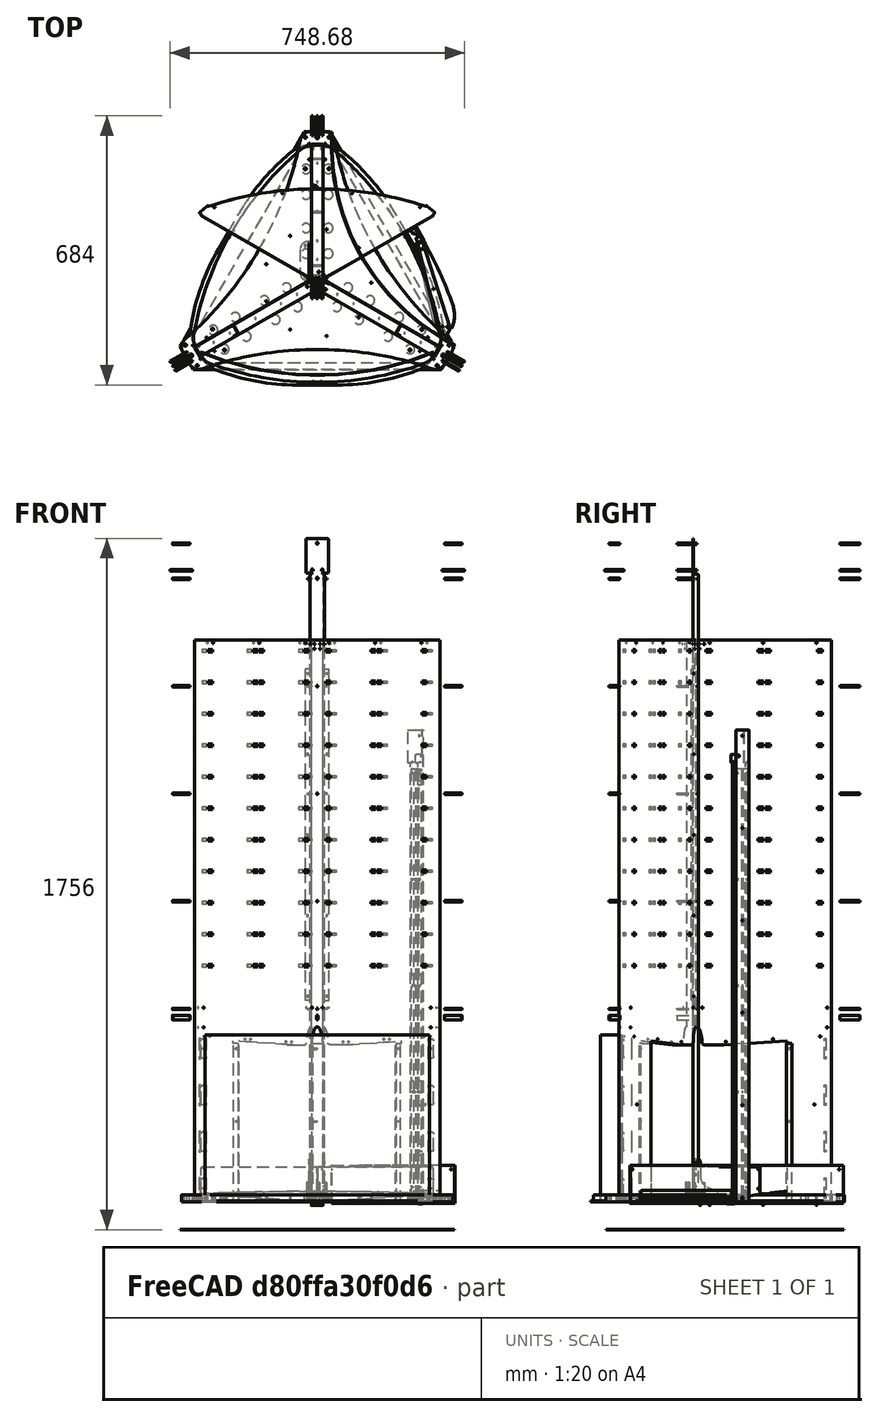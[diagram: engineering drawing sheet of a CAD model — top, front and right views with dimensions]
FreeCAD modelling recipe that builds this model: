
FCSTD DOCUMENT  (FreeCAD 0.22R36596 (Git))
Label: composit_full_size3_door
License: All rights reserved
LicenseURL: http://en.wikipedia.org/wiki/All_rights_reserved
objects: Sketcher::SketchObject×217, Part::FeaturePython×205, PartDesign::SubShapeBinder×115, Part::Compound×106, PartDesign::Pocket×95, PartDesign::Body×85, PartDesign::FeaturePython×60, PartDesign::Boolean×58, PartDesign::CoordinateSystem×49, App::Link×46, PartDesign::Pad×43, Part::Extrusion×41, Part::Mirroring×40, TechDraw::DrawViewDimension×37, App::DocumentObjectGroup×23, PartDesign::Mirrored×23, PartDesign::Hole×18, Part::Cylinder×16, PartDesign::Fillet×12, App::Part×11, +22 more types
note: 1421 computed .brp shape members not serialized (recipe doc carries the construction recipe); baked Part::Feature solids carry a one-line shape summary decoded from their .brp
EXTERNAL_REF file=basin_big.FCStd obj=Spreadsheet
EXTERNAL_REF file=composit-properties.FCStd obj=Spreadsheet
EXTERNAL_REF file=module.FCStd obj=Spreadsheet
EXTERNAL_REF file=module.FCStd obj=Sketch
EXTERNAL_REF file=dropper.FCStd obj=Sketch007
EXTERNAL_REF file=dropper.FCStd obj=Sketch008
EXTERNAL_REF file=dropper.FCStd obj=Connect
EXTERNAL_REF file=hub2108.FCStd obj=Body
EXTERNAL_REF file=U-fix.FCStd obj=Body
EXTERNAL_REF file=ULY-P91-20W.FCStd obj=Sketch001
EXTERNAL_REF file=socket_fixture.FCStd obj=Sketch003
EXTERNAL_REF file=UET-VAS-060A20_12V_IP20.FCStd obj=Sketch001
EXTERNAL_REF file=module.FCStd obj=Body
EXTERNAL_REF file=ULY-P91-20W.FCStd obj=Body
EXTERNAL_REF file=hub2108.FCStd obj=Sketch
EXTERNAL_REF file=hub2108.FCStd obj=Sketch001
EXTERNAL_REF file=U-fix.FCStd obj=Sketch002
EXTERNAL_REF file=hub2108.FCStd obj=Sketch002
EXTERNAL_REF file=hub2108.FCStd obj=Sketch003
EXTERNAL_REF file=ULZ-P02-14W.FCStd obj=Sketch
EXTERNAL_REF file=composit_full_size3_composit_cut.FCStd obj=Link026

FEATURE [Sketcher::SketchObject] Sketch
  FullyConstrained = true
  expr: Constraints[5] = <<Properties>>.endface_width
  expr: Constraints[9] = Spreadsheet.total_length
  sketch-geometry (4):
    g0: LineSegment StartX=-2.7195e-12 StartY=2.3473e-12 StartZ=0 EndX=14.5 EndY=8.37158 EndZ=0
    g1: LineSegment StartX=14.5 StartY=8.37158 StartZ=0 EndX=14.5 EndY=351.872 EndZ=0
    g2: GeomPoint X=-14.5 Y=351.872 Z=0
    g3: LineSegment StartX=14.5 StartY=351.872 StartZ=0 EndX=0 EndY=351.872 EndZ=0
  constraints (14):
    c: Coincident(g-1,g0)
    c: Coincident(g0,g1)
    c: Vertical(g1)
    c: Angle(g0) = 0.523599
    c: Symmetric(g2,g1,g-2)
    c: DistanceX(g2,g1) = 29
    c: Coincident(g3,g1)
    c: PointOnObject(g3,g-2)
    c: Horizontal(g3)
    c: DistanceY(g3) = 351.872
    c: Distance(g0,g1) = 352.17  'max_r'
    c: DistanceX(g1) = 14.5
    c: DistanceY(g1) = 8.37158
    c: Distance(g0) = 16.7432  'connection_offset'
FEATURE [Spreadsheet::Sheet] Spreadsheet  label="Properties"
  cells = B2(total_length)==22.5 mm + module#<<Properties>>.module_width + plane_middle; C2(endface_width)==29 mm; D2(rivet_d)==3.4 mm; E2(total_height)==modules_span + basin_big#<<Properties>>.height + 76 mm; F2(number_of_modules)=11; G2(module_distance_x)==2 mm; H2(modules_span)==<<module>>#<<Properties>>.module_fixture_distance_y * (number_of_modules - 1) + <<module>>#<<Properties>>.module_height; I2(top_offset)==27 mm; J2(plane_middle)==module#<<Properties>>.module_width + 25 mm + petal_offset; K2(inner_width)==endface_width - composit_properties#<<Properties>>.thickness * 2; L2(dropper_distance)==65 mm; M2(plane_width)==22.5 mm + module#<<Properties>>.module_width + plane_middle - petal_offset; N2(petal_offset)==endface_width / 2 / tan(60)
FEATURE [Part::Mirroring] Part__Mirroring  label="Sketch (Mirror #1)"
  Base = (0,0,0)
  Normal = (1,0,0)
  Source = -> Sketch
FEATURE [Part::Compound] Compound
  Links = -> [Part__Mirroring,Sketch]
FEATURE [Sketcher::SketchObject] Sketch001  label="part_main_sketch"
  ExternalGeometry = -> [Sketch]
  FullyConstrained = true
  expr: Constraints[7] = composit_properties#<<Properties>>.thickness
  sketch-geometry (3):
    g0: LineSegment StartX=0 StartY=351.872 StartZ=0 EndX=14.5 EndY=351.872 EndZ=0
    g1: LineSegment StartX=14.5 StartY=351.872 StartZ=0 EndX=14.5 EndY=4.90748 EndZ=0
    g2: LineSegment StartX=14.5 StartY=4.90748 StartZ=0 EndX=29.6554 EndY=-3.84252 EndZ=0
  constraints (9):
    c: PointOnObject(g0,g-2)
    c: Coincident(g0,g-3)
    c: Horizontal(g0)
    c: Coincident(g0,g1)
    c: PointOnObject(g1,g-3)
    c: Coincident(g1,g2)
    c: Angle(g2) = -0.523599
    c: Distance(g-3,g2) = 3
    c: Distance(g2) = 17.5
FEATURE [Part::Mirroring] Part__Mirroring001  label="part_main_sketch (Mirror #2)"
  Base = (0,0,0)
  Normal = (1,0,0)
  Source = -> Sketch001
FEATURE [Part::Compound] Compound001  label="part1_base"
  Links = -> [Part__Mirroring001,Sketch001]
FEATURE [Part::FeaturePython] Array001  label="2part_base"  # Draft array (typed FeaturePython)
  AlwaysSyncPlacement = false
  Angle = 240
  ArrayType = 1
  Axis = (0,0,1)
  Base = -> Compound
  Center = (0,0,0)
  Count = 2
  ExpandArray = false
  Fuse = false
  IntervalAxis = (0,0,0)
  IntervalX = (50,0,0)
  IntervalY = (0,50,0)
  IntervalZ = (0,0,50)
  NumberCircles = 3
  NumberPolar = 2
  NumberX = 2
  NumberY = 2
  NumberZ = 1
  PlacementList = 2 placements: [(0,0,0),(0,0,0)]
  RadialDistance = 50
  ScaleList = (2) [(1,1,1),(1,1,1)]
  Symmetry = 1
  TangentialDistance = 25
FEATURE [PartDesign::SubShapeBinder] Binder
  BindCopyOnChange = 0
  BindMode = 0
  ClaimChildren = true
  Context = -> Body [Binder.]
  Fuse = false
  MakeFace = true
  OffsetFill = false
  OffsetIntersection = false
  OffsetJoinType = 0
  OffsetOpenResult = false
  PartialLoad = false
  Relative = true
  Support = -> [Compound001]
  _Version = 2
  expr: Support = <<part1_base>>._self
FEATURE [PartDesign::SubShapeBinder] Binder001
  BindCopyOnChange = 0
  BindMode = 0
  ClaimChildren = true
  Context = -> Body001 [Binder001.]
  Fuse = false
  MakeFace = true
  OffsetFill = false
  OffsetIntersection = false
  OffsetJoinType = 0
  OffsetOpenResult = false
  PartialLoad = false
  Placement = pos=(0,0,0) rot=(0,0,1;4.18879rad)
  Relative = false
  Support = -> [Array001]
  _Version = 2
  expr: Support = <<2part_base>>._self
FEATURE [PartDesign::FeaturePython] BaseBend  # WARN: FeaturePython — macro-defined, semantics opaque (R4)
  BendSide = 1
  BendSketch = -> Binder
  MidPlane = false
  Reverse = false
  Suppressed = false
  length = 1428
  radius = 0.1
  thickness = 0.3
  expr: length = <<Properties>>.total_height
  expr: radius = composit_properties#<<Properties>>.bend_r
  expr: thickness = composit_properties#<<Properties>>.al_thickness
FEATURE [PartDesign::FeaturePython] BaseBend001  # WARN: FeaturePython — macro-defined, semantics opaque (R4)
  BendSide = 0
  BendSketch = -> Binder001
  MidPlane = false
  Reverse = false
  Suppressed = false
  length = 1428
  radius = 0.1
  thickness = 0.3
  expr: length = <<Properties>>.total_height
  expr: radius = composit_properties#<<Properties>>.bend_r
  expr: thickness = composit_properties#<<Properties>>.al_thickness
FEATURE [App::Link] Link  label="module_holes"
  LinkedObject = -> <external module.FCStd>#Sketch
  expr: LinkedObject = module#<<module_holes>>._self
FEATURE [Part::FeaturePython] LinearArray  # WARN: FeaturePython — macro-defined, semantics opaque (R4)
  Alignment = 0
  CellStart = A1
  Count = 11
  Dir = (0,-1,0)
  DirIsDriven = true
  DistributionLaw = 0
  DrivenProperty = 1
  EndInclusive = true
  ExposePlacement = false
  GeneratorMode = 1
  MarkerShape = 1
  MarkerSize = 0
  NumElements = 11
  OrientMode = 0
  Point = (0,0,0)
  PointIsDriven = true
  Reverse = false
  SpanEnd = 800
  SpanStart = 0
  Step = 80
  Type = lattice2LinearArray.LinearArray
  VSGVersion = 1
  Values = 0.0 | 80.0 | 160.0 | 240.0 | 320.0 | 400.0 | 480.0 | 560.0 | 640.0 | 720.0 | 800.0
  ValuesSource = 2
  isLattice = 1
  expr: Count = <<Properties>>.number_of_modules
  expr: SpanEnd = Step * (Count - 1)
  expr: Step = <<module>>#<<Properties>>.module_fixture_distance_y
FEATURE [Part::FeaturePython] LinearArray001  # WARN: FeaturePython — macro-defined, semantics opaque (R4)
  Alignment = 0
  CellStart = A1
  Count = 2
  Dir = (1,0,0)
  DirIsDriven = true
  DistributionLaw = 0
  DrivenProperty = 1
  EndInclusive = true
  ExposePlacement = false
  GeneratorMode = 1
  MarkerShape = 1
  MarkerSize = 0
  NumElements = 2
  OrientMode = 1
  Placement = pos=(-75,0,0) rot=(0,0,1;0rad)
  Point = (0,0,0)
  PointIsDriven = true
  Reverse = false
  SpanEnd = 150
  SpanStart = 0
  Step = 150
  Type = lattice2LinearArray.LinearArray
  VSGVersion = 1
  Values = 0.0 | 150.0
  ValuesSource = 2
  isLattice = 1
  expr: .Placement.Base.x = -SpanEnd / 2
  expr: SpanEnd = Step * (Count - 1)
  expr: Step = <<module>>#<<Properties>>.module_width + <<Properties>>.module_distance_x
FEATURE [Part::FeaturePython] Populate  label="Populate LinearArray with LinearArray001"  # WARN: FeaturePython — macro-defined, semantics opaque (R4)
  Copying = 0
  ExposePlacement = false
  MarkerShape = 1
  MarkerSize = 0
  NumElements = 22
  Object = -> LinearArray001
  OutputCompounding = 0
  PlacementsTo = -> LinearArray
  Referencing = 0
  Type = lattice2PopulateCopies.LatticePopulateCopies
  isLattice = 1
FEATURE [Part::FeaturePython] Populate001  label="Populate Populate LinearArray with LinearArray001 with module_holes"  # WARN: FeaturePython — macro-defined, semantics opaque (R4)
  Copying = 0
  ExposePlacement = false
  MarkerShape = 1
  MarkerSize = 0
  NumElements = 0
  Object = -> Link
  OutputCompounding = 1
  PlacementsTo = -> Populate
  Referencing = 0
  Type = lattice2PopulateCopies.LatticePopulateCopies
  isLattice = 0
FEATURE [Part::Extrusion] Extrude  label="modules_holes"
  Base = -> Populate001
  Dir = (0,0,1)
  DirMode = 2
  FaceMakerClass = Part::FaceMakerBullseye
  LengthFwd = 31
  LengthRev = 0
  Placement = pos=(0,181.372,1401) rot=(0.57735,0.57735,0.57735;2.0944rad)
  Solid = true
  Symmetric = true
  expr: .Placement.Base.y = <<Properties>>.plane_middle
  expr: .Placement.Base.z = <<Properties>>.total_height - <<Properties>>.top_offset
  expr: LengthFwd = <<Properties>>.endface_width + 2 mm
FEATURE [Sketcher::SketchObject] Sketch003  label="basin_cut_sketch"
  ExternalGeometry = -> [Sketch]
  FullyConstrained = true
  Placement = pos=(0,0,0) rot=(0.57735,0.57735,0.57735;2.0944rad)
  expr: Constraints[27] = <<sink_bend_line>>.FaceAngle
  sketch-geometry (12):
    g0: LineSegment StartX=0 StartY=0 StartZ=0 EndX=238.372 EndY=0 EndZ=0
    g1: LineSegment StartX=238.372 StartY=0 StartZ=0 EndX=238.372 EndY=409.023 EndZ=0
    g2: LineSegment StartX=79.3716 StartY=400 StartZ=0 EndX=28.4155 EndY=400 EndZ=0
    g3: ArcOfCircle CenterX=28.4155 CenterY=405 CenterZ=0 NormalX=0 NormalY=0 NormalZ=1 AngleXU=0 Radius=5 StartAngle=3.17548 EndAngle=4.71239
    g4: ArcOfEllipse CenterX=9.37158 CenterY=400 CenterZ=0 NormalX=0 NormalY=0 NormalZ=1 MajorRadius=45 MinorRadius=14.1284 AngleXU=-1.5708 StartAngle=1.67835 EndAngle=3.14159
    g5: LineSegment StartX=9.37158 StartY=355 StartZ=0 EndX=9.37158 EndY=445 EndZ=0
    g6: LineSegment StartX=23.5 StartY=400 StartZ=0 EndX=-4.75684 EndY=400 EndZ=0
    g7: GeomPoint X=9.37158 Y=357.275 Z=0
    g8: GeomPoint X=9.37158 Y=442.725 Z=0
    g9: LineSegment StartX=0 StartY=0 StartZ=0 EndX=0 EndY=445 EndZ=0
    g10: LineSegment StartX=0 StartY=445 StartZ=0 EndX=9.37158 EndY=445 EndZ=0
    g11: LineSegment StartX=79.3716 StartY=400 StartZ=0 EndX=238.372 EndY=409.023 EndZ=0
  constraints (25):
    c: Coincident(g-1,g0)
    c: Horizontal(g0)
    c: Coincident(g0,g1)
    c: Vertical(g1)
    c: Horizontal(g2)
    c: Tangent(g3,g2) = 1.5708
    c: InternalAlignment(g5-g8 -> g4) x4
    c: Horizontal(g6)
    c: Tangent(g4,g3) = 1.5708
    c: Coincident(g9,g0)
    c: Coincident(g9,g10)
    c: Vertical(g9)
    c: Horizontal(g10)
    c: Tangent(g10,g4) = 1.5708
    c: DistanceX(g-3,g0) = 230
    c: DistanceY(g2) = 400
    c: DistanceY(g9) = 445
    c: DistanceX(g-3,g4) = 1
    c: Radius(g3) = 5
    c: DistanceX(g6) = 23.5
    c: PointOnObject(g4,g2)
    c: DistanceX(g-3,g2) = 71
    c: Coincident(g11,g2)
    c: Coincident(g11,g1)
    c: Angle(g11) = 0.0566865
FEATURE [Part::Extrusion] Extrude001  label="basin_cut"
  Base = -> Sketch003
  Dir = (1,0,0)
  DirMode = 2
  FaceMakerClass = Part::FaceMakerBullseye
  LengthFwd = 30
  LengthRev = 0
  Solid = true
  Symmetric = true
FEATURE [Sketcher::SketchObject] Sketch004  label="leg_amplifier_base_sketch"
  ExternalGeometry = -> [Sketch003]
  FullyConstrained = true
  expr: Constraints[5] = <<Properties>>.endface_width / 2
  expr: Constraints[6] = composit_properties#<<Properties>>.bend_r + composit_properties#<<Properties>>.al_thickness
  expr: Constraints[7] = <<Properties>>.endface_width - composit_properties#<<Properties>>.thickness
  sketch-geometry (3):
    g0: LineSegment StartX=-11.5 StartY=-0.4 StartZ=0 EndX=14.5 EndY=-0.4 EndZ=0
    g1: LineSegment StartX=-11.5 StartY=-0.4 StartZ=0 EndX=-11.5 EndY=13 EndZ=0
    g2: LineSegment StartX=14.5 StartY=-0.4 StartZ=0 EndX=14.5 EndY=13 EndZ=0
  constraints (10):
    c: Horizontal(g0)
    c: Coincident(g1,g0)
    c: Vertical(g1)
    c: Coincident(g2,g0)
    c: Vertical(g2)
    c: DistanceX(g0) = 14.5
    c: DistanceY(g0,g-3) = 0.4
    c: DistanceX(g0,g0) = 26
    c: Horizontal(g1,g2)
    c: DistanceY(g-3,g2) = 13
FEATURE [Part::Mirroring] Part__Mirroring002  label="Sketch004 (Mirror #3)"
  Base = (0,0,0)
  Normal = (1,0,0)
  Source = -> Sketch004
FEATURE [Spreadsheet::Sheet] Spreadsheet001  label="Properties001"
  cells = B2(plane_width)==27.5 mm + module#<<Properties>>.module_width * 2 + 20 mm; C2(endface_width)==29 mm; D2(rivet_d)==3.4 mm; E2(total_height)==modules_span + basin_big#<<Properties>>.height; F2(number_of_modules)=11; G2(module_distance_x)==2 mm; H2(modules_span)==<<module>>#<<Properties>>.module_fixture_distance_y * number_of_modules + <<module>>#<<Properties>>.module_height; I2(top_offset)==30.5 mm; J2(plane_middle)==module#<<Properties>>.module_width + 25 mm; K2(inner_width)==endface_width - composit_properties#<<Properties>>.thickness * 2; L2(dropper_distance)==65 mm
FEATURE [Sketcher::SketchObject] Sketch005
  FullyConstrained = true
  expr: Constraints[5] = <<Properties001>>.endface_width
  expr: Constraints[6] = <<Properties001>>.plane_width
  sketch-geometry (4):
    g0: LineSegment StartX=5.67e-14 StartY=-9.82e-14 StartZ=0 EndX=14.5 EndY=8.37158 EndZ=0
    g1: LineSegment StartX=14.5 StartY=8.37158 StartZ=0 EndX=14.5 EndY=351.872 EndZ=0
    g2: GeomPoint X=-14.5 Y=351.872 Z=0
    g3: LineSegment StartX=14.5 StartY=351.872 StartZ=0 EndX=0 EndY=351.872 EndZ=0
  constraints (10):
    c: Coincident(g-1,g0)
    c: Coincident(g0,g1)
    c: Vertical(g1)
    c: Angle(g0) = 0.523599
    c: Symmetric(g2,g1,g-2)
    c: DistanceX(g2,g1) = 29
    c: DistanceY(g1,g1) = 343.5
    c: Coincident(g3,g1)
    c: PointOnObject(g3,g-2)
    c: Horizontal(g3)
FEATURE [Sketcher::SketchObject] Sketch006
  ExternalGeometry = -> [Sketch005]
  FullyConstrained = true
  Placement = pos=(0,0,0) rot=(0.57735,0.57735,0.57735;2.0944rad)
  sketch-geometry (12):
    g0: LineSegment StartX=0 StartY=0 StartZ=0 EndX=238.372 EndY=0 EndZ=0
    g1: LineSegment StartX=238.372 StartY=0 StartZ=0 EndX=238.372 EndY=410 EndZ=0
    g2: LineSegment StartX=238.372 StartY=410 StartZ=0 EndX=79.3716 EndY=400 EndZ=0
    g3: LineSegment StartX=79.3716 StartY=400 StartZ=0 EndX=19.9656 EndY=400 EndZ=0
    g4: ArcOfCircle CenterX=19.9656 CenterY=405 CenterZ=0 NormalX=0 NormalY=0 NormalZ=1 AngleXU=0 Radius=5 StartAngle=3.15538 EndAngle=4.71239
    g5: ArcOfEllipse CenterX=9.37158 CenterY=400 CenterZ=0 NormalX=0 NormalY=0 NormalZ=1 MajorRadius=45 MinorRadius=5.62842 AngleXU=-1.5708 StartAngle=1.6806 EndAngle=3.14159
    g6: LineSegment StartX=9.37158 StartY=355 StartZ=0 EndX=9.37158 EndY=445 EndZ=0
    g7: LineSegment StartX=15 StartY=400 StartZ=0 EndX=3.74316 EndY=400 EndZ=0
    g8: GeomPoint X=9.37158 Y=355.353 Z=0
    g9: GeomPoint X=9.37158 Y=444.647 Z=0
    g10: LineSegment StartX=0 StartY=0 StartZ=0 EndX=0 EndY=445 EndZ=0
    g11: LineSegment StartX=0 StartY=445 StartZ=0 EndX=9.37158 EndY=445 EndZ=0
  constraints (25):
    c: Coincident(g-1,g0)
    c: Horizontal(g0)
    c: Coincident(g0,g1)
    c: Vertical(g1)
    c: Coincident(g1,g2)
    c: Coincident(g2,g3)
    c: Horizontal(g3)
    c: Tangent(g4,g3) = 1.5708
    c: InternalAlignment(g6-g9 -> g5) x4
    c: Horizontal(g7)
    c: Tangent(g5,g4) = 1.5708
    c: Coincident(g10,g0)
    c: Coincident(g10,g11)
    c: Vertical(g10)
    c: Horizontal(g11)
    c: Tangent(g11,g5) = 1.5708
    c: DistanceX(g-3,g0) = 230
    c: DistanceY(g2) = 400
    c: DistanceY(g10) = 445
    c: DistanceX(g-3,g5) = 1
    c: Radius(g4) = 5
    c: DistanceX(g7) = 15
    c: PointOnObject(g5,g3)
    c: DistanceY(g1) = 410
    c: DistanceX(g-3,g2) = 71
FEATURE [Sketcher::SketchObject] Sketch007
  ExternalGeometry = -> [Sketch006]
  FullyConstrained = true
  expr: Constraints[5] = <<Properties001>>.endface_width / 2
  expr: Constraints[6] = composit_properties#<<Properties>>.bend_r + composit_properties#<<Properties>>.al_thickness
  expr: Constraints[7] = <<Properties001>>.endface_width - composit_properties#<<Properties>>.thickness
  sketch-geometry (3):
    g0: LineSegment StartX=-11.5 StartY=237.972 StartZ=0 EndX=14.5 EndY=237.972 EndZ=0
    g1: LineSegment StartX=-11.5 StartY=237.972 StartZ=0 EndX=-11.5 EndY=258.372 EndZ=0
    g2: LineSegment StartX=14.5 StartY=237.972 StartZ=0 EndX=14.5 EndY=258.372 EndZ=0
  constraints (10):
    c: Horizontal(g0)
    c: Coincident(g1,g0)
    c: Vertical(g1)
    c: Coincident(g2,g0)
    c: Vertical(g2)
    c: DistanceX(g0) = 14.5
    c: DistanceY(g0,g-3) = 0.4
    c: DistanceX(g0,g0) = 26
    c: Horizontal(g1,g2)
    c: DistanceY(g-3,g2) = 20
FEATURE [Part::FeaturePython] BaseBend003  label="BaseBend002_material_0.30ansi002"  # WARN: FeaturePython — macro-defined, semantics opaque (R4)
  BendSide = 0
  BendSketch = -> Part__Mirroring002
  MidPlane = false
  Reverse = false
  length = 403.5
  radius = 0.1
  thickness = 0.3
  expr: length = <<leg_amplifier>>.length
  expr: radius = composit_properties#<<Properties>>.bend_r
  expr: thickness = composit_properties#<<Properties>>.al_thickness
FEATURE [App::LinkGroup] CopyOnChangeGroup
  ElementList = -> [BaseBend003,Sketch007,Sketch006,Sketch005,Spreadsheet001]
  LinkMode = 1
FEATURE [App::Link] Link002  label="leg_amplifier_link"
  BendSketch = -> Part__Mirroring002
  LinkCopyOnChange = 2
  LinkCopyOnChangeGroup = -> CopyOnChangeGroup
  LinkCopyOnChangeSource = -> BaseBend002
  LinkCopyOnChangeTouched = true
  LinkPlacement = pos=(206.436,-119.186,0) rot=(0,0,1;4.18879rad)
  LinkedObject = -> BaseBend003
  Placement = pos=(206.436,-119.186,0) rot=(0,0,1;4.18879rad)
  expr: .LinkPlacement.Base.x = (<<Properties>>.petal_offset + 230 mm) * cos(-30)
  expr: .LinkPlacement.Base.y = (<<Properties>>.petal_offset + 230 mm) * sin(-30)
FEATURE [Part::Compound] Compound008
  Links = -> [Sketch004]
FEATURE [Part::FeaturePython] BaseBend002  label="leg_amplifier"  # WARN: FeaturePython — macro-defined, semantics opaque (R4)
  BendSide = 1
  BendSketch = -> Compound008
  MidPlane = false
  Placement = pos=(0,238.372,0) rot=(0,0,1;0rad)
  Reverse = false
  length = 403.5
  radius = 0.1
  thickness = 0.3
  expr: .Placement.Base.y = <<Properties>>.petal_offset + 230 mm
  expr: radius = composit_properties#<<Properties>>.bend_r
  expr: thickness = composit_properties#<<Properties>>.al_thickness
FEATURE [Part::Compound] Compound006  label="mirror_compound"
  Links = -> [BaseBend002]
  Placement = pos=(0,0,0) rot=(0,0,1;2.0944rad)
FEATURE [Part::Compound] Compound007  label="part2_fuse1"
  Links = -> [Link002,Compound006]
  expr: Links = list(<<leg_amplifier_link>>._self; <<mirror_compound>>._self)
FEATURE [App::DocumentObjectGroup] Group006  label="composit_cut"
FEATURE [App::DocumentObjectGroup] Group007  label="PP_cut"
FEATURE [App::DocumentObjectGroup] Group008  label="plywood_cut"
FEATURE [App::DocumentObjectGroup] Group002  label="cut"
  Group = -> [Group006,Group007,Group008]
FEATURE [Sketcher::SketchObject] Sketch008  label="pillar_base_sketch"
  FullyConstrained = true
  sketch-geometry (5):
    g0: LineSegment StartX=-18.3 StartY=19 StartZ=0 EndX=-18.3 EndY=-4.62e-14 EndZ=0
    g1: LineSegment StartX=-18.3 StartY=-4.62e-14 StartZ=0 EndX=18.3 EndY=-4.62e-14 EndZ=0
    g2: LineSegment StartX=18.3 StartY=-4.62e-14 StartZ=0 EndX=18.3 EndY=19 EndZ=0
    g3: LineSegment StartX=18.3 StartY=19 StartZ=0 EndX=-18.3 EndY=19 EndZ=0
    g4: GeomPoint X=8.6e-15 Y=9.5 Z=0
  constraints (13):
    c: Coincident(g0,g1)
    c: Coincident(g1,g2)
    c: Coincident(g2,g3)
    c: Coincident(g3,g0)
    c: Horizontal(g1)
    c: Horizontal(g3)
    c: Vertical(g0)
    c: Vertical(g2)
    c: Symmetric(g1,g0,g4)
    c: PointOnObject(g4,g-2)
    c: PointOnObject(g1,g-1)
    c: DistanceX(g1,g1) = 36.6  'width'
    c: DistanceY(g2,g2) = 19  'length'
FEATURE [PartDesign::SubShapeBinder] Binder002
  BindCopyOnChange = 0
  BindMode = 0
  ClaimChildren = true
  Fuse = false
  MakeFace = true
  OffsetFill = false
  OffsetIntersection = false
  OffsetJoinType = 0
  OffsetOpenResult = false
  PartialLoad = false
  Relative = false
  Support = -> [Sketch008]
  _Version = 2
FEATURE [PartDesign::FeaturePython] BaseBend004  label="pillar_BaseBend"  # WARN: FeaturePython — macro-defined, semantics opaque (R4)
  BendSide = 1
  BendSketch = -> Binder002
  MidPlane = false
  Reverse = false
  Suppressed = false
  length = 1594
  radius = 2
  thickness = 2
FEATURE [Sketcher::SketchObject] Sketch009
  AttachmentOffset = pos=(0,1594,0) rot=(0,0,1;0rad)
  AttachmentSupport = -> [XZ_Plane014]
  FullyConstrained = true
  MapMode = 5
  Placement = pos=(0,3.539e-13,1594) rot=(1,0,0;1.5708rad)
  expr: .AttachmentOffset.Base.y = BaseBend004.length
  expr: Constraints[15] = <<pillar_base_sketch>>.Constraints.width - (<<pillar_BaseBend>>.thickness + <<pillar_BaseBend>>.radius) * 2
  sketch-geometry (16):
    g0: LineSegment StartX=-14.3 StartY=0 StartZ=0 EndX=14.3 EndY=0 EndZ=0
    g1: LineSegment StartX=14.3 StartY=0 StartZ=0 EndX=14.3 EndY=2 EndZ=0
    g2: LineSegment StartX=14.3 StartY=2 StartZ=0 EndX=34.5 EndY=2 EndZ=0
    g3: LineSegment StartX=37.5 StartY=5 StartZ=0 EndX=37.5 EndY=87 EndZ=0
    g4: LineSegment StartX=34.5 StartY=90 StartZ=0 EndX=-34.5 EndY=90 EndZ=0
    g5: LineSegment StartX=-37.5 StartY=87 StartZ=0 EndX=-37.5 EndY=5 EndZ=0
    g6: LineSegment StartX=-34.5 StartY=2 StartZ=0 EndX=-14.3 EndY=2 EndZ=0
    g7: LineSegment StartX=-14.3 StartY=2 StartZ=0 EndX=-14.3 EndY=0 EndZ=0
    g8: ArcOfCircle CenterX=34.5 CenterY=5 CenterZ=0 NormalX=0 NormalY=0 NormalZ=1 AngleXU=0 Radius=3 StartAngle=4.71239 EndAngle=6.28319
    g9: GeomPoint X=37.5 Y=2 Z=0
    g10: ArcOfCircle CenterX=34.5 CenterY=87 CenterZ=0 NormalX=0 NormalY=0 NormalZ=1 AngleXU=0 Radius=3 StartAngle=1.02861e-11 EndAngle=1.5708
    g11: GeomPoint X=37.5 Y=90 Z=0
    g12: ArcOfCircle CenterX=-34.5 CenterY=87 CenterZ=0 NormalX=0 NormalY=0 NormalZ=1 AngleXU=0 Radius=3 StartAngle=1.5708 EndAngle=3.14159
    g13: GeomPoint X=-37.5 Y=90 Z=0
    g14: ArcOfCircle CenterX=-34.5 CenterY=5 CenterZ=0 NormalX=0 NormalY=0 NormalZ=1 AngleXU=0 Radius=3 StartAngle=3.14159 EndAngle=4.71239
    g15: GeomPoint X=-37.5 Y=2 Z=0
  constraints (38):
    c: PointOnObject(g0,g-1)
    c: Coincident(g0,g1)
    c: Vertical(g1)
    c: Coincident(g1,g2)
    c: Horizontal(g2)
    c: Vertical(g3)
    c: Vertical(g5)
    c: Horizontal(g6)
    c: Coincident(g6,g7)
    c: Vertical(g7)
    c: Coincident(g0,g7)
    c: Horizontal(g0)
    c: Symmetric(g6,g1,g-2)
    c: Symmetric(g11,g13,g-2)
    c: DistanceY(g1,g1) = 2
    c: DistanceX(g0,g0) = 28.6
    c: PointOnObject(g9,g2)
    c: PointOnObject(g9,g3)
    c: Tangent(g2,g8) = -1.5708
    c: Tangent(g3,g8) = -1.5708
    c: PointOnObject(g11,g3)
    c: PointOnObject(g11,g4)
    c: Tangent(g3,g10) = -1.5708
    c: Tangent(g4,g10) = -1.5708
    c: PointOnObject(g13,g4)
    c: PointOnObject(g13,g5)
    c: Tangent(g4,g12) = -1.5708
    c: Tangent(g5,g12) = -1.5708
    c: PointOnObject(g15,g5)
    c: PointOnObject(g15,g6)
    c: Tangent(g5,g14) = -1.5708
    c: Tangent(g6,g14) = -1.5708
    c: Equal(g14,g8)
    c: Equal(g14,g10)
    c: Equal(g14,g12)
    c: Radius(g14) = 3
    c: DistanceX(g13,g11) = 75
    c: DistanceY(g9,g11) = 88
FEATURE [Sketcher::SketchObject] Sketch010  label="pillar_bottom_BaseSketch"
  AttachmentSupport = -> [YZ_Plane015]
  FullyConstrained = true
  MapMode = 5
  Placement = pos=(0,0,0) rot=(0.57735,0.57735,0.57735;2.0944rad)
  sketch-geometry (2):
    g0: LineSegment StartX=-25 StartY=0 StartZ=0 EndX=0 EndY=0 EndZ=0
    g1: LineSegment StartX=0 StartY=0 StartZ=0 EndX=0 EndY=110 EndZ=0
  constraints (6):
    c: PointOnObject(g0,g-1)
    c: Coincident(g0,g-1)
    c: Coincident(g0,g1)
    c: PointOnObject(g1,g-2)
    c: DistanceX(g0,g0) = 25  'leg_length'
    c: DistanceY(g1) = 110  'height'
FEATURE [PartDesign::FeaturePython] BaseBend005  label="pillar_bottom_BaseBend"  # WARN: FeaturePython — macro-defined, semantics opaque (R4)
  BendSide = 0
  BendSketch = -> Sketch010
  MidPlane = true
  Reverse = true
  Suppressed = false
  length = 101
  radius = 2
  thickness = 2
FEATURE [Sketcher::SketchObject] Sketch011  label="pillar_bottom_cut_vert"
  AttachmentSupport = -> [XZ_Plane015]
  FullyConstrained = true
  MapMode = 5
  Placement = pos=(0,0,0) rot=(1,0,0;1.5708rad)
  expr: Constraints[15] = <<pillar_bottom_BaseBend>>.length
  expr: Constraints[16] = <<pillar_bottom_BaseBend>>.radius + <<pillar_bottom_BaseBend>>.thickness
  expr: Constraints[27] = <<pillar_base_sketch>>.Constraints.length - 4 mm
  sketch-geometry (15):
    g0: LineSegment StartX=-50.5 StartY=0 StartZ=0 EndX=-50.5 EndY=75 EndZ=0
    g1: LineSegment StartX=-45.5 StartY=80 StartZ=0 EndX=-40.5 EndY=80 EndZ=0
    g2: LineSegment StartX=50.5 StartY=4 StartZ=0 EndX=50.5 EndY=0 EndZ=0
    g3: LineSegment StartX=50.5 StartY=0 StartZ=0 EndX=-50.5 EndY=0 EndZ=0
    g4: ArcOfCircle CenterX=-45.5 CenterY=75 CenterZ=0 NormalX=0 NormalY=0 NormalZ=1 AngleXU=0 Radius=5 StartAngle=1.5708 EndAngle=3.14159
    g5: GeomPoint X=-50.5 Y=80 Z=0
    g6: ArcOfCircle CenterX=-40.5 CenterY=75 CenterZ=0 NormalX=0 NormalY=0 NormalZ=1 AngleXU=0 Radius=5 StartAngle=0 EndAngle=1.5708
    g7: GeomPoint X=-35.5 Y=80 Z=0
    g8: ArcOfCircle CenterX=45.5 CenterY=4 CenterZ=0 NormalX=0 NormalY=0 NormalZ=1 AngleXU=0 Radius=5 StartAngle=0 EndAngle=1.13485
    g9: GeomPoint X=50.5 Y=7.18672 Z=0
    g10: LineSegment StartX=-35.5 StartY=75 StartZ=0 EndX=-35.5 EndY=64.709 EndZ=0
    g11: LineSegment StartX=-19.6724 StartY=39.8753 StartZ=0 EndX=47.6113 EndY=8.53236 EndZ=0
    g12: ArcOfCircle CenterX=-8.10401 CenterY=64.709 CenterZ=0 NormalX=0 NormalY=0 NormalZ=1 AngleXU=0 Radius=27.396 StartAngle=3.14159 EndAngle=4.27645
    g13: GeomPoint X=-19.6724 Y=39.8753 Z=0
    g14: GeomPoint X=-13.5 Y=37 Z=0
  constraints (34):
    c: PointOnObject(g0,g-1)
    c: Vertical(g0)
    c: Horizontal(g1)
    c: Vertical(g2)
    c: Coincident(g2,g3)
    c: Coincident(g3,g0)
    c: PointOnObject(g5,g0)
    c: PointOnObject(g5,g1)
    c: Tangent(g0,g4) = 1.5708
    c: Tangent(g1,g4) = 1.5708
    c: PointOnObject(g7,g1)
    c: Tangent(g1,g6) = 1.5708
    c: PointOnObject(g9,g2)
    c: Tangent(g2,g8) = 1.5708
    c: Symmetric(g0,g2,g-2)
    c: DistanceX(g3,g3) = 101
    c: DistanceY(g2) = 4
    c: DistanceY(g5) = 80  'height'
    c: Radius(g4) = 5
    c: Radius(g8) = 5
    c: Equal(g4,g6)
    c: PointOnObject(g7,g10)
    c: PointOnObject(g9,g11)
    c: Vertical(g10)
    c: Tangent(g10,g6) = 1.5708
    c: Tangent(g12,g10) = -1.5708
    c: Tangent(g12,g11) = -1.5708
    c: DistanceX(g5,g7) = 15
    c: Tangent(g11,g8) = 1.5708
    c: Coincident(g11,g13)
    c: PointOnObject(g14,g11)
    c: DistanceY(g14) = 37
    c: DistanceX(g0,g14) = 37
    c: DistanceX(g11) = -19.6724
FEATURE [Sketcher::SketchObject] Sketch012
  AttachmentSupport = -> [XY_Plane015]
  FullyConstrained = true
  MapMode = 5
  expr: Constraints[18] = <<pillar_bottom_BaseSketch>>.Constraints.leg_length
  expr: Constraints[20] = <<pillar_bottom_BaseBend>>.radius + <<pillar_bottom_BaseBend>>.thickness
  expr: Constraints[9] = <<pillar_bottom_BaseBend>>.length
  sketch-geometry (9):
    g0: LineSegment StartX=-50.5 StartY=-4 StartZ=0 EndX=-50.5 EndY=0 EndZ=0
    g1: LineSegment StartX=-50.5 StartY=0 StartZ=0 EndX=50.5 EndY=0 EndZ=0
    g2: LineSegment StartX=50.5 StartY=0 StartZ=0 EndX=50.5 EndY=-4 EndZ=0
    g3: LineSegment StartX=29.5 StartY=-25 StartZ=0 EndX=-29.5 EndY=-25 EndZ=0
    g4: GeomPoint X=0 Y=-12.5 Z=0
    g5: ArcOfCircle CenterX=29.5 CenterY=-4 CenterZ=0 NormalX=0 NormalY=0 NormalZ=1 AngleXU=0 Radius=21 StartAngle=4.71239 EndAngle=6.28319
    g6: GeomPoint X=50.5 Y=-25 Z=0
    g7: ArcOfCircle CenterX=-29.5 CenterY=-4 CenterZ=0 NormalX=0 NormalY=0 NormalZ=1 AngleXU=0 Radius=21 StartAngle=3.14159 EndAngle=4.71239
    g8: GeomPoint X=-50.5 Y=-25 Z=0
  constraints (21):
    c: Coincident(g0,g1)
    c: Coincident(g1,g2)
    c: Horizontal(g1)
    c: Horizontal(g3)
    c: Vertical(g0)
    c: Vertical(g2)
    c: Symmetric(g1,g8,g4)
    c: PointOnObject(g4,g-2)
    c: PointOnObject(g1,g-1)
    c: DistanceX(g1,g1) = 101
    c: PointOnObject(g6,g2)
    c: PointOnObject(g6,g3)
    c: Tangent(g2,g5) = 1.5708
    c: Tangent(g3,g5) = 1.5708
    c: PointOnObject(g8,g0)
    c: PointOnObject(g8,g3)
    c: Tangent(g0,g7) = 1.5708
    c: Tangent(g3,g7) = 1.5708
    c: DistanceY(g6,g-1) = 25
    c: Equal(g7,g5)
    c: DistanceY(g2,g-1) = 4
FEATURE [Part::FeaturePython] WireFilter  # WARN: FeaturePython — macro-defined, semantics opaque (R4)
  AttacherType = Attacher::AttachEngine3D
  ClaimChildren = true
  ColorKeyCount = 8
  Colorize = true
  FaceMaker = 5
  FixNormal = false
  FollowSource = true
  InvertedFaceScale = 20
  MaxWires = 25
  Normal = (0,1,-2e-16)
  OffsetFill = false
  OffsetIntersection = false
  OffsetJoin = 0
  OffsetOpenResult = false
  Scale = (1,1,1)
  SelectEdges = false
  Source = -> Sketch011
  UniformScale = 1
  UseDefault = false
  UseSelected = true
  UseSelectedEdges = false
  Version = 0.2022.02.09
  WireOrder = [1]
FEATURE [Part::FeaturePython] WireFilter001  # WARN: FeaturePython — macro-defined, semantics opaque (R4)
  AttacherType = Attacher::AttachEngine3D
  ClaimChildren = true
  ColorKeyCount = 8
  Colorize = true
  FaceMaker = 5
  FixNormal = false
  FollowSource = true
  InvertedFaceScale = 5
  MaxWires = 25
  Normal = (0,0,1)
  OffsetFill = false
  OffsetIntersection = false
  OffsetJoin = 0
  OffsetOpenResult = false
  Scale = (1,1,1)
  SelectEdges = false
  Source = -> Sketch012
  UniformScale = 1
  UseDefault = false
  UseSelected = true
  UseSelectedEdges = false
  Version = 0.2022.02.09
  WireOrder = [1]
FEATURE [PartDesign::Pocket] Pocket
  BaseFeature = -> BaseBend005
  Direction = (0,-1,2e-16)
  Length = 5
  Length2 = 5
  Profile = -> WireFilter
  Suppressed = false
  Type = 1
FEATURE [PartDesign::Pocket] Pocket001
  BaseFeature = -> Pocket
  Direction = (0,0,-1)
  Length = 5
  Length2 = 5
  Profile = -> WireFilter001
  Reversed = true
  Suppressed = false
  Type = 1
FEATURE [Sketcher::SketchObject] Sketch013
  AttachmentSupport = -> [XY_Plane016]
  FullyConstrained = true
  MapMode = 5
  sketch-geometry (5):
    g0: LineSegment StartX=-36 StartY=25 StartZ=0 EndX=-36 EndY=0 EndZ=0
    g1: LineSegment StartX=-36 StartY=0 StartZ=0 EndX=36 EndY=0 EndZ=0
    g2: LineSegment StartX=36 StartY=0 StartZ=0 EndX=36 EndY=25 EndZ=0
    g3: LineSegment StartX=36 StartY=25 StartZ=0 EndX=-36 EndY=25 EndZ=0
    g4: GeomPoint X=0 Y=12.5 Z=0
  constraints (13):
    c: Coincident(g0,g1)
    c: Coincident(g1,g2)
    c: Coincident(g2,g3)
    c: Coincident(g3,g0)
    c: Horizontal(g1)
    c: Horizontal(g3)
    c: Vertical(g0)
    c: Vertical(g2)
    c: Symmetric(g1,g0,g4)
    c: PointOnObject(g4,g-2)
    c: PointOnObject(g1,g-1)
    c: DistanceY(g2,g2) = 25
    c: DistanceX(g1,g1) = 72
FEATURE [PartDesign::FeaturePython] BaseBend006  # WARN: FeaturePython — macro-defined, semantics opaque (R4)
  BendSide = 1
  BendSketch = -> Sketch013
  MidPlane = false
  Reverse = false
  Suppressed = false
  length = 84
  radius = 2
  thickness = 2
FEATURE [PartDesign::FeaturePython] Bend  # WARN: FeaturePython — macro-defined, semantics opaque (R4)
  AutoMiter = true
  BaseFeature = -> BaseBend006
  BendType = 1
  LengthList = [70]
  LengthSpec = 1
  ReliefFactor = 0.7
  Suppressed = false
  UseReliefFactor = false
  angle = 90
  baseObject = -> BaseBend006 [Edge26]
  bendAList = [90]
  extend1 = 0
  extend2 = 0
  gap1 = 0
  gap2 = 0
  invert = false
  kfactor = 0.5
  length = 70
  maxExtendDist = 5
  minGap = 0.1
  minReliefGap = 1
  miterangle1 = 0
  miterangle2 = 0
  offset = 0
  radius = 2
  reliefType = 0
  reliefd = 1
  reliefw = 0.8
  sketchflip = false
  sketchinvert = false
  unfold = false
  expr: radius = BaseBend006.radius
FEATURE [Sketcher::SketchObject] Sketch014  label="basement_bottom_sketch"
  FullyConstrained = true
  sketch-geometry (4):
    g0: LineSegment StartX=0 StartY=0 StartZ=0 EndX=147.224 EndY=85 EndZ=0
    g1: ArcOfCircle CenterX=930.111 CenterY=537 CenterZ=0 NormalX=0 NormalY=0 NormalZ=1 AngleXU=0 Radius=904 StartAngle=3.33435 EndAngle=3.66519
    g2: ArcOfCircle CenterX=18.317 CenterY=359.033 CenterZ=0 NormalX=0 NormalY=0 NormalZ=1 AngleXU=0 Radius=25 StartAngle=0.19276 EndAngle=1.51982
    g3: ArcOfCircle CenterX=0 CenterY=0 CenterZ=0 NormalX=0 NormalY=0 NormalZ=1 AngleXU=0 Radius=384.5 StartAngle=1.51982 EndAngle=1.5708
  constraints (13):
    c: Coincident(g0,g-1)
    c: Angle(g0) = 0.523599
    c: Coincident(g1,g0)
    c: PointOnObject(g1,g0)
    c: Tangent(g2,g1) = 1.5708
    c: Distance(g0) = 170  'min_r'
    c: Radius(g2) = 25
    c: PointOnObject(g3,g-2)
    c: PointOnObject(g3,g-2)
    c: Tangent(g3,g2) = -1.5708
    c: PointOnObject(g3,g-1)
    c: DistanceY(g3) = 384.5  'outer_r'
    c: Radius(g1) = 904
FEATURE [Sketcher::SketchObject] Sketch015  label="basement_sketch"
  FullyConstrained = true
  sketch-geometry (4):
    g0: LineSegment StartX=0 StartY=0 StartZ=0 EndX=219.104 EndY=126.5 EndZ=0
    g1: ArcOfCircle CenterX=-472.335 CenterY=-272.703 CenterZ=0 NormalX=0 NormalY=0 NormalZ=1 AngleXU=0 Radius=798.406 StartAngle=0.523599 EndAngle=0.870893
    g2: ArcOfCircle CenterX=12 CenterY=302.433 CenterZ=0 NormalX=0 NormalY=0 NormalZ=1 AngleXU=0 Radius=46.5 StartAngle=0.870893 EndAngle=1.53114
    g3: ArcOfCircle CenterX=0 CenterY=0 CenterZ=0 NormalX=0 NormalY=0 NormalZ=1 AngleXU=0 Radius=349.171 StartAngle=1.53114 EndAngle=1.5708
  constraints (13):
    c: Coincident(g1,g0)
    c: Angle(g0) = 0.523599
    c: Radius(g1) = 798.406
    c: Radius(g2) = 46.5
    c: Radius(g3) = 349.171  'max_r'
    c: Coincident(g3,g0)
    c: Coincident(g3,g-1)
    c: Tangent(g2,g1) = -1.5708
    c: Tangent(g3,g2) = -1.5708
    c: PointOnObject(g3,g-2)
    c: Distance(g0) = 253  'min_r'
    c: DistanceX(g2) = 12
    c: PointOnObject(g1,g0)
FEATURE [Part::Mirroring] Part__Mirroring003  label="Sketch014 (Mirror #4)"
  Base = (0,0,0)
  Normal = (1,0,0)
  Source = -> Sketch014
FEATURE [Part::Compound] Compound009
  Links = -> [Part__Mirroring003,Sketch014]
FEATURE [Part::FeaturePython] Array002  label="basement_bottom_2d"  # Draft array (typed FeaturePython)
  AlwaysSyncPlacement = false
  Angle = 360
  ArrayType = 1
  Axis = (0,0,1)
  Base = -> Compound009
  Center = (0,0,0)
  Count = 3
  ExpandArray = false
  Fuse = false
  IntervalAxis = (0,0,0)
  IntervalX = (50,0,0)
  IntervalY = (0,50,0)
  IntervalZ = (0,0,50)
  NumberCircles = 3
  NumberPolar = 3
  NumberX = 2
  NumberY = 2
  NumberZ = 1
  PlacementList = 3 placements: [(0,0,0),(0,0,0),(0,0,0)]
  RadialDistance = 50
  ScaleList = (3) [(1,1,1),(1,1,1),(1,1,1)]
  Symmetry = 1
  TangentialDistance = 25
FEATURE [Part::Mirroring] Part__Mirroring004  label="Sketch015 (Mirror #5)"
  Base = (0,0,0)
  Normal = (1,0,0)
  Source = -> Sketch015
FEATURE [PartDesign::SubShapeBinder] Binder003
  BindCopyOnChange = 0
  BindMode = 0
  ClaimChildren = true
  Context = -> Body007 [Binder003.]
  Fuse = false
  MakeFace = true
  OffsetFill = false
  OffsetIntersection = false
  OffsetJoinType = 0
  OffsetOpenResult = false
  PartialLoad = false
  Relative = false
  Support = -> [Array002]
  _Version = 2
FEATURE [PartDesign::SubShapeBinder] Binder004
  BindCopyOnChange = 0
  BindMode = 0
  ClaimChildren = true
  Context = -> Body009 [Binder004.]
  Fuse = false
  MakeFace = true
  Offset = 2
  OffsetFill = false
  OffsetIntersection = false
  OffsetJoinType = 0
  OffsetOpenResult = false
  PartialLoad = false
  Relative = false
  Support = -> [Array002]
  _Version = 2
FEATURE [PartDesign::SubShapeBinder] Binder005
  BindCopyOnChange = 0
  BindMode = 0
  ClaimChildren = true
  Context = -> Body006 [Binder005.]
  Fuse = false
  MakeFace = true
  OffsetFill = false
  OffsetIntersection = false
  OffsetJoinType = 0
  OffsetOpenResult = false
  PartialLoad = false
  Relative = false
  Support = -> [Array003]
  _Version = 2
FEATURE [PartDesign::SubShapeBinder] Binder006
  BindCopyOnChange = 0
  BindMode = 0
  ClaimChildren = true
  Context = -> Body008 [Binder006.]
  Fuse = false
  MakeFace = true
  Offset = 2
  OffsetFill = false
  OffsetIntersection = false
  OffsetJoinType = 0
  OffsetOpenResult = false
  PartialLoad = false
  Relative = false
  Support = -> [Array003]
  _Version = 2
FEATURE [Part::Compound] Compound010
  Links = -> [Sketch015,Part__Mirroring004]
FEATURE [Part::FeaturePython] Array003  label="basement_top_2d"  # Draft array (typed FeaturePython)
  AlwaysSyncPlacement = false
  Angle = 360
  ArrayType = 1
  Axis = (0,0,1)
  Base = -> Compound010
  Center = (0,0,0)
  Count = 3
  ExpandArray = false
  Fuse = false
  IntervalAxis = (0,0,0)
  IntervalX = (50,0,0)
  IntervalY = (0,50,0)
  IntervalZ = (0,0,50)
  NumberCircles = 3
  NumberPolar = 3
  NumberX = 2
  NumberY = 2
  NumberZ = 1
  PlacementList = 3 placements: [(0,0,0),(0,0,0),(0,0,0)]
  RadialDistance = 50
  ScaleList = (3) [(1,1,1),(1,1,1),(1,1,1)]
  Symmetry = 1
  TangentialDistance = 25
FEATURE [PartDesign::Pad] Pad001
  Direction = (0,0,1)
  Length = 18
  Length2 = 10
  Profile = -> Binder005
  Refine = true
  Suppressed = false
  Type = 0
FEATURE [PartDesign::Pad] Pad002
  Direction = (0,0,1)
  Length = 18
  Length2 = 10
  Profile = -> Binder003
  Suppressed = false
  Type = 0
FEATURE [PartDesign::Pad] Pad003
  Direction = (0,0,1)
  Length = 3
  Length2 = 10
  Profile = -> Binder006
  Suppressed = false
  Type = 0
FEATURE [PartDesign::Pad] Pad004
  Direction = (0,0,1)
  Length = 3
  Length2 = 10
  Profile = -> Binder004
  Suppressed = false
  Type = 0
FEATURE [PartDesign::SubShapeBinder] Binder007
  BindCopyOnChange = 0
  BindMode = 0
  ClaimChildren = true
  Fuse = false
  MakeFace = true
  OffsetFill = false
  OffsetIntersection = false
  OffsetJoinType = 0
  OffsetOpenResult = false
  PartialLoad = false
  Relative = false
  Support = -> [Compound011]
  _Version = 2
FEATURE [PartDesign::SubShapeBinder] Binder009  label="dropper_base"
  BindCopyOnChange = 0
  BindMode = 0
  ClaimChildren = true
  Fuse = false
  MakeFace = true
  OffsetFill = false
  OffsetIntersection = false
  OffsetJoinType = 0
  OffsetOpenResult = false
  PartialLoad = false
  Relative = true
  Support = -> [<external dropper.FCStd>#Sketch007]
  _Version = 2
  expr: Support = dropper#<<base>>._self
FEATURE [PartDesign::SubShapeBinder] Binder010  label="dropper_feed"
  BindCopyOnChange = 0
  BindMode = 0
  ClaimChildren = false
  Fuse = false
  MakeFace = true
  OffsetFill = false
  OffsetIntersection = false
  OffsetJoinType = 0
  OffsetOpenResult = false
  PartialLoad = false
  Relative = true
  Support = -> [<external dropper.FCStd>#Sketch008]
  _Version = 2
  expr: Support = dropper#<<feed>>._self
FEATURE [PartDesign::SubShapeBinder] Binder011  label="dropper_fix"
  BindCopyOnChange = 0
  BindMode = 0
  ClaimChildren = false
  Fuse = false
  MakeFace = true
  Offset = 0.5
  OffsetFill = false
  OffsetIntersection = false
  OffsetJoinType = 0
  OffsetOpenResult = false
  PartialLoad = false
  Relative = true
  Support = -> [<external dropper.FCStd>#Connect]
  _Version = 2
  expr: Support = dropper#<<fix>>._self
FEATURE [Part::FeaturePython] LinearArray002  # WARN: FeaturePython — macro-defined, semantics opaque (R4)
  Alignment = 0
  CellStart = A1
  Count = 2
  Dir = (1,0,0)
  DirIsDriven = true
  DistributionLaw = 0
  DrivenProperty = 1
  EndInclusive = true
  ExposePlacement = false
  GeneratorMode = 0
  MarkerShape = 1
  MarkerSize = 0
  NumElements = 2
  OrientMode = 1
  Placement = pos=(-32.5,0,0) rot=(0,0,1;0rad)
  Point = (0,0,0)
  PointIsDriven = true
  Reverse = false
  SpanEnd = 65
  SpanStart = 0
  Step = 65
  Type = lattice2LinearArray.LinearArray
  VSGVersion = 1
  Values = 0.0 | 65.0
  ValuesSource = 2
  isLattice = 1
  expr: .Placement.Base.x = -SpanEnd / 2
FEATURE [Part::FeaturePython] LinearArray003  # WARN: FeaturePython — macro-defined, semantics opaque (R4)
  Alignment = 0
  CellStart = A1
  Count = 2
  Dir = (1,0,0)
  DirIsDriven = true
  DistributionLaw = 0
  DrivenProperty = 1
  EndInclusive = true
  ExposePlacement = false
  GeneratorMode = 0
  MarkerShape = 1
  MarkerSize = 0
  NumElements = 2
  OrientMode = 1
  Placement = pos=(0,-75,0) rot=(0,0,1;1.5708rad)
  Point = (0,0,0)
  PointIsDriven = true
  Reverse = false
  SpanEnd = 150
  SpanStart = 0
  Step = 150
  Type = lattice2LinearArray.LinearArray
  VSGVersion = 1
  Values = 0.0 | 150.0
  ValuesSource = 2
  isLattice = 1
  expr: .Placement.Base.y = -SpanEnd / 2
FEATURE [Part::FeaturePython] LinearArray004  # WARN: FeaturePython — macro-defined, semantics opaque (R4)
  Alignment = 0
  CellStart = A1
  Count = 2
  Dir = (1,0,0)
  DirIsDriven = true
  DistributionLaw = 0
  DrivenProperty = 1
  EndInclusive = true
  ExposePlacement = false
  GeneratorMode = 0
  MarkerShape = 1
  MarkerSize = 0
  NumElements = 2
  OrientMode = 1
  Placement = pos=(-28.3,0,0) rot=(0,0,1;0rad)
  Point = (0,0,0)
  PointIsDriven = true
  Reverse = false
  SpanEnd = 56.6
  SpanStart = 0
  Step = 56.6
  Type = lattice2LinearArray.LinearArray
  VSGVersion = 1
  Values = 0.0 | 56.6
  ValuesSource = 2
  isLattice = 1
  expr: .Placement.Base.x = -SpanEnd / 2
  expr: SpanEnd = <<Properties>>.endface_width + dropper#<<base>>.Constraints.r * 2 + 4 mm
FEATURE [Part::FeaturePython] Populate002  label="Populate LinearArray004 with LinearArray003"  # WARN: FeaturePython — macro-defined, semantics opaque (R4)
  Copying = 0
  ExposePlacement = false
  MarkerShape = 1
  MarkerSize = 0
  NumElements = 4
  Object = -> LinearArray003
  OutputCompounding = 0
  PlacementsTo = -> LinearArray004
  Referencing = 0
  Type = lattice2PopulateCopies.LatticePopulateCopies
  isLattice = 1
FEATURE [Part::FeaturePython] Populate003  label="droppers placements"  # WARN: FeaturePython — macro-defined, semantics opaque (R4)
  Copying = 0
  ExposePlacement = false
  MarkerShape = 1
  MarkerSize = 0
  NumElements = 8
  Object = -> LinearArray002
  OutputCompounding = 0
  PlacementsTo = -> Populate002
  Referencing = 0
  Type = lattice2PopulateCopies.LatticePopulateCopies
  isLattice = 1
FEATURE [Part::FeaturePython] Populate004  label="populate dropper_fix"  # WARN: FeaturePython — macro-defined, semantics opaque (R4)
  Copying = 0
  ExposePlacement = false
  MarkerShape = 1
  MarkerSize = 0
  NumElements = 0
  Object = -> Binder011
  OutputCompounding = 1
  PlacementsTo = -> Populate003
  Referencing = 0
  Type = lattice2PopulateCopies.LatticePopulateCopies
  isLattice = 0
FEATURE [Part::FeaturePython] Populate005  label="Populate droppers placements with dropper_feed"  # WARN: FeaturePython — macro-defined, semantics opaque (R4)
  Copying = 0
  ExposePlacement = false
  MarkerShape = 1
  MarkerSize = 0
  NumElements = 0
  Object = -> Binder010
  OutputCompounding = 1
  PlacementsTo = -> Populate003
  Referencing = 0
  Type = lattice2PopulateCopies.LatticePopulateCopies
  isLattice = 0
FEATURE [Part::FeaturePython] Populate006  label="Populate droppers placements with dropper_base"  # WARN: FeaturePython — macro-defined, semantics opaque (R4)
  Copying = 0
  ExposePlacement = false
  MarkerShape = 1
  MarkerSize = 0
  NumElements = 0
  Object = -> Binder009
  OutputCompounding = 1
  PlacementsTo = -> Populate003
  Referencing = 0
  Type = lattice2PopulateCopies.LatticePopulateCopies
  isLattice = 0
FEATURE [Part::FeaturePython] Clone005  label="Populate droppers placements with dropper_base001"  # Draft clone (typed FeaturePython)
  AttacherType = Attacher::AttachEngine3D
  Fuse = false
  Objects = -> [Populate006]
  Placement = pos=(0,181.372,0) rot=(0,0,1;0rad)
  Scale = (1,1,1)
  expr: .Placement.Base.y = <<Properties>>.plane_middle
FEATURE [Sketcher::SketchObject] Sketch002  label="dropper_fix_sketch"
  ExternalGeometry = -> [Sketch,Clone005]
  FullyConstrained = true
  expr: Constraints[15] = composit_properties#<<Properties>>.thickness
  expr: Constraints[9] = 2 mm + <<dropper>>#<<base>>.Constraints.r * 2 + 2 mm
  sketch-geometry (8):
    g0: LineSegment StartX=42.1 StartY=292.046 StartZ=0 EndX=42.1 EndY=27.7705 EndZ=0
    g1: LineSegment StartX=0 StartY=348.872 StartZ=0 EndX=14.5 EndY=348.872 EndZ=0
    g2: LineSegment StartX=14.5 StartY=348.872 StartZ=0 EndX=42.1 EndY=292.046 EndZ=0
    g3: LineSegment StartX=0 StartY=0 StartZ=0 EndX=17 EndY=9.81495 EndZ=0
    g4: LineSegment StartX=17 StartY=9.81495 StartZ=0 EndX=15.5 EndY=12.413 EndZ=0
    g5: LineSegment StartX=15.5 StartY=12.413 StartZ=0 EndX=42.1 EndY=27.7705 EndZ=0
    g6: LineSegment StartX=28.3 StartY=288.872 StartZ=0 EndX=40.7133 EndY=294.901 EndZ=0
    g7: LineSegment StartX=28.3 StartY=288.872 StartZ=0 EndX=42.1 EndY=288.872 EndZ=0
  constraints (24):
    c: PointOnObject(g1,g-2)
    c: Coincident(g2,g0)
    c: Vertical(g0)
    c: Coincident(g3,g-1)
    c: Coincident(g5,g0)
    c: Coincident(g1,g2)
    c: Horizontal(g1)
    c: PointOnObject(g1,g-3)
    c: DistanceY(g1,g-3) = 3
    c: DistanceX(g-3,g5) = 27.6
    c: Coincident(g3,g4)
    c: PointOnObject(g-3,g3)
    c: Coincident(g4,g5)
    c: Perpendicular(g4,g3)
    c: Perpendicular(g5,g4)
    c: Distance(g4) = 3
    c: DistanceX(g-3,g4) = 1
    c: PointOnObject(g6,g2)
    c: PointOnObject(g7,g0)
    c: Perpendicular(g0,g7)
    c: Perpendicular(g2,g6)
    c: Equal(g7,g6)
    c: Coincident(g7,g-4)
    c: Coincident(g7,g6)
FEATURE [Part::Mirroring] Part__Mirroring005  label="dropper_fix_sketch (Mirror #6)"
  Base = (0,0,0)
  Normal = (1,0,0)
  Source = -> Sketch002
FEATURE [Part::Compound] Compound011  label="dropper_fix_base"
  Links = -> [Sketch002,Part__Mirroring005]
FEATURE [PartDesign::Pad] Pad005
  Direction = (0,0,1)
  Length = 3
  Length2 = 10
  Profile = -> Binder007
  Suppressed = false
  Type = 0
FEATURE [Sketcher::SketchObject] Sketch016
  ExternalGeometry = -> [Sketch002]
  FullyConstrained = true
  expr: Constraints[21] = composit_properties#<<Properties>>.thickness
  sketch-geometry (8):
    g0: LineSegment StartX=1.5 StartY=0.866025 StartZ=0 EndX=45.1 EndY=26.0385 EndZ=0
    g1: LineSegment StartX=45.1 StartY=26.0385 StartZ=0 EndX=45.1 EndY=292.736 EndZ=0
    g2: LineSegment StartX=45.1 StartY=292.736 StartZ=0 EndX=16.378 EndY=351.872 EndZ=0
    g3: LineSegment StartX=16.378 StartY=351.872 StartZ=0 EndX=0 EndY=351.872 EndZ=0
    g4: LineSegment StartX=14.5 StartY=351.872 StartZ=0 EndX=14.5 EndY=348.872 EndZ=0
    g5: LineSegment StartX=14.5 StartY=348.872 StartZ=0 EndX=17.1985 EndY=350.182 EndZ=0
    g6: LineSegment StartX=42.1 StartY=27.7705 StartZ=0 EndX=43.6 EndY=25.1725 EndZ=0
    g7: LineSegment StartX=42.1 StartY=27.7705 StartZ=0 EndX=45.1 EndY=27.7705 EndZ=0
  constraints (25):
    c: Coincident(g0,g1)
    c: Vertical(g1)
    c: Coincident(g1,g2)
    c: Coincident(g2,g3)
    c: PointOnObject(g3,g-2)
    c: Horizontal(g3)
    c: PointOnObject(g4,g3)
    c: Coincident(g4,g-4)
    c: Vertical(g4)
    c: Coincident(g4,g5)
    c: PointOnObject(g5,g2)
    c: Coincident(g-3,g6)
    c: PointOnObject(g6,g0)
    c: Coincident(g6,g7)
    c: PointOnObject(g7,g1)
    c: Horizontal(g7)
    c: Equal(g5,g4)
    c: Perpendicular(g5,g2)
    c: Perpendicular(g-4,g5)
    c: Perpendicular(g0,g6)
    c: Perpendicular(g-3,g6)
    c: DistanceY(g4,g4) = 3
    c: DistanceX(g0) = 1.5
    c: Equal(g5,g7)
    c: Equal(g7,g6)
FEATURE [Part::Mirroring] Part__Mirroring006  label="Sketch016 (Mirror #7)"
  Base = (0,0,0)
  Normal = (1,0,0)
  Source = -> Sketch016
FEATURE [Sketcher::SketchObject] Sketch017
  ExternalGeometry = -> [Sketch016]
  FullyConstrained = true
  sketch-geometry (9):
    g0: LineSegment StartX=45.1 StartY=26.0385 StartZ=0 EndX=-7.1e-15 EndY=52.077 EndZ=0
    g1: LineSegment StartX=45.1 StartY=292.736 StartZ=0 EndX=0 EndY=282.363 EndZ=0
    g2: LineSegment StartX=16.378 StartY=351.872 StartZ=0 EndX=0 EndY=325.709 EndZ=0
    g3: LineSegment StartX=0 StartY=351.872 StartZ=0 EndX=0 EndY=325.709 EndZ=0
    g4: LineSegment StartX=0 StartY=325.709 StartZ=0 EndX=23.5334 EndY=337.139 EndZ=0
    g5: LineSegment StartX=40.5682 StartY=302.066 StartZ=0 EndX=0 EndY=282.363 EndZ=0
    g6: LineSegment StartX=0 StartY=282.363 StartZ=0 EndX=45.1 EndY=282.363 EndZ=0
    g7: LineSegment StartX=22.55 StartY=13.0192 StartZ=0 EndX=-7.1e-15 EndY=52.077 EndZ=0
    g8: LineSegment StartX=-7.1e-15 StartY=52.077 StartZ=0 EndX=45.1 EndY=52.077 EndZ=0
  constraints (27):
    c: Coincident(g0,g-3)
    c: PointOnObject(g0,g-2)
    c: Coincident(g1,g-4)
    c: PointOnObject(g1,g-2)
    c: PointOnObject(g2,g-2)
    c: Coincident(g2,g-4)
    c: PointOnObject(g3,g-2)
    c: Coincident(g3,g2)
    c: Coincident(g3,g4)
    c: PointOnObject(g4,g-4)
    c: PointOnObject(g5,g-4)
    c: Coincident(g5,g1)
    c: Coincident(g5,g6)
    c: Horizontal(g6)
    c: PointOnObject(g7,g-3)
    c: Coincident(g7,g0)
    c: Coincident(g7,g8)
    c: Horizontal(g8)
    c: Vertical(g0,g8)
    c: Vertical(g8,g6)
    c: Horizontal(g3,g2)
    c: Perpendicular(g-4,g4)
    c: Perpendicular(g-4,g5)
    c: Equal(g6,g5)
    c: Equal(g4,g3)
    c: Perpendicular(g-3,g7)
    c: Equal(g7,g8)
FEATURE [Sketcher::SketchObject] Sketch018
  ExternalGeometry = -> [Sketch017]
  FullyConstrained = true
  sketch-geometry (30):
    g0: LineSegment StartX=0.05 StartY=0 StartZ=0 EndX=0.05 EndY=51.9904 EndZ=0
    g1: LineSegment StartX=0.05 StartY=51.9904 StartZ=0 EndX=44.65 EndY=26.2406 EndZ=0
    g2: LineSegment StartX=44.65 StartY=26.2406 StartZ=0 EndX=44.85 EndY=25.8942 EndZ=0
    g3: LineSegment StartX=44.85 StartY=25.8942 StartZ=0 EndX=45.1 EndY=26.0385 EndZ=0
    g4: LineSegment StartX=45.1 StartY=26.0385 StartZ=0 EndX=45.1 EndY=26.3272 EndZ=0
    g5: LineSegment StartX=45.1 StartY=26.3272 StartZ=0 EndX=44.7 EndY=26.3272 EndZ=0
    g6: LineSegment StartX=44.7 StartY=26.3272 StartZ=0 EndX=0.05 EndY=52.1059 EndZ=0
    g7: LineSegment StartX=0.05 StartY=52.1059 StartZ=0 EndX=0.05 EndY=282.323 EndZ=0
    g8: LineSegment StartX=0.05 StartY=282.323 StartZ=0 EndX=44.7 EndY=292.592 EndZ=0
    g9: LineSegment StartX=44.7 StartY=292.592 StartZ=0 EndX=45.1 EndY=292.592 EndZ=0
    g10: LineSegment StartX=45.1 StartY=292.592 StartZ=0 EndX=45.1 EndY=292.736 EndZ=0
    g11: LineSegment StartX=45.1 StartY=292.736 StartZ=0 EndX=45.0374 EndY=292.864 EndZ=0
    g12: LineSegment StartX=45.0374 StartY=292.864 StartZ=0 EndX=44.6776 EndY=292.69 EndZ=0
    g13: LineSegment StartX=44.6776 StartY=292.69 StartZ=0 EndX=0.05 EndY=282.425 EndZ=0
    g14: LineSegment StartX=0.05 StartY=282.425 StartZ=0 EndX=0.05 EndY=325.695 EndZ=0
    g15: LineSegment StartX=0.05 StartY=325.695 StartZ=0 EndX=16.1534 EndY=351.419 EndZ=0
    g16: LineSegment StartX=16.1534 StartY=351.419 StartZ=0 EndX=16.5132 EndY=351.593 EndZ=0
    g17: LineSegment StartX=16.5132 StartY=351.593 StartZ=0 EndX=16.378 EndY=351.872 EndZ=0
    g18: LineSegment StartX=16.378 StartY=351.872 StartZ=0 EndX=16.0687 EndY=351.872 EndZ=0
    g19: LineSegment StartX=16.0687 StartY=351.872 StartZ=0 EndX=16.0687 EndY=351.472 EndZ=0
    g20: LineSegment StartX=16.0687 StartY=351.472 StartZ=0 EndX=0 EndY=325.803 EndZ=0
    g21: LineSegment StartX=0.05 StartY=0 StartZ=0 EndX=0 EndY=0 EndZ=0
    g22: LineSegment StartX=0 StartY=0 StartZ=0 EndX=45.1 EndY=26.0385 EndZ=0
    g23: LineSegment StartX=45.1 StartY=26.0385 StartZ=0 EndX=45.1 EndY=292.736 EndZ=0
    g24: LineSegment StartX=45.1 StartY=292.736 StartZ=0 EndX=16.378 EndY=351.872 EndZ=0
    g25: LineSegment StartX=16.378 StartY=351.872 StartZ=0 EndX=0 EndY=351.872 EndZ=0
    g26: LineSegment StartX=-0.05 StartY=51.9904 StartZ=0 EndX=0.05 EndY=51.9904 EndZ=0
    g27: LineSegment StartX=0.05 StartY=51.9904 StartZ=0 EndX=0.1 EndY=52.077 EndZ=0
    g28: LineSegment StartX=0.05 StartY=282.425 StartZ=0 EndX=0.0724148 EndY=282.328 EndZ=0
    g29: LineSegment StartX=0.05 StartY=325.695 StartZ=0 EndX=-0.0347611 EndY=325.748 EndZ=0
  constraints (80):
    c: PointOnObject(g0,g-1)
    c: Vertical(g0)
    c: Coincident(g0,g1)
    c: Coincident(g1,g2)
    c: Coincident(g2,g3)
    c: Coincident(g3,g-5)
    c: Coincident(g3,g4)
    c: Vertical(g4)
    c: Coincident(g4,g5)
    c: Coincident(g5,g6)
    c: Coincident(g6,g7)
    c: Vertical(g7)
    c: Coincident(g7,g8)
    c: Coincident(g8,g9)
    c: Coincident(g9,g10)
    c: Coincident(g10,g-4)
    c: Vertical(g10)
    c: Coincident(g10,g11)
    c: Coincident(g11,g12)
    c: Coincident(g12,g13)
    c: Coincident(g13,g14)
    c: Vertical(g14)
    c: Coincident(g14,g15)
    c: Coincident(g15,g16)
    c: Coincident(g16,g17)
    c: Coincident(g17,g-3)
    c: Coincident(g17,g18)
    c: Horizontal(g18)
    c: Coincident(g18,g19)
    c: Vertical(g19)
    c: Coincident(g19,g20)
    c: PointOnObject(g20,g-2)
    c: Equal(g19,g16)
    c: Equal(g16,g12)
    c: Equal(g12,g9)
    c: Equal(g9,g5)
    c: Equal(g5,g2)
    c: Coincident(g21,g0)
    c: Coincident(g21,g-1)
    c: Coincident(g21,g22)
    c: Coincident(g22,g3)
    c: Coincident(g3,g23)
    c: Coincident(g23,g10)
    c: Coincident(g23,g24)
    c: Coincident(g24,g17)
    c: Coincident(g24,g25)
    c: PointOnObject(g25,g-2)
    c: Horizontal(g25)
    c: PointOnObject(g11,g24)
    c: PointOnObject(g2,g22)
    c: DistanceY(g19,g19) = 0.4
    c: Parallel(g15,g-3)
    c: Parallel(g-3,g20)
    c: Parallel(g13,g-4)
    c: Parallel(g-4,g8)
    c: Parallel(g6,g-5)
    c: Parallel(g-5,g1)
    c: Coincident(g26,g0)
    c: Coincident(g26,g27)
    c: PointOnObject(g27,g6)
    c: Symmetric(g26,g0,g-2)
    c: Vertical(g0,g6)
    c: Vertical(g7,g13)
    c: Coincident(g28,g13)
    c: PointOnObject(g28,g8)
    c: Coincident(g29,g14)
    c: PointOnObject(g29,g20)
    c: Equal(g26,g27)
    c: PointOnObject(g16,g24)
    c: Symmetric(g14,g29,g-3)
    c: DistanceX(g26,g26) = 0.1
    c: Perpendicular(g3,g2)
    c: Perpendicular(g4,g5)
    c: Equal(g27,g28)
    c: Equal(g29,g28)
    c: Perpendicular(g10,g9)
    c: Perpendicular(g11,g12)
    c: Symmetric(g0,g27,g-5)
    c: Perpendicular(g17,g16)
    c: Symmetric(g28,g13,g-4)
FEATURE [Part::Compound] Compound012
  Links = -> [Sketch016,Part__Mirroring006]
FEATURE [Part::Mirroring] Part__Mirroring007  label="Sketch018 (Mirror #8)"
  Base = (0,0,0)
  Normal = (1,0,0)
  Source = -> Sketch018
FEATURE [Part::Compound] Compound013
  Links = -> [Sketch018,Part__Mirroring007]
FEATURE [PartDesign::SubShapeBinder] Binder012
  BindCopyOnChange = 0
  BindMode = 0
  ClaimChildren = true
  Fuse = false
  MakeFace = true
  OffsetFill = false
  OffsetIntersection = false
  OffsetJoinType = 0
  OffsetOpenResult = false
  PartialLoad = false
  Placement = pos=(0,0,40) rot=(0,0,1;0rad)
  Relative = false
  Support = -> [Compound012]
  _Version = 2
FEATURE [PartDesign::SubShapeBinder] Binder013
  BindCopyOnChange = 0
  BindMode = 0
  ClaimChildren = true
  Fuse = false
  MakeFace = true
  OffsetFill = false
  OffsetIntersection = false
  OffsetJoinType = 0
  OffsetOpenResult = false
  PartialLoad = false
  Placement = pos=(0,0,40) rot=(0,0,1;0rad)
  Relative = false
  Support = -> [Compound013]
  _Version = 2
FEATURE [PartDesign::FeaturePython] BaseBend007  # WARN: FeaturePython — macro-defined, semantics opaque (R4)
  BendSide = 1
  BendSketch = -> Binder012
  MidPlane = false
  Reverse = true
  Suppressed = false
  length = 100
  radius = 0.1
  thickness = 0.3
  expr: radius = composit_properties#<<Properties>>.bend_r
  expr: thickness = composit_properties#<<Properties>>.al_thickness
FEATURE [PartDesign::FeaturePython] Bend001  # WARN: FeaturePython — macro-defined, semantics opaque (R4)
  AutoMiter = false
  BaseFeature = -> BaseBend007
  BendType = 0
  LengthList = [47]
  LengthSpec = 1
  ReliefFactor = 0.7
  Suppressed = false
  UseReliefFactor = false
  angle = 90
  baseObject = -> BaseBend007 [Edge14,Edge30,Edge46,Edge62,Edge70,Edge86,Edge102,Edge116]
  bendAList = [90]
  extend1 = 0
  extend2 = 0
  gap1 = 0
  gap2 = 0
  invert = false
  kfactor = 0.5
  length = 47
  maxExtendDist = 5
  minGap = 0.1
  minReliefGap = 1
  miterangle1 = 0
  miterangle2 = 0
  offset = 0
  radius = 0.1
  reliefType = 0
  reliefd = 1
  reliefw = 0.8
  sketchflip = false
  sketchinvert = false
  unfold = false
  expr: radius = BaseBend007.radius
FEATURE [PartDesign::Pocket] Pocket002
  BaseFeature = -> Bend001
  Direction = (0,0,-1)
  Length = 5
  Length2 = 5
  Profile = -> Binder013 [Face1]
  Refine = true
  Reversed = true
  Suppressed = false
  Type = 1
FEATURE [Sketcher::SketchObject] Sketch019
  ExternalGeometry = -> [Sketch017]
  FullyConstrained = true
  expr: Constraints[12] = <<Properties>>.rivet_d
  sketch-geometry (13):
    g0: Circle CenterX=0 CenterY=325.709 CenterZ=0 NormalX=0 NormalY=0 NormalZ=1 AngleXU=0 Radius=1.7
    g1: Circle CenterX=0 CenterY=282.363 CenterZ=0 NormalX=0 NormalY=0 NormalZ=1 AngleXU=0 Radius=2
    g2: Circle CenterX=-22.55 CenterY=277.288 CenterZ=0 NormalX=0 NormalY=0 NormalZ=1 AngleXU=0 Radius=1.7
    g3: Circle CenterX=22.55 CenterY=277.288 CenterZ=0 NormalX=0 NormalY=0 NormalZ=1 AngleXU=0 Radius=1.7
    g4: Circle CenterX=0 CenterY=52.077 CenterZ=0 NormalX=0 NormalY=0 NormalZ=1 AngleXU=0 Radius=2
    g5: Circle CenterX=20 CenterY=52.077 CenterZ=0 NormalX=0 NormalY=0 NormalZ=1 AngleXU=0 Radius=1.7
    g6: Circle CenterX=10 CenterY=34.7565 CenterZ=0 NormalX=0 NormalY=0 NormalZ=1 AngleXU=0 Radius=1.7
    g7: Circle CenterX=-10 CenterY=34.7565 CenterZ=0 NormalX=0 NormalY=0 NormalZ=1 AngleXU=0 Radius=1.7
    g8: Circle CenterX=-20 CenterY=52.077 CenterZ=0 NormalX=0 NormalY=0 NormalZ=1 AngleXU=0 Radius=1.7
    g9: GeomPoint X=22.55 Y=287.549 Z=0
    g10: LineSegment StartX=0 StartY=34.7565 StartZ=0 EndX=10 EndY=34.7565 EndZ=0
    g11: LineSegment StartX=10 StartY=34.7565 StartZ=0 EndX=15 EndY=43.4167 EndZ=0
    g12: Circle CenterX=0 CenterY=325.709 CenterZ=0 NormalX=0 NormalY=0 NormalZ=1 AngleXU=0 Radius=2
  constraints (29):
    c: Coincident(g0,g-4)
    c: Coincident(g1,g-3)
    c: Coincident(g4,g-5)
    c: Symmetric(g8,g5,g-2)
    c: Symmetric(g7,g6,g-2)
    c: Symmetric(g3,g2,g-2)
    c: Equal(g0,g3)
    c: Equal(g0,g2)
    c: Equal(g0,g8)
    c: Equal(g0,g5)
    c: Equal(g0,g7)
    c: Equal(g0,g6)
    c: Diameter(g0) = 3.4
    c: Symmetric(g1,g-3,g9)
    c: Symmetric(g6,g5,g-5)
    c: PointOnObject(g10,g-2)
    c: Coincident(g10,g6)
    c: Horizontal(g10)
    c: Coincident(g10,g11)
    c: PointOnObject(g11,g-5)
    c: Perpendicular(g-5,g11)
    c: Equal(g11,g10)
    c: DistanceX(g10,g10) = 10
    c: Vertical(g3,g9)
    c: Distance(g3,g-3) = 10
    c: Coincident(g12,g0)
    c: Diameter(g12) = 4
    c: Equal(g4,g1)
    c: Equal(g1,g12)
FEATURE [PartDesign::SubShapeBinder] Binder014
  BindCopyOnChange = 0
  BindMode = 0
  ClaimChildren = true
  Context = -> Link012 [Binder014.]
  Fuse = false
  MakeFace = true
  OffsetFill = false
  OffsetIntersection = false
  OffsetJoinType = 0
  OffsetOpenResult = false
  PartialLoad = false
  Relative = true
  Support = -> [Sketch019]
  _Version = 2
FEATURE [Sketcher::SketchObject] Sketch020
  AttachmentSupport = -> [XY_Plane005]
  FullyConstrained = true
  MapMode = 5
  expr: Constraints[10] = composit_properties#<<Properties>>.bend_r + composit_properties#<<Properties>>.al_thickness
  sketch-geometry (5):
    g0: ArcOfCircle CenterX=0 CenterY=0.46188 CenterZ=0 NormalX=0 NormalY=0 NormalZ=1 AngleXU=0 Radius=5 StartAngle=0.523599 EndAngle=2.61799
    g1: LineSegment StartX=0 StartY=0 StartZ=0 EndX=4.53013 EndY=2.61547 EndZ=0
    g2: LineSegment StartX=4.53013 StartY=2.61547 StartZ=0 EndX=4.33013 EndY=2.96188 EndZ=0
    g3: LineSegment StartX=0 StartY=0 StartZ=0 EndX=-4.53013 EndY=2.61547 EndZ=0
    g4: LineSegment StartX=-4.53013 StartY=2.61547 StartZ=0 EndX=-4.33013 EndY=2.96188 EndZ=0
  constraints (13):
    c: PointOnObject(g0,g-2)
    c: Coincident(g1,g-1)
    c: Coincident(g2,g1)
    c: Coincident(g3,g1)
    c: Coincident(g4,g3)
    c: Perpendicular(g3,g4)
    c: Perpendicular(g1,g2)
    c: Tangent(g2,g0) = -1.5708
    c: Tangent(g4,g0) = 1.5708
    c: Equal(g4,g2)
    c: Distance(g2) = 0.4
    c: Diameter(g0) = 10
    c: Angle(g1,g3) = 2.0944
FEATURE [PartDesign::SubShapeBinder] Binder015
  BindCopyOnChange = 0
  BindMode = 0
  ClaimChildren = false
  Context = -> Link012 [Binder015.]
  Fuse = false
  MakeFace = true
  OffsetFill = false
  OffsetIntersection = false
  OffsetJoinType = 0
  OffsetOpenResult = false
  PartialLoad = false
  Relative = true
  Support = -> [Sketch002]
  _Version = 2
  expr: Support = <<dropper_fix_sketch>>._self
FEATURE [Sketcher::SketchObject] Sketch022  label="cap_outer_shape"
  AttachmentSupport = -> [YZ_Plane005]
  ExternalGeometry = -> [Binder012]
  FullyConstrained = true
  MapMode = 5
  Placement = pos=(0,0,0) rot=(0.57735,0.57735,0.57735;2.0944rad)
  expr: Constraints[11] = composit_properties#<<Properties>>.bend_r + composit_properties#<<Properties>>.al_thickness
  expr: Constraints[9] = composit_properties#<<Properties>>.bend_r + composit_properties#<<Properties>>.al_thickness + 0.01 mm
  sketch-geometry (5):
    g0: LineSegment StartX=351.882 StartY=40.41 StartZ=0 EndX=0 EndY=40.41 EndZ=0
    g1: LineSegment StartX=0 StartY=40.41 StartZ=0 EndX=0 EndY=0 EndZ=0
    g2: LineSegment StartX=0 StartY=0 StartZ=0 EndX=351.882 EndY=0 EndZ=0
    g3: LineSegment StartX=351.882 StartY=0 StartZ=0 EndX=351.882 EndY=40.41 EndZ=0
    g4: GeomPoint X=351.872 Y=40.4 Z=0
  constraints (14):
    c: Coincident(g0,g1)
    c: Coincident(g1,g2)
    c: Coincident(g2,g3)
    c: Coincident(g3,g0)
    c: Horizontal(g0)
    c: Horizontal(g2)
    c: Vertical(g1)
    c: Vertical(g3)
    c: Coincident(g1,g-1)
    c: DistanceY(g-3,g0) = 0.41
    c: DistanceX(g-3,g0) = 0.01
    c: DistanceY(g-3,g4) = 0.4
    c: Vertical(g-3,g4)
    c: DistanceY(g4) = 40.4  'height'
FEATURE [Part::FeaturePython] WireFilter002  # WARN: FeaturePython — macro-defined, semantics opaque (R4)
  AttacherType = Attacher::AttachEngine3D
  ClaimChildren = true
  ColorKeyCount = 8
  Colorize = true
  FaceMaker = 5
  FixNormal = false
  FollowSource = true
  InvertedFaceScale = 5
  MaxWires = 25
  Normal = (1,0,0)
  OffsetFill = false
  OffsetIntersection = false
  OffsetJoin = 0
  OffsetOpenResult = false
  Scale = (1,1,1)
  SelectEdges = false
  Source = -> Sketch022
  UniformScale = 1
  UseDefault = false
  UseSelected = true
  UseSelectedEdges = false
  Version = 0.2022.02.09
  WireOrder = [1]
FEATURE [PartDesign::SubShapeBinder] Binder016
  BindCopyOnChange = 0
  BindMode = 0
  ClaimChildren = true
  Fuse = false
  MakeFace = false
  OffsetFill = false
  OffsetIntersection = false
  OffsetJoinType = 0
  OffsetOpenResult = false
  PartialLoad = false
  Relative = false
  Support = -> [Sketch019]
  _Version = 2
FEATURE [PartDesign::SubShapeBinder] Binder018
  BindCopyOnChange = 0
  BindMode = 0
  ClaimChildren = false
  Fuse = false
  MakeFace = true
  OffsetFill = false
  OffsetIntersection = false
  OffsetJoinType = 0
  OffsetOpenResult = false
  PartialLoad = false
  Relative = false
  Support = -> [Body002[BaseBend007.Binder012.Compound012.Part__Mirroring006.Sketch016.]]
  _Version = 2
FEATURE [PartDesign::SubShapeBinder] Binder019
  BindCopyOnChange = 0
  BindMode = 0
  ClaimChildren = false
  Fuse = false
  MakeFace = false
  OffsetFill = false
  OffsetIntersection = false
  OffsetJoinType = 0
  OffsetOpenResult = false
  PartialLoad = false
  Relative = false
  Support = -> [Sketch019]
  _Version = 2
FEATURE [PartDesign::SubShapeBinder] Binder020
  BindCopyOnChange = 0
  BindMode = 0
  ClaimChildren = false
  Context = -> Link015 [Binder020.]
  Fuse = false
  MakeFace = true
  OffsetFill = false
  OffsetIntersection = false
  OffsetJoinType = 0
  OffsetOpenResult = false
  PartialLoad = false
  Relative = true
  Support = -> [Body002[BaseBend007.Binder012.Compound012.Part__Mirroring006.Sketch016.]]
  _Version = 2
FEATURE [Sketcher::SketchObject] Sketch023
  AttachmentSupport = -> [XY_Plane006]
  ExternalGeometry = -> [Binder020]
  FullyConstrained = true
  MapMode = 5
  expr: Constraints[9] = composit_properties#<<Properties>>.thickness + composit_properties#<<Properties>>.bend_r + composit_properties#<<Properties>>.al_thickness
  sketch-geometry (5):
    g0: LineSegment StartX=41.7 StartY=29.0385 StartZ=0 EndX=-41.7 EndY=29.0385 EndZ=0
    g1: LineSegment StartX=-41.7 StartY=29.0385 StartZ=0 EndX=-41.7 EndY=58.0385 EndZ=0
    g2: LineSegment StartX=-41.7 StartY=58.0385 StartZ=0 EndX=41.7 EndY=58.0385 EndZ=0
    g3: LineSegment StartX=41.7 StartY=58.0385 StartZ=0 EndX=41.7 EndY=29.0385 EndZ=0
    g4: GeomPoint X=0 Y=43.5385 Z=0
  constraints (13):
    c: Coincident(g0,g1)
    c: Coincident(g1,g2)
    c: Coincident(g2,g3)
    c: Coincident(g3,g0)
    c: Horizontal(g0)
    c: Horizontal(g2)
    c: Vertical(g1)
    c: Vertical(g3)
    c: DistanceY(g-3,g0) = 3
    c: DistanceX(g0,g-3) = 3.4
    c: PointOnObject(g4,g-2)
    c: Symmetric(g2,g0,g4)
    c: DistanceY(g3,g3) = 29
FEATURE [PartDesign::Pad] Pad007
  Direction = (0,0,1)
  Length = 0.3
  Length2 = 10
  Profile = -> Sketch023
  ReferenceAxis = -> Sketch023 [N_Axis]
  Suppressed = false
  Type = 0
  expr: Length = composit_properties#<<Properties>>.al_thickness
FEATURE [PartDesign::FeaturePython] Bend002  label="cap_inner1_bend"  # WARN: FeaturePython — macro-defined, semantics opaque (R4)
  AutoMiter = true
  BaseFeature = -> Pad007
  BendType = 0
  LengthList = [31]
  LengthSpec = 0
  ReliefFactor = 0.7
  Suppressed = false
  UseReliefFactor = false
  angle = 90
  baseObject = -> Pad007 [Edge12,Edge7]
  bendAList = [90]
  extend1 = 0
  extend2 = 0
  gap1 = 0
  gap2 = 0
  invert = false
  kfactor = 0.5
  length = 31
  maxExtendDist = 5
  minGap = 0.1
  minReliefGap = 1
  miterangle1 = 0
  miterangle2 = 0
  offset = 0
  radius = 0.1
  reliefType = 0
  reliefd = 1
  reliefw = 0.8
  sketchflip = false
  sketchinvert = false
  unfold = false
  expr: length = <<cap_outer_shape>>.Constraints.height - composit_properties#<<Properties>>.thickness - composit_properties#<<Properties>>.al_thickness - composit_properties#<<Properties>>.bend_r - 6 mm
  expr: radius = BaseBend007.radius
FEATURE [Sketcher::SketchObject] Sketch024
  AttachmentSupport = -> [XY_Plane023]
  ExternalGeometry = -> [Binder019,Binder018]
  FullyConstrained = true
  MapMode = 5
  expr: Constraints[10] = composit_properties#<<Properties>>.thickness + composit_properties#<<Properties>>.al_thickness + composit_properties#<<Properties>>.bend_r
  sketch-geometry (5):
    g0: LineSegment StartX=-41.7 StartY=272.288 StartZ=0 EndX=-41.7 EndY=289.736 EndZ=0
    g1: LineSegment StartX=-41.7 StartY=289.736 StartZ=0 EndX=41.7 EndY=289.736 EndZ=0
    g2: LineSegment StartX=41.7 StartY=289.736 StartZ=0 EndX=41.7 EndY=272.288 EndZ=0
    g3: LineSegment StartX=41.7 StartY=272.288 StartZ=0 EndX=-41.7 EndY=272.288 EndZ=0
    g4: GeomPoint X=0 Y=281.012 Z=0
  constraints (13):
    c: Coincident(g0,g1)
    c: Coincident(g1,g2)
    c: Coincident(g2,g3)
    c: Coincident(g3,g0)
    c: Horizontal(g1)
    c: Horizontal(g3)
    c: Vertical(g0)
    c: Vertical(g2)
    c: Symmetric(g1,g0,g4)
    c: PointOnObject(g4,g-2)
    c: DistanceX(g1,g-4) = 3.4
    c: DistanceY(g2,g-3) = 5
    c: DistanceY(g1,g-4) = 3
FEATURE [PartDesign::FeaturePython] BaseBend008  # WARN: FeaturePython — macro-defined, semantics opaque (R4)
  BendSide = 0
  BendSketch = -> Sketch024
  MidPlane = false
  Reverse = false
  Suppressed = false
  length = 100
  radius = 0.1
  thickness = 0.3
  expr: radius = composit_properties#<<Properties>>.bend_r
  expr: thickness = composit_properties#<<Properties>>.al_thickness
FEATURE [PartDesign::Hole] Hole001
  BaseFeature = -> Bend002
  CustomThreadClearance = 0
  Depth = 25
  DepthType = 0
  Diameter = 3.4
  DrillForDepth = false
  DrillPoint = 1
  DrillPointAngle = 118
  HoleCutCountersinkAngle = 90
  HoleCutCustomValues = false
  HoleCutDepth = 0
  HoleCutDiameter = 6.1
  HoleCutType = 0
  ModelThread = false
  Profile = -> Binder016
  Reversed = true
  Suppressed = false
  Tapered = false
  TaperedAngle = 90
  ThreadClass = 0
  ThreadDepth = 25
  ThreadDepthType = 0
  ThreadDirection = 0
  ThreadFit = 0
  ThreadSize = 0
  ThreadType = 0
  Threaded = false
  UseCustomThreadClearance = false
  expr: Diameter = <<Properties>>.rivet_d
FEATURE [PartDesign::Body] Body003  label="cap_inner1_material_0.30ansi"
  Group = -> [Sketch023,Binder016,Binder020,Pad007,Bend002,Hole001]
  Origin = -> Origin006
  Tip = -> Hole001
FEATURE [Sketcher::SketchObject] Sketch025
  AttachmentSupport = -> [XY_Plane007]
  FullyConstrained = true
  MapMode = 5
FEATURE [Sketcher::SketchObject] Sketch026
  ExternalGeometry = -> [Sketch002]
  FullyConstrained = true
  expr: Constraints[38] = composit_properties#<<Properties>>.thickness
  sketch-geometry (16):
    g0: LineSegment StartX=42.1 StartY=27.7705 StartZ=0 EndX=42.1 EndY=292.046 EndZ=0
    g1: LineSegment StartX=14.5 StartY=348.872 StartZ=0 EndX=0 EndY=348.872 EndZ=0
    g2: LineSegment StartX=17 StartY=9.81495 StartZ=0 EndX=15.5 EndY=12.413 EndZ=0
    g3: ArcOfCircle CenterX=0 CenterY=5.53356 CenterZ=0 NormalX=0 NormalY=0 NormalZ=1 AngleXU=0 Radius=4.79221 StartAngle=4.71239 EndAngle=5.23599
    g4: LineSegment StartX=0 StartY=0 StartZ=0 EndX=2.39612 EndY=1.3834 EndZ=0
    g5: ArcOfCircle CenterX=16.8856 CenterY=13.213 CenterZ=0 NormalX=0 NormalY=0 NormalZ=1 AngleXU=0 Radius=1.6 StartAngle=0.523599 EndAngle=3.66519
    g6: LineSegment StartX=17 StartY=9.81495 StartZ=0 EndX=18.2713 EndY=14.013 EndZ=0
    g7: ArcOfCircle CenterX=37.3078 CenterY=30.5373 CenterZ=0 NormalX=0 NormalY=0 NormalZ=1 AngleXU=0 Radius=4.79221 StartAngle=5.23599 EndAngle=6.28319
    g8: LineSegment StartX=39.7039 StartY=26.3872 StartZ=0 EndX=42.1 EndY=27.7705 EndZ=0
    g9: LineSegment StartX=42.1 StartY=27.7705 StartZ=0 EndX=42.1 EndY=30.5373 EndZ=0
    g10: ArcOfCircle CenterX=29.6 CenterY=289.171 CenterZ=0 NormalX=0 NormalY=0 NormalZ=1 AngleXU=0 Radius=12.5 StartAngle=-9e-16 EndAngle=0.452137
    g11: LineSegment StartX=42.1 StartY=289.171 StartZ=0 EndX=42.1 EndY=292.046 EndZ=0
    g12: LineSegment StartX=42.1 StartY=292.046 StartZ=0 EndX=40.8439 EndY=294.632 EndZ=0
    g13: LineSegment StartX=11.5 StartY=348.872 StartZ=0 EndX=14.5 EndY=348.872 EndZ=0
    g14: LineSegment StartX=14.5 StartY=348.872 StartZ=0 EndX=15.8107 EndY=346.173 EndZ=0
    g15: ArcOfCircle CenterX=11.5 CenterY=344.079 CenterZ=0 NormalX=0 NormalY=0 NormalZ=1 AngleXU=0 Radius=4.79221 StartAngle=0.452137 EndAngle=1.5708
  constraints (42):
    c: Coincident(g0,g-4)
    c: Coincident(g0,g-5)
    c: Coincident(g1,g-5)
    c: PointOnObject(g1,g-2)
    c: Horizontal(g1)
    c: Coincident(g2,g-3)
    c: Coincident(g2,g-4)
    c: PointOnObject(g3,g-2)
    c: PointOnObject(g3,g-2)
    c: PointOnObject(g3,g-3)
    c: Coincident(g4,g-3)
    c: Coincident(g4,g3)
    c: Tangent(g4,g3)
    c: PointOnObject(g5,g-4)
    c: Coincident(g5,g2)
    c: PointOnObject(g5,g-4)
    c: Coincident(g6,g2)
    c: Coincident(g6,g5)
    c: Diameter(g5) = 3.2
    c: PointOnObject(g7,g-4)
    c: PointOnObject(g7,g0)
    c: Coincident(g8,g0)
    c: Coincident(g9,g8)
    c: Coincident(g9,g7)
    c: Tangent(g9,g7)
    c: Tangent(g8,g7) = -1.5708
    c: PointOnObject(g10,g-5)
    c: PointOnObject(g10,g0)
    c: Coincident(g11,g12)
    c: Tangent(g10,g11) = -1.5708
    c: Coincident(g11,g0)
    c: Tangent(g12,g10) = -1.5708
    c: PointOnObject(g13,g1)
    c: Coincident(g13,g1)
    c: Coincident(g13,g14)
    c: PointOnObject(g14,g-5)
    c: Tangent(g15,g13) = 1.5708
    c: Tangent(g15,g14) = 1.5708
    c: DistanceX(g13,g13) = 3
    c: Diameter(g10) = 25
    c: Equal(g3,g7)
    c: Equal(g7,g15)
FEATURE [Part::Mirroring] Part__Mirroring008  label="Sketch026 (Mirror #9)"
  Base = (0,0,0)
  Normal = (1,0,0)
  Source = -> Sketch026
FEATURE [Part::Compound] Compound014
  Links = -> [Part__Mirroring008,Sketch026]
FEATURE [PartDesign::SubShapeBinder] Binder021
  BindCopyOnChange = 0
  BindMode = 0
  ClaimChildren = true
  Fuse = false
  MakeFace = true
  OffsetFill = false
  OffsetIntersection = false
  OffsetJoinType = 0
  OffsetOpenResult = false
  PartialLoad = false
  Relative = false
  Support = -> [Compound014]
  _Version = 2
FEATURE [PartDesign::Pocket] Pocket006
  BaseFeature = -> Pad005
  Direction = (0,0,-1)
  Length = 5
  Length2 = 5
  Midplane = true
  Profile = -> Binder021
  Suppressed = false
  Type = 1
FEATURE [Sketcher::SketchObject] Sketch027
  AttachmentSupport = -> [XY_Plane007]
  FullyConstrained = true
  MapMode = 5
  sketch-geometry (1):
    g0: Circle CenterX=0 CenterY=40 CenterZ=0 NormalX=0 NormalY=0 NormalZ=1 AngleXU=0 Radius=4
  constraints (3):
    c: PointOnObject(g0,g-2)
    c: Diameter(g0) = 8
    c: DistanceY(g0) = 40
FEATURE [PartDesign::SubShapeBinder] Binder023
  BindCopyOnChange = 0
  BindMode = 0
  ClaimChildren = true
  Context = -> Body004 [Binder023.]
  Fuse = false
  MakeFace = true
  OffsetFill = false
  OffsetIntersection = false
  OffsetJoinType = 0
  OffsetOpenResult = false
  PartialLoad = false
  Relative = true
  Support = -> [Clone005]
  _Version = 2
FEATURE [Sketcher::SketchObject] Sketch028
  AttachmentSupport = -> [XY_Plane007]
  ExternalGeometry = -> [Binder023]
  FullyConstrained = true
  MapMode = 5
  expr: Constraints[9] = <<Properties>>.rivet_d
  sketch-geometry (10):
    g0: Circle CenterX=0 CenterY=59 CenterZ=0 NormalX=0 NormalY=0 NormalZ=1 AngleXU=0 Radius=1.7
    g1: Circle CenterX=0 CenterY=106.372 CenterZ=0 NormalX=0 NormalY=0 NormalZ=1 AngleXU=0 Radius=1.7
    g2: Circle CenterX=0 CenterY=181.372 CenterZ=0 NormalX=0 NormalY=0 NormalZ=1 AngleXU=0 Radius=1.7
    g3: Circle CenterX=0 CenterY=256.372 CenterZ=0 NormalX=0 NormalY=0 NormalZ=1 AngleXU=0 Radius=1.7
    g4: Circle CenterX=0 CenterY=303.743 CenterZ=0 NormalX=0 NormalY=0 NormalZ=1 AngleXU=0 Radius=1.7
    g5: LineSegment StartX=28.3 StartY=73.8716 StartZ=0 EndX=28.3 EndY=106.372 EndZ=0
    g6: LineSegment StartX=28.3 StartY=106.372 StartZ=0 EndX=28.3 EndY=138.872 EndZ=0
    g7: LineSegment StartX=28.3 StartY=138.872 StartZ=0 EndX=28.3 EndY=181.372 EndZ=0
    g8: LineSegment StartX=28.3 StartY=181.372 StartZ=0 EndX=28.3 EndY=223.872 EndZ=0
    g9: LineSegment StartX=28.3 StartY=223.872 StartZ=0 EndX=28.3 EndY=256.372 EndZ=0
  constraints (24):
    c: PointOnObject(g0,g-2)
    c: PointOnObject(g1,g-2)
    c: PointOnObject(g2,g-2)
    c: PointOnObject(g3,g-2)
    c: DistanceY(g0) = 59
    c: Equal(g0, g1-g4) x4
    c: Diameter(g0) = 3.4
    c: Coincident(g5,g-3)
    c: Vertical(g5)
    c: Coincident(g5,g6)
    c: Coincident(g6,g-4)
    c: Coincident(g6,g7)
    c: Vertical(g7)
    c: Coincident(g7,g8)
    c: Coincident(g8,g-5)
    c: Coincident(g8,g9)
    c: Vertical(g9)
    c: Equal(g5,g6)
    c: Equal(g6,g9)
    c: Equal(g7,g8)
    c: Horizontal(g2,g7)
    c: Horizontal(g1,g5)
    c: Horizontal(g3,g9)
    c: Symmetric(g0,g4,g2)
FEATURE [PartDesign::Hole] Hole003
  BaseFeature = -> Pocket006
  CustomThreadClearance = 0
  Depth = 25
  DepthType = 0
  Diameter = 3.4
  DrillForDepth = false
  DrillPoint = 1
  DrillPointAngle = 118
  HoleCutCountersinkAngle = 90
  HoleCutCustomValues = false
  HoleCutDepth = 0
  HoleCutDiameter = 6.1
  HoleCutType = 0
  ModelThread = false
  Profile = -> Sketch028
  Reversed = true
  Suppressed = false
  Tapered = false
  TaperedAngle = 90
  ThreadClass = 0
  ThreadDepth = 25
  ThreadDepthType = 0
  ThreadDirection = 0
  ThreadFit = 0
  ThreadSize = 0
  ThreadType = 0
  Threaded = false
  UseCustomThreadClearance = false
  expr: Diameter = <<Properties>>.rivet_d
FEATURE [Sketcher::SketchObject] Sketch029  label="top_connector_base_sketch"
  AttachmentOffset = pos=(0,0,-35) rot=(0,0,1;0rad)
  AttachmentSupport = -> [XZ_Plane024]
  FullyConstrained = true
  MapMode = 5
  Placement = pos=(0,35,-7.8e-15) rot=(1,0,0;1.5708rad)
  expr: .Constraints.width = <<Properties>>.inner_width
  sketch-geometry (5):
    g0: LineSegment StartX=-11.5 StartY=-13 StartZ=0 EndX=-11.5 EndY=-1.95e-14 EndZ=0
    g1: LineSegment StartX=-11.5 StartY=-1.95e-14 StartZ=0 EndX=11.5 EndY=-1.95e-14 EndZ=0
    g2: LineSegment StartX=11.5 StartY=-1.95e-14 StartZ=0 EndX=11.5 EndY=-13 EndZ=0
    g3: LineSegment StartX=11.5 StartY=-13 StartZ=0 EndX=-11.5 EndY=-13 EndZ=0
    g4: GeomPoint X=-3.6e-15 Y=-6.5 Z=0
  constraints (13):
    c: Coincident(g0,g1)
    c: Coincident(g1,g2)
    c: Coincident(g2,g3)
    c: Coincident(g3,g0)
    c: Horizontal(g1)
    c: Horizontal(g3)
    c: Vertical(g0)
    c: Vertical(g2)
    c: Symmetric(g1,g0,g4)
    c: PointOnObject(g4,g-2)
    c: PointOnObject(g1,g-1)
    c: DistanceX(g1,g1) = 23  'width'
    c: DistanceY(g2,g2) = 13  'height'
FEATURE [PartDesign::FeaturePython] BaseBend009  # WARN: FeaturePython — macro-defined, semantics opaque (R4)
  BendSide = 0
  BendSketch = -> Sketch029
  MidPlane = false
  Reverse = true
  Suppressed = false
  length = 283.743
  radius = 0.1
  thickness = 0.3
  expr: radius = composit_properties#<<Properties>>.bend_r
  expr: thickness = composit_properties#<<Properties>>.al_thickness
FEATURE [PartDesign::SubShapeBinder] Binder029
  BindCopyOnChange = 0
  BindMode = 0
  ClaimChildren = false
  Context = -> Body017 [Binder029.]
  Fuse = false
  MakeFace = true
  OffsetFill = false
  OffsetIntersection = false
  OffsetJoinType = 0
  OffsetOpenResult = false
  PartialLoad = false
  Relative = true
  Support = -> [Sketch027]
  _Version = 2
  expr: Support = Sketch027._self
FEATURE [PartDesign::SubShapeBinder] Binder030
  BindCopyOnChange = 0
  BindMode = 0
  ClaimChildren = false
  Context = -> Body017 [Binder030.]
  Fuse = false
  MakeFace = true
  OffsetFill = false
  OffsetIntersection = false
  OffsetJoinType = 0
  OffsetOpenResult = false
  PartialLoad = false
  Relative = true
  Support = -> [Sketch028]
  _Version = 2
  expr: Support = Sketch028._self
FEATURE [PartDesign::Hole] Hole004
  BaseFeature = -> BaseBend009
  CustomThreadClearance = 0
  Depth = 25
  DepthType = 0
  Diameter = 3.4
  DrillForDepth = false
  DrillPoint = 1
  DrillPointAngle = 118
  HoleCutCountersinkAngle = 90
  HoleCutCustomValues = false
  HoleCutDepth = 0
  HoleCutDiameter = 6.1
  HoleCutType = 0
  ModelThread = false
  Profile = -> Binder030
  Suppressed = false
  Tapered = false
  TaperedAngle = 90
  ThreadClass = 0
  ThreadDepth = 25
  ThreadDepthType = 0
  ThreadDirection = 0
  ThreadFit = 0
  ThreadSize = 0
  ThreadType = 0
  Threaded = false
  UseCustomThreadClearance = false
  expr: Diameter = <<Properties>>.rivet_d
FEATURE [Sketcher::SketchObject] Sketch032
  AttachmentSupport = -> [XZ_Plane025]
  FullyConstrained = true
  MapMode = 5
  Placement = pos=(0,0,0) rot=(1,0,0;1.5708rad)
  expr: Constraints[11] = <<Properties>>.inner_width
  sketch-geometry (5):
    g0: LineSegment StartX=-11.5 StartY=-12 StartZ=0 EndX=-11.5 EndY=-2.84e-14 EndZ=0
    g1: LineSegment StartX=-11.5 StartY=-2.84e-14 StartZ=0 EndX=11.5 EndY=-2.84e-14 EndZ=0
    g2: LineSegment StartX=11.5 StartY=-2.84e-14 StartZ=0 EndX=11.5 EndY=-12 EndZ=0
    g3: LineSegment StartX=11.5 StartY=-12 StartZ=0 EndX=-11.5 EndY=-12 EndZ=0
    g4: GeomPoint X=-5.1e-15 Y=-6 Z=0
  constraints (13):
    c: Coincident(g0,g1)
    c: Coincident(g1,g2)
    c: Coincident(g2,g3)
    c: Coincident(g3,g0)
    c: Horizontal(g1)
    c: Horizontal(g3)
    c: Vertical(g0)
    c: Vertical(g2)
    c: Symmetric(g1,g0,g4)
    c: PointOnObject(g4,g-2)
    c: PointOnObject(g1,g-1)
    c: DistanceX(g1,g1) = 23
    c: DistanceY(g2,g2) = 12
FEATURE [PartDesign::FeaturePython] BaseBend010  # WARN: FeaturePython — macro-defined, semantics opaque (R4)
  BendSide = 0
  BendSketch = -> Sketch032
  MidPlane = false
  Reverse = true
  Suppressed = false
  length = 35
  radius = 0.1
  thickness = 0.3
  expr: radius = composit_properties#<<Properties>>.bend_r
  expr: thickness = composit_properties#<<Properties>>.al_thickness
FEATURE [Sketcher::SketchObject] Sketch033
  AttachmentSupport = -> [XY_Plane025]
  FullyConstrained = true
  MapMode = 5
  expr: Constraints[6] = composit_properties#<<Properties>>.bend_r + composit_properties#<<Properties>>.al_thickness
  expr: Constraints[7] = <<Properties>>.inner_width / 2
  sketch-geometry (7):
    g0: LineSegment StartX=0 StartY=-1.289e-13 StartZ=0 EndX=11.1 EndY=6.40859 EndZ=0
    g1: LineSegment StartX=11.5 StartY=0 StartZ=0 EndX=0 EndY=-1.289e-13 EndZ=0
    g2: LineSegment StartX=11.1 StartY=6.40859 StartZ=0 EndX=11.1 EndY=8.33953 EndZ=0
    g3: LineSegment StartX=11.1 StartY=8.33953 StartZ=0 EndX=11.5 EndY=8.33953 EndZ=0
    g4: GeomPoint X=11.5 Y=6.63953 Z=0
    g5: LineSegment StartX=11.5 StartY=8.33953 StartZ=0 EndX=11.5 EndY=6.63953 EndZ=0
    g6: LineSegment StartX=11.5 StartY=6.63953 StartZ=0 EndX=11.5 EndY=0 EndZ=0
  constraints (18):
    c: Coincident(g-1,g0)
    c: Coincident(g0,g2)
    c: Coincident(g3,g5)
    c: PointOnObject(g6,g-1)
    c: Coincident(g6,g1)
    c: Coincident(g1,g0)
    c: DistanceX(g2,g3) = 0.4
    c: DistanceX(g1,g1) = 11.5
    c: Coincident(g2,g3)
    c: Horizontal(g3)
    c: Vertical(g2)
    c: PointOnObject(g4,g0)
    c: DistanceY(g4,g5) = 1.7
    c: Angle(g0) = 0.523599
    c: Coincident(g5,g6)
    c: Vertical(g5)
    c: Vertical(g6)
    c: Coincident(g5,g4)
FEATURE [PartDesign::Pocket] Pocket018
  BaseFeature = -> BaseBend010
  Direction = (0,0,-1)
  Length = 5
  Length2 = 5
  Profile = -> Sketch033
  ReferenceAxis = -> Sketch033 [N_Axis]
  Suppressed = false
  Type = 1
FEATURE [PartDesign::Mirrored] Mirrored001
  BaseFeature = -> Pocket018
  MirrorPlane = -> Sketch033 [V_Axis]
  Originals = -> [Pocket018]
  Suppressed = false
FEATURE [Sketcher::SketchObject] Sketch034
  AttachmentSupport = -> [YZ_Plane025]
  ExternalGeometry = -> [Sketch033]
  FullyConstrained = false
  MapMode = 5
  Placement = pos=(0,0,0) rot=(0.57735,0.57735,0.57735;2.0944rad)
  sketch-geometry (4):
    g0: LineSegment StartX=6.63953 StartY=-25.0734 StartZ=0 EndX=22.8156 EndY=-25.0734 EndZ=0
    g1: LineSegment StartX=22.8156 StartY=-25.0734 StartZ=0 EndX=8.57047 EndY=-0.4 EndZ=0
    g2: LineSegment StartX=6.63953 StartY=-0.4 StartZ=0 EndX=6.63953 EndY=-25.0734 EndZ=0
    g3: LineSegment StartX=6.63953 StartY=-0.4 StartZ=0 EndX=8.57047 EndY=-0.4 EndZ=0
  constraints (11):
    c: Coincident(g2,g0)
    c: Horizontal(g0)
    c: Coincident(g0,g1)
    c: Vertical(g2)
    c: Coincident(g3,g2)
    c: Coincident(g3,g1)
    c: Horizontal(g3)
    c: Angle(g1) = 2.0944
    c: DistanceY(g2) = -0.4
    c: PointOnObject(g-3,g2)
    c: PointOnObject(g-3,g1)
FEATURE [PartDesign::Pocket] Pocket019
  BaseFeature = -> Mirrored001
  Direction = (-1,0,0)
  Length = 5
  Length2 = 5
  Midplane = true
  Profile = -> Sketch034
  ReferenceAxis = -> Sketch034 [N_Axis]
  Suppressed = false
  Type = 1
FEATURE [Sketcher::SketchObject] Sketch036
  AttachmentSupport = -> [XY_Plane025]
  FullyConstrained = true
  MapMode = 5
  sketch-geometry (1):
    g0: Circle CenterX=0 CenterY=25 CenterZ=0 NormalX=0 NormalY=0 NormalZ=1 AngleXU=0 Radius=3
  constraints (3):
    c: PointOnObject(g0,g-2)
    c: DistanceY(g0) = 25
    c: Diameter(g0) = 6
FEATURE [PartDesign::Pocket] Pocket021
  BaseFeature = -> Pocket019
  Direction = (0,0,-1)
  Length = 5
  Length2 = 5
  Profile = -> Sketch036
  ReferenceAxis = -> Sketch036 [N_Axis]
  Suppressed = false
  Type = 0
FEATURE [Sketcher::SketchObject] Sketch037
  AttachmentSupport = -> [XY_Plane028]
  FullyConstrained = false
  MapMode = 5
  sketch-geometry (2):
    g0: LineSegment StartX=0 StartY=0 StartZ=0 EndX=74.4649 EndY=59.2839 EndZ=0
    g1: LineSegment StartX=0 StartY=0 StartZ=0 EndX=-93.8109 EndY=73.3435 EndZ=0
  constraints (2):
    c: Coincident(g0,g-1)
    c: Coincident(g1,g0)
FEATURE [Part::Part2DObjectPython] Line  label="sink_bend_line"  # Draft 2D object (typed FeaturePython)
  Area = 0
  AttachmentOffset = pos=(304.73,175.936,20) rot=(0,0,1;0rad)
  AttachmentSupport = -> [XY_Plane028]
  BendAngle = 6.48542
  ChamferSize = 0
  Closed = false
  End = (0,0,0)
  FaceAngle = 3.2479
  FilletRadius = 0
  Length = 352.44
  MakeFace = true
  MapMode = 5
  Placement = pos=(304.73,175.936,20) rot=(0,0,1;0rad)
  Points = (2) [(0,0,0),(-304.73,-175.936,-20)]
  Start = (304.73,175.936,20)
  Subdivisions = 0
  expr: .AttachmentOffset.Base.x = Spreadsheet.total_length * cos(30)
  expr: .AttachmentOffset.Base.y = Spreadsheet.total_length * sin(30)
  expr: BendAngle = atan2(.AttachmentOffset.Base.z; .AttachmentOffset.Base.y)
  expr: End = tuple(0; 0; 0)
  expr: FaceAngle = atan2(.AttachmentOffset.Base.z; Length)
FEATURE [PartDesign::Line] DatumLine
  AttacherType = Attacher::AttachEngineLine
  AttachmentSupport = -> [Z_Axis028]
  Length = 20
  MapMode = 29
  ResizeMode = 0
FEATURE [PartDesign::Line] DatumLine001
  AttacherType = Attacher::AttachEngineLine
  AttachmentSupport = -> [Line,X_Axis028]
  Length = 20
  MapMode = 24
  Placement = pos=(304.73,175.936,20) rot=(0.57735,-0.57735,-0.57735;2.0944rad)
  ResizeMode = 0
FEATURE [Sketcher::SketchObject] Sketch038
  AttachmentSupport = -> [Line]
  ExternalGeometry = -> [DatumLine001]
  FullyConstrained = false
  MapMode = 45
  Placement = pos=(152.365,87.9679,10) rot=(0.368581,0.6384,0.675717;2.39766rad)
  sketch-geometry (3):
    g0: LineSegment StartX=4.75e-14 StartY=4.27e-14 StartZ=0 EndX=4.75e-14 EndY=93.8582 EndZ=0
    g1: LineSegment StartX=4.75e-14 StartY=4.27e-14 StartZ=0 EndX=35.2298 EndY=3.46271 EndZ=0
    g2: ArcOfCircle CenterX=2.5 CenterY=2.75777 CenterZ=0 NormalX=0 NormalY=0 NormalZ=1 AngleXU=0 Radius=2.5 StartAngle=3.14159 EndAngle=4.81036
  constraints (9):
    c: Coincident(g0,g-1)
    c: Vertical(g0)
    c: Coincident(g1,g0)
    c: PointOnObject(g1,g-3)
    c: Angle(g-3) = 0.0979746
    c: Angle(g1,g0) = 1.47282  'bend_angle'
    c: Tangent(g2,g0) = 1.5708
    c: Tangent(g2,g1) = -1.5708
    c: Radius(g2) = 2.5
FEATURE [PartDesign::CoordinateSystem] Local_CS
  AttacherType = Attacher::AttachEngine3D
  AttachmentOffset = pos=(0,0,0) rot=(1,0,0;0.113192rad)
  AttachmentSupport = -> [XY_Plane028]
  MapMode = 5
  Placement = pos=(0,0,0) rot=(1,0,0;0.113192rad)
  expr: .AttachmentOffset.Rotation.Angle = Line.BendAngle
FEATURE [Sketcher::SketchObject] Sketch039
  AttachmentSupport = -> [Local_CS]
  ExternalGeometry = -> [Line,Sketch038]
  FullyConstrained = true
  MapMode = 5
  Placement = pos=(0,0,0) rot=(1,0,0;0.113192rad)
  sketch-geometry (3):
    g0: LineSegment StartX=2e-16 StartY=3.18954 StartZ=0 EndX=-459.172 EndY=270 EndZ=0
    g1: LineSegment StartX=2e-16 StartY=3.18954 StartZ=0 EndX=459.172 EndY=270 EndZ=0
    g2: LineSegment StartX=459.172 StartY=270 StartZ=0 EndX=-459.172 EndY=270 EndZ=0
  constraints (8):
    c: Coincident(g2,g1)
    c: DistanceY(g1) = 270
    c: Coincident(g0,g2)
    c: Symmetric(g1,g0,g-2)
    c: Coincident(g1,g0)
    c: PointOnObject(g0,g-2)
    c: Parallel(g1,g-3)
    c: PointOnObject(g-4,g1)
FEATURE [PartDesign::FeaturePython] BaseBend011  # WARN: FeaturePython — macro-defined, semantics opaque (R4)
  BendSide = 0
  BendSketch = -> Sketch039
  MidPlane = false
  Reverse = false
  Suppressed = false
  length = 100
  radius = 2
  thickness = 0.5
FEATURE [PartDesign::FeaturePython] Bend004  # WARN: FeaturePython — macro-defined, semantics opaque (R4)
  AutoMiter = false
  BaseFeature = -> BaseBend011
  BendType = 0
  LengthList = [100]
  LengthSpec = 1
  ReliefFactor = 0.7
  Suppressed = false
  UseReliefFactor = false
  angle = 95.6135
  baseObject = -> BaseBend011 [Edge3,Edge8]
  bendAList = [95.6135]
  extend1 = 2
  extend2 = 0
  gap1 = 0
  gap2 = 0
  invert = true
  kfactor = 0.5
  length = 100
  maxExtendDist = 5
  minGap = 0.1
  minReliefGap = 1
  miterangle1 = 0
  miterangle2 = 0
  offset = 0
  radius = 2
  reliefType = 0
  reliefd = 1
  reliefw = 0.8
  sketchflip = false
  sketchinvert = false
  unfold = false
  expr: angle = 180 deg - Sketch038.Constraints.bend_angle
  expr: radius = BaseBend011.radius
FEATURE [Sketcher::SketchObject] Sketch040
  AttachmentSupport = -> [Local_CS]
  ExternalGeometry = -> [Line,Sketch038]
  FullyConstrained = true
  MapMode = 5
  Placement = pos=(0,0,0) rot=(1,0,0;0.113192rad)
  sketch-geometry (13):
    g0: ArcOfCircle CenterX=0 CenterY=-630 CenterZ=0 NormalX=0 NormalY=0 NormalZ=1 AngleXU=0 Radius=870 StartAngle=1.24863 EndAngle=1.89296
    g1: LineSegment StartX=0 StartY=0 StartZ=0 EndX=294.959 EndY=171.391 EndZ=0
    g2: LineSegment StartX=150.979 StartY=90.9189 StartZ=0 EndX=293.573 EndY=173.776 EndZ=0
    g3: LineSegment StartX=-294.959 StartY=171.391 StartZ=0 EndX=0 EndY=0 EndZ=0
    g4: LineSegment StartX=-294.959 StartY=171.391 StartZ=0 EndX=-464.661 EndY=270 EndZ=0
    g5: LineSegment StartX=-464.661 StartY=270 StartZ=0 EndX=464.661 EndY=270 EndZ=0
    g6: LineSegment StartX=464.661 StartY=270 StartZ=0 EndX=294.959 EndY=171.391 EndZ=0
    g7: LineSegment StartX=294.959 StartY=171.391 StartZ=0 EndX=294.075 EndY=172.911 EndZ=0
    g8: LineSegment StartX=294.075 StartY=172.911 StartZ=0 EndX=293.573 EndY=173.776 EndZ=0
    g9: LineSegment StartX=-294.959 StartY=171.391 StartZ=0 EndX=-294.959 EndY=171.391 EndZ=0
    g10: LineSegment StartX=293.573 StartY=173.776 StartZ=0 EndX=275.46 EndY=195.241 EndZ=0
    g11: LineSegment StartX=-293.573 StartY=173.776 StartZ=0 EndX=-275.46 EndY=195.241 EndZ=0
    g12: LineSegment StartX=-294.959 StartY=171.391 StartZ=0 EndX=-293.573 EndY=173.776 EndZ=0
  constraints (34):
    c: Coincident(g1,g-1)
    c: PointOnObject(g1,g-3)
    c: Coincident(g7,g1)
    c: Distance(g1) = 341.139
    c: Coincident(g2,g-4)
    c: Parallel(g2,g1)
    c: DistanceY(g0) = -630
    c: Radius(g0) = 870
    c: Coincident(g9,g3)
    c: Coincident(g3,g1)
    c: Symmetric(g9,g7,g-2)
    c: Coincident(g4,g5)
    c: Coincident(g5,g6)
    c: Parallel(g6,g2)
    c: Symmetric(g5,g4,g-2)
    c: DistanceY(g5) = 270
    c: Coincident(g2,g8)
    c: Coincident(g7,g8)
    c: Perpendicular(g1,g7)
    c: Perpendicular(g1,g8)
    c: Distance(g8) = 1
    c: Coincident(g10,g0)
    c: Coincident(g11,g0)
    c: PointOnObject(g0,g-2)
    c: Coincident(g10,g8)
    c: Coincident(g12,g9)
    c: Coincident(g4,g12)
    c: Coincident(g12,g11)
    c: Symmetric(g4,g6,g-2)
    c: Symmetric(g8,g11,g-2)
    c: Horizontal(g0,g0)
    c: Distance(g10) = 28.0862
    c: Angle(g10,g2) = 1.39626
    c: Coincident(g6,g7)
FEATURE [PartDesign::SubShapeBinder] Binder031
  BindCopyOnChange = 0
  BindMode = 0
  ClaimChildren = false
  Context = -> Part007 [Body020.Binder031.]
  Fuse = false
  MakeFace = true
  OffsetFill = false
  OffsetIntersection = false
  OffsetJoinType = 0
  OffsetOpenResult = false
  PartialLoad = false
  Relative = true
  _Version = 2
FEATURE [PartDesign::Pocket] Pocket022
  BaseFeature = -> Bend004
  Direction = (0,0.11295,-0.993601)
  Length = 2.5
  Length2 = 5
  Profile = -> Sketch040
  ReferenceAxis = -> Sketch040 [N_Axis]
  Refine = true
  Reversed = true
  Suppressed = false
  Type = 0
FEATURE [Sketcher::SketchObject] Sketch042
  AttachmentSupport = -> [XY_Plane028]
  FullyConstrained = true
  MapMode = 5
  sketch-geometry (7):
    g0: LineSegment StartX=-18.3205 StartY=-10 StartZ=0 EndX=-0.5 EndY=0.288675 EndZ=0
    g1: LineSegment StartX=18.3205 StartY=-10 StartZ=0 EndX=-18.3205 EndY=-10 EndZ=0
    g2: LineSegment StartX=1 StartY=1.5e-15 StartZ=0 EndX=-1e-16 EndY=0.57735 EndZ=0
    g3: LineSegment StartX=1.3e-15 StartY=-2.2e-15 StartZ=0 EndX=0.5 EndY=0.288675 EndZ=0
    g4: LineSegment StartX=0.5 StartY=0.288675 StartZ=0 EndX=18.3205 EndY=-10 EndZ=0
    g5: LineSegment StartX=-2.6e-15 StartY=1.1547 StartZ=0 EndX=0.5 EndY=0.288675 EndZ=0
    g6: LineSegment StartX=-0.5 StartY=0.288675 StartZ=0 EndX=-2.6e-15 EndY=1.1547 EndZ=0
  constraints (19):
    c: Coincident(g4,g1)
    c: Coincident(g1,g0)
    c: Symmetric(g4,g0,g-2)
    c: PointOnObject(g2,g-1)
    c: PointOnObject(g2,g-2)
    c: Angle(g2) = 2.61799
    c: Distance(g-1,g2) = 0.5
    c: Coincident(g3,g-1)
    c: PointOnObject(g3,g2)
    c: Angle(g3) = 0.523599
    c: PointOnObject(g2,g4)
    c: Perpendicular(g3,g5)
    c: Coincident(g4,g5)
    c: Coincident(g4,g3)
    c: PointOnObject(g5,g-2)
    c: Coincident(g6,g0)
    c: Coincident(g6,g5)
    c: Symmetric(g4,g0,g-2)
    c: DistanceY(g1) = -10
FEATURE [Sketcher::SketchObject] Sketch041
  AttachmentOffset = pos=(0,0,0) rot=(0,1,0;0.523599rad)
  AttachmentSupport = -> [XZ_Plane028]
  ExternalGeometry = -> [Sketch038,Sketch042,Sketch040]
  FullyConstrained = false
  MapMode = 5
  Placement = pos=(0,0,0) rot=(0.935113,0.250563,0.250563;1.63783rad)
  sketch-geometry (16):
    g0: LineSegment StartX=340.573 StartY=19.628 StartZ=0 EndX=340.432 EndY=22.112 EndZ=0
    g1: LineSegment StartX=175.779 StartY=12.7533 StartZ=0 EndX=340.432 EndY=22.112 EndZ=0
    g2: LineSegment StartX=0.57735 StartY=196.491 StartZ=0 EndX=638.392 EndY=196.491 EndZ=0
    g3: LineSegment StartX=638.392 StartY=196.491 StartZ=0 EndX=638.392 EndY=36.5557 EndZ=0
    g4: LineSegment StartX=638.392 StartY=36.5557 StartZ=0 EndX=340.573 EndY=19.628 EndZ=0
    g5: LineSegment StartX=340.432 StartY=22.112 StartZ=0 EndX=340.432 EndY=85 EndZ=0
    g6: LineSegment StartX=0.57735 StartY=85 StartZ=0 EndX=0.57735 EndY=196.491 EndZ=0
    g7: LineSegment StartX=335.432 StartY=90 StartZ=0 EndX=5.57735 EndY=90 EndZ=0
    g8: ArcOfCircle CenterX=5.57735 CenterY=85 CenterZ=0 NormalX=0 NormalY=0 NormalZ=1 AngleXU=0 Radius=5 StartAngle=1.5708 EndAngle=3.14159
    g9: ArcOfCircle CenterX=335.432 CenterY=85 CenterZ=0 NormalX=0 NormalY=0 NormalZ=1 AngleXU=0 Radius=5 StartAngle=2e-16 EndAngle=1.5708
    g10: GeomPoint X=340.432 Y=90 Z=0
    g11: LineSegment StartX=0.57735 StartY=0 StartZ=0 EndX=0.57735 EndY=27.6603 EndZ=0
    g12: ArcOfCircle CenterX=5 CenterY=27.6603 CenterZ=0 NormalX=0 NormalY=0 NormalZ=1 AngleXU=0 Radius=4.42265 StartAngle=3.14159 EndAngle=4.18879
    g13: ArcOfCircle CenterX=0.57735 CenterY=20 CenterZ=0 NormalX=0 NormalY=0 NormalZ=1 AngleXU=0 Radius=4.42265 StartAngle=-2.31e-14 EndAngle=1.0472
    g14: LineSegment StartX=5 StartY=20 StartZ=0 EndX=5 EndY=0 EndZ=0
    g15: LineSegment StartX=5 StartY=0 StartZ=0 EndX=0.57735 EndY=0 EndZ=0
  constraints (39):
    c: Coincident(g1,g-3)
    c: Coincident(g1,g0)
    c: Perpendicular(g-3,g1)
    c: Perpendicular(g1,g0)
    c: Coincident(g5,g0)
    c: Coincident(g6,g2)
    c: Horizontal(g2)
    c: Coincident(g2,g3)
    c: Vertical(g3)
    c: Coincident(g3,g4)
    c: Coincident(g4,g0)
    c: Parallel(g4,g1)
    c: Vertical(g5)
    c: Vertical(g6)
    c: Vertical(g6,g-4)
    c: Horizontal(g7)
    c: Tangent(g8,g7) = -1.5708
    c: Tangent(g8,g6) = 1.5708
    c: PointOnObject(g10,g5)
    c: PointOnObject(g10,g7)
    c: Tangent(g5,g9) = -1.5708
    c: Tangent(g7,g9) = -1.5708
    c: Equal(g9,g8)
    c: Coincident(g11,g-4)
    c: Vertical(g11)
    c: PointOnObject(g13,g11)
    c: PointOnObject(g14,g-1)
    c: Vertical(g14)
    c: Coincident(g15,g14)
    c: Coincident(g15,g11)
    c: Tangent(g13,g12) = 1.5708
    c: Tangent(g12,g11) = 1.5708
    c: Tangent(g14,g13) = 1.5708
    c: Equal(g13,g12)
    c: DistanceX(g14) = 5
    c: DistanceY(g13) = 20
    c: DistanceY(g7) = 90
    c: Radius(g9) = 5
    c: Coincident(g0,g-5)
FEATURE [Sketcher::SketchObject] Sketch043
  AttachmentSupport = -> [Local_CS]
  FullyConstrained = false
  MapMode = 5
  Placement = pos=(0,0,0) rot=(1,0,0;0.113192rad)
  expr: Constraints[12] = Sketch038.Constraints.bend_angle / 2
  sketch-geometry (7):
    g0: ArcOfCircle CenterX=-2.2e-14 CenterY=1.72e-14 CenterZ=0 NormalX=0 NormalY=0 NormalZ=1 AngleXU=0 Radius=19.4106 StartAngle=5.52221 EndAngle=10.1858
    g1: ArcOfCircle CenterX=17.4885 CenterY=-16.6545 CenterZ=0 NormalX=0 NormalY=0 NormalZ=1 AngleXU=0 Radius=4.73935 StartAngle=2.38062 EndAngle=3.72466
    g2: ArcOfCircle CenterX=-17.4885 CenterY=-16.6545 CenterZ=0 NormalX=0 NormalY=0 NormalZ=1 AngleXU=0 Radius=4.73935 StartAngle=5.70012 EndAngle=7.04416
    g3: LineSegment StartX=13.5322 StartY=-19.2639 StartZ=0 EndX=49.1398 EndY=-73.2508 EndZ=0
    g4: LineSegment StartX=-13.5322 StartY=-19.2639 StartZ=0 EndX=-49.1398 EndY=-73.2508 EndZ=0
    g5: LineSegment StartX=-49.1398 StartY=-73.2508 StartZ=0 EndX=49.1398 EndY=-73.2508 EndZ=0
    g6: LineSegment StartX=-86.3387 StartY=-141.994 StartZ=0 EndX=130.665 EndY=54.7259 EndZ=0
  constraints (13):
    c: Coincident(g0,g-1)
    c: Coincident(g5,g4)
    c: Coincident(g5,g3)
    c: Tangent(g3,g1) = -1.5708
    c: Tangent(g1,g0) = 1.5708
    c: Tangent(g2,g0) = 1.5708
    c: Tangent(g4,g2) = 1.5708
    c: Symmetric(g4,g3,g-2)
    c: Symmetric(g2,g1,g-2)
    c: DistanceX(g1) = 13.5322
    c: DistanceY(g1) = -19.2639
    c: Angle(g3) = -0.987729
    c: Angle(g6) = 0.736411
FEATURE [Sketcher::SketchObject] Sketch044
  AttachmentSupport = -> [YZ_Plane]
  ExternalGeometry = -> [Binder]
  FullyConstrained = false
  MapMode = 5
  Placement = pos=(0,0,0) rot=(0.57735,0.57735,0.57735;2.0944rad)
  expr: Constraints[16] = <<Properties>>.total_height
  expr: Constraints[23] = composit_properties#<<Properties>>.bend_r
  expr: Constraints[33] = <<Properties>>.petal_offset
  sketch-geometry (12):
    g0: LineSegment StartX=-41.6284 StartY=0 StartZ=0 EndX=4.96521 EndY=0 EndZ=0
    g1: LineSegment StartX=4.96521 StartY=0 StartZ=0 EndX=4.96521 EndY=512 EndZ=0
    g2: LineSegment StartX=4.96521 StartY=512 StartZ=0 EndX=-41.6284 EndY=512 EndZ=0
    g3: LineSegment StartX=-41.6284 StartY=512 StartZ=0 EndX=-41.6284 EndY=0 EndZ=0
    g4: LineSegment StartX=-41.6284 StartY=1428 StartZ=0 EndX=8.37158 EndY=1428 EndZ=0
    g5: LineSegment StartX=4.96521 StartY=1354 StartZ=0 EndX=-41.6284 EndY=1354 EndZ=0
    g6: LineSegment StartX=-41.6284 StartY=1354 StartZ=0 EndX=-41.6284 EndY=1428 EndZ=0
    g7: ArcOfCircle CenterX=4.96521 CenterY=0.1 CenterZ=0 NormalX=0 NormalY=0 NormalZ=1 AngleXU=0 Radius=0.1 StartAngle=3.66519 EndAngle=4.71239
    g8: LineSegment StartX=4.96521 StartY=0 StartZ=0 EndX=6.6679 EndY=0 EndZ=0
    g9: LineSegment StartX=4.87861 StartY=0.05 StartZ=0 EndX=2.02073 EndY=5 EndZ=0
    g10: LineSegment StartX=8.37158 StartY=1428 StartZ=0 EndX=4.96521 EndY=1424.59 EndZ=0
    g11: LineSegment StartX=4.96521 StartY=1424.59 StartZ=0 EndX=4.96521 EndY=1354 EndZ=0
  constraints (35):
    c: Coincident(g0,g1)
    c: Coincident(g1,g2)
    c: Coincident(g2,g3)
    c: Coincident(g3,g0)
    c: Horizontal(g0)
    c: Horizontal(g2)
    c: Vertical(g1)
    c: Vertical(g3)
    c: PointOnObject(g0,g-1)
    c: Coincident(g4,g10)
    c: Coincident(g11,g5)
    c: Coincident(g5,g6)
    c: Coincident(g6,g4)
    c: Horizontal(g4)
    c: Horizontal(g5)
    c: Vertical(g6)
    c: DistanceY(g4) = 1428
    c: DistanceY(g11,g10) = 74
    c: PointOnObject(g7,g-1)
    c: PointOnObject(g8,g-1)
    c: Tangent(g8,g7) = -1.5708
    c: Tangent(g9,g7) = 1.5708
    c: Angle(g9) = 2.0944
    c: Radius(g7) = 0.1
    c: PointOnObject(g-3,g9)
    c: DistanceY(g9) = 5
    c: PointOnObject(g7,g1)
    c: DistanceY(g1,g11) = 842
    c: Vertical(g2,g5)
    c: DistanceX(g4,g4) = 50
    c: Coincident(g10,g11)
    c: Vertical(g11)
    c: Angle(g10) = -2.35619
    c: DistanceX(g4) = 8.37158
    c: Vertical(g5,g1)
FEATURE [Sketcher::SketchObject] Sketch045
  AttachmentSupport = -> [YZ_Plane025]
  FullyConstrained = true
  MapMode = 5
  Placement = pos=(0,0,0) rot=(0.57735,0.57735,0.57735;2.0944rad)
  expr: Constraints[0] = <<BaseBend010>>.length
  sketch-geometry (5):
    g0: ArcOfCircle CenterX=30 CenterY=-7 CenterZ=0 NormalX=0 NormalY=0 NormalZ=1 AngleXU=0 Radius=5 StartAngle=4.71239 EndAngle=6.28319
    g1: LineSegment StartX=35 StartY=-7 StartZ=0 EndX=35 EndY=-25 EndZ=0
    g2: LineSegment StartX=30 StartY=-12 StartZ=0 EndX=0 EndY=-12 EndZ=0
    g3: LineSegment StartX=35 StartY=-25 StartZ=0 EndX=0 EndY=-25 EndZ=0
    g4: LineSegment StartX=0 StartY=-25 StartZ=0 EndX=0 EndY=-12 EndZ=0
  constraints (14):
    c: DistanceX(g0) = 35
    c: Vertical(g1)
    c: Tangent(g1,g0) = 1.5708
    c: PointOnObject(g2,g-2)
    c: Horizontal(g2)
    c: Coincident(g3,g1)
    c: PointOnObject(g3,g-2)
    c: Horizontal(g3)
    c: Coincident(g4,g3)
    c: Coincident(g4,g2)
    c: Tangent(g2,g0) = 1.5708
    c: DistanceY(g0) = -7
    c: DistanceY(g3) = -25
    c: Radius(g0) = 5
FEATURE [PartDesign::Pocket] Pocket026
  BaseFeature = -> Pocket021
  Direction = (-1,0,0)
  Length = 5
  Length2 = 5
  Midplane = true
  Profile = -> Sketch045
  ReferenceAxis = -> Sketch045 [N_Axis]
  Suppressed = false
  Type = 1
FEATURE [Part::Part2DObjectPython] Circle  label="hole3.4mm"  # Draft 2D object (typed FeaturePython)
  Area = 0
  FirstAngle = 0
  LastAngle = 0
  MakeFace = false
  Placement = pos=(0,0,0) rot=(0,0,1;1.5708rad)
  Radius = 1.7
  expr: Radius = <<Properties>>.rivet_d / 2
FEATURE [Part::FeaturePython] LinearArray005  label="leg_amplifier_fix"  # WARN: FeaturePython — macro-defined, semantics opaque (R4)
  Alignment = 0
  CellStart = A1
  Count = 3
  Dir = (1,0,0)
  DirIsDriven = true
  DistributionLaw = 0
  DrivenProperty = 1
  EndInclusive = true
  ExposePlacement = false
  GeneratorMode = 0
  MarkerShape = 1
  MarkerSize = 0
  NumElements = 3
  OrientMode = 1
  Point = (0,0,0)
  PointIsDriven = true
  Reverse = false
  SpanEnd = 390
  SpanStart = 20
  Step = 185
  Type = lattice2LinearArray.LinearArray
  VSGVersion = 1
  Values = 20.0 | 205.0 | 390.0
  ValuesSource = 2
  isLattice = 1
FEATURE [Part::FeaturePython] Populate007  label="Populate leg_amplifier_fix with hole3.4mm"  # WARN: FeaturePython — macro-defined, semantics opaque (R4)
  Copying = 0
  ExposePlacement = false
  MarkerShape = 1
  MarkerSize = 0
  NumElements = 0
  Object = -> Circle
  OutputCompounding = 1
  PlacementsTo = -> LinearArray005
  Referencing = 0
  Type = lattice2PopulateCopies.LatticePopulateCopies
  isLattice = 0
FEATURE [Part::FeaturePython] LinearArray006  label="part_connector_array"  # WARN: FeaturePython — macro-defined, semantics opaque (R4)
  Alignment = 0
  CellStart = A1
  Count = 5
  Dir = (1,0,0)
  DirIsDriven = true
  DistributionLaw = 0
  DrivenProperty = 1
  EndInclusive = true
  ExposePlacement = false
  GeneratorMode = 0
  MarkerShape = 1
  MarkerSize = 0
  NumElements = 5
  OrientMode = 1
  Point = (0,0,0)
  PointIsDriven = true
  Reverse = false
  SpanEnd = 820
  SpanStart = 0
  Step = 205
  Type = lattice2LinearArray.LinearArray
  VSGVersion = 1
  Values = 0.0 | 205.0 | 410.0 | 615.0 | 820.0
  ValuesSource = 2
  isLattice = 1
FEATURE [Part::FeaturePython] Populate008  label="Populate part_connector with hole3.4mm"  # WARN: FeaturePython — macro-defined, semantics opaque (R4)
  Copying = 0
  ExposePlacement = false
  MarkerShape = 1
  MarkerSize = 0
  NumElements = 0
  Object = -> Circle
  OutputCompounding = 1
  PlacementsTo = -> LinearArray006
  Referencing = 0
  Type = lattice2PopulateCopies.LatticePopulateCopies
  isLattice = 0
FEATURE [Part::Extrusion] Extrude002  label="part_connector_extrude"
  Base = -> Populate008
  Dir = (0,0,1)
  DirMode = 2
  FaceMakerClass = Part::FaceMakerBullseye
  LengthFwd = 10
  LengthRev = 0
  Placement = pos=(21,-5,1343) rot=(-0.447204,0.774607,0.447204;1.82348rad)
  Solid = true
  Symmetric = false
  expr: .Placement.Base.z = <<Properties>>.total_height - 85 mm
FEATURE [Part::Mirroring] Part__Mirroring009  label="part_connector_extrude (Mirror #10)"
  Base = (0,0,0)
  Normal = (1,0,-1.19209e-07)
  Source = -> Extrude002
FEATURE [Part::Compound] Compound015  label="part_connector"
  Links = -> [Part__Mirroring009,Extrude002]
FEATURE [Part::Extrusion] Extrude003  label="star_amplifier_holes_extrude"
  Base = -> Circle
  Dir = (0,0,1)
  DirMode = 2
  FaceMakerClass = Part::FaceMakerBullseye
  LengthFwd = 29
  LengthRev = 0
  Placement = pos=(0,19,-7) rot=(0,1,0;1.5708rad)
  Solid = true
  Symmetric = true
  expr: LengthFwd = <<Properties>>.endface_width
FEATURE [Part::Extrusion] Extrude004  label=" leg_amplifier_extrude"
  Base = -> Populate007
  Dir = (0,0,1)
  DirMode = 2
  FaceMakerClass = Part::FaceMakerBullseye
  LengthFwd = 14.5
  LengthRev = 0
  Placement = pos=(0,245,0) rot=(0,-1,0;1.5708rad)
  Solid = true
  Symmetric = false
  expr: LengthFwd = <<Properties>>.endface_width / 2
FEATURE [Part::FeaturePython] Mirror  label="Mirror of  leg_amplifier_extrude"  # WARN: FeaturePython — macro-defined, semantics opaque (R4)
  ExposePlacement = false
  FlipX = true
  FlipY = false
  FlipZ = false
  MarkerShape = 1
  MarkerSize = 0
  NumElements = 0
  Object = -> Extrude004
  ObjectTraversal = 0
  PivotPlacement = pos=(0,0,0) rot=(0,0,1;4.18879rad)
  Type = lattice2Mirror.LatticeMirror
  isLattice = 0
FEATURE [Part::Compound] Compound018  label="leg_fix_2"
  Links = -> [Extrude004,Mirror]
  Placement = pos=(0,0,0) rot=(0,0,1;2.0944rad)
FEATURE [Part::FeaturePython] LinearArray007  label="plexiglass_bottom_fix_array"  # WARN: FeaturePython — macro-defined, semantics opaque (R4)
  Alignment = 0
  CellStart = A1
  Count = 4
  Dir = (1,0,0)
  DirIsDriven = true
  DistributionLaw = 0
  DrivenProperty = 1
  EndInclusive = true
  ExposePlacement = false
  GeneratorMode = 0
  MarkerShape = 1
  MarkerSize = 0
  NumElements = 4
  OrientMode = 1
  Point = (0,0,0)
  PointIsDriven = true
  Reverse = false
  SpanEnd = 390
  SpanStart = 35
  Step = 118.333
  Type = lattice2LinearArray.LinearArray
  VSGVersion = 1
  Values = 35.0 | 153.33333333333331 | 271.66666666666663 | 390.0
  ValuesSource = 2
  isLattice = 1
FEATURE [Sketcher::SketchObject] Sketch046  label="plexiglass_bottom_fix_sketch"
  FullyConstrained = true
  sketch-geometry (5):
    g0: LineSegment StartX=-26 StartY=1.6 StartZ=0 EndX=-26 EndY=-1.6 EndZ=0
    g1: LineSegment StartX=-26 StartY=-1.6 StartZ=0 EndX=26 EndY=-1.6 EndZ=0
    g2: LineSegment StartX=26 StartY=-1.6 StartZ=0 EndX=26 EndY=1.6 EndZ=0
    g3: LineSegment StartX=26 StartY=1.6 StartZ=0 EndX=-26 EndY=1.6 EndZ=0
    g4: GeomPoint X=0 Y=0 Z=0
  constraints (12):
    c: Coincident(g0,g1)
    c: Coincident(g1,g2)
    c: Coincident(g2,g3)
    c: Coincident(g3,g0)
    c: Horizontal(g1)
    c: Horizontal(g3)
    c: Vertical(g0)
    c: Vertical(g2)
    c: Symmetric(g1,g0,g4)
    c: Coincident(g4,g-1)
    c: DistanceY(g2,g2) = 3.2  'width'
    c: DistanceX(g3,g3) = 52  'length'
FEATURE [Part::FeaturePython] Populate009  label="Populate plexiglass_bottom_fix_array with plexiglass_bottom_fix_sketch"  # WARN: FeaturePython — macro-defined, semantics opaque (R4)
  Copying = 0
  ExposePlacement = false
  MarkerShape = 1
  MarkerSize = 0
  NumElements = 0
  Object = -> Sketch046
  OutputCompounding = 1
  PlacementsTo = -> LinearArray007
  Referencing = 0
  Type = lattice2PopulateCopies.LatticePopulateCopies
  isLattice = 0
FEATURE [Part::Extrusion] Extrude005  label="plexiglass_bottom_fix_extrude"
  Base = -> Populate009
  Dir = (0,0,1)
  DirMode = 2
  FaceMakerClass = Part::FaceMakerBullseye
  LengthFwd = 14.5
  LengthRev = 0
  Placement = pos=(0,336,0) rot=(0,-1,0;1.5708rad)
  Solid = true
  Symmetric = false
  expr: LengthFwd = <<Properties>>.endface_width / 2
FEATURE [Part::FeaturePython] Mirror001  label="Mirror001 of plexiglass_bottom_fix_extrude"  # WARN: FeaturePython — macro-defined, semantics opaque (R4)
  ExposePlacement = false
  FlipX = true
  FlipY = false
  FlipZ = false
  MarkerShape = 1
  MarkerSize = 0
  NumElements = 0
  Object = -> Extrude005
  ObjectTraversal = 0
  PivotPlacement = pos=(0,0,0) rot=(0,0,1;2.0944rad)
  Type = lattice2Mirror.LatticeMirror
  isLattice = 0
FEATURE [Part::FeaturePython] Mirror002  label="Mirror002 of plexiglass_bottom_fix_extrude"  # WARN: FeaturePython — macro-defined, semantics opaque (R4)
  ExposePlacement = false
  FlipX = true
  FlipY = false
  FlipZ = false
  MarkerShape = 1
  MarkerSize = 0
  NumElements = 0
  Object = -> Extrude005
  ObjectTraversal = 0
  Type = lattice2Mirror.LatticeMirror
  isLattice = 0
FEATURE [Part::Compound] Compound020
  Links = -> [Extrude005]
  Placement = pos=(0,0,0) rot=(0,0,1;4.18879rad)
FEATURE [Part::Compound] Compound019  label="plexiglass_bottom_fix"
  Links = -> [Mirror001,Mirror002,Compound020]
  Placement = pos=(0,0,0) rot=(0,0,1;4.18879rad)
FEATURE [Part::FeaturePython] LinearArray008  label="top_fix_array"  # WARN: FeaturePython — macro-defined, semantics opaque (R4)
  Alignment = 0
  CellStart = A1
  Count = 3
  Dir = (1,0,0)
  DirIsDriven = true
  DistributionLaw = 0
  DrivenProperty = 1
  EndInclusive = true
  ExposePlacement = false
  GeneratorMode = 0
  MarkerShape = 1
  MarkerSize = 0
  NumElements = 3
  OrientMode = 1
  Placement = pos=(-135.5,0,0) rot=(0,0,1;0rad)
  Point = (0,0,0)
  PointIsDriven = true
  Reverse = false
  SpanEnd = 271
  SpanStart = 0
  Step = 135.5
  Type = lattice2LinearArray.LinearArray
  VSGVersion = 1
  Values = 0.0 | 135.5 | 271.0
  ValuesSource = 2
  isLattice = 1
  expr: .Placement.Base.x = -SpanEnd / 2
FEATURE [Part::FeaturePython] Populate010  label="Populate top_fix_array with hole3.4mm"  # WARN: FeaturePython — macro-defined, semantics opaque (R4)
  Copying = 0
  ExposePlacement = false
  MarkerShape = 1
  MarkerSize = 0
  NumElements = 0
  Object = -> Circle
  OutputCompounding = 1
  PlacementsTo = -> LinearArray008
  Referencing = 0
  Type = lattice2PopulateCopies.LatticePopulateCopies
  isLattice = 0
FEATURE [Part::Extrusion] Extrude006  label="top_fix_extrude"
  Base = -> Populate010
  Dir = (0,0,1)
  DirMode = 2
  FaceMakerClass = Part::FaceMakerBullseye
  LengthFwd = 29
  LengthRev = 0
  Placement = pos=(0,178.372,-7) rot=(0.57735,0.57735,0.57735;2.0944rad)
  Solid = true
  Symmetric = true
  expr: .Placement.Base.y = <<Properties>>.plane_middle - 3 mm
  expr: LengthFwd = <<Properties>>.endface_width
FEATURE [Part::Compound] Compound022  label="top_fix2"
  Links = -> [Extrude006]
  Placement = pos=(0,0,1428) rot=(0,0,1;0rad)
  expr: .Placement.Base.z = <<Properties>>.total_height
FEATURE [Sketcher::SketchObject] Sketch047
  FullyConstrained = true
  expr: Constraints[14] = <<Properties>>.rivet_d
  sketch-geometry (8):
    g0: LineSegment StartX=22.7472 StartY=52 StartZ=0 EndX=340 EndY=52 EndZ=0
    g1: LineSegment StartX=340 StartY=52 StartZ=0 EndX=340 EndY=102 EndZ=0
    g2: LineSegment StartX=340 StartY=102 StartZ=0 EndX=22.7472 EndY=102 EndZ=0
    g3: LineSegment StartX=22.7472 StartY=102 StartZ=0 EndX=22.7472 EndY=52 EndZ=0
    g4: Circle CenterX=22.7472 CenterY=52 CenterZ=0 NormalX=0 NormalY=0 NormalZ=1 AngleXU=0 Radius=1.7
    g5: Circle CenterX=22.7472 CenterY=102 CenterZ=0 NormalX=0 NormalY=0 NormalZ=1 AngleXU=0 Radius=1.7
    g6: Circle CenterX=340 CenterY=102 CenterZ=0 NormalX=0 NormalY=0 NormalZ=1 AngleXU=0 Radius=1.7
    g7: Circle CenterX=340 CenterY=52 CenterZ=0 NormalX=0 NormalY=0 NormalZ=1 AngleXU=0 Radius=1.7
  constraints (20):
    c: Coincident(g0,g1)
    c: Coincident(g1,g2)
    c: Coincident(g2,g3)
    c: Coincident(g3,g0)
    c: Horizontal(g2)
    c: Vertical(g1)
    c: Vertical(g3)
    c: Coincident(g4,g0)
    c: Coincident(g5,g2)
    c: Coincident(g6,g1)
    c: Coincident(g7,g0)
    c: Equal(g4,g5)
    c: Equal(g4,g6)
    c: Equal(g4,g7)
    c: Diameter(g4) = 3.4
    c: DistanceX(g4) = 22.7472
    c: DistanceY(g4) = 52
    c: DistanceY(g5) = 102
    c: DistanceX(g7) = 340
    c: DistanceY(g7) = 52
FEATURE [Part::Extrusion] Extrude007  label="sink_fix_extrude"
  Base = -> Sketch047
  Dir = (0,0,1)
  DirMode = 2
  FaceMakerClass = Part::FaceMakerBullseye
  LengthFwd = 34
  LengthRev = 0
  Placement = pos=(0,0,0) rot=(0.57735,0.57735,0.57735;2.0944rad)
  Solid = true
  Symmetric = true
  expr: LengthFwd = <<Properties>>.endface_width + 5 mm
FEATURE [Part::Compound] Compound024  label="part1_cut2"
  Links = -> [Extrude004]
FEATURE [Part::Compound] Compound025  label="part2_cut2"
  Links = -> [Compound018]
FEATURE [Part::Compound] Compound026  label="part1_fuse1"
  Links = -> [BaseBend002]
FEATURE [Sketcher::SketchObject] Sketch048
  AttachmentSupport = -> [YZ_Plane024]
  FullyConstrained = true
  MapMode = 5
  Placement = pos=(0,0,0) rot=(0.57735,0.57735,0.57735;2.0944rad)
  expr: Constraints[5] = -<<top_connector_base_sketch>>.Constraints.height
  expr: Constraints[7] = -<<top_connector_base_sketch>>.AttachmentOffset.Base.z
  sketch-geometry (3):
    g0: ArcOfCircle CenterX=42 CenterY=-6 CenterZ=0 NormalX=0 NormalY=0 NormalZ=1 AngleXU=0 Radius=7 StartAngle=3.14159 EndAngle=4.71239
    g1: LineSegment StartX=42 StartY=-13 StartZ=0 EndX=35 EndY=-13 EndZ=0
    g2: LineSegment StartX=35 StartY=-6 StartZ=0 EndX=35 EndY=-13 EndZ=0
  constraints (8):
    c: Horizontal(g1)
    c: Coincident(g2,g1)
    c: Vertical(g2)
    c: Tangent(g1,g0) = 1.5708
    c: Tangent(g2,g0) = -1.5708
    c: DistanceY(g1) = -13
    c: DistanceY(g0) = -6
    c: DistanceX(g1) = 35
FEATURE [Part::FeaturePython] LinearArray009  label="bot_hor_amplifier_fix_array"  # WARN: FeaturePython — macro-defined, semantics opaque (R4)
  Alignment = 0
  CellStart = A1
  Count = 3
  Dir = (1,0,0)
  DirIsDriven = true
  DistributionLaw = 0
  DrivenProperty = 1
  EndInclusive = true
  ExposePlacement = false
  GeneratorMode = 0
  MarkerShape = 1
  MarkerSize = 0
  NumElements = 3
  OrientMode = 1
  Placement = pos=(-120,0,0) rot=(0,0,1;0rad)
  Point = (0,0,0)
  PointIsDriven = true
  Reverse = false
  SpanEnd = 240
  SpanStart = 0
  Step = 120
  Type = lattice2LinearArray.LinearArray
  VSGVersion = 1
  Values = 0.0 | 120.0 | 240.0
  ValuesSource = 2
  isLattice = 1
  expr: .Placement.Base.x = -SpanEnd / 2
FEATURE [Part::FeaturePython] Populate011  label="Populate bot_hor_amplifier_fix_array with hole3.4mm"  # WARN: FeaturePython — macro-defined, semantics opaque (R4)
  Copying = 0
  ExposePlacement = false
  MarkerShape = 1
  MarkerSize = 0
  NumElements = 0
  Object = -> Circle
  OutputCompounding = 1
  PlacementsTo = -> LinearArray009
  Referencing = 0
  Type = lattice2PopulateCopies.LatticePopulateCopies
  isLattice = 0
FEATURE [Sketcher::SketchObject] Sketch049
  AttachmentSupport = -> [YZ_Plane030]
  FullyConstrained = true
  MapMode = 5
  Placement = pos=(0,0,0) rot=(0.57735,0.57735,0.57735;2.0944rad)
  expr: Constraints[11] = <<Properties>>.inner_width
  sketch-geometry (5):
    g0: LineSegment StartX=-11.5 StartY=-14 StartZ=0 EndX=-11.5 EndY=0 EndZ=0
    g1: LineSegment StartX=-11.5 StartY=0 StartZ=0 EndX=11.5 EndY=0 EndZ=0
    g2: LineSegment StartX=11.5 StartY=0 StartZ=0 EndX=11.5 EndY=-14 EndZ=0
    g3: LineSegment StartX=11.5 StartY=-14 StartZ=0 EndX=-11.5 EndY=-14 EndZ=0
    g4: GeomPoint X=0 Y=-7 Z=0
  constraints (13):
    c: Coincident(g0,g1)
    c: Coincident(g1,g2)
    c: Coincident(g2,g3)
    c: Coincident(g3,g0)
    c: Horizontal(g1)
    c: Horizontal(g3)
    c: Vertical(g0)
    c: Vertical(g2)
    c: Symmetric(g1,g0,g4)
    c: PointOnObject(g4,g-2)
    c: PointOnObject(g1,g-1)
    c: DistanceX(g1,g1) = 23
    c: DistanceY(g2) = -14
FEATURE [Part::Extrusion] Extrude008  label="bot_hor_amplifier_extrude"
  Base = -> Populate011
  Dir = (0,0,1)
  DirMode = 2
  FaceMakerClass = Part::FaceMakerBullseye
  LengthFwd = 29
  LengthRev = 0
  Placement = pos=(0,0,-7) rot=(1,0,0;1.5708rad)
  Solid = true
  Symmetric = true
  expr: LengthFwd = <<Properties>>.endface_width
FEATURE [Part::Compound] Compound027
  Links = -> [Extrude007]
  Placement = pos=(0,-16.7432,-18) rot=(0,0,1;1.0472rad)
  expr: .Placement.Base.y = -<<Properties>>.endface_width / 2 / sin(60)
FEATURE [Part::Mirroring] Part__Mirroring010  label="Compound027 (Mirror #11)"
  Base = (0,0,0)
  Normal = (1,0,0)
  Source = -> Compound027
FEATURE [Part::Compound] Compound028  label="sink_fix001"
  Links = -> [Part__Mirroring010,Compound027]
FEATURE [Part::Compound] Compound029
  Links = -> [Extrude008]
  Placement = pos=(0,204,407.1) rot=(0.706965,0.706965,0.020021;3.18172rad)
  expr: .Placement.Rotation.Pitch = -<<sink_bend_line>>.FaceAngle
FEATURE [Part::Part2DObjectPython] Circle001  label="hole_8mm"  # Draft 2D object (typed FeaturePython)
  Area = 0
  FirstAngle = 0
  LastAngle = 0
  MakeFace = false
  Radius = 4
FEATURE [Sketcher::SketchObject] Sketch055
  ExternalGeometry = -> [Sketch008]
  FullyConstrained = true
  sketch-geometry (7):
    g0: LineSegment StartX=16.3 StartY=4 StartZ=0 EndX=16.3 EndY=19 EndZ=0
    g1: LineSegment StartX=16.3 StartY=19 StartZ=0 EndX=6.55 EndY=19 EndZ=0
    g2: LineSegment StartX=6.55 StartY=19 StartZ=0 EndX=6.55 EndY=11 EndZ=0
    g3: LineSegment StartX=6.55 StartY=11 StartZ=0 EndX=-6.55 EndY=11 EndZ=0
    g4: LineSegment StartX=-6.55 StartY=11 StartZ=0 EndX=-6.55 EndY=19 EndZ=0
    g5: LineSegment StartX=-6.55 StartY=19 StartZ=0 EndX=-16.3 EndY=19 EndZ=0
    g6: LineSegment StartX=-16.3 StartY=19 StartZ=0 EndX=-16.3 EndY=4 EndZ=0
  constraints (20):
    c: Vertical(g0)
    c: Coincident(g0,g1)
    c: Horizontal(g1)
    c: Coincident(g1,g2)
    c: Vertical(g2)
    c: Coincident(g2,g3)
    c: Coincident(g3,g4)
    c: Coincident(g4,g5)
    c: Horizontal(g5)
    c: Coincident(g5,g6)
    c: Vertical(g6)
    c: DistanceY(g0) = 4
    c: DistanceX(g0,g-3) = 2
    c: DistanceY(g0,g-3) = 0
    c: Symmetric(g0,g5,g-2)
    c: Horizontal(g6,g0)
    c: Symmetric(g2,g3,g-2)
    c: Vertical(g4)
    c: DistanceX(g3,g3) = 13.1
    c: DistanceY(g2,g2) = 8
FEATURE [PartDesign::SubShapeBinder] Binder034
  BindCopyOnChange = 0
  BindMode = 0
  ClaimChildren = true
  Fuse = false
  MakeFace = true
  OffsetFill = false
  OffsetIntersection = false
  OffsetJoinType = 0
  OffsetOpenResult = false
  PartialLoad = false
  Placement = pos=(0,0,1594) rot=(0,0,1;0rad)
  Relative = false
  Support = -> [Sketch055]
  _Version = 2
FEATURE [PartDesign::FeaturePython] BaseBend016  # WARN: FeaturePython — macro-defined, semantics opaque (R4)
  BendSide = 1
  BendSketch = -> Binder034
  MidPlane = false
  Reverse = true
  Suppressed = false
  length = 1122.3
  radius = 0.1
  thickness = 0.3
  expr: radius = composit_properties#<<Properties>>.bend_r
  expr: thickness = composit_properties#<<Properties>>.al_thickness
FEATURE [Part::FeaturePython] LinearArray012  label="led_holder_fix_array"  # WARN: FeaturePython — macro-defined, semantics opaque (R4)
  Alignment = 0
  CellStart = A1
  Count = 5
  Dir = (1,0,0)
  DirIsDriven = true
  DistributionLaw = 0
  DrivenProperty = 1
  EndInclusive = true
  ExposePlacement = false
  GeneratorMode = 0
  MarkerShape = 1
  MarkerSize = 0
  NumElements = 5
  OrientMode = 1
  Point = (0,0,0)
  PointIsDriven = true
  Reverse = false
  SpanEnd = 1093
  SpanStart = 0
  Step = 273.25
  Type = lattice2LinearArray.LinearArray
  VSGVersion = 1
  Values = 0.0 | 273.25 | 546.5 | 819.75 | 1093.0
  ValuesSource = 2
  isLattice = 1
FEATURE [Part::FeaturePython] Populate015  label="Populate led_holder_fix_array with hole3.4mm"  # WARN: FeaturePython — macro-defined, semantics opaque (R4)
  Copying = 0
  ExposePlacement = false
  MarkerShape = 1
  MarkerSize = 0
  NumElements = 0
  Object = -> Circle
  OutputCompounding = 1
  PlacementsTo = -> LinearArray012
  Referencing = 0
  Type = lattice2PopulateCopies.LatticePopulateCopies
  isLattice = 0
FEATURE [Part::Extrusion] Extrude010  label="led_holder_fix_extrude"
  Base = -> Populate015
  Dir = (0,0,1)
  DirMode = 2
  FaceMakerClass = Part::FaceMakerBullseye
  LengthFwd = 10
  LengthRev = 0
  Placement = pos=(-15,11.8848,1584) rot=(0.707107,0,-0.707107;3.14159rad)
  Solid = true
  Symmetric = false
FEATURE [Sketcher::SketchObject] Sketch056  label="pillar_dec_corner_base_sketch"
  ExternalGeometry = -> [Sketch008]
  FullyConstrained = true
  sketch-geometry (2):
    g0: LineSegment StartX=-18.3 StartY=19 StartZ=0 EndX=-18.3 EndY=-1.5 EndZ=0
    g1: LineSegment StartX=-18.3 StartY=-1.5 StartZ=0 EndX=18.3 EndY=-1.5 EndZ=0
  constraints (5):
    c: Coincident(g-3,g0)
    c: Vertical(g0)
    c: Coincident(g0,g1)
    c: Symmetric(g1,g0,g-2)
    c: DistanceY(g0) = -1.5
FEATURE [PartDesign::SubShapeBinder] Binder035
  BindCopyOnChange = 0
  BindMode = 0
  ClaimChildren = true
  Fuse = false
  MakeFace = true
  OffsetFill = false
  OffsetIntersection = false
  OffsetJoinType = 0
  OffsetOpenResult = false
  PartialLoad = false
  Relative = false
  Support = -> [Sketch056]
  _Version = 2
FEATURE [PartDesign::FeaturePython] BaseBend017  # WARN: FeaturePython — macro-defined, semantics opaque (R4)
  BendSide = 0
  BendSketch = -> Binder035
  MidPlane = false
  Placement = pos=(0,0,481) rot=(0,0,1;0rad)
  Reverse = false
  Suppressed = false
  length = 1113
  radius = 2
  thickness = 0.5
FEATURE [Part::Mirroring] Part__Mirroring011  label="led_holder_fix_extrude (Mirror #12)"
  Base = (0,0,0)
  Normal = (1,0,0)
  Source = -> Extrude010
FEATURE [Part::Compound] Compound033  label="led_holder_fix"
  Links = -> [Extrude010,Part__Mirroring011]
FEATURE [App::Link] Link004  label="hub2108"
  LinkPlacement = pos=(0,0,-90) rot=(0,0,1;0rad)
  LinkedObject = -> <external hub2108.FCStd>#Body
  Placement = pos=(0,0,-90) rot=(0,0,1;0rad)
FEATURE [App::Link] Link005  label="U_fix_material_0.50ansi"
  LinkPlacement = pos=(0,294.4,0) rot=(0,0,1;0rad)
  LinkedObject = -> <external U-fix.FCStd>#Body
  Placement = pos=(0,294.4,0) rot=(0,0,1;0rad)
FEATURE [PartDesign::SubShapeBinder] Binder036
  BindCopyOnChange = 0
  BindMode = 0
  ClaimChildren = true
  Fuse = false
  MakeFace = true
  OffsetFill = false
  OffsetIntersection = false
  OffsetJoinType = 0
  OffsetOpenResult = false
  PartialLoad = false
  Relative = false
  Support = -> [Link005[Binder.]]
  _Version = 2
FEATURE [Part::Extrusion] Extrude011  label="U-fix_vert_holes_extrude"
  Base = -> Binder036
  Dir = (0,1,2e-16)
  DirMode = 2
  FaceMakerClass = Part::FaceMakerBullseye
  LengthFwd = 29
  LengthRev = 0
  Placement = pos=(0,294.4,0) rot=(0,0,1;1.5708rad)
  Solid = false
  Symmetric = true
  expr: LengthFwd = <<Properties>>.endface_width
FEATURE [Sketcher::SketchObject] Sketch058
  AttachmentSupport = -> [XZ_Plane019]
  FullyConstrained = true
  MapMode = 5
  Placement = pos=(0,0,0) rot=(1,0,0;1.5708rad)
  sketch-geometry (5):
    g0: LineSegment StartX=8 StartY=497.7 StartZ=0 EndX=8 EndY=471.7 EndZ=0
    g1: LineSegment StartX=8 StartY=471.7 StartZ=0 EndX=-8 EndY=471.7 EndZ=0
    g2: LineSegment StartX=-8 StartY=471.7 StartZ=0 EndX=-8 EndY=497.7 EndZ=0
    g3: LineSegment StartX=-8 StartY=497.7 StartZ=0 EndX=8 EndY=497.7 EndZ=0
    g4: GeomPoint X=0 Y=484.7 Z=0
  constraints (13):
    c: Coincident(g0,g1)
    c: Coincident(g1,g2)
    c: Coincident(g2,g3)
    c: Coincident(g3,g0)
    c: Horizontal(g1)
    c: Horizontal(g3)
    c: Vertical(g0)
    c: Vertical(g2)
    c: Symmetric(g1,g0,g4)
    c: PointOnObject(g4,g-2)
    c: DistanceY(g0) = 471.7
    c: DistanceX(g1,g1) = 16
    c: DistanceY(g0,g0) = 26
FEATURE [Sketcher::SketchObject] Sketch060
  FullyConstrained = true
  expr: Constraints[11] = Sketch.Constraints.max_r + 15 mm
  sketch-geometry (4):
    g0: LineSegment StartX=0 StartY=0 StartZ=0 EndX=317.979 EndY=183.585 EndZ=0
    g1: LineSegment StartX=0 StartY=380 StartZ=0 EndX=37.5 EndY=380 EndZ=0
    g2: ArcOfCircle CenterX=-35.1249 CenterY=-20.2794 CenterZ=0 NormalX=0 NormalY=0 NormalZ=1 AngleXU=0 Radius=407.729 StartAngle=0.523599 EndAngle=1.36636
    g3: ArcOfCircle CenterX=37.5 CenterY=330 CenterZ=0 NormalX=0 NormalY=0 NormalZ=1 AngleXU=0 Radius=50 StartAngle=1.36636 EndAngle=1.5708
  constraints (12):
    c: Coincident(g0,g-1)
    c: Angle(g0) = 0.523599
    c: PointOnObject(g1,g-2)
    c: Horizontal(g1)
    c: DistanceX(g1,g1) = 37.5
    c: DistanceY(g1) = 380
    c: Coincident(g2,g0)
    c: PointOnObject(g2,g0)
    c: Tangent(g3,g1) = 1.5708
    c: Tangent(g2,g3) = -1.5708
    c: Radius(g3) = 50
    c: Distance(g0) = 367.17
FEATURE [Part::Mirroring] Mirror003  label="Sketch060 (mirrored)"
  Base = (0,0,0)
  Normal = (0.5,-0.866025,0)
  Source = -> Sketch060
  expr: .Normal.x = sin(30)
  expr: .Normal.y = -cos(30)
FEATURE [Sketcher::SketchObject] Sketch061
  ExternalGeometry = -> [Sketch060]
  FullyConstrained = true
  expr: Constraints[7] = (36.6 mm - 8 mm) / 2 + 1 mm
  sketch-geometry (3):
    g0: LineSegment StartX=0 StartY=380 StartZ=0 EndX=0 EndY=0 EndZ=0
    g1: LineSegment StartX=0 StartY=0 StartZ=0 EndX=329.09 EndY=-190 EndZ=0
    g2: LineSegment StartX=329.09 StartY=-190 StartZ=0 EndX=321.44 EndY=-203.25 EndZ=0
  constraints (8):
    c: Coincident(g-3,g0)
    c: Coincident(g0,g-1)
    c: Coincident(g0,g1)
    c: Angle(g1) = -0.523599
    c: Equal(g1,g0)
    c: Coincident(g2,g1)
    c: Perpendicular(g1,g2)
    c: Distance(g2) = 15.3
FEATURE [Part::Compound] Compound035
  Links = -> [Mirror003,Sketch061,Sketch060]
FEATURE [Part::Mirroring] Part__Mirroring012  label="Compound035 (Mirror #14)"
  Base = (0,0,0)
  Normal = (1,0,0)
  Source = -> Compound035
FEATURE [Part::Compound] Compound036
  Links = -> [Part__Mirroring012,Compound035]
FEATURE [PartDesign::SubShapeBinder] Binder037
  BindCopyOnChange = 0
  BindMode = 0
  ClaimChildren = true
  Context = -> Body072 [Binder037.]
  Fuse = false
  MakeFace = true
  OffsetFill = false
  OffsetIntersection = false
  OffsetJoinType = 0
  OffsetOpenResult = false
  PartialLoad = false
  Relative = false
  Support = -> [Compound036]
  _Version = 2
FEATURE [PartDesign::FeaturePython] BaseBend018  # WARN: FeaturePython — macro-defined, semantics opaque (R4)
  BendSide = 1
  BendSketch = -> Binder037
  MidPlane = false
  Placement = pos=(0,0,1596) rot=(0,0,1;0rad)
  Reverse = true
  Suppressed = false
  length = 1203
  radius = 1
  thickness = 1.5
FEATURE [PartDesign::FeaturePython] BaseBend019  # WARN: FeaturePython — macro-defined, semantics opaque (R4)
  BendSide = 0
  BendSketch = -> Sketch049
  MidPlane = true
  Reverse = false
  Suppressed = false
  length = 250
  radius = 0.1
  thickness = 0.3
FEATURE [PartDesign::Boolean] Boolean009
  BaseFeature = -> BaseBend019
  Group = -> [Extrude008]
  Suppressed = false
  Type = 1
  UsePlacement = false
  expr: Group = <<bot_hor_amplifier_extrude>>._self
FEATURE [PartDesign::Body] Body068  label="bot_hor_amplifier_material_0.30ansi"
  Group = -> [BaseBend019,Sketch049,Boolean009]
  Origin = -> Origin030
  Tip = -> Boolean009
FEATURE [Sketcher::SketchObject] Sketch062
  AttachmentSupport = -> [XY_Plane036]
  FullyConstrained = true
  MapMode = 5
  expr: Constraints[3] = <<Properties>>.endface_width / 2 + 0.5 mm
  sketch-geometry (7):
    g0: LineSegment StartX=61.9452 StartY=297.209 StartZ=0 EndX=15 EndY=280 EndZ=0
    g1: LineSegment StartX=15 StartY=280 StartZ=0 EndX=15 EndY=335 EndZ=0
    g2: LineSegment StartX=15 StartY=335 StartZ=0 EndX=62.031 EndY=297.743 EndZ=0
    g3: LineSegment StartX=61.9452 StartY=297.209 StartZ=0 EndX=62.4647 EndY=297.399 EndZ=0
    g4: LineSegment StartX=62.4647 StartY=297.399 StartZ=0 EndX=62.031 EndY=297.743 EndZ=0
    g5: LineSegment StartX=61.9452 StartY=297.209 StartZ=0 EndX=61.8385 EndY=297.5 EndZ=0
    g6: LineSegment StartX=61.8385 StartY=297.5 StartZ=0 EndX=62.031 EndY=297.743 EndZ=0
  constraints (20):
    c: Coincident(g0,g1)
    c: Vertical(g1)
    c: Coincident(g1,g2)
    c: DistanceX(g1) = 15
    c: Distance(g1) = 55
    c: Distance(g2) = 60
    c: Distance(g0) = 50
    c: Coincident(g3,g0)
    c: Coincident(g4,g3)
    c: Coincident(g4,g2)
    c: Parallel(g0,g3)
    c: Parallel(g4,g2)
    c: Equal(g3,g4)
    c: Coincident(g0,g5)
    c: Coincident(g5,g6)
    c: Coincident(g6,g2)
    c: Perpendicular(g3,g5)
    c: Perpendicular(g4,g6)
    c: Distance(g5) = 0.31
    c: DistanceY(g1) = 335
FEATURE [PartDesign::FeaturePython] BaseBend020  # WARN: FeaturePython — macro-defined, semantics opaque (R4)
  BendSide = 0
  BendSketch = -> Sketch062
  MidPlane = false
  Reverse = false
  Suppressed = false
  length = 413
  radius = 0.1
  thickness = 0.3
  expr: radius = composit_properties#<<Properties>>.bend_r
  expr: thickness = composit_properties#<<Properties>>.al_thickness
FEATURE [PartDesign::FeaturePython] Bend009  # WARN: FeaturePython — macro-defined, semantics opaque (R4)
  AutoMiter = true
  BaseFeature = -> BaseBend020
  BendType = 0
  LengthList = [15]
  LengthSpec = 0
  ReliefFactor = 0.7
  Suppressed = false
  UseReliefFactor = false
  angle = 90
  baseObject = -> BaseBend020 [Edge17,Edge4,Edge33,Edge32,Edge16,Edge3]
  bendAList = [90]
  extend1 = 0
  extend2 = 0
  gap1 = 0
  gap2 = 0
  invert = false
  kfactor = 0.5
  length = 15
  maxExtendDist = 5
  minGap = 0.1
  minReliefGap = 1
  miterangle1 = 0
  miterangle2 = 0
  offset = 0
  radius = 0.1
  reliefType = 0
  reliefd = 1
  reliefw = 0.8
  sketchflip = false
  sketchinvert = false
  unfold = false
  expr: radius = BaseBend020.radius
FEATURE [Sketcher::SketchObject] Sketch063
  ExternalGeometry = -> [Sketch062]
  FullyConstrained = true
  sketch-geometry (8):
    g0: LineSegment StartX=15 StartY=281.556 StartZ=0 EndX=15 EndY=328.796 EndZ=0
    g1: LineSegment StartX=19.8629 StartY=331.148 StartZ=0 EndX=62.031 EndY=297.743 EndZ=0
    g2: LineSegment StartX=0 StartY=0 StartZ=0 EndX=212.95 EndY=122.947 EndZ=0
    g3: ArcOfCircle CenterX=-320.353 CenterY=-184.956 CenterZ=0 NormalX=0 NormalY=0 NormalZ=1 AngleXU=0 Radius=615.805 StartAngle=0.523599 EndAngle=0.900842
    g4: ArcOfCircle CenterX=-305.711 CenterY=-176.502 CenterZ=0 NormalX=0 NormalY=0 NormalZ=1 AngleXU=0 Radius=557.898 StartAngle=0.523599 EndAngle=0.955586
    g5: ArcOfCircle CenterX=18 CenterY=328.796 CenterZ=0 NormalX=0 NormalY=0 NormalZ=1 AngleXU=0 Radius=3 StartAngle=0.900842 EndAngle=3.14159
    g6: GeomPoint X=15 Y=335 Z=0
    g7: ArcOfCircle CenterX=18 CenterY=281.556 CenterZ=0 NormalX=0 NormalY=0 NormalZ=1 AngleXU=0 Radius=3 StartAngle=3.14159 EndAngle=4.09718
  constraints (20):
    c: Coincident(g6,g-4)
    c: Coincident(g1,g-3)
    c: Coincident(g2,g-1)
    c: Angle(g2) = 0.523599
    c: Coincident(g3,g2)
    c: PointOnObject(g4,g2)
    c: Perpendicular(g4,g2)
    c: Perpendicular(g3,g2)
    c: Tangent(g3,g1) = 1.5708
    c: PointOnObject(g6,g0)
    c: PointOnObject(g6,g1)
    c: Tangent(g0,g5) = 1.5708
    c: Tangent(g1,g5) = 1.5708
    c: Tangent(g4,g7) = 1.5708
    c: Tangent(g0,g7) = 1.5708
    c: PointOnObject(g-4,g4)
    c: PointOnObject(g-4,g0)
    c: Equal(g7,g5)
    c: Radius(g7) = 3
    c: Distance(g4,g3) = 41
FEATURE [Part::Mirroring] Mirror004  label="Sketch063 (mirrored)"
  Base = (0,0,0)
  Normal = (0.5,-0.866025,0)
  Source = -> Sketch063
  expr: .Normal.x = cos(-60)
  expr: .Normal.y = sin(-60)
FEATURE [Part::Compound] Compound037
  Links = -> [Sketch063,Mirror004]
FEATURE [PartDesign::SubShapeBinder] Binder038
  BindCopyOnChange = 0
  BindMode = 0
  ClaimChildren = true
  Context = -> Body074 [Binder038.]
  Fuse = false
  MakeFace = true
  OffsetFill = false
  OffsetIntersection = false
  OffsetJoinType = 0
  OffsetOpenResult = false
  PartialLoad = false
  Relative = true
  Support = -> [Compound037]
  _Version = 2
FEATURE [PartDesign::Pad] Pad008
  Direction = (0,0,1)
  Length = 3
  Length2 = 10
  Profile = -> Binder038
  Suppressed = false
  Type = 0
FEATURE [Sketcher::SketchObject] Sketch064
  AttachmentSupport = -> [Local_CS]
  FullyConstrained = true
  MapMode = 5
  Placement = pos=(0,0,0) rot=(1,0,0;0.113192rad)
  expr: Constraints[3] = <<Properties>>.rivet_d
  sketch-geometry (4):
    g0: Circle CenterX=-88.3 CenterY=228.865 CenterZ=0 NormalX=0 NormalY=0 NormalZ=1 AngleXU=0 Radius=1.7
    g1: Circle CenterX=88.3 CenterY=228.865 CenterZ=0 NormalX=0 NormalY=0 NormalZ=1 AngleXU=0 Radius=1.7
    g2: Circle CenterX=261.291 CenterY=193.3 CenterZ=0 NormalX=0 NormalY=0 NormalZ=1 AngleXU=0 Radius=1.7
    g3: Circle CenterX=-261.291 CenterY=193.3 CenterZ=0 NormalX=0 NormalY=0 NormalZ=1 AngleXU=0 Radius=1.7
  constraints (10):
    c: Equal(g2,g1)
    c: Equal(g2,g0)
    c: Equal(g2,g3)
    c: Diameter(g2) = 3.4
    c: DistanceX(g1) = 88.3
    c: DistanceY(g1) = 228.865
    c: DistanceX(g2) = 261.291
    c: DistanceY(g2) = 193.3
    c: Symmetric(g0,g1,g-2)
    c: Symmetric(g3,g2,g-2)
FEATURE [Sketcher::SketchObject] Sketch066
  AttachmentSupport = -> [XY_Plane016]
  FullyConstrained = true
  MapMode = 5
  expr: Constraints[6] = <<Properties>>.rivet_d
  sketch-geometry (3):
    g0: Circle CenterX=0 CenterY=35 CenterZ=0 NormalX=0 NormalY=0 NormalZ=1 AngleXU=0 Radius=1.7
    g1: Circle CenterX=25 CenterY=60 CenterZ=0 NormalX=0 NormalY=0 NormalZ=1 AngleXU=0 Radius=1.7
    g2: Circle CenterX=-25 CenterY=60 CenterZ=0 NormalX=0 NormalY=0 NormalZ=1 AngleXU=0 Radius=1.7
  constraints (8):
    c: PointOnObject(g0,g-2)
    c: DistanceY(g0) = 35
    c: DistanceX(g1) = 25
    c: DistanceY(g1) = 60
    c: Equal(g0,g1)
    c: Equal(g0,g2)
    c: Diameter(g0) = 3.4
    c: Symmetric(g2,g1,g-2)
FEATURE [Sketcher::SketchObject] Sketch067
  AttachmentSupport = -> [XY_Plane016]
  FullyConstrained = true
  MapMode = 5
  sketch-geometry (13):
    g0: LineSegment StartX=-8.5 StartY=28 StartZ=0 EndX=-8.5 EndY=0 EndZ=0
    g1: LineSegment StartX=-8.5 StartY=0 StartZ=0 EndX=8.5 EndY=0 EndZ=0
    g2: LineSegment StartX=8.5 StartY=28 StartZ=0 EndX=-8.5 EndY=28 EndZ=0
    g3: GeomPoint X=0 Y=14 Z=0
    g4: LineSegment StartX=8.5 StartY=0 StartZ=0 EndX=14 EndY=0 EndZ=0
    g5: LineSegment StartX=8.5 StartY=20.9904 StartZ=0 EndX=8.5 EndY=28 EndZ=0
    g6: ArcOfCircle CenterX=8.5 CenterY=8 CenterZ=0 NormalX=0 NormalY=0 NormalZ=1 AngleXU=0 Radius=7.5 StartAngle=0 EndAngle=1.0472
    g7: ArcOfCircle CenterX=16 CenterY=20.9904 CenterZ=0 NormalX=0 NormalY=0 NormalZ=1 AngleXU=0 Radius=7.5 StartAngle=3.14159 EndAngle=4.18879
    g8: LineSegment StartX=14 StartY=0 StartZ=0 EndX=14 EndY=4 EndZ=0
    g9: LineSegment StartX=14 StartY=4 StartZ=0 EndX=14 EndY=10 EndZ=0
    g10: LineSegment StartX=16 StartY=6 StartZ=0 EndX=16 EndY=8 EndZ=0
    g11: ArcOfCircle CenterX=15 CenterY=4 CenterZ=0 NormalX=0 NormalY=0 NormalZ=1 AngleXU=0 Radius=1 StartAngle=1.5708 EndAngle=3.14159
    g12: ArcOfCircle CenterX=15 CenterY=6 CenterZ=0 NormalX=0 NormalY=0 NormalZ=1 AngleXU=0 Radius=1 StartAngle=4.71239 EndAngle=6.28319
  constraints (34):
    c: Coincident(g0,g1)
    c: Coincident(g1,g4)
    c: Coincident(g5,g2)
    c: Coincident(g2,g0)
    c: Horizontal(g1)
    c: Vertical(g0)
    c: Symmetric(g1,g0,g3)
    c: PointOnObject(g3,g-2)
    c: PointOnObject(g1,g-1)
    c: DistanceX(g2,g2) = 17
    c: DistanceY(g4,g5) = 28
    c: Coincident(g4,g8)
    c: Vertical(g5)
    c: Horizontal(g4)
    c: DistanceX(g4,g4) = 5.5
    c: DistanceY(g8,g9) = 10
    c: Symmetric(g2,g0,g-2)
    c: Tangent(g7,g6) = 1.5708
    c: Tangent(g7,g5) = 1.5708
    c: PointOnObject(g6,g5)
    c: Equal(g6,g7)
    c: Coincident(g8,g9)
    c: Vertical(g8)
    c: Vertical(g9)
    c: DistanceY(g8,g8) = 4
    c: Vertical(g10)
    c: DistanceX(g10) = 16
    c: Tangent(g11,g8) = 1.5708
    c: Tangent(g12,g11) = 1.5708
    c: Tangent(g12,g10) = -1.5708
    c: Equal(g12,g11)
    c: Tangent(g6,g10) = -1.5708
    c: Vertical(g11,g11)
    c: DistanceY(g10,g10) = 2
FEATURE [Sketcher::SketchObject] Sketch068  label="hat1_sketch"
  FullyConstrained = true
  sketch-geometry (8):
    g0: LineSegment StartX=0 StartY=0 StartZ=0 EndX=112.627 EndY=65.0251 EndZ=0
    g1: GeomPoint X=36 Y=353 Z=0
    g2: ArcOfCircle CenterX=34 CenterY=351 CenterZ=0 NormalX=0 NormalY=0 NormalZ=1 AngleXU=0 Radius=2 StartAngle=-1.07e-14 EndAngle=1.80501
    g3: LineSegment StartX=0 StartY=350 StartZ=0 EndX=8.5 EndY=350 EndZ=0
    g4: ArcOfCircle CenterX=8.5 CenterY=457.875 CenterZ=0 NormalX=0 NormalY=0 NormalZ=1 AngleXU=0 Radius=107.875 StartAngle=4.71239 EndAngle=4.94661
    g5: LineSegment StartX=34 StartY=353 StartZ=0 EndX=36 EndY=353 EndZ=0
    g6: ArcOfCircle CenterX=607.95 CenterY=351 CenterZ=0 NormalX=0 NormalY=0 NormalZ=1 AngleXU=0 Radius=571.95 StartAngle=3.14159 EndAngle=3.66519
    g7: LineSegment StartX=36 StartY=351 StartZ=0 EndX=36 EndY=353 EndZ=0
  constraints (23):
    c: DistanceX(g1) = 36
    c: DistanceY(g1) = 353
    c: Coincident(g0,g-1)
    c: Angle(g0) = 0.523599
    c: PointOnObject(g3,g-2)
    c: Horizontal(g3)
    c: DistanceX(g3,g3) = 8.5
    c: DistanceY(g3) = 350
    c: Tangent(g4,g2) = 1.5708
    c: PointOnObject(g5,g2)
    c: Coincident(g5,g1)
    c: Horizontal(g5)
    c: Tangent(g5,g2)
    c: Tangent(g4,g3) = -1.5708
    c: Radius(g2) = 2
    c: Distance(g0) = 130.05
    c: Coincident(g6,g0)
    c: Tangent(g6,g2) = 1.5708
    c: Horizontal(g2,g2)
    c: Perpendicular(g6,g0)
    c: Coincident(g7,g2)
    c: Coincident(g7,g1)
    c: Vertical(g7)
FEATURE [Sketcher::SketchObject] Sketch070
  AttachmentSupport = -> [XY_Plane015]
  FullyConstrained = true
  MapMode = 5
  sketch-geometry (2):
    g0: Circle CenterX=-40 CenterY=-12 CenterZ=0 NormalX=0 NormalY=0 NormalZ=1 AngleXU=0 Radius=2.75
    g1: Circle CenterX=40 CenterY=-12 CenterZ=0 NormalX=0 NormalY=0 NormalZ=1 AngleXU=0 Radius=2.75
  constraints (5):
    c: Equal(g1,g0)
    c: Diameter(g1) = 5.5
    c: Symmetric(g0,g1,g-2)
    c: DistanceX(g0,g1) = 80
    c: DistanceY(g1) = -12
FEATURE [PartDesign::Pocket] Pocket031
  BaseFeature = -> Pocket001
  Direction = (0,0,-1)
  Length = 5
  Length2 = 5
  Midplane = true
  Profile = -> Sketch070
  ReferenceAxis = -> Sketch070 [N_Axis]
  Suppressed = false
  Type = 1
FEATURE [Part::Mirroring] Part__Mirroring013  label="Sketch068 (Mirror #16)"
  Base = (0,0,0)
  Normal = (1,0,0)
  Source = -> Sketch068
FEATURE [Part::Compound] Compound039
  Links = -> [Part__Mirroring013,Sketch068]
FEATURE [Part::FeaturePython] Array005  # Draft array (typed FeaturePython)
  AlwaysSyncPlacement = false
  Angle = 360
  ArrayType = 1
  Axis = (0,0,1)
  Base = -> Compound039
  Center = (0,0,0)
  Count = 3
  ExpandArray = false
  Fuse = false
  IntervalAxis = (0,0,0)
  IntervalX = (50,0,0)
  IntervalY = (0,50,0)
  IntervalZ = (0,0,50)
  NumberCircles = 3
  NumberPolar = 3
  NumberX = 2
  NumberY = 2
  NumberZ = 1
  PlacementList = 3 placements: [(0,0,0),(0,0,0),(0,0,0)]
  RadialDistance = 50
  ScaleList = (3) [(1,1,1),(1,1,1),(1,1,1)]
  Symmetry = 1
  TangentialDistance = 25
FEATURE [PartDesign::SubShapeBinder] Binder039
  BindCopyOnChange = 0
  BindMode = 0
  ClaimChildren = true
  Context = -> Body075 [Binder039.]
  Fuse = false
  MakeFace = true
  OffsetFill = false
  OffsetIntersection = false
  OffsetJoinType = 0
  OffsetOpenResult = false
  PartialLoad = false
  Relative = false
  Support = -> [Array005]
  _Version = 2
FEATURE [PartDesign::Pad] Pad009
  Direction = (0,0,1)
  Length = 3
  Length2 = 10
  Profile = -> Binder039
  Suppressed = false
  Type = 0
FEATURE [PartDesign::SubShapeBinder] Binder040
  BindCopyOnChange = 0
  BindMode = 0
  ClaimChildren = true
  Context = -> Part010 [Body075.Binder040.]
  Fuse = false
  MakeFace = true
  OffsetFill = false
  OffsetIntersection = false
  OffsetJoinType = 0
  OffsetOpenResult = false
  PartialLoad = false
  Placement = pos=(0,382,0) rot=(0,0,1;3.14159rad)
  Relative = false
  Support = -> [Sketch066]
  _Version = 2
  expr: Support = Sketch066._self
FEATURE [PartDesign::Pocket] Pocket032
  BaseFeature = -> Pad009
  Direction = (0,0,-1)
  Length = 5
  Length2 = 5
  Midplane = true
  Profile = -> Binder040
  Suppressed = false
  Type = 1
FEATURE [Sketcher::SketchObject] Sketch071  label="hat2_sketch"
  ExternalGeometry = -> [Sketch068]
  FullyConstrained = true
  sketch-geometry (13):
    g0: LineSegment StartX=36 StartY=353 StartZ=0 EndX=36 EndY=376.5 EndZ=0
    g1: LineSegment StartX=0 StartY=381.5 StartZ=0 EndX=31 EndY=381.5 EndZ=0
    g2: ArcOfCircle CenterX=31 CenterY=376.5 CenterZ=0 NormalX=0 NormalY=0 NormalZ=1 AngleXU=0 Radius=5 StartAngle=2e-15 EndAngle=1.5708
    g3: GeomPoint X=36 Y=381.5 Z=0
    g4: ArcOfEllipse CenterX=243.039 CenterY=353 CenterZ=0 NormalX=0 NormalY=0 NormalZ=1 MajorRadius=395.482 MinorRadius=207.039 AngleXU=1.5708 StartAngle=1.5708 EndAngle=2.40506
    g5: LineSegment StartX=243.039 StartY=748.482 StartZ=0 EndX=243.039 EndY=-42.4822 EndZ=0
    g6: LineSegment StartX=36 StartY=353 StartZ=0 EndX=450.077 EndY=353 EndZ=0
    g7: GeomPoint X=243.039 Y=689.959 Z=0
    g8: GeomPoint X=243.039 Y=16.0414 Z=0
    g9: LineSegment StartX=103.966 StartY=60.0251 StartZ=0 EndX=112.627 EndY=65.0251 EndZ=0
    g10: GeomPoint X=103.966 Y=60.0251 Z=0
    g11: ArcOfCircle CenterX=34 CenterY=351 CenterZ=0 NormalX=0 NormalY=0 NormalZ=1 AngleXU=0 Radius=2 StartAngle=5.8e-15 EndAngle=1.80501
    g12: LineSegment StartX=34 StartY=353 StartZ=0 EndX=36 EndY=353 EndZ=0
  constraints (26):
    c: Vertical(g0)
    c: DistanceY(g3) = 381.5
    c: PointOnObject(g1,g-2)
    c: Horizontal(g1)
    c: PointOnObject(g3,g0)
    c: PointOnObject(g3,g1)
    c: Tangent(g0,g2) = -1.5708
    c: Tangent(g1,g2) = 1.5708
    c: Radius(g2) = 5
    c: InternalAlignment(g5-g8 -> g4) x4
    c: Horizontal(g6)
    c: Coincident(g9,g4)
    c: Coincident(g9,g-4)
    c: PointOnObject(g-1,g9)
    c: PointOnObject(g10,g4)
    c: PointOnObject(g10,g9)
    c: Perpendicular(g4,g9,g10) = 1.5708
    c: Coincident(g4,g0)
    c: PointOnObject(g-4,g0)
    c: Distance(g9) = 10
    c: Coincident(g11,g-3)
    c: Tangent(g11,g-4) = 1.5708
    c: Coincident(g12,g0)
    c: Horizontal(g12)
    c: Tangent(g12,g11) = 1.5708
    c: Horizontal(g6,g0)
FEATURE [Part::Mirroring] Part__Mirroring014  label="hat2_sketch (Mirror #17)"
  Base = (0,0,0)
  Normal = (1,0,0)
  Source = -> Sketch071
FEATURE [Part::Compound] Compound040  label="hat2_sketch_compound"
  Links = -> [Part__Mirroring014,Sketch071]
FEATURE [Part::FeaturePython] Array006  label="hat2_pad_base"  # Draft array (typed FeaturePython)
  AlwaysSyncPlacement = false
  Angle = 360
  ArrayType = 1
  Axis = (0,0,1)
  Base = -> Compound040
  Center = (0,0,0)
  Count = 3
  ExpandArray = false
  Fuse = false
  IntervalAxis = (0,0,0)
  IntervalX = (50,0,0)
  IntervalY = (0,50,0)
  IntervalZ = (0,0,50)
  NumberCircles = 3
  NumberPolar = 3
  NumberX = 2
  NumberY = 2
  NumberZ = 1
  PlacementList = 3 placements: [(0,0,0),(0,0,0),(0,0,0)]
  RadialDistance = 50
  ScaleList = (3) [(1,1,1),(1,1,1),(1,1,1)]
  Symmetry = 1
  TangentialDistance = 25
FEATURE [PartDesign::SubShapeBinder] Binder041
  BindCopyOnChange = 0
  BindMode = 0
  ClaimChildren = true
  Context = -> Body076 [Binder041.]
  Fuse = false
  MakeFace = true
  OffsetFill = false
  OffsetIntersection = false
  OffsetJoinType = 0
  OffsetOpenResult = false
  PartialLoad = false
  Relative = false
  Support = -> [Array006]
  _Version = 2
FEATURE [PartDesign::Pad] Pad010
  Direction = (0,0,1)
  Length = 3
  Length2 = 10
  Profile = -> Binder041
  Suppressed = false
  Type = 0
FEATURE [Sketcher::SketchObject] Sketch072
  AttachmentSupport = -> [XY_Plane039]
  FullyConstrained = true
  MapMode = 5
  sketch-geometry (3):
    g0: Circle CenterX=122.567 CenterY=-102.846 CenterZ=0 NormalX=0 NormalY=0 NormalZ=1 AngleXU=0 Radius=15
    g1: Circle CenterX=-122.567 CenterY=-102.846 CenterZ=0 NormalX=0 NormalY=0 NormalZ=1 AngleXU=0 Radius=15
    g2: LineSegment StartX=0 StartY=0 StartZ=0 EndX=122.567 EndY=-102.846 EndZ=0
  constraints (7):
    c: Coincident(g2,g-1)
    c: Coincident(g2,g0)
    c: Angle(g2) = -0.698132
    c: Symmetric(g1,g0,g-2)
    c: Equal(g0,g1)
    c: Distance(g2) = 160
    c: Diameter(g0) = 30
FEATURE [PartDesign::Pocket] Pocket033
  BaseFeature = -> Pad010
  Direction = (0,0,-1)
  Length = 5
  Length2 = 5
  Midplane = true
  Profile = -> Sketch072
  ReferenceAxis = -> Sketch072 [N_Axis]
  Suppressed = false
  Type = 1
FEATURE [PartDesign::Body] Body076  label="hat_top"
  Group = -> [Binder041,Pad010,Sketch072,Pocket033]
  Origin = -> Origin039
  Placement = pos=(0,0,87) rot=(0,0,1;0rad)
  Tip = -> Pocket033
FEATURE [Sketcher::SketchObject] Sketch073
  AttachmentSupport = -> [YZ_Plane016]
  FullyConstrained = true
  MapMode = 5
  Placement = pos=(0,0,0) rot=(0.57735,0.57735,0.57735;2.0944rad)
  expr: Constraints[5] = <<Properties>>.rivet_d
  sketch-geometry (2):
    g0: Circle CenterX=10 CenterY=80 CenterZ=0 NormalX=0 NormalY=0 NormalZ=1 AngleXU=0 Radius=1.7
    g1: Circle CenterX=10 CenterY=10 CenterZ=0 NormalX=0 NormalY=0 NormalZ=1 AngleXU=0 Radius=1.7
  constraints (6):
    c: Vertical(g1,g0)
    c: DistanceX(g1) = 10
    c: DistanceY(g0) = 80
    c: DistanceY(g1) = 10
    c: Equal(g1,g0)
    c: Diameter(g1) = 3.4
FEATURE [Part::FeaturePython] Placment002  label="top_placement"  # WARN: FeaturePython — macro-defined, semantics opaque (R4)
  AttacherType = Attacher::AttachEngine3D
  ExposePlacement = true
  MarkerShape = 1
  MarkerSize = 10
  NumElements = 1
  Type = lattice2AttachablePlacement.AttachablePlacement
  isLattice = 1
FEATURE [Part::FeaturePython] Placment004  label="pillar_dec_corner_placement"  # WARN: FeaturePython — macro-defined, semantics opaque (R4)
  AttacherType = Attacher::AttachEngine3D
  ExposePlacement = true
  MarkerShape = 1
  MarkerSize = 50
  NumElements = 1
  Type = lattice2AttachablePlacement.AttachablePlacement
  isLattice = 1
FEATURE [Part::FeaturePython] Placment005  label="pillar_top_dec_corner_placement"  # WARN: FeaturePython — macro-defined, semantics opaque (R4)
  AttacherType = Attacher::AttachEngine3D
  ExposePlacement = true
  MarkerShape = 1
  MarkerSize = 50
  NumElements = 1
  Type = lattice2AttachablePlacement.AttachablePlacement
  isLattice = 1
FEATURE [Part::FeaturePython] PolarArray  # WARN: FeaturePython — macro-defined, semantics opaque (R4)
  Alignment = 0
  AttacherType = Attacher::AttachEngine3D
  CellStart = A1
  Count = 3
  DistributionLaw = 0
  EndInclusive = false
  ExposePlacement = false
  FlipX = false
  FlipZ = false
  GeneratorMode = 0
  MarkerShape = 1
  MarkerSize = 0
  NumElements = 3
  OrientMode = 2
  Radius = 50
  Reverse = false
  SpanEnd = 360
  SpanStart = 0
  Step = 120
  Type = lattice2PolarArray2.PolarArray
  UseArcRadius = false
  UseArcRange = 0
  VSGVersion = 1
  Values = 0.0 | 120.0 | 240.0
  ValuesSource = 2
  isLattice = 1
FEATURE [PartDesign::SubShapeBinder] Binder042  label="led_holes"
  BindCopyOnChange = 0
  BindMode = 0
  ClaimChildren = true
  Fuse = false
  MakeFace = false
  OffsetFill = false
  OffsetIntersection = false
  OffsetJoinType = 0
  OffsetOpenResult = false
  PartialLoad = false
  Relative = true
  Support = -> [<external ULY-P91-20W.FCStd>#Sketch001]
  _Version = 2
FEATURE [Part::FeaturePython] Placment006  label="Custom"  # WARN: FeaturePython — macro-defined, semantics opaque (R4)
  ExposePlacement = true
  FlipZ = false
  Invert = false
  MarkerShape = 1
  MarkerSize = 20
  NumElements = 1
  Placement = pos=(-89,0,0) rot=(0,0,1;0rad)
  PlacementChoice = 0
  Type = lattice2Placement.LatticePlacement
  isLattice = 1
FEATURE [Part::FeaturePython] Join  label="plexiglass_fix_base"  # WARN: FeaturePython — macro-defined, semantics opaque (R4)
  ExposePlacement = false
  Interleave = false
  Links = -> [Placment006,LinearArray012]
  MarkerShape = 1
  MarkerSize = 0
  NumElements = 6
  Type = lattice2JoinArrays.JoinArrays
  isLattice = 1
FEATURE [Part::FeaturePython] Populate017  label="Populate plexiglass_fix_base with hole3.4mm"  # WARN: FeaturePython — macro-defined, semantics opaque (R4)
  Copying = 0
  ExposePlacement = false
  MarkerShape = 1
  MarkerSize = 0
  NumElements = 0
  Object = -> Circle
  OutputCompounding = 1
  PlacementsTo = -> Join
  Referencing = 0
  Type = lattice2PopulateCopies.LatticePopulateCopies
  isLattice = 0
FEATURE [PartDesign::SubShapeBinder] Binder043  label="plexiglass_fix"
  BindCopyOnChange = 0
  BindMode = 0
  ClaimChildren = true
  Fuse = true
  MakeFace = true
  OffsetFill = false
  OffsetIntersection = false
  OffsetJoinType = 0
  OffsetOpenResult = false
  PartialLoad = false
  Relative = false
  Support = -> [Populate017,Compound041]
  _Version = 2
FEATURE [Part::Extrusion] Extrude014  label="plexiglass_fix_extrude"
  Base = -> Binder043
  Dir = (0,0,1)
  DirMode = 2
  FaceMakerClass = Part::FaceMakerBullseye
  LengthFwd = 50
  LengthRev = 0
  Placement = pos=(0,10,1584) rot=(0.57735,0.57735,-0.57735;2.0944rad)
  Solid = true
  Symmetric = false
FEATURE [Part::Compound] Compound034  label="pillar_common_cut"
  Links = -> [Compound033,Extrude014]
FEATURE [Part::Compound] Compound030  label="pillar_cut1"
  Links = -> [Extrude010,Compound034]
FEATURE [Part::Compound] Compound031  label="led_holder_cut1"
  Links = -> [Compound034]
FEATURE [PartDesign::Boolean] Boolean010
  BaseFeature = -> BaseBend016
  Group = -> [Compound031]
  Suppressed = false
  Type = 1
  UsePlacement = false
  expr: Group = <<led_holder_cut1>>._self
FEATURE [Part::Compound] Compound032  label="dec_corner_cut1"
  Links = -> [Compound034]
FEATURE [PartDesign::Pocket] Pocket028
  BaseFeature = -> Boolean010
  Direction = (0,1,-2e-16)
  Length = 5
  Length2 = 5
  Midplane = true
  Profile = -> Sketch058
  ReferenceAxis = -> Sketch058 [N_Axis]
  Suppressed = false
  Type = 1
FEATURE [PartDesign::Body] Body015  label="led_holder_material_0.30ansi"
  Group = -> [Binder034,BaseBend016,Boolean010,Sketch058,Pocket028]
  Origin = -> Origin019
  Tip = -> Pocket028
FEATURE [Sketcher::SketchObject] Sketch074
  ExternalGeometry = -> [Binder042]
  FullyConstrained = true
  sketch-geometry (1):
    g0: Circle CenterX=-12.5 CenterY=0 CenterZ=0 NormalX=0 NormalY=0 NormalZ=1 AngleXU=0 Radius=1.8
  constraints (2):
    c: Symmetric(g0,g-3,g-2)
    c: Equal(g0,g-3)
FEATURE [Part::Compound] Compound041
  Links = -> [Binder042,Sketch074]
  Placement = pos=(-21,0,0) rot=(0,0,1;1.5708rad)
FEATURE [Part::Compound] Compound042
  Links = -> [Extrude014]
  Placement = pos=(0,384,0) rot=(0,0,1;3.14159rad)
  expr: Placement = <<pillar_placement>>.Placement
FEATURE [Part::FeaturePython] Populate018  label="Populate PolarArray with Compound042"  # WARN: FeaturePython — macro-defined, semantics opaque (R4)
  Copying = 0
  ExposePlacement = false
  MarkerShape = 1
  MarkerSize = 0
  NumElements = 0
  Object = -> Compound042
  OutputCompounding = 1
  PlacementsTo = -> PolarArray
  Referencing = 1
  Type = lattice2PopulateCopies.LatticePopulateCopies
  isLattice = 0
FEATURE [Sketcher::SketchObject] Sketch075
  AttachmentSupport = -> [XY_Plane036]
  ExternalGeometry = -> [Sketch062]
  FullyConstrained = true
  MapMode = 5
  expr: Constraints[34] = <<Properties>>.rivet_d
  sketch-geometry (14):
    g0: LineSegment StartX=15 StartY=280 StartZ=0 EndX=62.4647 EndY=297.399 EndZ=0
    g1: LineSegment StartX=62.4647 StartY=297.399 StartZ=0 EndX=15 EndY=335 EndZ=0
    g2: LineSegment StartX=15 StartY=280 StartZ=0 EndX=30.7162 EndY=302.5 EndZ=0
    g3: LineSegment StartX=30.7162 StartY=302.5 StartZ=0 EndX=15 EndY=335 EndZ=0
    g4: LineSegment StartX=30.7162 StartY=302.5 StartZ=0 EndX=62.4647 EndY=297.399 EndZ=0
    g5: LineSegment StartX=15 StartY=302.5 StartZ=0 EndX=30.7162 EndY=302.5 EndZ=0
    g6: LineSegment StartX=30.7162 StartY=302.5 StartZ=0 EndX=36.1253 EndY=287.744 EndZ=0
    g7: LineSegment StartX=30.7162 StartY=302.5 StartZ=0 EndX=40.4751 EndY=314.819 EndZ=0
    g8: Circle CenterX=34.4044 CenterY=292.439 CenterZ=0 NormalX=0 NormalY=0 NormalZ=1 AngleXU=0 Radius=1.7
    g9: Circle CenterX=36.2097 CenterY=309.435 CenterZ=0 NormalX=0 NormalY=0 NormalZ=1 AngleXU=0 Radius=1.7
    g10: Circle CenterX=20.588 CenterY=302.5 CenterZ=0 NormalX=0 NormalY=0 NormalZ=1 AngleXU=0 Radius=1.7
    g11: LineSegment StartX=20.588 StartY=302.5 StartZ=0 EndX=36.2097 EndY=309.435 EndZ=0
    g12: LineSegment StartX=36.2097 StartY=309.435 StartZ=0 EndX=34.4044 EndY=292.439 EndZ=0
    g13: LineSegment StartX=34.4044 StartY=292.439 StartZ=0 EndX=20.588 EndY=302.5 EndZ=0
  constraints (36):
    c: Coincident(g-4,g0)
    c: Coincident(g0,g1)
    c: Coincident(g1,g-3)
    c: PointOnObject(g-4,g0)
    c: PointOnObject(g-3,g1)
    c: Coincident(g0,g2)
    c: Coincident(g2,g3)
    c: Coincident(g2,g4)
    c: Coincident(g4,g0)
    c: Coincident(g3,g1)
    c: Coincident(g5,g2)
    c: Horizontal(g5)
    c: Coincident(g5,g6)
    c: PointOnObject(g6,g0)
    c: Perpendicular(g0,g6)
    c: Vertical(g5,g0)
    c: Equal(g6,g5)
    c: Coincident(g7,g2)
    c: PointOnObject(g7,g1)
    c: Perpendicular(g1,g7)
    c: Equal(g6,g7)
    c: PointOnObject(g8,g6)
    c: PointOnObject(g9,g7)
    c: PointOnObject(g10,g5)
    c: Coincident(g11,g10)
    c: Coincident(g11,g9)
    c: Coincident(g11,g12)
    c: Coincident(g12,g8)
    c: Coincident(g12,g13)
    c: Coincident(g13,g11)
    c: Equal(g13,g11)
    c: Equal(g11,g12)
    c: Equal(g8,g10)
    c: Equal(g8,g9)
    c: Diameter(g8) = 3.4
    c: Distance(g8,g6) = 5
FEATURE [PartDesign::Pocket] Pocket035
  BaseFeature = -> Bend009
  Direction = (0,0,-1)
  Length = 5
  Length2 = 5
  Midplane = true
  Profile = -> Sketch075
  ReferenceAxis = -> Sketch075 [N_Axis]
  Suppressed = false
  Type = 1
FEATURE [PartDesign::SubShapeBinder] Binder044
  BindCopyOnChange = 0
  BindMode = 0
  ClaimChildren = false
  Context = -> Body074 [Binder044.]
  Fuse = false
  MakeFace = true
  OffsetFill = false
  OffsetIntersection = false
  OffsetJoinType = 0
  OffsetOpenResult = false
  PartialLoad = false
  Relative = true
  Support = -> [Body073[Pocket035.Sketch075.]]
  _Version = 2
FEATURE [PartDesign::Pocket] Pocket036
  BaseFeature = -> Pad008
  Direction = (0,0,-1)
  Length = 5
  Length2 = 5
  Midplane = true
  Profile = -> Binder044
  Suppressed = false
  Type = 1
FEATURE [PartDesign::Plane] DatumPlane
  AttachmentOffset = pos=(0,0,0) rot=(0,1,0;0.523599rad)
  AttachmentSupport = -> [XZ_Plane037]
  Length = 552.693
  MapMode = 5
  Placement = pos=(0,0,0) rot=(0.935113,0.250563,0.250563;1.63783rad)
  ResizeMode = 0
  Width = 82.2624
FEATURE [PartDesign::Mirrored] Mirrored003
  BaseFeature = -> Pocket036
  MirrorPlane = -> DatumPlane
  Originals = -> [Pocket036]
  Suppressed = false
FEATURE [PartDesign::SubShapeBinder] Binder045
  BindCopyOnChange = 0
  BindMode = 0
  ClaimChildren = false
  Context = -> Body077 [Binder045.]
  Fuse = false
  MakeFace = true
  OffsetFill = false
  OffsetIntersection = false
  OffsetJoinType = 0
  OffsetOpenResult = false
  PartialLoad = false
  Relative = true
  Support = -> [Body074[Binder038.Compound037.Sketch063.]]
  _Version = 2
FEATURE [Sketcher::SketchObject] Sketch076
  AttachmentSupport = -> [XY_Plane041]
  ExternalGeometry = -> [Binder045]
  FullyConstrained = true
  MapMode = 5
  sketch-geometry (5):
    g0: LineSegment StartX=15 StartY=335 StartZ=0 EndX=62.031 EndY=297.743 EndZ=0
    g1: ArcOfCircle CenterX=-320.353 CenterY=-184.956 CenterZ=0 NormalX=0 NormalY=0 NormalZ=1 AngleXU=0 Radius=615.805 StartAngle=0.146355 EndAngle=0.900842
    g2: LineSegment StartX=288.868 StartY=-95.1511 StartZ=0 EndX=297.619 EndY=-154.51 EndZ=0
    g3: LineSegment StartX=-320.353 StartY=-184.956 StartZ=0 EndX=212.95 EndY=122.947 EndZ=0
    g4: LineSegment StartX=62.031 StartY=297.743 StartZ=0 EndX=288.868 EndY=-95.1511 EndZ=0
  constraints (12):
    c: Coincident(g0,g-4)
    c: Coincident(g1,g-4)
    c: Coincident(g1,g0)
    c: Tangent(g2,g1) = 1.5708
    c: Coincident(g3,g1)
    c: Coincident(g3,g-4)
    c: Vertical(g0,g-5)
    c: Equal(g0,g2)
    c: PointOnObject(g-3,g0)
    c: Coincident(g4,g0)
    c: Coincident(g4,g1)
    c: Perpendicular(g3,g4)
FEATURE [PartDesign::FeaturePython] BaseBend021  # WARN: FeaturePython — macro-defined, semantics opaque (R4)
  BendSide = 1
  BendSketch = -> Sketch076
  MidPlane = false
  Reverse = false
  Suppressed = false
  length = 419
  radius = 1
  thickness = 1.5
  expr: length = BaseBend020.length + composit_properties#<<Properties>>.thickness * 2
FEATURE [PartDesign::Fillet] Fillet
  Base = -> BaseBend021 [Edge10,Edge8,Edge25,Edge23]
  BaseFeature = -> BaseBend021
  Radius = 3
  SupportTransform = false
  Suppressed = false
  UseAllEdges = false
FEATURE [PartDesign::Plane] DatumPlane001
  AttachmentOffset = pos=(0,0,0) rot=(0,1,0;1.5708rad)
  AttachmentSupport = -> [Sketch062]
  Length = 411.982
  MapMode = 7
  Placement = pos=(15,335,0) rot=(-0.89718,0.312304,0.312304;4.6041rad)
  ResizeMode = 0
  Width = 515.08
FEATURE [Sketcher::SketchObject] Sketch077
  AttachmentSupport = -> [DatumPlane001]
  FullyConstrained = true
  MapMode = 5
  Placement = pos=(15,335,0) rot=(0.89718,-0.312304,-0.312304;1.67908rad)
  expr: Constraints[1] = <<Properties>>.rivet_d
  expr: Constraints[3] = BaseBend020.length
  sketch-geometry (4):
    g0: Circle CenterX=10 CenterY=7 CenterZ=0 NormalX=0 NormalY=0 NormalZ=1 AngleXU=0 Radius=1.7
    g1: Circle CenterX=10 CenterY=406 CenterZ=0 NormalX=0 NormalY=0 NormalZ=1 AngleXU=0 Radius=1.7
    g2: GeomPoint X=0 Y=413 Z=0
    g3: LineSegment StartX=0 StartY=206.5 StartZ=0 EndX=10 EndY=206.5 EndZ=0
  constraints (10):
    c: Equal(g0,g1)
    c: Diameter(g0) = 3.4
    c: PointOnObject(g2,g-2)
    c: DistanceY(g2) = 413
    c: DistanceX(g0) = 10
    c: DistanceY(g0) = 7
    c: Vertical(g1,g0)
    c: Horizontal(g3)
    c: Symmetric(g-1,g2,g3)
    c: Symmetric(g1,g0,g3)
FEATURE [PartDesign::Hole] Hole006
  BaseFeature = -> Pocket035
  CustomThreadClearance = 0
  Depth = 1
  DepthType = 0
  Diameter = 3.4
  DrillForDepth = false
  DrillPoint = 1
  DrillPointAngle = 118
  HoleCutCountersinkAngle = 90
  HoleCutCustomValues = false
  HoleCutDepth = 0
  HoleCutDiameter = 6.1
  HoleCutType = 0
  ModelThread = false
  Profile = -> Sketch077
  Reversed = true
  Suppressed = false
  Tapered = false
  TaperedAngle = 90
  ThreadClass = 0
  ThreadDepth = 1
  ThreadDepthType = 0
  ThreadDirection = 0
  ThreadFit = 0
  ThreadSize = 0
  ThreadType = 0
  Threaded = false
  UseCustomThreadClearance = false
  expr: Diameter = <<Properties>>.rivet_d
FEATURE [PartDesign::SubShapeBinder] Binder046
  BindCopyOnChange = 0
  BindMode = 0
  ClaimChildren = false
  Context = -> Body077 [Binder046.]
  Fuse = false
  MakeFace = true
  OffsetFill = false
  OffsetIntersection = false
  OffsetJoinType = 0
  OffsetOpenResult = false
  PartialLoad = false
  Relative = true
  Support = -> [Body073[Hole006.Sketch077.]]
  _Version = 2
FEATURE [Sketcher::SketchObject] Sketch078  label="pillar_magnet_fix"
  AttachmentOffset = pos=(0,0,0) rot=(0,1,0;1.5708rad)
  AttachmentSupport = -> [Sketch062]
  FullyConstrained = true
  MapMode = 7
  Placement = pos=(15,280,0) rot=(0.57735,0.57735,0.57735;2.0944rad)
  expr: Constraints[11] = <<Properties>>.rivet_d
  sketch-geometry (8):
    g0: ArcOfCircle CenterX=32.5 CenterY=244.5 CenterZ=0 NormalX=0 NormalY=0 NormalZ=1 AngleXU=0 Radius=11 StartAngle=4.71239 EndAngle=7.85398
    g1: ArcOfCircle CenterX=27.5 CenterY=244.5 CenterZ=0 NormalX=0 NormalY=0 NormalZ=1 AngleXU=0 Radius=11 StartAngle=1.5708 EndAngle=4.71239
    g2: LineSegment StartX=32.5 StartY=255.5 StartZ=0 EndX=27.5 EndY=255.5 EndZ=0
    g3: LineSegment StartX=27.5 StartY=233.5 StartZ=0 EndX=32.5 EndY=233.5 EndZ=0
    g4: Circle CenterX=30 CenterY=224.5 CenterZ=0 NormalX=0 NormalY=0 NormalZ=1 AngleXU=0 Radius=1.7
    g5: Circle CenterX=30 CenterY=264.5 CenterZ=0 NormalX=0 NormalY=0 NormalZ=1 AngleXU=0 Radius=1.7
    g6: LineSegment StartX=27.5 StartY=244.5 StartZ=0 EndX=30 EndY=244.5 EndZ=0
    g7: LineSegment StartX=32.5 StartY=244.5 StartZ=0 EndX=30 EndY=244.5 EndZ=0
  constraints (20):
    c: Tangent(g0,g2) = -1.5708
    c: Tangent(g2,g1) = -1.5708
    c: Tangent(g1,g3) = -1.5708
    c: Tangent(g3,g0) = -1.5708
    c: Equal(g0,g1)
    c: Coincident(g6,g1)
    c: Coincident(g7,g0)
    c: Coincident(g7,g6)
    c: Equal(g6,g7)
    c: Symmetric(g4,g5,g6)
    c: Equal(g4,g5)
    c: Diameter(g4) = 3.4
    c: Parallel(g6,g7)
    c: Distance(g1,g0) = 5
    c: Diameter(g0) = 22
    c: Horizontal(g1,g0)
    c: DistanceY(g4,g5) = 40
    c: DistanceY(g6) = 244.5  'height'
    c: DistanceX(g6) = 30
    c: Vertical(g4,g5)
FEATURE [PartDesign::Pocket] Pocket037
  BaseFeature = -> Hole006
  Direction = (-1,2e-16,0)
  Length = 5
  Length2 = 5
  Midplane = true
  Profile = -> Sketch078
  ReferenceAxis = -> Sketch078 [N_Axis]
  Suppressed = false
  Type = 0
FEATURE [Sketcher::SketchObject] Sketch079
  AttachmentSupport = -> [DatumPlane001]
  FullyConstrained = true
  MapMode = 5
  Placement = pos=(15,335,0) rot=(0.89718,-0.312304,-0.312304;1.67908rad)
  expr: Constraints[3] = BaseBend020.length - 111.35 mm
  sketch-geometry (2):
    g0: Circle CenterX=35 CenterY=301.65 CenterZ=0 NormalX=0 NormalY=0 NormalZ=1 AngleXU=0 Radius=1.25
    g1: Circle CenterX=35 CenterY=205.65 CenterZ=0 NormalX=0 NormalY=0 NormalZ=1 AngleXU=0 Radius=1.25
  constraints (6):
    c: Vertical(g1,g0)
    c: DistanceY(g1,g0) = 96
    c: DistanceX(g1) = 35
    c: DistanceY(g0) = 301.65
    c: Equal(g1,g0)
    c: Diameter(g1) = 2.5
FEATURE [PartDesign::SubShapeBinder] Binder047
  BindCopyOnChange = 0
  BindMode = 0
  ClaimChildren = true
  Context = -> Body077 [Binder047.]
  Fuse = false
  MakeFace = true
  OffsetFill = false
  OffsetIntersection = false
  OffsetJoinType = 0
  OffsetOpenResult = false
  PartialLoad = false
  Relative = true
  Support = -> [Body073[Sketch079.]]
  _Version = 2
FEATURE [PartDesign::Hole] Hole009
  BaseFeature = -> Pocket037
  CustomThreadClearance = 0
  Depth = 25
  DepthType = 0
  Diameter = 2.5
  DrillForDepth = false
  DrillPoint = 1
  DrillPointAngle = 118
  HoleCutCountersinkAngle = 90
  HoleCutCustomValues = false
  HoleCutDepth = 0
  HoleCutDiameter = 6.1
  HoleCutType = 0
  ModelThread = false
  Profile = -> Sketch079
  Reversed = true
  Suppressed = false
  Tapered = false
  TaperedAngle = 90
  ThreadClass = 0
  ThreadDepth = 25
  ThreadDepthType = 0
  ThreadDirection = 0
  ThreadFit = 0
  ThreadSize = 0
  ThreadType = 0
  Threaded = false
  UseCustomThreadClearance = false
FEATURE [PartDesign::Body] Body073  label="tech_sector_pillar_material_0.30ansi"
  Group = -> [Sketch062,BaseBend020,Bend009,Sketch075,Pocket035,DatumPlane001,Sketch077,Hole006,Sketch078,Pocket037,Sketch079,Hole009]
  Origin = -> Origin036
  Placement = pos=(0,0,3) rot=(0,0,1;0rad)
  Tip = -> Hole009
FEATURE [PartDesign::FeaturePython] Extend  # WARN: FeaturePython — macro-defined, semantics opaque (R4)
  BaseFeature = -> BaseBend018
  Offset = 0.02
  Refine = true
  Suppressed = false
  UseSubtraction = false
  baseObject = -> BaseBend018 [Face32]
  gap1 = 0
  gap2 = 0
  length = 0
FEATURE [PartDesign::Boolean] Boolean013
  BaseFeature = -> Extend
  Group = -> [Populate018]
  Suppressed = false
  Type = 1
  UsePlacement = false
FEATURE [PartDesign::Body] Body072  label="plexiglass_outer_material_0.30ansi"
  Group = -> [Binder037,BaseBend018,Extend,Boolean013]
  Origin = -> Origin035
  Tip = -> Extend
FEATURE [PartDesign::Plane] DatumPlane002
  AttachmentOffset = pos=(0,0,0) rot=(0,1,0;0.523599rad)
  AttachmentSupport = -> [XZ_Plane041]
  Length = 622.679
  MapMode = 5
  Placement = pos=(0,0,0) rot=(0.935113,0.250563,0.250563;1.63783rad)
  ResizeMode = 0
  Width = 540.655
FEATURE [Sketcher::SketchObject] Sketch080  label="hat_plexiglass_sketch"
  ExternalGeometry = -> [Sketch071,Sketch068]
  FullyConstrained = true
  sketch-geometry (4):
    g0: ArcOfCircle CenterX=614.788 CenterY=353 CenterZ=0 NormalX=0 NormalY=0 NormalZ=1 AngleXU=0 Radius=578.788 StartAngle=3.14159 EndAngle=3.645
    g1: LineSegment StartX=36 StartY=353 StartZ=0 EndX=36 EndY=382 EndZ=0
    g2: LineSegment StartX=112.627 StartY=65.0251 StartZ=0 EndX=107.803 EndY=73.7845 EndZ=0
    g3: LineSegment StartX=0 StartY=0 StartZ=0 EndX=112.627 EndY=65.0251 EndZ=0
  constraints (11):
    c: Coincident(g0,g-3)
    c: Vertical(g1)
    c: Coincident(g2,g-5)
    c: Tangent(g2,g0) = 1.5708
    c: Tangent(g1,g0) = 1.5708
    c: Distance(g2) = 10
    c: Coincident(g3,g-1)
    c: Coincident(g3,g2)
    c: Angle(g3) = 0.523599
    c: Angle(g2,g3) = 1.59099
    c: DistanceY(g1,g1) = 29
FEATURE [PartDesign::SubShapeBinder] Binder048
  BindCopyOnChange = 0
  BindMode = 0
  ClaimChildren = true
  Context = -> Part010 [Body078.Binder048.]
  Fuse = false
  MakeFace = true
  OffsetFill = false
  OffsetIntersection = false
  OffsetJoinType = 0
  OffsetOpenResult = false
  PartialLoad = false
  Relative = false
  Support = -> [Compound043]
  _Version = 2
FEATURE [PartDesign::FeaturePython] BaseBend022  # WARN: FeaturePython — macro-defined, semantics opaque (R4)
  BendSide = 1
  BendSketch = -> Binder048
  MidPlane = false
  Reverse = false
  Suppressed = false
  length = 96
  radius = 1
  thickness = 1.5
FEATURE [PartDesign::SubShapeBinder] Binder049
  BindCopyOnChange = 0
  BindMode = 0
  ClaimChildren = true
  Context = -> Part010 [Body078.Binder049.]
  Fuse = false
  MakeFace = false
  OffsetFill = false
  OffsetIntersection = false
  OffsetJoinType = 0
  OffsetOpenResult = false
  PartialLoad = false
  Placement = pos=(0,362,6) rot=(0.57735,0.57735,0.57735;2.0944rad)
  Relative = false
  Support = -> [Sketch073]
  _Version = 2
  expr: Support = Sketch073._self
FEATURE [PartDesign::Plane] DatumPlane003
  AttachmentOffset = pos=(0,0,0) rot=(0,1,0;0.523599rad)
  AttachmentSupport = -> [XZ_Plane043]
  Length = 648.977
  MapMode = 5
  Placement = pos=(0,0,0) rot=(0.935113,0.250563,0.250563;1.63783rad)
  ResizeMode = 0
  Width = 174.677
FEATURE [Part::Mirroring] Part__Mirroring015  label="hat_plexiglass_sketch (Mirror #19)"
  Base = (0,0,0)
  Normal = (0.5,-0.866025,0)
  Source = -> Sketch080
  expr: .Normal.x = cos(-60)
  expr: .Normal.y = sin(-60)
FEATURE [Part::Compound] Compound043  label="hat_plexiglass_bend_base"
  Links = -> [Sketch080,Part__Mirroring015]
FEATURE [PartDesign::Hole] Hole010
  BaseFeature = -> BaseBend022
  CustomThreadClearance = 0
  Depth = 1303.68
  DepthType = 1
  Diameter = 3.4
  DrillForDepth = false
  DrillPoint = 1
  DrillPointAngle = 118
  HoleCutCountersinkAngle = 90
  HoleCutCustomValues = false
  HoleCutDepth = 0
  HoleCutDiameter = 6.1
  HoleCutType = 0
  ModelThread = false
  Profile = -> Binder049
  Reversed = true
  Suppressed = false
  Tapered = false
  TaperedAngle = 90
  ThreadClass = 0
  ThreadDepth = 1303.68
  ThreadDepthType = 0
  ThreadDirection = 0
  ThreadFit = 0
  ThreadSize = 0
  ThreadType = 0
  Threaded = false
  UseCustomThreadClearance = false
  expr: Diameter = <<Properties>>.rivet_d
FEATURE [Sketcher::SketchObject] Sketch081
  AttachmentOffset = pos=(0,0,0) rot=(0,1,0;-1.0472rad)
  AttachmentSupport = -> [XZ_Plane043]
  FullyConstrained = true
  MapMode = 5
  Placement = pos=(0,0,0) rot=(-0.774597,0.447214,0.447214;4.45971rad)
  expr: Constraints[2] = <<Properties>>.rivet_d
  sketch-geometry (1):
    g0: Circle CenterX=0 CenterY=19 CenterZ=0 NormalX=0 NormalY=0 NormalZ=1 AngleXU=0 Radius=1.7
  constraints (3):
    c: PointOnObject(g0,g-2)
    c: DistanceY(g0) = 19
    c: Diameter(g0) = 3.4
FEATURE [PartDesign::Mirrored] Mirrored005
  BaseFeature = -> Hole010
  MirrorPlane = -> DatumPlane003
  Originals = -> [Hole010]
  Refine = true
  Suppressed = false
FEATURE [PartDesign::SubShapeBinder] Binder050
  BindCopyOnChange = 0
  BindMode = 0
  ClaimChildren = true
  Context = -> Part010 [Body078.Binder050.]
  Fuse = false
  MakeFace = true
  OffsetFill = false
  OffsetIntersection = false
  OffsetJoinType = 0
  OffsetOpenResult = false
  PartialLoad = false
  Relative = false
  Support = -> [Body075[Binder039.Array005.Compound039.Sketch068.]]
  _Version = 2
FEATURE [Sketcher::SketchObject] Sketch082
  AttachmentSupport = -> [XY_Plane043]
  FullyConstrained = true
  MapMode = 5
FEATURE [Sketcher::SketchObject] Sketch083
  AttachmentSupport = -> [XY_Plane037]
  ExternalGeometry = -> [Binder038]
  FullyConstrained = true
  MapMode = 5
  expr: Constraints[4] = <<Properties>>.rivet_d
  sketch-geometry (2):
    g0: LineSegment StartX=212.95 StartY=122.947 StartZ=0 EndX=201.691 EndY=116.447 EndZ=0
    g1: Circle CenterX=201.691 CenterY=116.447 CenterZ=0 NormalX=0 NormalY=0 NormalZ=1 AngleXU=0 Radius=1.7
  constraints (5):
    c: Coincident(g0,g-3)
    c: Perpendicular(g-3,g0)
    c: Distance(g0) = 13
    c: Coincident(g1,g0)
    c: Diameter(g1) = 3.4
FEATURE [PartDesign::Hole] Hole011
  BaseFeature = -> Mirrored003
  CustomThreadClearance = 0
  Depth = 25
  DepthType = 0
  Diameter = 3.4
  DrillForDepth = false
  DrillPoint = 1
  DrillPointAngle = 118
  HoleCutCountersinkAngle = 90
  HoleCutCustomValues = false
  HoleCutDepth = 0
  HoleCutDiameter = 6.1
  HoleCutType = 0
  ModelThread = false
  Profile = -> Sketch083
  Reversed = true
  Suppressed = false
  Tapered = false
  TaperedAngle = 90
  ThreadClass = 0
  ThreadDepth = 25
  ThreadDepthType = 0
  ThreadDirection = 0
  ThreadFit = 0
  ThreadSize = 0
  ThreadType = 0
  Threaded = false
  UseCustomThreadClearance = false
  expr: Diameter = <<Properties>>.rivet_d
FEATURE [PartDesign::Body] Body074  label="tech_sector_hor"
  Group = -> [Binder038,Pad008,Binder044,Pocket036,DatumPlane,Mirrored003,Sketch083,Hole011]
  Origin = -> Origin037
  Tip = -> Hole011
FEATURE [Sketcher::SketchObject] Sketch084
  AttachmentSupport = -> [Binder046]
  ExternalGeometry = -> [Binder046]
  FullyConstrained = false
  MapMode = 5
  Placement = pos=(168.839,213.132,5.44e-14) rot=(0.239007,0.686613,0.686613;2.67238rad)
  sketch-geometry (3):
    g0: Circle CenterX=186.261 CenterY=10.25 CenterZ=0 NormalX=0 NormalY=0 NormalZ=1 AngleXU=0 Radius=1.69397
    g1: Circle CenterX=186.261 CenterY=408.75 CenterZ=0 NormalX=0 NormalY=0 NormalZ=1 AngleXU=0 Radius=1.72481
    g2: GeomPoint X=186.261 Y=209.5 Z=0
  constraints (4):
    c: Symmetric(g-4,g-3,g2)
    c: Symmetric(g1,g0,g2)
    c: Vertical(g-3,g0)
    c: DistanceY(g-3,g0) = 0.25
FEATURE [PartDesign::Hole] Hole007
  BaseFeature = -> Fillet
  CustomThreadClearance = 0
  Depth = 25
  DepthType = 0
  Diameter = 3.4
  DrillForDepth = false
  DrillPoint = 1
  DrillPointAngle = 118
  HoleCutCountersinkAngle = 90
  HoleCutCustomValues = false
  HoleCutDepth = 0
  HoleCutDiameter = 6.1
  HoleCutType = 0
  ModelThread = false
  Profile = -> Sketch084
  Reversed = true
  Suppressed = false
  Tapered = false
  TaperedAngle = 90
  ThreadClass = 0
  ThreadDepth = 25
  ThreadDepthType = 0
  ThreadDirection = 0
  ThreadFit = 0
  ThreadSize = 0
  ThreadType = 0
  Threaded = false
  UseCustomThreadClearance = false
  expr: Diameter = <<Properties>>.rivet_d
FEATURE [PartDesign::Hole] Hole008
  BaseFeature = -> Hole007
  CustomThreadClearance = 0
  Depth = 25
  DepthType = 0
  Diameter = 3.4
  DrillForDepth = false
  DrillPoint = 1
  DrillPointAngle = 118
  HoleCutCountersinkAngle = 90
  HoleCutCustomValues = false
  HoleCutDepth = 0
  HoleCutDiameter = 6.1
  HoleCutType = 0
  ModelThread = false
  Profile = -> Binder047
  Reversed = true
  Suppressed = false
  Tapered = false
  TaperedAngle = 90
  ThreadClass = 0
  ThreadDepth = 25
  ThreadDepthType = 0
  ThreadDirection = 0
  ThreadFit = 0
  ThreadSize = 0
  ThreadType = 0
  Threaded = false
  UseCustomThreadClearance = false
  expr: Diameter = <<Properties>>.rivet_d
FEATURE [PartDesign::Mirrored] Mirrored004
  BaseFeature = -> Hole008
  MirrorPlane = -> DatumPlane002
  Originals = -> [Hole007,Hole008]
  Suppressed = false
FEATURE [PartDesign::Body] Body077  label="tech_sector_plexiglass_material_0.30ansi"
  Group = -> [Binder045,Sketch076,BaseBend021,Fillet,Binder046,Hole007,Binder047,Hole008,DatumPlane002,Mirrored004,Sketch084]
  Origin = -> Origin041
  Tip = -> Mirrored004
FEATURE [Part::Extrusion] Extrude015  label="magnet_fix"
  Base = -> Circle
  Dir = (0,0,1)
  DirMode = 2
  FaceMakerClass = Part::FaceMakerBullseye
  LengthFwd = 15
  LengthRev = 0
  Placement = pos=(0,308.872,248) rot=(0,1,0;1.5708rad)
  Solid = true
  Symmetric = false
  expr: .Placement.Base.y = <<Properties>>.total_length - 43 mm
FEATURE [Part::Mirroring] Part__Mirroring016  label="magnet_fix (Mirror #20)"
  Base = (0,0,0)
  Normal = (0.5,-0.866025,0)
  Source = -> Extrude015
  expr: .Normal.x = cos(-60)
  expr: .Normal.y = sin(-60)
FEATURE [Sketcher::SketchObject] Sketch098
  AttachmentSupport = -> [XY_Plane038]
  FullyConstrained = true
  MapMode = 5
  sketch-geometry (1):
    g0: Circle CenterX=0 CenterY=0 CenterZ=0 NormalX=0 NormalY=0 NormalZ=1 AngleXU=0 Radius=3.25
  constraints (2):
    c: Coincident(g0,g-1)
    c: Diameter(g0) = 6.5
FEATURE [PartDesign::SubShapeBinder] Binder054  label="socket_fixture"
  BindCopyOnChange = 0
  BindMode = 0
  ClaimChildren = false
  Context = -> Part010 [Body075.Binder054.]
  Fuse = false
  MakeFace = true
  OffsetFill = false
  OffsetIntersection = false
  OffsetJoinType = 0
  OffsetOpenResult = false
  PartialLoad = false
  Placement = pos=(69,65,0) rot=(0,0,1;3.14159rad)
  Relative = false
  Support = -> [<external socket_fixture.FCStd>#Sketch003]
  _Version = 2
  expr: Support = socket_fixture#<<fix_holes>>._self
FEATURE [PartDesign::SubShapeBinder] Binder055  label="driver_fixture"
  BindCopyOnChange = 0
  BindMode = 0
  ClaimChildren = false
  Context = -> Part010 [Body075.Binder055.]
  Fuse = false
  MakeFace = true
  OffsetFill = false
  OffsetIntersection = false
  OffsetJoinType = 0
  OffsetOpenResult = false
  PartialLoad = false
  Placement = pos=(-24,152,0) rot=(0,0,1;0rad)
  Relative = false
  Support = -> [<external UET-VAS-060A20_12V_IP20.FCStd>#Sketch001]
  _Version = 2
  expr: Support = <<UET-VAS-060A20_12V_IP20>>#<<holes>>._self
FEATURE [Sketcher::SketchObject] Sketch108
  AttachmentSupport = -> [XY_Plane038]
  ExternalGeometry = -> [Binder039]
  FullyConstrained = true
  MapMode = 5
  expr: Constraints[3] = <<Properties>>.rivet_d
  sketch-geometry (2):
    g0: LineSegment StartX=112.627 StartY=65.0251 StartZ=0 EndX=101.801 EndY=58.7751 EndZ=0
    g1: Circle CenterX=101.801 CenterY=58.7751 CenterZ=0 NormalX=0 NormalY=0 NormalZ=1 AngleXU=0 Radius=1.7
  constraints (5):
    c: Coincident(g0,g-3)
    c: PointOnObject(g-1,g0)
    c: Coincident(g1,g0)
    c: Diameter(g1) = 3.4
    c: Distance(g0) = 12.5
FEATURE [PartDesign::Pocket] Pocket054
  BaseFeature = -> Pocket032
  Direction = (0,0,-1)
  Length = 5
  Length2 = 5
  Profile = -> Sketch108
  ReferenceAxis = -> Sketch108 [N_Axis]
  Reversed = true
  Suppressed = false
  Type = 0
FEATURE [PartDesign::PolarPattern] PolarPattern
  Angle = 360
  Axis = -> Z_Axis038
  BaseFeature = -> Pocket054
  Mode = 0
  Occurrences = 3
  Offset = 120
  Originals = -> [Pocket032,Pocket054]
  Suppressed = false
FEATURE [PartDesign::Hole] Hole015
  BaseFeature = -> PolarPattern
  CustomThreadClearance = 0
  Depth = 25
  DepthType = 0
  Diameter = 27.5
  DrillForDepth = false
  DrillPoint = 1
  DrillPointAngle = 118
  HoleCutCountersinkAngle = 90
  HoleCutCustomValues = false
  HoleCutDepth = 0
  HoleCutDiameter = 0
  HoleCutType = 0
  ModelThread = false
  Profile = -> Sketch098
  Reversed = true
  Suppressed = false
  Tapered = false
  TaperedAngle = 90
  ThreadClass = 0
  ThreadDepth = 23.5
  ThreadDepthType = 0
  ThreadDirection = 0
  ThreadFit = 0
  ThreadSize = 0
  ThreadType = 0
  Threaded = false
  UseCustomThreadClearance = false
  expr: Diameter = <<sleeve_inner_sketch>>.Constraints.outer_r * 2 + 1.5 mm
FEATURE [PartDesign::Hole] Hole016
  BaseFeature = -> Hole015
  CustomThreadClearance = 0
  Depth = 25
  DepthType = 0
  Diameter = 3.4
  DrillForDepth = false
  DrillPoint = 1
  DrillPointAngle = 118
  HoleCutCountersinkAngle = 90
  HoleCutCustomValues = false
  HoleCutDepth = 0
  HoleCutDiameter = 0
  HoleCutType = 0
  ModelThread = false
  Profile = -> Binder054
  Reversed = true
  Suppressed = false
  Tapered = false
  TaperedAngle = 90
  ThreadClass = 0
  ThreadDepth = 23.5
  ThreadDepthType = 0
  ThreadDirection = 0
  ThreadFit = 0
  ThreadSize = 0
  ThreadType = 0
  Threaded = false
  UseCustomThreadClearance = false
  expr: Diameter = <<Properties>>.rivet_d
FEATURE [PartDesign::Hole] Hole017
  BaseFeature = -> Hole016
  CustomThreadClearance = 0
  Depth = 25
  DepthType = 0
  Diameter = 3.4
  DrillForDepth = false
  DrillPoint = 1
  DrillPointAngle = 118
  HoleCutCountersinkAngle = 90
  HoleCutCustomValues = false
  HoleCutDepth = 0
  HoleCutDiameter = 0
  HoleCutType = 0
  ModelThread = false
  Profile = -> Binder055
  Reversed = true
  Suppressed = false
  Tapered = false
  TaperedAngle = 90
  ThreadClass = 0
  ThreadDepth = 23.5
  ThreadDepthType = 0
  ThreadDirection = 0
  ThreadFit = 0
  ThreadSize = 0
  ThreadType = 0
  Threaded = false
  UseCustomThreadClearance = false
FEATURE [PartDesign::Mirrored] Mirrored006
  BaseFeature = -> Hole017
  MirrorPlane = -> YZ_Plane038
  Originals = -> [Hole016]
  Refine = true
  Suppressed = false
FEATURE [PartDesign::SubShapeBinder] Binder061
  BindCopyOnChange = 0
  BindMode = 0
  ClaimChildren = false
  Context = -> Part007 [Body021.Binder061.]
  Fuse = false
  MakeFace = true
  OffsetFill = false
  OffsetIntersection = false
  OffsetJoinType = 0
  OffsetOpenResult = false
  PartialLoad = false
  Relative = false
  Support = -> [Body020[Pocket022.Sketch040.]]
  _Version = 2
FEATURE [PartDesign::SubShapeBinder] Binder062
  BindCopyOnChange = 0
  BindMode = 0
  ClaimChildren = false
  Context = -> Part007 [Body021.Binder062.]
  Fuse = false
  MakeFace = true
  OffsetFill = false
  OffsetIntersection = false
  OffsetJoinType = 0
  OffsetOpenResult = false
  PartialLoad = false
  Relative = false
  Support = -> [Body020[Pocket029.Sketch064.]]
  _Version = 2
FEATURE [Sketcher::SketchObject] Sketch109
  AttachmentSupport = -> [XY_Plane029]
  ExternalGeometry = -> [Binder061]
  FullyConstrained = false
  MapMode = 5
  sketch-geometry (19):
    g0: ArcOfCircle CenterX=291.996 CenterY=172.865 CenterZ=0 NormalX=0 NormalY=0 NormalZ=1 AngleXU=0 Radius=1 StartAngle=5.23599 EndAngle=6.98132
    g1: LineSegment StartX=5.51e-14 StartY=239 StartZ=0 EndX=5.51e-14 EndY=240 EndZ=0
    g2: LineSegment StartX=292.496 StartY=171.999 StartZ=0 EndX=287.719 EndY=169.241 EndZ=0
    g3: ArcOfCircle CenterX=287.219 CenterY=170.107 CenterZ=0 NormalX=0 NormalY=0 NormalZ=1 AngleXU=0 Radius=1 StartAngle=3.90153 EndAngle=5.23599
    g4: LineSegment StartX=5.51e-14 StartY=239 StartZ=0 EndX=5.51e-14 EndY=224 EndZ=0
    g5: ArcOfCircle CenterX=243.002 CenterY=128.086 CenterZ=0 NormalX=0 NormalY=0 NormalZ=1 AngleXU=0 Radius=60 StartAngle=0.759936 EndAngle=1.27733
    g6: GeomPoint X=287.033 Y=168.845 Z=0
    g7: GeomPoint X=293.528 Y=172.595 Z=0
    g8: ArcOfCircle CenterX=1.26657 CenterY=-621.999 CenterZ=0 NormalX=0 NormalY=0 NormalZ=1 AngleXU=0 Radius=862 StartAngle=1.25533 EndAngle=1.57227
    g9: LineSegment StartX=5.28e-14 StartY=220.8 StartZ=0 EndX=5.51e-14 EndY=240 EndZ=0
    g10: ArcOfCircle CenterX=0 CenterY=-641.2 CenterZ=0 NormalX=0 NormalY=0 NormalZ=1 AngleXU=0 Radius=862 StartAngle=1.25386 EndAngle=1.5708
    g11: LineSegment StartX=5.51e-14 StartY=240 StartZ=0 EndX=268.713 EndY=197.462 EndZ=0
    g12: LineSegment StartX=5.28e-14 StartY=220.8 StartZ=0 EndX=268.65 EndY=177.867 EndZ=0
    g13: ArcOfCircle CenterX=0 CenterY=-676.059 CenterZ=0 NormalX=0 NormalY=0 NormalZ=1 AngleXU=0 Radius=900.059 StartAngle=1.27733 EndAngle=1.5708
    g14: Circle CenterX=268.65 CenterY=177.867 CenterZ=0 NormalX=0 NormalY=0 NormalZ=1 AngleXU=0 Radius=4
    g15: LineSegment StartX=0 StartY=0 StartZ=0 EndX=301.632 EndY=174.148 EndZ=0
    g16: LineSegment StartX=0 StartY=0 StartZ=0 EndX=-15 EndY=25.9808 EndZ=0
    g17: ArcOfCircle CenterX=262.507 CenterY=178.449 CenterZ=0 NormalX=0 NormalY=0 NormalZ=1 AngleXU=0 Radius=20 StartAngle=0.698132 EndAngle=1.25533
    g18: LineSegment StartX=292.762 StartY=173.508 StartZ=0 EndX=277.828 EndY=191.305 EndZ=0
  constraints (51):
    c: Tangent(g17,g8) = -1.5708
    c: Vertical(g1)
    c: PointOnObject(g1,g-2)
    c: Angle(g2) = -2.61799
    c: Tangent(g2,g0) = 1.5708
    c: DistanceY(g1,g1) = 1
    c: Tangent(g3,g2) = 1.5708
    c: Radius(g3) = 1
    c: Equal(g3,g0)
    c: Coincident(g4,g1)
    c: Vertical(g4)
    c: Distance(g4) = 15
    c: Tangent(g5,g3) = 1.5708
    c: PointOnObject(g7,g2)
    c: PointOnObject(g6,g2)
    c: PointOnObject(g6,g5)
    c: Coincident(g8,g1)
    c: PointOnObject(g9,g-2)
    c: DistanceY(g9,g4) = 3.2
    c: Coincident(g9,g1)
    c: Radius(g8) = 862  'outer_r'
    c: Distance(g6,g7) = 7.5
    c: PointOnObject(g10,g-2)
    c: Coincident(g11,g1)
    c: Coincident(g11,g17)
    c: Coincident(g12,g10)
    c: Coincident(g12,g10)
    c: Equal(g10,g8)
    c: Equal(g12,g11)
    c: Coincident(g10,g9)
    c: PointOnObject(g13,g-2)
    c: Coincident(g13,g4)
    c: Tangent(g13,g5) = -1.5708
    c: Coincident(g14,g10)
    c: Tangent(g14,g5)
    c: Radius(g14) = 4
    c: Coincident(g15,g-1)
    c: Angle(g15) = 0.523599
    c: Distance(g6,g15) = 2.7076
    c: DistanceY(g1) = 240
    c: Coincident(g16,g15)
    c: Perpendicular(g15,g16)
    c: Distance(g7,g16) = 340.5
    c: Tangent(g18,g0) = -1.5708
    c: Angle(g18) = 2.26893
    c: Tangent(g17,g18) = -1.5708
    c: PointOnObject(g8,g-5)
    c: Radius(g17) = 20
    c: PointOnObject(g7,g18)
    c: Radius(g5) = 60
    c: Distance(g16) = 30
FEATURE [PartDesign::Pad] Pad014
  Direction = (0,0,1)
  Length = 3
  Length2 = 10
  Profile = -> Sketch109
  ReferenceAxis = -> Sketch109 [N_Axis]
  Suppressed = false
  Type = 0
FEATURE [PartDesign::Mirrored] Mirrored008
  BaseFeature = -> Pad014
  MirrorPlane = -> Sketch109 [V_Axis]
  Originals = -> [Pad014]
  Refine = true
  Suppressed = false
FEATURE [PartDesign::Pocket] Pocket055
  BaseFeature = -> Mirrored008
  Direction = (0,0,-1)
  Length = 5
  Length2 = 5
  Profile = -> Binder062
  Reversed = true
  Suppressed = false
  Type = 0
FEATURE [PartDesign::Body] Body021
  Group = -> [Binder061,Binder062,Sketch109,Pad014,Mirrored008,Pocket055]
  Origin = -> Origin029
  Placement = pos=(0,0,0) rot=(1,0,0;0.116239rad)
  Tip = -> Pocket055
FEATURE [Sketcher::SketchObject] Sketch110
  AttachmentOffset = pos=(0,333,0) rot=(0,0,1;0rad)
  AttachmentSupport = -> [XY_Plane011]
  FullyConstrained = true
  MapMode = 5
  Placement = pos=(0,333,0) rot=(0,0,1;0rad)
  sketch-geometry (2):
    g0: Circle CenterX=0 CenterY=26.3 CenterZ=0 NormalX=0 NormalY=0 NormalZ=1 AngleXU=0 Radius=2.75
    g1: Circle CenterX=0 CenterY=-26.3 CenterZ=0 NormalX=0 NormalY=0 NormalZ=1 AngleXU=0 Radius=2.75
  constraints (5):
    c: PointOnObject(g0,g-2)
    c: Equal(g1,g0)
    c: Diameter(g1) = 5.5
    c: Symmetric(g1,g0,g-1)
    c: DistanceY(g1,g0) = 52.6
FEATURE [PartDesign::PolarPattern] PolarPattern002
  Angle = 360
  Axis = -> Z_Axis011
  BaseFeature = -> Pad002
  Mode = 0
  Occurrences = 3
  Offset = 120
  Suppressed = false
FEATURE [Sketcher::SketchObject] Sketch112
  AttachmentSupport = -> [XY_Plane010]
  FullyConstrained = true
  MapMode = 5
  sketch-geometry (2):
    g0: Circle CenterX=0 CenterY=311.872 CenterZ=0 NormalX=0 NormalY=0 NormalZ=1 AngleXU=0 Radius=2.75
    g1: Circle CenterX=0 CenterY=276.872 CenterZ=0 NormalX=0 NormalY=0 NormalZ=1 AngleXU=0 Radius=2.75
  constraints (6):
    c: PointOnObject(g0,g-2)
    c: PointOnObject(g1,g-2)
    c: Equal(g1,g0)
    c: Diameter(g1) = 5.5
    c: DistanceY(g1,g0) = 35
    c: DistanceY(g1) = 276.872
FEATURE [Sketcher::SketchObject] Sketch113
  AttachmentSupport = -> [XY_Plane010]
  FullyConstrained = true
  MapMode = 5
  sketch-geometry (9):
    g0: LineSegment StartX=-22.5 StartY=-136 StartZ=0 EndX=-22.5 EndY=-161 EndZ=0
    g1: LineSegment StartX=-22.5 StartY=-161 StartZ=0 EndX=22.5 EndY=-161 EndZ=0
    g2: LineSegment StartX=22.5 StartY=-161 StartZ=0 EndX=22.5 EndY=-136 EndZ=0
    g3: LineSegment StartX=22.5 StartY=-136 StartZ=0 EndX=-22.5 EndY=-136 EndZ=0
    g4: GeomPoint X=0 Y=-148.5 Z=0
    g5: Circle CenterX=22.5 CenterY=-161 CenterZ=0 NormalX=0 NormalY=0 NormalZ=1 AngleXU=0 Radius=2.75
    g6: Circle CenterX=22.5 CenterY=-136 CenterZ=0 NormalX=0 NormalY=0 NormalZ=1 AngleXU=0 Radius=2.75
    g7: Circle CenterX=-22.5 CenterY=-136 CenterZ=0 NormalX=0 NormalY=0 NormalZ=1 AngleXU=0 Radius=2.75
    g8: Circle CenterX=-22.5 CenterY=-161 CenterZ=0 NormalX=0 NormalY=0 NormalZ=1 AngleXU=0 Radius=2.75
  constraints (21):
    c: Coincident(g0,g1)
    c: Coincident(g1,g2)
    c: Coincident(g2,g3)
    c: Coincident(g3,g0)
    c: Horizontal(g1)
    c: Horizontal(g3)
    c: Vertical(g0)
    c: Vertical(g2)
    c: Symmetric(g1,g0,g4)
    c: PointOnObject(g4,g-2)
    c: Coincident(g5,g1)
    c: Coincident(g6,g2)
    c: Coincident(g7,g0)
    c: Coincident(g8,g0)
    c: Equal(g5,g8)
    c: Equal(g5,g7)
    c: Equal(g5,g6)
    c: Diameter(g5) = 5.5
    c: DistanceY(g2,g2) = 25
    c: DistanceX(g1,g1) = 45
    c: DistanceY(g6) = -136
FEATURE [App::Link] Link006  label="Body084"
  LinkedObject = -> <external module.FCStd>#Body
FEATURE [Part::FeaturePython] Populate019  label="Populate Populate LinearArray with LinearArray001 with Body084"  # WARN: FeaturePython — macro-defined, semantics opaque (R4)
  Copying = 0
  ExposePlacement = false
  MarkerShape = 1
  MarkerSize = 0
  NumElements = 0
  Object = -> Link006
  OutputCompounding = 1
  Placement = pos=(14.5,181.372,1401) rot=(0.57735,0.57735,0.57735;2.0944rad)
  PlacementsTo = -> Populate
  Referencing = 0
  Type = lattice2PopulateCopies.LatticePopulateCopies
  isLattice = 0
  expr: Placement = <<modules_holes>>.Placement * placement(vector(0; 0; 14.5); rotation(0; 0; 0))
FEATURE [Sketcher::SketchObject] Sketch118
  AttachmentSupport = -> [XZ_Plane015]
  FullyConstrained = true
  MapMode = 5
  Placement = pos=(0,0,0) rot=(1,0,0;1.5708rad)
  expr: Constraints[10] = <<pillar_base_sketch>>.Constraints.length / 2 - 2 mm
  expr: Constraints[9] = -<<pillar_bottom_BaseBend>>.length / 2
  sketch-geometry (11):
    g0: Circle CenterX=-43 CenterY=9 CenterZ=0 NormalX=0 NormalY=0 NormalZ=1 AngleXU=0 Radius=1.7
    g1: Circle CenterX=-43 CenterY=40.3333 CenterZ=0 NormalX=0 NormalY=0 NormalZ=1 AngleXU=0 Radius=1.7
    g2: Circle CenterX=-43 CenterY=103 CenterZ=0 NormalX=0 NormalY=0 NormalZ=1 AngleXU=0 Radius=1.7
    g3: LineSegment StartX=-43 StartY=9 StartZ=0 EndX=-43 EndY=40.3333 EndZ=0
    g4: GeomPoint X=-50.5 Y=0 Z=0
    g5: GeomPoint X=-43 Y=110 Z=0
    g6: LineSegment StartX=-43 StartY=103 StartZ=0 EndX=-43 EndY=110 EndZ=0
    g7: LineSegment StartX=-43 StartY=9 StartZ=0 EndX=-43 EndY=0 EndZ=0
    g8: LineSegment StartX=-43 StartY=40.3333 StartZ=0 EndX=-43 EndY=71.6667 EndZ=0
    g9: LineSegment StartX=-43 StartY=71.6667 StartZ=0 EndX=-43 EndY=103 EndZ=0
    g10: Circle CenterX=-43 CenterY=71.6667 CenterZ=0 NormalX=0 NormalY=0 NormalZ=1 AngleXU=0 Radius=1.7
  constraints (27):
    c: Equal(g0,g1)
    c: Equal(g0,g2)
    c: Diameter(g0) = 3.4
    c: Coincident(g3,g0)
    c: Coincident(g3,g1)
    c: Vertical(g3)
    c: Coincident(g8,g1)
    c: Coincident(g9,g2)
    c: PointOnObject(g4,g-1)
    c: DistanceX(g4) = -50.5
    c: DistanceX(g4,g0) = 7.5
    c: DistanceY(g5) = 110
    c: Coincident(g6,g2)
    c: Coincident(g6,g5)
    c: Vertical(g6)
    c: Coincident(g7,g0)
    c: PointOnObject(g7,g-1)
    c: Vertical(g7)
    c: DistanceY(g7,g7) = 9
    c: DistanceY(g6,g6) = 7
    c: Coincident(g8,g9)
    c: Vertical(g8)
    c: Vertical(g9)
    c: Equal(g3,g8)
    c: Equal(g8,g9)
    c: Coincident(g10,g8)
    c: Equal(g0,g10)
FEATURE [PartDesign::Pocket] Pocket063
  BaseFeature = -> Pocket031
  Direction = (0,1,-2e-16)
  Length = 5
  Length2 = 5
  Profile = -> Sketch118
  ReferenceAxis = -> Sketch118 [N_Axis]
  Reversed = true
  Suppressed = false
  Type = 0
FEATURE [PartDesign::SubShapeBinder] Binder072
  BindCopyOnChange = 0
  BindMode = 0
  ClaimChildren = true
  Context = -> Body010 [Binder072.]
  Fuse = false
  MakeFace = true
  OffsetFill = false
  OffsetIntersection = false
  OffsetJoinType = 0
  OffsetOpenResult = false
  PartialLoad = false
  Relative = true
  Support = -> [Body011[Pocket063.Sketch118.]]
  _Version = 2
FEATURE [PartDesign::Fillet] Fillet001
  Base = -> Bend [Edge65,Edge66,Edge8,Edge64,Edge50,Edge2]
  BaseFeature = -> Bend
  Radius = 5
  SupportTransform = false
  Suppressed = false
  UseAllEdges = false
FEATURE [PartDesign::Hole] Hole005
  BaseFeature = -> Fillet001
  CustomThreadClearance = 0
  Depth = 286.27
  DepthType = 1
  Diameter = 3.4
  DrillForDepth = false
  DrillPoint = 1
  DrillPointAngle = 118
  HoleCutCountersinkAngle = 90
  HoleCutCustomValues = false
  HoleCutDepth = 0
  HoleCutDiameter = 6.1
  HoleCutType = 0
  ModelThread = false
  Profile = -> Sketch066
  Reversed = true
  Suppressed = false
  Tapered = false
  TaperedAngle = 90
  ThreadClass = 0
  ThreadDepth = 286.27
  ThreadDepthType = 0
  ThreadDirection = 0
  ThreadFit = 0
  ThreadSize = 0
  ThreadType = 0
  Threaded = false
  UseCustomThreadClearance = false
  expr: Diameter = <<Properties>>.rivet_d
FEATURE [PartDesign::Pocket] Pocket030
  BaseFeature = -> Hole005
  Direction = (0,0,-1)
  Length = 5
  Length2 = 5
  Profile = -> Sketch067
  ReferenceAxis = -> Sketch067 [N_Axis]
  Reversed = true
  Suppressed = false
  Type = 0
FEATURE [PartDesign::Pocket] Pocket034
  BaseFeature = -> Pocket030
  Direction = (-1,0,0)
  Length = 5
  Length2 = 5
  Midplane = true
  Profile = -> Sketch073
  ReferenceAxis = -> Sketch073 [N_Axis]
  Suppressed = false
  Type = 1
FEATURE [PartDesign::Fillet] Fillet002
  Base = -> BaseBend004 [Edge10,Edge39,Edge41,Edge8]
  BaseFeature = -> BaseBend004
  Radius = 5
  SupportTransform = false
  Suppressed = false
  UseAllEdges = false
FEATURE [PartDesign::Pad] Pad
  BaseFeature = -> Fillet002
  Direction = (0,-1,2e-16)
  Length = 2
  Length2 = 10
  Profile = -> Sketch009
  ReferenceAxis = -> Sketch009 [N_Axis]
  Reversed = true
  Suppressed = false
  Type = 0
  expr: Length = <<pillar_BaseBend>>.thickness
FEATURE [PartDesign::Boolean] Boolean011
  BaseFeature = -> Pad
  Group = -> [Compound030]
  Refine = true
  Suppressed = false
  Type = 1
  UsePlacement = false
  expr: Group = <<pillar_cut1>>._self
FEATURE [PartDesign::Hole] Hole019
  BaseFeature = -> Boolean011
  CustomThreadClearance = 0
  Depth = 3405.27
  DepthType = 1
  Diameter = 3.4
  DrillForDepth = false
  DrillPoint = 1
  DrillPointAngle = 118
  HoleCutCountersinkAngle = 90
  HoleCutCustomValues = false
  HoleCutDepth = 0
  HoleCutDiameter = 6.1
  HoleCutType = 0
  ModelThread = false
  Profile = -> Binder072
  Suppressed = false
  Tapered = false
  TaperedAngle = 90
  ThreadClass = 0
  ThreadDepth = 3405.27
  ThreadDepthType = 0
  ThreadDirection = 0
  ThreadFit = 0
  ThreadSize = 0
  ThreadType = 0
  Threaded = false
  UseCustomThreadClearance = false
  expr: Diameter = <<Properties>>.rivet_d
FEATURE [PartDesign::Body] Body010  label="pillar_material_0.30ansi"
  Group = -> [Binder002,BaseBend004,Sketch009,Fillet002,Pad,Boolean011,Binder072,Hole019]
  Origin = -> Origin014
  Tip = -> Hole019
FEATURE [PartDesign::Fillet] Fillet003
  Base = -> BaseBend017 [Edge23,Edge10,Edge25,Edge8]
  BaseFeature = -> BaseBend017
  Placement = pos=(0,0,481) rot=(0,0,1;0rad)
  Radius = 5
  SupportTransform = false
  Suppressed = false
  UseAllEdges = false
FEATURE [PartDesign::Boolean] Boolean012
  BaseFeature = -> Fillet003
  Group = -> [Compound032]
  Suppressed = false
  Type = 1
  UsePlacement = false
  expr: Group = <<dec_corner_cut1>>._self
FEATURE [PartDesign::Body] Body013  label="dec_corner_material_0.30ansi"
  Group = -> [Binder035,BaseBend017,Fillet003,Boolean012]
  Origin = -> Origin017
  Tip = -> Boolean012
FEATURE [Sketcher::SketchObject] Sketch119
  AttachmentSupport = -> [XY_Plane018]
  FullyConstrained = true
  MapMode = 5
  sketch-geometry (2):
    g0: LineSegment StartX=37.5 StartY=-1.5 StartZ=0 EndX=-37.5 EndY=-1.5 EndZ=0
    g1: LineSegment StartX=-37.5 StartY=-1.5 StartZ=0 EndX=-37.5 EndY=27 EndZ=0
  constraints (6):
    c: Coincident(g1,g0)
    c: Vertical(g1)
    c: DistanceY(g0) = -1.5
    c: Symmetric(g0,g0,g-2)
    c: DistanceX(g0,g0) = 75
    c: DistanceY(g1) = 27
FEATURE [PartDesign::FeaturePython] BaseBend029  # WARN: FeaturePython — macro-defined, semantics opaque (R4)
  BendSide = 1
  BendSketch = -> Sketch119
  MidPlane = false
  Placement = pos=(0,0,1588) rot=(0,0,1;0rad)
  Reverse = false
  Suppressed = false
  length = 96
  radius = 2
  thickness = 0.5
FEATURE [Sketcher::SketchObject] Sketch120
  AttachmentOffset = pos=(0,1588,0) rot=(0,0,1;0rad)
  AttachmentSupport = -> [XZ_Plane018]
  FullyConstrained = true
  MapMode = 5
  Placement = pos=(0,3.526e-13,1588) rot=(1,0,0;1.5708rad)
  expr: .AttachmentOffset.Base.y = BaseBend029.Placement.Base.z
  sketch-geometry (5):
    g0: ArcOfCircle CenterX=-35.5 CenterY=13.8267 CenterZ=0 NormalX=0 NormalY=0 NormalZ=1 AngleXU=0 Radius=13.8267 StartAngle=4.71239 EndAngle=5.38367
    g1: ArcOfCircle CenterX=-18.3 CenterY=-7.82667 CenterZ=0 NormalX=0 NormalY=0 NormalZ=1 AngleXU=0 Radius=13.8267 StartAngle=1.5708 EndAngle=2.24207
    g2: LineSegment StartX=-18.3 StartY=6 StartZ=0 EndX=40 EndY=6 EndZ=0
    g3: LineSegment StartX=40 StartY=6 StartZ=0 EndX=40 EndY=0 EndZ=0
    g4: LineSegment StartX=40 StartY=0 StartZ=0 EndX=-35.5 EndY=1.42e-14 EndZ=0
  constraints (15):
    c: PointOnObject(g0,g-1)
    c: Horizontal(g2)
    c: Coincident(g3,g2)
    c: PointOnObject(g3,g-1)
    c: Vertical(g3)
    c: Coincident(g4,g3)
    c: Coincident(g4,g0)
    c: Tangent(g4,g0)
    c: Equal(g0,g1)
    c: DistanceX(g0) = -35.5
    c: Tangent(g2,g1) = 1.5708
    c: Tangent(g1,g0) = 1.5708
    c: DistanceY(g3,g3) = 6
    c: DistanceX(g1) = -18.3
    c: DistanceX(g3) = 40
FEATURE [PartDesign::Pocket] Pocket064
  BaseFeature = -> BaseBend029
  Direction = (0,1,2e-16)
  Length = 5
  Length2 = 5
  Midplane = true
  Placement = pos=(0,0,1588) rot=(0,0,1;0rad)
  Profile = -> Sketch120
  ReferenceAxis = -> Sketch120 [N_Axis]
  Suppressed = false
  Type = 1
FEATURE [PartDesign::Fillet] Fillet004
  Base = -> Pocket064 [Edge25,Edge31,Edge8,Edge10]
  BaseFeature = -> Pocket064
  Placement = pos=(0,0,1588) rot=(0,0,1;0rad)
  Radius = 3
  SupportTransform = false
  Suppressed = false
  UseAllEdges = false
FEATURE [Part::Compound] Compound044  label="top_dec_corner_cut1"
  Links = -> [Compound034]
FEATURE [PartDesign::Boolean] Boolean014
  BaseFeature = -> Fillet004
  Group = -> [Compound044]
  Suppressed = false
  Type = 1
  UsePlacement = false
FEATURE [PartDesign::SubShapeBinder] Binder073
  BindCopyOnChange = 0
  BindMode = 0
  ClaimChildren = false
  Context = -> Link025 [Binder073.]
  Fuse = false
  MakeFace = true
  OffsetFill = false
  OffsetIntersection = false
  OffsetJoinType = 0
  OffsetOpenResult = false
  PartialLoad = false
  Relative = true
  Support = -> [Body012[Pocket034.Sketch073.]]
  _Version = 2
FEATURE [PartDesign::Hole] Hole020
  BaseFeature = -> Boolean014
  CustomThreadClearance = 0
  Depth = 253.566
  DepthType = 1
  Diameter = 3.4
  DrillForDepth = false
  DrillPoint = 1
  DrillPointAngle = 118
  HoleCutCountersinkAngle = 90
  HoleCutCustomValues = false
  HoleCutDepth = 0
  HoleCutDiameter = 6.1
  HoleCutType = 0
  ModelThread = false
  Profile = -> Binder073
  Suppressed = false
  Tapered = false
  TaperedAngle = 90
  ThreadClass = 0
  ThreadDepth = 253.566
  ThreadDepthType = 0
  ThreadDirection = 0
  ThreadFit = 0
  ThreadSize = 0
  ThreadType = 0
  Threaded = false
  UseCustomThreadClearance = false
  expr: Diameter = <<Properties>>.rivet_d
FEATURE [PartDesign::Body] Body014  label="top_dec_corner_material_0.30ansi"
  Group = -> [Sketch119,BaseBend029,Sketch120,Pocket064,Fillet004,Boolean014,Binder073,Hole020]
  Origin = -> Origin018
  Tip = -> Hole020
FEATURE [PartDesign::SubShapeBinder] Binder074
  BindCopyOnChange = 0
  BindMode = 0
  ClaimChildren = false
  Context = -> Body012 [Binder074.]
  Fuse = false
  MakeFace = true
  OffsetFill = false
  OffsetIntersection = false
  OffsetJoinType = 0
  OffsetOpenResult = false
  PartialLoad = false
  Relative = true
  Support = -> [Body010[Boolean011.Edge138,Boolean011.Edge140,Boolean011.Edge152]]
  _Version = 2
FEATURE [PartDesign::Pocket] Pocket065
  BaseFeature = -> Pocket034
  Direction = (0,-1,2e-16)
  Length = 5
  Length2 = 5
  Profile = -> Binder074
  Reversed = true
  Suppressed = false
  Type = 0
FEATURE [PartDesign::Body] Body012  label="pillar_top_element_material_0.30ansi"
  Group = -> [Sketch013,BaseBend006,Bend,Sketch066,Fillet001,Hole005,Sketch067,Pocket030,Sketch073,Pocket034,Binder074,Pocket065]
  Origin = -> Origin016
  Placement = pos=(0,2,1594) rot=(0,0,1;0rad)
  Tip = -> Pocket065
FEATURE [Sketcher::SketchObject] Sketch121
  AttachmentSupport = -> [XZ_Plane054]
  FullyConstrained = true
  MapMode = 5
  Placement = pos=(0,0,0) rot=(1,0,0;1.5708rad)
  sketch-geometry (5):
    g0: LineSegment StartX=-18 StartY=15 StartZ=0 EndX=-18 EndY=0 EndZ=0
    g1: LineSegment StartX=-18 StartY=0 StartZ=0 EndX=18 EndY=0 EndZ=0
    g2: LineSegment StartX=18 StartY=0 StartZ=0 EndX=18 EndY=15 EndZ=0
    g3: LineSegment StartX=18 StartY=15 StartZ=0 EndX=-18 EndY=15 EndZ=0
    g4: GeomPoint X=0 Y=7.5 Z=0
  constraints (13):
    c: Coincident(g0,g1)
    c: Coincident(g1,g2)
    c: Coincident(g2,g3)
    c: Coincident(g3,g0)
    c: Horizontal(g1)
    c: Horizontal(g3)
    c: Vertical(g0)
    c: Vertical(g2)
    c: Symmetric(g1,g0,g4)
    c: PointOnObject(g4,g-2)
    c: PointOnObject(g1,g-1)
    c: DistanceY(g2,g2) = 15  'height'
    c: DistanceX(g1,g1) = 36  'width'
FEATURE [PartDesign::FeaturePython] BaseBend030  # WARN: FeaturePython — macro-defined, semantics opaque (R4)
  BendSide = 1
  BendSketch = -> Sketch121
  MidPlane = true
  Reverse = false
  Suppressed = false
  length = 245
  radius = 2
  thickness = 2
FEATURE [Sketcher::SketchObject] Sketch122
  AttachmentSupport = -> [YZ_Plane054]
  FullyConstrained = true
  MapMode = 5
  Placement = pos=(0,0,0) rot=(0.57735,0.57735,0.57735;2.0944rad)
  expr: Constraints[10] = Sketch121.Constraints.height
  expr: Constraints[12] = BaseBend030.length / 2
  expr: Constraints[9] = BaseBend030.thickness + BaseBend030.radius
  sketch-geometry (14):
    g0: ArcOfCircle CenterX=117.5 CenterY=4 CenterZ=0 NormalX=0 NormalY=0 NormalZ=1 AngleXU=0 Radius=5 StartAngle=1e-16 EndAngle=0.785398
    g1: LineSegment StartX=121.036 StartY=7.53553 StartZ=0 EndX=115.036 EndY=13.5355 EndZ=0
    g2: ArcOfCircle CenterX=111.5 CenterY=10 CenterZ=0 NormalX=0 NormalY=0 NormalZ=1 AngleXU=0 Radius=5 StartAngle=0.785398 EndAngle=1.5708
    g3: LineSegment StartX=111.5 StartY=15 StartZ=0 EndX=-111.5 EndY=15 EndZ=0
    g4: LineSegment StartX=122.5 StartY=4 StartZ=0 EndX=122.5 EndY=0 EndZ=0
    g5: LineSegment StartX=122.5 StartY=0 StartZ=0 EndX=-122.5 EndY=0 EndZ=0
    g6: LineSegment StartX=-122.5 StartY=0 StartZ=0 EndX=-122.5 EndY=4 EndZ=0
    g7: LineSegment StartX=-121.036 StartY=7.53553 StartZ=0 EndX=-115.036 EndY=13.5355 EndZ=0
    g8: ArcOfCircle CenterX=-111.5 CenterY=10 CenterZ=0 NormalX=0 NormalY=0 NormalZ=1 AngleXU=0 Radius=5 StartAngle=1.5708 EndAngle=2.35619
    g9: GeomPoint X=-113.571 Y=15 Z=0
    g10: ArcOfCircle CenterX=-117.5 CenterY=4 CenterZ=0 NormalX=0 NormalY=0 NormalZ=1 AngleXU=0 Radius=5 StartAngle=2.35619 EndAngle=3.14159
    g11: GeomPoint X=-122.5 Y=6.07107 Z=0
    g12: GeomPoint X=113.571 Y=15 Z=0
    g13: GeomPoint X=122.5 Y=6.07107 Z=0
  constraints (32):
    c: Tangent(g1,g0) = -1.5708
    c: Angle(g1) = 2.35619
    c: Tangent(g2,g1) = -1.5708
    c: Horizontal(g3)
    c: Tangent(g3,g2) = -1.5708
    c: Equal(g0,g2)
    c: Tangent(g0,g4) = 1.5708
    c: Coincident(g4,g5)
    c: Horizontal(g5)
    c: DistanceY(g0) = 4
    c: DistanceY(g9) = 15
    c: Vertical(g4)
    c: DistanceX(g4) = 122.5
    c: Radius(g0) = 5
    c: Coincident(g5,g6)
    c: Tangent(g3,g8) = -1.5708
    c: Tangent(g7,g8) = 1.5708
    c: PointOnObject(g11,g6)
    c: PointOnObject(g11,g7)
    c: Tangent(g6,g10) = 1.5708
    c: Tangent(g7,g10) = 1.5708
    c: Vertical(g6)
    c: Equal(g10,g8)
    c: Equal(g8,g2)
    c: PointOnObject(g13,g4)
    c: PointOnObject(g13,g1)
    c: PointOnObject(g12,g1)
    c: Symmetric(g13,g11,g-2)
    c: Symmetric(g9,g12,g-2)
    c: PointOnObject(g9,g3)
    c: PointOnObject(g9,g7)
    c: PointOnObject(g-1,g5)
FEATURE [Part::FeaturePython] WireFilter003  # WARN: FeaturePython — macro-defined, semantics opaque (R4)
  AttacherType = Attacher::AttachEngine3D
  ClaimChildren = true
  ColorKeyCount = 8
  Colorize = true
  FaceMaker = 5
  FixNormal = false
  FollowSource = true
  InvertedFaceScale = 5
  MaxWires = 25
  Normal = (1,-3e-16,2e-16)
  OffsetFill = false
  OffsetIntersection = false
  OffsetJoin = 0
  OffsetOpenResult = false
  Scale = (1,1,1)
  SelectEdges = false
  Source = -> Sketch122
  UniformScale = 1
  UseDefault = false
  UseSelected = true
  UseSelectedEdges = false
  Version = 0.2022.02.09
  WireOrder = [1]
FEATURE [PartDesign::Pocket] Pocket066
  BaseFeature = -> BaseBend030
  Direction = (-1,3e-16,-2e-16)
  Length = 5
  Length2 = 5
  Midplane = true
  Profile = -> WireFilter003
  Suppressed = false
  Type = 1
FEATURE [Sketcher::SketchObject] Sketch123
  AttachmentSupport = -> [XY_Plane054]
  FullyConstrained = true
  MapMode = 5
  expr: Constraints[1] = -BaseBend030.length / 2
  expr: Constraints[32] = BaseBend030.length - 14 mm
  sketch-geometry (15):
    g0: GeomPoint X=0 Y=-122.5 Z=0
    g1: Circle CenterX=0 CenterY=92.5 CenterZ=0 NormalX=0 NormalY=0 NormalZ=1 AngleXU=0 Radius=2.5
    g2: LineSegment StartX=9 StartY=115.5 StartZ=0 EndX=-9 EndY=115.5 EndZ=0
    g3: LineSegment StartX=-9 StartY=115.5 StartZ=0 EndX=-9 EndY=0 EndZ=0
    g4: LineSegment StartX=-9 StartY=0 StartZ=0 EndX=-9 EndY=-115.5 EndZ=0
    g5: LineSegment StartX=-9 StartY=-115.5 StartZ=0 EndX=9 EndY=-115.5 EndZ=0
    g6: LineSegment StartX=9 StartY=-115.5 StartZ=0 EndX=9 EndY=0 EndZ=0
    g7: LineSegment StartX=9 StartY=0 StartZ=0 EndX=9 EndY=115.5 EndZ=0
    g8: Circle CenterX=-9 CenterY=0 CenterZ=0 NormalX=0 NormalY=0 NormalZ=1 AngleXU=0 Radius=2.5
    g9: Circle CenterX=9 CenterY=0 CenterZ=0 NormalX=0 NormalY=0 NormalZ=1 AngleXU=0 Radius=2.5
    g10: Circle CenterX=-9 CenterY=115.5 CenterZ=0 NormalX=0 NormalY=0 NormalZ=1 AngleXU=0 Radius=2.5
    g11: Circle CenterX=9 CenterY=115.5 CenterZ=0 NormalX=0 NormalY=0 NormalZ=1 AngleXU=0 Radius=2.5
    g12: Circle CenterX=-9 CenterY=-115.5 CenterZ=0 NormalX=0 NormalY=0 NormalZ=1 AngleXU=0 Radius=2.5
    g13: Circle CenterX=9 CenterY=-115.5 CenterZ=0 NormalX=0 NormalY=0 NormalZ=1 AngleXU=0 Radius=2.5
    g14: Circle CenterX=0 CenterY=-92.5 CenterZ=0 NormalX=0 NormalY=0 NormalZ=1 AngleXU=0 Radius=4
  constraints (36):
    c: PointOnObject(g0,g-2)
    c: DistanceY(g0) = -122.5
    c: PointOnObject(g1,g-2)
    c: DistanceY(g0,g1) = 215
    c: Horizontal(g2)
    c: Coincident(g2,g3)
    c: PointOnObject(g3,g-1)
    c: Vertical(g3)
    c: Coincident(g3,g4)
    c: Vertical(g4)
    c: Coincident(g4,g5)
    c: Horizontal(g5)
    c: Coincident(g5,g6)
    c: PointOnObject(g6,g-1)
    c: Vertical(g6)
    c: Coincident(g6,g7)
    c: Coincident(g7,g2)
    c: Vertical(g7)
    c: Coincident(g8,g3)
    c: Coincident(g9,g6)
    c: Coincident(g10,g2)
    c: Coincident(g11,g2)
    c: Coincident(g12,g4)
    c: Coincident(g13,g5)
    c: Symmetric(g12,g11,g-1)
    c: Equal(g11,g10)
    c: Equal(g11,g1)
    c: Equal(g11,g8)
    c: Equal(g11,g9)
    c: Equal(g11,g12)
    c: Equal(g11,g13)
    c: Diameter(g11) = 5
    c: DistanceY(g12,g10) = 231
    c: DistanceX(g2,g2) = 18
    c: Diameter(g14) = 8
    c: Symmetric(g14,g1,g-1)
FEATURE [PartDesign::Pocket] Pocket067
  BaseFeature = -> Pocket066
  Direction = (0,0,-1)
  Length = 5
  Length2 = 5
  Profile = -> Sketch123
  ReferenceAxis = -> Sketch123 [N_Axis]
  Reversed = true
  Suppressed = false
  Type = 0
FEATURE [PartDesign::Body] Body088  label="basement_amplifier_material_0.30ansi"
  Group = -> [Sketch121,BaseBend030,Sketch122,WireFilter003,Pocket066,Sketch123,Pocket067]
  Origin = -> Origin054
  Tip = -> Pocket067
FEATURE [Sketcher::SketchObject] Sketch128  label="door_base_pillar_sketch"
  FullyConstrained = true
  Raduis = 2
  Thickness = 1
  expr: Constraints[2] = <<Properties>>.endface_width / 2 + 25 mm
  expr: Constraints[3] = <<Properties>>.total_length + 5 mm
  expr: Constraints[5] = <<Properties>>.total_length - 15 mm
  sketch-geometry (2):
    g0: LineSegment StartX=39.5 StartY=336.872 StartZ=0 EndX=39.5 EndY=356.872 EndZ=0
    g1: LineSegment StartX=39.5 StartY=356.872 StartZ=0 EndX=69.3858 EndY=354.257 EndZ=0
  constraints (8):
    c: Vertical(g0)
    c: Coincident(g0,g1)
    c: DistanceX(g0) = 39.5
    c: DistanceY(g0) = 356.872
    c: Distance(g0,g1) = 30  'face_side'
    c: DistanceY(g0) = 336.872
    c: Angle(g1) = -0.0872665
    c: Distance(g0) = 20  'fix_side'
FEATURE [Sketcher::SketchObject] Sketch131  label="door_base_pillar_to_hor_fix_sketch"
  ExternalGeometry = -> [Sketch128]
  FullyConstrained = false
  Raduis = 2
  Thickness = 1
  expr: Constraints[6] = <<door_base_pillar_sketch>>.Thickness + Thickness + Raduis
  sketch-geometry (10):
    g0: LineSegment StartX=43.5 StartY=336.872 StartZ=0 EndX=43.5 EndY=352.506 EndZ=0
    g1: LineSegment StartX=43.5 StartY=352.506 StartZ=0 EndX=69.0372 EndY=350.272 EndZ=0
    g2: LineSegment StartX=39.5 StartY=336.872 StartZ=0 EndX=43.5 EndY=336.872 EndZ=0
    g3: LineSegment StartX=69.0372 StartY=350.272 StartZ=0 EndX=69.3858 EndY=354.257 EndZ=0
    g4: GeomPoint X=69.0372 Y=350.272 Z=0
    g5: GeomPoint X=43.5 Y=336.872 Z=0
    g6: ArcOfCircle CenterX=62.4098 CenterY=331.608 CenterZ=0 NormalX=0 NormalY=0 NormalZ=1 AngleXU=0 Radius=6 StartAngle=4.13024 EndAngle=5.83473
    g7: ArcOfCircle CenterX=68.5143 CenterY=344.295 CenterZ=0 NormalX=0 NormalY=0 NormalZ=1 AngleXU=0 Radius=6 StartAngle=5.83473 EndAngle=7.76672
    g8: LineSegment StartX=67.8165 StartY=329.006 StartZ=0 EndX=73.921 EndY=341.694 EndZ=0
    g9: LineSegment StartX=59.1109 StartY=326.596 StartZ=0 EndX=43.5 EndY=336.872 EndZ=0
  constraints (22):
    c: Coincident(g2,g-4)
    c: Coincident(g2,g0)
    c: Perpendicular(g-4,g2)
    c: Coincident(g3,g1)
    c: Coincident(g3,g-3)
    c: Perpendicular(g1,g3)
    c: Distance(g3) = 4
    c: Equal(g3,g2)
    c: Perpendicular(g-3,g3)
    c: Perpendicular(g2,g0)
    c: Coincident(g0,g1)
    c: PointOnObject(g4,g3)
    c: PointOnObject(g5,g2)
    c: Tangent(g7,g1) = 1.5708
    c: Tangent(g8,g6) = -1.5708
    c: Tangent(g8,g7) = -1.5708
    c: DistanceX(g6) = 62.4098
    c: DistanceY(g6) = 331.608
    c: Radius(g6) = 6
    c: Radius(g7) = 6
    c: Coincident(g9,g0)
    c: Tangent(g9,g6) = 1.5708
FEATURE [Sketcher::SketchObject] Sketch133  label="door_base_pillar_to_hor_fix_holes_sketch"
  ExternalGeometry = -> [Sketch131]
  FullyConstrained = false
  sketch-geometry (7):
    g0: Circle CenterX=68.34 CenterY=342.303 CenterZ=0 NormalX=0 NormalY=0 NormalZ=1 AngleXU=0 Radius=1.7
    g1: Circle CenterX=51.5 CenterY=336.872 CenterZ=0 NormalX=0 NormalY=0 NormalZ=1 AngleXU=0 Radius=1.7
    g2: Circle CenterX=62.5438 CenterY=331.451 CenterZ=0 NormalX=0 NormalY=0 NormalZ=1 AngleXU=0 Radius=1.7
    g3: LineSegment StartX=68.34 StartY=342.303 StartZ=0 EndX=62.5438 EndY=331.451 EndZ=0
    g4: LineSegment StartX=62.5438 StartY=331.451 StartZ=0 EndX=51.5 EndY=336.872 EndZ=0
    g5: LineSegment StartX=51.5 StartY=336.872 StartZ=0 EndX=43.5 EndY=336.872 EndZ=0
    g6: LineSegment StartX=69.0372 StartY=350.272 StartZ=0 EndX=68.34 EndY=342.303 EndZ=0
  constraints (16):
    c: Equal(g0,g2)
    c: Equal(g0,g1)
    c: Diameter(g0) = 3.4
    c: Coincident(g3,g0)
    c: Coincident(g3,g2)
    c: Coincident(g4,g2)
    c: Coincident(g4,g1)
    c: Distance(g1,g-3) = 8
    c: Coincident(g5,g1)
    c: Perpendicular(g-3,g5)
    c: Coincident(g6,g0)
    c: Equal(g4,g3)
    c: Coincident(g5,g-3)
    c: Coincident(g6,g-4)
    c: Equal(g6,g5)
    c: Perpendicular(g-4,g6)
FEATURE [Sketcher::SketchObject] Sketch138
  FullyConstrained = true
  expr: Constraints[4] = <<Properties>>.endface_width / 2
  expr: Constraints[5] = Sketch.Constraints.max_r
  sketch-geometry (7):
    g0: LineSegment StartX=0 StartY=0 StartZ=0 EndX=220.836 EndY=127.5 EndZ=0
    g1: LineSegment StartX=0 StartY=0 StartZ=0 EndX=14.5 EndY=351.872 EndZ=0
    g2: ArcOfCircle CenterX=14.5 CenterY=270.372 CenterZ=0 NormalX=0 NormalY=0 NormalZ=1 AngleXU=0 Radius=80 StartAngle=0.886335 EndAngle=1.5708
    g3: ArcOfCircle CenterX=-298.923 CenterY=-113.694 CenterZ=0 NormalX=0 NormalY=0 NormalZ=1 AngleXU=0 Radius=575.722 StartAngle=0.523599 EndAngle=0.886335
    g4: LineSegment StartX=225.167 StartY=130 StartZ=0 EndX=199.667 EndY=174.167 EndZ=0
    g5: LineSegment StartX=220.836 StartY=127.5 StartZ=0 EndX=225.167 EndY=130 EndZ=0
    g6: LineSegment StartX=14.5 StartY=350.372 StartZ=0 EndX=0 EndY=350.372 EndZ=0
  constraints (20):
    c: Coincident(g0,g-1)
    c: Angle(g0) = 0.523599
    c: Distance(g0,g0) = 255
    c: Coincident(g1,g0)
    c: DistanceX(g1) = 14.5
    c: Distance(g0,g1) = 352.17
    c: Vertical(g2,g2)
    c: Tangent(g3,g2) = -1.5708
    c: Tangent(g4,g3) = -1.5708
    c: Coincident(g5,g0)
    c: Coincident(g5,g4)
    c: Parallel(g5,g0)
    c: Distance(g5) = 5
    c: Perpendicular(g5,g4)
    c: Distance(g4) = 51
    c: Radius(g2) = 80
    c: PointOnObject(g6,g-2)
    c: Tangent(g2,g6) = -1.5708
    c: Vertical(g2,g1)
    c: DistanceY(g2,g1) = 1.5
FEATURE [Part::Mirroring] Part__Mirroring021  label="Sketch138 (Mirror #25)"
  Base = (0,0,0)
  Normal = (-0.5,0.866025,0)
  Source = -> Sketch138
  expr: .Normal.x = sin(-30)
  expr: .Normal.y = cos(-30)
FEATURE [Part::Compound] Compound045
  Links = -> [Part__Mirroring021,Sketch138]
FEATURE [PartDesign::SubShapeBinder] Binder076
  BindCopyOnChange = 0
  BindMode = 0
  ClaimChildren = true
  Context = -> Part014 [Body091.Binder076.]
  Fuse = false
  MakeFace = true
  OffsetFill = false
  OffsetIntersection = false
  OffsetJoinType = 0
  OffsetOpenResult = false
  PartialLoad = false
  Relative = false
  Support = -> [Compound045]
  _Version = 2
FEATURE [PartDesign::FeaturePython] BaseBend031  # WARN: FeaturePython — macro-defined, semantics opaque (R4)
  BendSide = 1
  BendSketch = -> Binder076
  MidPlane = false
  Reverse = false
  Suppressed = false
  length = 100
  radius = 1
  thickness = 1.5
FEATURE [PartDesign::FeaturePython] Extend001  # WARN: FeaturePython — macro-defined, semantics opaque (R4)
  BaseFeature = -> BaseBend031
  Offset = 0.02
  Refine = true
  Suppressed = false
  UseSubtraction = false
  baseObject = -> BaseBend031 [Face5]
  gap1 = 0
  gap2 = 0
  length = 0
FEATURE [PartDesign::Body] Body091  label="door_top_plexiglass_material_0.30ansi"
  Group = -> [Binder076,BaseBend031,Extend001]
  Origin = -> Origin057
  Tip = -> Extend001
FEATURE [Part::FeaturePython] Array007  # Draft array (typed FeaturePython)
  AlwaysSyncPlacement = false
  Angle = 360
  ArrayType = 1
  Axis = (0,0,1)
  Base = -> Compound045
  Center = (0,0,0)
  Count = 3
  ExpandArray = false
  Fuse = false
  IntervalAxis = (0,0,0)
  IntervalX = (50,0,0)
  IntervalY = (0,50,0)
  IntervalZ = (0,0,50)
  NumberCircles = 3
  NumberPolar = 3
  NumberX = 2
  NumberY = 2
  NumberZ = 1
  PlacementList = 3 placements: [(0,0,0),(0,0,0),(0,0,0)]
  RadialDistance = 50
  ScaleList = (3) [(1,1,1),(1,1,1),(1,1,1)]
  Symmetry = 1
  TangentialDistance = 25
FEATURE [PartDesign::SubShapeBinder] Binder077
  BindCopyOnChange = 0
  BindMode = 0
  ClaimChildren = true
  Context = -> Part014 [Body092.Binder077.]
  Fuse = false
  MakeFace = true
  OffsetFill = false
  OffsetIntersection = false
  OffsetJoinType = 0
  OffsetOpenResult = false
  PartialLoad = false
  Relative = false
  Support = -> [Array007]
  _Version = 2
FEATURE [PartDesign::Pad] Pad016
  Direction = (0,0,1)
  Length = 3
  Length2 = 10
  Profile = -> Binder077
  Suppressed = false
  Type = 0
FEATURE [Part::FeaturePython] Array008  # Draft array (typed FeaturePython)
  AlwaysSyncPlacement = false
  Angle = 360
  ArrayType = 1
  Axis = (0,0,1)
  Base = -> Clone005
  Center = (0,0,0)
  Count = 3
  ExpandArray = false
  Fuse = false
  IntervalAxis = (0,0,0)
  IntervalX = (50,0,0)
  IntervalY = (0,50,0)
  IntervalZ = (0,0,50)
  NumberCircles = 3
  NumberPolar = 3
  NumberX = 2
  NumberY = 2
  NumberZ = 1
  PlacementList = 3 placements: [(0,181.372,0),(-157.072,-90.6858,0),(157.072,-90.6858,0)]
  RadialDistance = 50
  ScaleList = (3) [(1,1,1),(1,1,1),(1,1,1)]
  Symmetry = 1
  TangentialDistance = 25
FEATURE [PartDesign::SubShapeBinder] Binder078
  BindCopyOnChange = 0
  BindMode = 0
  ClaimChildren = true
  Context = -> Part015 [Part014.Body092.Binder078.]
  Fuse = false
  MakeFace = true
  OffsetFill = false
  OffsetIntersection = false
  OffsetJoinType = 0
  OffsetOpenResult = false
  PartialLoad = false
  Relative = true
  Support = -> [Array008]
  _Version = 2
FEATURE [PartDesign::Pocket] Pocket070
  BaseFeature = -> Pad016
  Direction = (0,0,-1)
  Length = 5
  Length2 = 5
  Midplane = true
  Profile = -> Binder078
  Suppressed = false
  Type = 1
FEATURE [PartDesign::SubShapeBinder] Binder079
  BindCopyOnChange = 0
  BindMode = 0
  ClaimChildren = true
  Context = -> Body092 [Binder079.]
  Fuse = false
  MakeFace = true
  OffsetFill = false
  OffsetIntersection = false
  OffsetJoinType = 0
  OffsetOpenResult = false
  PartialLoad = false
  Relative = false
  Support = -> [Sketch028]
  _Version = 2
  expr: Support = Sketch028._self
FEATURE [PartDesign::Pocket] Pocket071
  BaseFeature = -> Pocket070
  Direction = (0,0,-1)
  Length = 5
  Length2 = 5
  Profile = -> Binder079
  Reversed = true
  Suppressed = false
  Type = 0
FEATURE [PartDesign::PolarPattern] PolarPattern004
  Angle = 360
  Axis = -> Z_Axis058
  BaseFeature = -> Pocket071
  Mode = 0
  Occurrences = 3
  Offset = 120
  Originals = -> [Pocket071]
  Suppressed = false
FEATURE [Part::FeaturePython] Placment007  # WARN: FeaturePython — macro-defined, semantics opaque (R4)
  AttacherType = Attacher::AttachEngine3D
  AttachmentOffset = pos=(0,0,0) rot=(-0.57735,-0.57735,-0.57735;2.0944rad)
  AttachmentSupport = -> [Sketch138]
  ExposePlacement = true
  MapMode = 7
  MarkerShape = 1
  MarkerSize = 5
  NumElements = 1
  Placement = pos=(225.167,130,0) rot=(0,0,-1;1.0472rad)
  Type = lattice2AttachablePlacement.AttachablePlacement
  isLattice = 1
FEATURE [Part::FeaturePython] Placment008  # WARN: FeaturePython — macro-defined, semantics opaque (R4)
  AttacherType = Attacher::AttachEngine3D
  AttachmentOffset = pos=(0,0,0) rot=(-0.57735,-0.57735,-0.57735;2.0944rad)
  AttachmentSupport = -> [Sketch138]
  ExposePlacement = true
  MapMode = 7
  MarkerShape = 1
  MarkerSize = 20
  NumElements = 1
  Placement = pos=(0,350.372,0) rot=(0,0,1;0rad)
  Type = lattice2AttachablePlacement.AttachablePlacement
  isLattice = 1
FEATURE [Part::FeaturePython] Join001  # WARN: FeaturePython — macro-defined, semantics opaque (R4)
  ExposePlacement = false
  Interleave = false
  Links = -> [Placment007,Placment008]
  MarkerShape = 1
  MarkerSize = 0
  NumElements = 2
  Type = lattice2JoinArrays.JoinArrays
  isLattice = 1
FEATURE [Part::FeaturePython] PolarArray001  # WARN: FeaturePython — macro-defined, semantics opaque (R4)
  Alignment = 0
  AttacherType = Attacher::AttachEngine3D
  CellStart = A1
  Count = 3
  DistributionLaw = 0
  EndInclusive = false
  ExposePlacement = false
  FlipX = false
  FlipZ = false
  GeneratorMode = 0
  MarkerShape = 1
  MarkerSize = 0
  NumElements = 3
  OrientMode = 2
  Radius = 50
  Reverse = false
  SpanEnd = 360
  SpanStart = 0
  Step = 120
  Type = lattice2PolarArray2.PolarArray
  UseArcRadius = false
  UseArcRange = 0
  VSGVersion = 1
  Values = 0.0 | 120.0 | 240.0
  ValuesSource = 2
  isLattice = 1
FEATURE [Part::FeaturePython] Populate020  label="Populate PolarArray001 with Join001"  # WARN: FeaturePython — macro-defined, semantics opaque (R4)
  Copying = 0
  ExposePlacement = false
  MarkerShape = 1
  MarkerSize = 0
  NumElements = 6
  Object = -> Join001
  OutputCompounding = 0
  PlacementsTo = -> PolarArray001
  Referencing = 1
  Type = lattice2PopulateCopies.LatticePopulateCopies
  isLattice = 1
FEATURE [Sketcher::SketchObject] Sketch139
  FullyConstrained = true
  sketch-geometry (2):
    g0: Circle CenterX=-10 CenterY=-10 CenterZ=0 NormalX=0 NormalY=0 NormalZ=1 AngleXU=0 Radius=1.7
    g1: Circle CenterX=10 CenterY=-10 CenterZ=0 NormalX=0 NormalY=0 NormalZ=1 AngleXU=0 Radius=1.7
  constraints (5):
    c: Symmetric(g0,g1,g-2)
    c: Equal(g0,g1)
    c: Diameter(g0) = 3.4
    c: DistanceX(g0,g1) = 20
    c: DistanceY(g1) = -10
FEATURE [Part::FeaturePython] Populate021  label="Populate Populate PolarArray001 with Join001 with Sketch139"  # WARN: FeaturePython — macro-defined, semantics opaque (R4)
  Copying = 0
  ExposePlacement = false
  MarkerShape = 1
  MarkerSize = 0
  NumElements = 0
  Object = -> Sketch139
  OutputCompounding = 1
  PlacementsTo = -> Populate020
  Referencing = 0
  Type = lattice2PopulateCopies.LatticePopulateCopies
  isLattice = 0
FEATURE [PartDesign::SubShapeBinder] Binder080
  BindCopyOnChange = 0
  BindMode = 0
  ClaimChildren = true
  Context = -> Body092 [Binder080.]
  Fuse = false
  MakeFace = true
  OffsetFill = false
  OffsetIntersection = false
  OffsetJoinType = 0
  OffsetOpenResult = false
  PartialLoad = false
  Relative = false
  Support = -> [Populate021]
  _Version = 2
FEATURE [PartDesign::Pocket] Pocket072
  BaseFeature = -> PolarPattern004
  Direction = (0,0,-1)
  Length = 5
  Length2 = 5
  Profile = -> Binder080
  Reversed = true
  Suppressed = false
  Type = 0
FEATURE [PartDesign::Body] Body092  label="top_door"
  Group = -> [Binder077,Pad016,Binder078,Pocket070,Binder079,Pocket071,PolarPattern004,Binder080,Pocket072]
  Origin = -> Origin058
  Tip = -> Pocket072
FEATURE [PartDesign::SubShapeBinder] Binder081
  BindCopyOnChange = 0
  BindMode = 0
  ClaimChildren = true
  Fuse = false
  MakeFace = true
  OffsetFill = false
  OffsetIntersection = false
  OffsetJoinType = 0
  OffsetOpenResult = false
  PartialLoad = false
  Relative = false
  Support = -> [Sketch131]
  _Version = 2
FEATURE [PartDesign::FeaturePython] BaseBend032  # WARN: FeaturePython — macro-defined, semantics opaque (R4)
  BendSide = 0
  BendSketch = -> Binder081
  MidPlane = false
  Reverse = false
  Suppressed = false
  length = 100
  radius = 2
  thickness = 1
FEATURE [PartDesign::FeaturePython] Bend020  # WARN: FeaturePython — macro-defined, semantics opaque (R4)
  AutoMiter = false
  BaseFeature = -> BaseBend032
  BendType = 0
  LengthList = [10]
  LengthSpec = 0
  ReliefFactor = 0.7
  Suppressed = false
  UseReliefFactor = false
  angle = 90
  baseObject = -> BaseBend032 [Edge7,Edge10]
  bendAList = [90]
  extend1 = 0
  extend2 = 0
  gap1 = 0
  gap2 = 0
  invert = false
  kfactor = 0.5
  length = 10
  maxExtendDist = 5
  minGap = 0.1
  minReliefGap = 1
  miterangle1 = 0
  miterangle2 = 0
  offset = 0
  radius = 2
  reliefType = 0
  reliefd = 1
  reliefw = 0.8
  sketchflip = false
  sketchinvert = false
  unfold = false
  expr: radius = BaseBend032.radius
FEATURE [PartDesign::SubShapeBinder] Binder082
  BindCopyOnChange = 0
  BindMode = 0
  ClaimChildren = true
  Context = -> Body094 [Binder082.]
  Fuse = false
  MakeFace = true
  OffsetFill = false
  OffsetIntersection = false
  OffsetJoinType = 0
  OffsetOpenResult = false
  PartialLoad = false
  Relative = false
  Support = -> [Sketch137]
  _Version = 2
FEATURE [PartDesign::FeaturePython] BaseBend033  label="door_led_holder_BaseBend"  # WARN: FeaturePython — macro-defined, semantics opaque (R4)
  BendSide = 1
  BendSketch = -> Binder082
  MidPlane = false
  Reverse = false
  Suppressed = false
  length = 1100
  radius = 0.1
  thickness = 0.3
  expr: radius = composit_properties#<<Properties>>.bend_r
  expr: thickness = composit_properties#<<Properties>>.al_thickness
FEATURE [PartDesign::SubShapeBinder] Binder083
  BindCopyOnChange = 0
  BindMode = 0
  ClaimChildren = true
  Context = -> Body095 [Binder083.]
  Fuse = false
  MakeFace = true
  OffsetFill = false
  OffsetIntersection = false
  OffsetJoinType = 0
  OffsetOpenResult = false
  PartialLoad = false
  Relative = false
  Support = -> [Sketch128]
  _Version = 2
FEATURE [PartDesign::FeaturePython] BaseBend034  label="door_base_pillar_BaseBend"  # WARN: FeaturePython — macro-defined, semantics opaque (R4)
  BendSide = 0
  BendSketch = -> Binder083
  MidPlane = false
  Reverse = false
  Suppressed = false
  length = 1200
  radius = 2
  thickness = 1
FEATURE [App::Part] Part014  label="door3_top"
  Group = -> [Body092,Body091]
  Origin = -> Origin068
  Placement = pos=(0,0,1428) rot=(0,0,1;0rad)
  expr: .Placement.Base.z = <<Properties>>.total_height
FEATURE [PartDesign::SubShapeBinder] Binder091
  BindCopyOnChange = 0
  BindMode = 0
  ClaimChildren = true
  Fuse = false
  MakeFace = true
  OffsetFill = false
  OffsetIntersection = false
  OffsetJoinType = 0
  OffsetOpenResult = false
  PartialLoad = false
  Relative = false
  Support = -> [Sketch133]
  _Version = 2
FEATURE [App::Link] Link007  label="Body100"
  LinkPlacement = pos=(253.237,121.38,1450) rot=(0.774597,-0.447214,-0.447214;1.82348rad)
  LinkedObject = -> <external ULY-P91-20W.FCStd>#Body
  Placement = pos=(253.237,121.38,1450) rot=(0.774597,-0.447214,-0.447214;1.82348rad)
  expr: Placement = placement(vector(0; 0; 1450 mm); rotation(-60; 0; 90)) * placement(vector(21.5; 0; -280); rotation(0; 0; 0))
FEATURE [Sketcher::SketchObject] Sketch141
  FullyConstrained = true
  Placement = pos=(0,0,0) rot=(1,0,0;1.5708rad)
  expr: Constraints[19] = <<Properties>>.total_height - 5 mm
  sketch-geometry (8):
    g0: LineSegment StartX=0 StartY=0 StartZ=0 EndX=44 EndY=0 EndZ=0
    g1: LineSegment StartX=44 StartY=0 StartZ=0 EndX=44 EndY=440 EndZ=0
    g2: LineSegment StartX=44 StartY=440 StartZ=0 EndX=0 EndY=440 EndZ=0
    g3: LineSegment StartX=0 StartY=440 StartZ=0 EndX=0 EndY=0 EndZ=0
    g4: LineSegment StartX=0 StartY=1423 StartZ=0 EndX=44 EndY=1423 EndZ=0
    g5: LineSegment StartX=44 StartY=1423 StartZ=0 EndX=44 EndY=1623 EndZ=0
    g6: LineSegment StartX=44 StartY=1623 StartZ=0 EndX=0 EndY=1623 EndZ=0
    g7: LineSegment StartX=0 StartY=1623 StartZ=0 EndX=0 EndY=1423 EndZ=0
  constraints (23):
    c: Coincident(g0,g1)
    c: Coincident(g1,g2)
    c: Coincident(g2,g3)
    c: Coincident(g3,g0)
    c: Horizontal(g0)
    c: Horizontal(g2)
    c: Vertical(g1)
    c: Vertical(g3)
    c: Coincident(g0,g-1)
    c: Coincident(g4,g5)
    c: Coincident(g5,g6)
    c: Coincident(g6,g7)
    c: Coincident(g7,g4)
    c: Horizontal(g4)
    c: Horizontal(g6)
    c: Vertical(g5)
    c: Vertical(g7)
    c: PointOnObject(g4,g-2)
    c: Vertical(g1,g4)
    c: DistanceY(g4) = 1423
    c: DistanceX(g1) = 44
    c: DistanceY(g3,g3) = 440
    c: DistanceY(g7,g7) = 200
FEATURE [PartDesign::SubShapeBinder] Binder092
  BindCopyOnChange = 0
  BindMode = 0
  ClaimChildren = true
  Context = -> Body095 [Binder092.]
  Fuse = false
  MakeFace = true
  OffsetFill = false
  OffsetIntersection = false
  OffsetJoinType = 0
  OffsetOpenResult = false
  PartialLoad = false
  Relative = true
  Support = -> [Sketch141]
  _Version = 2
FEATURE [PartDesign::Pocket] Pocket075
  BaseFeature = -> BaseBend034
  Direction = (0,-1,2e-16)
  Length = 5
  Length2 = 5
  Midplane = true
  Profile = -> Binder092
  Suppressed = false
  Type = 1
FEATURE [PartDesign::SubShapeBinder] Binder093
  BindCopyOnChange = 0
  BindMode = 0
  ClaimChildren = true
  Fuse = false
  MakeFace = false
  OffsetFill = false
  OffsetIntersection = false
  OffsetJoinType = 0
  OffsetOpenResult = false
  PartialLoad = false
  Relative = true
  Support = -> [Link007[Sketch005.]]
  _Version = 2
FEATURE [PartDesign::Line] DatumLine002
  AttacherType = Attacher::AttachEngineLine
  Length = 20
  Placement = pos=(0,0,0) rot=(-0.250563,0.935113,0.250563;1.63783rad)
  ResizeMode = 0
FEATURE [PartDesign::SubShapeBinder] Binder094
  BindCopyOnChange = 0
  BindMode = 0
  ClaimChildren = true
  Fuse = false
  MakeFace = false
  OffsetFill = false
  OffsetIntersection = false
  OffsetJoinType = 0
  OffsetOpenResult = false
  PartialLoad = false
  Relative = true
  Support = -> [Link007[Sketch006.]]
  _Version = 2
FEATURE [Sketcher::SketchObject] Sketch144
  ExternalGeometry = -> [DatumLine002]
  FullyConstrained = false
  sketch-geometry (4):
    g0: LineSegment StartX=235.737 StartY=134.371 StartZ=0 EndX=234.987 EndY=135.67 EndZ=0
    g1: LineSegment StartX=235.737 StartY=134.371 StartZ=0 EndX=235.987 EndY=133.938 EndZ=0
    g2: LineSegment StartX=235.987 StartY=133.938 StartZ=0 EndX=236.487 EndY=133.072 EndZ=0
    g3: LineSegment StartX=236.487 StartY=133.072 StartZ=0 EndX=237.987 EndY=130.474 EndZ=0
  constraints (12):
    c: PointOnObject(g0,g-3)
    c: Perpendicular(g0,g-3)
    c: Distance(g0) = 1.5  'rivet_length'
    c: Coincident(g0,g1)
    c: Coincident(g1,g2)
    c: Parallel(g0,g1)
    c: Parallel(g1,g2)
    c: Distance(g1) = 0.5  'dec_thickness'
    c: Distance(g2) = 1  'corner_thickness'
    c: Coincident(g3,g2)
    c: Parallel(g2,g3)
    c: Distance(g3) = 3  'composit_thickness'
FEATURE [Sketcher::SketchObject] Sketch137  label="door_led_holder_sketch"
  ExternalGeometry = -> [Binder094,Sketch144]
  FullyConstrained = true
  expr: Constraints[32] = 10
  sketch-geometry (16):
    g0: LineSegment StartX=246.282 StartY=138.727 StartZ=0 EndX=237.622 EndY=133.727 EndZ=0
    g1: LineSegment StartX=237.622 StartY=133.727 StartZ=0 EndX=243.547 EndY=123.465 EndZ=0
    g2: LineSegment StartX=243.547 StartY=123.465 StartZ=0 EndX=249.955 EndY=127.165 EndZ=0
    g3: LineSegment StartX=249.955 StartY=127.165 StartZ=0 EndX=256.605 EndY=115.646 EndZ=0
    g4: LineSegment StartX=256.605 StartY=115.646 StartZ=0 EndX=250.197 EndY=111.946 EndZ=0
    g5: LineSegment StartX=250.197 StartY=111.946 StartZ=0 EndX=256.122 EndY=101.684 EndZ=0
    g6: LineSegment StartX=267.727 StartY=108.384 StartZ=0 EndX=262.727 EndY=117.044 EndZ=0
    g7: LineSegment StartX=250.197 StartY=111.946 StartZ=0 EndX=243.547 EndY=123.465 EndZ=0
    g8: LineSegment StartX=243.547 StartY=123.465 StartZ=0 EndX=243.64 EndY=123.403 EndZ=0
    g9: LineSegment StartX=250.197 StartY=111.946 StartZ=0 EndX=250.19 EndY=112.058 EndZ=0
    g10: LineSegment StartX=249.955 StartY=127.165 StartZ=0 EndX=249.962 EndY=127.053 EndZ=0
    g11: LineSegment StartX=256.512 StartY=115.708 StartZ=0 EndX=256.605 EndY=115.646 EndZ=0
    g12: LineSegment StartX=236.487 StartY=133.072 StartZ=0 EndX=237.622 EndY=133.727 EndZ=0
    g13: LineSegment StartX=256.605 StartY=115.646 StartZ=0 EndX=261.802 EndY=118.646 EndZ=0
    g14: LineSegment StartX=256.122 StartY=101.684 StartZ=0 EndX=264.782 EndY=106.684 EndZ=0
    g15: LineSegment StartX=264.782 StartY=106.684 StartZ=0 EndX=267.727 EndY=108.384 EndZ=0
  constraints (44):
    c: Coincident(g0,g1)
    c: Coincident(g1,g2)
    c: Coincident(g2,g3)
    c: Coincident(g3,g4)
    c: Coincident(g4,g5)
    c: Coincident(g5,g14)
    c: Coincident(g15,g6)
    c: Perpendicular(g4,g5)
    c: Perpendicular(g3,g4)
    c: Perpendicular(g3,g2)
    c: Perpendicular(g0,g1)
    c: Coincident(g7,g4)
    c: Coincident(g7,g1)
    c: Parallel(g7,g3)
    c: Perpendicular(g2,g1)
    c: Distance(g6) = 10
    c: Distance(g7) = 13.3
    c: Distance(g4) = 7.4
    c: Coincident(g8,g1)
    c: Coincident(g8,g-4)
    c: Coincident(g9,g4)
    c: Coincident(g9,g-3)
    c: Coincident(g10,g2)
    c: Coincident(g10,g-4)
    c: Equal(g10,g8)
    c: Equal(g8,g9)
    c: Coincident(g11,g-3)
    c: Coincident(g11,g3)
    c: Equal(g11,g10)
    c: Coincident(g12,g-5)
    c: Coincident(g12,g0)
    c: Perpendicular(g-5,g12)
    c: Distance(g0) = 10
    c: Coincident(g13,g3)
    c: Parallel(g13,g4)
    c: PointOnObject(g13,g6)
    c: Distance(g13) = 6
    c: Distance(g5) = 11.85
    c: Coincident(g14,g15)
    c: Perpendicular(g14,g6)
    c: Perpendicular(g15,g6)
    c: Perpendicular(g5,g14)
    c: Equal(g14,g0)
    c: Equal(g5,g1)
FEATURE [Sketcher::SketchObject] Sketch146
  ExternalGeometry = -> [Sketch137,Binder093]
  FullyConstrained = true
  sketch-geometry (4):
    g0: LineSegment StartX=230.997 StartY=129.902 StartZ=0 EndX=249.227 EndY=140.427 EndZ=0
    g1: LineSegment StartX=249.227 StartY=140.427 StartZ=0 EndX=267.727 EndY=108.384 EndZ=0
    g2: LineSegment StartX=249.497 StartY=97.859 StartZ=0 EndX=267.727 EndY=108.384 EndZ=0
    g3: LineSegment StartX=235.397 StartY=122.281 StartZ=0 EndX=230.997 EndY=129.902 EndZ=0
  constraints (12):
    c: Coincident(g0,g1)
    c: Coincident(g2,g1)
    c: Coincident(g3,g-4)
    c: Coincident(g3,g0)
    c: Perpendicular(g-4,g2)
    c: Parallel(g-4,g3)
    c: PointOnObject(g-3,g0)
    c: PointOnObject(g-3,g0)
    c: Perpendicular(g0,g1)
    c: Distance(g-5,g1) = 6
    c: PointOnObject(g2,g-4)
    c: PointOnObject(g-6,g2)
FEATURE [PartDesign::SubShapeBinder] Binder095
  BindCopyOnChange = 0
  BindMode = 0
  ClaimChildren = true
  Context = -> Part015 [Body100.Binder095.]
  Fuse = false
  MakeFace = true
  OffsetFill = false
  OffsetIntersection = false
  OffsetJoinType = 0
  OffsetOpenResult = false
  PartialLoad = false
  Relative = true
  Support = -> [Sketch146]
  _Version = 2
FEATURE [PartDesign::FeaturePython] BaseBend039  # WARN: FeaturePython — macro-defined, semantics opaque (R4)
  BendSide = 1
  BendSketch = -> Binder095
  MidPlane = false
  Reverse = false
  Suppressed = false
  length = 1200
  radius = 2
  thickness = 1
FEATURE [PartDesign::SubShapeBinder] Binder096
  BindCopyOnChange = 0
  BindMode = 0
  ClaimChildren = true
  Context = -> Part015 [Body100.Binder096.]
  Fuse = false
  MakeFace = true
  OffsetFill = false
  OffsetIntersection = false
  OffsetJoinType = 0
  OffsetOpenResult = false
  PartialLoad = false
  Relative = true
  Support = -> [Body094[BaseBend033.Binder082.Sketch137.]]
  _Version = 2
FEATURE [Sketcher::SketchObject] Sketch148
  ExternalGeometry = -> [Sketch146]
  FullyConstrained = true
  sketch-geometry (4):
    g0: LineSegment StartX=230.497 StartY=130.768 StartZ=0 EndX=250.892 EndY=142.543 EndZ=0
    g1: LineSegment StartX=250.892 StartY=142.543 StartZ=0 EndX=269.892 EndY=109.634 EndZ=0
    g2: LineSegment StartX=230.997 StartY=129.902 StartZ=0 EndX=230.497 EndY=130.768 EndZ=0
    g3: LineSegment StartX=267.727 StartY=108.384 StartZ=0 EndX=269.892 EndY=109.634 EndZ=0
  constraints (11):
    c: Coincident(g0,g1)
    c: Coincident(g2,g-4)
    c: Coincident(g2,g0)
    c: Coincident(g3,g-3)
    c: Coincident(g3,g1)
    c: Perpendicular(g3,g1)
    c: Perpendicular(g-3,g3)
    c: Perpendicular(g2,g-4)
    c: Perpendicular(g0,g2)
    c: Distance(g2) = 1
    c: Distance(g3) = 2.5
FEATURE [PartDesign::SubShapeBinder] Binder097
  BindCopyOnChange = 0
  BindMode = 0
  ClaimChildren = true
  Context = -> Part015 [Body101.Binder097.]
  Fuse = false
  MakeFace = true
  OffsetFill = false
  OffsetIntersection = false
  OffsetJoinType = 0
  OffsetOpenResult = false
  PartialLoad = false
  Relative = true
  Support = -> [Sketch148]
  _Version = 2
FEATURE [PartDesign::FeaturePython] BaseBend040  # WARN: FeaturePython — macro-defined, semantics opaque (R4)
  BendSide = 1
  BendSketch = -> Binder097
  MidPlane = false
  Reverse = false
  Suppressed = false
  length = 1200
  radius = 2
  thickness = 0.5
FEATURE [PartDesign::SubShapeBinder] Binder098
  BindCopyOnChange = 0
  BindMode = 0
  ClaimChildren = true
  Context = -> Part015 [Body101.Binder098.]
  Fuse = false
  MakeFace = true
  OffsetFill = false
  OffsetIntersection = false
  OffsetJoinType = 0
  OffsetOpenResult = false
  PartialLoad = false
  Relative = true
  Support = -> [Sketch153]
  _Version = 2
FEATURE [PartDesign::Pocket] Pocket077
  BaseFeature = -> BaseBend040
  Direction = (0.5,-0.866025,-2e-16)
  Length = 5
  Length2 = 5
  Midplane = true
  Profile = -> Binder098
  Suppressed = false
  Type = 1
FEATURE [PartDesign::SubShapeBinder] Binder101
  BindCopyOnChange = 0
  BindMode = 0
  ClaimChildren = true
  Context = -> Part015 [Body100.Binder101.]
  Fuse = false
  MakeFace = false
  OffsetFill = false
  OffsetIntersection = false
  OffsetJoinType = 0
  OffsetOpenResult = false
  PartialLoad = false
  Relative = true
  Support = -> [Binder093]
  _Version = 2
FEATURE [Part::Mirroring] Part__Mirroring023  label="door_base_pillar_sketch (Mirror #27)"
  Base = (0,0,0)
  Normal = (-0.5,0.866025,0)
  Source = -> Sketch128
  expr: .Normal.x = sin(-30)
  expr: .Normal.y = cos(-30)
FEATURE [Sketcher::SketchObject] Sketch153
  ExternalGeometry = -> [Sketch137]
  FullyConstrained = true
  Placement = pos=(0,0,0) rot=(0.935113,0.250563,0.250563;1.63783rad)
  sketch-geometry (4):
    g0: LineSegment StartX=0 StartY=0 StartZ=0 EndX=272.65 EndY=-1.31e-14 EndZ=0
    g1: LineSegment StartX=272.65 StartY=-1.31e-14 StartZ=0 EndX=272.65 EndY=1116 EndZ=0
    g2: LineSegment StartX=272.65 StartY=1116 StartZ=0 EndX=0 EndY=1116 EndZ=0
    g3: LineSegment StartX=0 StartY=1116 StartZ=0 EndX=0 EndY=0 EndZ=0
  constraints (10):
    c: Coincident(g0,g1)
    c: Coincident(g1,g2)
    c: Coincident(g2,g3)
    c: Coincident(g3,g0)
    c: Horizontal(g2)
    c: Vertical(g1)
    c: Vertical(g3)
    c: Coincident(g0,g-1)
    c: Coincident(g-3,g0)
    c: DistanceY(g1,g1) = 1116
FEATURE [Sketcher::SketchObject] Sketch152
  ExternalGeometry = -> [Part__Mirroring023,Sketch146,Sketch153]
  FullyConstrained = true
  sketch-geometry (12):
    g0: LineSegment StartX=313.489 StartY=-130.764 StartZ=0 EndX=327.029 EndY=-138.581 EndZ=0
    g1: LineSegment StartX=327.029 StartY=-138.581 StartZ=0 EndX=337.863 EndY=-115.348 EndZ=0
    g2: LineSegment StartX=337.863 StartY=-115.348 StartZ=0 EndX=267.995 EndY=103.92 EndZ=0
    g3: LineSegment StartX=258.122 StartY=98.2199 StartZ=0 EndX=313.489 EndY=-130.764 EndZ=0
    g4: LineSegment StartX=251.497 StartY=94.3949 StartZ=0 EndX=249.497 EndY=97.859 EndZ=0
    g5: LineSegment StartX=269.727 StartY=104.92 StartZ=0 EndX=267.727 EndY=108.384 EndZ=0
    g6: LineSegment StartX=311.489 StartY=-134.228 StartZ=0 EndX=313.489 EndY=-130.764 EndZ=0
    g7: LineSegment StartX=337.863 StartY=-115.348 StartZ=0 EndX=341.488 EndY=-117.039 EndZ=0
    g8: LineSegment StartX=236.122 StartY=136.325 StartZ=0 EndX=258.122 EndY=98.2199 EndZ=0
    g9: LineSegment StartX=258.122 StartY=98.2199 StartZ=0 EndX=251.497 EndY=94.3949 EndZ=0
    g10: LineSegment StartX=269.727 StartY=104.92 StartZ=0 EndX=267.995 EndY=103.92 EndZ=0
    g11: LineSegment StartX=267.995 StartY=103.92 StartZ=0 EndX=258.122 EndY=98.2199 EndZ=0
  constraints (31):
    c: Coincident(g0,g1)
    c: Coincident(g1,g2)
    c: Coincident(g3,g0)
    c: Coincident(g4,g9)
    c: Coincident(g4,g-5)
    c: Coincident(g5,g-5)
    c: Perpendicular(g-5,g5)
    c: Perpendicular(g-5,g4)
    c: Distance(g4) = 4
    c: Equal(g5,g4)
    c: Parallel(g0,g-4)
    c: Parallel(g1,g-3)
    c: Coincident(g6,g-4)
    c: Coincident(g6,g0)
    c: Coincident(g7,g1)
    c: Coincident(g7,g-3)
    c: Perpendicular(g7,g-3)
    c: Perpendicular(g6,g-4)
    c: Equal(g6,g7)
    c: Equal(g7,g4)
    c: Coincident(g8,g-6)
    c: Coincident(g11,g9)
    c: Perpendicular(g9,g8)
    c: Coincident(g11,g8)
    c: Coincident(g3,g11)
    c: Coincident(g10,g5)
    c: Coincident(g10,g11)
    c: Perpendicular(g10,g8)
    c: Perpendicular(g11,g8)
    c: Distance(g10,g10) = 2
    c: Coincident(g2,g10)
FEATURE [PartDesign::SubShapeBinder] Binder102
  BindCopyOnChange = 0
  BindMode = 0
  ClaimChildren = true
  Context = -> Part015 [Body100.Binder102.]
  Fuse = false
  MakeFace = true
  OffsetFill = false
  OffsetIntersection = false
  OffsetJoinType = 0
  OffsetOpenResult = false
  PartialLoad = false
  Relative = true
  Support = -> [Sketch153]
  _Version = 2
FEATURE [PartDesign::Pocket] Pocket076
  BaseFeature = -> BaseBend039
  Direction = (0.5,-0.866025,-2e-16)
  Length = 5
  Length2 = 5
  Midplane = true
  Profile = -> Binder102
  Suppressed = false
  Type = 1
FEATURE [PartDesign::SubShapeBinder] Binder103
  BindCopyOnChange = 0
  BindMode = 0
  ClaimChildren = true
  Context = -> Body103 [Binder103.]
  Fuse = false
  MakeFace = true
  OffsetFill = false
  OffsetIntersection = false
  OffsetJoinType = 0
  OffsetOpenResult = false
  PartialLoad = false
  Relative = false
  Support = -> [Sketch152]
  _Version = 2
FEATURE [Sketcher::SketchObject] Sketch154
  AttachmentOffset = pos=(0,0,0) rot=(0,1,0;-1.0472rad)
  AttachmentSupport = -> [XZ_Plane070]
  FullyConstrained = false
  MapMode = 5
  Placement = pos=(0,0,0) rot=(-0.774597,0.447214,0.447214;4.45971rad)
  sketch-geometry (4):
    g0: LineSegment StartX=72.1252 StartY=1580.58 StartZ=0 EndX=37 EndY=1580.58 EndZ=0
    g1: LineSegment StartX=37 StartY=1580.58 StartZ=0 EndX=37 EndY=1137.47 EndZ=0
    g2: LineSegment StartX=37 StartY=1137.47 StartZ=0 EndX=72.1252 EndY=1137.47 EndZ=0
    g3: LineSegment StartX=72.1252 StartY=1137.47 StartZ=0 EndX=72.1252 EndY=1580.58 EndZ=0
  constraints (9):
    c: Coincident(g0,g1)
    c: Coincident(g1,g2)
    c: Coincident(g2,g3)
    c: Coincident(g3,g0)
    c: Horizontal(g0)
    c: Horizontal(g2)
    c: Vertical(g1)
    c: Vertical(g3)
    c: DistanceX(g1) = 37
FEATURE [PartDesign::Pocket] Pocket080
  BaseFeature = -> Pocket076
  Direction = (0.866025,0.5,-1e-16)
  Length = 5
  Length2 = 5
  Midplane = true
  Profile = -> Sketch154
  ReferenceAxis = -> Sketch154 [N_Axis]
  Suppressed = false
  Type = 1
FEATURE [Sketcher::SketchObject] Sketch155
  ExternalGeometry = -> [Sketch152]
  FullyConstrained = true
  sketch-geometry (4):
    g0: LineSegment StartX=266.995 StartY=105.652 StartZ=0 EndX=255.826 EndY=99.2039 EndZ=0
    g1: LineSegment StartX=255.826 StartY=99.2039 StartZ=0 EndX=258.857 EndY=86.6692 EndZ=0
    g2: LineSegment StartX=258.857 StartY=86.6692 StartZ=0 EndX=260.801 EndY=87.1392 EndZ=0
    g3: LineSegment StartX=267.995 StartY=103.92 StartZ=0 EndX=266.995 EndY=105.652 EndZ=0
  constraints (12):
    c: Coincident(g1,g0)
    c: Coincident(g2,g1)
    c: PointOnObject(g2,g-4)
    c: Coincident(g3,g-3)
    c: Coincident(g3,g0)
    c: Perpendicular(g-3,g3)
    c: Perpendicular(g0,g3)
    c: Perpendicular(g2,g-4)
    c: Perpendicular(g1,g2)
    c: Equal(g2,g3)
    c: Distance(g3) = 2
    c: Equal(g1,g0)
FEATURE [PartDesign::SubShapeBinder] Binder104
  BindCopyOnChange = 0
  BindMode = 0
  ClaimChildren = false
  Context = -> Part015 [Body104.Binder104.]
  Fuse = false
  MakeFace = true
  OffsetFill = false
  OffsetIntersection = false
  OffsetJoinType = 0
  OffsetOpenResult = false
  PartialLoad = false
  Relative = true
  Support = -> [Sketch155]
  _Version = 2
FEATURE [PartDesign::FeaturePython] BaseBend042  # WARN: FeaturePython — macro-defined, semantics opaque (R4)
  BendSide = 1
  BendSketch = -> Binder104
  MidPlane = false
  Reverse = true
  Suppressed = false
  length = 15
  radius = 1
  thickness = 1
FEATURE [PartDesign::SubShapeBinder] Binder105
  BindCopyOnChange = 0
  BindMode = 0
  ClaimChildren = true
  Context = -> Part015 [Body103.Binder105.]
  Fuse = false
  MakeFace = true
  OffsetFill = false
  OffsetIntersection = false
  OffsetJoinType = 0
  OffsetOpenResult = false
  PartialLoad = false
  Relative = true
  _Version = 2
FEATURE [PartDesign::FeaturePython] BaseBend041  # WARN: FeaturePython — macro-defined, semantics opaque (R4)
  BendSide = 0
  BendSketch = -> Binder103
  MidPlane = false
  Reverse = false
  Suppressed = false
  length = 100
  radius = 2
  thickness = 1
FEATURE [PartDesign::FeaturePython] Bend024  # WARN: FeaturePython — macro-defined, semantics opaque (R4)
  AutoMiter = false
  BaseFeature = -> BaseBend041
  BendType = 0
  LengthList = [15]
  LengthSpec = 0
  ReliefFactor = 0.7
  Suppressed = false
  UseReliefFactor = false
  angle = 90
  baseObject = -> BaseBend041 [Edge13,Edge15]
  bendAList = [90]
  extend1 = 0
  extend2 = 0
  gap1 = 0
  gap2 = 0
  invert = false
  kfactor = 0.5
  length = 15
  maxExtendDist = 5
  minGap = 0.1
  minReliefGap = 1
  miterangle1 = 0
  miterangle2 = 0
  offset = 0
  radius = 2
  reliefType = 0
  reliefd = 1
  reliefw = 0.8
  sketchflip = false
  sketchinvert = false
  unfold = false
  expr: radius = BaseBend041.radius
FEATURE [Sketcher::SketchObject] Sketch156
  AttachmentSupport = -> [XY_Plane073]
  ExternalGeometry = -> [Binder103]
  FullyConstrained = true
  MapMode = 5
  sketch-geometry (3):
    g0: ArcOfCircle CenterX=324.804 CenterY=-131.523 CenterZ=0 NormalX=0 NormalY=0 NormalZ=1 AngleXU=0 Radius=5 StartAngle=4.18879 EndAngle=5.84685
    g1: LineSegment StartX=322.304 StartY=-135.853 StartZ=0 EndX=327.029 EndY=-138.581 EndZ=0
    g2: LineSegment StartX=327.029 StartY=-138.581 StartZ=0 EndX=329.335 EndY=-133.636 EndZ=0
  constraints (7):
    c: Tangent(g0,g-4) = -1.5708
    c: Tangent(g0,g-3) = -1.5708
    c: Radius(g0) = 5
    c: Coincident(g1,g0)
    c: Coincident(g1,g-4)
    c: Coincident(g2,g1)
    c: Coincident(g2,g0)
FEATURE [App::Link] Link008  label="Part019"
  LinkPlacement = pos=(0,0,1090) rot=(0,0,1;0rad)
  LinkedObject = -> Part018
  Placement = pos=(0,0,1090) rot=(0,0,1;0rad)
FEATURE [PartDesign::CoordinateSystem] Local_CS003
  AttacherType = Attacher::AttachEngine3D
  AttachmentOffset = pos=(0,0,0) rot=(0,0,1;0.523599rad)
  AttachmentSupport = -> [XY_Plane060]
  MapMode = 5
  Placement = pos=(0,0,0) rot=(0,0,1;0.523599rad)
FEATURE [Sketcher::SketchObject] Sketch157
  AttachmentSupport = -> [Local_CS003]
  ExternalGeometry = -> [Binder082]
  FullyConstrained = true
  MapMode = 3
  Placement = pos=(0,0,0) rot=(0.935113,0.250563,0.250563;1.63783rad)
  sketch-geometry (12):
    g0: Circle CenterX=277.85 CenterY=10 CenterZ=0 NormalX=0 NormalY=0 NormalZ=1 AngleXU=0 Radius=1.7
    g1: LineSegment StartX=277.85 StartY=1100 StartZ=0 EndX=277.85 EndY=1090 EndZ=0
    g2: LineSegment StartX=277.85 StartY=1090 StartZ=0 EndX=277.85 EndY=820 EndZ=0
    g3: LineSegment StartX=277.85 StartY=820 StartZ=0 EndX=277.85 EndY=550 EndZ=0
    g4: LineSegment StartX=277.85 StartY=550 StartZ=0 EndX=277.85 EndY=280 EndZ=0
    g5: LineSegment StartX=277.85 StartY=280 StartZ=0 EndX=277.85 EndY=10 EndZ=0
    g6: LineSegment StartX=277.85 StartY=10 StartZ=0 EndX=277.85 EndY=1.8e-15 EndZ=0
    g7: Circle CenterX=277.85 CenterY=280 CenterZ=0 NormalX=0 NormalY=0 NormalZ=1 AngleXU=0 Radius=1.7
    g8: Circle CenterX=277.85 CenterY=550 CenterZ=0 NormalX=0 NormalY=0 NormalZ=1 AngleXU=0 Radius=1.7
    g9: Circle CenterX=277.85 CenterY=820 CenterZ=0 NormalX=0 NormalY=0 NormalZ=1 AngleXU=0 Radius=1.7
    g10: Circle CenterX=277.85 CenterY=1090 CenterZ=0 NormalX=0 NormalY=0 NormalZ=1 AngleXU=0 Radius=1.7
    g11: GeomPoint X=276.15 Y=10 Z=0
  constraints (31):
    c: Vertical(g1)
    c: DistanceY(g1) = 1100
    c: Coincident(g2,g1)
    c: Vertical(g2)
    c: Coincident(g2,g3)
    c: Vertical(g3)
    c: Coincident(g3,g4)
    c: Vertical(g4)
    c: Coincident(g4,g5)
    c: Coincident(g5,g0)
    c: Vertical(g5)
    c: Coincident(g5,g6)
    c: PointOnObject(g6,g-3)
    c: Vertical(g6)
    c: Equal(g6,g1)
    c: Equal(g5,g4)
    c: Equal(g4,g3)
    c: Equal(g3,g2)
    c: Coincident(g7,g4)
    c: Coincident(g8,g3)
    c: Coincident(g9,g2)
    c: Coincident(g10,g1)
    c: Equal(g10,g9)
    c: Equal(g10,g8)
    c: Equal(g10,g7)
    c: Equal(g10,g0)
    c: Diameter(g10) = 3.4
    c: PointOnObject(g11,g0)
    c: Horizontal(g0,g11)
    c: DistanceX(g-3,g11) = 3.5
    c: DistanceY(g6,g6) = 10
FEATURE [PartDesign::Pocket] Pocket083
  BaseFeature = -> BaseBend033
  Direction = (-0.5,0.866025,0)
  Length = 5
  Length2 = 5
  Midplane = true
  Profile = -> Sketch157
  ReferenceAxis = -> Sketch157 [N_Axis]
  Suppressed = false
  Type = 1
FEATURE [PartDesign::SubShapeBinder] Binder106
  BindCopyOnChange = 0
  BindMode = 0
  ClaimChildren = true
  Context = -> Part015 [Part017.Body100.Binder106.]
  Fuse = false
  MakeFace = true
  OffsetFill = false
  OffsetIntersection = false
  OffsetJoinType = 0
  OffsetOpenResult = false
  PartialLoad = false
  Relative = true
  Support = -> [Part016[Body094.Pocket083.Sketch157.]]
  _Version = 2
FEATURE [PartDesign::Pocket] Pocket084
  BaseFeature = -> Pocket080
  Direction = (0.5,-0.866025,-2e-16)
  Length = 5
  Length2 = 5
  Midplane = true
  Profile = -> Binder106
  Suppressed = false
  Type = 1
FEATURE [PartDesign::SubShapeBinder] Binder107
  BindCopyOnChange = 0
  BindMode = 0
  ClaimChildren = true
  Context = -> Part015 [Part017.Body101.Binder107.]
  Fuse = false
  MakeFace = true
  OffsetFill = false
  OffsetIntersection = false
  OffsetJoinType = 0
  OffsetOpenResult = false
  PartialLoad = false
  Relative = true
  Support = -> [Part016[Body094.Pocket083.Sketch157.]]
  _Version = 2
FEATURE [PartDesign::Pocket] Pocket085
  BaseFeature = -> Pocket077
  Direction = (0.5,-0.866025,-2e-16)
  Length = 5
  Length2 = 5
  Midplane = true
  Profile = -> Binder107
  Suppressed = false
  Type = 1
FEATURE [Sketcher::SketchObject] Sketch158
  AttachmentOffset = pos=(0,0,37) rot=(0,0,1;0rad)
  AttachmentSupport = -> [Local_CS003]
  FullyConstrained = true
  MapMode = 3
  Placement = pos=(18.5,-32.0429,0) rot=(0.935113,0.250563,0.250563;1.63783rad)
  sketch-geometry (9):
    g0: Circle CenterX=277.349 CenterY=120 CenterZ=0 NormalX=0 NormalY=0 NormalZ=1 AngleXU=0 Radius=1.7
    g1: GeomPoint X=275.649 Y=120 Z=0
    g2: Circle CenterX=280.849 CenterY=129.3 CenterZ=0 NormalX=0 NormalY=0 NormalZ=1 AngleXU=0 Radius=1.7
    g3: Circle CenterX=277.349 CenterY=1060 CenterZ=0 NormalX=0 NormalY=0 NormalZ=1 AngleXU=0 Radius=1.7
    g4: Circle CenterX=280.849 CenterY=1069.3 CenterZ=0 NormalX=0 NormalY=0 NormalZ=1 AngleXU=0 Radius=1.7
    g5: LineSegment StartX=277.349 StartY=120 StartZ=0 EndX=280.849 EndY=120 EndZ=0
    g6: LineSegment StartX=280.849 StartY=120 StartZ=0 EndX=280.849 EndY=129.3 EndZ=0
    g7: LineSegment StartX=277.349 StartY=1060 StartZ=0 EndX=280.849 EndY=1060 EndZ=0
    g8: LineSegment StartX=280.849 StartY=1060 StartZ=0 EndX=280.849 EndY=1069.3 EndZ=0
  constraints (25):
    c: PointOnObject(g1,g0)
    c: Horizontal(g1,g0)
    c: DistanceX(g1) = 275.649
    c: Diameter(g0) = 3.4
    c: Equal(g0,g2)
    c: DistanceX(g0,g2) = 3.5
    c: DistanceY(g0,g2) = 9.3
    c: DistanceY(g2) = 129.3
    c: Vertical(g3,g0)
    c: Coincident(g5,g0)
    c: Horizontal(g5)
    c: Coincident(g5,g6)
    c: Coincident(g6,g2)
    c: Coincident(g7,g3)
    c: Horizontal(g7)
    c: Coincident(g7,g8)
    c: Coincident(g8,g4)
    c: Vertical(g8)
    c: Vertical(g6)
    c: Equal(g5,g7)
    c: Equal(g6,g8)
    c: Equal(g4,g3)
    c: Equal(g3,g0)
    c: DistanceY(g3) = 1060
    c: DistanceY(g0,g3) = 940
FEATURE [PartDesign::Pocket] Pocket086
  BaseFeature = -> Pocket083
  Direction = (-0.5,0.866025,0)
  Length = 5
  Length2 = 5
  Profile = -> Sketch158
  ReferenceAxis = -> Sketch158 [N_Axis]
  Reversed = true
  Suppressed = false
  Type = 1
FEATURE [PartDesign::Body] Body094  label="door_led_holder_material_0.30ansi"
  Group = -> [Binder082,BaseBend033,Local_CS003,Sketch157,Pocket083,Sketch158,Pocket086]
  Origin = -> Origin060
  Tip = -> Pocket086
FEATURE [App::Part] Part016
  Group = -> [Body094]
  Origin = -> Origin075
  Placement = pos=(0,0,340) rot=(0,0,1;0rad)
FEATURE [PartDesign::SubShapeBinder] Binder108
  BindCopyOnChange = 0
  BindMode = 0
  ClaimChildren = true
  Context = -> Part015 [Part017.Body100.Binder108.]
  Fuse = false
  MakeFace = true
  OffsetFill = false
  OffsetIntersection = false
  OffsetJoinType = 0
  OffsetOpenResult = false
  PartialLoad = false
  Relative = true
  Support = -> [Part016[Body094.Pocket086.Sketch158.]]
  _Version = 2
FEATURE [PartDesign::Pocket] Pocket087
  BaseFeature = -> Pocket084
  Direction = (0.5,-0.866025,-2e-16)
  Length = 5
  Length2 = 5
  Profile = -> Binder108
  Suppressed = false
  Type = 1
FEATURE [PartDesign::SubShapeBinder] Binder109
  BindCopyOnChange = 0
  BindMode = 0
  ClaimChildren = true
  Context = -> Part015 [Part017.Part018.Body103.Binder109.]
  Fuse = false
  MakeFace = true
  OffsetFill = false
  OffsetIntersection = false
  OffsetJoinType = 0
  OffsetOpenResult = false
  PartialLoad = false
  Relative = true
  Support = -> [Part016[Body094.Pocket086.Sketch158.]]
  _Version = 2
FEATURE [PartDesign::SubShapeBinder] Binder110
  BindCopyOnChange = 0
  BindMode = 0
  ClaimChildren = true
  Context = -> Part015 [Part017.Part018.Body104.Binder110.]
  Fuse = false
  MakeFace = true
  OffsetFill = false
  OffsetIntersection = false
  OffsetJoinType = 0
  OffsetOpenResult = false
  PartialLoad = false
  Relative = true
  Support = -> [Part016[Body094.Pocket086.Sketch158.]]
  _Version = 2
FEATURE [Sketcher::SketchObject] Sketch159
  AttachmentSupport = -> [BaseBend034]
  FullyConstrained = true
  MapMode = 5
  Placement = pos=(40.5,0,0) rot=(0.57735,0.57735,0.57735;2.0944rad)
  sketch-geometry (2):
    g0: Circle CenterX=345 CenterY=1094 CenterZ=0 NormalX=0 NormalY=0 NormalZ=1 AngleXU=0 Radius=1.7
    g1: Circle CenterX=345 CenterY=154 CenterZ=0 NormalX=0 NormalY=0 NormalZ=1 AngleXU=0 Radius=1.7
  constraints (6):
    c: DistanceY(g0) = 1094
    c: DistanceY(g1,g0) = 940
    c: Equal(g0,g1)
    c: Diameter(g0) = 3.4
    c: Vertical(g1,g0)
    c: DistanceX(g0) = 345
FEATURE [Sketcher::SketchObject] Sketch160
  AttachmentSupport = -> [BaseBend034]
  FullyConstrained = true
  MapMode = 5
  Placement = pos=(31.1979,356.594,0) rot=(0.998099,-0.043578,-0.043578;1.5727rad)
  sketch-geometry (8):
    g0: Circle CenterX=17.5 CenterY=1094 CenterZ=0 NormalX=0 NormalY=0 NormalZ=1 AngleXU=0 Radius=1.7
    g1: Circle CenterX=33.5 CenterY=1094 CenterZ=0 NormalX=0 NormalY=0 NormalZ=1 AngleXU=0 Radius=1.7
    g2: Circle CenterX=17.5 CenterY=154 CenterZ=0 NormalX=0 NormalY=0 NormalZ=1 AngleXU=0 Radius=1.7
    g3: Circle CenterX=33.5 CenterY=154 CenterZ=0 NormalX=0 NormalY=0 NormalZ=1 AngleXU=0 Radius=1.7
    g4: LineSegment StartX=17.5 StartY=154 StartZ=0 EndX=33.5 EndY=154 EndZ=0
    g5: LineSegment StartX=33.5 StartY=154 StartZ=0 EndX=33.5 EndY=1094 EndZ=0
    g6: LineSegment StartX=33.5 StartY=1094 StartZ=0 EndX=17.5 EndY=1094 EndZ=0
    g7: LineSegment StartX=17.5 StartY=1094 StartZ=0 EndX=17.5 EndY=154 EndZ=0
  constraints (20):
    c: Equal(g0,g1)
    c: Diameter(g0) = 3.4
    c: Equal(g2,g3)
    c: Equal(g3,g0)
    c: Coincident(g4,g5)
    c: Coincident(g5,g6)
    c: Coincident(g6,g7)
    c: Coincident(g7,g4)
    c: Horizontal(g4)
    c: Horizontal(g6)
    c: Vertical(g5)
    c: Vertical(g7)
    c: Coincident(g4,g2)
    c: Coincident(g5,g1)
    c: Coincident(g4,g3)
    c: Coincident(g6,g0)
    c: DistanceY(g0) = 1094
    c: DistanceY(g7,g7) = 940
    c: DistanceX(g6,g6) = 16
    c: DistanceX(g0) = 17.5
FEATURE [PartDesign::SubShapeBinder] Binder111
  BindCopyOnChange = 0
  BindMode = 0
  ClaimChildren = false
  Context = -> Part013 [Body093.Binder111.]
  Fuse = false
  MakeFace = true
  OffsetFill = false
  OffsetIntersection = false
  OffsetJoinType = 0
  OffsetOpenResult = false
  PartialLoad = false
  Relative = true
  Support = -> [Compound047[Body095.Pocket090.Sketch159.]]
  _Version = 2
FEATURE [PartDesign::SubShapeBinder] Binder112
  BindCopyOnChange = 0
  BindMode = 0
  ClaimChildren = false
  Context = -> Part013 [Body093.Binder112.]
  Fuse = false
  MakeFace = true
  OffsetFill = false
  OffsetIntersection = false
  OffsetJoinType = 0
  OffsetOpenResult = false
  PartialLoad = false
  Relative = true
  Support = -> [Compound047[Body095.Pocket091.Sketch160.]]
  _Version = 2
FEATURE [Sketcher::SketchObject] Sketch161
  AttachmentSupport = -> [BaseBend034]
  FullyConstrained = true
  MapMode = 5
  Placement = pos=(40.5,0,0) rot=(0.57735,0.57735,0.57735;2.0944rad)
  sketch-geometry (8):
    g0: Circle CenterX=343.262 CenterY=363.2 CenterZ=0 NormalX=0 NormalY=0 NormalZ=1 AngleXU=0 Radius=2
    g1: Circle CenterX=343.262 CenterY=300 CenterZ=0 NormalX=0 NormalY=0 NormalZ=1 AngleXU=0 Radius=2
    g2: Circle CenterX=343.262 CenterY=1063 CenterZ=0 NormalX=0 NormalY=0 NormalZ=1 AngleXU=0 Radius=2
    g3: Circle CenterX=343.262 CenterY=999.8 CenterZ=0 NormalX=0 NormalY=0 NormalZ=1 AngleXU=0 Radius=2
    g4: LineSegment StartX=343.262 StartY=1063 StartZ=0 EndX=343.262 EndY=999.8 EndZ=0
    g5: LineSegment StartX=343.262 StartY=999.8 StartZ=0 EndX=343.262 EndY=363.2 EndZ=0
    g6: LineSegment StartX=343.262 StartY=363.2 StartZ=0 EndX=343.262 EndY=300 EndZ=0
    g7: GeomPoint X=353.262 Y=301.263 Z=0
  constraints (21):
    c: Coincident(g4,g2)
    c: Vertical(g4)
    c: Coincident(g4,g5)
    c: Coincident(g5,g0)
    c: Vertical(g5)
    c: Coincident(g5,g6)
    c: Coincident(g6,g1)
    c: Vertical(g6)
    c: Coincident(g4,g3)
    c: Equal(g4,g6)
    c: DistanceY(g6,g6) = 63.2
    c: DistanceY(g2) = 1063
    c: DistanceY(g1) = 300
    c: Equal(g1,g0)
    c: Equal(g1,g3)
    c: Equal(g1,g2)
    c: Diameter(g1) = 4
    c: DistanceX(g1) = 343.262
    c: DistanceX(g7) = 353.262
    c: DistanceY(g7) = 301.263
    c: DistanceX(g1,g7) = 10
FEATURE [Sketcher::SketchObject] Sketch162
  AttachmentSupport = -> [BaseBend034]
  FullyConstrained = true
  MapMode = 5
  Placement = pos=(31.1979,356.594,0) rot=(0.998099,-0.043578,-0.043578;1.5727rad)
  sketch-geometry (11):
    g0: LineSegment StartX=20 StartY=15 StartZ=0 EndX=20 EndY=250 EndZ=0
    g1: LineSegment StartX=20 StartY=250 StartZ=0 EndX=20 EndY=485 EndZ=0
    g2: LineSegment StartX=20 StartY=485 StartZ=0 EndX=20 EndY=720 EndZ=0
    g3: LineSegment StartX=20 StartY=720 StartZ=0 EndX=20 EndY=955 EndZ=0
    g4: LineSegment StartX=20 StartY=955 StartZ=0 EndX=20 EndY=1190 EndZ=0
    g5: Circle CenterX=20 CenterY=15 CenterZ=0 NormalX=0 NormalY=0 NormalZ=1 AngleXU=0 Radius=1.7
    g6: Circle CenterX=20 CenterY=250 CenterZ=0 NormalX=0 NormalY=0 NormalZ=1 AngleXU=0 Radius=1.7
    g7: Circle CenterX=20 CenterY=485 CenterZ=0 NormalX=0 NormalY=0 NormalZ=1 AngleXU=0 Radius=1.7
    g8: Circle CenterX=20 CenterY=720 CenterZ=0 NormalX=0 NormalY=0 NormalZ=1 AngleXU=0 Radius=1.7
    g9: Circle CenterX=20 CenterY=955 CenterZ=0 NormalX=0 NormalY=0 NormalZ=1 AngleXU=0 Radius=1.7
    g10: Circle CenterX=20 CenterY=1190 CenterZ=0 NormalX=0 NormalY=0 NormalZ=1 AngleXU=0 Radius=1.7
  constraints (24):
    c: Vertical(g0)
    c: Coincident(g0,g1)
    c: Vertical(g1)
    c: Coincident(g1,g2)
    c: Vertical(g2)
    c: Coincident(g2,g3)
    c: Vertical(g3)
    c: Coincident(g3,g4)
    c: Vertical(g4)
    c: Equal(g0,g1)
    c: Equal(g1,g2)
    c: Equal(g2,g3)
    c: Equal(g3,g4)
    c: Coincident(g5,g0)
    c: Coincident(g6,g0)
    c: Coincident(g7,g1)
    c: Coincident(g8,g2)
    c: Coincident(g9,g3)
    c: Coincident(g10,g4)
    c: Equal(g5, g6-g10) x5
    c: Diameter(g5) = 3.4
    c: DistanceY(g10) = 1190
    c: DistanceY(g5) = 15
    c: DistanceX(g5) = 20
FEATURE [PartDesign::Pocket] Pocket095
  BaseFeature = -> Pocket075
  Direction = (0.0871557,0.996195,3e-16)
  Length = 5
  Length2 = 5
  Profile = -> Sketch162
  ReferenceAxis = -> Sketch162 [N_Axis]
  Suppressed = false
  Type = 0
FEATURE [PartDesign::Pocket] Pocket094
  BaseFeature = -> Pocket095
  Direction = (-1,0,0)
  Length = 5
  Length2 = 5
  Profile = -> Sketch161
  ReferenceAxis = -> Sketch161 [N_Axis]
  Suppressed = false
  Type = 0
FEATURE [PartDesign::Pocket] Pocket090
  BaseFeature = -> Pocket094
  Direction = (-1,0,0)
  Length = 5
  Length2 = 5
  Profile = -> Sketch159
  ReferenceAxis = -> Sketch159 [N_Axis]
  Suppressed = false
  Type = 0
FEATURE [PartDesign::Pocket] Pocket091
  BaseFeature = -> Pocket090
  Direction = (0.0871557,0.996195,3e-16)
  Length = 5
  Length2 = 5
  Profile = -> Sketch160
  ReferenceAxis = -> Sketch160 [N_Axis]
  Suppressed = false
  Type = 0
FEATURE [PartDesign::Body] Body095  label="door_base_pillar_material_0.45ansi"
  Group = -> [Binder083,BaseBend034,Pocket075,Binder092,Sketch159,Sketch160,Sketch161,Sketch162,Pocket095,Pocket094,Pocket090,Pocket091]
  Origin = -> Origin061
  Tip = -> Pocket091
FEATURE [Part::Compound] Compound046
  Links = -> [Body095]
FEATURE [Part::Mirroring] Part__Mirroring025  label="door_base_pillar (Mirror #29)"
  Base = (0,0,0)
  Normal = (-0.5,0.866025,0)
  Placement = pos=(0,0,312) rot=(0,0,1;0rad)
  Source = -> Compound046
  expr: .Normal.x = sin(-30)
  expr: .Normal.y = cos(-30)
FEATURE [Part::Compound] Compound047
  Links = -> [Body095]
FEATURE [Sketcher::SketchObject] Sketch163
  AttachmentSupport = -> [BaseBend039]
  FullyConstrained = false
  MapMode = 5
  Placement = pos=(247.727,143.025,0) rot=(0.774597,-0.447214,-0.447214;1.82348rad)
  sketch-geometry (17):
    g0: LineSegment StartX=21.5 StartY=12 StartZ=0 EndX=21.5 EndY=246.6 EndZ=0
    g1: LineSegment StartX=21.5 StartY=246.6 StartZ=0 EndX=21.5 EndY=481.2 EndZ=0
    g2: LineSegment StartX=21.5 StartY=481.2 StartZ=0 EndX=21.5 EndY=715.8 EndZ=0
    g3: LineSegment StartX=21.5 StartY=715.8 StartZ=0 EndX=21.5 EndY=950.4 EndZ=0
    g4: LineSegment StartX=21.5 StartY=950.4 StartZ=0 EndX=21.5 EndY=1185 EndZ=0
    g5: Circle CenterX=21.5 CenterY=246.6 CenterZ=0 NormalX=0 NormalY=0 NormalZ=1 AngleXU=0 Radius=1.7
    g6: Circle CenterX=21.5 CenterY=481.2 CenterZ=0 NormalX=0 NormalY=0 NormalZ=1 AngleXU=0 Radius=1.7
    g7: Circle CenterX=21.5 CenterY=715.8 CenterZ=0 NormalX=0 NormalY=0 NormalZ=1 AngleXU=0 Radius=1.7
    g8: Circle CenterX=21.5 CenterY=950.4 CenterZ=0 NormalX=0 NormalY=0 NormalZ=1 AngleXU=0 Radius=1.7
    g9: Circle CenterX=21.5 CenterY=1185 CenterZ=0 NormalX=0 NormalY=0 NormalZ=1 AngleXU=0 Radius=1.7
    g10: ArcOfCircle CenterX=21.5 CenterY=12 CenterZ=0 NormalX=0 NormalY=0 NormalZ=1 AngleXU=0 Radius=1.7 StartAngle=-3.29e-14 EndAngle=3.14159
    g11: ArcOfCircle CenterX=21.5 CenterY=5 CenterZ=0 NormalX=0 NormalY=0 NormalZ=1 AngleXU=0 Radius=1.7 StartAngle=3.14159 EndAngle=6.28319
    g12: LineSegment StartX=19.8 StartY=12 StartZ=0 EndX=19.8 EndY=5 EndZ=0
    g13: LineSegment StartX=23.2 StartY=5 StartZ=0 EndX=23.2 EndY=12 EndZ=0
    g14: Circle CenterX=32.5346 CenterY=1133.99 CenterZ=0 NormalX=0 NormalY=0 NormalZ=1 AngleXU=0 Radius=2.5
    g15: LineSegment StartX=14 StartY=4.03894 StartZ=0 EndX=21.5 EndY=4.03894 EndZ=0
    g16: LineSegment StartX=21.5 StartY=4.03894 StartZ=0 EndX=29 EndY=4.03894 EndZ=0
  constraints (42):
    c: Vertical(g0)
    c: Coincident(g0,g1)
    c: Vertical(g1)
    c: Coincident(g1,g2)
    c: Vertical(g2)
    c: Coincident(g2,g3)
    c: Vertical(g3)
    c: Coincident(g3,g4)
    c: Vertical(g4)
    c: Coincident(g5,g0)
    c: Coincident(g6,g1)
    c: Coincident(g7,g2)
    c: Coincident(g8,g3)
    c: Coincident(g9,g4)
    c: Equal(g0,g1)
    c: Equal(g1,g2)
    c: Equal(g2,g3)
    c: Equal(g3,g4)
    c: Diameter(g5) = 3.4
    c: Tangent(g10,g12) = -1.5708
    c: Tangent(g12,g11) = -1.5708
    c: Tangent(g11,g13) = -1.5708
    c: Tangent(g13,g10) = -1.5708
    c: Equal(g10,g11)
    c: Coincident(g10,g0)
    c: Vertical(g12)
    c: Equal(g11,g5)
    c: DistanceY(g11,g10) = 7
    c: DistanceY(g11) = 5
    c: DistanceY(g9) = 1185
    c: Equal(g9,g8)
    c: Equal(g8,g7)
    c: Equal(g7,g6)
    c: Equal(g6,g5)
    c: Diameter(g14) = 5
    c: Horizontal(g15)
    c: Coincident(g16,g15)
    c: Horizontal(g16)
    c: DistanceX(g15) = 14
    c: DistanceX(g16) = 29
    c: Equal(g16,g15)
    c: Vertical(g15,g11)
FEATURE [PartDesign::Pocket] Pocket096
  BaseFeature = -> Pocket087
  Direction = (0.866025,0.5,0)
  Length = 5
  Length2 = 5
  Midplane = true
  Profile = -> Sketch163
  ReferenceAxis = -> Sketch163 [N_Axis]
  Suppressed = false
  Type = 1
FEATURE [PartDesign::SubShapeBinder] Binder113
  BindCopyOnChange = 0
  BindMode = 0
  ClaimChildren = true
  Context = -> Part015 [Part017.Body101.Binder113.]
  Fuse = false
  MakeFace = true
  OffsetFill = false
  OffsetIntersection = false
  OffsetJoinType = 0
  OffsetOpenResult = false
  PartialLoad = false
  Relative = true
  Support = -> [Body100[Pocket096.Sketch163.]]
  _Version = 2
FEATURE [PartDesign::Pocket] Pocket097
  BaseFeature = -> Pocket085
  Direction = (-0.866025,-0.5,0)
  Length = 5
  Length2 = 5
  Midplane = true
  Profile = -> Binder113
  Suppressed = false
  Type = 1
FEATURE [Sketcher::SketchObject] Sketch164
  AttachmentSupport = -> [Bend024]
  FullyConstrained = false
  MapMode = 5
  Placement = pos=(263.386,63.6858,-2.92e-14) rot=(0.668332,-0.525991,-0.525991;1.96328rad)
  sketch-geometry (1):
    g0: Circle CenterX=26.3683 CenterY=-9.22528 CenterZ=0 NormalX=0 NormalY=0 NormalZ=1 AngleXU=0 Radius=1.7
  constraints (1):
    c: Diameter(g0) = 3.4
FEATURE [PartDesign::SubShapeBinder] Binder114
  BindCopyOnChange = 0
  BindMode = 0
  ClaimChildren = true
  Context = -> Part015 [Part017.Part018.Body104.Binder114.]
  Fuse = false
  MakeFace = true
  OffsetFill = false
  OffsetIntersection = false
  OffsetJoinType = 0
  OffsetOpenResult = false
  PartialLoad = false
  Relative = true
  Support = -> [Body103[Pocket098.Sketch164.]]
  _Version = 2
FEATURE [Sketcher::SketchObject] Sketch165
  AttachmentSupport = -> [XY_Plane073]
  FullyConstrained = true
  MapMode = 5
  sketch-geometry (2):
    g0: Circle CenterX=267.044 CenterY=85.865 CenterZ=0 NormalX=0 NormalY=0 NormalZ=1 AngleXU=0 Radius=1.7
    g1: Circle CenterX=295.563 CenterY=-15.8437 CenterZ=0 NormalX=0 NormalY=0 NormalZ=1 AngleXU=0 Radius=1.7
  constraints (6):
    c: DistanceX(g0) = 267.044
    c: DistanceY(g0) = 85.865
    c: Diameter(g0) = 3.4
    c: Equal(g1,g0)
    c: DistanceX(g1) = 295.563
    c: DistanceY(g1) = -15.8437
FEATURE [PartDesign::Fillet] Fillet005
  Base = -> Bend020 [Edge2,Edge38,Edge50,Edge8]
  BaseFeature = -> Bend020
  Radius = 2
  SupportTransform = false
  Suppressed = false
  UseAllEdges = false
FEATURE [PartDesign::Pocket] Pocket074
  BaseFeature = -> Fillet005
  Direction = (0,0,-1)
  Length = 5
  Length2 = 5
  Midplane = true
  Profile = -> Binder091
  Suppressed = false
  Type = 1
FEATURE [PartDesign::Pocket] Pocket092
  BaseFeature = -> Pocket074
  Direction = (-1,0,0)
  Length = 5
  Length2 = 5
  Midplane = true
  Profile = -> Binder111
  Suppressed = false
  Type = 1
FEATURE [PartDesign::Pocket] Pocket093
  BaseFeature = -> Pocket092
  Direction = (-0.0871557,-0.996195,-4e-16)
  Length = 5
  Length2 = 5
  Midplane = true
  Profile = -> Binder112
  Suppressed = false
  Type = 1
FEATURE [PartDesign::Body] Body093  label="door_base_pillar_to_hor_fix_material_0.45ansi"
  Group = -> [Binder081,BaseBend032,Bend020,Binder091,Fillet005,Pocket074,Binder111,Binder112,Pocket092,Pocket093]
  Origin = -> Origin059
  Tip = -> Pocket093
FEATURE [App::Part] Part013  label="door3_hor_section"
  Group = -> [Body093]
  Origin = -> Origin067
  Placement = pos=(0,0,1101) rot=(0,0,1;0rad)
FEATURE [PartDesign::Fillet] Fillet006
  Base = -> BaseBend042 [Edge10,Edge8,Edge25,Edge23]
  BaseFeature = -> BaseBend042
  Radius = 2
  SupportTransform = false
  Suppressed = false
  UseAllEdges = false
FEATURE [PartDesign::Pocket] Pocket089
  BaseFeature = -> Fillet006
  Direction = (0.5,-0.866025,-2e-16)
  Length = 5
  Length2 = 5
  Profile = -> Binder110
  Suppressed = false
  Type = 1
FEATURE [PartDesign::Pocket] Pocket099
  BaseFeature = -> Pocket089
  Direction = (-0.97199,-0.235024,-6e-16)
  Length = 5
  Length2 = 5
  Midplane = true
  Profile = -> Binder114
  Suppressed = false
  Type = 1
FEATURE [PartDesign::Body] Body104  label="Body104_material_0.45ansi"
  Group = -> [Binder104,BaseBend042,Binder110,Fillet006,Pocket089,Binder114,Pocket099]
  Origin = -> Origin074
  Placement = pos=(0,0,10) rot=(0,0,1;0rad)
  Tip = -> Pocket099
FEATURE [PartDesign::Fillet] Fillet007
  Base = -> Bend024 [Edge2,Edge36,Edge47,Edge8,Edge40]
  BaseFeature = -> Bend024
  Radius = 2
  SupportTransform = false
  Suppressed = false
  UseAllEdges = false
FEATURE [PartDesign::Pocket] Pocket081
  BaseFeature = -> Fillet007
  Direction = (0,0,-1)
  Length = 5
  Length2 = 5
  Midplane = true
  Profile = -> Binder105
  Suppressed = false
  Type = 1
FEATURE [PartDesign::Pocket] Pocket082
  BaseFeature = -> Pocket081
  Direction = (0,0,-1)
  Length = 5
  Length2 = 5
  Profile = -> Sketch156
  ReferenceAxis = -> Sketch156 [N_Axis]
  Reversed = true
  Suppressed = false
  Type = 0
FEATURE [PartDesign::Pocket] Pocket088
  BaseFeature = -> Pocket082
  Direction = (0.5,-0.866025,-2e-16)
  Length = 5
  Length2 = 5
  Profile = -> Binder109
  Suppressed = false
  Type = 1
FEATURE [PartDesign::Pocket] Pocket098
  BaseFeature = -> Pocket088
  Direction = (0.97199,0.235024,2e-16)
  Length = 5
  Length2 = 5
  Midplane = true
  Profile = -> Sketch164
  ReferenceAxis = -> Sketch164 [N_Axis]
  Suppressed = false
  Type = 1
FEATURE [PartDesign::Pocket] Pocket100
  BaseFeature = -> Pocket098
  Direction = (0,0,-1)
  Length = 5
  Length2 = 5
  Midplane = true
  Profile = -> Sketch165
  ReferenceAxis = -> Sketch165 [N_Axis]
  Suppressed = false
  Type = 1
FEATURE [PartDesign::Body] Body103  label="Body103_material_0.45ansi"
  Group = -> [Binder103,BaseBend041,Bend024,Binder105,Fillet007,Pocket081,Sketch156,Pocket082,Binder109,Pocket088,Sketch164,Pocket098,Sketch165,Pocket100]
  Origin = -> Origin073
  Placement = pos=(0,0,12) rot=(0,0,1;0rad)
  Tip = -> Pocket100
FEATURE [PartDesign::Fillet] Fillet008
  Base = -> Pocket096 [Edge124,Edge18,Edge127,Edge83,Edge27,Edge125,Edge126,Edge22,Edge17]
  BaseFeature = -> Pocket096
  Radius = 2
  SupportTransform = false
  Suppressed = false
  UseAllEdges = false
FEATURE [PartDesign::Body] Body100  label="Body101_material_0.45ansi"
  Group = -> [Binder095,BaseBend039,Binder096,Pocket076,Binder101,Binder102,Sketch154,Pocket080,Binder106,Pocket084,Binder108,Pocket087,Sketch163,Pocket096,Fillet008]
  Origin = -> Origin070
  Tip = -> Fillet008
FEATURE [PartDesign::Fillet] Fillet010
  Base = -> Pocket097 [Edge23,Edge65,Edge18,Edge64,Edge62,Edge60]
  BaseFeature = -> Pocket097
  Radius = 2
  SupportTransform = false
  Suppressed = false
  UseAllEdges = false
FEATURE [PartDesign::Body] Body101  label="Body102"
  Group = -> [Binder097,BaseBend040,Binder098,Pocket077,Binder107,Pocket085,Binder113,Pocket097,Fillet010]
  Origin = -> Origin071
  Tip = -> Fillet010
FEATURE [Sketcher::SketchObject] Sketch166
  AttachmentOffset = pos=(349.171,0,0) rot=(0,0,1;0rad)
  AttachmentSupport = -> [YZ_Plane010]
  FullyConstrained = true
  MapMode = 5
  Placement = pos=(0,349.171,0) rot=(0.57735,0.57735,0.57735;2.0944rad)
  expr: .AttachmentOffset.Base.x = <<basement_sketch>>.Constraints.max_r
  sketch-geometry (3):
    g0: LineSegment StartX=-15 StartY=0 StartZ=0 EndX=0 EndY=15 EndZ=0
    g1: LineSegment StartX=0 StartY=15 StartZ=0 EndX=0 EndY=0 EndZ=0
    g2: LineSegment StartX=0 StartY=0 StartZ=0 EndX=-15 EndY=0 EndZ=0
  constraints (8):
    c: PointOnObject(g0,g-1)
    c: PointOnObject(g0,g-2)
    c: Coincident(g0,g1)
    c: Coincident(g1,g-1)
    c: Coincident(g1,g2)
    c: Coincident(g2,g0)
    c: Equal(g2,g1)
    c: DistanceY(g1,g1) = 15
FEATURE [Sketcher::SketchObject] Sketch167  label="basement_amplifier_sketch"
  AttachmentSupport = -> [XY_Plane078]
  FullyConstrained = true
  MapMode = 5
  sketch-geometry (10):
    g0: LineSegment StartX=-25 StartY=320.166 StartZ=0 EndX=25 EndY=320.166 EndZ=0
    g1: LineSegment StartX=80 StartY=46.188 StartZ=0 EndX=0 EndY=0 EndZ=0
    g2: LineSegment StartX=0 StartY=0 StartZ=0 EndX=-80 EndY=46.188 EndZ=0
    g3: LineSegment StartX=25 StartY=320.166 StartZ=0 EndX=79.5375 EndY=48.492 EndZ=0
    g4: LineSegment StartX=79.5375 StartY=48.492 StartZ=0 EndX=80 EndY=46.188 EndZ=0
    g5: LineSegment StartX=-80 StartY=46.188 StartZ=0 EndX=-79.5375 EndY=48.492 EndZ=0
    g6: LineSegment StartX=-79.5375 StartY=48.492 StartZ=0 EndX=-25 EndY=320.166 EndZ=0
    g7: LineSegment StartX=-79.7343 StartY=47.5116 StartZ=0 EndX=-83.6561 EndY=48.2988 EndZ=0
    g8: LineSegment StartX=-83.6561 StartY=48.2988 StartZ=0 EndX=-81.0134 EndY=45.2961 EndZ=0
    g9: LineSegment StartX=-81.0134 StartY=45.2961 StartZ=0 EndX=-80 EndY=46.188 EndZ=0
  constraints (27):
    c: Coincident(g2,g5)
    c: Coincident(g6,g0)
    c: Coincident(g0,g3)
    c: Coincident(g4,g1)
    c: Symmetric(g1,g2,g-2)
    c: Symmetric(g0,g6,g-2)
    c: DistanceX(g0,g0) = 50
    c: DistanceY(g6) = 320.166  'length'
    c: DistanceX(g2,g1) = 160
    c: Coincident(g1,g2)
    c: Coincident(g3,g4)
    c: Symmetric(g5,g3,g-2)
    c: Coincident(g8,g7)
    c: Perpendicular(g5,g7)
    c: Equal(g8,g7)
    c: Distance(g7) = 4
    c: PointOnObject(g7,g5)
    c: Coincident(g6,g5)
    c: Distance(g7,g5) = 1
    c: Distance(g2) = 92.376  'inner_r'
    c: Angle(g1) = -2.61799
    c: Coincident(g9,g8)
    c: Coincident(g9,g2)
    c: Symmetric(g8,g7,g2)
    c: Parallel(g5,g6)
    c: Coincident(g1,g-1)
    c: Angle(g5,g9) = 2.49062  'connection_angle'
FEATURE [PartDesign::FeaturePython] BaseBend043  # WARN: FeaturePython — macro-defined, semantics opaque (R4)
  BendSide = 0
  BendSketch = -> Sketch167
  MidPlane = false
  Reverse = false
  Suppressed = false
  length = 100
  radius = 2
  thickness = 2
FEATURE [PartDesign::FeaturePython] Bend025  # WARN: FeaturePython — macro-defined, semantics opaque (R4)
  AutoMiter = false
  BaseFeature = -> BaseBend043
  BendType = 0
  LengthList = [100]
  LengthSpec = 0
  ReliefFactor = 0.7
  Suppressed = false
  UseReliefFactor = false
  angle = 90
  baseObject = -> BaseBend043 [Edge21,Edge7]
  bendAList = [90]
  extend1 = 0
  extend2 = 0
  gap1 = 0
  gap2 = 0
  invert = false
  kfactor = 0.5
  length = 100
  maxExtendDist = 5
  minGap = 0.1
  minReliefGap = 1
  miterangle1 = 18.649
  miterangle2 = 18.649
  offset = 0
  radius = 2
  reliefType = 0
  reliefd = 1
  reliefw = 0.8
  sketchflip = false
  sketchinvert = false
  unfold = false
  expr: miterangle1 = 90 deg - Sketch167.Constraints.connection_angle / 2
  expr: miterangle2 = miterangle1
  expr: radius = BaseBend043.radius
FEATURE [Sketcher::SketchObject] Sketch170
  AttachmentSupport = -> [YZ_Plane078]
  FullyConstrained = false
  MapMode = 5
  Placement = pos=(0,0,0) rot=(0.57735,0.57735,0.57735;2.0944rad)
  expr: Constraints[10] = <<basement_amplifier_sketch>>.Constraints.length
  sketch-geometry (11):
    g0: LineSegment StartX=320.166 StartY=-15 StartZ=0 EndX=320.166 EndY=2 EndZ=0
    g1: LineSegment StartX=320.166 StartY=2 StartZ=0 EndX=0 EndY=2 EndZ=0
    g2: LineSegment StartX=0 StartY=2 StartZ=0 EndX=0 EndY=-60 EndZ=0
    g3: LineSegment StartX=0 StartY=-60 StartZ=0 EndX=125.378 EndY=-25.2665 EndZ=0
    g4: LineSegment StartX=133.266 StartY=-24 StartZ=0 EndX=320.166 EndY=-15 EndZ=0
    g5: ArcOfCircle CenterX=135 CenterY=-60 CenterZ=0 NormalX=0 NormalY=0 NormalZ=1 AngleXU=0 Radius=36.0417 StartAngle=1.61891 EndAngle=1.84105
    g6: GeomPoint X=129.251 Y=-24.1933 Z=0
    g7: LineSegment StartX=-219.815 StartY=310.193 StartZ=0 EndX=564.966 EndY=310.193 EndZ=0
    g8: LineSegment StartX=564.966 StartY=310.193 StartZ=0 EndX=564.966 EndY=-309.063 EndZ=0
    g9: LineSegment StartX=564.966 StartY=-309.063 StartZ=0 EndX=-219.815 EndY=-309.063 EndZ=0
    g10: LineSegment StartX=-219.815 StartY=-309.063 StartZ=0 EndX=-219.815 EndY=310.193 EndZ=0
  constraints (27):
    c: Vertical(g0)
    c: Coincident(g0,g1)
    c: Horizontal(g1)
    c: PointOnObject(g2,g-2)
    c: Coincident(g4,g0)
    c: Coincident(g2,g1)
    c: Vertical(g2)
    c: DistanceY(g-1,g1) = 2
    c: DistanceY(g0,g1) = 17
    c: DistanceY(g2) = -60
    c: DistanceX(g1,g1) = 320.166
    c: PointOnObject(g6,g4)
    c: PointOnObject(g6,g3)
    c: Tangent(g4,g5) = 1.5708
    c: Tangent(g3,g5) = 1.5708
    c: Coincident(g7,g8)
    c: Coincident(g8,g9)
    c: Coincident(g9,g10)
    c: Coincident(g10,g7)
    c: Horizontal(g7)
    c: Horizontal(g9)
    c: Vertical(g8)
    c: Vertical(g10)
    c: DistanceY(g4) = -24
    c: DistanceX(g5) = 135
    c: Coincident(g3,g2)
    c: Horizontal(g5,g2)
FEATURE [Sketcher::SketchObject] Sketch171  label="basement2_sketch"
  AttachmentSupport = -> [XY_Plane080]
  FullyConstrained = true
  MapMode = 5
  sketch-geometry (10):
    g0: LineSegment StartX=-80 StartY=46.188 StartZ=0 EndX=2.84e-14 EndY=-4.97e-14 EndZ=0
    g1: LineSegment StartX=2.84e-14 StartY=-4.97e-14 StartZ=0 EndX=80 EndY=46.188 EndZ=0
    g2: LineSegment StartX=80 StartY=46.188 StartZ=0 EndX=79.7011 EndY=48.0916 EndZ=0
    g3: LineSegment StartX=79.7011 StartY=48.0916 StartZ=0 EndX=42.5 EndY=285 EndZ=0
    g4: LineSegment StartX=42.5 StartY=285 StartZ=0 EndX=-42.5 EndY=285 EndZ=0
    g5: LineSegment StartX=-42.5 StartY=285 StartZ=0 EndX=-79.7011 EndY=48.0916 EndZ=0
    g6: LineSegment StartX=-79.7011 StartY=48.0916 StartZ=0 EndX=-80 EndY=46.188 EndZ=0
    g7: LineSegment StartX=80 StartY=46.188 StartZ=0 EndX=81.4991 EndY=44.9774 EndZ=0
    g8: LineSegment StartX=81.4991 StartY=44.9774 StartZ=0 EndX=84.6406 EndY=48.8672 EndZ=0
    g9: LineSegment StartX=84.6406 StartY=48.8672 StartZ=0 EndX=79.7011 EndY=48.0916 EndZ=0
  constraints (26):
    c: Coincident(g0,g-1)
    c: Coincident(g0,g1)
    c: Coincident(g1,g2)
    c: Coincident(g2,g3)
    c: Coincident(g3,g4)
    c: Coincident(g4,g5)
    c: Coincident(g5,g6)
    c: Coincident(g6,g0)
    c: Symmetric(g0,g1,g-2)
    c: Symmetric(g4,g3,g-2)
    c: Symmetric(g5,g2,g-2)
    c: Parallel(g2,g3)
    c: Angle(g1) = 0.523599
    c: Coincident(g7,g1)
    c: Symmetric(g7,g2,g1)
    c: DistanceX(g4,g4) = 85
    c: DistanceY(g3) = 285
    c: Coincident(g8,g7)
    c: Coincident(g9,g8)
    c: Coincident(g9,g2)
    c: Perpendicular(g2,g9)
    c: Perpendicular(g7,g8)
    c: Distance(g9) = 5
    c: Distance(g1) = 92.376  'inner_r'
    c: Angle(g7,g2) = 2.40591  'connection_angle'
    c: DistanceX(g0,g1) = 160
FEATURE [PartDesign::FeaturePython] BaseBend044  # WARN: FeaturePython — macro-defined, semantics opaque (R4)
  BendSide = 0
  BendSketch = -> Sketch171
  MidPlane = false
  Reverse = false
  Suppressed = false
  length = 100
  radius = 2
  thickness = 2
FEATURE [PartDesign::FeaturePython] Bend026  # WARN: FeaturePython — macro-defined, semantics opaque (R4)
  AutoMiter = false
  BaseFeature = -> BaseBend044
  BendType = 0
  LengthList = [30]
  LengthSpec = 0
  ReliefFactor = 0.7
  Suppressed = false
  UseReliefFactor = false
  angle = 90
  baseObject = -> BaseBend044 [Edge19,Edge13]
  bendAList = [90]
  extend1 = 0
  extend2 = 0
  gap1 = 0
  gap2 = 0
  invert = false
  kfactor = 0.5
  length = 30
  maxExtendDist = 5
  minGap = 0.1
  minReliefGap = 1
  miterangle1 = 21.0759
  miterangle2 = 21.0759
  offset = 0
  radius = 2
  reliefType = 0
  reliefd = 1
  reliefw = 0.8
  sketchflip = false
  sketchinvert = false
  unfold = false
  expr: miterangle1 = 90 deg - <<basement2_sketch>>.Constraints.connection_angle / 2
  expr: miterangle2 = miterangle1
  expr: radius = BaseBend044.radius
FEATURE [PartDesign::Plane] DatumPlane005
  AttachmentOffset = pos=(0,0,0) rot=(0,-1,0;1.5708rad)
  AttachmentSupport = -> [Sketch167]
  Length = 647.453
  MapMode = 7
  Placement = pos=(-79.5375,48.492,0) rot=(0.501242,-0.611865,-0.611865;2.21231rad)
  ResizeMode = 0
  Width = 88.0953
FEATURE [PartDesign::Line] DatumLine003
  AttacherType = Attacher::AttachEngineLine
  AttachmentOffset = pos=(0,0,0) rot=(0,1,0;1.5708rad)
  AttachmentSupport = -> [Sketch170]
  Length = 20
  MapMode = 24
  Placement = pos=(0,0,-60) rot=(0,1,0;1.5708rad)
  ResizeMode = 0
FEATURE [PartDesign::Line] DatumLine004
  AttacherType = Attacher::AttachEngineLine
  AttachmentOffset = pos=(0,0,0) rot=(0,1,0;1.5708rad)
  AttachmentSupport = -> [Sketch170]
  Length = 20
  MapMode = 24
  Placement = pos=(0,133.266,-24) rot=(0.58639,0.558832,0.58639;2.1224rad)
  ResizeMode = 0
FEATURE [Sketcher::SketchObject] Sketch173
  AttachmentOffset = pos=(0,0,4) rot=(0,0,1;0rad)
  AttachmentSupport = -> [DatumPlane005]
  ExternalGeometry = -> [Sketch167]
  FullyConstrained = false
  MapMode = 5
  Placement = pos=(-83.4592,49.2793,0) rot=(-0.501242,0.611865,0.611865;4.07087rad)
  sketch-geometry (9):
    g0: LineSegment StartX=49.4595 StartY=-30.4174 StartZ=0 EndX=49.4595 EndY=2 EndZ=0
    g1: LineSegment StartX=-86.4657 StartY=-24 StartZ=0 EndX=-277.094 EndY=-15 EndZ=0
    g2: LineSegment StartX=-277.094 StartY=-15 StartZ=0 EndX=-277.094 EndY=2 EndZ=0
    g3: LineSegment StartX=-277.094 StartY=2 StartZ=0 EndX=49.4595 EndY=2 EndZ=0
    g4: LineSegment StartX=-568.045 StartY=-343.581 StartZ=0 EndX=236.236 EndY=-343.581 EndZ=0
    g5: LineSegment StartX=236.236 StartY=-343.581 StartZ=0 EndX=236.236 EndY=220.397 EndZ=0
    g6: LineSegment StartX=236.236 StartY=220.397 StartZ=0 EndX=-568.045 EndY=220.397 EndZ=0
    g7: LineSegment StartX=-568.045 StartY=220.397 StartZ=0 EndX=-568.045 EndY=-343.581 EndZ=0
    g8: LineSegment StartX=-86.4657 StartY=-24 StartZ=0 EndX=49.4595 EndY=-30.4174 EndZ=0
  constraints (22):
    c: Coincident(g2,g1)
    c: Vertical(g2)
    c: Coincident(g3,g2)
    c: Horizontal(g3)
    c: Coincident(g3,g0)
    c: DistanceY(g0) = 2
    c: DistanceY(g1) = -15
    c: Coincident(g4,g5)
    c: Coincident(g5,g6)
    c: Coincident(g6,g7)
    c: Coincident(g7,g4)
    c: Horizontal(g4)
    c: Horizontal(g6)
    c: Vertical(g5)
    c: Vertical(g7)
    c: PointOnObject(g-5,g2)
    c: Coincident(g1,g-4) = -1.5708
    c: Coincident(g8,g1)
    c: Coincident(g8,g0)
    c: Parallel(g8,g1)
    c: Vertical(g0)
    c: PointOnObject(g-3,g0)
FEATURE [PartDesign::Pocket] Pocket104
  BaseFeature = -> Bend025
  Direction = (0.98044,-0.19682,0)
  Length = 2
  Length2 = 5
  Profile = -> Sketch173
  ReferenceAxis = -> Sketch173 [N_Axis]
  Suppressed = false
  Type = 0
FEATURE [PartDesign::Fillet] Fillet011
  Base = -> Pocket104 [Edge57,Edge56]
  BaseFeature = -> Pocket104
  Radius = 10
  SupportTransform = false
  Suppressed = false
  UseAllEdges = false
FEATURE [Sketcher::SketchObject] Sketch174
  AttachmentSupport = -> [XY_Plane080]
  ExternalGeometry = -> [Sketch171]
  FullyConstrained = true
  MapMode = 5
  sketch-geometry (7):
    g0: LineSegment StartX=44.3713 StartY=273.083 StartZ=0 EndX=49.3108 EndY=273.858 EndZ=0
    g1: LineSegment StartX=49.3108 StartY=273.858 StartZ=0 EndX=4.93947 EndY=556.429 EndZ=0
    g2: LineSegment StartX=4.93947 StartY=556.429 StartZ=0 EndX=0 EndY=555.654 EndZ=0
    g3: LineSegment StartX=42.5 StartY=285 StartZ=0 EndX=38.2239 EndY=285 EndZ=0
    g4: LineSegment StartX=43.1633 StartY=280.776 StartZ=0 EndX=44.3713 EndY=273.083 EndZ=0
    g5: LineSegment StartX=0 StartY=555.654 StartZ=0 EndX=42.5 EndY=285 EndZ=0
    g6: ArcOfCircle CenterX=38.2239 CenterY=280 CenterZ=0 NormalX=0 NormalY=0 NormalZ=1 AngleXU=0 Radius=5 StartAngle=0.155755 EndAngle=1.5708
  constraints (20):
    c: Coincident(g0,g1)
    c: Coincident(g1,g2)
    c: Coincident(g2,g5)
    c: Coincident(g4,g0)
    c: Parallel(g0,g2)
    c: Perpendicular(g1,g0)
    c: PointOnObject(g0,g-3)
    c: PointOnObject(g2,g-3)
    c: DistanceY(g0) = 273.083
    c: PointOnObject(g2,g-2)
    c: Distance(g0) = 5
    c: Coincident(g3,g-3)
    c: Horizontal(g3)
    c: Parallel(g1,g4)
    c: Parallel(g1,g5)
    c: Coincident(g5,g3)
    c: Tangent(g6,g4) = 1.5708
    c: Tangent(g6,g3) = -1.5708
    c: Radius(g6) = 5
    c: Distance(g3,g0) = 12.0632
FEATURE [PartDesign::Pocket] Pocket105
  BaseFeature = -> Bend026
  Direction = (0,0,-1)
  Length = 5
  Length2 = 5
  Midplane = true
  Profile = -> Sketch174
  ReferenceAxis = -> Sketch174 [N_Axis]
  Suppressed = false
  Type = 1
FEATURE [PartDesign::Mirrored] Mirrored011
  BaseFeature = -> Pocket105
  MirrorPlane = -> Sketch174 [V_Axis]
  Originals = -> [Pocket105]
  Refine = true
  Suppressed = false
FEATURE [PartDesign::SubShapeBinder] Binder117
  BindCopyOnChange = 0
  BindMode = 0
  ClaimChildren = false
  Context = -> Body107 [Binder117.]
  Fuse = false
  MakeFace = true
  OffsetFill = false
  OffsetIntersection = false
  OffsetJoinType = 0
  OffsetOpenResult = false
  PartialLoad = false
  Relative = true
  Support = -> [Body007[Binder066.Binder064.]]
  _Version = 2
FEATURE [PartDesign::SubShapeBinder] Binder118
  BindCopyOnChange = 0
  BindMode = 0
  ClaimChildren = false
  Context = -> Body105 [Binder118.]
  Fuse = false
  MakeFace = true
  OffsetFill = false
  OffsetIntersection = false
  OffsetJoinType = 0
  OffsetOpenResult = false
  PartialLoad = false
  Relative = true
  Support = -> [Body006[Binder069.]]
  _Version = 2
FEATURE [PartDesign::SubShapeBinder] Binder119
  BindCopyOnChange = 0
  BindMode = 0
  ClaimChildren = false
  Context = -> Body105 [Binder119.]
  Fuse = false
  MakeFace = true
  OffsetFill = false
  OffsetIntersection = false
  OffsetJoinType = 0
  OffsetOpenResult = false
  PartialLoad = false
  Relative = true
  Support = -> [Body006[Pocket061.Sketch112.]]
  _Version = 2
FEATURE [PartDesign::Pocket] Pocket108
  BaseFeature = -> Fillet011
  Direction = (0,0,-1)
  Length = 5
  Length2 = 5
  Midplane = true
  Profile = -> Binder119
  Suppressed = false
  Type = 1
FEATURE [Sketcher::SketchObject] Sketch175
  AttachmentSupport = -> [XY_Plane078]
  ExternalGeometry = -> [Sketch167]
  FullyConstrained = true
  MapMode = 5
  sketch-geometry (6):
    g0: Circle CenterX=43.3161 CenterY=155 CenterZ=0 NormalX=0 NormalY=0 NormalZ=1 AngleXU=0 Radius=2.55
    g1: Circle CenterX=-43.3161 CenterY=155 CenterZ=0 NormalX=0 NormalY=0 NormalZ=1 AngleXU=0 Radius=2.55
    g2: Circle CenterX=63.3907 CenterY=55 CenterZ=0 NormalX=0 NormalY=0 NormalZ=1 AngleXU=0 Radius=2.55
    g3: Circle CenterX=-63.3907 CenterY=55 CenterZ=0 NormalX=0 NormalY=0 NormalZ=1 AngleXU=0 Radius=2.55
    g4: LineSegment StartX=45.8162 StartY=155.502 StartZ=0 EndX=57.5815 EndY=157.864 EndZ=0
    g5: LineSegment StartX=65.8909 StartY=55.5019 StartZ=0 EndX=77.6561 EndY=57.8637 EndZ=0
  constraints (18):
    c: Distance(g0,g-3) = 12
    c: Diameter(g0) = 5.1
    c: Equal(g1,g0)
    c: Symmetric(g1,g0,g-2)
    c: DistanceY(g0) = 155
    c: Symmetric(g2,g3,g-2)
    c: Equal(g2,g3)
    c: Equal(g3,g0)
    c: PointOnObject(g4,g0)
    c: PointOnObject(g4,g-3)
    c: PointOnObject(g5,g2)
    c: PointOnObject(g5,g-3)
    c: Perpendicular(g5,g-3)
    c: PointOnObject(g2,g5)
    c: Equal(g5,g4)
    c: PointOnObject(g0,g4)
    c: Perpendicular(g-3,g4)
    c: DistanceY(g2) = 55
FEATURE [PartDesign::Pocket] Pocket109
  BaseFeature = -> Pocket108
  Direction = (0,0,-1)
  Length = 5
  Length2 = 5
  Midplane = true
  Profile = -> Sketch175
  ReferenceAxis = -> Sketch175 [N_Axis]
  Suppressed = false
  Type = 1
FEATURE [PartDesign::Mirrored] Mirrored010
  BaseFeature = -> Pocket109
  MirrorPlane = -> YZ_Plane078
  Originals = -> [Pocket104,Fillet011]
  Suppressed = false
FEATURE [PartDesign::FeatureAdditivePython] PDW_Common_Add  # link proxy (typed FeaturePython)
  BaseFeature = -> Mirrored010
  Body = Body105
  ClaimChildren = false
  EditPlacementAdjustments = false
  Enabled = 0
  LinkedObject = -> Mirrored010
  MeshTolerance = 0.1
  PatternBase = -> Pocket109
  PatternBaseOffset = 0
  PatternBaseScale = 1
  PatternBaseScaleXYZ = (1,1,1)
  PatternOffsetCut = false
  PatternOffsetIntersection = false
  PatternOffsetJoin = 0
  PatternOffsetMode = 0
  PatternOffsetSelfIntersection = false
  PatternOperation = 3
  PatternOperationDefault = Common
  PatternScaleCut = false
  PatternShapeOffset = 0
  PatternShapeScale = 1
  PatternShapeScaleXYZ = (1,1,1)
  PatternTool = -> Mirrored010
  PatternToolOffset = 0
  PatternToolScale = 1
  PatternToolScaleXYZ = (1,1,1)
  RefineMesh = true
  ShapeManagement = 0
  ShowMeshProps = false
  ShowOffsetProps = false
  ShowScaleProps = false
  ShowWarnings = true
  Suppressed = false
  TipBase = -> Mirrored010
  TipBaseOffset = 0
  TipBaseScale = 1
  TipBaseScaleXYZ = (1,1,1)
  TipOffsetCut = false
  TipOffsetIntersection = false
  TipOffsetJoin = 0
  TipOffsetMode = 0
  TipOffsetSelfIntersection = false
  TipOperation = 4
  TipOperationDefault = Common
  TipScaleCut = false
  TipShapeOffset = 0
  TipShapeScale = 1
  TipShapeScaleXYZ = (1,1,1)
  TipTool = -> Mirrored010
  TipToolOffset = 0
  TipToolScale = 1
  TipToolScaleXYZ = (1,1,1)
  Type = Additive
  UsePatternBaseAddSubShape = false
  UsePatternToolAddSubShape = true
  UseTipBaseAddSubShape = false
  UseTipToolAddSubShape = true
  Version = 0.2023.08.13
FEATURE [PartDesign::PolarPattern] PolarPattern006
  Angle = 360
  Axis = -> Z_Axis078
  BaseFeature = -> PDW_Common_Add
  Mode = 0
  Occurrences = 3
  Offset = 120
  Originals = -> [PDW_Common_Add]
  Refine = true
  Suppressed = false
FEATURE [PartDesign::Pocket] Pocket107
  BaseFeature = -> PolarPattern006
  Direction = (0,0,-1)
  Length = 5
  Length2 = 5
  Midplane = true
  Profile = -> Binder118
  Suppressed = false
  Type = 1
FEATURE [Sketcher::SketchObject] Sketch176
  AttachmentSupport = -> [XY_Plane080]
  ExternalGeometry = -> [Sketch171]
  FullyConstrained = true
  MapMode = 5
  sketch-geometry (5):
    g0: LineSegment StartX=42.5 StartY=285 StartZ=0 EndX=42.5 EndY=362 EndZ=0
    g1: ArcOfCircle CenterX=27.5 CenterY=362 CenterZ=0 NormalX=0 NormalY=0 NormalZ=1 AngleXU=0 Radius=15 StartAngle=-8.4623e-11 EndAngle=1.5708
    g2: LineSegment StartX=0 StartY=285 StartZ=0 EndX=42.5 EndY=285 EndZ=0
    g3: LineSegment StartX=0 StartY=377 StartZ=0 EndX=27.5 EndY=377 EndZ=0
    g4: LineSegment StartX=0 StartY=285 StartZ=0 EndX=0 EndY=377 EndZ=0
  constraints (13):
    c: Coincident(g2,g0)
    c: Vertical(g0)
    c: Coincident(g2,g-3)
    c: Tangent(g0,g1) = -1.5708
    c: PointOnObject(g2,g-2)
    c: PointOnObject(g2,g-3)
    c: PointOnObject(g3,g-2)
    c: Horizontal(g3)
    c: Tangent(g3,g1) = 1.5708
    c: Coincident(g4,g2)
    c: Coincident(g4,g3)
    c: DistanceY(g4,g4) = 92
    c: Radius(g1) = 15
FEATURE [PartDesign::SubShapeBinder] Binder120
  BindCopyOnChange = 0
  BindMode = 0
  ClaimChildren = false
  Context = -> Body107 [Binder120.]
  Fuse = false
  MakeFace = true
  OffsetFill = false
  OffsetIntersection = false
  OffsetJoinType = 0
  OffsetOpenResult = false
  PartialLoad = false
  Relative = true
  Support = -> [Body007[Binder063.]]
  _Version = 2
FEATURE [PartDesign::Pocket] Pocket110
  BaseFeature = -> Mirrored011
  Direction = (0,0,-1)
  Length = 5
  Length2 = 5
  Profile = -> Binder120
  Suppressed = false
  Type = 1
FEATURE [PartDesign::SubShapeBinder] Binder121
  BindCopyOnChange = 0
  BindMode = 0
  ClaimChildren = false
  Context = -> Body107 [Binder121.]
  Fuse = false
  MakeFace = true
  OffsetFill = false
  OffsetIntersection = false
  OffsetJoinType = 0
  OffsetOpenResult = false
  PartialLoad = false
  Relative = true
  Support = -> [Body007[Pocket057.Sketch110.,Pocket058.Sketch111.]]
  _Version = 2
FEATURE [PartDesign::Pocket] Pocket111
  BaseFeature = -> Pocket110
  Direction = (0,0,-1)
  Length = 5
  Length2 = 5
  Midplane = true
  Profile = -> Binder121
  Suppressed = false
  Type = 1
FEATURE [PartDesign::Mirrored] Mirrored012
  BaseFeature = -> Pocket111
  MirrorPlane = -> YZ_Plane080
  Originals = -> [Pocket110]
  Suppressed = false
FEATURE [PartDesign::FeatureAdditivePython] PDW_Add  # link proxy (typed FeaturePython)
  BaseFeature = -> Mirrored012
  Body = Body107
  ClaimChildren = false
  EditPlacementAdjustments = false
  Enabled = 1
  LinkedObject = -> Mirrored011
  MeshTolerance = 0.1
  PatternBase = -> Mirrored012
  PatternBaseOffset = 0
  PatternBaseScale = 1
  PatternBaseScaleXYZ = (1,1,1)
  PatternOffsetCut = false
  PatternOffsetIntersection = false
  PatternOffsetJoin = 0
  PatternOffsetMode = 0
  PatternOffsetSelfIntersection = false
  PatternOperation = 0
  PatternOperationDefault = None
  PatternScaleCut = false
  PatternShapeOffset = 0
  PatternShapeScale = 1
  PatternShapeScaleXYZ = (1,1,1)
  PatternTool = -> Mirrored011
  PatternToolOffset = 0
  PatternToolScale = 1
  PatternToolScaleXYZ = (1,1,1)
  RefineMesh = true
  ShapeManagement = 0
  ShowMeshProps = false
  ShowOffsetProps = false
  ShowScaleProps = false
  ShowWarnings = true
  Suppressed = false
  TipBase = -> Mirrored012
  TipBaseOffset = 0
  TipBaseScale = 1
  TipBaseScaleXYZ = (1,1,1)
  TipOffsetCut = false
  TipOffsetIntersection = false
  TipOffsetJoin = 0
  TipOffsetMode = 0
  TipOffsetSelfIntersection = false
  TipOperation = 0
  TipOperationDefault = Fuse
  TipScaleCut = false
  TipShapeOffset = 0
  TipShapeScale = 1
  TipShapeScaleXYZ = (1,1,1)
  TipTool = -> Mirrored011
  TipToolOffset = 0
  TipToolScale = 1
  TipToolScaleXYZ = (1,1,1)
  Type = Additive
  UsePatternBaseAddSubShape = false
  UsePatternToolAddSubShape = true
  UseTipBaseAddSubShape = false
  UseTipToolAddSubShape = true
  Version = 0.2023.08.13
FEATURE [PartDesign::FeatureAdditivePython] PDW_Common_Add001  # link proxy (typed FeaturePython)
  BaseFeature = -> PDW_Add
  Body = Body107
  ClaimChildren = false
  EditPlacementAdjustments = false
  Enabled = 1
  LinkedObject = -> Mirrored012
  MeshTolerance = 0.1
  PatternBase = -> PDW_Add
  PatternBaseOffset = 0
  PatternBaseScale = 1
  PatternBaseScaleXYZ = (1,1,1)
  PatternOffsetCut = false
  PatternOffsetIntersection = false
  PatternOffsetJoin = 0
  PatternOffsetMode = 0
  PatternOffsetSelfIntersection = false
  PatternOperation = 3
  PatternOperationDefault = Common
  PatternScaleCut = false
  PatternShapeOffset = 0
  PatternShapeScale = 1
  PatternShapeScaleXYZ = (1,1,1)
  PatternTool = -> Mirrored012
  PatternToolOffset = 0
  PatternToolScale = 1
  PatternToolScaleXYZ = (1,1,1)
  RefineMesh = true
  ShapeManagement = 0
  ShowMeshProps = false
  ShowOffsetProps = false
  ShowScaleProps = false
  ShowWarnings = true
  Suppressed = false
  TipBase = -> PDW_Add
  TipBaseOffset = 0
  TipBaseScale = 1
  TipBaseScaleXYZ = (1,1,1)
  TipOffsetCut = false
  TipOffsetIntersection = false
  TipOffsetJoin = 0
  TipOffsetMode = 0
  TipOffsetSelfIntersection = false
  TipOperation = 2
  TipOperationDefault = Common
  TipScaleCut = false
  TipShapeOffset = 0
  TipShapeScale = 1
  TipShapeScaleXYZ = (1,1,1)
  TipTool = -> Mirrored012
  TipToolOffset = 0
  TipToolScale = 1
  TipToolScaleXYZ = (1,1,1)
  Type = Additive
  UsePatternBaseAddSubShape = false
  UsePatternToolAddSubShape = true
  UseTipBaseAddSubShape = false
  UseTipToolAddSubShape = true
  Version = 0.2023.08.13
FEATURE [PartDesign::PolarPattern] PolarPattern007
  Angle = 360
  Axis = -> Z_Axis080
  BaseFeature = -> PDW_Common_Add001
  Mode = 0
  Occurrences = 3
  Offset = 120
  Originals = -> [PDW_Common_Add001]
  Refine = true
  Suppressed = false
FEATURE [PartDesign::Pocket] Pocket106
  BaseFeature = -> PolarPattern007
  Direction = (0,0,-1)
  Length = 5
  Length2 = 5
  Midplane = true
  Profile = -> Binder117
  Suppressed = false
  Type = 1
FEATURE [Spreadsheet::Sheet] Spreadsheet002  label="material_stainlessSteel"
  cells = A1='Radius / Thickness ; B1='K-factor (ANSI); A2=1; B2=0.38; A3=3; B3=0.43; A4=99; B4=0.5
FEATURE [App::DocumentObjectGroup] Group001  label="tables"
  Group = -> [Spreadsheet,Spreadsheet002]
FEATURE [Sketcher::SketchObject] Sketch177
  AttachmentSupport = -> [XY_Plane081]
  FullyConstrained = true
  MapMode = 5
  sketch-geometry (9):
    g0: LineSegment StartX=250 StartY=97 StartZ=0 EndX=269.053 EndY=108 EndZ=0
    g1: LineSegment StartX=250 StartY=97 StartZ=0 EndX=292.808 EndY=-94.3391 EndZ=0
    g2: LineSegment StartX=292.808 StartY=-94.3391 StartZ=0 EndX=329.057 EndY=-111.242 EndZ=0
    g3: ArcOfCircle CenterX=268.986 CenterY=-83.2305 CenterZ=0 NormalX=0 NormalY=0 NormalZ=1 AngleXU=0 Radius=80 StartAngle=5.84685 EndAngle=6.61803
    g4: ArcOfCircle CenterX=-564.456 CenterY=-373.226 CenterZ=0 NormalX=0 NormalY=0 NormalZ=1 AngleXU=0 Radius=962.453 StartAngle=0.334847 EndAngle=0.523599
    g5: Circle CenterX=295.561 CenterY=-15.8447 CenterZ=0 NormalX=0 NormalY=0 NormalZ=1 AngleXU=0 Radius=1.7
    g6: Circle CenterX=267.045 CenterY=85.8678 CenterZ=0 NormalX=0 NormalY=0 NormalZ=1 AngleXU=0 Radius=1.7
    g7: ArcOfCircle CenterX=330.58 CenterY=-111.997 CenterZ=0 NormalX=0 NormalY=0 NormalZ=1 AngleXU=0 Radius=1.7 StartAngle=5.8707 EndAngle=8.9646
    g8: LineSegment StartX=332.138 StartY=-112.679 StartZ=0 EndX=341.49 EndY=-117.04 EndZ=0
  constraints (29):
    c: Coincident(g1,g0)
    c: Coincident(g2,g1)
    c: Angle(g0) = 0.523599
    c: DistanceX(g0) = 250
    c: DistanceY(g0) = 97
    c: Distance(g0) = 22
    c: DistanceX(g8) = 341.49
    c: DistanceY(g8) = -117.04
    c: Coincident(g3,g8)
    c: Coincident(g4,g0)
    c: Tangent(g3,g4) = -1.5708
    c: Perpendicular(g3,g2)
    c: Perpendicular(g4,g0)
    c: Radius(g3) = 80
    c: Angle(g2) = -0.436332
    c: Equal(g6,g5)
    c: Diameter(g6) = 3.4
    c: DistanceX(g5) = 295.561
    c: DistanceY(g5) = -15.8447
    c: DistanceX(g6) = 267.045
    c: DistanceY(g6) = 85.8678
    c: Equal(g7,g5)
    c: DistanceX(g7) = 330.58
    c: DistanceY(g7) = -111.997
    c: Coincident(g2,g7)
    c: Coincident(g8,g7)
    c: Parallel(g8,g2)
    c: PointOnObject(g7,g2)
    c: Distance(g3,g1) = 53.7148
FEATURE [PartDesign::Pad] Pad019
  Direction = (0,0,1)
  Length = 3
  Length2 = 10
  Profile = -> Sketch177
  ReferenceAxis = -> Sketch177 [N_Axis]
  Suppressed = false
  Type = 0
FEATURE [PartDesign::Body] Body108
  Group = -> [Sketch177,Pad019]
  Origin = -> Origin081
  Tip = -> Pad019
FEATURE [App::Part] Part018
  Group = -> [Body103,Body104,Body108]
  Origin = -> Origin077
  Placement = pos=(0,0,150) rot=(0,0,1;0rad)
FEATURE [App::Part] Part017
  Group = -> [Body100,Body101,Link008,Part018]
  Origin = -> Origin076
  Placement = pos=(0,0,312) rot=(0,0,1;0rad)
FEATURE [App::Part] Part015  label="door3_2"
  Group = -> [Link007,Part016,Part017,Compound046,Part__Mirroring025,Part014]
  Origin = -> Origin069
FEATURE [PartDesign::Body] Body109  label="dummy_body"
  Origin = -> Origin082
FEATURE [Sketcher::SketchObject] Sketch178
  AttachmentSupport = -> [XY_Plane011]
  FullyConstrained = true
  MapMode = 5
  sketch-geometry (4):
    g0: Circle CenterX=29 CenterY=-145.633 CenterZ=0 NormalX=0 NormalY=0 NormalZ=1 AngleXU=0 Radius=4.25
    g1: LineSegment StartX=0 StartY=0 StartZ=0 EndX=84.8108 EndY=-48.9655 EndZ=0
    g2: Circle CenterX=140.622 CenterY=47.7016 CenterZ=0 NormalX=0 NormalY=0 NormalZ=1 AngleXU=0 Radius=4.25
    g3: LineSegment StartX=140.622 StartY=47.7016 StartZ=0 EndX=29 EndY=-145.633 EndZ=0
  constraints (10):
    c: Diameter(g0) = 8.5
    c: DistanceX(g0) = 29
    c: DistanceY(g0) = -145.633
    c: Coincident(g1,g-1)
    c: Angle(g1) = -0.523599
    c: Symmetric(g2,g0,g1)
    c: Equal(g2,g0)
    c: Coincident(g3,g2)
    c: Coincident(g3,g0)
    c: PointOnObject(g1,g3)
FEATURE [Part::Extrusion] Extrude016  label="Populate droppers placements with dropper_base_extrude"
  Base = -> Populate006
  Dir = (0,0,1)
  DirMode = 2
  FaceMakerClass = Part::FaceMakerBullseye
  LengthFwd = 10
  LengthRev = 0
  Placement = pos=(0,181.372,0) rot=(0,0,1;0rad)
  Solid = false
  Symmetric = false
  expr: .Placement.Base.y = <<Properties>>.plane_middle
FEATURE [App::Link] Link010  label="top_top001"
  LinkedObject = -> Body110
  expr: LinkedObject = <<dropper_fix_top>>._self
FEATURE [App::Link] Link011  label="top_bottom001"
  LinkedObject = -> Body004
FEATURE [App::Link] Link012  label="cap_outer_material_0.30ansi001"
  LinkedObject = -> Body002
FEATURE [App::Link] Link013  label="cap_inner2_material_0.30ansi001"
  LinkedObject = -> Body016
FEATURE [App::Link] Link014  label="top_connector_material_0.30ansi001"
  LinkedObject = -> Body017
FEATURE [App::Link] Link015  label="cap_inner1_material_0.30ansi001"
  LinkedObject = -> Body003
FEATURE [App::Link] Link016  label="part1_material_0.30ansi001"
  LinkedObject = -> Body
FEATURE [App::Link] Link017  label="part2_material_0.30ansi001"
  LinkedObject = -> Body001
FEATURE [App::Link] Link018  label="bot_hor_amplifier_material_0.30ansi001"
  LinkedObject = -> Body068
FEATURE [App::Link] Link019  label="star_material_0.30ansi001"
  LinkedObject = -> Body018
FEATURE [App::Link] Link020  label="plexiglass_outer_material_0.30ansi001"
  LinkedObject = -> Body072
FEATURE [App::Link] Link021  label="pillar_bottom_material_0.30ansi001"
  LinkedObject = -> Body011
FEATURE [App::Link] Link022  label="pillar_material_0.30ansi001"
  LinkedObject = -> Body010
FEATURE [App::Link] Link023  label="pillar_top_element_material_0.30ansi001"
  LinkedObject = -> Body012
FEATURE [App::Link] Link024  label="led_holder_material_0.30ansi001"
  LinkedObject = -> Body015
FEATURE [App::Link] Link025  label="top_dec_corner_material_0.30ansi001"
  LinkedObject = -> Body014
FEATURE [App::Link] Link026  label="dec_corner_material_0.30ansi001"
  LinkedObject = -> Body013
FEATURE [App::Link] Link027  label="basement_amplifier_material_0.30ansi002"
  LinkedObject = -> Body105
FEATURE [App::Link] Link028  label="basement_proxy001"
  LinkedObject = -> Body008
FEATURE [App::Link] Link029  label="basement_plywood001"
  LinkedObject = -> Body006
FEATURE [App::Link] Link030  label="basement2_amplifier_material_stainlessSteel001"
  LinkedObject = -> Body107
FEATURE [App::Link] Link031  label="basement2_plywood001"
  LinkedObject = -> Body007
FEATURE [App::Link] Link032  label="basement2_proxy001"
  LinkedObject = -> Body009
FEATURE [App::Link] Link033  label="sink_material_0.30ansi001"
  LinkedObject = -> Body020
FEATURE [App::Link] Link034  label="Body110"
  LinkedObject = -> Body021
FEATURE [App::Link] Link035  label="hat003"
  LinkedObject = -> Body076
FEATURE [App::Link] Link036  label="hat004"
  LinkedObject = -> Body075
FEATURE [App::Link] Link037  label="hat_plexiglass_material_0.30ansi001"
  LinkedObject = -> Body078
FEATURE [Part::Extrusion] Extrude017  label="populate dropper_fix_extrude"
  Base = -> Populate004
  Dir = (0,0,1)
  DirMode = 2
  FaceMakerClass = Part::FaceMakerBullseye
  LengthFwd = 10
  LengthRev = 0
  Placement = pos=(0,181.372,1.5) rot=(0,0,1;0rad)
  Solid = false
  Symmetric = false
  expr: .Placement.Base.y = <<Properties>>.plane_middle
FEATURE [Part::Compound] Compound048  label="top_bottom_cut1"
  Links = -> [Extrude016,Extrude017]
FEATURE [Part::Extrusion] Extrude018  label="Populate droppers placements with dropper_feed_extrude"
  Base = -> Populate005
  Dir = (0,0,1)
  DirMode = 2
  FaceMakerClass = Part::FaceMakerBullseye
  LengthFwd = 10
  LengthRev = 0
  Placement = pos=(0,181.372,0) rot=(0,0,1;0rad)
  Solid = false
  Symmetric = false
  expr: .Placement.Base.y = <<Properties>>.plane_middle
FEATURE [Part::Compound] Compound049  label="top_top_cut1"
  Links = -> [Extrude017,Extrude018]
FEATURE [Part::FeaturePython] Connect  label="top_bottom_cut1_refined"  # WARN: FeaturePython — macro-defined, semantics opaque (R4)
  Objects = -> [Compound048]
  Refine = true
  Tolerance = 0
FEATURE [Part::FeaturePython] Connect001  label="top_top_cut1_refined"  # WARN: FeaturePython — macro-defined, semantics opaque (R4)
  Objects = -> [Compound049]
  Refine = true
  Tolerance = 0
FEATURE [PartDesign::FeatureBase] BaseFeature
  BaseFeature = -> Hole003
  Suppressed = false
  expr: BaseFeature = <<Hole003>>._self
FEATURE [PartDesign::FeatureSubtractivePython] PDW_Sub  # link proxy (typed FeaturePython)
  BaseFeature = -> BaseFeature
  Body = Body110
  ClaimChildren = true
  EditPlacementAdjustments = false
  Enabled = 1
  LinkedObject = -> Connect001
  MeshTolerance = 0.1
  PatternBase = -> Connect001
  PatternBaseOffset = 0
  PatternBaseScale = 1
  PatternBaseScaleXYZ = (1,1,1)
  PatternOffsetCut = false
  PatternOffsetIntersection = false
  PatternOffsetJoin = 0
  PatternOffsetMode = 0
  PatternOffsetSelfIntersection = false
  PatternOperation = 0
  PatternOperationDefault = None
  PatternScaleCut = false
  PatternShapeOffset = 0
  PatternShapeScale = 1
  PatternShapeScaleXYZ = (1,1,1)
  PatternToolOffset = 0
  PatternToolScale = 1
  PatternToolScaleXYZ = (1,1,1)
  RefineMesh = true
  ShapeManagement = 0
  ShowMeshProps = false
  ShowOffsetProps = false
  ShowScaleProps = false
  ShowWarnings = true
  Suppressed = false
  TipBase = -> BaseFeature
  TipBaseOffset = 0
  TipBaseScale = 1
  TipBaseScaleXYZ = (1,1,1)
  TipOffsetCut = false
  TipOffsetIntersection = false
  TipOffsetJoin = 0
  TipOffsetMode = 0
  TipOffsetSelfIntersection = false
  TipOperation = 1
  TipOperationDefault = Cut
  TipScaleCut = false
  TipShapeOffset = 0
  TipShapeScale = 1
  TipShapeScaleXYZ = (1,1,1)
  TipTool = -> Connect001
  TipToolOffset = 0
  TipToolScale = 1
  TipToolScaleXYZ = (1,1,1)
  Type = Subtractive
  UsePatternBaseAddSubShape = false
  UsePatternToolAddSubShape = false
  UseTipBaseAddSubShape = false
  UseTipToolAddSubShape = false
  Version = 0.2023.08.13
FEATURE [Part::Extrusion] Extrude019  label="hole_3.4mm_extrude"
  Base = -> Circle
  Dir = (0,0,1)
  DirMode = 2
  FaceMakerClass = Part::FaceMakerBullseye
  LengthFwd = 10
  LengthRev = 10
  Solid = true
  Symmetric = false
FEATURE [Part::FeaturePython] LinearArray014  label="pillar_bottom_hor_fix_holes"  # WARN: FeaturePython — macro-defined, semantics opaque (R4)
  Alignment = 0
  CellStart = A1
  Count = 2
  Dir = (1,0,0)
  DirIsDriven = true
  DistributionLaw = 0
  DrivenProperty = 1
  EndInclusive = true
  ExposePlacement = false
  GeneratorMode = 0
  MarkerShape = 1
  MarkerSize = 0
  NumElements = 2
  OrientMode = 1
  Placement = pos=(-40,-12,0) rot=(0,0,1;0rad)
  Point = (0,0,0)
  PointIsDriven = true
  Reverse = false
  SpanEnd = 80
  SpanStart = 0
  Step = 80
  Type = lattice2LinearArray.LinearArray
  VSGVersion = 1
  Values = 0.0 | 80.0
  ValuesSource = 2
  isLattice = 1
  expr: .Placement.Base.x = -SpanEnd / 2
FEATURE [Part::Part2DObjectPython] Circle002  label="hole_5.5mm"  # Draft 2D object (typed FeaturePython)
  Area = 0
  FirstAngle = 0
  LastAngle = 0
  MakeFace = false
  Placement = pos=(0,0,0) rot=(0,0,1;1e-06rad)
  Radius = 2.75
FEATURE [Part::Extrusion] Extrude021  label="hole_5.5mm_extrude"
  Base = -> Circle002
  Dir = (2.13e-14,-2.56e-13,1)
  DirMode = 2
  FaceMakerClass = Part::FaceMakerBullseye
  LengthFwd = 30
  LengthRev = 0
  Solid = true
  Symmetric = false
FEATURE [Part::FeaturePython] Populate024  label="Populate pillar_bottom_hor_fix_holes with hole_5.5mm_extrude"  # WARN: FeaturePython — macro-defined, semantics opaque (R4)
  Copying = 0
  ExposePlacement = false
  MarkerShape = 1
  MarkerSize = 0
  NumElements = 0
  Object = -> Extrude021
  OutputCompounding = 1
  PlacementsTo = -> LinearArray014
  Referencing = 0
  Type = lattice2PopulateCopies.LatticePopulateCopies
  isLattice = 0
FEATURE [Part::FeaturePython] Mirror006  label="pillar_bottom_mirror_hor_fix_holes"  # WARN: FeaturePython — macro-defined, semantics opaque (R4)
  ExposePlacement = false
  FlipX = false
  FlipY = true
  FlipZ = false
  MarkerShape = 1
  MarkerSize = 0
  NumElements = 2
  Object = -> LinearArray014
  ObjectTraversal = 0
  Type = lattice2Mirror.LatticeMirror
  isLattice = 1
FEATURE [Part::FeaturePython] Placment017  # WARN: FeaturePython — macro-defined, semantics opaque (R4)
  AttacherType = Attacher::AttachEngine3D
  ExposePlacement = true
  MarkerShape = 1
  MarkerSize = 20
  NumElements = 1
  Placement = pos=(-18.3,329.5,0) rot=(0,0,-1;1.5708rad)
  Type = lattice2AttachablePlacement.AttachablePlacement
  isLattice = 1
  expr: Placement = <<pillar_placement>>.AttachmentOffset * <<pillar_bottom_placement>>.AttachmentOffset
FEATURE [Part::FeaturePython] Placment018  label="basement2_placement"  # WARN: FeaturePython — macro-defined, semantics opaque (R4)
  AttacherType = Attacher::AttachEngine3D
  AttachmentOffset = pos=(0,0,-88) rot=(0,0,1;0rad)
  ExposePlacement = true
  MarkerShape = 1
  MarkerSize = 20
  NumElements = 1
  Type = lattice2AttachablePlacement.AttachablePlacement
  isLattice = 1
FEATURE [Part::FeaturePython] Placment  label="pillar_placement"  # WARN: FeaturePython — macro-defined, semantics opaque (R4)
  AttacherType = Attacher::AttachEngine3D
  AttachmentOffset = pos=(0,384,0) rot=(0,0,1;3.14159rad)
  AttachmentSupport = -> [Placment018]
  ExposePlacement = true
  MapMode = 2
  MarkerShape = 1
  MarkerSize = 10
  NumElements = 1
  Placement = pos=(0,384,0) rot=(0,0,1;3.14159rad)
  Type = lattice2AttachablePlacement.AttachablePlacement
  isLattice = 1
FEATURE [Part::FeaturePython] Placment001  label="pillar_top_part_placement"  # WARN: FeaturePython — macro-defined, semantics opaque (R4)
  AttacherType = Attacher::AttachEngine3D
  AttachmentSupport = -> [Placment]
  ExposePlacement = true
  MapMode = 2
  MarkerShape = 1
  MarkerSize = 10
  NumElements = 1
  Placement = pos=(0,384,0) rot=(0,0,1;3.14159rad)
  Type = lattice2AttachablePlacement.AttachablePlacement
  isLattice = 1
FEATURE [Part::FeaturePython] Placment003  label="pillar_bottom_placement"  # WARN: FeaturePython — macro-defined, semantics opaque (R4)
  AttacherType = Attacher::AttachEngine3D
  AttachmentOffset = pos=(18.3,54.5,0) rot=(0,0,1;1.5708rad)
  AttachmentSupport = -> [Placment]
  ExposePlacement = true
  MapMode = 2
  MarkerShape = 1
  MarkerSize = 50
  NumElements = 1
  Placement = pos=(-18.3,329.5,0) rot=(0,0,1;4.71239rad)
  Type = lattice2AttachablePlacement.AttachablePlacement
  isLattice = 1
FEATURE [Part::FeaturePython] Mirror007  label="Mirror007 of Placment017"  # WARN: FeaturePython — macro-defined, semantics opaque (R4)
  ExposePlacement = false
  FlipX = true
  FlipY = false
  FlipZ = false
  MarkerShape = 1
  MarkerSize = 10
  NumElements = 1
  Object = -> Placment017
  ObjectTraversal = 0
  Type = lattice2Mirror.LatticeMirror
  isLattice = 1
FEATURE [Part::FeaturePython] Populate025  label="Populate Mirror007 of Placment017 with pillar_bottom_mirror_hor_fix_holes"  # WARN: FeaturePython — macro-defined, semantics opaque (R4)
  Copying = 0
  ExposePlacement = false
  MarkerShape = 1
  MarkerSize = 0
  NumElements = 2
  Object = -> Mirror006
  OutputCompounding = 0
  PlacementsTo = -> Mirror007
  Referencing = 0
  Type = lattice2PopulateCopies.LatticePopulateCopies
  isLattice = 1
FEATURE [Part::FeaturePython] Populate026  label="Populate Placment017 with pillar_bottom_hor_fix_holes"  # WARN: FeaturePython — macro-defined, semantics opaque (R4)
  Copying = 0
  ExposePlacement = false
  MarkerShape = 1
  MarkerSize = 0
  NumElements = 2
  Object = -> LinearArray014
  OutputCompounding = 0
  PlacementsTo = -> Placment017
  Referencing = 0
  Type = lattice2PopulateCopies.LatticePopulateCopies
  isLattice = 1
FEATURE [Part::FeaturePython] Join004  # WARN: FeaturePython — macro-defined, semantics opaque (R4)
  ExposePlacement = false
  Interleave = false
  Links = -> [Populate025,Populate026]
  MarkerShape = 1
  MarkerSize = 0
  NumElements = 4
  Type = lattice2JoinArrays.JoinArrays
  isLattice = 1
FEATURE [Part::FeaturePython] PolarArray002  # WARN: FeaturePython — macro-defined, semantics opaque (R4)
  Alignment = 0
  AttacherType = Attacher::AttachEngine3D
  CellStart = A1
  Count = 3
  DistributionLaw = 0
  EndInclusive = false
  ExposePlacement = false
  FlipX = false
  FlipZ = false
  GeneratorMode = 0
  MarkerShape = 1
  MarkerSize = 0
  NumElements = 3
  OrientMode = 2
  Radius = 25
  Reverse = false
  SpanEnd = 360
  SpanStart = 0
  Step = 120
  Type = lattice2PolarArray2.PolarArray
  UseArcRadius = false
  UseArcRange = 0
  VSGVersion = 1
  Values = 0.0 | 120.0 | 240.0
  ValuesSource = 2
  isLattice = 1
FEATURE [Part::FeaturePython] Populate027  label="Populate PolarArray002 with Join004"  # WARN: FeaturePython — macro-defined, semantics opaque (R4)
  Copying = 0
  ExposePlacement = false
  MarkerShape = 1
  MarkerSize = 0
  NumElements = 12
  Object = -> Join004
  OutputCompounding = 0
  PlacementsTo = -> PolarArray002
  Referencing = 1
  Type = lattice2PopulateCopies.LatticePopulateCopies
  isLattice = 1
FEATURE [Part::FeaturePython] Populate028  label="Populate Populate PolarArray002 with Join004 with hole_5.5mm_extrude"  # WARN: FeaturePython — macro-defined, semantics opaque (R4)
  Copying = 0
  ExposePlacement = false
  MarkerShape = 1
  MarkerSize = 0
  NumElements = 0
  Object = -> Extrude021
  OutputCompounding = 1
  PlacementsTo = -> Populate027
  Referencing = 0
  Type = lattice2PopulateCopies.LatticePopulateCopies
  isLattice = 0
FEATURE [Sketcher::SketchObject] Sketch180
  AttachmentSupport = -> [YZ_Plane085]
  FullyConstrained = true
  MapMode = 5
  Placement = pos=(0,0,0) rot=(0.57735,0.57735,0.57735;2.0944rad)
  sketch-geometry (4):
    g0: ArcOfCircle CenterX=-4 CenterY=4 CenterZ=0 NormalX=0 NormalY=0 NormalZ=1 AngleXU=0 Radius=4 StartAngle=4.71239 EndAngle=6.28319
    g1: ArcOfCircle CenterX=-4 CenterY=4 CenterZ=0 NormalX=0 NormalY=0 NormalZ=1 AngleXU=0 Radius=2 StartAngle=4.71239 EndAngle=6.28319
    g2: LineSegment StartX=-4 StartY=0 StartZ=0 EndX=-4 EndY=2 EndZ=0
    g3: LineSegment StartX=-2 StartY=4 StartZ=0 EndX=0 EndY=4 EndZ=0
  constraints (13):
    c: PointOnObject(g0,g-1)
    c: PointOnObject(g0,g-2)
    c: Coincident(g1,g0)
    c: Coincident(g2,g0)
    c: Coincident(g2,g1)
    c: Coincident(g3,g1)
    c: Coincident(g3,g0)
    c: Perpendicular(g1,g3)
    c: Perpendicular(g1,g2)
    c: Vertical(g2)
    c: Horizontal(g3)
    c: Radius(g1) = 2  'r'
    c: Distance(g2) = 2  'thickness'
FEATURE [PartDesign::Pad] Pad020
  Direction = (1,-2e-16,3e-16)
  Length = 101
  Length2 = 10
  Midplane = true
  Placement = pos=(0,0,0) rot=(0.57735,0.57735,0.57735;2.0944rad)
  Profile = -> Sketch180
  ReferenceAxis = -> Sketch180 [N_Axis]
  Suppressed = false
  Type = 0
FEATURE [Sketcher::SketchObject] Sketch181
  AttachmentSupport = -> [XY_Plane085]
  FullyConstrained = true
  MapMode = 5
  expr: Constraints[2] = Pad020.Length
  sketch-geometry (4):
    g0: LineSegment StartX=-50.5 StartY=-4 StartZ=0 EndX=50.5 EndY=-4 EndZ=0
    g1: LineSegment StartX=29.5 StartY=-25 StartZ=0 EndX=-29.5 EndY=-25 EndZ=0
    g2: ArcOfCircle CenterX=29.5 CenterY=-4 CenterZ=0 NormalX=0 NormalY=0 NormalZ=1 AngleXU=0 Radius=21 StartAngle=4.71239 EndAngle=6.28319
    g3: ArcOfCircle CenterX=-29.5 CenterY=-4 CenterZ=0 NormalX=0 NormalY=0 NormalZ=1 AngleXU=0 Radius=21 StartAngle=3.14159 EndAngle=4.71239
  constraints (11):
    c: Horizontal(g1)
    c: DistanceY(g0) = -4
    c: DistanceX(g0,g0) = 101
    c: DistanceY(g1,g-1) = 25
    c: PointOnObject(g2,g0)
    c: Coincident(g2,g0)
    c: PointOnObject(g3,g0)
    c: Coincident(g3,g0)
    c: Tangent(g3,g1) = 1.5708
    c: Tangent(g2,g1) = 1.5708
    c: Symmetric(g0,g0,g-2)
FEATURE [Sketcher::SketchObject] Sketch182
  AttachmentSupport = -> [XZ_Plane085]
  FullyConstrained = true
  MapMode = 5
  Placement = pos=(0,0,0) rot=(1,0,0;1.5708rad)
  expr: Constraints[17] = <<pillar2_base_sketch>>.Constraints.length + 3 mm
  expr: Constraints[8] = Pad020.Length
  sketch-geometry (13):
    g0: LineSegment StartX=-50.5 StartY=4 StartZ=0 EndX=-50.5 EndY=110 EndZ=0
    g1: LineSegment StartX=-35.5 StartY=110 StartZ=0 EndX=-35.5 EndY=66.1722 EndZ=0
    g2: LineSegment StartX=-18.1011 StartY=38.947 StartZ=0 EndX=47.6002 EndY=8.53754 EndZ=0
    g3: ArcOfCircle CenterX=45.5 CenterY=4 CenterZ=0 NormalX=0 NormalY=0 NormalZ=1 AngleXU=0 Radius=5 StartAngle=2.92426e-11 EndAngle=1.13731
    g4: ArcOfCircle CenterX=-5.5 CenterY=66.1722 CenterZ=0 NormalX=0 NormalY=0 NormalZ=1 AngleXU=0 Radius=30 StartAngle=3.14159 EndAngle=4.27891
    g5: GeomPoint X=-35.5 Y=47 Z=0
    g6: GeomPoint X=-35.5 Y=110 Z=0
    g7: GeomPoint X=-52.5 Y=110 Z=0
    g8: LineSegment StartX=50.5 StartY=4 StartZ=0 EndX=-48.5 EndY=4 EndZ=0
    g9: LineSegment StartX=-48.5 StartY=4 StartZ=0 EndX=-50.5 EndY=4 EndZ=0
    g10: LineSegment StartX=-50.5 StartY=110 StartZ=0 EndX=-48.5 EndY=110 EndZ=0
    g11: LineSegment StartX=-48.5 StartY=110 StartZ=0 EndX=-35.5 EndY=110 EndZ=0
    g12: LineSegment StartX=-48.5 StartY=4 StartZ=0 EndX=-48.5 EndY=110 EndZ=0
  constraints (32):
    c: Vertical(g0)
    c: Coincident(g0,g10)
    c: Vertical(g1)
    c: Coincident(g9,g0)
    c: Coincident(g3,g8)
    c: Tangent(g3,g2) = 1.5708
    c: DistanceY(g8) = 4
    c: Symmetric(g0,g8,g-2)
    c: DistanceX(g9,g8) = 101
    c: DistanceY(g0) = 110  'total_height'
    c: PointOnObject(g5,g1)
    c: PointOnObject(g5,g2)
    c: Tangent(g1,g4) = -1.5708
    c: Tangent(g2,g4) = -1.5708
    c: Radius(g4) = 30
    c: Radius(g3) = 5
    c: DistanceX(g7,g0) = 2
    c: DistanceX(g7,g6) = 17
    c: Coincident(g8,g9)
    c: PointOnObject(g3,g8)
    c: Coincident(g10,g11)
    c: Horizontal(g10)
    c: Horizontal(g11)
    c: PointOnObject(g7,g10)
    c: Coincident(g12,g8)
    c: Coincident(g12,g11)
    c: Vertical(g12)
    c: DistanceX(g0,g11) = 2
    c: Horizontal(g9)
    c: DistanceY(g5) = 47
    c: Coincident(g1,g11)
    c: Coincident(g1,g6)
FEATURE [PartDesign::Pad] Pad021
  BaseFeature = -> Pad020
  Direction = (0,0,1)
  Length = 2
  Length2 = 10
  Placement = pos=(0,0,0) rot=(0.57735,0.57735,0.57735;2.0944rad)
  Profile = -> Sketch181
  ReferenceAxis = -> Sketch181 [N_Axis]
  Suppressed = false
  Type = 0
FEATURE [PartDesign::Pad] Pad022
  BaseFeature = -> Pad021
  Direction = (0,-1,-2e-16)
  Length = 2
  Length2 = 10
  Placement = pos=(0,0,0) rot=(0.57735,0.57735,0.57735;2.0944rad)
  Profile = -> Sketch182
  ReferenceAxis = -> Sketch182 [N_Axis]
  Suppressed = false
  Type = 0
FEATURE [Sketcher::SketchObject] Sketch183
  AttachmentOffset = pos=(-52.5,2,0) rot=(0,0,1;0rad)
  AttachmentSupport = -> [XY_Plane085]
  FullyConstrained = true
  MapMode = 5
  Placement = pos=(-52.5,2,0) rot=(0,0,1;0rad)
  expr: .AttachmentOffset.Base.x = -Pad020.Length / 2 - 2 mm
  expr: Constraints[16] = <<pillar2_base_sketch>>.Constraints.width / 2 - 1 mm
  sketch-geometry (9):
    g0: ArcOfCircle CenterX=-5.92e-14 CenterY=4.503e-13 CenterZ=0 NormalX=0 NormalY=0 NormalZ=1 AngleXU=0 Radius=2 StartAngle=3.14159 EndAngle=4.71239
    g1: ArcOfCircle CenterX=-5.92e-14 CenterY=4.503e-13 CenterZ=0 NormalX=0 NormalY=0 NormalZ=1 AngleXU=0 Radius=4 StartAngle=3.14159 EndAngle=4.71239
    g2: LineSegment StartX=-2 StartY=-4.469e-13 StartZ=0 EndX=-2 EndY=15.3 EndZ=0
    g3: LineSegment StartX=-2 StartY=15.3 StartZ=0 EndX=-4 EndY=15.3 EndZ=0
    g4: LineSegment StartX=-4 StartY=15.3 StartZ=0 EndX=-4 EndY=0 EndZ=0
    g5: LineSegment StartX=0 StartY=-4 StartZ=0 EndX=0 EndY=-2 EndZ=0
    g6: LineSegment StartX=0 StartY=-4 StartZ=0 EndX=2 EndY=-4 EndZ=0
    g7: LineSegment StartX=2 StartY=-4 StartZ=0 EndX=2 EndY=-2 EndZ=0
    g8: LineSegment StartX=2 StartY=-2 StartZ=0 EndX=0 EndY=-2 EndZ=0
  constraints (25):
    c: Coincident(g0,g-1)
    c: PointOnObject(g0,g-2)
    c: PointOnObject(g0,g-1)
    c: Coincident(g1,g0)
    c: PointOnObject(g1,g-2)
    c: PointOnObject(g1,g-1)
    c: Tangent(g0,g2) = 1.5708
    c: Coincident(g2,g3)
    c: Horizontal(g3)
    c: Coincident(g3,g4)
    c: Coincident(g4,g1)
    c: Vertical(g4)
    c: Coincident(g5,g1)
    c: Coincident(g5,g0)
    c: Radius(g0) = 2
    c: DistanceY(g5,g5) = 2
    c: DistanceY(g0,g2) = 17.3
    c: Coincident(g6,g7)
    c: Coincident(g7,g8)
    c: Horizontal(g6)
    c: Horizontal(g8)
    c: Vertical(g7)
    c: Coincident(g6,g1)
    c: Coincident(g0,g8)
    c: DistanceX(g6,g6) = 2
FEATURE [Sketcher::SketchObject] Sketch184
  AttachmentSupport = -> [YZ_Plane085]
  ExternalGeometry = -> [Sketch183]
  FullyConstrained = true
  MapMode = 5
  Placement = pos=(0,0,0) rot=(0.57735,0.57735,0.57735;2.0944rad)
  expr: Constraints[12] = Sketch182.Constraints.total_height
  sketch-geometry (9):
    g0: ArcOfCircle CenterX=15.3 CenterY=2 CenterZ=0 NormalX=0 NormalY=0 NormalZ=1 AngleXU=0 Radius=2 StartAngle=4.71239 EndAngle=6.28319
    g1: LineSegment StartX=17.3 StartY=2 StartZ=0 EndX=17.3 EndY=1.47e-14 EndZ=0
    g2: LineSegment StartX=17.3 StartY=1.47e-14 StartZ=0 EndX=15.3 EndY=1.95e-14 EndZ=0
    g3: LineSegment StartX=17.3 StartY=108 StartZ=0 EndX=17.3 EndY=110 EndZ=0
    g4: LineSegment StartX=17.3 StartY=110 StartZ=0 EndX=15.3 EndY=110 EndZ=0
    g5: ArcOfCircle CenterX=15.3 CenterY=108 CenterZ=0 NormalX=0 NormalY=0 NormalZ=1 AngleXU=0 Radius=2 StartAngle=-5.3e-15 EndAngle=1.5708
    g6: ArcOfCircle CenterX=4 CenterY=2 CenterZ=0 NormalX=0 NormalY=0 NormalZ=1 AngleXU=0 Radius=2 StartAngle=3.14159 EndAngle=4.71239
    g7: LineSegment StartX=2 StartY=2 StartZ=0 EndX=2 EndY=1.11e-14 EndZ=0
    g8: LineSegment StartX=2 StartY=1.11e-14 StartZ=0 EndX=4 EndY=3.55e-14 EndZ=0
  constraints (22):
    c: Coincident(g1,g2)
    c: Vertical(g3)
    c: Coincident(g3,g4)
    c: Horizontal(g4)
    c: Tangent(g5,g4) = -1.5708
    c: Tangent(g5,g3) = -1.5708
    c: Vertical(g1)
    c: Tangent(g0,g1) = 1.5708
    c: Tangent(g2,g0) = 1.5708
    c: Vertical(g3,g1)
    c: Equal(g5,g0)
    c: Radius(g5) = 2
    c: DistanceY(g3) = 110
    c: Coincident(g7,g8)
    c: Vertical(g7)
    c: Tangent(g6,g7) = -1.5708
    c: Tangent(g8,g6) = -1.5708
    c: Equal(g6,g0)
    c: Coincident(g1,g-3)
    c: Coincident(g7,g-3)
    c: PointOnObject(g6,g-3)
    c: PointOnObject(g0,g-1)
FEATURE [Sketcher::SketchObject] Sketch185
  AttachmentOffset = pos=(-52.5,2,0) rot=(0,0,1;0rad)
  AttachmentSupport = -> [XY_Plane085]
  FullyConstrained = true
  MapMode = 5
  Placement = pos=(-52.5,2,0) rot=(0,0,1;0rad)
  expr: AttachmentOffset = <<Sketch183>>.AttachmentOffset
  sketch-geometry (6):
    g0: ArcOfCircle CenterX=-1.4879e-12 CenterY=3.7497e-12 CenterZ=0 NormalX=0 NormalY=0 NormalZ=1 AngleXU=0 Radius=4 StartAngle=3.14159 EndAngle=4.71239
    g1: ArcOfCircle CenterX=-1.4879e-12 CenterY=3.7497e-12 CenterZ=0 NormalX=0 NormalY=0 NormalZ=1 AngleXU=0 Radius=2 StartAngle=3.14159 EndAngle=4.71239
    g2: LineSegment StartX=-4 StartY=-4.94e-14 StartZ=0 EndX=-2 EndY=-2.158e-13 EndZ=0
    g3: LineSegment StartX=1.0947e-12 StartY=-4 StartZ=0 EndX=2 EndY=-4 EndZ=0
    g4: LineSegment StartX=2 StartY=-4 StartZ=0 EndX=2 EndY=-2 EndZ=0
    g5: LineSegment StartX=2 StartY=-2 StartZ=0 EndX=1.583e-13 EndY=-2 EndZ=0
  constraints (17):
    c: Coincident(g0,g-1)
    c: PointOnObject(g0,g-2)
    c: PointOnObject(g0,g-1)
    c: Coincident(g1,g0)
    c: PointOnObject(g1,g-2)
    c: PointOnObject(g1,g-1)
    c: Coincident(g2,g0)
    c: Coincident(g2,g1)
    c: Radius(g1) = 2
    c: Radius(g0) = 4
    c: Tangent(g0,g3) = -1.5708
    c: Coincident(g3,g4)
    c: Vertical(g4)
    c: Coincident(g4,g5)
    c: Coincident(g5,g1)
    c: Horizontal(g5)
    c: DistanceX(g5,g5) = 2
FEATURE [Sketcher::SketchObject] Sketch186  label="pillar2_base_sketch"
  AttachmentSupport = -> [XY_Plane086]
  FullyConstrained = true
  MapMode = 5
  expr: .Constraints.length = <<pillar2_Properties>>.outer_length
  sketch-geometry (5):
    g0: LineSegment StartX=-18.3 StartY=14 StartZ=0 EndX=-18.3 EndY=0 EndZ=0
    g1: LineSegment StartX=-18.3 StartY=0 StartZ=0 EndX=18.3 EndY=0 EndZ=0
    g2: LineSegment StartX=18.3 StartY=0 StartZ=0 EndX=18.3 EndY=14 EndZ=0
    g3: LineSegment StartX=18.3 StartY=14 StartZ=0 EndX=-18.3 EndY=14 EndZ=0
    g4: GeomPoint X=0 Y=7 Z=0
  constraints (13):
    c: Coincident(g0,g1)
    c: Coincident(g1,g2)
    c: Coincident(g2,g3)
    c: Coincident(g3,g0)
    c: Horizontal(g1)
    c: Horizontal(g3)
    c: Vertical(g0)
    c: Vertical(g2)
    c: Symmetric(g1,g0,g4)
    c: PointOnObject(g4,g-2)
    c: PointOnObject(g1,g-1)
    c: DistanceX(g1,g1) = 36.6  'width'
    c: DistanceY(g2,g2) = 14  'length'
FEATURE [PartDesign::FeaturePython] BaseBend045  # WARN: FeaturePython — macro-defined, semantics opaque (R4)
  BendSide = 1
  BendSketch = -> Sketch186
  MidPlane = false
  Reverse = false
  Suppressed = false
  length = 1596
  radius = 2
  thickness = 2
FEATURE [Part::FeaturePython] Placment019  # WARN: FeaturePython — macro-defined, semantics opaque (R4)
  AttacherType = Attacher::AttachEngine3D
  ExposePlacement = true
  MarkerShape = 1
  MarkerSize = 10
  NumElements = 1
  Placement = pos=(16.3,8,0) rot=(0.707107,0,0.707107;3.14159rad)
  Type = lattice2AttachablePlacement.AttachablePlacement
  isLattice = 1
  expr: .Placement.Base.x = <<pillar2_base_sketch>>.Constraints.width / 2 - 2 mm
FEATURE [Part::FeaturePython] LinearArray015  # WARN: FeaturePython — macro-defined, semantics opaque (R4)
  Alignment = 0
  CellStart = A1
  Count = 4
  Dir = (0,0,1)
  DirIsDriven = true
  DistributionLaw = 0
  DrivenProperty = 1
  EndInclusive = true
  ExposePlacement = false
  GeneratorMode = 0
  MarkerShape = 1
  MarkerSize = 0
  NumElements = 4
  OrientMode = 0
  Point = (0,0,0)
  PointIsDriven = true
  Reverse = false
  SpanEnd = 100
  SpanStart = 10
  Step = 30
  Type = lattice2LinearArray.LinearArray
  VSGVersion = 1
  Values = 10.0 | 40.0 | 70.0 | 100.0
  ValuesSource = 2
  isLattice = 1
FEATURE [Part::Part2DObjectPython] Join006  # Draft 2D object (typed FeaturePython)
  AttacherType = Attacher::AttachEngine3D
  ExposePlacement = false
  Interleave = false
  Links = -> [Placment019]
  MarkerShape = 1
  MarkerSize = 2
  NumElements = 1
  Type = lattice2JoinArrays.JoinArrays
  isLattice = 1
FEATURE [Part::FeaturePython] Mirror008  label="Mirror008 of Placment019"  # WARN: FeaturePython — macro-defined, semantics opaque (R4)
  ExposePlacement = false
  FlipX = true
  FlipY = false
  FlipZ = false
  MarkerShape = 1
  MarkerSize = 5
  NumElements = 1
  Object = -> Join006
  ObjectTraversal = 0
  Type = lattice2Mirror.LatticeMirror
  isLattice = 1
FEATURE [Part::FeaturePython] Join005  # WARN: FeaturePython — macro-defined, semantics opaque (R4)
  ExposePlacement = false
  Interleave = false
  Links = -> [Mirror008,Join006]
  MarkerShape = 1
  MarkerSize = 0
  NumElements = 2
  Type = lattice2JoinArrays.JoinArrays
  isLattice = 1
FEATURE [Part::FeaturePython] Populate029  label="Populate LinearArray015 with Join005"  # WARN: FeaturePython — macro-defined, semantics opaque (R4)
  Copying = 0
  ExposePlacement = false
  MarkerShape = 1
  MarkerSize = 0
  NumElements = 8
  Object = -> Join005
  OutputCompounding = 0
  PlacementsTo = -> LinearArray015
  Referencing = 0
  Type = lattice2PopulateCopies.LatticePopulateCopies
  isLattice = 1
FEATURE [Part::FeaturePython] Populate030  label="Populate Populate LinearArray015 with Join005 with hole_3.4mm_extrude"  # WARN: FeaturePython — macro-defined, semantics opaque (R4)
  Copying = 0
  ExposePlacement = false
  MarkerShape = 1
  MarkerSize = 0
  NumElements = 0
  Object = -> Extrude019
  OutputCompounding = 1
  PlacementsTo = -> Populate029
  Referencing = 0
  Type = lattice2PopulateCopies.LatticePopulateCopies
  isLattice = 0
FEATURE [Part::Compound] Compound053
  Links = -> [Populate030]
  Placement = pos=(-54.5,18.3,0) rot=(0,0,-1;1.5708rad)
FEATURE [Part::Compound] Compound054  label="pillar2_bottom_cut1"
  Links = -> [Compound053,Populate024]
FEATURE [Spreadsheet::Sheet] Spreadsheet003  label="pillar2_Properties"
  cells = B2(thickness)==2 mm; C2(default_bend_r)==2 mm; D2(outer_width)==36.6 mm; E2(outer_length)==14 mm
FEATURE [Spreadsheet::Sheet] Spreadsheet004  label="pillar2_bottom_Properties"
  cells = B2(thickness)==2 mm; C2(default_bend_r)==2 mm; D2(outer_width)==101 mm; E2(outer_length)==10 mm
FEATURE [Sketcher::SketchObject] Sketch187
  AttachmentOffset = pos=(0,1598,0) rot=(0,0,1;0rad)
  AttachmentSupport = -> [XZ_Plane086]
  FullyConstrained = true
  MapMode = 5
  Placement = pos=(0,3.548e-13,1598) rot=(1,0,0;1.5708rad)
  expr: .AttachmentOffset.Base.y = BaseBend045.length + Sketch188.Constraints.length
  expr: Constraints[11] = <<pillar2_Properties>>.outer_width - 4 mm * 2 + (<<pillar2_Properties>>.outer_length - 4 mm) * 2 + 9.42 mm
  sketch-geometry (5):
    g0: LineSegment StartX=-29.01 StartY=88 StartZ=0 EndX=-29.01 EndY=0 EndZ=0
    g1: LineSegment StartX=-29.01 StartY=0 StartZ=0 EndX=29.01 EndY=0 EndZ=0
    g2: LineSegment StartX=29.01 StartY=0 StartZ=0 EndX=29.01 EndY=88 EndZ=0
    g3: LineSegment StartX=29.01 StartY=88 StartZ=0 EndX=-29.01 EndY=88 EndZ=0
    g4: GeomPoint X=0 Y=44 Z=0
  constraints (13):
    c: Coincident(g0,g1)
    c: Coincident(g1,g2)
    c: Coincident(g2,g3)
    c: Coincident(g3,g0)
    c: Horizontal(g1)
    c: Horizontal(g3)
    c: Vertical(g0)
    c: Vertical(g2)
    c: Symmetric(g1,g0,g4)
    c: PointOnObject(g4,g-2)
    c: PointOnObject(g1,g-1)
    c: DistanceX(g1,g1) = 58.02
    c: DistanceY(g2,g2) = 88
FEATURE [Sketcher::SketchObject] Sketch188
  AttachmentOffset = pos=(0,1596,0) rot=(0,0,1;0rad)
  AttachmentSupport = -> [XZ_Plane086]
  FullyConstrained = true
  MapMode = 5
  Placement = pos=(0,3.544e-13,1596) rot=(1,0,0;1.5708rad)
  expr: .AttachmentOffset.Base.y = BaseBend045.length
  expr: Constraints[11] = <<pillar2_Properties>>.outer_width - (<<pillar2_Properties>>.thickness + <<pillar2_Properties>>.default_bend_r) * 2
  sketch-geometry (7):
    g0: LineSegment StartX=-14.3 StartY=2 StartZ=0 EndX=-14.3 EndY=-4e-16 EndZ=0
    g1: LineSegment StartX=-14.3 StartY=-4e-16 StartZ=0 EndX=14.3 EndY=-4e-16 EndZ=0
    g2: LineSegment StartX=14.3 StartY=-4e-16 StartZ=0 EndX=14.3 EndY=2 EndZ=0
    g3: LineSegment StartX=14.3 StartY=2 StartZ=0 EndX=-14.3 EndY=2 EndZ=0
    g4: GeomPoint X=-2.547e-12 Y=1 Z=0
    g5: ArcOfCircle CenterX=14.3 CenterY=1 CenterZ=0 NormalX=0 NormalY=0 NormalZ=1 AngleXU=0 Radius=1 StartAngle=1.5708 EndAngle=4.71239
    g6: ArcOfCircle CenterX=-14.3 CenterY=1 CenterZ=0 NormalX=0 NormalY=0 NormalZ=1 AngleXU=0 Radius=1 StartAngle=4.71239 EndAngle=7.85398
  constraints (19):
    c: Coincident(g0,g1)
    c: Coincident(g1,g2)
    c: Coincident(g2,g3)
    c: Coincident(g3,g0)
    c: Horizontal(g1)
    c: Horizontal(g3)
    c: Vertical(g0)
    c: Vertical(g2)
    c: Symmetric(g1,g0,g4)
    c: PointOnObject(g4,g-2)
    c: PointOnObject(g1,g-1)
    c: DistanceX(g1,g1) = 28.6
    c: DistanceY(g2) = 2  'length'
    c: PointOnObject(g5,g2)
    c: Coincident(g5,g1)
    c: Coincident(g5,g3)
    c: PointOnObject(g6,g0)
    c: Coincident(g6,g1)
    c: Coincident(g6,g3)
FEATURE [PartDesign::Pad] Pad024
  BaseFeature = -> BaseBend045
  Direction = (0,-1,2e-16)
  Length = 2
  Length2 = 10
  Profile = -> Sketch188
  ReferenceAxis = -> Sketch188 [N_Axis]
  Reversed = true
  Suppressed = false
  Type = 0
FEATURE [PartDesign::Pad] Pad025
  BaseFeature = -> Pad024
  Direction = (0,-1,2e-16)
  Length = 2
  Length2 = 10
  Profile = -> Sketch187
  ReferenceAxis = -> Sketch187 [N_Axis]
  Reversed = true
  Suppressed = false
  Type = 0
FEATURE [Sketcher::SketchObject] Sketch189
  AttachmentSupport = -> [XZ_Plane086]
  ExternalGeometry = -> [Sketch187]
  FullyConstrained = true
  MapMode = 5
  Placement = pos=(0,0,0) rot=(1,0,0;1.5708rad)
  sketch-geometry (12):
    g0: LineSegment StartX=26.01 StartY=1598 StartZ=0 EndX=29.01 EndY=1598 EndZ=0
    g1: LineSegment StartX=29.01 StartY=1598 StartZ=0 EndX=29.01 EndY=1601 EndZ=0
    g2: LineSegment StartX=29.01 StartY=1683 StartZ=0 EndX=29.01 EndY=1686 EndZ=0
    g3: LineSegment StartX=29.01 StartY=1686 StartZ=0 EndX=26.01 EndY=1686 EndZ=0
    g4: LineSegment StartX=-26.01 StartY=1686 StartZ=0 EndX=-29.01 EndY=1686 EndZ=0
    g5: LineSegment StartX=-29.01 StartY=1686 StartZ=0 EndX=-29.01 EndY=1683 EndZ=0
    g6: LineSegment StartX=-29.01 StartY=1601 StartZ=0 EndX=-29.01 EndY=1598 EndZ=0
    g7: LineSegment StartX=-29.01 StartY=1598 StartZ=0 EndX=-26.01 EndY=1598 EndZ=0
    g8: ArcOfCircle CenterX=26.01 CenterY=1601 CenterZ=0 NormalX=0 NormalY=0 NormalZ=1 AngleXU=0 Radius=3 StartAngle=4.71239 EndAngle=6.28319
    g9: ArcOfCircle CenterX=26.01 CenterY=1683 CenterZ=0 NormalX=0 NormalY=0 NormalZ=1 AngleXU=0 Radius=3 StartAngle=-2.04e-14 EndAngle=1.5708
    g10: ArcOfCircle CenterX=-26.01 CenterY=1683 CenterZ=0 NormalX=0 NormalY=0 NormalZ=1 AngleXU=0 Radius=3 StartAngle=1.5708 EndAngle=3.14159
    g11: ArcOfCircle CenterX=-26.01 CenterY=1601 CenterZ=0 NormalX=0 NormalY=0 NormalZ=1 AngleXU=0 Radius=3 StartAngle=3.14159 EndAngle=4.71239
  constraints (29):
    c: Coincident(g0,g-3)
    c: Horizontal(g0)
    c: Coincident(g0,g1)
    c: PointOnObject(g1,g-3)
    c: PointOnObject(g2,g-3)
    c: Coincident(g2,g-3)
    c: Coincident(g2,g3)
    c: Horizontal(g3)
    c: Coincident(g4,g-4)
    c: Horizontal(g4)
    c: Coincident(g4,g5)
    c: PointOnObject(g5,g-4)
    c: PointOnObject(g6,g-4)
    c: Coincident(g6,g-4)
    c: Coincident(g6,g7)
    c: Horizontal(g7)
    c: Coincident(g9,g3)
    c: Tangent(g8,g0) = -1.5708
    c: Tangent(g8,g1) = -1.5708
    c: Tangent(g9,g2) = -1.5708
    c: Tangent(g9,g3,g3) = -1.5708
    c: Tangent(g10,g4) = -1.5708
    c: Tangent(g10,g5) = -1.5708
    c: Tangent(g11,g7) = -1.5708
    c: Tangent(g11,g6) = -1.5708
    c: Equal(g8,g9)
    c: Equal(g8,g10)
    c: Equal(g8,g11)
    c: Radius(g8) = 3
FEATURE [PartDesign::Pocket] Pocket115
  BaseFeature = -> Pad025
  Direction = (0,1,-2e-16)
  Length = 5
  Length2 = 5
  Profile = -> Sketch189
  ReferenceAxis = -> Sketch189 [N_Axis]
  Suppressed = false
  Type = 1
FEATURE [Part::Extrusion] Extrude022
  Base = -> Compound041
  Dir = (0,0,1)
  DirMode = 2
  FaceMakerClass = Part::FaceMakerBullseye
  LengthFwd = 30
  LengthRev = 0
  Placement = pos=(0,10,1586) rot=(0.57735,0.57735,-0.57735;2.0944rad)
  Solid = true
  Symmetric = false
FEATURE [Sketcher::SketchObject] Sketch190
  AttachmentOffset = pos=(14,0,0) rot=(0,0,1;0rad)
  AttachmentSupport = -> [YZ_Plane086]
  FullyConstrained = true
  MapMode = 5
  Placement = pos=(0,14,0) rot=(0.57735,0.57735,0.57735;2.0944rad)
  expr: .AttachmentOffset.Base.x = <<pillar2_Properties>>.outer_length
  sketch-geometry (3):
    g0: ArcOfCircle CenterX=-3 CenterY=3 CenterZ=0 NormalX=0 NormalY=0 NormalZ=1 AngleXU=0 Radius=3 StartAngle=4.71239 EndAngle=6.28319
    g1: LineSegment StartX=-5.6e-14 StartY=3 StartZ=0 EndX=-5.6e-14 EndY=0 EndZ=0
    g2: LineSegment StartX=-5.6e-14 StartY=0 StartZ=0 EndX=-3 EndY=6.7e-15 EndZ=0
  constraints (7):
    c: PointOnObject(g0,g-1)
    c: Coincident(g2,g1)
    c: Vertical(g1)
    c: Tangent(g0,g1) = 1.5708
    c: Tangent(g2,g0) = 1.5708
    c: Coincident(g1,g-1)
    c: Radius(g0) = 3
FEATURE [PartDesign::Pocket] Pocket116
  BaseFeature = -> Pocket115
  Direction = (-1,2e-16,-3e-16)
  Length = 5
  Length2 = 5
  Midplane = true
  Profile = -> Sketch190
  ReferenceAxis = -> Sketch190 [N_Axis]
  Suppressed = false
  Type = 1
FEATURE [PartDesign::Plane] DatumPlane006
  AttachmentOffset = pos=(0,0,798) rot=(1,0,0;0rad)
  AttachmentSupport = -> [XY_Plane086]
  Length = 68.7922
  MapMode = 5
  Placement = pos=(0,0,798) rot=(0,0,1;0rad)
  ResizeMode = 0
  Width = 60.7722
  expr: .AttachmentOffset.Base.z = BaseBend045.length / 2
FEATURE [PartDesign::Mirrored] Mirrored013
  BaseFeature = -> Pocket116
  MirrorPlane = -> DatumPlane006
  Originals = -> [Pocket116]
  Suppressed = false
FEATURE [Sketcher::SketchObject] Sketch191  label="top_corner_base_sketch"
  AttachmentSupport = -> [XY_Plane087]
  FullyConstrained = true
  MapMode = 5
  sketch-geometry (2):
    g0: LineSegment StartX=-23.3827 StartY=13.5 StartZ=0 EndX=-5.116e-13 EndY=-3.109e-13 EndZ=0
    g1: LineSegment StartX=-5.131e-13 StartY=-3.108e-13 StartZ=0 EndX=23.3827 EndY=13.5 EndZ=0
  constraints (5):
    c: Coincident(g0,g-1)
    c: Coincident(g0,g1)
    c: Symmetric(g0,g1,g-2)
    c: Angle(g1,g0) = 2.0944
    c: Distance(g1) = 27  'length'
FEATURE [PartDesign::FeaturePython] BaseBend046  # WARN: FeaturePython — macro-defined, semantics opaque (R4)
  BendSide = 0
  BendSketch = -> Sketch191
  MidPlane = false
  Reverse = false
  Suppressed = false
  length = 30
  radius = 2
  thickness = 2
FEATURE [Part::FeaturePython] Placment021  # WARN: FeaturePython — macro-defined, semantics opaque (R4)
  AttacherType = Attacher::AttachEngine3D
  AttachmentOffset = pos=(0,24,-10) rot=(0,1,0;1.5708rad)
  AttachmentSupport = -> [Sketch191]
  ExposePlacement = true
  MapMode = 7
  MarkerShape = 1
  MarkerSize = 2
  NumElements = 1
  Placement = pos=(8.66025,5,24) rot=(0.935113,0.250563,0.250563;1.63783rad)
  Type = lattice2AttachablePlacement.AttachablePlacement
  isLattice = 1
FEATURE [Part::FeaturePython] Placment022  # WARN: FeaturePython — macro-defined, semantics opaque (R4)
  AttacherType = Attacher::AttachEngine3D
  AttachmentOffset = pos=(0,24,-22) rot=(0,1,0;1.5708rad)
  AttachmentSupport = -> [Sketch191]
  ExposePlacement = true
  MapMode = 7
  MarkerShape = 1
  MarkerSize = 2
  NumElements = 1
  Placement = pos=(19.0526,11,24) rot=(0.935113,0.250563,0.250563;1.63783rad)
  Type = lattice2AttachablePlacement.AttachablePlacement
  isLattice = 1
  expr: .AttachmentOffset.Base.z = -(<<top_corner_base_sketch>>.Constraints.length - 5 mm)
FEATURE [PartDesign::Pocket] Pocket117
  BaseFeature = -> Mirrored005
  Direction = (0.866025,0.5,-1e-16)
  Length = 5
  Length2 = 5
  Midplane = true
  Profile = -> Sketch081
  ReferenceAxis = -> Sketch081 [N_Axis]
  Refine = true
  Suppressed = false
  Type = 1
FEATURE [PartDesign::Body] Body078  label="hat_plexiglass_material_0.30ansi"
  Group = -> [Binder048,BaseBend022,Binder049,DatumPlane003,Hole010,Sketch081,Mirrored005,Binder050,Sketch082,Pocket117]
  Origin = -> Origin043
  Placement = pos=(0,0,-3) rot=(0,0,1;0rad)
  Tip = -> Pocket117
FEATURE [Sketcher::SketchObject] Sketch192
  AttachmentSupport = -> [XZ_Plane085]
  FullyConstrained = true
  MapMode = 5
  Placement = pos=(0,0,0) rot=(1,0,0;1.5708rad)
  sketch-geometry (4):
    g0: LineSegment StartX=-46.5 StartY=-2.18e-14 StartZ=0 EndX=-50.5 EndY=-2.18e-14 EndZ=0
    g1: LineSegment StartX=-50.5 StartY=-2.18e-14 StartZ=0 EndX=-50.5 EndY=4 EndZ=0
    g2: LineSegment StartX=-50.5 StartY=4 StartZ=0 EndX=-46.5 EndY=4 EndZ=0
    g3: LineSegment StartX=-46.5 StartY=4 StartZ=0 EndX=-46.5 EndY=-2.18e-14 EndZ=0
  constraints (12):
    c: Coincident(g0,g1)
    c: Coincident(g1,g2)
    c: Coincident(g2,g3)
    c: Coincident(g3,g0)
    c: Horizontal(g0)
    c: Horizontal(g2)
    c: Vertical(g1)
    c: Vertical(g3)
    c: PointOnObject(g0,g-1)
    c: DistanceX(g0,g0) = 4
    c: Equal(g1,g0)
    c: DistanceX(g0) = -50.5
FEATURE [Sketcher::SketchObject] Sketch193
  AttachmentOffset = pos=(0,0,0) rot=(0,1,0;0.523599rad)
  AttachmentSupport = -> [XZ_Plane087]
  FullyConstrained = true
  MapMode = 5
  Placement = pos=(0,0,0) rot=(0.935113,0.250563,0.250563;1.63783rad)
  expr: Constraints[6] = <<top_corner_base_sketch>>.Constraints.length
  sketch-geometry (9):
    g0: LineSegment StartX=27 StartY=20 StartZ=0 EndX=27 EndY=0 EndZ=0
    g1: LineSegment StartX=27 StartY=0 StartZ=0 EndX=4 EndY=0 EndZ=0
    g2: ArcOfCircle CenterX=24 CenterY=21.3669 CenterZ=0 NormalX=0 NormalY=0 NormalZ=1 AngleXU=0 Radius=3 StartAngle=5.42813 EndAngle=6.28319
    g3: ArcOfCircle CenterX=2.87807 CenterY=3 CenterZ=0 NormalX=0 NormalY=0 NormalZ=1 AngleXU=0 Radius=3 StartAngle=4.71239 EndAngle=5.42813
    g4: LineSegment StartX=25.9685 StartY=19.1031 StartZ=0 EndX=27 EndY=20 EndZ=0
    g5: LineSegment StartX=4 StartY=0 StartZ=0 EndX=4.84661 EndY=0.736183 EndZ=0
    g6: LineSegment StartX=4.84661 StartY=0.736183 StartZ=0 EndX=25.9685 EndY=19.1031 EndZ=0
    g7: LineSegment StartX=2.87807 StartY=0 StartZ=0 EndX=4 EndY=0 EndZ=0
    g8: LineSegment StartX=27 StartY=20 StartZ=0 EndX=27 EndY=21.3669 EndZ=0
  constraints (24):
    c: PointOnObject(g5,g-1)
    c: Coincident(g4,g0)
    c: PointOnObject(g0,g-1)
    c: Vertical(g0)
    c: Coincident(g0,g1)
    c: Coincident(g1,g5)
    c: DistanceX(g0) = 27
    c: DistanceX(g5) = 4
    c: Tangent(g2,g0)
    c: Coincident(g5,g6)
    c: Coincident(g7,g1)
    c: Horizontal(g7)
    c: Coincident(g8,g0)
    c: Coincident(g8,g2)
    c: Vertical(g8)
    c: Equal(g3,g2)
    c: Radius(g3) = 3
    c: Tangent(g3,g6) = -1.5708
    c: Tangent(g6,g2) = -1.5708
    c: Coincident(g2,g4)
    c: Parallel(g4,g6)
    c: Parallel(g5,g6)
    c: Tangent(g7,g3) = -1.5708
    c: DistanceY(g0) = 20
FEATURE [Part::FeaturePython] Placment023  # WARN: FeaturePython — macro-defined, semantics opaque (R4)
  AttacherType = Attacher::AttachEngine3D
  AttachmentOffset = pos=(0,12,-10) rot=(0,1,0;1.5708rad)
  AttachmentSupport = -> [Sketch191]
  ExposePlacement = true
  MapMode = 7
  MarkerShape = 1
  MarkerSize = 20
  NumElements = 1
  Placement = pos=(8.66025,5,12) rot=(0.935113,0.250563,0.250563;1.63783rad)
  Type = lattice2AttachablePlacement.AttachablePlacement
  isLattice = 1
FEATURE [Part::FeaturePython] Join007  # WARN: FeaturePython — macro-defined, semantics opaque (R4)
  ExposePlacement = false
  Interleave = false
  Links = -> [Placment021,Placment022,Placment023]
  MarkerShape = 1
  MarkerSize = 0
  NumElements = 3
  Type = lattice2JoinArrays.JoinArrays
  isLattice = 1
FEATURE [Part::FeaturePython] Mirror009  label="Mirror009 of Join007"  # WARN: FeaturePython — macro-defined, semantics opaque (R4)
  ExposePlacement = false
  FlipX = true
  FlipY = false
  FlipZ = false
  MarkerShape = 1
  MarkerSize = 0
  NumElements = 3
  Object = -> Join007
  ObjectTraversal = 0
  Type = lattice2Mirror.LatticeMirror
  isLattice = 1
FEATURE [Part::FeaturePython] Join008  # WARN: FeaturePython — macro-defined, semantics opaque (R4)
  ExposePlacement = false
  Interleave = false
  Links = -> [Mirror009,Join007]
  MarkerShape = 1
  MarkerSize = 0
  NumElements = 6
  Type = lattice2JoinArrays.JoinArrays
  isLattice = 1
FEATURE [Part::FeaturePython] Populate031  label="Populate Join008 with hole_3.4mm_extrude"  # WARN: FeaturePython — macro-defined, semantics opaque (R4)
  Copying = 0
  ExposePlacement = false
  MarkerShape = 1
  MarkerSize = 0
  NumElements = 0
  Object = -> Extrude019
  OutputCompounding = 1
  PlacementsTo = -> Join008
  Referencing = 0
  Type = lattice2PopulateCopies.LatticePopulateCopies
  isLattice = 0
FEATURE [Sketcher::SketchObject] Sketch194
  AttachmentSupport = -> [XZ_Plane085]
  FullyConstrained = true
  MapMode = 5
  Placement = pos=(0,0,0) rot=(1,0,0;1.5708rad)
  sketch-geometry (6):
    g0: LineSegment StartX=-50.5 StartY=108 StartZ=0 EndX=-50.5 EndY=110 EndZ=0
    g1: LineSegment StartX=-50.5 StartY=110 StartZ=0 EndX=-48.5 EndY=110 EndZ=0
    g2: LineSegment StartX=-43.5 StartY=110 StartZ=0 EndX=-35.5 EndY=110 EndZ=0
    g3: LineSegment StartX=-35.5 StartY=110 StartZ=0 EndX=-35.5 EndY=102 EndZ=0
    g4: ArcOfCircle CenterX=-43.5 CenterY=102 CenterZ=0 NormalX=0 NormalY=0 NormalZ=1 AngleXU=0 Radius=8 StartAngle=8.302e-13 EndAngle=1.5708
    g5: ArcOfCircle CenterX=-48.5 CenterY=108 CenterZ=0 NormalX=0 NormalY=0 NormalZ=1 AngleXU=0 Radius=2 StartAngle=1.5708 EndAngle=3.14159
  constraints (16):
    c: Vertical(g0)
    c: Coincident(g0,g1)
    c: Horizontal(g1)
    c: Horizontal(g2)
    c: Coincident(g2,g3)
    c: Vertical(g3)
    c: Horizontal(g0,g2)
    c: DistanceY(g0) = 110
    c: Tangent(g5,g0) = 1.5708
    c: DistanceX(g0) = -50.5
    c: Tangent(g5,g1) = 1.5708
    c: Tangent(g4,g3) = 1.5708
    c: Tangent(g4,g2) = 1.5708
    c: DistanceX(g0,g2) = 15
    c: DistanceX(g0,g2) = 7
    c: Radius(g5) = 2
FEATURE [PartDesign::Pocket] Pocket119
  BaseFeature = -> Pad022
  Direction = (0,1,2e-16)
  Length = 5
  Length2 = 5
  Midplane = true
  Placement = pos=(0,0,0) rot=(0.57735,0.57735,0.57735;2.0944rad)
  Profile = -> Sketch194
  ReferenceAxis = -> Sketch194 [N_Axis]
  Suppressed = false
  Type = 1
FEATURE [PartDesign::Boolean] Boolean015
  BaseFeature = -> Pocket119
  Group = -> [Compound054]
  Refine = true
  Suppressed = false
  Type = 1
  UsePlacement = false
FEATURE [PartDesign::Body] Body111  label="pillar2_bottom_material_0.50ansi"
  Group = -> [Sketch180,Pad020,Sketch181,Sketch182,Sketch192,Pad021,Pad022,Sketch183,Sketch184,Sketch185,Pocket119,Boolean015,Sketch194]
  Origin = -> Origin085
  Placement = pos=(18.3,54.5,0) rot=(0,0,1;1.5708rad)
  Tip = -> Boolean015
FEATURE [Part::Mirroring] Part__Mirroring026  label="pillar2_bottom_material_0.50ansi (Mirror #27)"
  Base = (0,0,0)
  Normal = (0,1,0)
  Placement = pos=(0,0,0) rot=(0,0,1;3.14159rad)
  Source = -> Body111
FEATURE [Sketcher::SketchObject] Sketch195
  AttachmentSupport = -> [XY_Plane080]
  ExternalGeometry = -> [Sketch174,Sketch171]
  FullyConstrained = true
  MapMode = 5
  sketch-geometry (9):
    g0: LineSegment StartX=6.08e-14 StartY=555.654 StartZ=0 EndX=42.5 EndY=285 EndZ=0
    g1: LineSegment StartX=42.5 StartY=285 StartZ=0 EndX=0 EndY=285 EndZ=0
    g2: LineSegment StartX=6.08e-14 StartY=555.654 StartZ=0 EndX=0 EndY=555.654 EndZ=0
    g3: LineSegment StartX=0 StartY=555.654 StartZ=0 EndX=0 EndY=285 EndZ=0
    g4: Circle CenterX=36 CenterY=265 CenterZ=0 NormalX=0 NormalY=0 NormalZ=1 AngleXU=0 Radius=2.5
    g5: Circle CenterX=68.9742 CenterY=55.7258 CenterZ=0 NormalX=0 NormalY=0 NormalZ=1 AngleXU=0 Radius=2.5
    g6: Circle CenterX=56.173 CenterY=140.207 CenterZ=0 NormalX=0 NormalY=0 NormalZ=1 AngleXU=0 Radius=2.5
    g7: LineSegment StartX=68.9742 StartY=55.7258 StartZ=0 EndX=56.173 EndY=140.207 EndZ=0
    g8: LineSegment StartX=56.173 StartY=140.207 StartZ=0 EndX=36 EndY=265 EndZ=0
  constraints (24):
    c: Coincident(g-3,g0)
    c: Coincident(g0,g-4)
    c: Coincident(g0,g1)
    c: Coincident(g0,g2)
    c: PointOnObject(g2,g-2)
    c: Horizontal(g2)
    c: Coincident(g2,g3)
    c: PointOnObject(g3,g-4)
    c: Vertical(g3)
    c: Coincident(g1,g3)
    c: Diameter(g4) = 5
    c: DistanceX(g-1,g4) = 36
    c: DistanceY(g-1,g4) = 265
    c: Equal(g5,g6)
    c: Equal(g6,g4)
    c: Block(g5)
    c: Block(g6)
    c: Coincident(g7,g5)
    c: Coincident(g7,g6)
    c: Coincident(g8,g6)
    c: Coincident(g8,g4)
    c: DistanceX(g5) = 68.9742
    c: DistanceY(g5) = 55.7258
    c: Distance(g6,g-3) = 419.132
FEATURE [Sketcher::SketchObject] Sketch196
  ExternalGeometry = -> [Sketch015]
  FullyConstrained = true
  sketch-geometry (8):
    g0: LineSegment StartX=0 StartY=0 StartZ=0 EndX=129.904 EndY=75 EndZ=0
    g1: ArcOfCircle CenterX=0 CenterY=-545.406 CenterZ=0 NormalX=0 NormalY=0 NormalZ=1 AngleXU=0 Radius=735.406 StartAngle=1.50554 EndAngle=1.5708
    g2: ArcOfCircle CenterX=46 CenterY=158.499 CenterZ=0 NormalX=0 NormalY=0 NormalZ=1 AngleXU=0 Radius=30 StartAngle=0.539589 EndAngle=1.50554
    g3: ArcOfCircle CenterX=-6084.95 CenterY=-3513.15 CenterZ=0 NormalX=0 NormalY=0 NormalZ=1 AngleXU=0 Radius=7176.3 StartAngle=0.523599 EndAngle=0.539589
    g4: Circle CenterX=0 CenterY=0 CenterZ=0 NormalX=0 NormalY=0 NormalZ=1 AngleXU=0 Radius=545.406
    g5: LineSegment StartX=0 StartY=0 StartZ=0 EndX=219.104 EndY=126.5 EndZ=0
    g6: LineSegment StartX=0 StartY=0 StartZ=0 EndX=4.89e-14 EndY=253 EndZ=0
    g7: ArcOfCircle CenterX=0 CenterY=-545.406 CenterZ=0 NormalX=0 NormalY=0 NormalZ=1 AngleXU=0 Radius=798.406 StartAngle=0.821161 EndAngle=1.5708
  constraints (23):
    c: Angle(g0) = 0.523599
    c: Tangent(g2,g1) = -1.5708
    c: Distance(g0) = 150
    c: PointOnObject(g1,g-2)
    c: PointOnObject(g1,g-2)
    c: DistanceY(g1) = 190
    c: Coincident(g3,g0)
    c: Coincident(g0,g-1)
    c: Coincident(g4,g0)
    c: Coincident(g5,g0)
    c: Coincident(g5,g-3)
    c: PointOnObject(g6,g-2)
    c: Coincident(g6,g0)
    c: Equal(g6,g5)
    c: PointOnObject(g7,g4)
    c: Coincident(g7,g6)
    c: PointOnObject(g7,g4)
    c: PointOnObject(g-3,g4)
    c: Coincident(g1,g7)
    c: Tangent(g3,g2) = -1.5708
    c: Perpendicular(g3,g5)
    c: Radius(g2) = 30
    c: DistanceX(g2) = 46
FEATURE [Sketcher::SketchObject] Sketch197  label="hole_5_mm"
  FullyConstrained = true
  sketch-geometry (1):
    g0: Circle CenterX=0 CenterY=0 CenterZ=0 NormalX=0 NormalY=0 NormalZ=1 AngleXU=0 Radius=2.5
  constraints (2):
    c: Coincident(g0,g-1)
    c: Diameter(g0) = 5
FEATURE [Part::Extrusion] Extrude023  label="hole_5_mm_extrude"
  Base = -> Sketch197
  Dir = (0,0,1)
  DirMode = 2
  FaceMakerClass = Part::FaceMakerBullseye
  LengthFwd = 30
  LengthRev = 0
  Solid = true
  Symmetric = false
FEATURE [Part::FeaturePython] PolarArray003  # WARN: FeaturePython — macro-defined, semantics opaque (R4)
  Alignment = 0
  AttacherType = Attacher::AttachEngine3D
  CellStart = A1
  Count = 9
  DistributionLaw = 0
  EndInclusive = false
  ExposePlacement = false
  FlipX = false
  FlipZ = false
  GeneratorMode = 0
  MarkerShape = 1
  MarkerSize = 0
  NumElements = 9
  OrientMode = 2
  Radius = 137.5
  Reverse = false
  SpanEnd = 360
  SpanStart = 0
  Step = 40
  Type = lattice2PolarArray2.PolarArray
  UseArcRadius = false
  UseArcRange = 0
  VSGVersion = 1
  Values = 0.0 | 40.0 | 80.0 | 120.0 | 160.0 | 200.0 | 240.0 | 280.0 | 320.0
  ValuesSource = 2
  isLattice = 1
FEATURE [Part::Mirroring] Part__Mirroring027  label="Sketch196 (Mirror #28)"
  Base = (0,0,0)
  Normal = (1,0,0)
  Source = -> Sketch196
FEATURE [Part::Compound] Compound055
  Links = -> [Sketch196,Part__Mirroring027]
FEATURE [Part::FeaturePython] Array009  # Draft array (typed FeaturePython)
  AlwaysSyncPlacement = false
  Angle = 360
  ArrayType = 1
  Axis = (0,0,1)
  Base = -> Compound055
  Center = (0,0,0)
  Count = 3
  ExpandArray = false
  Fuse = false
  IntervalAxis = (0,0,0)
  IntervalX = (50,0,0)
  IntervalY = (0,50,0)
  IntervalZ = (0,0,50)
  NumberCircles = 3
  NumberPolar = 3
  NumberX = 2
  NumberY = 2
  NumberZ = 1
  PlacementList = 3 placements: [(0,0,0),(0,0,0),(0,0,0)]
  RadialDistance = 50
  ScaleList = (3) [(1,1,1),(1,1,1),(1,1,1)]
  Symmetry = 1
  TangentialDistance = 25
FEATURE [PartDesign::SubShapeBinder] Binder123
  BindCopyOnChange = 0
  BindMode = 0
  ClaimChildren = true
  Context = -> Part020 [Body114.Binder123.]
  Fuse = false
  MakeFace = true
  OffsetFill = false
  OffsetIntersection = false
  OffsetJoinType = 0
  OffsetOpenResult = false
  PartialLoad = false
  Relative = true
  Support = -> [Array009]
  _Version = 2
FEATURE [PartDesign::Pad] Pad026
  Direction = (0,0,1)
  Length = 18
  Length2 = 10
  Profile = -> Binder123
  Suppressed = false
  Type = 0
FEATURE [Sketcher::SketchObject] Sketch198  label="hole_10.5mm"
  FullyConstrained = true
  sketch-geometry (1):
    g0: Circle CenterX=0 CenterY=0 CenterZ=0 NormalX=0 NormalY=0 NormalZ=1 AngleXU=0 Radius=5.25
  constraints (2):
    c: Coincident(g0,g-1)
    c: Diameter(g0) = 10.5
FEATURE [Part::Extrusion] Extrude024  label="hole_10.5mm_extrude"
  Base = -> Sketch198
  Dir = (0,0,1)
  DirMode = 2
  FaceMakerClass = Part::FaceMakerBullseye
  LengthFwd = 30
  LengthRev = 0
  Solid = true
  Symmetric = false
FEATURE [Sketcher::SketchObject] Sketch199
  AttachmentSupport = -> [XY_Plane090]
  FullyConstrained = true
  MapMode = 5
  sketch-geometry (5):
    g0: LineSegment StartX=-42.5 StartY=-49 StartZ=0 EndX=-42.5 EndY=49 EndZ=0
    g1: LineSegment StartX=-42.5 StartY=49 StartZ=0 EndX=42.5 EndY=49 EndZ=0
    g2: LineSegment StartX=42.5 StartY=49 StartZ=0 EndX=42.5 EndY=-49 EndZ=0
    g3: LineSegment StartX=42.5 StartY=-49 StartZ=0 EndX=-42.5 EndY=-49 EndZ=0
    g4: GeomPoint X=0 Y=0 Z=0
  constraints (12):
    c: Coincident(g0,g1)
    c: Coincident(g1,g2)
    c: Coincident(g2,g3)
    c: Coincident(g3,g0)
    c: Horizontal(g1)
    c: Horizontal(g3)
    c: Vertical(g0)
    c: Vertical(g2)
    c: Symmetric(g1,g0,g4)
    c: Coincident(g4,g-1)
    c: DistanceX(g0,g1) = 85
    c: DistanceY(g0,g1) = 98
FEATURE [Sketcher::SketchObject] Sketch200
  AttachmentOffset = pos=(0,0,3) rot=(0,0,1;0rad)
  AttachmentSupport = -> [XY_Plane090]
  FullyConstrained = true
  MapMode = 5
  Placement = pos=(0,0,3) rot=(0,0,1;0rad)
  sketch-geometry (7):
    g0: LineSegment StartX=9.81495 StartY=3.2e-14 StartZ=0 EndX=4.90748 EndY=8.5 EndZ=0
    g1: LineSegment StartX=4.90748 StartY=8.5 StartZ=0 EndX=-4.90748 EndY=8.5 EndZ=0
    g2: LineSegment StartX=-4.90748 StartY=8.5 StartZ=0 EndX=-9.81495 EndY=-2.149e-13 EndZ=0
    g3: LineSegment StartX=-9.81495 StartY=-2.149e-13 StartZ=0 EndX=-4.90748 EndY=-8.5 EndZ=0
    g4: LineSegment StartX=-4.90748 StartY=-8.5 StartZ=0 EndX=4.90748 EndY=-8.5 EndZ=0
    g5: LineSegment StartX=4.90748 StartY=-8.5 StartZ=0 EndX=9.81495 EndY=3.2e-14 EndZ=0
    g6: Circle CenterX=2.6e-15 CenterY=-5.63e-14 CenterZ=0 NormalX=0 NormalY=0 NormalZ=1 AngleXU=0 Radius=9.81495
  constraints (16):
    c: Coincident(g0,g1)
    c: Coincident(g1,g2)
    c: Coincident(g2,g3)
    c: Coincident(g3,g4)
    c: Coincident(g4,g5)
    c: Coincident(g5,g0)
    c: Equal(g0, g1-g5) x5
    c: PointOnObject(g0,g6)
    c: PointOnObject(g1,g6)
    c: PointOnObject(g2,g6)
    c: PointOnObject(g3,g6)
    c: PointOnObject(g4,g6)
    c: PointOnObject(g5,g6)
    c: Coincident(g6,g-1)
    c: PointOnObject(g5,g-1)
    c: DistanceY(g4,g0) = 17
FEATURE [PartDesign::SubShapeBinder] Binder124
  BindCopyOnChange = 0
  BindMode = 0
  ClaimChildren = false
  Context = -> Part020 [Body116.Binder124.]
  Fuse = false
  MakeFace = true
  OffsetFill = false
  OffsetIntersection = false
  OffsetJoinType = 0
  OffsetOpenResult = false
  PartialLoad = false
  Relative = true
  Support = -> [Array003]
  _Version = 2
  expr: Support = Array003._self
FEATURE [PartDesign::Pad] Pad027
  Direction = (0,0,1)
  Length = 18
  Length2 = 10
  Profile = -> Binder124
  Suppressed = false
  Type = 0
FEATURE [PartDesign::Body] Body116  label="basement_v2_top"
  Group = -> [Binder124,Pad027]
  Origin = -> Origin091
  Tip = -> Pad027
FEATURE [PartDesign::SubShapeBinder] Binder125
  BindCopyOnChange = 0
  BindMode = 0
  ClaimChildren = true
  Context = -> Part020 [Body117.Binder125.]
  Fuse = false
  MakeFace = true
  OffsetFill = false
  OffsetIntersection = false
  OffsetJoinType = 0
  OffsetOpenResult = false
  PartialLoad = false
  Relative = false
  Support = -> [Array002]
  _Version = 2
FEATURE [PartDesign::Pad] Pad028
  Direction = (0,0,1)
  Length = 18
  Length2 = 10
  Profile = -> Binder125
  Suppressed = false
  Type = 0
FEATURE [Sketcher::SketchObject] Sketch201  label="basement_v3_bottom_sketch"
  FullyConstrained = false
  sketch-geometry (3):
    g0: LineSegment StartX=0 StartY=383.246 StartZ=0 EndX=33.1532 EndY=383.246 EndZ=0
    g1: LineSegment StartX=33.1532 StartY=383.246 StartZ=0 EndX=190.815 EndY=110.167 EndZ=0
    g2: LineSegment StartX=0 StartY=0 StartZ=0 EndX=190.815 EndY=110.167 EndZ=0
  constraints (9):
    c: Horizontal(g0)
    c: Coincident(g0,g1)
    c: Coincident(g2,g-1)
    c: Coincident(g2,g1)
    c: Angle(g2) = 0.523599
    c: Perpendicular(g1,g2)
    c: DistanceX(g0) = 33.1532
    c: DistanceY(g0) = 383.246
    c: PointOnObject(g0,g-2)
FEATURE [Part::Mirroring] Part__Mirroring028  label="basement_v3_bottom_sketch (Mirror #29)"
  Base = (0,0,0)
  Normal = (1,0,0)
  Source = -> Sketch201
FEATURE [Part::Compound] Compound057
  Links = -> [Sketch201,Part__Mirroring028]
FEATURE [Part::FeaturePython] Array010  # Draft array (typed FeaturePython)
  AlwaysSyncPlacement = false
  Angle = 360
  ArrayType = 1
  Axis = (0,0,1)
  Base = -> Compound057
  Center = (0,0,0)
  Count = 3
  ExpandArray = false
  Fuse = false
  IntervalAxis = (0,0,0)
  IntervalX = (50,0,0)
  IntervalY = (0,50,0)
  IntervalZ = (0,0,50)
  NumberCircles = 3
  NumberPolar = 3
  NumberX = 2
  NumberY = 2
  NumberZ = 1
  PlacementList = 3 placements: [(0,0,0),(0,0,0),(0,0,0)]
  RadialDistance = 50
  ScaleList = (3) [(1,1,1),(1,1,1),(1,1,1)]
  Symmetry = 1
  TangentialDistance = 25
FEATURE [Sketcher::SketchObject] Sketch202  label="basement_v3_top_sketch"
  FullyConstrained = false
  sketch-geometry (3):
    g0: LineSegment StartX=9.16e-14 StartY=1.21e-14 StartZ=0 EndX=177.196 EndY=102.304 EndZ=0
    g1: LineSegment StartX=177.196 StartY=102.304 StartZ=0 EndX=37.3483 EndY=344.528 EndZ=0
    g2: LineSegment StartX=37.3483 StartY=344.528 StartZ=0 EndX=0 EndY=344.528 EndZ=0
  constraints (8):
    c: Coincident(g-1,g0)
    c: Coincident(g0,g1)
    c: Coincident(g1,g2)
    c: PointOnObject(g2,g-2)
    c: Horizontal(g2)
    c: Angle(g0) = 0.523599
    c: Perpendicular(g1,g0)
    c: Distance(g0) = 204.609
FEATURE [Part::Mirroring] Part__Mirroring029  label="basement_v3_top_sketch (Mirror #30)"
  Base = (0,0,0)
  Normal = (1,0,0)
  Source = -> Sketch202
FEATURE [Part::Compound] Compound058
  Links = -> [Part__Mirroring029,Sketch202]
FEATURE [Part::FeaturePython] Array011  # Draft array (typed FeaturePython)
  AlwaysSyncPlacement = false
  Angle = 360
  ArrayType = 1
  Axis = (0,0,1)
  Base = -> Compound058
  Center = (0,0,0)
  Count = 3
  ExpandArray = false
  Fuse = false
  IntervalAxis = (0,0,0)
  IntervalX = (50,0,0)
  IntervalY = (0,50,0)
  IntervalZ = (0,0,50)
  NumberCircles = 3
  NumberPolar = 3
  NumberX = 2
  NumberY = 2
  NumberZ = 1
  PlacementList = 3 placements: [(0,0,0),(0,0,0),(0,0,0)]
  RadialDistance = 50
  ScaleList = (3) [(1,1,1),(1,1,1),(1,1,1)]
  Symmetry = 1
  TangentialDistance = 25
FEATURE [PartDesign::SubShapeBinder] Binder126
  BindCopyOnChange = 0
  BindMode = 0
  ClaimChildren = true
  Context = -> Part021 [Body118.Binder126.]
  Fuse = false
  MakeFace = true
  OffsetFill = false
  OffsetIntersection = false
  OffsetJoinType = 0
  OffsetOpenResult = false
  PartialLoad = false
  Relative = false
  Support = -> [Array010]
  _Version = 2
FEATURE [PartDesign::FeaturePython] BaseBend047  # WARN: FeaturePython — macro-defined, semantics opaque (R4)
  BendSide = 0
  BendSketch = -> Binder126
  MidPlane = false
  Reverse = false
  Suppressed = false
  length = 100
  radius = 1
  thickness = 1
FEATURE [PartDesign::SubShapeBinder] Binder127
  BindCopyOnChange = 0
  BindMode = 0
  ClaimChildren = true
  Context = -> Part021 [Body119.Binder127.]
  Fuse = true
  MakeFace = true
  OffsetFill = false
  OffsetIntersection = false
  OffsetJoinType = 0
  OffsetOpenResult = false
  PartialLoad = false
  Relative = true
  Support = -> [Connect003]
  _Version = 2
FEATURE [PartDesign::FeaturePython] BaseBend048  # WARN: FeaturePython — macro-defined, semantics opaque (R4)
  BendSide = 0
  BendSketch = -> Binder127
  MidPlane = false
  Reverse = false
  Suppressed = false
  length = 100
  radius = 1
  thickness = 3
FEATURE [Sketcher::SketchObject] Sketch203  label="wheel_holes"
  FullyConstrained = true
  sketch-geometry (9):
    g0: LineSegment StartX=-20 StartY=-20 StartZ=0 EndX=-20 EndY=20 EndZ=0
    g1: LineSegment StartX=-20 StartY=20 StartZ=0 EndX=20 EndY=20 EndZ=0
    g2: LineSegment StartX=20 StartY=20 StartZ=0 EndX=20 EndY=-20 EndZ=0
    g3: LineSegment StartX=20 StartY=-20 StartZ=0 EndX=-20 EndY=-20 EndZ=0
    g4: GeomPoint X=0 Y=0 Z=0
    g5: Circle CenterX=20 CenterY=20 CenterZ=0 NormalX=0 NormalY=0 NormalZ=1 AngleXU=0 Radius=1.6
    g6: Circle CenterX=-20 CenterY=20 CenterZ=0 NormalX=0 NormalY=0 NormalZ=1 AngleXU=0 Radius=1.6
    g7: Circle CenterX=-20 CenterY=-20 CenterZ=0 NormalX=0 NormalY=0 NormalZ=1 AngleXU=0 Radius=1.6
    g8: Circle CenterX=20 CenterY=-20 CenterZ=0 NormalX=0 NormalY=0 NormalZ=1 AngleXU=0 Radius=1.6
  constraints (20):
    c: Coincident(g0,g1)
    c: Coincident(g1,g2)
    c: Coincident(g2,g3)
    c: Coincident(g3,g0)
    c: Horizontal(g1)
    c: Horizontal(g3)
    c: Vertical(g0)
    c: Vertical(g2)
    c: Symmetric(g1,g0,g4)
    c: Coincident(g4,g-1)
    c: Equal(g2,g1)
    c: DistanceX(g1,g1) = 40
    c: Coincident(g5,g1)
    c: Coincident(g6,g0)
    c: Coincident(g7,g0)
    c: Coincident(g8,g2)
    c: Equal(g8,g5)
    c: Equal(g5,g7)
    c: Equal(g7,g6)
    c: Diameter(g5) = 3.2
FEATURE [Part::FeaturePython] PolarArray004  label="wheel_holes_placements"  # WARN: FeaturePython — macro-defined, semantics opaque (R4)
  Alignment = 0
  AttacherType = Attacher::AttachEngine3D
  CellStart = A1
  Count = 3
  DistributionLaw = 0
  EndInclusive = false
  ExposePlacement = false
  FlipX = false
  FlipZ = false
  GeneratorMode = 0
  MarkerShape = 1
  MarkerSize = 0
  NumElements = 3
  OrientMode = 2
  Placement = pos=(0,0,0) rot=(0,0,1;1.5708rad)
  Radius = 333
  Reverse = false
  SpanEnd = 360
  SpanStart = 0
  Step = 120
  Type = lattice2PolarArray2.PolarArray
  UseArcRadius = false
  UseArcRange = 0
  VSGVersion = 1
  Values = 0.0 | 120.0 | 240.0
  ValuesSource = 2
  isLattice = 1
FEATURE [Part::Extrusion] Extrude025  label="wheel_holes_extrude"
  Base = -> Sketch203
  Dir = (0,0,1)
  DirMode = 2
  FaceMakerClass = Part::FaceMakerBullseye
  LengthFwd = 30
  LengthRev = 0
  Solid = true
  Symmetric = false
FEATURE [Part::FeaturePython] Populate033  label="Populate wheel_holes_placements with wheel_holes_extrude"  # WARN: FeaturePython — macro-defined, semantics opaque (R4)
  Copying = 0
  ExposePlacement = false
  MarkerShape = 1
  MarkerSize = 0
  NumElements = 0
  Object = -> Extrude025
  OutputCompounding = 1
  PlacementsTo = -> PolarArray004
  Referencing = 0
  Type = lattice2PopulateCopies.LatticePopulateCopies
  isLattice = 0
FEATURE [Part::Cylinder] Cylinder  label="hole_7.5_mm_extrude"
  Angle = 360
  AttacherType = Attacher::AttachEngine3D
  FirstAngle = 0
  Height = 30
  Radius = 3.5
  SecondAngle = 0
FEATURE [Part::FeaturePython] Populate034  label="Populate PolarArray003 with hole_7.5_mm_extrude"  # WARN: FeaturePython — macro-defined, semantics opaque (R4)
  Copying = 0
  ExposePlacement = false
  MarkerShape = 1
  MarkerSize = 0
  NumElements = 0
  Object = -> Cylinder
  OutputCompounding = 1
  PlacementsTo = -> PolarArray003
  Referencing = 0
  Type = lattice2PopulateCopies.LatticePopulateCopies
  isLattice = 0
FEATURE [Part::Compound] Compound056  label="basement_spacer_cut1"
  Links = -> [Extrude024,Populate034]
FEATURE [PartDesign::Boolean] Boolean018
  BaseFeature = -> Pad026
  Group = -> [Compound056]
  Suppressed = false
  Type = 1
  UsePlacement = false
FEATURE [PartDesign::Body] Body114  label="basement_v2_spacer"
  Group = -> [Binder123,Pad026,Boolean018]
  Origin = -> Origin089
  Tip = -> Boolean018
FEATURE [PartDesign::FeatureBase] BaseFeature001
  BaseFeature = -> Body114
  Suppressed = false
FEATURE [PartDesign::Pocket] Pocket122
  BaseFeature = -> BaseFeature001
  Direction = (0,0,-1)
  Length = 7
  Length2 = 5
  Profile = -> Sketch200
  ReferenceAxis = -> Sketch200 [N_Axis]
  Reversed = true
  Suppressed = false
  Type = 0
FEATURE [PartDesign::Body] Body115  label="basement_v2_spacer2"
  BaseFeature = -> Body114
  Group = -> [BaseFeature001,Sketch199,Sketch200,Pocket122]
  Origin = -> Origin090
  Tip = -> Pocket122
  expr: BaseFeature = <<basement_v2_spacer>>._self
FEATURE [Part::Cylinder] Cylinder001  label="hole_3.2_mm_extrude"
  Angle = 360
  AttacherType = Attacher::AttachEngine3D
  FirstAngle = 0
  Height = 30
  Radius = 1.6
  SecondAngle = 0
FEATURE [Part::FeaturePython] Populate035  label="Populate PolarArray003 with hole_3.2_mm"  # WARN: FeaturePython — macro-defined, semantics opaque (R4)
  Copying = 0
  ExposePlacement = false
  MarkerShape = 1
  MarkerSize = 0
  NumElements = 0
  Object = -> Cylinder001
  OutputCompounding = 1
  PlacementsTo = -> PolarArray003
  Referencing = 0
  Type = lattice2PopulateCopies.LatticePopulateCopies
  isLattice = 0
FEATURE [Part::Compound] Compound059  label="basement_v2_bottom_cut1"
  Links = -> [Populate033,Populate028,Populate035,Extrude024]
FEATURE [Sketcher::SketchObject] Sketch204
  AttachmentOffset = pos=(0,370,0) rot=(0,0,1;0rad)
  AttachmentSupport = -> [XY_Plane092]
  FullyConstrained = true
  MapMode = 5
  Placement = pos=(0,370,0) rot=(0,0,1;0rad)
  sketch-geometry (1):
    g0: Circle CenterX=0 CenterY=0 CenterZ=0 NormalX=0 NormalY=0 NormalZ=1 AngleXU=0 Radius=4
  constraints (2):
    c: Coincident(g0,g-1)
    c: Diameter(g0) = 8
FEATURE [PartDesign::Hole] Hole021
  BaseFeature = -> Pad028
  CustomThreadClearance = 0
  Depth = 25
  DepthType = 0
  Diameter = 8
  DrillForDepth = false
  DrillPoint = 1
  DrillPointAngle = 118
  HoleCutCountersinkAngle = 90
  HoleCutCustomValues = false
  HoleCutDepth = 0
  HoleCutDiameter = 6.1
  HoleCutType = 0
  ModelThread = false
  Profile = -> Sketch204
  Reversed = true
  Suppressed = false
  Tapered = false
  TaperedAngle = 90
  ThreadClass = 0
  ThreadDepth = 25
  ThreadDepthType = 0
  ThreadDirection = 0
  ThreadFit = 0
  ThreadSize = 0
  ThreadType = 0
  Threaded = false
  UseCustomThreadClearance = false
FEATURE [PartDesign::PolarPattern] PolarPattern011
  Angle = 360
  Axis = -> Z_Axis092
  BaseFeature = -> Hole021
  Mode = 0
  Occurrences = 3
  Offset = 120
  Originals = -> [Hole021]
  Suppressed = false
FEATURE [PartDesign::Boolean] Boolean019
  BaseFeature = -> PolarPattern011
  Group = -> [Compound059]
  Suppressed = false
  Type = 1
  UsePlacement = false
FEATURE [PartDesign::Body] Body117  label="basement_v2_bottom"
  Group = -> [Binder125,Pad028,Sketch204,Hole021,PolarPattern011,Boolean019]
  Origin = -> Origin092
  Tip = -> Boolean019
FEATURE [App::Part] Part020  label="basement_v2"
  Group = -> [Body114,Body115,Body116,Body117]
  Origin = -> Origin088
FEATURE [Sketcher::SketchObject] Sketch205
  AttachmentSupport = -> [XZ_Plane096]
  FullyConstrained = true
  MapMode = 5
  Placement = pos=(0,0,0) rot=(1,0,0;1.5708rad)
  sketch-geometry (4):
    g0: LineSegment StartX=0.1 StartY=485 StartZ=0 EndX=-14 EndY=485 EndZ=0
    g1: LineSegment StartX=-14 StartY=485 StartZ=0 EndX=-14 EndY=1590 EndZ=0
    g2: LineSegment StartX=-14 StartY=1590 StartZ=0 EndX=0.1 EndY=1590 EndZ=0
    g3: LineSegment StartX=0.1 StartY=1590 StartZ=0 EndX=0.1 EndY=485 EndZ=0
  constraints (13):
    c: Coincident(g0,g1)
    c: Coincident(g1,g2)
    c: Coincident(g2,g3)
    c: Coincident(g3,g0)
    c: Horizontal(g0)
    c: Horizontal(g2)
    c: Vertical(g1)
    c: Vertical(g3)
    c: DistanceY(g2) = 1590
    c: DistanceX(g2) = 0.1
    c: DistanceX(g1) = -14
    c: DistanceY(g0) = 485
    c: DistanceY(g3,g3) = 1105
FEATURE [Part::Cylinder] Cylinder002  label="hole_7_mm_extrude"
  Angle = 360
  AttacherType = Attacher::AttachEngine3D
  FirstAngle = 0
  Height = 20
  Radius = 5.5
  SecondAngle = 0
FEATURE [Part::FeaturePython] Populate036  label="Populate led_holder_fix_array with hole_7_mm_extrude"  # WARN: FeaturePython — macro-defined, semantics opaque (R4)
  Copying = 0
  ExposePlacement = false
  MarkerShape = 1
  MarkerSize = 0
  NumElements = 0
  Object = -> Cylinder002
  OutputCompounding = 1
  Placement = pos=(0,11.8848,1584) rot=(0.57735,0.57735,-0.57735;2.0944rad)
  PlacementsTo = -> LinearArray012
  Referencing = 0
  Type = lattice2PopulateCopies.LatticePopulateCopies
  isLattice = 0
FEATURE [Part::Compound] Compound060  label="led_holder_2_cut1"
  Links = -> [Populate036]
FEATURE [PartDesign::Pad] Pad029
  Direction = (0,-1,2e-16)
  Length = 3
  Length2 = 10
  Placement = pos=(0,0,0) rot=(1,0,0;1.5708rad)
  Profile = -> Sketch205
  ReferenceAxis = -> Sketch205 [N_Axis]
  Suppressed = false
  Type = 0
FEATURE [PartDesign::Boolean] Boolean020
  BaseFeature = -> Pad029
  Group = -> [Compound060]
  Suppressed = false
  Type = 1
  UsePlacement = false
FEATURE [Sketcher::SketchObject] Sketch206
  AttachmentSupport = -> [XZ_Plane096]
  ExternalGeometry = -> [Sketch205]
  FullyConstrained = true
  MapMode = 5
  Placement = pos=(0,0,0) rot=(1,0,0;1.5708rad)
  sketch-geometry (13):
    g0: LineSegment StartX=-14 StartY=1590 StartZ=0 EndX=-6.95 EndY=1570 EndZ=0
    g1: LineSegment StartX=-6.95 StartY=1570 StartZ=0 EndX=0.1 EndY=1590 EndZ=0
    g2: LineSegment StartX=-14 StartY=485 StartZ=0 EndX=-6.95 EndY=505 EndZ=0
    g3: LineSegment StartX=-6.95 StartY=505 StartZ=0 EndX=0.1 EndY=485 EndZ=0
    g4: Circle CenterX=-6.95 CenterY=1570 CenterZ=0 NormalX=0 NormalY=0 NormalZ=1 AngleXU=0 Radius=1.7
    g5: Circle CenterX=-6.95 CenterY=1057.5 CenterZ=0 NormalX=0 NormalY=0 NormalZ=1 AngleXU=0 Radius=1.7
    g6: Circle CenterX=-6.95 CenterY=505 CenterZ=0 NormalX=0 NormalY=0 NormalZ=1 AngleXU=0 Radius=1.7
    g7: Circle CenterX=-6.95 CenterY=786.25 CenterZ=0 NormalX=0 NormalY=0 NormalZ=1 AngleXU=0 Radius=1.7
    g8: Circle CenterX=-6.95 CenterY=1288.75 CenterZ=0 NormalX=0 NormalY=0 NormalZ=1 AngleXU=0 Radius=1.7
    g9: LineSegment StartX=-6.95 StartY=505 StartZ=0 EndX=-6.95 EndY=771.25 EndZ=0
    g10: LineSegment StartX=-6.95 StartY=771.25 StartZ=0 EndX=-6.95 EndY=1037.5 EndZ=0
    g11: LineSegment StartX=-6.95 StartY=1037.5 StartZ=0 EndX=-6.95 EndY=1303.75 EndZ=0
    g12: LineSegment StartX=-6.95 StartY=1303.75 StartZ=0 EndX=-6.95 EndY=1570 EndZ=0
  constraints (34):
    c: Coincident(g-4,g0)
    c: Coincident(g0,g1)
    c: Coincident(g1,g-4)
    c: Coincident(g-3,g2)
    c: Coincident(g2,g3)
    c: Coincident(g3,g-3)
    c: Equal(g2,g3)
    c: Equal(g3,g0)
    c: Equal(g0,g1)
    c: DistanceY(g2,g2) = 20
    c: Coincident(g9,g2)
    c: Coincident(g11,g10)
    c: Coincident(g12,g0)
    c: Coincident(g4,g0)
    c: Coincident(g6,g2)
    c: Equal(g6,g5)
    c: Equal(g6,g4)
    c: Diameter(g6) = 3.4
    c: DistanceY(g10,g5) = 20
    c: Equal(g8,g7)
    c: Equal(g7,g6)
    c: Coincident(g9,g10)
    c: Vertical(g9)
    c: Vertical(g10)
    c: PointOnObject(g7,g9)
    c: Equal(g9,g10)
    c: Coincident(g11,g12)
    c: PointOnObject(g5,g11)
    c: PointOnObject(g8,g11)
    c: Equal(g11,g12)
    c: Equal(g10,g11)
    c: DistanceY(g8,g11) = 15
    c: DistanceY(g9,g7) = 15
    c: Vertical(g11)
FEATURE [PartDesign::Pocket] Pocket123
  BaseFeature = -> Boolean020
  Direction = (0,1,2e-16)
  Length = 5
  Length2 = 5
  Midplane = true
  Profile = -> Sketch206
  ReferenceAxis = -> Sketch206 [N_Axis]
  Suppressed = false
  Type = 1
FEATURE [PartDesign::Body] Body120  label="led_holder2"
  Group = -> [Sketch205,Pad029,Boolean020,Sketch206,Pocket123]
  Origin = -> Origin096
  Placement = pos=(0,3.2,0) rot=(0,0,1;3.14159rad)
  Tip = -> Pocket123
FEATURE [Sketcher::SketchObject] Sketch207  label="sector_plexiglass_sketch"
  FullyConstrained = true
  expr: .Constraints.offset = <<plexiglass_bottom_fix_extrude>>.Placement.Base.y + <<plexiglass_bottom_fix_sketch>>.Constraints.width / 2
  expr: Constraints[3] = <<Properties>>.endface_width / 2
  sketch-geometry (5):
    g0: ArcOfCircle CenterX=0 CenterY=549.544 CenterZ=0 NormalX=0 NormalY=0 NormalZ=1 AngleXU=0 Radius=784.544 StartAngle=4.71239 EndAngle=5.08305
    g1: LineSegment StartX=-7.25 StartY=-12.5574 StartZ=0 EndX=285.12 EndY=-181.357 EndZ=0
    g2: LineSegment StartX=-7.25 StartY=-12.5574 StartZ=0 EndX=0 EndY=0 EndZ=0
    g3: LineSegment StartX=284.188 StartY=-181.72 StartZ=0 EndX=295.373 EndY=-177.373 EndZ=0
    g4: LineSegment StartX=295.373 StartY=-177.373 StartZ=0 EndX=751.783 EndY=0 EndZ=0
  constraints (17):
    c: PointOnObject(g0,g-2)
    c: PointOnObject(g0,g-2)
    c: Angle(g1) = -0.523599
    c: Distance(g-1,g1) = 14.5
    c: Coincident(g2,g1)
    c: Coincident(g2,g-1)
    c: Perpendicular(g2,g1)
    c: Distance(g1) = 337.6  'offset'
    c: PointOnObject(g4,g-1)
    c: Coincident(g3,g4)
    c: Parallel(g3,g4)
    c: Tangent(g3,g0) = -1.5708
    c: Distance(g3) = 12
    c: PointOnObject(g1,g3)
    c: Distance(g0,g1) = 1
    c: Angle(g4) = 0.370663
    c: DistanceY(g0) = -235
FEATURE [Part::Mirroring] Part__Mirroring030  label="sector_plexiglass_sketch (Mirror #31)"
  Base = (0,0,0)
  Normal = (1,0,0)
  Source = -> Sketch207
FEATURE [Part::Compound] Compound061
  Links = -> [Sketch207,Part__Mirroring030]
FEATURE [PartDesign::SubShapeBinder] Binder128
  BindCopyOnChange = 0
  BindMode = 0
  ClaimChildren = true
  Context = -> Body121 [Binder128.]
  Fuse = false
  MakeFace = true
  OffsetFill = false
  OffsetIntersection = false
  OffsetJoinType = 0
  OffsetOpenResult = false
  PartialLoad = false
  Relative = false
  Support = -> [Compound061]
  _Version = 2
FEATURE [PartDesign::FeaturePython] BaseBend049  label="sector_plexiglass_BaseBend"  # WARN: FeaturePython — macro-defined, semantics opaque (R4)
  BendSide = 1
  BendSketch = -> Binder128
  MidPlane = false
  Reverse = false
  Suppressed = false
  length = 425
  radius = 1
  thickness = 1
FEATURE [PartDesign::CoordinateSystem] Local_CS004
  AttacherType = Attacher::AttachEngine3D
  AttachmentOffset = pos=(0,0,0) rot=(0,-1,0;1.5708rad)
  AttachmentSupport = -> [Binder128]
  MapMode = 7
  Placement = pos=(284.188,-181.72,0) rot=(0.131421,-0.700974,-0.700974;2.88025rad)
FEATURE [Sketcher::SketchObject] Sketch208
  AttachmentSupport = -> [Local_CS004]
  FullyConstrained = true
  MapMode = 5
  Placement = pos=(284.188,-181.72,0) rot=(-0.131421,0.700974,0.700974;3.40294rad)
  expr: Constraints[4] = <<plexiglass_bottom_fix_array>>.Step * 1 mm - <<plexiglass_bottom_fix_sketch>>.Constraints.length + 2 mm
  expr: Constraints[6] = <<plexiglass_bottom_fix_array>>.SpanStart - <<plexiglass_bottom_fix_array>>.Step * 1 mm / 2
  sketch-geometry (7):
    g0: LineSegment StartX=-12 StartY=-63.3333 StartZ=0 EndX=-12 EndY=15 EndZ=0
    g1: LineSegment StartX=-1 StartY=10 StartZ=0 EndX=-1 EndY=-58.3333 EndZ=0
    g2: GeomPoint X=-1 Y=-24.1667 Z=0
    g3: LineSegment StartX=-7 StartY=10 StartZ=0 EndX=-1 EndY=10 EndZ=0
    g4: LineSegment StartX=-1 StartY=-58.3333 StartZ=0 EndX=-7 EndY=-58.3333 EndZ=0
    g5: ArcOfCircle CenterX=-7 CenterY=15 CenterZ=0 NormalX=0 NormalY=0 NormalZ=1 AngleXU=0 Radius=5 StartAngle=3.14159 EndAngle=4.71239
    g6: ArcOfCircle CenterX=-7 CenterY=-63.3333 CenterZ=0 NormalX=0 NormalY=0 NormalZ=1 AngleXU=0 Radius=5 StartAngle=1.5708 EndAngle=3.14159
  constraints (17):
    c: Coincident(g3,g1)
    c: Coincident(g1,g4)
    c: Vertical(g0)
    c: Vertical(g1)
    c: DistanceY(g1,g1) = 68.3333
    c: Symmetric(g4,g3,g2)
    c: DistanceY(g2) = -24.1667
    c: Horizontal(g3)
    c: Horizontal(g4)
    c: Tangent(g5,g3) = -1.5708
    c: Tangent(g5,g0) = 1.5708
    c: Tangent(g6,g4) = -1.5708
    c: Tangent(g6,g0) = 1.5708
    c: Equal(g6,g5)
    c: Radius(g6) = 5
    c: Distance(g-1,g0) = 12
    c: Distance(g-1,g1) = 1
FEATURE [PartDesign::Pocket] Pocket124
  BaseFeature = -> BaseBend049
  Direction = (0.362233,-0.932087,0)
  Length = 5
  Length2 = 5
  Midplane = true
  Profile = -> Sketch208
  ReferenceAxis = -> Sketch208 [N_Axis]
  Suppressed = false
  Type = 1
FEATURE [PartDesign::LinearPattern] LinearPattern
  Direction = -> Z_Axis097
  Length = 591.667
  Mode = 1
  Occurrences = 6
  Offset = 118.333
  Suppressed = false
  expr: Length = <<plexiglass_bottom_fix_array>>.Step
  expr: Offset = <<plexiglass_bottom_fix_array>>.Step
FEATURE [PartDesign::Mirrored] Mirrored015
  MirrorPlane = -> YZ_Plane097
  Suppressed = false
FEATURE [PartDesign::MultiTransform] MultiTransform001
  BaseFeature = -> Pocket124
  Originals = -> [Pocket124]
  Suppressed = false
  Transformations = -> [LinearPattern,Mirrored015]
FEATURE [App::Link] Link039  label="top_fix_holes"
  LinkedObject = -> <external hub2108.FCStd>#Sketch
FEATURE [App::Link] Link040  label="top_center_hole"
  LinkedObject = -> <external hub2108.FCStd>#Sketch001
FEATURE [PartDesign::SubShapeBinder] Binder129
  BindCopyOnChange = 0
  BindMode = 0
  ClaimChildren = false
  Context = -> Link028 [Binder129.]
  Fuse = false
  MakeFace = true
  OffsetFill = false
  OffsetIntersection = false
  OffsetJoinType = 0
  OffsetOpenResult = false
  PartialLoad = false
  Relative = true
  Support = -> [Link005[Hole.Binder001.]]
  _Version = 2
FEATURE [PartDesign::SubShapeBinder] Binder130  label="U-fix_bottom_holes"
  BindCopyOnChange = 0
  BindMode = 0
  ClaimChildren = false
  Fuse = false
  MakeFace = true
  OffsetFill = false
  OffsetIntersection = false
  OffsetJoinType = 0
  OffsetOpenResult = false
  PartialLoad = false
  Placement = pos=(0,0,0) rot=(0,0,1;1.5708rad)
  Relative = false
  Support = -> [<external U-fix.FCStd>#Sketch002]
  _Version = 2
  expr: Support = <<U-fix>>#<<holes_bottom>>._self
FEATURE [Part::Extrusion] Extrude027  label="U-fix_bottom_holes_extrude"
  Base = -> Binder130
  Dir = (0,0,1)
  DirMode = 2
  FaceMakerClass = Part::FaceMakerBullseye
  LengthFwd = 20
  LengthRev = 0
  Solid = false
  Symmetric = false
FEATURE [Part::FeaturePython] PolarArray005  label="U-fix_bottom_array"  # WARN: FeaturePython — macro-defined, semantics opaque (R4)
  Alignment = 0
  AttacherType = Attacher::AttachEngine3D
  CellStart = A1
  Count = 3
  DistributionLaw = 0
  EndInclusive = false
  ExposePlacement = false
  FlipX = false
  FlipZ = false
  GeneratorMode = 0
  MarkerShape = 1
  MarkerSize = 0
  NumElements = 3
  OrientMode = 2
  Placement = pos=(0,0,0) rot=(0,0,1;1.5708rad)
  Radius = 294.4
  Reverse = false
  SpanEnd = 360
  SpanStart = 0
  Step = 120
  Type = lattice2PolarArray2.PolarArray
  UseArcRadius = false
  UseArcRange = 0
  VSGVersion = 1
  Values = 0.0 | 120.0 | 240.0
  ValuesSource = 2
  isLattice = 1
  expr: Radius = <<U-fix_vert_holes_extrude>>.Placement.Base.y
FEATURE [Part::FeaturePython] Populate037  label="Populate U-fix_bottom_array with U-fix_bottom_holes_extrude"  # WARN: FeaturePython — macro-defined, semantics opaque (R4)
  Copying = 0
  ExposePlacement = false
  MarkerShape = 1
  MarkerSize = 0
  NumElements = 0
  Object = -> Extrude027
  OutputCompounding = 1
  PlacementsTo = -> PolarArray005
  Referencing = 0
  Type = lattice2PopulateCopies.LatticePopulateCopies
  isLattice = 0
FEATURE [Sketcher::SketchObject] Sketch209  label="basin_stop_sketch"
  FullyConstrained = true
  sketch-geometry (5):
    g0: ArcOfCircle CenterX=152.272 CenterY=-105.063 CenterZ=0 NormalX=0 NormalY=0 NormalZ=1 AngleXU=0 Radius=15 StartAngle=1.20141 EndAngle=2.53763
    g1: ArcOfCircle CenterX=156.785 CenterY=-93.4065 CenterZ=0 NormalX=0 NormalY=0 NormalZ=1 AngleXU=0 Radius=2.5 StartAngle=5.74589 EndAngle=7.48459
    g2: ArcOfCircle CenterX=0 CenterY=0 CenterZ=0 NormalX=0 NormalY=0 NormalZ=1 AngleXU=0 Radius=170 StartAngle=4.71239 EndAngle=5.67922
    g3: ArcOfCircle CenterX=0 CenterY=0 CenterZ=0 NormalX=0 NormalY=0 NormalZ=1 AngleXU=0 Radius=185 StartAngle=4.71239 EndAngle=5.74589
    g4: LineSegment StartX=0 StartY=0 StartZ=0 EndX=158.035 EndY=-91.2414 EndZ=0
  constraints (14):
    c: PointOnObject(g2,g-2)
    c: PointOnObject(g3,g-2)
    c: DistanceY(g3) = -185
    c: DistanceY(g2) = -170
    c: Radius(g1) = 2.5
    c: Tangent(g2,g0) = 1.5708
    c: Tangent(g3,g1) = -1.5708
    c: Tangent(g0,g1) = -1.5708
    c: PointOnObject(g0,g3)
    c: Coincident(g3,g2)
    c: Coincident(g2,g-1)
    c: Coincident(g4,g2)
    c: Tangent(g4,g1) = 1.5708
    c: Angle(g4) = -0.523599
FEATURE [Part::Mirroring] Part__Mirroring031  label="basin_stop_sketch (Mirror #32)"
  Base = (0,0,0)
  Normal = (1,0,0)
  Source = -> Sketch209
FEATURE [Part::Compound] Compound064
  Links = -> [Part__Mirroring031,Sketch209]
FEATURE [PartDesign::SubShapeBinder] Binder131
  BindCopyOnChange = 0
  BindMode = 0
  ClaimChildren = true
  Fuse = false
  MakeFace = true
  OffsetFill = false
  OffsetIntersection = false
  OffsetJoinType = 0
  OffsetOpenResult = false
  PartialLoad = false
  Placement = pos=(0,0,0) rot=(0,0,1;3.14159rad)
  Relative = false
  Support = -> [Compound064]
  _Version = 2
FEATURE [PartDesign::Pad] Pad030
  Direction = (0,0,1)
  Length = 3
  Length2 = 10
  Placement = pos=(0,0,0) rot=(0,0,1;3.14159rad)
  Profile = -> Binder131
  Refine = true
  Suppressed = false
  Type = 0
FEATURE [Sketcher::SketchObject] Sketch210
  ExternalGeometry = -> [Sketch209]
  FullyConstrained = false
  sketch-geometry (4):
    g0: LineSegment StartX=51.5032 StartY=-169.937 StartZ=0 EndX=56.2455 EndY=-168.353 EndZ=0
    g1: LineSegment StartX=56.2455 StartY=-168.353 StartZ=0 EndX=49.908 EndY=-149.384 EndZ=0
    g2: LineSegment StartX=143.621 StartY=-105.272 StartZ=0 EndX=146.462 EndY=-101.158 EndZ=0
    g3: LineSegment StartX=146.462 StartY=-101.158 StartZ=0 EndX=130.006 EndY=-89.7916 EndZ=0
  constraints (12):
    c: Coincident(g1,g0)
    c: Coincident(g3,g2)
    c: Perpendicular(g1,g0)
    c: Perpendicular(g3,g2)
    c: Equal(g0,g2)
    c: Equal(g1,g3)
    c: Distance(g0) = 5
    c: Distance(g1) = 20
    c: DistanceX(g0) = 56.2455
    c: DistanceY(g0) = -168.353
    c: DistanceX(g2) = 146.462
    c: DistanceY(g2) = -101.158
FEATURE [Part::FeaturePython] Placment024  # WARN: FeaturePython — macro-defined, semantics opaque (R4)
  AttacherType = Attacher::AttachEngine3D
  AttachmentOffset = pos=(0,0,0) rot=(0,0,1;1.5708rad)
  AttachmentSupport = -> [Sketch210]
  ExposePlacement = true
  MapMode = 49
  MarkerShape = 1
  MarkerSize = 10
  NumElements = 1
  Placement = pos=(56.2455,-168.353,0) rot=(0,0,1;1.89323rad)
  Type = lattice2AttachablePlacement.AttachablePlacement
  isLattice = 1
FEATURE [Part::FeaturePython] PlacementSubsequence  # WARN: FeaturePython — macro-defined, semantics opaque (R4)
  Base = -> Placment024
  CycleMode = 0
  ExposePlacement = false
  MarkerShape = 1
  MarkerSize = 0
  NumElements = 2
  Type = lattice2AttachablePlacement.AttachedPlacementSubsequence
  isLattice = 1
FEATURE [Part::FeaturePython] Mirror010  label="Mirror010 of PlacementSubsequence"  # WARN: FeaturePython — macro-defined, semantics opaque (R4)
  ExposePlacement = false
  FlipX = true
  FlipY = false
  FlipZ = false
  MarkerShape = 1
  MarkerSize = 0
  NumElements = 2
  Object = -> PlacementSubsequence
  ObjectTraversal = 0
  Type = lattice2Mirror.LatticeMirror
  isLattice = 1
FEATURE [Part::FeaturePython] Join009  label="basin_limiter_placements"  # WARN: FeaturePython — macro-defined, semantics opaque (R4)
  ExposePlacement = false
  Interleave = false
  Links = -> [Mirror010,PlacementSubsequence]
  MarkerShape = 1
  MarkerSize = 0
  NumElements = 4
  Type = lattice2JoinArrays.JoinArrays
  isLattice = 1
FEATURE [Part::FeaturePython] Populate038  label="Populate basin_limiter_placements with hole_3.4mm_extrude"  # WARN: FeaturePython — macro-defined, semantics opaque (R4)
  Copying = 0
  ExposePlacement = false
  MarkerShape = 1
  MarkerSize = 0
  NumElements = 0
  Object = -> Extrude019
  OutputCompounding = 1
  Placement = pos=(0,0,0) rot=(0,0,1;3.14159rad)
  PlacementsTo = -> Join009
  Referencing = 0
  Type = lattice2PopulateCopies.LatticePopulateCopies
  isLattice = 0
FEATURE [Part::Compound] Compound063  label="basement_proxy_cut1"
  Links = -> [Populate037,Populate038]
FEATURE [PartDesign::Boolean] Boolean021
  BaseFeature = -> Pad003
  Group = -> [Compound063]
  Suppressed = false
  Type = 1
  UsePlacement = false
FEATURE [Part::Compound] Compound065  label="basin_limiter_cut1"
  Links = -> [Populate038]
FEATURE [PartDesign::Boolean] Boolean022
  BaseFeature = -> Pad030
  Group = -> [Compound065]
  Refine = true
  Suppressed = false
  Type = 1
  UsePlacement = false
FEATURE [PartDesign::SubShapeBinder] Binder132
  BindCopyOnChange = 0
  BindMode = 0
  ClaimChildren = true
  Fuse = false
  MakeFace = true
  OffsetFill = false
  OffsetIntersection = false
  OffsetJoinType = 0
  OffsetOpenResult = false
  PartialLoad = false
  Relative = false
  Support = -> [Sketch017]
  _Version = 2
FEATURE [PartDesign::SubShapeBinder] Binder133
  BindCopyOnChange = 0
  BindMode = 0
  ClaimChildren = true
  Context = -> Body122 [Binder133.]
  Fuse = false
  MakeFace = true
  OffsetFill = false
  OffsetIntersection = false
  OffsetJoinType = 0
  OffsetOpenResult = false
  PartialLoad = false
  Relative = true
  Support = -> [Sketch210]
  _Version = 2
FEATURE [PartDesign::Body] Body122  label="basin_limiter"
  Group = -> [Binder131,Pad030,Boolean022,Binder133]
  Origin = -> Origin098
  Placement = pos=(0,0,21) rot=(0,0,1;0rad)
  Tip = -> Boolean022
FEATURE [PartDesign::Pocket] Pocket125
  BaseFeature = -> Pocket002
  Direction = (0,0,-1)
  Length = 5
  Length2 = 5
  Midplane = true
  Profile = -> Binder014
  Suppressed = false
  Type = 1
FEATURE [PartDesign::Pocket] Pocket003
  BaseFeature = -> Pocket125
  Direction = (0,0,-1)
  Length = 5
  Length2 = 5
  Midplane = true
  Profile = -> Sketch020
  ReferenceAxis = -> Sketch020 [N_Axis]
  Suppressed = false
  Type = 1
FEATURE [PartDesign::Mirrored] Mirrored
  BaseFeature = -> Pocket003
  MirrorPlane = -> YZ_Plane005
  Suppressed = false
FEATURE [PartDesign::Pocket] Pocket005
  BaseFeature = -> Mirrored
  Direction = (-1,0,0)
  Length = 5
  Length2 = 5
  Midplane = true
  Profile = -> WireFilter002
  Suppressed = false
  Type = 1
FEATURE [Part::Extrusion] Extrude028
  Base = -> Populate017
  Dir = (0,0,1)
  DirMode = 2
  FaceMakerClass = Part::FaceMakerBullseye
  LengthFwd = 10
  LengthRev = 0
  Placement = pos=(0,10,1586) rot=(0.57735,0.57735,-0.57735;2.0944rad)
  Solid = true
  Symmetric = false
  expr: Placement = <<Extrude022>>.Placement
FEATURE [Part::Compound] Compound052  label="pillar2_cut1"
  Links = -> [Populate030,Extrude022,Extrude028]
FEATURE [PartDesign::Boolean] Boolean016
  BaseFeature = -> Mirrored013
  Group = -> [Compound052]
  Refine = true
  Suppressed = false
  Type = 1
  UsePlacement = false
FEATURE [PartDesign::Body] Body112  label="pillar2_material_0.50ansi"
  Group = -> [Sketch186,BaseBend045,Sketch187,Sketch188,Pad024,Pad025,Sketch189,Pocket115,Sketch190,Pocket116,DatumPlane006,Mirrored013,Boolean016]
  Origin = -> Origin086
  Tip = -> Boolean016
FEATURE [App::Part] Part019  label="pillar2"
  Group = -> [Body111,Body112,Spreadsheet003,Spreadsheet004,Part__Mirroring026]
  Origin = -> Origin084
  Placement = pos=(0,384,0) rot=(0,0,1;3.14159rad)
FEATURE [Sketcher::SketchObject] Sketch213
  AttachmentOffset = pos=(0,0,3) rot=(0,0,1;0rad)
  AttachmentSupport = -> [XY_Plane095]
  FullyConstrained = false
  MapMode = 5
  Placement = pos=(0,0,3) rot=(0,0,1;0rad)
  sketch-geometry (4):
    g0: LineSegment StartX=-416.278 StartY=-313.21 StartZ=0 EndX=489.891 EndY=-313.21 EndZ=0
    g1: LineSegment StartX=489.891 StartY=-313.21 StartZ=0 EndX=489.891 EndY=399.547 EndZ=0
    g2: LineSegment StartX=489.891 StartY=399.547 StartZ=0 EndX=-416.278 EndY=399.547 EndZ=0
    g3: LineSegment StartX=-416.278 StartY=399.547 StartZ=0 EndX=-416.278 EndY=-313.21 EndZ=0
  constraints (8):
    c: Coincident(g0,g1)
    c: Coincident(g1,g2)
    c: Coincident(g2,g3)
    c: Coincident(g3,g0)
    c: Horizontal(g0)
    c: Horizontal(g2)
    c: Vertical(g1)
    c: Vertical(g3)
FEATURE [Part::FeaturePython] Connect003  # WARN: FeaturePython — macro-defined, semantics opaque (R4)
  Objects = -> [Array011]
  Tolerance = 0
FEATURE [PartDesign::Pad] Pad031
  BaseFeature = -> BaseBend048
  Direction = (0,0,1)
  Length = 10
  Length2 = 10
  Profile = -> Binder127
  Refine = true
  Suppressed = false
  Type = 0
FEATURE [PartDesign::Pocket] Pocket126
  BaseFeature = -> Pad031
  Direction = (0,0,-1)
  Length = 5
  Length2 = 5
  Profile = -> Sketch213
  ReferenceAxis = -> Sketch213 [N_Axis]
  Refine = true
  Reversed = true
  Suppressed = false
  Type = 1
FEATURE [PartDesign::FeaturePython] Bend028  # WARN: FeaturePython — macro-defined, semantics opaque (R4)
  AutoMiter = true
  BaseFeature = -> Pocket126
  BendType = 0
  LengthList = [10]
  LengthSpec = 0
  ReliefFactor = 0.7
  Suppressed = false
  UseReliefFactor = false
  angle = 90
  baseObject = -> Pocket126 [Edge4]
  bendAList = [90]
  extend1 = 0
  extend2 = 0
  gap1 = 0
  gap2 = 0
  invert = false
  kfactor = 0.5
  length = 10
  maxExtendDist = 5
  minGap = 0.1
  minReliefGap = 1
  miterangle1 = 0
  miterangle2 = 0
  offset = 0
  radius = 1
  reliefType = 0
  reliefd = 1
  reliefw = 0.8
  sketchflip = false
  sketchinvert = false
  unfold = false
  expr: baseObject = tuple(<<Pocket126>>._self; list(<<Edge4>>))
  expr: radius = BaseBend048.radius
FEATURE [PartDesign::FeatureAdditivePython] PDW_Add001  # link proxy (typed FeaturePython)
  BaseFeature = -> Bend028
  Body = Body119
  ClaimChildren = false
  EditPlacementAdjustments = false
  Enabled = 1
  LinkedObject = -> Bend028
  MeshTolerance = 0.1
  PatternBaseOffset = 0
  PatternBaseScale = 1
  PatternBaseScaleXYZ = (1,1,1)
  PatternOffsetCut = false
  PatternOffsetIntersection = false
  PatternOffsetJoin = 0
  PatternOffsetMode = 0
  PatternOffsetSelfIntersection = false
  PatternOperation = 4
  PatternOperationDefault = None
  PatternScaleCut = false
  PatternShapeOffset = 0
  PatternShapeScale = 1
  PatternShapeScaleXYZ = (1,1,1)
  PatternTool = -> Bend028
  PatternToolOffset = 0
  PatternToolScale = 1
  PatternToolScaleXYZ = (1,1,1)
  RefineMesh = true
  ShapeManagement = 1
  ShowMeshProps = false
  ShowOffsetProps = false
  ShowScaleProps = false
  ShowWarnings = true
  Suppressed = false
  TipBaseOffset = 0
  TipBaseScale = 1
  TipBaseScaleXYZ = (1,1,1)
  TipOffsetCut = false
  TipOffsetIntersection = false
  TipOffsetJoin = 0
  TipOffsetMode = 0
  TipOffsetSelfIntersection = false
  TipOperation = 0
  TipOperationDefault = Fuse
  TipScaleCut = false
  TipShapeOffset = 0
  TipShapeScale = 1
  TipShapeScaleXYZ = (1,1,1)
  TipTool = -> Bend028
  TipToolOffset = 0
  TipToolScale = 1
  TipToolScaleXYZ = (1,1,1)
  Type = Additive
  UsePatternBaseAddSubShape = false
  UsePatternToolAddSubShape = true
  UseTipBaseAddSubShape = false
  UseTipToolAddSubShape = true
  Version = 0.2023.08.13
FEATURE [PartDesign::PolarPattern] PolarPattern010
  Angle = 360
  Axis = -> Z_Axis095
  BaseFeature = -> PDW_Add001
  Mode = 0
  Occurrences = 3
  Offset = 120
  Originals = -> [PDW_Add001]
  Suppressed = false
FEATURE [Part::Compound] Compound068  label="basement_v3_bottom_cut1"
  Links = -> [Populate033,Populate028]
FEATURE [Sketcher::SketchObject] Sketch214
  AttachmentOffset = pos=(0,0,1) rot=(0,0,1;0rad)
  AttachmentSupport = -> [XY_Plane094]
  FullyConstrained = false
  MapMode = 5
  Placement = pos=(0,0,1) rot=(0,0,1;0rad)
  expr: .AttachmentOffset.Base.z = <<BaseBend047>>.thickness
  sketch-geometry (4):
    g0: LineSegment StartX=-1342.32 StartY=-909.255 StartZ=0 EndX=1751.43 EndY=-909.255 EndZ=0
    g1: LineSegment StartX=1751.43 StartY=-909.255 StartZ=0 EndX=1751.43 EndY=1451 EndZ=0
    g2: LineSegment StartX=1751.43 StartY=1451 StartZ=0 EndX=-1342.32 EndY=1451 EndZ=0
    g3: LineSegment StartX=-1342.32 StartY=1451 StartZ=0 EndX=-1342.32 EndY=-909.255 EndZ=0
  constraints (8):
    c: Coincident(g0,g1)
    c: Coincident(g1,g2)
    c: Coincident(g2,g3)
    c: Coincident(g3,g0)
    c: Horizontal(g0)
    c: Horizontal(g2)
    c: Vertical(g1)
    c: Vertical(g3)
FEATURE [PartDesign::Pad] Pad032
  BaseFeature = -> BaseBend047
  Direction = (0,0,1)
  Length = 10
  Length2 = 10
  Profile = -> Sketch214
  ReferenceAxis = -> Sketch214 [N_Axis]
  Refine = true
  Suppressed = false
  Type = 0
FEATURE [PartDesign::Pocket] Pocket127
  BaseFeature = -> Pad032
  Direction = (0,0,-1)
  Length = 5
  Length2 = 5
  Profile = -> Sketch214
  ReferenceAxis = -> Sketch214 [N_Axis]
  Reversed = true
  Suppressed = false
  Type = 1
FEATURE [PartDesign::FeaturePython] Bend027  # WARN: FeaturePython — macro-defined, semantics opaque (R4)
  AutoMiter = true
  BaseFeature = -> Pocket127
  BendType = 0
  LengthList = [10]
  LengthSpec = 0
  ReliefFactor = 0.7
  Suppressed = false
  UseReliefFactor = false
  angle = 90
  baseObject = -> Pocket127 [Edge4]
  bendAList = [90]
  extend1 = 0
  extend2 = 0
  gap1 = 0
  gap2 = 0
  invert = false
  kfactor = 0.5
  length = 10
  maxExtendDist = 5
  minGap = 0.1
  minReliefGap = 1
  miterangle1 = 0
  miterangle2 = 0
  offset = 0
  radius = 1
  reliefType = 0
  reliefd = 1
  reliefw = 0.8
  sketchflip = false
  sketchinvert = false
  unfold = false
  expr: radius = BaseBend047.radius
FEATURE [PartDesign::FeatureAdditivePython] PDW_Common_Add003  # link proxy (typed FeaturePython)
  BaseFeature = -> Bend027
  Body = Body118
  ClaimChildren = false
  EditPlacementAdjustments = false
  Enabled = 1
  LinkedObject = -> Bend027
  MeshTolerance = 0.1
  PatternBase = -> BaseBend047
  PatternBaseOffset = 0
  PatternBaseScale = 1
  PatternBaseScaleXYZ = (1,1,1)
  PatternOffsetCut = false
  PatternOffsetIntersection = false
  PatternOffsetJoin = 0
  PatternOffsetMode = 0
  PatternOffsetSelfIntersection = false
  PatternOperation = 4
  PatternOperationDefault = Common
  PatternScaleCut = false
  PatternShapeOffset = 0
  PatternShapeScale = 1
  PatternShapeScaleXYZ = (1,1,1)
  PatternTool = -> Bend027
  PatternToolOffset = 0
  PatternToolScale = 1
  PatternToolScaleXYZ = (1,1,1)
  RefineMesh = true
  ShapeManagement = 1
  ShowMeshProps = false
  ShowOffsetProps = false
  ShowScaleProps = false
  ShowWarnings = true
  Suppressed = false
  TipBase = -> BaseBend047
  TipBaseOffset = 0
  TipBaseScale = 1
  TipBaseScaleXYZ = (1,1,1)
  TipOffsetCut = false
  TipOffsetIntersection = false
  TipOffsetJoin = 0
  TipOffsetMode = 0
  TipOffsetSelfIntersection = false
  TipOperation = 0
  TipOperationDefault = Common
  TipScaleCut = false
  TipShapeOffset = 0
  TipShapeScale = 1
  TipShapeScaleXYZ = (1,1,1)
  TipTool = -> Bend027
  TipToolOffset = 0
  TipToolScale = 1
  TipToolScaleXYZ = (1,1,1)
  Type = Additive
  UsePatternBaseAddSubShape = false
  UsePatternToolAddSubShape = true
  UseTipBaseAddSubShape = false
  UseTipToolAddSubShape = true
  Version = 0.2023.08.13
FEATURE [PartDesign::PolarPattern] PolarPattern009
  Angle = 360
  Axis = -> Z_Axis094
  BaseFeature = -> PDW_Common_Add003
  Mode = 0
  Occurrences = 3
  Offset = 120
  Originals = -> [PDW_Common_Add003]
  Suppressed = false
FEATURE [PartDesign::Boolean] Boolean025
  BaseFeature = -> PolarPattern009
  Group = -> [Compound068]
  Suppressed = false
  Type = 1
  UsePlacement = false
FEATURE [PartDesign::Body] Body118  label="basement_v3_bottom_material_0.50ansi"
  Group = -> [Binder126,BaseBend047,Sketch214,Pad032,Pocket127,Bend027,PDW_Common_Add003,PolarPattern009,Boolean025]
  Origin = -> Origin094
  Placement = pos=(0,0,-70) rot=(0,0,1;0rad)
  Tip = -> Pocket127
FEATURE [PartDesign::FeaturePython] Bend029  # WARN: FeaturePython — macro-defined, semantics opaque (R4)
  AutoMiter = true
  BaseFeature = -> BaseBend046
  BendType = 0
  LengthList = [20]
  LengthSpec = 1
  ReliefFactor = 0.7
  Suppressed = false
  UseReliefFactor = false
  angle = 90
  baseObject = -> BaseBend046 [Edge17]
  bendAList = [90]
  extend1 = 0
  extend2 = 0
  gap1 = 0
  gap2 = 0
  invert = false
  kfactor = 0.5
  length = 20
  maxExtendDist = 5
  minGap = 0.1
  minReliefGap = 1
  miterangle1 = 0
  miterangle2 = 0
  offset = 0
  radius = 2
  reliefType = 0
  reliefd = 1
  reliefw = 0.8
  sketchflip = false
  sketchinvert = false
  unfold = false
  expr: radius = BaseBend046.radius
FEATURE [PartDesign::Fillet] Fillet014
  Base = -> Bend029 [Edge39,Edge2,Edge8]
  BaseFeature = -> Bend029
  Radius = 2
  SupportTransform = false
  Suppressed = false
  UseAllEdges = false
FEATURE [PartDesign::Pocket] Pocket118
  BaseFeature = -> Fillet014
  Direction = (-0.5,0.866025,-1e-16)
  Length = 5
  Length2 = 5
  Midplane = true
  Profile = -> Sketch193
  ReferenceAxis = -> Sketch193 [N_Axis]
  Suppressed = false
  Type = 1
FEATURE [PartDesign::Mirrored] Mirrored014
  BaseFeature = -> Pocket118
  MirrorPlane = -> YZ_Plane087
  Originals = -> [Pocket118]
  Suppressed = false
FEATURE [Part::FeaturePython] Placment025  # WARN: FeaturePython — macro-defined, semantics opaque (R4)
  AttacherType = Attacher::AttachEngine3D
  ExposePlacement = true
  MarkerShape = 1
  MarkerSize = 50
  NumElements = 1
  Placement = pos=(68.9742,55.7258,0) rot=(0,0,1;1.5708rad)
  Type = lattice2AttachablePlacement.AttachablePlacement
  isLattice = 1
FEATURE [Part::FeaturePython] Placment026  # WARN: FeaturePython — macro-defined, semantics opaque (R4)
  AttacherType = Attacher::AttachEngine3D
  ExposePlacement = true
  MarkerShape = 1
  MarkerSize = 5
  NumElements = 1
  Placement = pos=(56.173,140.207,0) rot=(0,0,1;1.5708rad)
  Type = lattice2AttachablePlacement.AttachablePlacement
  isLattice = 1
FEATURE [Part::FeaturePython] Placment027  # WARN: FeaturePython — macro-defined, semantics opaque (R4)
  AttacherType = Attacher::AttachEngine3D
  ExposePlacement = true
  MarkerShape = 1
  MarkerSize = 5
  NumElements = 1
  Placement = pos=(36,265,0) rot=(0,0,1;1.5708rad)
  Type = lattice2AttachablePlacement.AttachablePlacement
  isLattice = 1
FEATURE [Part::FeaturePython] Join011  # WARN: FeaturePython — macro-defined, semantics opaque (R4)
  ExposePlacement = false
  Interleave = false
  Links = -> [Placment025,Placment026,Placment027]
  MarkerShape = 1
  MarkerSize = 0
  NumElements = 3
  Type = lattice2JoinArrays.JoinArrays
  isLattice = 1
FEATURE [Part::FeaturePython] Mirror011  label="Mirror011 of Join011"  # WARN: FeaturePython — macro-defined, semantics opaque (R4)
  ExposePlacement = false
  FlipX = true
  FlipY = false
  FlipZ = false
  MarkerShape = 1
  MarkerSize = 0
  NumElements = 3
  Object = -> Join011
  ObjectTraversal = 0
  Type = lattice2Mirror.LatticeMirror
  isLattice = 1
FEATURE [Part::FeaturePython] Join012  # WARN: FeaturePython — macro-defined, semantics opaque (R4)
  ExposePlacement = false
  Interleave = false
  Links = -> [Mirror011,Join011]
  MarkerShape = 1
  MarkerSize = 0
  NumElements = 6
  Type = lattice2JoinArrays.JoinArrays
  isLattice = 1
FEATURE [Part::FeaturePython] PolarArray006  label="3_elem_polar_array"  # WARN: FeaturePython — macro-defined, semantics opaque (R4)
  Alignment = 0
  AttacherType = Attacher::AttachEngine3D
  CellStart = A1
  Count = 3
  DistributionLaw = 0
  EndInclusive = false
  ExposePlacement = false
  FlipX = false
  FlipZ = false
  GeneratorMode = 0
  MarkerShape = 1
  MarkerSize = 0
  NumElements = 3
  OrientMode = 2
  Radius = 100
  Reverse = false
  SpanEnd = 360
  SpanStart = 0
  Step = 120
  Type = lattice2PolarArray2.PolarArray
  UseArcRadius = false
  UseArcRange = 0
  VSGVersion = 1
  Values = 0.0 | 120.0 | 240.0
  ValuesSource = 2
  isLattice = 1
FEATURE [Part::FeaturePython] Populate039  label="Populate PolarArray006 with Join012"  # WARN: FeaturePython — macro-defined, semantics opaque (R4)
  Copying = 0
  ExposePlacement = false
  MarkerShape = 1
  MarkerSize = 0
  NumElements = 18
  Object = -> Join012
  OutputCompounding = 0
  PlacementsTo = -> PolarArray006
  Referencing = 1
  Type = lattice2PopulateCopies.LatticePopulateCopies
  isLattice = 1
FEATURE [Part::Cylinder] Cylinder003  label="hole_3.2mm_extrude"
  Angle = 360
  AttacherType = Attacher::AttachEngine3D
  FirstAngle = 0
  Height = 20
  Radius = 1.6
  SecondAngle = 0
FEATURE [Part::FeaturePython] Populate040  label="Populate Populate PolarArray006 with Join012 with hole_3.2mm_extrude"  # WARN: FeaturePython — macro-defined, semantics opaque (R4)
  Copying = 0
  ExposePlacement = false
  MarkerShape = 1
  MarkerSize = 0
  NumElements = 0
  Object = -> Cylinder003
  OutputCompounding = 1
  PlacementsTo = -> Populate039
  Referencing = 0
  Type = lattice2PopulateCopies.LatticePopulateCopies
  isLattice = 0
FEATURE [Part::FeaturePython] Populate041  label="Populate Populate PolarArray006 with Join012 with hole_5_mm_extrude"  # WARN: FeaturePython — macro-defined, semantics opaque (R4)
  Copying = 0
  ExposePlacement = false
  MarkerShape = 1
  MarkerSize = 0
  NumElements = 0
  Object = -> Extrude023
  OutputCompounding = 1
  PlacementsTo = -> Populate039
  Referencing = 0
  Type = lattice2PopulateCopies.LatticePopulateCopies
  isLattice = 0
FEATURE [Part::FeaturePython] Placment028  # WARN: FeaturePython — macro-defined, semantics opaque (R4)
  AttacherType = Attacher::AttachEngine3D
  ExposePlacement = true
  MapMode = 11
  MarkerShape = 1
  MarkerSize = 10
  NumElements = 1
  Placement = pos=(63.3907,55,0) rot=(0,0,1;1.5708rad)
  Type = lattice2AttachablePlacement.AttachablePlacement
  isLattice = 1
FEATURE [Part::FeaturePython] Placment029  # WARN: FeaturePython — macro-defined, semantics opaque (R4)
  AttacherType = Attacher::AttachEngine3D
  ExposePlacement = true
  MapMode = 11
  MarkerShape = 1
  MarkerSize = 10
  NumElements = 1
  Placement = pos=(43.3161,155,0) rot=(0,0,1;1.5708rad)
  Type = lattice2AttachablePlacement.AttachablePlacement
  isLattice = 1
FEATURE [Part::FeaturePython] Join013  # WARN: FeaturePython — macro-defined, semantics opaque (R4)
  ExposePlacement = false
  Interleave = false
  Links = -> [Placment028,Placment029]
  MarkerShape = 1
  MarkerSize = 0
  NumElements = 2
  Type = lattice2JoinArrays.JoinArrays
  isLattice = 1
FEATURE [Part::FeaturePython] Mirror012  label="Mirror012 of Join013"  # WARN: FeaturePython — macro-defined, semantics opaque (R4)
  ExposePlacement = false
  FlipX = true
  FlipY = false
  FlipZ = false
  MarkerShape = 1
  MarkerSize = 0
  NumElements = 2
  Object = -> Join013
  ObjectTraversal = 0
  Type = lattice2Mirror.LatticeMirror
  isLattice = 1
FEATURE [Part::FeaturePython] Join014  # WARN: FeaturePython — macro-defined, semantics opaque (R4)
  ExposePlacement = false
  Interleave = false
  Links = -> [Mirror012,Join013]
  MarkerShape = 1
  MarkerSize = 0
  NumElements = 4
  Type = lattice2JoinArrays.JoinArrays
  isLattice = 1
FEATURE [Part::FeaturePython] Populate042  label="Populate 3_elem_polar_array with Join014"  # WARN: FeaturePython — macro-defined, semantics opaque (R4)
  Copying = 0
  ExposePlacement = false
  MarkerShape = 1
  MarkerSize = 0
  NumElements = 12
  Object = -> Join014
  OutputCompounding = 0
  PlacementsTo = -> PolarArray006
  Referencing = 1
  Type = lattice2PopulateCopies.LatticePopulateCopies
  isLattice = 1
FEATURE [Part::FeaturePython] Populate043  label="Populate Populate 3_elem_polar_array with Join014 with hole_3.2_mm_extrude"  # WARN: FeaturePython — macro-defined, semantics opaque (R4)
  Copying = 0
  ExposePlacement = false
  MarkerShape = 1
  MarkerSize = 0
  NumElements = 0
  Object = -> Cylinder001
  OutputCompounding = 1
  PlacementsTo = -> Populate042
  Referencing = 0
  Type = lattice2PopulateCopies.LatticePopulateCopies
  isLattice = 0
FEATURE [Part::FeaturePython] Populate044  label="Populate Populate 3_elem_polar_array with Join014 with hole_5_mm_extrude"  # WARN: FeaturePython — macro-defined, semantics opaque (R4)
  Copying = 0
  ExposePlacement = false
  MarkerShape = 1
  MarkerSize = 0
  NumElements = 0
  Object = -> Extrude023
  OutputCompounding = 1
  PlacementsTo = -> Populate042
  Referencing = 0
  Type = lattice2PopulateCopies.LatticePopulateCopies
  isLattice = 0
FEATURE [Part::Compound] Compound070  label="basement_top_amplifier_cut1"
  Links = -> [Populate044]
FEATURE [PartDesign::Boolean] Boolean028
  BaseFeature = -> Pocket107
  Group = -> [Compound070]
  Suppressed = false
  Type = 1
  UsePlacement = false
FEATURE [PartDesign::SubShapeBinder] Binder134
  BindCopyOnChange = 0
  BindMode = 0
  ClaimChildren = false
  Context = -> Body009 [Binder134.]
  Fuse = false
  MakeFace = true
  OffsetFill = false
  OffsetIntersection = false
  OffsetJoinType = 0
  OffsetOpenResult = false
  PartialLoad = false
  Relative = true
  Support = -> [Body007[Pocket112.Sketch178.]]
  _Version = 2
FEATURE [App::Link] Link041  label="hub2108_bottom_fix"
  LinkedObject = -> <external hub2108.FCStd>#Sketch002
  expr: LinkedObject = <<hub2108>>#<<bottom_fix_holes>>._self
FEATURE [App::Link] Link042  label="hub2108_bottom_center"
  LinkedObject = -> <external hub2108.FCStd>#Sketch003
  expr: LinkedObject = <<hub2108>>#<<bottom_center_hole>>._self
FEATURE [Part::Extrusion] Extrude029  label="hub2108_bottom_fix_extrude"
  Base = -> Link041
  Dir = (0,0,1)
  DirMode = 2
  FaceMakerClass = Part::FaceMakerBullseye
  LengthFwd = 20
  LengthRev = 0
  Solid = true
  Symmetric = false
FEATURE [Part::Extrusion] Extrude030  label="hub2108_bottom_center_extrude"
  Base = -> Link042
  Dir = (0,0,1)
  DirMode = 2
  FaceMakerClass = Part::FaceMakerBullseye
  LengthFwd = 20
  LengthRev = 0
  Solid = true
  Symmetric = false
FEATURE [Sketcher::SketchObject] Sketch216
  AttachmentOffset = pos=(350,0,0) rot=(0,0,1;0rad)
  AttachmentSupport = -> [YZ_Plane010]
  FullyConstrained = true
  MapMode = 5
  Placement = pos=(0,350,0) rot=(0.57735,0.57735,0.57735;2.0944rad)
  sketch-geometry (3):
    g0: LineSegment StartX=0 StartY=15 StartZ=0 EndX=-15 EndY=0 EndZ=0
    g1: LineSegment StartX=-15 StartY=0 StartZ=0 EndX=0 EndY=0 EndZ=0
    g2: LineSegment StartX=0 StartY=15 StartZ=0 EndX=0 EndY=0 EndZ=0
  constraints (8):
    c: PointOnObject(g0,g-2)
    c: PointOnObject(g0,g-1)
    c: Coincident(g0,g1)
    c: Coincident(g1,g-1)
    c: Coincident(g2,g0)
    c: Coincident(g2,g1)
    c: Equal(g1,g2)
    c: DistanceY(g2,g2) = 15
FEATURE [PartDesign::SubtractivePipe] SubtractivePipe
  AuxilleryCurvelinear = true
  AuxillerySpineTangent = false
  BaseFeature = -> Pad001
  Binormal = (0,0,0)
  Mode = 0
  Profile = -> Sketch216
  Spine = -> Binder005 [Edge1,Edge2,Edge3,Edge4,Edge5,Edge6,Edge7,Edge8,Edge9,Edge10,Edge11,Edge12,Edge13,Edge14,Edge15,Edge16,Edge17,Edge18]
  SpineTangent = false
  Suppressed = false
  Transformation = 0
  Transition = 0
FEATURE [PartDesign::Pocket] Pocket062
  BaseFeature = -> SubtractivePipe
  Direction = (0,0,-1)
  Length = 5
  Length2 = 5
  Midplane = true
  Profile = -> Sketch113
  ReferenceAxis = -> Sketch113 [N_Axis]
  Suppressed = false
  Type = 1
FEATURE [Part::FeaturePython] PolarArray007  # WARN: FeaturePython — macro-defined, semantics opaque (R4)
  Alignment = 0
  AttacherType = Attacher::AttachEngine3D
  CellStart = A1
  Count = 3
  DistributionLaw = 0
  EndInclusive = false
  ExposePlacement = false
  FlipX = false
  FlipZ = false
  GeneratorMode = 0
  MarkerShape = 1
  MarkerSize = 0
  NumElements = 3
  OrientMode = 2
  Placement = pos=(0,0,0) rot=(0,0,1;1.5708rad)
  Radius = 370
  Reverse = false
  SpanEnd = 360
  SpanStart = 0
  Step = 120
  Type = lattice2PolarArray2.PolarArray
  UseArcRadius = false
  UseArcRange = 0
  VSGVersion = 1
  Values = 0.0 | 120.0 | 240.0
  ValuesSource = 2
  isLattice = 1
FEATURE [Part::Extrusion] Extrude031  label="hole_8mm_extrude"
  Base = -> Circle001
  Dir = (0,0,1)
  DirMode = 2
  FaceMakerClass = Part::FaceMakerBullseye
  LengthFwd = 20
  LengthRev = 0
  Solid = true
  Symmetric = false
FEATURE [Part::FeaturePython] Populate045  label="Populate PolarArray007 with hole_8mm_extrude"  # WARN: FeaturePython — macro-defined, semantics opaque (R4)
  Copying = 0
  ExposePlacement = false
  MarkerShape = 1
  MarkerSize = 0
  NumElements = 0
  Object = -> Extrude031
  OutputCompounding = 1
  PlacementsTo = -> PolarArray007
  Referencing = 0
  Type = lattice2PopulateCopies.LatticePopulateCopies
  isLattice = 0
FEATURE [Part::FeaturePython] Populate046  label="Populate Mirror009 of Join007 with hole_3.4mm_extrude"  # WARN: FeaturePython — macro-defined, semantics opaque (R4)
  Copying = 0
  ExposePlacement = false
  MarkerShape = 1
  MarkerSize = 0
  NumElements = 0
  Object = -> Extrude019
  OutputCompounding = 1
  PlacementsTo = -> Mirror009
  Referencing = 0
  Type = lattice2PopulateCopies.LatticePopulateCopies
  isLattice = 0
FEATURE [Part::Compound] Compound073
  Links = -> [Populate046]
  Placement = pos=(11.5,6.63953,1394) rot=(0,0,-1;1.0472rad)
  expr: .Placement.Base.x = Sketch.Constraints.connection_offset * cos(30) - 3 mm
  expr: .Placement.Base.y = Sketch.Constraints.connection_offset * sin(30) - 1.5 mm / sin(60)
  expr: .Placement.Base.z = <<Properties>>.total_height - 34 mm
FEATURE [Part::Mirroring] Part__Mirroring032  label="Compound073 (Mirror #32)"
  Base = (0,0,0)
  Normal = (1,0,0)
  Source = -> Compound073
FEATURE [Part::Compound] Compound074
  Links = -> [Part__Mirroring032,Compound073]
FEATURE [Part::Compound] Compound077  label="star_amplifier_cut1"
  Links = -> [Extrude003]
FEATURE [PartDesign::Boolean] Boolean004
  BaseFeature = -> Pocket026
  Group = -> [Compound077]
  Suppressed = false
  Type = 1
  UsePlacement = false
  expr: Group = <<star_amplifier_cut1>>._self
FEATURE [PartDesign::FeatureAdditivePython] PDW_Common_Add002  # link proxy (typed FeaturePython)
  BaseFeature = -> Boolean004
  Body = Body018
  ClaimChildren = false
  EditPlacementAdjustments = false
  Enabled = 1
  LinkedObject = -> Boolean004
  MeshTolerance = 0.1
  PatternBase = -> Pocket026
  PatternBaseOffset = 0
  PatternBaseScale = 1
  PatternBaseScaleXYZ = (1,1,1)
  PatternOffsetCut = false
  PatternOffsetIntersection = false
  PatternOffsetJoin = 0
  PatternOffsetMode = 0
  PatternOffsetSelfIntersection = false
  PatternOperation = 3
  PatternOperationDefault = Common
  PatternScaleCut = false
  PatternShapeOffset = 0
  PatternShapeScale = 1
  PatternShapeScaleXYZ = (1,1,1)
  PatternTool = -> Boolean004
  PatternToolOffset = 0
  PatternToolScale = 1
  PatternToolScaleXYZ = (1,1,1)
  RefineMesh = true
  ShapeManagement = 0
  ShowMeshProps = false
  ShowOffsetProps = false
  ShowScaleProps = false
  ShowWarnings = true
  Suppressed = false
  TipBase = -> Pocket026
  TipBaseOffset = 0
  TipBaseScale = 1
  TipBaseScaleXYZ = (1,1,1)
  TipOffsetCut = false
  TipOffsetIntersection = false
  TipOffsetJoin = 0
  TipOffsetMode = 0
  TipOffsetSelfIntersection = false
  TipOperation = 2
  TipOperationDefault = Common
  TipScaleCut = false
  TipShapeOffset = 0
  TipShapeScale = 1
  TipShapeScaleXYZ = (1,1,1)
  TipTool = -> Boolean004
  TipToolOffset = 0
  TipToolScale = 1
  TipToolScaleXYZ = (1,1,1)
  Type = Additive
  UsePatternBaseAddSubShape = false
  UsePatternToolAddSubShape = true
  UseTipBaseAddSubShape = false
  UseTipToolAddSubShape = true
  Version = 0.2023.08.13
FEATURE [PartDesign::PolarPattern] PolarPattern008
  Angle = 360
  Axis = -> Z_Axis025
  BaseFeature = -> PDW_Common_Add002
  Mode = 0
  Occurrences = 3
  Offset = 120
  Originals = -> [PDW_Common_Add002]
  Refine = true
  Suppressed = false
FEATURE [PartDesign::Body] Body018  label="star_material_0.30ansi"
  Group = -> [Sketch032,BaseBend010,Sketch033,Pocket018,Mirrored001,Sketch034,Pocket019,Sketch036,Pocket021,Sketch045,Pocket026,Boolean004,PDW_Common_Add002,PolarPattern008]
  Origin = -> Origin025
  Placement = pos=(0,0,1428) rot=(0,0,1;0rad)
  Tip = -> PolarPattern008
  expr: .Placement.Base.z = <<Properties>>.total_height
FEATURE [Part::Compound] Compound078  label="top_connector_cut1"
  Links = -> [Extrude006]
FEATURE [PartDesign::Boolean] Boolean007
  BaseFeature = -> Hole004
  Group = -> [Compound078]
  Suppressed = false
  Type = 1
  UsePlacement = false
  expr: Group = <<top_connector_cut1>>._self
FEATURE [PartDesign::Pocket] Pocket027
  BaseFeature = -> Boolean007
  Direction = (-1,0,0)
  Length = 5
  Length2 = 5
  Midplane = true
  Profile = -> Sketch048
  ReferenceAxis = -> Sketch048 [N_Axis]
  Suppressed = false
  Type = 1
FEATURE [PartDesign::Body] Body017  label="top_connector_material_0.30ansi"
  Group = -> [Sketch029,BaseBend009,Binder029,Binder030,Hole004,Boolean007,Sketch048,Pocket027]
  Origin = -> Origin024
  Tip = -> Pocket027
FEATURE [Sketcher::SketchObject] Sketch217
  AttachmentSupport = -> [XY_Plane023]
  ExternalGeometry = -> [Sketch024,Binder018]
  FullyConstrained = true
  MapMode = 5
  sketch-geometry (6):
    g0: LineSegment StartX=41.7 StartY=289.736 StartZ=0 EndX=14.25 EndY=348.472 EndZ=0
    g1: LineSegment StartX=0 StartY=348.472 StartZ=0 EndX=14.25 EndY=348.472 EndZ=0
    g2: LineSegment StartX=14.25 StartY=351.872 StartZ=0 EndX=14.25 EndY=348.472 EndZ=0
    g3: LineSegment StartX=14.25 StartY=348.472 StartZ=0 EndX=17.3302 EndY=349.911 EndZ=0
    g4: LineSegment StartX=0 StartY=348.472 StartZ=0 EndX=0 EndY=289.736 EndZ=0
    g5: LineSegment StartX=0 StartY=289.736 StartZ=0 EndX=41.7 EndY=289.736 EndZ=0
  constraints (17):
    c: Coincident(g0,g-3)
    c: PointOnObject(g1,g-2)
    c: Coincident(g1,g0)
    c: Horizontal(g1)
    c: Coincident(g2,g0)
    c: Coincident(g2,g3)
    c: PointOnObject(g3,g-4)
    c: Perpendicular(g0,g3)
    c: Perpendicular(g1,g2)
    c: Equal(g3,g2)
    c: DistanceY(g2,g2) = 3.4
    c: Horizontal(g2,g-4)
    c: Coincident(g4,g1)
    c: PointOnObject(g4,g-3)
    c: Vertical(g4)
    c: Coincident(g5,g4)
    c: Coincident(g5,g0)
FEATURE [PartDesign::Pad] Pad033
  BaseFeature = -> BaseBend008
  Direction = (0,0,1)
  Length = 0.3
  Length2 = 10
  Profile = -> Sketch217
  ReferenceAxis = -> Sketch217 [N_Axis]
  Suppressed = false
  Type = 0
FEATURE [PartDesign::Mirrored] Mirrored016
  BaseFeature = -> Pad033
  MirrorPlane = -> Sketch217 [V_Axis]
  Originals = -> [Pad033]
  Suppressed = false
FEATURE [PartDesign::Hole] Hole002
  BaseFeature = -> Mirrored016
  CustomThreadClearance = 0
  Depth = 25
  DepthType = 0
  Diameter = 3.4
  DrillForDepth = false
  DrillPoint = 1
  DrillPointAngle = 118
  HoleCutCountersinkAngle = 90
  HoleCutCustomValues = false
  HoleCutDepth = 0
  HoleCutDiameter = 6.1
  HoleCutType = 0
  ModelThread = false
  Profile = -> Binder019
  Refine = true
  Reversed = true
  Suppressed = false
  Tapered = false
  TaperedAngle = 90
  ThreadClass = 0
  ThreadDepth = 25
  ThreadDepthType = 0
  ThreadDirection = 0
  ThreadFit = 0
  ThreadSize = 0
  ThreadType = 0
  Threaded = false
  UseCustomThreadClearance = false
  expr: Diameter = <<Properties>>.rivet_d
FEATURE [PartDesign::Body] Body016  label="cap_inner2_material_0.30ansi"
  Group = -> [Binder018,Binder019,Sketch024,BaseBend008,Sketch217,Pad033,Mirrored016,Hole002]
  Origin = -> Origin023
  Tip = -> Hole002
FEATURE [Sketcher::SketchObject] Sketch218
  AttachmentOffset = pos=(0,0,18) rot=(0,0,1;0rad)
  AttachmentSupport = -> [XY_Plane011]
  FullyConstrained = false
  MapMode = 5
  Placement = pos=(0,0,18) rot=(0,0,1;0rad)
  sketch-geometry (4):
    g0: LineSegment StartX=93.4507 StartY=-44.023 StartZ=0 EndX=107.489 EndY=-44.023 EndZ=0
    g1: LineSegment StartX=107.489 StartY=-44.023 StartZ=0 EndX=107.489 EndY=-29.1068 EndZ=0
    g2: LineSegment StartX=107.489 StartY=-29.1068 StartZ=0 EndX=93.4507 EndY=-29.1068 EndZ=0
    g3: LineSegment StartX=93.4507 StartY=-29.1068 StartZ=0 EndX=93.4507 EndY=-44.023 EndZ=0
  constraints (8):
    c: Coincident(g0,g1)
    c: Coincident(g1,g2)
    c: Coincident(g2,g3)
    c: Coincident(g3,g0)
    c: Horizontal(g0)
    c: Horizontal(g2)
    c: Vertical(g1)
    c: Vertical(g3)
FEATURE [PartDesign::FeaturePython] Bend030  # WARN: FeaturePython — macro-defined, semantics opaque (R4)
  AutoMiter = true
  BaseFeature = -> Pocket022
  BendType = 0
  LengthList = [10]
  LengthSpec = 0
  ReliefFactor = 0.7
  Suppressed = false
  UseReliefFactor = false
  angle = 90
  baseObject = -> Pocket022 [Edge44,Edge42]
  bendAList = [90]
  extend1 = 0
  extend2 = 0
  gap1 = 0
  gap2 = 0
  invert = false
  kfactor = 0.5
  length = 10
  maxExtendDist = 5
  minGap = 0.1
  minReliefGap = 1
  miterangle1 = 0
  miterangle2 = 0
  offset = 0
  radius = 2
  reliefType = 0
  reliefd = 1
  reliefw = 0.8
  sketchflip = false
  sketchinvert = false
  unfold = true
  expr: radius = BaseBend011.radius
FEATURE [Sketcher::SketchObject] Sketch219
  AttachmentSupport = -> [Bend030]
  ExternalGeometry = -> [Bend030]
  FullyConstrained = true
  MapMode = 5
  Placement = pos=(0,-1.69e-14,1.483e-13) rot=(1,0,0;3.25479rad)
  sketch-geometry (6):
    g0: LineSegment StartX=297.803 StartY=-177.345 StartZ=0 EndX=303.917 EndY=-182.504 EndZ=0
    g1: LineSegment StartX=303.917 StartY=-182.504 StartZ=0 EndX=285.803 EndY=-203.969 EndZ=0
    g2: LineSegment StartX=285.803 StartY=-203.969 StartZ=0 EndX=276.608 EndY=-196.209 EndZ=0
    g3: LineSegment StartX=279.192 StartY=-196.205 StartZ=0 EndX=297.807 EndY=-180.398 EndZ=0
    g4: ArcOfCircle CenterX=296.513 CenterY=-178.873 CenterZ=0 NormalX=0 NormalY=0 NormalZ=1 AngleXU=0 Radius=2 StartAngle=5.41641 EndAngle=7.15307
    g5: ArcOfCircle CenterX=277.898 CenterY=-194.681 CenterZ=0 NormalX=0 NormalY=0 NormalZ=1 AngleXU=0 Radius=2 StartAngle=4.01147 EndAngle=5.41641
  constraints (15):
    c: Coincident(g0,g-3)
    c: Coincident(g0,g1)
    c: Coincident(g1,g-3)
    c: Coincident(g1,g2)
    c: Perpendicular(g1,g2)
    c: Perpendicular(g0,g1)
    c: Tangent(g4,g0) = 1.5708
    c: Tangent(g5,g2) = 1.5708
    c: Tangent(g5,g3) = -1.5708
    c: Tangent(g4,g3) = -1.5708
    c: Equal(g4,g5)
    c: Radius(g4) = 2
    c: Distance(g0) = 8
    c: Distance(g2) = 12.0319
    c: Distance(g3,g1) = 10.0593
FEATURE [PartDesign::Pocket] Pocket131
  BaseFeature = -> Bend030
  Direction = (0,-0.11295,0.993601)
  Length = 5
  Length2 = 5
  Profile = -> Sketch219
  ReferenceAxis = -> Sketch219 [N_Axis]
  Suppressed = false
  Type = 0
FEATURE [PartDesign::Mirrored] Mirrored017
  BaseFeature = -> Pocket131
  MirrorPlane = -> YZ_Plane028
  Originals = -> [Pocket131]
  Suppressed = false
FEATURE [PartDesign::Pocket] Pocket024
  BaseFeature = -> Mirrored017
  Direction = (0,0,-1)
  Length = 5
  Length2 = 5
  Midplane = true
  Profile = -> Sketch042
  ReferenceAxis = -> Sketch042 [N_Axis]
  Suppressed = false
  Type = 1
FEATURE [PartDesign::FeaturePython] CornerRelief  # WARN: FeaturePython — macro-defined, semantics opaque (R4)
  BaseFeature = -> Pocket024
  ReliefSketch = 0
  Size = 6
  SizeRatio = 1.5
  Sketch = -> Sketch043
  Suppressed = false
  XOffset = 0
  YOffset = 0
  baseObject = -> Pocket024 [Edge28,Edge31]
  kfactor = 0.5
FEATURE [PartDesign::Pocket] Pocket023
  BaseFeature = -> CornerRelief
  Direction = (-0.5,0.866025,-1e-16)
  Length = 0.6
  Length2 = 5
  Profile = -> Sketch041
  ReferenceAxis = -> Sketch041 [N_Axis]
  Suppressed = false
  Type = 0
FEATURE [PartDesign::Mirrored] Mirrored002
  BaseFeature = -> Pocket023
  MirrorPlane = -> YZ_Plane028
  Originals = -> [Pocket023]
  Refine = true
  Suppressed = false
FEATURE [PartDesign::Boolean] Boolean008
  BaseFeature = -> Mirrored002
  Group = -> [Compound028]
  Suppressed = false
  Type = 1
  UsePlacement = false
  expr: Group = <<sink_fix001>>._self
FEATURE [PartDesign::Pocket] Pocket029
  BaseFeature = -> Boolean008
  Direction = (0,0.11295,-0.993601)
  Length = 5
  Length2 = 5
  Profile = -> Sketch064
  ReferenceAxis = -> Sketch064 [N_Axis]
  Reversed = true
  Suppressed = false
  Type = 1
FEATURE [PartDesign::Body] Body020  label="sink_material_0.30ansi"
  Group = -> [Sketch037,Line,DatumLine,Sketch038,DatumLine001,Sketch039,BaseBend011,Bend004,Local_CS,Sketch040,Binder031,Pocket022,Sketch041,Sketch042,Bend030,Sketch219,Pocket131,Mirrored017,Pocket024,Sketch043,CornerRelief,Pocket023,Mirrored002,Boolean008,Sketch064,Pocket029]
  Origin = -> Origin028
  Tip = -> Pocket029
FEATURE [App::Part] Part007  label="sink"
  Group = -> [Body020,Body021]
  Origin = -> Origin027
  Placement = pos=(14.5,8.37158,410) rot=(0,0,1;-1.0472rad)
  expr: .Placement.Base.x = <<Properties>>.endface_width / 2
  expr: .Placement.Base.y = <<Properties>>.petal_offset
  expr: .Placement.Base.z = basin_big#<<Properties>>.height + 18 mm
FEATURE [Sketcher::SketchObject] Sketch220  label="sleeve_outer_sketch"
  AttachmentSupport = -> [XZ_Plane100]
  FullyConstrained = true
  MapMode = 5
  Placement = pos=(0,0,0) rot=(1,0,0;1.5708rad)
  expr: Constraints[13] = <<sleeve_inner_sketch>>.Constraints.outer_r + 0.25 mm
  sketch-geometry (6):
    g0: LineSegment StartX=13.25 StartY=67 StartZ=0 EndX=13.25 EndY=0 EndZ=0
    g1: LineSegment StartX=13.25 StartY=0 StartZ=0 EndX=35.25 EndY=0 EndZ=0
    g2: LineSegment StartX=35.25 StartY=0 StartZ=0 EndX=35.25 EndY=7 EndZ=0
    g3: LineSegment StartX=35.25 StartY=7 StartZ=0 EndX=20.25 EndY=7 EndZ=0
    g4: LineSegment StartX=20.25 StartY=7 StartZ=0 EndX=20.25 EndY=67 EndZ=0
    g5: LineSegment StartX=20.25 StartY=67 StartZ=0 EndX=13.25 EndY=67 EndZ=0
  constraints (20):
    c: PointOnObject(g0,g-1)
    c: Vertical(g0)
    c: Coincident(g0,g1)
    c: PointOnObject(g1,g-1)
    c: Coincident(g1,g2)
    c: Vertical(g2)
    c: Coincident(g2,g3)
    c: Horizontal(g3)
    c: Coincident(g3,g4)
    c: Vertical(g4)
    c: Coincident(g4,g5)
    c: Coincident(g5,g0)
    c: Horizontal(g5)
    c: DistanceX(g0) = 13.25
    c: DistanceX(g5,g5) = 7
    c: DistanceX(g3,g3) = 15
    c: DistanceY(g2,g2) = 7  'flange_height'
    c: DistanceY(g0,g0) = 67
    c: DistanceX(g3) = 20.25  'max_r'
    c: DistanceX(g1) = 35.25  'flange_max_r'
FEATURE [Sketcher::SketchObject] Sketch221  label="sleeve_inner_sketch"
  AttachmentSupport = -> [XZ_Plane101]
  FullyConstrained = true
  MapMode = 5
  Placement = pos=(0,0,0) rot=(1,0,0;1.5708rad)
  sketch-geometry (6):
    g0: LineSegment StartX=5 StartY=79 StartZ=0 EndX=5 EndY=0 EndZ=0
    g1: LineSegment StartX=5 StartY=0 StartZ=0 EndX=33 EndY=0 EndZ=0
    g2: LineSegment StartX=33 StartY=0 StartZ=0 EndX=33 EndY=8 EndZ=0
    g3: LineSegment StartX=33 StartY=8 StartZ=0 EndX=13 EndY=8 EndZ=0
    g4: LineSegment StartX=13 StartY=8 StartZ=0 EndX=13 EndY=79 EndZ=0
    g5: LineSegment StartX=13 StartY=79 StartZ=0 EndX=5 EndY=79 EndZ=0
  constraints (19):
    c: PointOnObject(g0,g-1)
    c: Vertical(g0)
    c: Coincident(g0,g1)
    c: PointOnObject(g1,g-1)
    c: Coincident(g1,g2)
    c: Vertical(g2)
    c: Coincident(g2,g3)
    c: Horizontal(g3)
    c: Coincident(g3,g4)
    c: Vertical(g4)
    c: Coincident(g4,g5)
    c: Coincident(g5,g0)
    c: Horizontal(g5)
    c: DistanceX(g0) = 5  'inner_r'
    c: DistanceX(g0,g3) = 8
    c: DistanceY(g2,g2) = 8
    c: DistanceX(g3,g3) = 20
    c: DistanceX(g3) = 13  'outer_r'
    c: DistanceY(g4,g4) = 71
FEATURE [PartDesign::Revolution] Revolution
  Angle = 360
  Angle2 = 60
  Axis = (0,2e-16,1)
  Base = (0,0,0)
  Placement = pos=(0,0,0) rot=(1,0,0;1.5708rad)
  Profile = -> Sketch221
  ReferenceAxis = -> Sketch221 [V_Axis]
  Reversed = true
  Suppressed = false
  Type = 0
FEATURE [PartDesign::Revolution] Revolution001
  Angle = 360
  Angle2 = 60
  Axis = (0,2e-16,1)
  Base = (0,0,0)
  Placement = pos=(0,0,0) rot=(1,0,0;1.5708rad)
  Profile = -> Sketch220
  ReferenceAxis = -> Sketch220 [V_Axis]
  Reversed = true
  Suppressed = false
  Type = 0
FEATURE [App::Link] Link043  label="top_amplifier_cornrer_material_0.50ansi001"
  LinkedObject = -> Body113
FEATURE [Part::Cylinder] Cylinder004  label="Cylinder"
  Angle = 360
  AttacherType = Attacher::AttachEngine3D
  FirstAngle = 0
  Height = 50
  Placement = pos=(-21.5035,3.75481,0) rot=(0,0,-1;0.523599rad)
  Radius = 2.05
  SecondAngle = 0
  expr: Placement = placement(vector(0; 0; 0); rotation(-30; 0; -0)) * placement(vector(-20.5; -<<Properties>>.inner_width / 2 + 4 mm; 0); rotation(0; 0; 0))
FEATURE [Part::Compound] Compound072  label="top_amplifier_cornrer_cut1"
  Links = -> [Populate031,Cylinder004]
FEATURE [PartDesign::Boolean] Boolean017
  BaseFeature = -> Mirrored014
  Group = -> [Compound072]
  Refine = true
  Suppressed = false
  Type = 1
  UsePlacement = false
FEATURE [PartDesign::Body] Body113  label="top_amplifier_cornrer_material_0.50ansi"
  Group = -> [Sketch191,BaseBend046,Sketch193,Bend029,Fillet014,Pocket118,Mirrored014,Boolean017]
  Origin = -> Origin087
  Tip = -> Boolean017
FEATURE [Part::FeaturePython] Placment030  label="top_amplifier_placement"  # WARN: FeaturePython — macro-defined, semantics opaque (R4)
  AttacherType = Attacher::AttachEngine3D
  ExposePlacement = true
  MarkerShape = 1
  MarkerSize = 10
  NumElements = 1
  Placement = pos=(11.5,6.63953,1394) rot=(0,0,-1;1.0472rad)
  Type = lattice2AttachablePlacement.AttachablePlacement
  isLattice = 1
  expr: .Placement.Base.x = <<Properties>>.inner_width / 2
  expr: .Placement.Base.y = Sketch.Constraints.connection_offset * sin(30) - 1.5 mm / sin(60)
  expr: .Placement.Base.z = <<Properties>>.total_height - BaseBend046.length - 4 mm
FEATURE [App::DocumentObjectGroup] Group009  label="placements"
  Group = -> [Placment,Placment001,Placment002,Placment003,Placment004,Placment005,Placment018,Placment030]
FEATURE [Part::FeaturePython] Placment031  # WARN: FeaturePython — macro-defined, semantics opaque (R4)
  AttacherType = Attacher::AttachEngine3D
  AttachmentOffset = pos=(0,0,-1394) rot=(0,0,1;0rad)
  AttachmentSupport = -> [Placment030]
  ExposePlacement = true
  MapMode = 2
  MarkerShape = 1
  MarkerSize = 10
  NumElements = 1
  Placement = pos=(11.5,6.63953,0) rot=(0,0,-1;1.0472rad)
  Type = lattice2AttachablePlacement.AttachablePlacement
  isLattice = 1
  expr: .AttachmentOffset.Base.z = -<<top_amplifier_placement>>.Placement.Base.z
FEATURE [Part::FeaturePython] Populate047  label="Populate Placment031 with Cylinder"  # WARN: FeaturePython — macro-defined, semantics opaque (R4)
  Copying = 0
  ExposePlacement = false
  MarkerShape = 1
  MarkerSize = 0
  NumElements = 0
  Object = -> Cylinder004
  OutputCompounding = 2
  PlacementsTo = -> Placment031
  Referencing = 0
  Type = lattice2PopulateCopies.LatticePopulateCopies
  isLattice = 0
FEATURE [Part::FeaturePython] Array012  # Draft array (typed FeaturePython)
  Angle = 360
  ArrayType = 1
  Axis = (0,0,1)
  Base = -> Populate047
  Center = (0,0,0)
  Count = 3
  Fuse = true
  IntervalAxis = (0,0,0)
  IntervalX = (50,0,0)
  IntervalY = (0,50,0)
  IntervalZ = (0,0,50)
  NumberCircles = 3
  NumberPolar = 3
  NumberX = 2
  NumberY = 2
  NumberZ = 1
  RadialDistance = 50
  Symmetry = 1
  TangentialDistance = 25
FEATURE [Part::Compound] Compound079  label="sleeve_outer_cut1"
  Links = -> [Array012]
FEATURE [PartDesign::Boolean] Boolean030
  BaseFeature = -> Revolution001
  Group = -> [Compound079]
  Suppressed = false
  Type = 1
  UsePlacement = false
FEATURE [Sketcher::SketchObject] Sketch222
  FullyConstrained = true
  sketch-geometry (10):
    g0: LineSegment StartX=22.5167 StartY=-13 StartZ=0 EndX=-22.5167 EndY=-13 EndZ=0
    g1: LineSegment StartX=-22.5167 StartY=-13 StartZ=0 EndX=0 EndY=26 EndZ=0
    g2: LineSegment StartX=0 StartY=26 StartZ=0 EndX=22.5167 EndY=-13 EndZ=0
    g3: GeomPoint X=0 Y=0 Z=0
    g4: Circle CenterX=0 CenterY=26 CenterZ=0 NormalX=0 NormalY=0 NormalZ=1 AngleXU=0 Radius=2
    g5: Circle CenterX=-22.5167 CenterY=-13 CenterZ=0 NormalX=0 NormalY=0 NormalZ=1 AngleXU=0 Radius=2
    g6: Circle CenterX=22.5167 CenterY=-13 CenterZ=0 NormalX=0 NormalY=0 NormalZ=1 AngleXU=0 Radius=2
    g7: LineSegment StartX=-22.5167 StartY=-13 StartZ=0 EndX=0 EndY=0 EndZ=0
    g8: LineSegment StartX=0 StartY=0 StartZ=0 EndX=0 EndY=26 EndZ=0
    g9: LineSegment StartX=0 StartY=0 StartZ=0 EndX=22.5167 EndY=-13 EndZ=0
  constraints (22):
    c: Coincident(g0,g1)
    c: Coincident(g2,g0)
    c: Coincident(g3,g-1)
    c: Coincident(g4,g1)
    c: Coincident(g5,g0)
    c: Coincident(g6,g0)
    c: Distance(g3,g4) = 26
    c: Equal(g4,g5)
    c: Equal(g4,g6)
    c: Diameter(g4) = 4
    c: Coincident(g2,g4)
    c: Equal(g1,g2)
    c: Equal(g2,g0)
    c: Coincident(g7,g5)
    c: Coincident(g7,g3)
    c: Coincident(g7,g8)
    c: Coincident(g8,g4)
    c: Coincident(g9,g3)
    c: Coincident(g9,g6)
    c: PointOnObject(g4,g-2)
    c: Equal(g9,g8)
    c: Equal(g9,g7)
FEATURE [Part::Extrusion] Extrude032
  Base = -> Sketch222
  Dir = (0,0,1)
  DirMode = 2
  FaceMakerClass = Part::FaceMakerBullseye
  LengthFwd = 10
  LengthRev = 0
  Placement = pos=(0,0,0) rot=(0,0,1;3.14159rad)
  Solid = true
  Symmetric = false
FEATURE [TechDraw::DrawSVGTemplate] Template
  Height = 210
  Orientation = 1
  Template = <path>
  Width = 297
FEATURE [App::Link] Link044  label="sleeve_outer001"
  LinkedObject = -> Body123
FEATURE [App::Link] Link045  label="sleeve_inner001"
  LinkedObject = -> Body124
FEATURE [App::DocumentObjectGroup] Group010  label="links"
  Group = -> [Link011,Link010,Link015,Link014,Link013,Link012,Link019,Link018,Link017,Link020,Link016,Link025,Link024,Link022,Link026,Link021,Link023,Link029,Link027,Link028,Link032,Link031,Link030,Link034,Link033,Link036,Link035,Link037,Link043,Link044,Link045]
FEATURE [Sketcher::SketchObject] Sketch223
  AttachmentOffset = pos=(0,0,0) rot=(0,1,0;0.523599rad)
  AttachmentSupport = -> [XZ_Plane102]
  FullyConstrained = true
  MapMode = 5
  Placement = pos=(0,0,0) rot=(0.935113,0.250563,0.250563;1.63783rad)
  expr: Constraints[15] = <<sleeve_outer_sketch>>.Constraints.flange_max_r + 1 mm
  expr: Constraints[16] = <<sleeve_outer_sketch>>.Constraints.max_r + 1 mm
  sketch-geometry (8):
    g0: ArcOfCircle CenterX=39.25 CenterY=3 CenterZ=0 NormalX=0 NormalY=0 NormalZ=1 AngleXU=0 Radius=3 StartAngle=3.14159 EndAngle=4.71239
    g1: LineSegment StartX=36.25 StartY=3 StartZ=0 EndX=36.25 EndY=48.4 EndZ=0
    g2: LineSegment StartX=36.25 StartY=48.4 StartZ=0 EndX=21.25 EndY=48.4 EndZ=0
    g3: LineSegment StartX=21.25 StartY=48.4 StartZ=0 EndX=21.25 EndY=40.4 EndZ=0
    g4: LineSegment StartX=0 StartY=0 StartZ=0 EndX=39.25 EndY=0 EndZ=0
    g5: LineSegment StartX=21.25 StartY=40.4 StartZ=0 EndX=0 EndY=40.4 EndZ=0
    g6: LineSegment StartX=0 StartY=40.4 StartZ=0 EndX=0 EndY=0 EndZ=0
    g7: GeomPoint X=21.25 Y=48.4 Z=0
  constraints (21):
    c: PointOnObject(g0,g-1)
    c: Vertical(g1)
    c: Coincident(g2,g1)
    c: Horizontal(g2)
    c: Vertical(g3)
    c: Tangent(g1,g0) = 1.5708
    c: Coincident(g4,g-1)
    c: Tangent(g4,g0) = -1.5708
    c: Radius(g0) = 3
    c: Coincident(g5,g3)
    c: PointOnObject(g5,g-2)
    c: Horizontal(g5)
    c: Coincident(g6,g5)
    c: Coincident(g6,g4)
    c: DistanceY(g6,g6) = 40.4
    c: DistanceX(g1) = 36.25
    c: DistanceX(g7) = 21.25
    c: DistanceY(g7,g3) = -8
    c: PointOnObject(g7,g2)
    c: PointOnObject(g7,g3)
    c: Coincident(g2,g3)
FEATURE [Sketcher::SketchObject] Sketch224
  AttachmentSupport = -> [XY_Plane102]
  FullyConstrained = true
  MapMode = 5
  expr: Constraints[10] = <<sleeve_outer_sketch>>.Constraints.max_r + 1 mm
  sketch-geometry (7):
    g0: LineSegment StartX=1.3e-15 StartY=21.4809 StartZ=0 EndX=0 EndY=0.46188 EndZ=0
    g1: LineSegment StartX=0 StartY=0.46188 StartZ=0 EndX=18.203 EndY=10.9714 EndZ=0
    g2: LineSegment StartX=0 StartY=0 StartZ=0 EndX=-0.2 EndY=0.34641 EndZ=0
    g3: LineSegment StartX=-0.2 StartY=0.34641 StartZ=0 EndX=0 EndY=0.46188 EndZ=0
    g4: ArcOfCircle CenterX=0 CenterY=0.46188 CenterZ=0 NormalX=0 NormalY=0 NormalZ=1 AngleXU=0 Radius=21.0191 StartAngle=0.648827 EndAngle=1.5708
    g5: ArcOfCircle CenterX=19.1382 CenterY=14.9754 CenterZ=0 NormalX=0 NormalY=0 NormalZ=1 AngleXU=0 Radius=3 StartAngle=3.79042 EndAngle=5.23599
    g6: LineSegment StartX=18.203 StartY=10.9714 StartZ=0 EndX=20.6382 EndY=12.3774 EndZ=0
  constraints (19):
    c: PointOnObject(g0,g-2)
    c: PointOnObject(g0,g-2)
    c: Coincident(g0,g1)
    c: Angle(g1) = 0.523599
    c: Distance(g-1,g1) = 0.4
    c: Coincident(g4,g0)
    c: Coincident(g2,g3)
    c: Coincident(g3,g0)
    c: Perpendicular(g3,g2)
    c: Parallel(g3,g1)
    c: Distance(g2,g1) = 21.25
    c: Coincident(g6,g1)
    c: Parallel(g6,g1)
    c: Tangent(g5,g4) = 1.5708
    c: PointOnObject(g1,g4)
    c: Coincident(g-1,g2)
    c: Coincident(g4,g0)
    c: Tangent(g6,g5) = -1.5708
    c: Radius(g5) = 3
FEATURE [PartDesign::Pad] Pad034
  Direction = (0.5,-0.866025,1e-16)
  Length = 0.4
  Length2 = 10
  Placement = pos=(0,0,0) rot=(1,0,0;1.5708rad)
  Profile = -> Sketch223
  ReferenceAxis = -> Sketch223 [N_Axis]
  Reversed = true
  Suppressed = false
  Type = 0
FEATURE [PartDesign::Pad] Pad035
  BaseFeature = -> Pad034
  Direction = (0,0,1)
  Length = 50
  Length2 = 10
  Placement = pos=(0,0,0) rot=(1,0,0;1.5708rad)
  Profile = -> Sketch224
  ReferenceAxis = -> Sketch224 [N_Axis]
  Suppressed = false
  Type = 0
FEATURE [PartDesign::Mirrored] Mirrored018
  BaseFeature = -> Pad035
  MirrorPlane = -> YZ_Plane102
  Originals = -> [Pad034,Pad035]
  Placement = pos=(0,0,0) rot=(1,0,0;1.5708rad)
  Suppressed = false
FEATURE [PartDesign::Body] Body125  label="Body"
  Group = -> [Sketch223,Sketch224,Pad034,Pad035,Mirrored018]
  Origin = -> Origin102
  Tip = -> Mirrored018
FEATURE [Part::Compound] Compound080
  Links = -> [Body125]
FEATURE [PartDesign::Boolean] Boolean032
  BaseFeature = -> Pocket005
  Group = -> [Compound080]
  Suppressed = false
  Type = 1
  UsePlacement = false
FEATURE [PartDesign::Body] Body002  label="cap_outer_material_0.30ansi"
  Group = -> [Binder012,Binder013,BaseBend007,Bend001,Pocket002,Binder014,Sketch020,Pocket125,Pocket003,Binder015,Mirrored,Sketch022,WireFilter002,Pocket005,Binder132,Boolean032]
  Origin = -> Origin005
  Tip = -> Boolean032
FEATURE [Part::FeaturePython] Placment032  # WARN: FeaturePython — macro-defined, semantics opaque (R4)
  AttacherType = Attacher::AttachEngine3D
  ExposePlacement = true
  MarkerShape = 1
  MarkerSize = 10
  NumElements = 1
  Placement = pos=(0,0,6) rot=(0,1,0;3.14159rad)
  Type = lattice2AttachablePlacement.AttachablePlacement
  isLattice = 1
FEATURE [Part::FeaturePython] Populate048  label="Populate Placment032 with Populate Placment031 with Cylinder"  # WARN: FeaturePython — macro-defined, semantics opaque (R4)
  Copying = 0
  ExposePlacement = false
  MarkerShape = 1
  MarkerSize = 0
  NumElements = 0
  Object = -> Populate047
  OutputCompounding = 2
  PlacementsTo = -> Placment032
  Referencing = 0
  Type = lattice2PopulateCopies.LatticePopulateCopies
  isLattice = 0
FEATURE [Part::Cylinder] Cylinder005
  Angle = 360
  AttacherType = Attacher::AttachEngine3D
  FirstAngle = 0
  Height = 10
  Radius = 13.5
  SecondAngle = 0
FEATURE [Part::Compound] Compound082
  Links = -> [Populate048,Cylinder005]
FEATURE [PartDesign::Boolean] Boolean034
  BaseFeature = -> PDW_Sub
  Group = -> [Compound082]
  Suppressed = false
  Type = 1
  UsePlacement = false
FEATURE [Part::Cylinder] Cylinder006
  Angle = 360
  AttacherType = Attacher::AttachEngine3D
  FirstAngle = 0
  Height = 10
  Radius = 7.5
  SecondAngle = 0
FEATURE [Part::Compound] Compound081
  Links = -> [Populate047,Cylinder006]
FEATURE [PartDesign::Boolean] Boolean033
  BaseFeature = -> Hole003
  Group = -> [Compound081]
  Suppressed = false
  Type = 1
  UsePlacement = false
FEATURE [PartDesign::FeatureSubtractivePython] PDW_Common_Sub  # link proxy (typed FeaturePython)
  BaseFeature = -> Boolean033
  Body = Body004
  ClaimChildren = true
  EditPlacementAdjustments = false
  Enabled = 1
  LinkedObject = -> Connect
  MeshTolerance = 0.1
  PatternBaseOffset = 0
  PatternBaseScale = 1
  PatternBaseScaleXYZ = (1,1,1)
  PatternOffsetCut = false
  PatternOffsetIntersection = false
  PatternOffsetJoin = 0
  PatternOffsetMode = 0
  PatternOffsetSelfIntersection = false
  PatternOperation = 3
  PatternOperationDefault = Common
  PatternScaleCut = false
  PatternShapeOffset = 0
  PatternShapeScale = 1
  PatternShapeScaleXYZ = (1,1,1)
  PatternTool = -> Compound048
  PatternToolOffset = 0
  PatternToolScale = 1
  PatternToolScaleXYZ = (1,1,1)
  Refine = true
  RefineMesh = true
  ShapeManagement = 1
  ShowMeshProps = false
  ShowOffsetProps = false
  ShowScaleProps = false
  ShowWarnings = true
  Suppressed = false
  TipBase = -> Boolean033
  TipBaseOffset = 0
  TipBaseScale = 1
  TipBaseScaleXYZ = (1,1,1)
  TipOffsetCut = false
  TipOffsetIntersection = false
  TipOffsetJoin = 0
  TipOffsetMode = 0
  TipOffsetSelfIntersection = false
  TipOperation = 1
  TipOperationDefault = Common
  TipScaleCut = false
  TipShapeOffset = 0
  TipShapeScale = 1
  TipShapeScaleXYZ = (1,1,1)
  TipTool = -> Connect
  TipToolOffset = 0
  TipToolScale = 1
  TipToolScaleXYZ = (1,1,1)
  Type = Subtractive
  UsePatternBaseAddSubShape = false
  UsePatternToolAddSubShape = false
  UseTipBaseAddSubShape = true
  UseTipToolAddSubShape = true
  Version = 0.2023.08.13
FEATURE [Sketcher::SketchObject] Sketch225  label="UV_driver_holder_base_Sketch"
  FullyConstrained = true
  MapMode = 5
  sketch-geometry (5):
    g0: LineSegment StartX=-31.5 StartY=3 StartZ=0 EndX=-15.5 EndY=3 EndZ=0
    g1: LineSegment StartX=-15.5 StartY=3 StartZ=0 EndX=-15.5 EndY=52 EndZ=0
    g2: LineSegment StartX=-15.5 StartY=52 StartZ=0 EndX=15.5 EndY=52 EndZ=0
    g3: LineSegment StartX=15.5 StartY=52 StartZ=0 EndX=15.5 EndY=3 EndZ=0
    g4: LineSegment StartX=15.5 StartY=3 StartZ=0 EndX=31.5 EndY=3 EndZ=0
  constraints (15):
    c: Horizontal(g0)
    c: Coincident(g0,g1)
    c: Vertical(g1)
    c: Coincident(g1,g2)
    c: Coincident(g2,g3)
    c: Vertical(g3)
    c: Coincident(g3,g4)
    c: Horizontal(g4)
    c: Symmetric(g1,g2,g-2)
    c: Symmetric(g4,g0,g-2)
    c: DistanceX(g2,g2) = 31
    c: DistanceY(g4) = 3
    c: DistanceY(g2) = 52
    c: DistanceX(g4,g4) = 16
    c: DistanceX(g0,g4) = 63  'total_width'
FEATURE [Sketcher::SketchObject] Sketch226  label="UV_driver_holder_holes_Sketch"
  ExternalGeometry = -> [Sketch225]
  FullyConstrained = true
  sketch-geometry (2):
    g0: Circle CenterX=26.5 CenterY=0 CenterZ=0 NormalX=0 NormalY=0 NormalZ=1 AngleXU=0 Radius=1.7
    g1: Circle CenterX=-26.5 CenterY=0 CenterZ=0 NormalX=0 NormalY=0 NormalZ=1 AngleXU=0 Radius=1.7
  constraints (5):
    c: PointOnObject(g0,g-1)
    c: Diameter(g0) = 3.4
    c: DistanceX(g0,g-3) = 5
    c: Equal(g1,g0)
    c: Symmetric(g1,g0,g-2)
FEATURE [Part::Compound] Compound083  label="sleeve_inner_cut1"
  Links = -> [Extrude032]
FEATURE [PartDesign::Boolean] Boolean031
  BaseFeature = -> Revolution
  Group = -> [Compound083]
  Suppressed = false
  Type = 1
  UsePlacement = false
FEATURE [Part::Compound] Compound084  label="hat1_cut1"
  Links = -> [Extrude032]
FEATURE [PartDesign::SubShapeBinder] Binder135
  BindCopyOnChange = 0
  BindMode = 0
  ClaimChildren = false
  Context = -> Part010 [Body075.Binder135.]
  Fuse = false
  MakeFace = true
  OffsetFill = false
  OffsetIntersection = false
  OffsetJoinType = 0
  OffsetOpenResult = false
  PartialLoad = false
  Placement = pos=(35,150,0) rot=(0,0,1;0rad)
  Relative = false
  Support = -> [Sketch226]
  _Version = 2
  expr: Support = <<UV_driver_holder_holes_Sketch>>._self
FEATURE [PartDesign::Hole] Hole
  BaseFeature = -> Mirrored006
  CustomThreadClearance = 0
  Depth = 25
  DepthType = 0
  Diameter = 3.4
  DrillForDepth = false
  DrillPoint = 1
  DrillPointAngle = 118
  HoleCutCountersinkAngle = 90
  HoleCutCustomValues = false
  HoleCutDepth = 0
  HoleCutDiameter = 6.1
  HoleCutType = 0
  ModelThread = false
  Profile = -> Binder135
  Reversed = true
  Suppressed = false
  Tapered = false
  TaperedAngle = 90
  ThreadClass = 0
  ThreadDepth = 25
  ThreadDepthType = 0
  ThreadDirection = 0
  ThreadFit = 0
  ThreadSize = 0
  ThreadType = 0
  Threaded = false
  UseCustomThreadClearance = false
  expr: Diameter = <<Properties>>.rivet_d
FEATURE [PartDesign::Boolean] Boolean035
  BaseFeature = -> Hole
  Group = -> [Compound084]
  Suppressed = false
  Type = 1
  UsePlacement = false
FEATURE [PartDesign::Body] Body075  label="hat_bottom_material_0.30ansi"
  Group = -> [Binder039,Pad009,Binder040,Pocket032,Pocket054,PolarPattern,Sketch098,Hole015,Binder054,Binder055,Hole016,Hole017,Mirrored006,Sketch108,Binder135,Hole,Boolean035]
  Origin = -> Origin038
  Tip = -> Boolean035
FEATURE [App::Part] Part010  label="hat"
  Group = -> [Body075,Body076,Body078]
  Origin = -> Origin042
  Placement = pos=(0,0,1503) rot=(0,0,1;0rad)
FEATURE [Sketcher::SketchObject] Sketch227  label="bottom_bearing_Sketch"
  AttachmentSupport = -> [XZ_Plane104]
  FullyConstrained = true
  MapMode = 5
  Placement = pos=(0,0,0) rot=(1,0,0;1.5708rad)
  sketch-geometry (4):
    g0: LineSegment StartX=37.5 StartY=0 StartZ=0 EndX=50 EndY=0 EndZ=0
    g1: LineSegment StartX=50 StartY=0 StartZ=0 EndX=50 EndY=19 EndZ=0
    g2: LineSegment StartX=50 StartY=19 StartZ=0 EndX=37.5 EndY=19 EndZ=0
    g3: LineSegment StartX=37.5 StartY=19 StartZ=0 EndX=37.5 EndY=0 EndZ=0
  constraints (12):
    c: Coincident(g0,g1)
    c: Coincident(g1,g2)
    c: Coincident(g2,g3)
    c: Coincident(g3,g0)
    c: Horizontal(g0)
    c: Horizontal(g2)
    c: Vertical(g1)
    c: Vertical(g3)
    c: PointOnObject(g0,g-1)
    c: DistanceY(g3,g3) = 19  'height'
    c: DistanceX(g0) = 37.5  'inner_r'
    c: DistanceX(g0) = 50  'outer_r'
FEATURE [PartDesign::Revolution] Revolution002
  Angle = 360
  Angle2 = 60
  Axis = (0,2e-16,1)
  Base = (0,0,0)
  Placement = pos=(0,0,0) rot=(1,0,0;1.5708rad)
  Profile = -> Sketch227
  ReferenceAxis = -> Sketch227 [V_Axis]
  Reversed = true
  Suppressed = false
  Type = 0
FEATURE [PartDesign::Body] Body127  label="bottom_bearing"
  Group = -> [Sketch227,Revolution002]
  Origin = -> Origin104
  Tip = -> Revolution002
FEATURE [Sketcher::SketchObject] Sketch228
  AttachmentSupport = -> [XZ_Plane105]
  FullyConstrained = true
  MapMode = 5
  Placement = pos=(0,0,0) rot=(1,0,0;1.5708rad)
  expr: Constraints[12] = <<bottom_bearing_Sketch>>.Constraints.inner_r - 0.5 mm
  expr: Constraints[13] = <<bottom_bearing_Sketch>>.Constraints.outer_r
  expr: Constraints[16] = 61.3 mm - <<bottom_bearing_Sketch>>.Constraints.height
  sketch-geometry (6):
    g0: LineSegment StartX=37 StartY=0 StartZ=0 EndX=37 EndY=5 EndZ=0
    g1: LineSegment StartX=37 StartY=5 StartZ=0 EndX=50 EndY=5 EndZ=0
    g2: LineSegment StartX=50 StartY=5 StartZ=0 EndX=50 EndY=47.3 EndZ=0
    g3: LineSegment StartX=50 StartY=47.3 StartZ=0 EndX=0 EndY=47.3 EndZ=0
    g4: LineSegment StartX=0 StartY=47.3 StartZ=0 EndX=0 EndY=0 EndZ=0
    g5: LineSegment StartX=0 StartY=0 StartZ=0 EndX=37 EndY=0 EndZ=0
  constraints (17):
    c: Vertical(g0)
    c: Coincident(g0,g1)
    c: Coincident(g1,g2)
    c: Vertical(g2)
    c: Coincident(g2,g3)
    c: Horizontal(g3)
    c: Coincident(g3,g4)
    c: Vertical(g4)
    c: Coincident(g4,g5)
    c: Coincident(g5,g0)
    c: Horizontal(g5)
    c: DistanceY(g0,g0) = 5
    c: DistanceX(g0) = 37
    c: DistanceX(g1) = 50
    c: Horizontal(g1)
    c: Coincident(g4,g-1)
    c: DistanceY(g2,g2) = 42.3
FEATURE [PartDesign::Revolution] Revolution003
  Angle = 360
  Angle2 = 60
  Axis = (0,2e-16,1)
  Base = (0,0,0)
  Placement = pos=(0,0,0) rot=(1,0,0;1.5708rad)
  Profile = -> Sketch228
  ReferenceAxis = -> Sketch228 [V_Axis]
  Reversed = true
  Suppressed = false
  Type = 0
FEATURE [Part::Cylinder] Cylinder007  label="hole_6.5mm"
  Angle = 360
  AttacherType = Attacher::AttachEngine3D
  FirstAngle = 0
  Height = 100
  Radius = 3.25
  SecondAngle = 0
FEATURE [Part::FeaturePython] PolarArray008  label="bottom_sleeve_to_basement_placement"  # WARN: FeaturePython — macro-defined, semantics opaque (R4)
  Alignment = 0
  AttacherType = Attacher::AttachEngine3D
  CellStart = A1
  Count = 3
  DistributionLaw = 0
  EndInclusive = false
  ExposePlacement = false
  FlipX = false
  FlipZ = false
  GeneratorMode = 0
  MarkerShape = 1
  MarkerSize = 0
  NumElements = 3
  OrientMode = 2
  Radius = 28.4
  Reverse = false
  SpanEnd = 360
  SpanStart = 0
  Step = 120
  Type = lattice2PolarArray2.PolarArray
  UseArcRadius = false
  UseArcRange = 0
  VSGVersion = 1
  Values = 0.0 | 120.0 | 240.0
  ValuesSource = 2
  isLattice = 1
  expr: Radius = <<bottom_bearing_Sketch>>.Constraints.inner_r - 18.2 mm / 2
FEATURE [Part::FeaturePython] Populate049  label="Populate bottom_sleeve_to_basement_placement with hole_6.5mm"  # WARN: FeaturePython — macro-defined, semantics opaque (R4)
  Copying = 0
  ExposePlacement = false
  MarkerShape = 1
  MarkerSize = 0
  NumElements = 0
  Object = -> Cylinder007
  OutputCompounding = 1
  Placement = pos=(0,0,-10) rot=(0,0,1;0rad)
  PlacementsTo = -> PolarArray008
  Referencing = 0
  Type = lattice2PopulateCopies.LatticePopulateCopies
  isLattice = 0
FEATURE [Part::Cylinder] Cylinder008  label="hole_12.5mm"
  Angle = 360
  AttacherType = Attacher::AttachEngine3D
  FirstAngle = 0
  Height = 100
  Radius = 6.25
  SecondAngle = 0
FEATURE [Part::Compound] Compound085  label="bottom_caprolon_cut1"
  Links = -> [Populate049,Cylinder008]
FEATURE [PartDesign::Boolean] Boolean036
  BaseFeature = -> Revolution003
  Group = -> [Compound085]
  Suppressed = false
  Type = 1
  UsePlacement = false
FEATURE [PartDesign::Body] Body128  label="bottom_caprolon"
  Group = -> [Sketch228,Revolution003,Boolean036]
  Origin = -> Origin105
  Placement = pos=(0,0,14) rot=(0,0,1;0rad)
  Tip = -> Boolean036
FEATURE [Sketcher::SketchObject] Sketch229
  AttachmentSupport = -> [XY_Plane106]
  FullyConstrained = true
  MapMode = 5
  sketch-geometry (13):
    g0: LineSegment StartX=-15.05 StartY=-24.05 StartZ=0 EndX=-15.05 EndY=24.05 EndZ=0
    g1: LineSegment StartX=-15.05 StartY=24.05 StartZ=0 EndX=15.05 EndY=24.05 EndZ=0
    g2: LineSegment StartX=15.05 StartY=24.05 StartZ=0 EndX=15.05 EndY=-24.05 EndZ=0
    g3: LineSegment StartX=15.05 StartY=-24.05 StartZ=0 EndX=-15.05 EndY=-24.05 EndZ=0
    g4: GeomPoint X=2e-16 Y=0 Z=0
    g5: Circle CenterX=15.05 CenterY=24.05 CenterZ=0 NormalX=0 NormalY=0 NormalZ=1 AngleXU=0 Radius=3.15
    g6: Circle CenterX=-15.05 CenterY=24.05 CenterZ=0 NormalX=0 NormalY=0 NormalZ=1 AngleXU=0 Radius=3.15
    g7: Circle CenterX=-15.05 CenterY=-24.05 CenterZ=0 NormalX=0 NormalY=0 NormalZ=1 AngleXU=0 Radius=3.15
    g8: Circle CenterX=15.05 CenterY=-24.05 CenterZ=0 NormalX=0 NormalY=0 NormalZ=1 AngleXU=0 Radius=3.15
    g9: GeomPoint X=-18.2 Y=24.05 Z=0
    g10: GeomPoint X=18.2 Y=24.05 Z=0
    g11: GeomPoint X=15.05 Y=-27.2 Z=0
    g12: GeomPoint X=15.05 Y=27.2 Z=0
  constraints (28):
    c: Coincident(g0,g1)
    c: Coincident(g1,g2)
    c: Coincident(g2,g3)
    c: Coincident(g3,g0)
    c: Horizontal(g1)
    c: Horizontal(g3)
    c: Vertical(g0)
    c: Vertical(g2)
    c: Symmetric(g1,g0,g4)
    c: Coincident(g4,g-1)
    c: Coincident(g5,g1)
    c: Coincident(g6,g0)
    c: Coincident(g7,g0)
    c: Coincident(g8,g2)
    c: PointOnObject(g9,g6)
    c: PointOnObject(g10,g5)
    c: PointOnObject(g11,g8)
    c: PointOnObject(g12,g5)
    c: Vertical(g5,g12)
    c: Horizontal(g5,g10)
    c: Horizontal(g6,g9)
    c: Vertical(g8,g11)
    c: Equal(g5,g6)
    c: Equal(g6,g7)
    c: Equal(g7,g8)
    c: DistanceX(g9,g10) = 36.4
    c: DistanceY(g11,g12) = 54.4
    c: Diameter(g5) = 6.3
FEATURE [Sketcher::SketchObject] Sketch230
  AttachmentSupport = -> [XY_Plane106]
  FullyConstrained = true
  MapMode = 5
  sketch-geometry (5):
    g0: LineSegment StartX=-22.5 StartY=-30 StartZ=0 EndX=-22.5 EndY=30 EndZ=0
    g1: LineSegment StartX=-22.5 StartY=30 StartZ=0 EndX=22.5 EndY=30 EndZ=0
    g2: LineSegment StartX=22.5 StartY=30 StartZ=0 EndX=22.5 EndY=-30 EndZ=0
    g3: LineSegment StartX=22.5 StartY=-30 StartZ=0 EndX=-22.5 EndY=-30 EndZ=0
    g4: GeomPoint X=0 Y=0 Z=0
  constraints (12):
    c: Coincident(g0,g1)
    c: Coincident(g1,g2)
    c: Coincident(g2,g3)
    c: Coincident(g3,g0)
    c: Horizontal(g1)
    c: Horizontal(g3)
    c: Vertical(g0)
    c: Vertical(g2)
    c: Symmetric(g1,g0,g4)
    c: Coincident(g4,g-1)
    c: DistanceY(g2,g2) = 60
    c: DistanceX(g1,g1) = 45
FEATURE [PartDesign::Pad] Pad036
  Direction = (0,0,1)
  Length = 60.3
  Length2 = 10
  Profile = -> Sketch230
  ReferenceAxis = -> Sketch230 [N_Axis]
  Suppressed = false
  Type = 0
FEATURE [PartDesign::Body] Body129  label="wheel"
  Group = -> [Sketch229,Sketch230,Pad036]
  Origin = -> Origin106
  Tip = -> Pad036
FEATURE [Sketcher::SketchObject] Sketch231
  FullyConstrained = true
  expr: .Constraints.outer_r = <<basement_bottom_sketch>>.Constraints.min_r - 2 mm
  sketch-geometry (5):
    g0: ArcOfCircle CenterX=0 CenterY=0 CenterZ=0 NormalX=0 NormalY=0 NormalZ=1 AngleXU=0 Radius=148 StartAngle=0.543468 EndAngle=1.5708
    g1: ArcOfCircle CenterX=0 CenterY=0 CenterZ=0 NormalX=0 NormalY=0 NormalZ=1 AngleXU=0 Radius=168 StartAngle=0.541782 EndAngle=1.5708
    g2: ArcOfCircle CenterX=129.244 CenterY=78.0832 CenterZ=0 NormalX=0 NormalY=0 NormalZ=1 AngleXU=0 Radius=3 StartAngle=3.68506 EndAngle=5.23599
    g3: ArcOfCircle CenterX=141.371 CenterY=85.0844 CenterZ=0 NormalX=0 NormalY=0 NormalZ=1 AngleXU=0 Radius=3 StartAngle=5.23599 EndAngle=6.82497
    g4: LineSegment StartX=130.744 StartY=75.4851 StartZ=0 EndX=142.871 EndY=82.4864 EndZ=0
  constraints (15):
    c: Coincident(g0,g-1)
    c: PointOnObject(g0,g-2)
    c: Coincident(g1,g0)
    c: PointOnObject(g1,g-2)
    c: Tangent(g3,g1) = -1.5708
    c: Tangent(g4,g3) = -1.5708
    c: Tangent(g4,g2) = -1.5708
    c: Tangent(g2,g0) = 1.5708
    c: Equal(g2,g3)
    c: Radius(g2) = 3
    c: DistanceY(g0,g1) = 20
    c: PointOnObject(g0,g4)
    c: Angle(g4) = 0.523599
    c: DistanceY(g1) = 168  'outer_r'
    c: DistanceY(g0) = 148  'inner_r'
FEATURE [Part::Mirroring] Part__Mirroring033  label="Sketch231 (Mirror #30)"
  Base = (0,0,0)
  Normal = (1,0,0)
  Source = -> Sketch231
FEATURE [Part::FeaturePython] Connect004  # WARN: FeaturePython — macro-defined, semantics opaque (R4)
  Objects = -> [Sketch231,Part__Mirroring033]
  Tolerance = 0
FEATURE [Part::FeaturePython] PolarArray009  # WARN: FeaturePython — macro-defined, semantics opaque (R4)
  Alignment = 0
  AttacherType = Attacher::AttachEngine3D
  CellStart = A1
  Count = 3
  DistributionLaw = 0
  EndInclusive = true
  ExposePlacement = false
  FlipX = false
  FlipZ = false
  GeneratorMode = 0
  MarkerShape = 1
  MarkerSize = 0
  NumElements = 3
  OrientMode = 2
  Placement = pos=(0,0,0) rot=(0,0,1;1.5708rad)
  Radius = 140
  Reverse = false
  SpanEnd = 50
  SpanStart = -50
  Step = 50
  Type = lattice2PolarArray2.PolarArray
  UseArcRadius = false
  UseArcRange = 0
  VSGVersion = 1
  Values = -50.0 | 0.0 | 50.0
  ValuesSource = 2
  isLattice = 1
  expr: Radius = <<Sketch231>>.Constraints.inner_r - 8 mm
FEATURE [Sketcher::SketchObject] Sketch232
  FullyConstrained = true
  sketch-geometry (4):
    g0: ArcOfCircle CenterX=0 CenterY=0 CenterZ=0 NormalX=0 NormalY=0 NormalZ=1 AngleXU=0 Radius=5 StartAngle=1.5708 EndAngle=4.71239
    g1: LineSegment StartX=8 StartY=-13 StartZ=0 EndX=8 EndY=13 EndZ=0
    g2: ArcOfCircle CenterX=0 CenterY=13 CenterZ=0 NormalX=0 NormalY=0 NormalZ=1 AngleXU=0 Radius=8 StartAngle=4.71239 EndAngle=6.28319
    g3: ArcOfCircle CenterX=0 CenterY=-13 CenterZ=0 NormalX=0 NormalY=0 NormalZ=1 AngleXU=0 Radius=8 StartAngle=0 EndAngle=1.5708
  constraints (12):
    c: Coincident(g0,g-1)
    c: PointOnObject(g0,g-2)
    c: PointOnObject(g0,g-2)
    c: Vertical(g1)
    c: PointOnObject(g2,g-2)
    c: Coincident(g2,g0)
    c: PointOnObject(g3,g-2)
    c: Coincident(g3,g0)
    c: Diameter(g0) = 10
    c: Tangent(g2,g1) = -1.5708
    c: Tangent(g3,g1) = -1.5708
    c: DistanceX(g1) = 8
FEATURE [Part::Extrusion] Extrude034
  Base = -> Sketch232
  Dir = (0,0,1)
  DirMode = 2
  FaceMakerClass = Part::FaceMakerBullseye
  LengthFwd = 1
  LengthRev = 0
  Solid = true
  Symmetric = false
FEATURE [Part::FeaturePython] Populate050  label="Populate PolarArray009 with Extrude034"  # WARN: FeaturePython — macro-defined, semantics opaque (R4)
  Copying = 0
  ExposePlacement = false
  MarkerShape = 1
  MarkerSize = 0
  NumElements = 0
  Object = -> Extrude034
  OutputCompounding = 1
  PlacementsTo = -> PolarArray009
  Referencing = 0
  Type = lattice2PopulateCopies.LatticePopulateCopies
  isLattice = 0
FEATURE [PartDesign::SubShapeBinder] Binder136
  BindCopyOnChange = 0
  BindMode = 0
  ClaimChildren = true
  Context = -> Body130 [Binder136.]
  Fuse = false
  MakeFace = true
  OffsetFill = false
  OffsetIntersection = false
  OffsetJoinType = 0
  OffsetOpenResult = false
  PartialLoad = false
  Relative = false
  Support = -> [Connect004]
  _Version = 2
FEATURE [PartDesign::Pad] Pad037
  Direction = (0,0,1)
  Length = 1
  Length2 = 10
  Profile = -> Binder136
  Suppressed = false
  Type = 0
FEATURE [Part::Compound] Compound086
  Links = -> [Populate050]
FEATURE [PartDesign::Boolean] Boolean037
  BaseFeature = -> Pad037
  Group = -> [Compound086]
  Refine = true
  Suppressed = false
  Type = 0
  UsePlacement = false
FEATURE [Part::FeaturePython] Populate051  label="Populate 3_elem_polar_array with PolarArray009"  # WARN: FeaturePython — macro-defined, semantics opaque (R4)
  Copying = 0
  ExposePlacement = false
  MarkerShape = 1
  MarkerSize = 0
  NumElements = 9
  Object = -> PolarArray009
  OutputCompounding = 0
  PlacementsTo = -> PolarArray006
  Referencing = 1
  Type = lattice2PopulateCopies.LatticePopulateCopies
  isLattice = 1
FEATURE [Part::FeaturePython] Populate052  label="Populate Populate 3_elem_polar_array with PolarArray009 with hole_3.2_mm_extrude"  # WARN: FeaturePython — macro-defined, semantics opaque (R4)
  Copying = 0
  ExposePlacement = false
  MarkerShape = 1
  MarkerSize = 0
  NumElements = 0
  Object = -> Cylinder001
  OutputCompounding = 1
  PlacementsTo = -> Populate051
  Referencing = 0
  Type = lattice2PopulateCopies.LatticePopulateCopies
  isLattice = 0
FEATURE [Part::FeaturePython] Populate053  label="Populate PolarArray009 with hole_5_mm_extrude"  # WARN: FeaturePython — macro-defined, semantics opaque (R4)
  Copying = 0
  ExposePlacement = false
  MarkerShape = 1
  MarkerSize = 0
  NumElements = 0
  Object = -> Extrude023
  OutputCompounding = 1
  PlacementsTo = -> PolarArray009
  Referencing = 0
  Type = lattice2PopulateCopies.LatticePopulateCopies
  isLattice = 0
FEATURE [PartDesign::Boolean] Boolean038
  BaseFeature = -> Boolean037
  Group = -> [Populate053]
  Suppressed = false
  Type = 1
  UsePlacement = false
FEATURE [PartDesign::Body] Body130
  Group = -> [Binder136,Pad037,Boolean037,Boolean038]
  Origin = -> Origin107
  Tip = -> Boolean038
FEATURE [Sketcher::SketchObject] Sketch233  label="small_bearing_Sketch"
  AttachmentSupport = -> [XZ_Plane108]
  FullyConstrained = true
  MapMode = 5
  Placement = pos=(0,0,0) rot=(1,0,0;1.5708rad)
  sketch-geometry (4):
    g0: LineSegment StartX=6 StartY=0 StartZ=0 EndX=13 EndY=0 EndZ=0
    g1: LineSegment StartX=13 StartY=0 StartZ=0 EndX=13 EndY=8.9 EndZ=0
    g2: LineSegment StartX=13 StartY=8.9 StartZ=0 EndX=6 EndY=8.9 EndZ=0
    g3: LineSegment StartX=6 StartY=8.9 StartZ=0 EndX=6 EndY=0 EndZ=0
  constraints (12):
    c: Coincident(g0,g1)
    c: Coincident(g1,g2)
    c: Coincident(g2,g3)
    c: Coincident(g3,g0)
    c: Horizontal(g0)
    c: Horizontal(g2)
    c: Vertical(g1)
    c: Vertical(g3)
    c: PointOnObject(g0,g-1)
    c: DistanceY(g3,g3) = 8.9
    c: DistanceX(g0) = 6
    c: DistanceX(g0) = 13
FEATURE [PartDesign::Revolution] Revolution004
  Angle = 360
  Angle2 = 60
  Axis = (0,2e-16,1)
  Base = (0,0,0)
  Placement = pos=(0,0,0) rot=(1,0,0;1.5708rad)
  Profile = -> Sketch233
  ReferenceAxis = -> Sketch233 [V_Axis]
  Reversed = true
  Suppressed = false
  Type = 0
FEATURE [PartDesign::Body] Body131  label="small_bearing"
  Group = -> [Sketch233,Revolution004]
  Origin = -> Origin108
  Tip = -> Revolution004
FEATURE [TechDraw::DrawViewPart] View004
  CoarseView = false
  Direction = (0,0,1)
  Focus = 100
  HardHidden = false
  IsoCount = 0
  IsoHidden = false
  IsoVisible = false
  LockPosition = false
  Perspective = false
  Rotation = 0
  ScaleType = 0
  ScrubCount = 0
  SeamHidden = false
  SeamVisible = true
  SmoothHidden = false
  SmoothVisible = true
  Source = -> [Body128]
  X = 78.5
  XDirection = (1,0,0)
  Y = 105
FEATURE [TechDraw::DrawViewPart] View005
  CoarseView = false
  Direction = (0,-1,0)
  Focus = 100
  HardHidden = false
  IsoCount = 0
  IsoHidden = false
  IsoVisible = false
  LockPosition = false
  Perspective = false
  Rotation = 0
  ScaleType = 0
  ScrubCount = 0
  SeamHidden = false
  SeamVisible = true
  SmoothHidden = false
  SmoothVisible = true
  Source = -> [Body128]
  X = 228.5
  XDirection = (1,0,0)
  Y = 155
FEATURE [TechDraw::DrawViewSection] SectionView002  label="Section002  - "
  BaseView = -> View005
  CoarseView = false
  CutSurfaceDisplay = 1
  Direction = (1,0,0)
  FileGeomPattern = <path>
  FileHatchPattern = <path>
  Focus = 100
  FuseBeforeCut = false
  HardHidden = false
  HatchOffset = (0,0,0)
  HatchRotation = 0
  HatchScale = 1
  IsoCount = 0
  IsoHidden = false
  IsoVisible = false
  LockPosition = false
  NameGeomPattern = Diamond
  Perspective = false
  Rotation = 90
  ScaleType = 0
  ScrubCount = 0
  SeamHidden = false
  SeamVisible = true
  SectionDirection = 4
  SectionLineStretch = 1
  SectionNormal = (1,0,0)
  SectionOrigin = (0,0,37.65)
  SmoothHidden = false
  SmoothVisible = true
  Source = -> [Body128]
  TrimAfterCut = false
  UsePreviousCut = false
  X = 228.5
  XDirection = (0,0,1)
  Y = 55
FEATURE [TechDraw::DrawViewDimension] Dimension016
  AngleOverride = false
  Arbitrary = false
  ArbitraryTolerances = false
  EqualTolerance = true
  ExtensionAngle = 0
  FormatSpec = %.2w
  FormatSpecOverTolerance = %+.2w
  FormatSpecUnderTolerance = %+.2w
  Inverted = false
  LineAngle = 0
  LockPosition = false
  MeasureType = 1
  OverTolerance = 0
  References2D = -> [View005]
  Rotation = 0
  ScaleType = 0
  TheoreticalExact = false
  Type = 2
  UnderTolerance = 0
  X = -63.5214
  Y = -28.8688
FEATURE [TechDraw::DrawViewDimension] Dimension017
  AngleOverride = false
  Arbitrary = false
  ArbitraryTolerances = false
  EqualTolerance = true
  ExtensionAngle = 0
  FormatSpec = %.2w
  FormatSpecOverTolerance = %+.2w
  FormatSpecUnderTolerance = %+.2w
  Inverted = false
  LineAngle = 0
  LockPosition = false
  MeasureType = 1
  OverTolerance = 0
  References2D = -> [View005]
  Rotation = 0
  ScaleType = 0
  TheoreticalExact = false
  Type = 2
  UnderTolerance = 0
  X = -69.3536
  Y = 5.37948
FEATURE [TechDraw::DrawViewDimension] Dimension018
  AngleOverride = false
  Arbitrary = false
  ArbitraryTolerances = false
  EqualTolerance = true
  ExtensionAngle = 0
  FormatSpec = ⌀%.2w
  FormatSpecOverTolerance = %+.2w
  FormatSpecUnderTolerance = %+.2w
  Inverted = false
  LineAngle = 0
  LockPosition = false
  MeasureType = 1
  OverTolerance = 0
  References2D = -> [View004]
  Rotation = 0
  ScaleType = 0
  TheoreticalExact = false
  Type = 5
  UnderTolerance = 0
  X = -23.9762
  Y = 6.63298
FEATURE [TechDraw::DrawViewDimension] Dimension019
  AngleOverride = false
  Arbitrary = false
  ArbitraryTolerances = false
  EqualTolerance = true
  ExtensionAngle = 0
  FormatSpec = ⌀%.2w
  FormatSpecOverTolerance = %+.2w
  FormatSpecUnderTolerance = %+.2w
  Inverted = false
  LineAngle = 0
  LockPosition = false
  MeasureType = 1
  OverTolerance = 0
  References2D = -> [View004]
  Rotation = 0
  ScaleType = 0
  TheoreticalExact = false
  Type = 5
  UnderTolerance = 0
  X = 8.66891
  Y = 33.3069
FEATURE [TechDraw::DrawViewDimension] Dimension020
  AngleOverride = false
  Arbitrary = false
  ArbitraryTolerances = false
  EqualTolerance = true
  ExtensionAngle = 0
  FormatSpec = %.2w
  FormatSpecOverTolerance = %+.2w
  FormatSpecUnderTolerance = %+.2w
  Inverted = false
  LineAngle = 0
  LockPosition = false
  MeasureType = 1
  OverTolerance = 0
  References2D = -> [View004]
  Rotation = 0
  ScaleType = 0
  TheoreticalExact = false
  Type = 1
  UnderTolerance = 0
  X = 13.41
  Y = -12.6373
FEATURE [TechDraw::DrawViewDimension] Dimension021
  AngleOverride = false
  Arbitrary = false
  ArbitraryTolerances = false
  EqualTolerance = true
  ExtensionAngle = 0
  FormatSpec = %.2w
  FormatSpecOverTolerance = %+.2w
  FormatSpecUnderTolerance = %+.2w
  Inverted = false
  LineAngle = 0
  LockPosition = false
  MeasureType = 1
  OverTolerance = 0
  References2D = -> [View005]
  Rotation = 0
  ScaleType = 0
  TheoreticalExact = false
  Type = 1
  UnderTolerance = 0
  X = -11.0078
  Y = 36.7782
FEATURE [TechDraw::DrawViewDimension] Dimension022
  AngleOverride = false
  Arbitrary = false
  ArbitraryTolerances = false
  EqualTolerance = true
  ExtensionAngle = 0
  FormatSpec = %.2w
  FormatSpecOverTolerance = %+.2w
  FormatSpecUnderTolerance = %+.2w
  Inverted = false
  LineAngle = 0
  LockPosition = false
  MeasureType = 1
  OverTolerance = 0
  References2D = -> [View005]
  Rotation = 0
  ScaleType = 0
  TheoreticalExact = false
  Type = 1
  UnderTolerance = 0
  X = -1.13845
  Y = -46.1959
FEATURE [TechDraw::DrawViewDimension] Dimension023
  AngleOverride = false
  Arbitrary = false
  ArbitraryTolerances = false
  EqualTolerance = true
  ExtensionAngle = 0
  FormatSpec = %.2w
  FormatSpecOverTolerance = %+.2w
  FormatSpecUnderTolerance = %+.2w
  Inverted = false
  LineAngle = 0
  LockPosition = false
  MeasureType = 1
  OverTolerance = 0
  References2D = -> [SectionView002]
  Rotation = 0
  ScaleType = 0
  TheoreticalExact = false
  Type = 1
  UnderTolerance = 0
  X = 0
  Y = -27.26
FEATURE [Sketcher::SketchObject] Sketch234  label="sleeve_outer_sketch001"
  AttachmentSupport = -> [XZ_Plane110]
  FullyConstrained = true
  MapMode = 5
  Placement = pos=(0,0,0) rot=(1,0,0;1.5708rad)
  expr: Constraints[13] = <<sleeve_inner_sketch001>>.Constraints.outer_r + 0.25 mm
  sketch-geometry (6):
    g0: LineSegment StartX=13.25 StartY=74.7 StartZ=0 EndX=13.25 EndY=0 EndZ=0
    g1: LineSegment StartX=13.25 StartY=0 StartZ=0 EndX=35.25 EndY=0 EndZ=0
    g2: LineSegment StartX=35.25 StartY=0 StartZ=0 EndX=35.25 EndY=7 EndZ=0
    g3: LineSegment StartX=35.25 StartY=7 StartZ=0 EndX=20.25 EndY=7 EndZ=0
    g4: LineSegment StartX=20.25 StartY=7 StartZ=0 EndX=20.25 EndY=74.7 EndZ=0
    g5: LineSegment StartX=20.25 StartY=74.7 StartZ=0 EndX=13.25 EndY=74.7 EndZ=0
  constraints (20):
    c: PointOnObject(g0,g-1)
    c: Vertical(g0)
    c: Coincident(g0,g1)
    c: PointOnObject(g1,g-1)
    c: Coincident(g1,g2)
    c: Vertical(g2)
    c: Coincident(g2,g3)
    c: Horizontal(g3)
    c: Coincident(g3,g4)
    c: Vertical(g4)
    c: Coincident(g4,g5)
    c: Coincident(g5,g0)
    c: Horizontal(g5)
    c: DistanceX(g0) = 13.25
    c: DistanceX(g5,g5) = 7
    c: DistanceX(g3,g3) = 15
    c: DistanceY(g2,g2) = 7  'flange_height'
    c: DistanceY(g0,g0) = 74.7
    c: DistanceX(g3) = 20.25  'max_r'
    c: DistanceX(g1) = 35.25  'flange_max_r'
FEATURE [Sketcher::SketchObject] Sketch235  label="sleeve_inner_sketch001"
  AttachmentSupport = -> [XZ_Plane101]
  FullyConstrained = true
  MapMode = 5
  Placement = pos=(0,0,0) rot=(1,0,0;1.5708rad)
  sketch-geometry (6):
    g0: LineSegment StartX=5 StartY=83.7 StartZ=0 EndX=5 EndY=0 EndZ=0
    g1: LineSegment StartX=5 StartY=0 StartZ=0 EndX=33 EndY=0 EndZ=0
    g2: LineSegment StartX=33 StartY=0 StartZ=0 EndX=33 EndY=5 EndZ=0
    g3: LineSegment StartX=33 StartY=5 StartZ=0 EndX=13 EndY=5 EndZ=0
    g4: LineSegment StartX=13 StartY=5 StartZ=0 EndX=13 EndY=83.7 EndZ=0
    g5: LineSegment StartX=13 StartY=83.7 StartZ=0 EndX=5 EndY=83.7 EndZ=0
  constraints (19):
    c: PointOnObject(g0,g-1)
    c: Vertical(g0)
    c: Coincident(g0,g1)
    c: PointOnObject(g1,g-1)
    c: Coincident(g1,g2)
    c: Vertical(g2)
    c: Coincident(g2,g3)
    c: Horizontal(g3)
    c: Coincident(g3,g4)
    c: Vertical(g4)
    c: Coincident(g4,g5)
    c: Coincident(g5,g0)
    c: Horizontal(g5)
    c: DistanceX(g0) = 5  'inner_r'
    c: DistanceX(g0,g3) = 8
    c: DistanceY(g2,g2) = 5
    c: DistanceX(g3,g3) = 20
    c: DistanceX(g3) = 13  'outer_r'
    c: DistanceY(g0) = 83.7
FEATURE [PartDesign::Revolution] Revolution005
  Angle = 360
  Angle2 = 60
  Axis = (0,2e-16,1)
  Base = (0,0,0)
  Placement = pos=(0,0,0) rot=(1,0,0;1.5708rad)
  Profile = -> Sketch235
  ReferenceAxis = -> Sketch235 [V_Axis]
  Reversed = true
  Suppressed = false
  Type = 0
FEATURE [PartDesign::Revolution] Revolution006
  Angle = 360
  Angle2 = 60
  Axis = (0,2e-16,1)
  Base = (0,0,0)
  Placement = pos=(0,0,0) rot=(1,0,0;1.5708rad)
  Profile = -> Sketch234
  ReferenceAxis = -> Sketch234 [V_Axis]
  Reversed = true
  Suppressed = false
  Type = 0
FEATURE [Part::Compound] Compound087  label="sleeve_outer_cut002"
  Links = -> [Array012]
FEATURE [PartDesign::Boolean] Boolean039
  BaseFeature = -> Revolution006
  Group = -> [Compound087]
  Suppressed = false
  Type = 1
  UsePlacement = false
FEATURE [Part::Compound] Compound088  label="sleeve_inner_cut002"
  Links = -> [Extrude032]
FEATURE [PartDesign::Boolean] Boolean040
  BaseFeature = -> Revolution005
  Group = -> [Compound088]
  Suppressed = false
  Type = 1
  UsePlacement = false
FEATURE [TechDraw::DrawViewAnnotation] Annotation
  Font = osifont
  LineSpace = 100
  LockPosition = false
  MaxWidth = -1
  Rotation = 0
  ScaleType = 0
  Text = 1 шт.
  TextSize = 5
  TextStyle = 0
  X = 81.8233
  Y = 167.816
FEATURE [TechDraw::DrawViewAnnotation] Annotation001
  Font = osifont
  LineSpace = 100
  LockPosition = false
  MaxWidth = -1
  Rotation = 0
  ScaleType = 0
  Text = 1 шт.
  TextSize = 5
  TextStyle = 0
  X = 81.8233
  Y = 167.816
FEATURE [TechDraw::DrawViewAnnotation] Annotation004
  Font = osifont
  LineSpace = 100
  LockPosition = false
  MaxWidth = -1
  Rotation = 0
  ScaleType = 0
  Text = 1 шт.
  TextSize = 5
  TextStyle = 0
  X = 73.0733
  Y = 186.077
FEATURE [TechDraw::DrawPage] Page002  label="bottom_sleeve_Page"
  KeepUpdated = true
  NextBalloonIndex = 1
  ProjectionType = 0
  Template = -> Template
  Views = -> [View004,View005,SectionView002,Dimension016,Dimension017,Dimension018,Dimension019,Dimension020,Dimension021,Dimension022,Dimension023,Annotation004]
FEATURE [Sketcher::SketchObject] Sketch236
  FullyConstrained = true
  expr: Constraints[10] = <<pillar_base_sketch>>.Constraints.length - <<led_holder_fix_extrude>>.Placement.Base.y
  sketch-geometry (5):
    g0: LineSegment StartX=-3 StartY=-3.5 StartZ=0 EndX=-3 EndY=7.1152 EndZ=0
    g1: LineSegment StartX=-3 StartY=7.1152 StartZ=0 EndX=3 EndY=7.1152 EndZ=0
    g2: LineSegment StartX=3 StartY=7.1152 StartZ=0 EndX=3 EndY=-3.5 EndZ=0
    g3: LineSegment StartX=3 StartY=-3.5 StartZ=0 EndX=-3 EndY=-3.5 EndZ=0
    g4: GeomPoint X=0 Y=1.8076 Z=0
  constraints (13):
    c: Coincident(g0,g1)
    c: Coincident(g1,g2)
    c: Coincident(g2,g3)
    c: Coincident(g3,g0)
    c: Horizontal(g1)
    c: Horizontal(g3)
    c: Vertical(g0)
    c: Vertical(g2)
    c: Symmetric(g1,g0,g4)
    c: PointOnObject(g4,g-2)
    c: DistanceY(g1) = 7.1152
    c: DistanceY(g2) = -3.5
    c: DistanceX(g1,g1) = 6
FEATURE [PartDesign::SubShapeBinder] Binder137
  BindCopyOnChange = 0
  BindMode = 0
  ClaimChildren = true
  Context = -> Body134 [Binder137.]
  Fuse = false
  MakeFace = true
  OffsetFill = false
  OffsetIntersection = false
  OffsetJoinType = 0
  OffsetOpenResult = false
  PartialLoad = false
  Relative = false
  Support = -> [Sketch236]
  _Version = 2
FEATURE [PartDesign::FeaturePython] BaseBend051  # WARN: FeaturePython — macro-defined, semantics opaque (R4)
  BendSide = 0
  BendSketch = -> Binder137
  MidPlane = false
  Reverse = false
  Suppressed = false
  length = 830
  radius = 0.1
  thickness = 0.3
FEATURE [App::Link] Link046  label="led_holder_fix_extrude001"
  LinkPlacement = pos=(4,0,5) rot=(0,1,0;-1.5708rad)
  LinkedObject = -> Extrude010
  Placement = pos=(4,0,5) rot=(0,1,0;-1.5708rad)
FEATURE [Part::Compound] Compound089
  Links = -> [Link046]
FEATURE [PartDesign::Boolean] Boolean041
  BaseFeature = -> BaseBend051
  Group = -> [Compound089]
  Suppressed = false
  Type = 1
  UsePlacement = false
FEATURE [PartDesign::Body] Body134  label="wire_holder_material_0.30ansi"
  Group = -> [Binder137,BaseBend051,Boolean041]
  Origin = -> Origin112
  Tip = -> Boolean041
FEATURE [Sketcher::SketchObject] Sketch237
  FullyConstrained = true
  expr: Constraints[11] = <<pillar_base_sketch>>.Constraints.length - <<led_holder_fix_extrude>>.Placement.Base.y - 1.5 mm
  sketch-geometry (5):
    g0: LineSegment StartX=-4 StartY=-3.5 StartZ=0 EndX=4 EndY=-3.5 EndZ=0
    g1: LineSegment StartX=4 StartY=-3.5 StartZ=0 EndX=4 EndY=5.6152 EndZ=0
    g2: LineSegment StartX=4 StartY=5.6152 StartZ=0 EndX=-4 EndY=5.6152 EndZ=0
    g3: LineSegment StartX=-4 StartY=5.6152 StartZ=0 EndX=-4 EndY=-3.5 EndZ=0
    g4: GeomPoint X=0 Y=1.0576 Z=0
  constraints (13):
    c: Coincident(g0,g1)
    c: Coincident(g1,g2)
    c: Coincident(g2,g3)
    c: Coincident(g3,g0)
    c: Horizontal(g0)
    c: Horizontal(g2)
    c: Vertical(g1)
    c: Vertical(g3)
    c: Symmetric(g2,g0,g4)
    c: PointOnObject(g4,g-2)
    c: DistanceX(g0,g0) = 8
    c: DistanceY(g1) = 5.6152
    c: DistanceY(g0) = -3.5
FEATURE [PartDesign::SubShapeBinder] Binder138
  BindCopyOnChange = 0
  BindMode = 0
  ClaimChildren = true
  Context = -> Body135 [Binder138.]
  Fuse = false
  MakeFace = true
  OffsetFill = false
  OffsetIntersection = false
  OffsetJoinType = 0
  OffsetOpenResult = false
  PartialLoad = false
  Relative = true
  Support = -> [Sketch237]
  _Version = 2
FEATURE [PartDesign::Pad] Pad038
  Direction = (0,0,1)
  Length = 10
  Length2 = 10
  Profile = -> Binder138 [Face1]
  Suppressed = false
  Type = 0
FEATURE [Part::Compound] Compound090
  Links = -> [Link046]
FEATURE [PartDesign::Boolean] Boolean042
  BaseFeature = -> Pad038
  Group = -> [Compound090]
  Suppressed = false
  Type = 1
  UsePlacement = false
FEATURE [PartDesign::Body] Body135  label="wire_holder"
  Group = -> [Binder138,Pad038,Boolean042]
  Origin = -> Origin113
  Tip = -> Boolean042
FEATURE [Sketcher::SketchObject] Sketch238
  AttachmentSupport = -> [XY_Plane113]
  FullyConstrained = true
  MapMode = 5
  sketch-geometry (10):
    g0: LineSegment StartX=-10 StartY=-23.5 StartZ=0 EndX=10 EndY=-23.5 EndZ=0
    g1: LineSegment StartX=15 StartY=-18.5 StartZ=0 EndX=15 EndY=18.5 EndZ=0
    g2: LineSegment StartX=10 StartY=23.5 StartZ=0 EndX=-10 EndY=23.5 EndZ=0
    g3: LineSegment StartX=-15 StartY=18.5 StartZ=0 EndX=-15 EndY=-18.5 EndZ=0
    g4: ArcOfCircle CenterX=-10 CenterY=-18.5 CenterZ=0 NormalX=0 NormalY=0 NormalZ=1 AngleXU=0 Radius=5 StartAngle=3.14159 EndAngle=4.71239
    g5: ArcOfCircle CenterX=10 CenterY=-18.5 CenterZ=0 NormalX=0 NormalY=0 NormalZ=1 AngleXU=0 Radius=5 StartAngle=4.71239 EndAngle=6.28319
    g6: ArcOfCircle CenterX=10 CenterY=18.5 CenterZ=0 NormalX=0 NormalY=0 NormalZ=1 AngleXU=0 Radius=5 StartAngle=2.76279e-11 EndAngle=1.5708
    g7: ArcOfCircle CenterX=-10 CenterY=18.5 CenterZ=0 NormalX=0 NormalY=0 NormalZ=1 AngleXU=0 Radius=5 StartAngle=1.5708 EndAngle=3.14159
    g8: GeomPoint X=-15 Y=-23.5 Z=0
    g9: GeomPoint X=15 Y=23.5 Z=0
  constraints (23):
    c: Tangent(g0,g4) = -1.5708
    c: Tangent(g0,g5) = -1.5708
    c: Tangent(g1,g5) = -1.5708
    c: Tangent(g1,g6) = -1.5708
    c: Tangent(g2,g6) = -1.5708
    c: Tangent(g2,g7) = -1.5708
    c: Tangent(g3,g7) = -1.5708
    c: Tangent(g3,g4) = -1.5708
    c: Horizontal(g0)
    c: Horizontal(g2)
    c: Vertical(g1)
    c: Vertical(g3)
    c: Equal(g4,g5)
    c: Equal(g5,g6)
    c: Equal(g6,g7)
    c: PointOnObject(g8,g0)
    c: PointOnObject(g8,g3)
    c: PointOnObject(g9,g1)
    c: PointOnObject(g9,g2)
    c: Distance(g1,g3) = 30
    c: Distance(g0,g2) = 47
    c: Radius(g5) = 5
    c: Symmetric(g8,g9,g-1)
FEATURE [PartDesign::Pad] Pad039
  Direction = (0,0,1)
  Length = 1.5
  Length2 = 10
  Profile = -> Sketch238
  ReferenceAxis = -> Sketch238 [N_Axis]
  Suppressed = false
  Type = 0
FEATURE [Sketcher::SketchObject] Sketch239
  FullyConstrained = true
  sketch-geometry (2):
    g0: Circle CenterX=0 CenterY=-20 CenterZ=0 NormalX=0 NormalY=0 NormalZ=1 AngleXU=0 Radius=1.7
    g1: Circle CenterX=0 CenterY=20 CenterZ=0 NormalX=0 NormalY=0 NormalZ=1 AngleXU=0 Radius=1.7
  constraints (5):
    c: PointOnObject(g0,g-2)
    c: Symmetric(g1,g0,g-1)
    c: DistanceY(g0,g1) = 40
    c: Equal(g1,g0)
    c: Diameter(g1) = 3.4
FEATURE [PartDesign::SubShapeBinder] Binder139
  BindCopyOnChange = 0
  BindMode = 0
  ClaimChildren = true
  Fuse = false
  MakeFace = true
  OffsetFill = false
  OffsetIntersection = false
  OffsetJoinType = 0
  OffsetOpenResult = false
  PartialLoad = false
  Relative = false
  Support = -> [Sketch239]
  _Version = 2
FEATURE [PartDesign::Pocket] Pocket133
  BaseFeature = -> Pad039
  Direction = (0,0,-1)
  Length = 5
  Length2 = 5
  Midplane = true
  Profile = -> Binder139
  Suppressed = false
  Type = 1
FEATURE [PartDesign::Body] Body136
  Group = -> [Sketch238,Pad039,Binder139,Pocket133]
  Origin = -> Origin114
  Tip = -> Pocket133
FEATURE [Part::Part2DObjectPython] Rectangle  # Draft 2D object (typed FeaturePython)
  Area = 2e+06
  ChamferSize = 0
  Columns = 1
  FilletRadius = 0
  Height = 1000
  Length = 2000
  MakeFace = true
  Placement = pos=(-1000,-1000,0) rot=(0,0,1;0rad)
  Rows = 1
FEATURE [Part::Extrusion] Extrude035
  Base = -> Rectangle
  Dir = (0,0,1)
  DirMode = 2
  FaceMakerClass = Part::FaceMakerBullseye
  LengthFwd = 100
  LengthRev = 0
  Solid = false
  Symmetric = false
FEATURE [Part::Cut] Cut
  Base = -> Populate045
  Tool = -> Extrude035
FEATURE [Sketcher::SketchObject] Sketch240
  FullyConstrained = true
  sketch-geometry (10):
    g0: LineSegment StartX=-22.5 StartY=-20 StartZ=0 EndX=22.5 EndY=-20 EndZ=0
    g1: LineSegment StartX=30 StartY=-12.5 StartZ=0 EndX=30 EndY=12.5 EndZ=0
    g2: LineSegment StartX=22.5 StartY=20 StartZ=0 EndX=-22.5 EndY=20 EndZ=0
    g3: LineSegment StartX=-30 StartY=12.5 StartZ=0 EndX=-30 EndY=-12.5 EndZ=0
    g4: ArcOfCircle CenterX=-22.5 CenterY=-12.5 CenterZ=0 NormalX=0 NormalY=0 NormalZ=1 AngleXU=0 Radius=7.5 StartAngle=3.14159 EndAngle=4.71239
    g5: ArcOfCircle CenterX=22.5 CenterY=-12.5 CenterZ=0 NormalX=0 NormalY=0 NormalZ=1 AngleXU=0 Radius=7.5 StartAngle=4.71239 EndAngle=6.28319
    g6: ArcOfCircle CenterX=22.5 CenterY=12.5 CenterZ=0 NormalX=0 NormalY=0 NormalZ=1 AngleXU=0 Radius=7.5 StartAngle=-7.9e-14 EndAngle=1.5708
    g7: ArcOfCircle CenterX=-22.5 CenterY=12.5 CenterZ=0 NormalX=0 NormalY=0 NormalZ=1 AngleXU=0 Radius=7.5 StartAngle=1.5708 EndAngle=3.14159
    g8: GeomPoint X=-30 Y=-20 Z=0
    g9: GeomPoint X=30 Y=20 Z=0
  constraints (23):
    c: Tangent(g0,g4) = -1.5708
    c: Tangent(g0,g5) = -1.5708
    c: Tangent(g1,g5) = -1.5708
    c: Tangent(g1,g6) = -1.5708
    c: Tangent(g2,g6) = -1.5708
    c: Tangent(g2,g7) = -1.5708
    c: Tangent(g3,g7) = -1.5708
    c: Tangent(g3,g4) = -1.5708
    c: Horizontal(g0)
    c: Horizontal(g2)
    c: Vertical(g1)
    c: Vertical(g3)
    c: Equal(g4,g5)
    c: Equal(g5,g6)
    c: Equal(g6,g7)
    c: PointOnObject(g8,g0)
    c: PointOnObject(g8,g3)
    c: PointOnObject(g9,g1)
    c: PointOnObject(g9,g2)
    c: Distance(g1,g3) = 60
    c: Distance(g0,g2) = 40
    c: Radius(g5) = 7.5
    c: Symmetric(g8,g9,g-1)
FEATURE [Sketcher::SketchObject] Sketch241
  FullyConstrained = true
  sketch-geometry (9):
    g0: LineSegment StartX=-22.5 StartY=-12.5 StartZ=0 EndX=22.5 EndY=-12.5 EndZ=0
    g1: LineSegment StartX=22.5 StartY=-12.5 StartZ=0 EndX=22.5 EndY=12.5 EndZ=0
    g2: LineSegment StartX=22.5 StartY=12.5 StartZ=0 EndX=-22.5 EndY=12.5 EndZ=0
    g3: LineSegment StartX=-22.5 StartY=12.5 StartZ=0 EndX=-22.5 EndY=-12.5 EndZ=0
    g4: GeomPoint X=0 Y=0 Z=0
    g5: Circle CenterX=22.5 CenterY=12.5 CenterZ=0 NormalX=0 NormalY=0 NormalZ=1 AngleXU=0 Radius=2.75
    g6: Circle CenterX=22.5 CenterY=-12.5 CenterZ=0 NormalX=0 NormalY=0 NormalZ=1 AngleXU=0 Radius=2.75
    g7: Circle CenterX=-22.5 CenterY=-12.5 CenterZ=0 NormalX=0 NormalY=0 NormalZ=1 AngleXU=0 Radius=2.75
    g8: Circle CenterX=-22.5 CenterY=12.5 CenterZ=0 NormalX=0 NormalY=0 NormalZ=1 AngleXU=0 Radius=2.75
  constraints (20):
    c: Coincident(g0,g1)
    c: Coincident(g1,g2)
    c: Coincident(g2,g3)
    c: Coincident(g3,g0)
    c: Horizontal(g0)
    c: Horizontal(g2)
    c: Vertical(g1)
    c: Vertical(g3)
    c: Symmetric(g2,g0,g4)
    c: Distance(g1,g3) = 45
    c: Distance(g0,g2) = 25
    c: Coincident(g4,g-1)
    c: Coincident(g5,g1)
    c: Coincident(g6,g0)
    c: Coincident(g7,g0)
    c: Coincident(g8,g2)
    c: Equal(g7,g8)
    c: Equal(g7,g5)
    c: Equal(g7,g6)
    c: Diameter(g7) = 5.5
FEATURE [PartDesign::SubShapeBinder] Binder140
  BindCopyOnChange = 0
  BindMode = 0
  ClaimChildren = true
  Fuse = false
  MakeFace = true
  OffsetFill = false
  OffsetIntersection = false
  OffsetJoinType = 0
  OffsetOpenResult = false
  PartialLoad = false
  Relative = false
  Support = -> [Sketch240]
  _Version = 2
FEATURE [PartDesign::Pad] Pad040
  Direction = (0,0,1)
  Length = 3
  Length2 = 10
  Profile = -> Binder140
  Suppressed = false
  Type = 0
FEATURE [Part::Extrusion] Extrude036
  Base = -> Sketch241
  Dir = (0,0,1)
  DirMode = 2
  FaceMakerClass = Part::FaceMakerBullseye
  LengthFwd = 10
  LengthRev = 0
  Placement = pos=(0,0,-1) rot=(0,0,1;0rad)
  Solid = true
  Symmetric = false
FEATURE [Part::Compound] Compound091
  Links = -> [Extrude036]
FEATURE [PartDesign::Boolean] Boolean043
  BaseFeature = -> Pad040
  Group = -> [Compound091]
  Suppressed = false
  Type = 1
  UsePlacement = false
FEATURE [PartDesign::Body] Body137  label="wheel_proxy"
  Group = -> [Binder140,Pad040,Boolean043]
  Origin = -> Origin115
  Tip = -> Boolean043
FEATURE [Sketcher::SketchObject] Sketch242
  AttachmentOffset = pos=(0,35,0) rot=(0,0,1;0rad)
  AttachmentSupport = -> [Local_CS004]
  FullyConstrained = true
  MapMode = 5
  Placement = pos=(284.188,-181.72,35) rot=(-0.131421,0.700974,0.700974;3.40294rad)
  sketch-geometry (3):
    g0: Circle CenterX=-6.5 CenterY=0 CenterZ=0 NormalX=0 NormalY=0 NormalZ=1 AngleXU=0 Radius=1.7
    g1: GeomPoint X=-12 Y=0 Z=0
    g2: GeomPoint X=-1 Y=0 Z=0
  constraints (6):
    c: Diameter(g0) = 3.4
    c: PointOnObject(g1,g-1)
    c: PointOnObject(g2,g-1)
    c: DistanceX(g2) = -1
    c: DistanceX(g1) = -12
    c: Symmetric(g2,g1,g0)
FEATURE [PartDesign::Pocket] Pocket134
  BaseFeature = -> MultiTransform001
  Direction = (0.362233,-0.932087,0)
  Length = 5
  Length2 = 5
  Midplane = true
  Profile = -> Sketch242
  ReferenceAxis = -> Sketch242 [N_Axis]
  Suppressed = false
  Type = 1
FEATURE [PartDesign::LinearPattern] LinearPattern001
  Direction = -> Z_Axis097
  Length = 355
  Mode = 0
  Occurrences = 2
  Offset = 355
  Suppressed = false
FEATURE [PartDesign::Mirrored] Mirrored019
  MirrorPlane = -> YZ_Plane097
  Suppressed = false
FEATURE [PartDesign::MultiTransform] MultiTransform
  BaseFeature = -> Pocket134
  Originals = -> [Pocket134]
  Suppressed = false
  Transformations = -> [LinearPattern001,Mirrored019]
FEATURE [PartDesign::Body] Body121  label="sector_plexiglass_material_0.30ansi"
  Group = -> [Binder128,BaseBend049,Sketch208,Local_CS004,Pocket124,MultiTransform001,LinearPattern,Mirrored015,Sketch242,Pocket134,MultiTransform,LinearPattern001,Mirrored019]
  Origin = -> Origin097
  Tip = -> MultiTransform
FEATURE [Sketcher::SketchObject] Sketch243
  AttachmentSupport = -> [XY_Plane115]
  FullyConstrained = true
  MapMode = 5
  expr: Constraints[1] = <<bottom_bearing_Sketch>>.Constraints.outer_r * 2 + 50 mm
  sketch-geometry (1):
    g0: Circle CenterX=0 CenterY=0 CenterZ=0 NormalX=0 NormalY=0 NormalZ=1 AngleXU=0 Radius=75
  constraints (2):
    c: Coincident(g0,g-1)
    c: Diameter(g0) = 150
FEATURE [PartDesign::Pad] Pad041
  Direction = (0,0,1)
  Length = 18
  Length2 = 10
  Profile = -> Sketch243
  ReferenceAxis = -> Sketch243 [N_Axis]
  Suppressed = false
  Type = 0
FEATURE [Sketcher::SketchObject] Sketch244
  AttachmentOffset = pos=(0,0,18) rot=(0,0,1;0rad)
  AttachmentSupport = -> [XY_Plane115]
  FullyConstrained = true
  MapMode = 5
  Placement = pos=(0,0,18) rot=(0,0,1;0rad)
  expr: .AttachmentOffset.Base.z = <<Pad041>>.Length
  expr: .Constraints.inner_r = <<bottom_bearing_Sketch>>.Constraints.inner_r * 2 - 1 mm
  expr: .Constraints.outer_r = <<bottom_bearing_Sketch>>.Constraints.outer_r * 2 + 1 mm
  sketch-geometry (2):
    g0: Circle CenterX=0 CenterY=0 CenterZ=0 NormalX=0 NormalY=0 NormalZ=1 AngleXU=0 Radius=37
    g1: Circle CenterX=0 CenterY=0 CenterZ=0 NormalX=0 NormalY=0 NormalZ=1 AngleXU=0 Radius=50.5
  constraints (4):
    c: Coincident(g0,g-1)
    c: Coincident(g1,g0)
    c: Diameter(g0) = 74  'inner_r'
    c: Diameter(g1) = 101  'outer_r'
FEATURE [PartDesign::Pocket] Pocket135
  BaseFeature = -> Pad041
  Direction = (0,0,-1)
  Length = 5
  Length2 = 5
  Profile = -> Sketch244
  ReferenceAxis = -> Sketch244 [N_Axis]
  Suppressed = false
  Type = 0
FEATURE [Sketcher::SketchObject] Sketch245
  AttachmentSupport = -> [XY_Plane115]
  FullyConstrained = true
  MapMode = 5
  sketch-geometry (1):
    g0: Circle CenterX=0 CenterY=0 CenterZ=0 NormalX=0 NormalY=0 NormalZ=1 AngleXU=0 Radius=5.25
  constraints (2):
    c: Coincident(g0,g-1)
    c: Diameter(g0) = 10.5
FEATURE [Sketcher::SketchObject] Sketch246
  AttachmentSupport = -> [XY_Plane116]
  FullyConstrained = true
  MapMode = 5
  sketch-geometry (7):
    g0: LineSegment StartX=7.50555 StartY=0 StartZ=0 EndX=3.75278 EndY=6.5 EndZ=0
    g1: LineSegment StartX=3.75278 StartY=6.5 StartZ=0 EndX=-3.75278 EndY=6.5 EndZ=0
    g2: LineSegment StartX=-3.75278 StartY=6.5 StartZ=0 EndX=-7.50555 EndY=4.3228e-12 EndZ=0
    g3: LineSegment StartX=-7.50555 StartY=4.3229e-12 StartZ=0 EndX=-3.75278 EndY=-6.5 EndZ=0
    g4: LineSegment StartX=-3.75278 StartY=-6.5 StartZ=0 EndX=3.75278 EndY=-6.5 EndZ=0
    g5: LineSegment StartX=3.75278 StartY=-6.5 StartZ=0 EndX=7.50555 EndY=0 EndZ=0
    g6: Circle CenterX=0 CenterY=0 CenterZ=0 NormalX=0 NormalY=0 NormalZ=1 AngleXU=0 Radius=7.50555
  constraints (16):
    c: Coincident(g0,g1)
    c: Coincident(g1,g2)
    c: Coincident(g2,g3)
    c: Coincident(g3,g4)
    c: Coincident(g4,g5)
    c: Coincident(g5,g0)
    c: Equal(g0, g1-g5) x5
    c: PointOnObject(g0,g6)
    c: PointOnObject(g1,g6)
    c: PointOnObject(g2,g6)
    c: PointOnObject(g3,g6)
    c: PointOnObject(g4,g6)
    c: PointOnObject(g5,g6)
    c: Coincident(g6,g-1)
    c: PointOnObject(g5,g-1)
    c: DistanceY(g4,g0) = 13
FEATURE [PartDesign::Pad] Pad042
  Direction = (0,0,1)
  Length = 5
  Length2 = 10
  Profile = -> Sketch246
  ReferenceAxis = -> Sketch246 [N_Axis]
  Suppressed = false
  Type = 0
FEATURE [Sketcher::SketchObject] Sketch247
  AttachmentSupport = -> [XY_Plane116]
  FullyConstrained = true
  MapMode = 5
  sketch-geometry (1):
    g0: Circle CenterX=0 CenterY=0 CenterZ=0 NormalX=0 NormalY=0 NormalZ=1 AngleXU=0 Radius=4.25
  constraints (2):
    c: Coincident(g0,g-1)
    c: Diameter(g0) = 8.5
FEATURE [PartDesign::Pad] Pad043
  BaseFeature = -> Pad042
  Direction = (0,0,1)
  Length = 20
  Length2 = 10
  Profile = -> Sketch247
  ReferenceAxis = -> Sketch247 [N_Axis]
  Suppressed = false
  Type = 0
FEATURE [PartDesign::Body] Body139
  Group = -> [Sketch246,Pad042,Sketch247,Pad043]
  Origin = -> Origin117
  Placement = pos=(60,0,0) rot=(0,0,1;0rad)
  Tip = -> Pad043
  expr: .Placement.Base.x = <<bottom_bearing_Sketch>>.Constraints.outer_r + 10 mm
FEATURE [Part::FeaturePython] PolarArray010  # WARN: FeaturePython — macro-defined, semantics opaque (R4)
  Alignment = 0
  AttacherType = Attacher::AttachEngine3D
  CellStart = A1
  Count = 5
  DistributionLaw = 0
  EndInclusive = false
  ExposePlacement = false
  FlipX = false
  FlipZ = false
  GeneratorMode = 0
  MarkerShape = 1
  MarkerSize = 0
  NumElements = 5
  OrientMode = 2
  Placement = pos=(0,0,0) rot=(0,0,1;0.628319rad)
  Radius = 64
  Reverse = false
  SpanEnd = 360
  SpanStart = 0
  Step = 72
  Type = lattice2PolarArray2.PolarArray
  UseArcRadius = false
  UseArcRange = 0
  VSGVersion = 1
  Values = 0.0 | 72.0 | 144.0 | 216.0 | 288.0
  ValuesSource = 2
  isLattice = 1
  expr: .Placement.Rotation.Angle = 360 deg / (Count * 2)
  expr: Radius = <<bottom_bearing_Sketch>>.Constraints.outer_r + 14 mm
FEATURE [Part::Cylinder] Cylinder009  label="hole_4mm"
  Angle = 360
  AttacherType = Attacher::AttachEngine3D
  FirstAngle = 0
  Height = 40
  Radius = 2
  SecondAngle = 0
FEATURE [Part::FeaturePython] Populate054  label="Populate PolarArray010 with hole_4mm"  # WARN: FeaturePython — macro-defined, semantics opaque (R4)
  Copying = 0
  ExposePlacement = false
  MarkerShape = 1
  MarkerSize = 0
  NumElements = 0
  Object = -> Cylinder009
  OutputCompounding = 1
  PlacementsTo = -> PolarArray010
  Referencing = 0
  Type = lattice2PopulateCopies.LatticePopulateCopies
  isLattice = 0
FEATURE [Part::Cylinder] Cylinder010
  Angle = 360
  AttacherType = Attacher::AttachEngine3D
  FirstAngle = 0
  Height = 20
  Radius = 5.5
  SecondAngle = 0
FEATURE [Part::MultiFuse] Fusion
  Shapes = -> [Body139,Populate054,Cylinder010]
FEATURE [PartDesign::Boolean] Boolean044
  BaseFeature = -> Pocket135
  Group = -> [Fusion]
  Suppressed = false
  Type = 1
  UsePlacement = false
FEATURE [PartDesign::Body] Body138
  Group = -> [Sketch243,Pad041,Sketch244,Pocket135,Sketch245,Boolean044]
  Origin = -> Origin116
  Tip = -> Boolean044
FEATURE [Sketcher::SketchObject] Sketch248
  AttachmentOffset = pos=(0,0,18) rot=(0,0,1;0rad)
  AttachmentSupport = -> [XY_Plane117]
  FullyConstrained = true
  MapMode = 5
  Placement = pos=(0,0,18) rot=(0,0,1;0rad)
  expr: .AttachmentOffset.Base.z = <<Pad044>>.Length
  expr: .Constraints.inner_r = <<bottom_bearing_Sketch>>.Constraints.inner_r * 2 - 1 mm
  expr: .Constraints.outer_r = <<bottom_bearing_Sketch>>.Constraints.outer_r * 2 + 1 mm
  sketch-geometry (2):
    g0: Circle CenterX=0 CenterY=0 CenterZ=0 NormalX=0 NormalY=0 NormalZ=1 AngleXU=0 Radius=37
    g1: Circle CenterX=0 CenterY=0 CenterZ=0 NormalX=0 NormalY=0 NormalZ=1 AngleXU=0 Radius=50.5
  constraints (4):
    c: Coincident(g0,g-1)
    c: Coincident(g1,g0)
    c: Diameter(g0) = 74  'inner_r'
    c: Diameter(g1) = 101  'outer_r'
FEATURE [Sketcher::SketchObject] Sketch249
  AttachmentSupport = -> [XY_Plane117]
  FullyConstrained = true
  MapMode = 5
  expr: Constraints[1] = <<bottom_bearing_Sketch>>.Constraints.outer_r * 2 + 50 mm
  sketch-geometry (1):
    g0: Circle CenterX=0 CenterY=0 CenterZ=0 NormalX=0 NormalY=0 NormalZ=1 AngleXU=0 Radius=75
  constraints (2):
    c: Coincident(g0,g-1)
    c: Diameter(g0) = 150
FEATURE [PartDesign::Pad] Pad044
  Direction = (0,0,1)
  Length = 18
  Length2 = 10
  Profile = -> Sketch249
  ReferenceAxis = -> Sketch249 [N_Axis]
  Suppressed = false
  Type = 0
FEATURE [Sketcher::SketchObject] Sketch250
  AttachmentSupport = -> [XY_Plane117]
  FullyConstrained = true
  MapMode = 5
  sketch-geometry (1):
    g0: Circle CenterX=0 CenterY=0 CenterZ=0 NormalX=0 NormalY=0 NormalZ=1 AngleXU=0 Radius=5.25
  constraints (2):
    c: Coincident(g0,g-1)
    c: Diameter(g0) = 10.5
FEATURE [PartDesign::Pocket] Pocket136
  BaseFeature = -> Pad044
  Direction = (0,0,-1)
  Length = 5
  Length2 = 5
  Profile = -> Sketch248
  ReferenceAxis = -> Sketch248 [N_Axis]
  Suppressed = false
  Type = 0
FEATURE [Part::Cylinder] Cylinder011
  Angle = 360
  AttacherType = Attacher::AttachEngine3D
  FirstAngle = 0
  Height = 10
  Radius = 13.5
  SecondAngle = 0
FEATURE [Part::MultiFuse] Fusion001
  Shapes = -> [Body139,Populate054,Cylinder010,Cylinder011]
FEATURE [PartDesign::Boolean] Boolean045
  BaseFeature = -> Pocket136
  Group = -> [Fusion001]
  Suppressed = false
  Type = 1
  UsePlacement = false
FEATURE [PartDesign::Body] Body140
  Group = -> [Sketch249,Pad044,Sketch248,Pocket136,Sketch250,Boolean045]
  Origin = -> Origin118
  Tip = -> Boolean045
FEATURE [Part::Cylinder] Cylinder012
  Angle = 360
  AttacherType = Attacher::AttachEngine3D
  FirstAngle = 0
  Height = 30
  Placement = pos=(8.9e-15,-145.633,0) rot=(0,0,1;0rad)
  Radius = 4.25
  SecondAngle = 0
  expr: .Placement.Base.x = 145.6327 * cos(-90 deg)
  expr: .Placement.Base.y = 145.6327 * sin(-90 deg)
FEATURE [PartDesign::Boolean] Boolean027
  BaseFeature = -> Pocket106
  Group = -> [Populate041,Cylinder012]
  Suppressed = false
  Type = 1
  UsePlacement = false
FEATURE [Part::Compound] Compound069  label="basement_bottom_cut1"
  Links = -> [Populate040,Populate033,Populate028,Extrude029,Extrude030,Populate045,Cylinder012]
FEATURE [PartDesign::Boolean] Boolean026
  BaseFeature = -> Pad002
  Group = -> [Compound069]
  Suppressed = false
  Type = 1
  UsePlacement = false
FEATURE [Part::Compound] Compound071  label="basement_bottom_proxy_cut1"
  Links = -> [Populate028,Extrude029,Extrude030,Cut,Cylinder012]
FEATURE [PartDesign::Boolean] Boolean029
  BaseFeature = -> Pad004
  Group = -> [Compound071]
  Suppressed = false
  Type = 1
  UsePlacement = false
FEATURE [Part::Offset2D] Offset2D
  Fill = false
  Intersection = false
  Join = 0
  Mode = 1
  SelfIntersection = false
  Source = -> Link040
  Value = 0.15
FEATURE [Part::Compound] Compound062  label="hub_top"
  Links = -> [Link039,Offset2D]
FEATURE [Part::Extrusion] Extrude026  label="hub_top_extrude"
  Base = -> Compound062
  Dir = (0,0,1)
  DirMode = 2
  FaceMakerClass = Part::FaceMakerBullseye
  LengthFwd = 20
  LengthRev = 0
  Solid = true
  Symmetric = false
FEATURE [Part::Compound] Compound067  label="basement_v3_top_cut"
  Links = -> [Populate037,Extrude026]
FEATURE [PartDesign::Boolean] Boolean024
  BaseFeature = -> PolarPattern010
  Group = -> [Compound067]
  Suppressed = false
  Type = 1
  UsePlacement = false
FEATURE [PartDesign::Body] Body119  label="basement_v3_top_material_0.50ansi"
  Group = -> [Binder127,Sketch213,BaseBend048,Pad031,Pocket126,Bend028,PDW_Add001,PolarPattern010,Boolean024]
  Origin = -> Origin095
  Tip = -> Pocket126
FEATURE [App::Part] Part021  label="basement_v3"
  Group = -> [Body118,Body119]
  Origin = -> Origin093
FEATURE [Sketcher::SketchObject] Sketch251
  FullyConstrained = true
  expr: Constraints[6] = <<pillar3_BaseBend>>.length - <<pillar3_hat_fix_placement>>.Placement.Base.z - 6 mm
  sketch-geometry (3):
    g0: LineSegment StartX=0 StartY=70 StartZ=0 EndX=1e-16 EndY=0 EndZ=0
    g1: LineSegment StartX=1e-16 StartY=0 StartZ=0 EndX=84 EndY=0 EndZ=0
    g2: LineSegment StartX=84 StartY=0 StartZ=0 EndX=84 EndY=30 EndZ=0
  constraints (9):
    c: PointOnObject(g0,g-2)
    c: Coincident(g0,g-1)
    c: Coincident(g0,g1)
    c: PointOnObject(g1,g-1)
    c: Coincident(g1,g2)
    c: Vertical(g2)
    c: Distance(g1) = 84
    c: DistanceY(g0,g0) = 70
    c: DistanceY(g2,g2) = 30
FEATURE [PartDesign::SubShapeBinder] Binder141
  BindCopyOnChange = 0
  BindMode = 0
  ClaimChildren = true
  Fuse = false
  MakeFace = true
  OffsetFill = false
  OffsetIntersection = false
  OffsetJoinType = 0
  OffsetOpenResult = false
  PartialLoad = false
  Relative = false
  Support = -> [Sketch008]
  _Version = 2
  expr: Support = <<pillar_base_sketch>>._self
FEATURE [PartDesign::FeaturePython] BaseBend052  label="pillar3_BaseBend"  # WARN: FeaturePython — macro-defined, semantics opaque (R4)
  BendSide = 1
  BendSketch = -> Binder141
  MidPlane = false
  Reverse = false
  Suppressed = false
  length = 1684
  radius = 2
  thickness = 2
FEATURE [Sketcher::SketchObject] Sketch252
  FullyConstrained = false
  expr: Constraints[7] = <<pillar_base_sketch>>.Constraints.width / 2 - 2 mm - 1.5 mm
  sketch-geometry (8):
    g0: LineSegment StartX=0 StartY=0 StartZ=0 EndX=112.583 EndY=65 EndZ=0
    g1: LineSegment StartX=112.583 StartY=65 StartZ=0 EndX=111.083 EndY=67.5981 EndZ=0
    g2: ArcOfCircle CenterX=343.601 CenterY=370 CenterZ=0 NormalX=0 NormalY=0 NormalZ=1 AngleXU=0 Radius=328.801 StartAngle=3.14159 EndAngle=3.34165
    g3: LineSegment StartX=14.8 StartY=370 StartZ=0 EndX=14.8 EndY=378 EndZ=0
    g4: LineSegment StartX=12.8 StartY=380 StartZ=0 EndX=0 EndY=380 EndZ=0
    g5: ArcOfCircle CenterX=12.8 CenterY=378 CenterZ=0 NormalX=0 NormalY=0 NormalZ=1 AngleXU=0 Radius=2 StartAngle=-8e-15 EndAngle=1.5708
    g6: GeomPoint X=14.8 Y=380 Z=0
    g7: ArcOfCircle CenterX=792.523 CenterY=461.028 CenterZ=0 NormalX=0 NormalY=0 NormalZ=1 AngleXU=0 Radius=786.859 StartAngle=3.34165 EndAngle=3.66519
  constraints (20):
    c: Coincident(g0,g-1)
    c: Coincident(g1,g0)
    c: Angle(g0) = 0.523599
    c: Perpendicular(g0,g1)
    c: Tangent(g3,g2) = 1.5708
    c: Vertical(g3)
    c: Distance(g1) = 3
    c: DistanceX(g2) = 14.8
    c: DistanceY(g2) = 370
    c: DistanceY(g3,g6) = 10
    c: PointOnObject(g4,g-2)
    c: Horizontal(g4)
    c: PointOnObject(g6,g3)
    c: PointOnObject(g6,g4)
    c: Tangent(g3,g5) = -1.5708
    c: Tangent(g4,g5) = -1.5708
    c: Radius(g5) = 2
    c: Distance(g0) = 130
    c: Tangent(g7,g1) = 1.5708
    c: Tangent(g7,g2) = -1.5708
FEATURE [Sketcher::SketchObject] Sketch253
  AttachmentSupport = -> [YZ_Plane121]
  ExternalGeometry = -> [Binder141]
  FullyConstrained = true
  MapMode = 5
  Placement = pos=(0,0,0) rot=(0.57735,0.57735,0.57735;2.0944rad)
  sketch-geometry (3):
    g0: LineSegment StartX=14 StartY=0 StartZ=0 EndX=19 EndY=0 EndZ=0
    g1: LineSegment StartX=19 StartY=0 StartZ=0 EndX=19 EndY=5 EndZ=0
    g2: ArcOfCircle CenterX=14 CenterY=5 CenterZ=0 NormalX=0 NormalY=0 NormalZ=1 AngleXU=0 Radius=5 StartAngle=4.71239 EndAngle=6.28319
  constraints (7):
    c: PointOnObject(g0,g-3)
    c: Coincident(g0,g-3)
    c: Coincident(g1,g0)
    c: Vertical(g1)
    c: Tangent(g2,g1) = -1.5708
    c: Tangent(g2,g0) = -1.5708
    c: Radius(g2) = 5
FEATURE [PartDesign::Pocket] Pocket137
  BaseFeature = -> BaseBend052
  Direction = (-1,0,0)
  Length = 5
  Length2 = 5
  Midplane = true
  Profile = -> Sketch253
  ReferenceAxis = -> Sketch253 [N_Axis]
  Suppressed = false
  Type = 1
FEATURE [PartDesign::SubShapeBinder] Binder142
  BindCopyOnChange = 0
  BindMode = 0
  ClaimChildren = true
  Context = -> Body142 [Binder142.]
  Fuse = false
  MakeFace = true
  OffsetFill = false
  OffsetIntersection = false
  OffsetJoinType = 0
  OffsetOpenResult = false
  PartialLoad = false
  Relative = true
  Support = -> [Connect005]
  _Version = 2
FEATURE [PartDesign::Pad] Pad045
  Direction = (0,0,1)
  Length = 3
  Length2 = 10
  Profile = -> Binder142
  Refine = true
  Suppressed = false
  Type = 0
FEATURE [Sketcher::SketchObject] Sketch254  label="hat3_border"
  FullyConstrained = true
  expr: Constraints[7] = 365
  sketch-geometry (7):
    g0: LineSegment StartX=0 StartY=0 StartZ=0 EndX=113.449 EndY=65.5 EndZ=0
    g1: LineSegment StartX=113.449 StartY=65.5 StartZ=0 EndX=111.949 EndY=68.0981 EndZ=0
    g2: ArcOfCircle CenterX=1199.51 CenterY=696.004 CenterZ=0 NormalX=0 NormalY=0 NormalZ=1 AngleXU=0 Radius=1255.81 StartAngle=3.57233 EndAngle=3.66519
    g3: GeomPoint X=14.8 Y=365 Z=0
    g4: LineSegment StartX=14.8 StartY=365 StartZ=0 EndX=14.8 EndY=0 EndZ=0
    g5: ArcOfCircle CenterX=464.8 CenterY=365 CenterZ=0 NormalX=0 NormalY=0 NormalZ=1 AngleXU=0 Radius=450 StartAngle=3.14159 EndAngle=3.57233
    g6: LineSegment StartX=58.4082 StartY=171.657 StartZ=0 EndX=55.903 EndY=177.109 EndZ=0
  constraints (18):
    c: Coincident(g-1,g0)
    c: Coincident(g0,g1)
    c: Angle(g0) = 0.523599
    c: Perpendicular(g1,g0)
    c: Distance(g0) = 131  'min_r'
    c: Distance(g1) = 3
    c: DistanceX(g3) = 14.8
    c: DistanceY(g3) = 365
    c: Coincident(g4,g3)
    c: PointOnObject(g4,g-1)
    c: Vertical(g4)
    c: Coincident(g5,g3)
    c: Tangent(g2,g1) = 1.5708
    c: Radius(g5) = 450
    c: Distance(g6) = 6
    c: Tangent(g6,g2) = 1.5708
    c: Tangent(g6,g5) = 1.5708
    c: Tangent(g5,g4)
FEATURE [Sketcher::SketchObject] Sketch255
  FullyConstrained = true
  expr: Constraints[3] = <<pillar_base_sketch>>.Constraints.width / 2 - 2 mm - 1.5 mm
  expr: Constraints[4] = <<pillar_placement>>.Placement.Base.y - <<pillar_base_sketch>>.Constraints.length
  expr: Constraints[7] = <<pillar_placement>>.Placement.Base.y - 15 mm
  sketch-geometry (4):
    g0: LineSegment StartX=0 StartY=369 StartZ=0 EndX=11.8 EndY=369 EndZ=0
    g1: LineSegment StartX=14.8 StartY=366 StartZ=0 EndX=14.8 EndY=365 EndZ=0
    g2: GeomPoint X=14.8 Y=369 Z=0
    g3: ArcOfCircle CenterX=11.8 CenterY=366 CenterZ=0 NormalX=0 NormalY=0 NormalZ=1 AngleXU=0 Radius=3 StartAngle=4.81e-14 EndAngle=1.5708
  constraints (11):
    c: Horizontal(g0)
    c: Vertical(g1)
    c: PointOnObject(g0,g-2)
    c: DistanceX(g1) = 14.8
    c: DistanceY(g1) = 365
    c: PointOnObject(g2,g0)
    c: PointOnObject(g2,g1)
    c: DistanceY(g0) = 369
    c: Tangent(g3,g0) = 1.5708
    c: Tangent(g3,g1) = 1.5708
    c: Radius(g3) = 3
FEATURE [Part::Compound] Compound093
  Links = -> [Sketch254,Sketch255]
FEATURE [Part::Mirroring] Part__Mirroring034  label="Sketch252 (Mirror #31)"
  Base = (0,0,0)
  Normal = (1,0,0)
  Source = -> Compound093
FEATURE [Part::Compound] Compound092
  Links = -> [Part__Mirroring034,Compound093]
FEATURE [Part::FeaturePython] Array013  # Draft array (typed FeaturePython)
  Angle = 360
  ArrayType = 1
  Axis = (0,0,1)
  Base = -> Compound092
  Center = (0,0,0)
  Count = 3
  Fuse = true
  IntervalAxis = (0,0,0)
  IntervalX = (50,0,0)
  IntervalY = (0,50,0)
  IntervalZ = (0,0,50)
  NumberCircles = 3
  NumberPolar = 3
  NumberX = 2
  NumberY = 2
  NumberZ = 1
  RadialDistance = 50
  Symmetry = 1
  TangentialDistance = 25
FEATURE [Part::FeaturePython] Connect005  # WARN: FeaturePython — macro-defined, semantics opaque (R4)
  Objects = -> [Array013]
  Tolerance = 0
FEATURE [PartDesign::SubShapeBinder] Binder143
  BindCopyOnChange = 0
  BindMode = 0
  ClaimChildren = true
  Fuse = false
  MakeFace = true
  OffsetFill = false
  OffsetIntersection = false
  OffsetJoinType = 0
  OffsetOpenResult = false
  PartialLoad = false
  Placement = pos=(0,0,0) rot=(0,-1,0;1.5708rad)
  Relative = false
  Support = -> [Sketch251]
  _Version = 2
FEATURE [PartDesign::FeaturePython] BaseBend053  label="pillar3_hat_fix_BaseBend"  # WARN: FeaturePython — macro-defined, semantics opaque (R4)
  BendSide = 1
  BendSketch = -> Binder143
  MidPlane = true
  Reverse = false
  Suppressed = false
  length = 28.6
  radius = 2
  thickness = 1.5
  expr: length = <<pillar_base_sketch>>.Constraints.width - 8 mm
FEATURE [Sketcher::SketchObject] Sketch256
  AttachmentSupport = -> [XY_Plane124]
  ExternalGeometry = -> [Binder143]
  FullyConstrained = true
  MapMode = 5
  expr: Constraints[12] = <<pillar3_hat_fix_BaseBend>>.length
  sketch-geometry (6):
    g0: LineSegment StartX=9.3 StartY=70 StartZ=0 EndX=14.3 EndY=70 EndZ=0
    g1: LineSegment StartX=14.3 StartY=70 StartZ=0 EndX=14.3 EndY=65 EndZ=0
    g2: LineSegment StartX=-14.3 StartY=65 StartZ=0 EndX=-14.3 EndY=70 EndZ=0
    g3: LineSegment StartX=-14.3 StartY=70 StartZ=0 EndX=-9.3 EndY=70 EndZ=0
    g4: ArcOfCircle CenterX=9.3 CenterY=65 CenterZ=0 NormalX=0 NormalY=0 NormalZ=1 AngleXU=0 Radius=5 StartAngle=4e-16 EndAngle=1.5708
    g5: ArcOfCircle CenterX=-9.3 CenterY=65 CenterZ=0 NormalX=0 NormalY=0 NormalZ=1 AngleXU=0 Radius=5 StartAngle=1.5708 EndAngle=3.14159
  constraints (15):
    c: Coincident(g0,g1)
    c: Coincident(g2,g3)
    c: Tangent(g5,g2) = 1.5708
    c: Tangent(g5,g3) = 1.5708
    c: Tangent(g4,g1) = 1.5708
    c: Tangent(g4,g0) = 1.5708
    c: Equal(g4,g5)
    c: Radius(g5) = 5
    c: Parallel(g1,g-3)
    c: Perpendicular(g-3,g0)
    c: Perpendicular(g-3,g3)
    c: Parallel(g2,g-3)
    c: DistanceX(g2,g0) = 28.6
    c: Horizontal(g2,g0)
    c: Symmetric(g0,g2,g-3)
FEATURE [Sketcher::SketchObject] Sketch257
  AttachmentOffset = pos=(0,0,4) rot=(0,0,1;0rad)
  AttachmentSupport = -> [XY_Plane124]
  ExternalGeometry = -> [Binder143]
  FullyConstrained = true
  MapMode = 5
  Placement = pos=(0,0,4) rot=(0,0,1;0rad)
  expr: Constraints[13] = <<pillar3_hat_fix_BaseBend>>.length
  sketch-geometry (6):
    g0: LineSegment StartX=9.3 StartY=30 StartZ=0 EndX=14.3 EndY=30 EndZ=0
    g1: LineSegment StartX=14.3 StartY=30 StartZ=0 EndX=14.3 EndY=25 EndZ=0
    g2: LineSegment StartX=-14.3 StartY=25 StartZ=0 EndX=-14.3 EndY=30 EndZ=0
    g3: LineSegment StartX=-14.3 StartY=30 StartZ=0 EndX=-9.3 EndY=30 EndZ=0
    g4: ArcOfCircle CenterX=9.3 CenterY=25 CenterZ=0 NormalX=0 NormalY=0 NormalZ=1 AngleXU=0 Radius=5 StartAngle=3e-16 EndAngle=1.5708
    g5: ArcOfCircle CenterX=-9.3 CenterY=25 CenterZ=0 NormalX=0 NormalY=0 NormalZ=1 AngleXU=0 Radius=5 StartAngle=1.5708 EndAngle=3.14159
  constraints (15):
    c: Coincident(g0,g1)
    c: Coincident(g2,g3)
    c: Tangent(g5,g2) = 1.5708
    c: Tangent(g5,g3) = 1.5708
    c: Tangent(g4,g1) = 1.5708
    c: Tangent(g4,g0) = 1.5708
    c: Equal(g4,g5)
    c: Radius(g4) = 5
    c: Symmetric(g2,g0,g-3)
    c: Parallel(g2,g-3)
    c: Parallel(g-3,g1)
    c: Perpendicular(g0,g1)
    c: Horizontal(g0,g-3)
    c: DistanceX(g2,g0) = 28.6
    c: Perpendicular(g-3,g3)
FEATURE [PartDesign::CoordinateSystem] Local_CS005
  AttacherType = Attacher::AttachEngine3D
  AttachmentSupport = -> [XY_Plane124]
  MapMode = 5
FEATURE [PartDesign::CoordinateSystem] Local_CS006  label="pillar3_base"
  AttacherType = Attacher::AttachEngine3D
  AttachmentSupport = -> [XY_Plane121]
  MapMode = 5
FEATURE [PartDesign::CoordinateSystem] Local_CS007  label="pillar3_hat_fix_Local_CS"
  AttacherType = Attacher::AttachEngine3D
  AttachmentOffset = pos=(0,2,1594) rot=(0,0,1;0rad)
  AttachmentSupport = -> [XY_Plane121]
  MapMode = 5
  Placement = pos=(0,2,1594) rot=(0,0,1;0rad)
  expr: AttachmentOffset = <<pillar3_hat_fix_placement>>.Placement
FEATURE [Sketcher::SketchObject] Sketch258
  FullyConstrained = true
  sketch-geometry (2):
    g0: Circle CenterX=0 CenterY=10 CenterZ=0 NormalX=0 NormalY=0 NormalZ=1 AngleXU=0 Radius=1.7
    g1: Circle CenterX=0 CenterY=78 CenterZ=0 NormalX=0 NormalY=0 NormalZ=1 AngleXU=0 Radius=1.7
  constraints (6):
    c: PointOnObject(g0,g-2)
    c: PointOnObject(g1,g-2)
    c: Equal(g1,g0)
    c: Diameter(g1) = 3.4
    c: DistanceY(g0) = 10
    c: DistanceY(g1) = 78
FEATURE [Part::Extrusion] Extrude037
  Base = -> Sketch258
  Dir = (0,0,1)
  DirMode = 2
  FaceMakerClass = Part::FaceMakerBullseye
  LengthFwd = 10
  LengthRev = 0
  Solid = true
  Symmetric = true
FEATURE [Part::FeaturePython] Placment033  # WARN: FeaturePython — macro-defined, semantics opaque (R4)
  AttacherType = Attacher::AttachEngine3D
  ExposePlacement = true
  MarkerShape = 1
  MarkerSize = 5
  NumElements = 1
  Placement = pos=(0,0,0) rot=(0,0.707107,0.707107;3.14159rad)
  Type = lattice2AttachablePlacement.AttachablePlacement
  isLattice = 1
FEATURE [Part::FeaturePython] Populate055  label="Populate Placment033 with Extrude037"  # WARN: FeaturePython — macro-defined, semantics opaque (R4)
  Copying = 0
  ExposePlacement = false
  MarkerShape = 1
  MarkerSize = 0
  NumElements = 0
  Object = -> Extrude037
  OutputCompounding = 2
  PlacementsTo = -> Placment033
  Referencing = 0
  Type = lattice2PopulateCopies.LatticePopulateCopies
  isLattice = 0
FEATURE [PartDesign::Plane] DatumPlane007
  AttachmentOffset = pos=(0,0,842) rot=(0,0,1;0rad)
  AttachmentSupport = -> [XY_Plane121]
  Length = 60
  MapMode = 5
  Placement = pos=(0,0,842) rot=(0,0,1;0rad)
  ResizeMode = 0
  Width = 60
  expr: .AttachmentOffset.Base.z = <<pillar3_BaseBend>>.length / 2
FEATURE [PartDesign::Mirrored] Mirrored020
  BaseFeature = -> Pocket137
  MirrorPlane = -> DatumPlane007
  Originals = -> [Pocket137]
  Suppressed = false
FEATURE [Sketcher::SketchObject] Sketch259
  FullyConstrained = true
FEATURE [PartDesign::SubShapeBinder] Binder144
  BindCopyOnChange = 0
  BindMode = 0
  ClaimChildren = true
  Context = -> Body145 [Binder144.]
  Fuse = false
  MakeFace = true
  OffsetFill = false
  OffsetIntersection = false
  OffsetJoinType = 0
  OffsetOpenResult = false
  PartialLoad = false
  Relative = true
  Support = -> [Sketch056]
  _Version = 2
  expr: Support = <<pillar_dec_corner_base_sketch>>._self
FEATURE [PartDesign::FeaturePython] BaseBend054  label="pillar3_dec_corner_BaseBend"  # WARN: FeaturePython — macro-defined, semantics opaque (R4)
  BendSide = 0
  BendSketch = -> Binder144
  MidPlane = false
  Reverse = false
  Suppressed = false
  length = 1214
  radius = 2
  thickness = 0.5
  expr: length = <<pillar3_BaseBend>>.length - <<pillar3_dec_corner_placement>>.Placement.Base.z
FEATURE [Sketcher::SketchObject] Sketch260
  AttachmentSupport = -> [XZ_Plane125]
  ExternalGeometry = -> [Binder144]
  FullyConstrained = true
  MapMode = 5
  Placement = pos=(0,0,0) rot=(1,0,0;1.5708rad)
  sketch-geometry (3):
    g0: LineSegment StartX=13.3 StartY=0 StartZ=0 EndX=18.3 EndY=-3e-16 EndZ=0
    g1: LineSegment StartX=18.3 StartY=-3e-16 StartZ=0 EndX=18.3 EndY=5 EndZ=0
    g2: ArcOfCircle CenterX=13.3 CenterY=5 CenterZ=0 NormalX=0 NormalY=0 NormalZ=1 AngleXU=0 Radius=5 StartAngle=4.71239 EndAngle=6.28319
  constraints (7):
    c: PointOnObject(g0,g-3)
    c: Coincident(g0,g-3)
    c: Coincident(g0,g1)
    c: Vertical(g1)
    c: Tangent(g2,g1) = -1.5708
    c: Tangent(g2,g0) = -1.5708
    c: Radius(g2) = 5
FEATURE [Sketcher::SketchObject] Sketch261
  AttachmentSupport = -> [YZ_Plane125]
  ExternalGeometry = -> [Binder144]
  FullyConstrained = true
  MapMode = 5
  Placement = pos=(0,0,0) rot=(0.57735,0.57735,0.57735;2.0944rad)
  sketch-geometry (3):
    g0: LineSegment StartX=14 StartY=9e-16 StartZ=0 EndX=19 EndY=0 EndZ=0
    g1: LineSegment StartX=19 StartY=0 StartZ=0 EndX=19 EndY=5 EndZ=0
    g2: ArcOfCircle CenterX=14 CenterY=5 CenterZ=0 NormalX=0 NormalY=0 NormalZ=1 AngleXU=0 Radius=5 StartAngle=4.71239 EndAngle=6.28319
  constraints (7):
    c: PointOnObject(g0,g-3)
    c: Coincident(g0,g-3)
    c: Coincident(g0,g1)
    c: Vertical(g1)
    c: Tangent(g2,g1) = -1.5708
    c: Tangent(g2,g0) = -1.5708
    c: Radius(g2) = 5
FEATURE [PartDesign::Pocket] Pocket140
  BaseFeature = -> BaseBend054
  Direction = (0,1,-2e-16)
  Length = 5
  Length2 = 5
  Midplane = true
  Profile = -> Sketch260
  ReferenceAxis = -> Sketch260 [N_Axis]
  Suppressed = false
  Type = 1
FEATURE [PartDesign::Pocket] Pocket141
  BaseFeature = -> Pocket140
  Direction = (-1,0,0)
  Length = 5
  Length2 = 5
  Midplane = true
  Profile = -> Sketch261
  ReferenceAxis = -> Sketch261 [N_Axis]
  Suppressed = false
  Type = 1
FEATURE [PartDesign::Plane] DatumPlane008
  AttachmentOffset = pos=(0,0,607) rot=(0,0,1;0rad)
  AttachmentSupport = -> [XY_Plane125]
  Length = 60
  MapMode = 5
  Placement = pos=(0,0,607) rot=(0,0,1;0rad)
  ResizeMode = 0
  Width = 60
  expr: .AttachmentOffset.Base.z = <<pillar3_dec_corner_BaseBend>>.length / 2
FEATURE [PartDesign::Mirrored] Mirrored021
  BaseFeature = -> Pocket141
  MirrorPlane = -> DatumPlane008
  Originals = -> [Pocket140,Pocket141]
  Suppressed = false
FEATURE [Part::FeaturePython] Placment034  label="pillar3_hat_fix_placement"  # WARN: FeaturePython — macro-defined, semantics opaque (R4)
  AttacherType = Attacher::AttachEngine3D
  ExposePlacement = true
  MarkerShape = 1
  MarkerSize = 50
  NumElements = 1
  Placement = pos=(0,2,1594) rot=(0,0,1;0rad)
  Type = lattice2AttachablePlacement.AttachablePlacement
  isLattice = 1
  expr: .Placement.Base.z = <<pillar3_Properties>>.hat_offset
FEATURE [Part::FeaturePython] Placment035  label="pillar3_dec_corner_placement"  # WARN: FeaturePython — macro-defined, semantics opaque (R4)
  AttacherType = Attacher::AttachEngine3D
  ExposePlacement = true
  MarkerShape = 1
  MarkerSize = 50
  NumElements = 1
  Placement = pos=(0,0,470) rot=(0,0,1;0rad)
  Type = lattice2AttachablePlacement.AttachablePlacement
  isLattice = 1
FEATURE [PartDesign::SubShapeBinder] Binder145
  BindCopyOnChange = 0
  BindMode = 0
  ClaimChildren = true
  Context = -> Body146 [Binder145.]
  Fuse = false
  MakeFace = true
  OffsetFill = false
  OffsetIntersection = false
  OffsetJoinType = 0
  OffsetOpenResult = false
  PartialLoad = false
  Relative = false
  Support = -> [Connect006]
  _Version = 2
FEATURE [PartDesign::FeaturePython] BaseBend055  # WARN: FeaturePython — macro-defined, semantics opaque (R4)
  BendSide = 1
  BendSketch = -> Binder145
  MidPlane = false
  Reverse = false
  Suppressed = false
  length = 100
  radius = 1
  thickness = 1.5
FEATURE [Sketcher::SketchObject] Sketch262
  FullyConstrained = true
  expr: Constraints[1] = <<pillar_placement>>.Placement.Base.y - 4 mm
  expr: Constraints[2] = <<pillar_placement>>.Placement.Base.y - <<pillar_base_sketch>>.Constraints.length
  expr: Constraints[3] = <<pillar_base_sketch>>.Constraints.width / 2 - 2 mm - 1.5 mm
  sketch-geometry (1):
    g0: LineSegment StartX=14.8 StartY=365 StartZ=0 EndX=14.8 EndY=380 EndZ=0
  constraints (4):
    c: Vertical(g0)
    c: DistanceY(g0) = 380
    c: DistanceY(g0) = 365
    c: DistanceX(g0) = 14.8
FEATURE [Part::Compound] Compound095
  Links = -> [Sketch254,Sketch262]
FEATURE [Part::Mirroring] Part__Mirroring035  label="hat3_border (Mirror #32)"
  Base = (0,0,0)
  Normal = (-0.5,0.866025,0)
  Source = -> Compound095
  expr: .Normal.x = cos(120 deg)
  expr: .Normal.y = sin(120)
FEATURE [Part::FeaturePython] Connect006  # WARN: FeaturePython — macro-defined, semantics opaque (R4)
  Objects = -> [Part__Mirroring035,Compound095]
  Tolerance = 0
FEATURE [PartDesign::FeaturePython] Extend002  # WARN: FeaturePython — macro-defined, semantics opaque (R4)
  BaseFeature = -> BaseBend055
  Offset = 0.02
  Refine = true
  Suppressed = false
  UseSubtraction = false
  baseObject = -> BaseBend055 [Face1]
  gap1 = 0
  gap2 = 0
  length = 0
FEATURE [Part::FeaturePython] Placment036  label="hat3_pillar_fix_placement"  # WARN: FeaturePython — macro-defined, semantics opaque (R4)
  AttacherType = Attacher::AttachEngine3D
  ExposePlacement = true
  MarkerShape = 1
  MarkerSize = 50
  NumElements = 1
  Placement = pos=(18.8,372,10) rot=(0,0,1;0rad)
  Type = lattice2AttachablePlacement.AttachablePlacement
  isLattice = 1
  expr: .Placement.Base.x = <<pillar_base_sketch>>.Constraints.width / 2 + 0.5 mm
  expr: .Placement.Base.y = <<pillar_placement>>.Placement.Base.y - 4 mm - 8 mm
FEATURE [Part::FeaturePython] Mirror013  label="Mirror013 of hat3_pillar_fix_placement"  # WARN: FeaturePython — macro-defined, semantics opaque (R4)
  ExposePlacement = false
  FlipX = false
  FlipY = true
  FlipZ = false
  MarkerShape = 1
  MarkerSize = 100
  NumElements = 1
  Object = -> Placment036
  ObjectTraversal = 0
  PivotPlacement = pos=(0,0,0) rot=(0,0,1;0.523599rad)
  Type = lattice2Mirror.LatticeMirror
  isLattice = 1
FEATURE [Part::FeaturePython] Join015  # WARN: FeaturePython — macro-defined, semantics opaque (R4)
  ExposePlacement = false
  Interleave = false
  Links = -> [Mirror013,Placment036]
  MarkerShape = 1
  MarkerSize = 0
  NumElements = 2
  Type = lattice2JoinArrays.JoinArrays
  isLattice = 1
FEATURE [Part::FeaturePython] LinearArray016  # WARN: FeaturePython — macro-defined, semantics opaque (R4)
  Alignment = 0
  CellStart = A1
  Count = 2
  Dir = (1,0,0)
  DirIsDriven = true
  DistributionLaw = 0
  DrivenProperty = 1
  EndInclusive = true
  ExposePlacement = false
  GeneratorMode = 0
  MarkerShape = 1
  MarkerSize = 0
  NumElements = 2
  OrientMode = 1
  Placement = pos=(0,0,0) rot=(0,-1,0;1.5708rad)
  Point = (0,0,0)
  PointIsDriven = true
  Reverse = false
  SpanEnd = 80
  SpanStart = 10
  Step = 70
  Type = lattice2LinearArray.LinearArray
  VSGVersion = 1
  Values = 10.0 | 80.0
  ValuesSource = 2
  isLattice = 1
  expr: SpanEnd = <<pillar3_Properties>>.hat_height - 10 mm
FEATURE [Part::FeaturePython] Populate056  label="Populate Join015 with LinearArray016"  # WARN: FeaturePython — macro-defined, semantics opaque (R4)
  Copying = 0
  ExposePlacement = false
  MarkerShape = 1
  MarkerSize = 0
  NumElements = 4
  Object = -> LinearArray016
  OutputCompounding = 0
  PlacementsTo = -> Join015
  Referencing = 0
  Type = lattice2PopulateCopies.LatticePopulateCopies
  isLattice = 1
FEATURE [Part::FeaturePython] Populate057  label="Populate Populate Join015 with LinearArray016 with hole_3.4mm_extrude"  # WARN: FeaturePython — macro-defined, semantics opaque (R4)
  Copying = 0
  ExposePlacement = false
  MarkerShape = 1
  MarkerSize = 0
  NumElements = 0
  Object = -> Extrude019
  OutputCompounding = 1
  PlacementsTo = -> Populate056
  Referencing = 0
  Type = lattice2PopulateCopies.LatticePopulateCopies
  isLattice = 0
FEATURE [Part::Compound] Compound096
  Links = -> [Populate057]
FEATURE [PartDesign::Boolean] Boolean047
  BaseFeature = -> Extend002
  Group = -> [Compound096]
  Suppressed = false
  Type = 1
  UsePlacement = true
FEATURE [Sketcher::SketchObject] Sketch263  label="hat3_top_base_sketch"
  FullyConstrained = false
  expr: Constraints[12] = <<hat3_border>>.Constraints.min_r - 5 mm
  expr: Constraints[5] = <<pillar_base_sketch>>.Constraints.width / 2 - 2 mm - 1.5 mm - 0.2 mm
  expr: Constraints[6] = <<pillar_placement>>.Placement.Base.y - <<pillar_base_sketch>>.Constraints.length
  expr: Constraints[8] = <<pillar_placement>>.Placement.Base.y - 5 mm
  sketch-geometry (7):
    g0: LineSegment StartX=0 StartY=379 StartZ=0 EndX=9.6 EndY=379 EndZ=0
    g1: LineSegment StartX=14.6 StartY=374 StartZ=0 EndX=14.6 EndY=365 EndZ=0
    g2: ArcOfCircle CenterX=1008.94 CenterY=582.513 CenterZ=0 NormalX=0 NormalY=0 NormalZ=1 AngleXU=0 Radius=1039.03 StartAngle=3.54682 EndAngle=3.66519
    g3: ArcOfCircle CenterX=501.877 CenterY=365 CenterZ=0 NormalX=0 NormalY=0 NormalZ=1 AngleXU=0 Radius=487.277 StartAngle=3.14159 EndAngle=3.54682
    g4: LineSegment StartX=0 StartY=0 StartZ=0 EndX=109.119 EndY=63 EndZ=0
    g5: ArcOfCircle CenterX=9.6 CenterY=374 CenterZ=0 NormalX=0 NormalY=0 NormalZ=1 AngleXU=0 Radius=5 StartAngle=-5.3e-15 EndAngle=1.5708
    g6: GeomPoint X=14.6 Y=379 Z=0
  constraints (18):
    c: Horizontal(g0)
    c: Vertical(g1)
    c: Coincident(g-1,g4)
    c: Coincident(g4,g2)
    c: Angle(g4) = 0.523599
    c: DistanceX(g1) = 14.6
    c: DistanceY(g1) = 365
    c: PointOnObject(g0,g-2)
    c: DistanceY(g6) = 379
    c: Tangent(g3,g1) = -1.5708
    c: Tangent(g3,g2) = -1.5708
    c: Perpendicular(g2,g4)
    c: Distance(g4) = 126
    c: PointOnObject(g6,g0)
    c: PointOnObject(g6,g1)
    c: Tangent(g0,g5) = 1.5708
    c: Tangent(g1,g5) = 1.5708
    c: Radius(g5) = 5
FEATURE [Part::Mirroring] Part__Mirroring036  label="hat3_top_base_sketch (Mirror #33)"
  Base = (0,0,0)
  Normal = (1,0,0)
  Source = -> Sketch263
FEATURE [Part::Compound] Compound097
  Links = -> [Part__Mirroring036,Sketch263]
FEATURE [Part::FeaturePython] Array014  # Draft array (typed FeaturePython)
  Angle = 360
  ArrayType = 1
  Axis = (0,0,1)
  Base = -> Compound097
  Center = (0,0,0)
  Count = 3
  Fuse = true
  IntervalAxis = (0,0,0)
  IntervalX = (50,0,0)
  IntervalY = (0,50,0)
  IntervalZ = (0,0,50)
  NumberCircles = 3
  NumberPolar = 3
  NumberX = 2
  NumberY = 2
  NumberZ = 1
  RadialDistance = 50
  Symmetry = 1
  TangentialDistance = 25
FEATURE [Part::FeaturePython] Connect007  # WARN: FeaturePython — macro-defined, semantics opaque (R4)
  Objects = -> [Array014]
  Tolerance = 0
FEATURE [PartDesign::SubShapeBinder] Binder146
  BindCopyOnChange = 0
  BindMode = 0
  ClaimChildren = true
  Context = -> Body143 [Binder146.]
  Fuse = false
  MakeFace = true
  OffsetFill = false
  OffsetIntersection = false
  OffsetJoinType = 0
  OffsetOpenResult = false
  PartialLoad = false
  Relative = false
  Support = -> [Connect007]
  _Version = 2
FEATURE [PartDesign::Pad] Pad046
  Direction = (0,0,1)
  Length = 3
  Length2 = 10
  Profile = -> Binder146
  Refine = true
  Suppressed = false
  Type = 0
FEATURE [PartDesign::CoordinateSystem] Local_CS008  label="pilllar3_dec_corner_base_local_cs"
  AttacherType = Attacher::AttachEngine3D
  AttachmentSupport = -> [XY_Plane125]
  MapMode = 5
FEATURE [Part::FeaturePython] Placment037  # WARN: FeaturePython — macro-defined, semantics opaque (R4)
  AttacherType = Attacher::AttachEngine3D
  ExposePlacement = true
  MarkerShape = 1
  MarkerSize = 20
  NumElements = 1
  Placement = pos=(-18.8,10,0) rot=(0,0,1;0rad)
  Type = lattice2AttachablePlacement.AttachablePlacement
  isLattice = 1
  expr: .Placement.Base.x = -(<<pillar_base_sketch>>.Constraints.width / 2 + 0.5 mm)
FEATURE [Part::FeaturePython] LinearArray017  label="dec_corner_pillar_fix"  # WARN: FeaturePython — macro-defined, semantics opaque (R4)
  Alignment = 0
  CellStart = A1
  Count = 5
  Dir = (1,0,0)
  DirIsDriven = true
  DistributionLaw = 0
  DrivenProperty = 1
  EndInclusive = true
  ExposePlacement = false
  GeneratorMode = 0
  MarkerShape = 1
  MarkerSize = 0
  NumElements = 5
  OrientMode = 1
  Placement = pos=(0,0,0) rot=(0.707107,0,0.707107;3.14159rad)
  Point = (0,0,0)
  PointIsDriven = true
  Reverse = false
  SpanEnd = 1104
  SpanStart = 20
  Step = 271
  Type = lattice2LinearArray.LinearArray
  VSGVersion = 1
  Values = 20.0 | 291.0 | 562.0 | 833.0 | 1104.0
  ValuesSource = 2
  isLattice = 1
  expr: SpanEnd = <<pillar3_hat_fix_placement>>.Placement.Base.z - <<pillar3_dec_corner_placement>>.Placement.Base.z - 20 mm
FEATURE [PartDesign::CoordinateSystem] Local_CS009  label="pillar3_dec_corner_LCS"
  AttacherType = Attacher::AttachEngine3D
  AttachmentOffset = pos=(0,0,470) rot=(0,0,1;0rad)
  AttachmentSupport = -> [XY_Plane121]
  MapMode = 5
  Placement = pos=(0,0,470) rot=(0,0,1;0rad)
  expr: AttachmentOffset = <<pillar3_dec_corner_placement>>.Placement
FEATURE [Part::FeaturePython] Populate058  label="Populate Placment037 with dec_corner_pillar_fix"  # WARN: FeaturePython — macro-defined, semantics opaque (R4)
  Copying = 0
  ExposePlacement = false
  MarkerShape = 1
  MarkerSize = 0
  NumElements = 5
  Object = -> LinearArray017
  OutputCompounding = 0
  PlacementsTo = -> Placment037
  Referencing = 0
  Type = lattice2PopulateCopies.LatticePopulateCopies
  isLattice = 1
FEATURE [Part::FeaturePython] Populate060  label="Populate Populate Placment037 with dec_corner_pillar_fix with hole_3.4mm_extrude"  # WARN: FeaturePython — macro-defined, semantics opaque (R4)
  Copying = 0
  ExposePlacement = false
  MarkerShape = 1
  MarkerSize = 0
  NumElements = 0
  Object = -> Extrude019
  OutputCompounding = 1
  PlacementsTo = -> Populate058
  Referencing = 0
  Type = lattice2PopulateCopies.LatticePopulateCopies
  isLattice = 0
FEATURE [Part::FeaturePython] Populate062  label="Populate pillar3_hat_fix_placement with Populate Placment033 with Extrude037"  # WARN: FeaturePython — macro-defined, semantics opaque (R4)
  Copying = 0
  ExposePlacement = false
  MarkerShape = 1
  MarkerSize = 0
  NumElements = 0
  Object = -> Populate055
  OutputCompounding = 2
  PlacementsTo = -> Placment034
  Referencing = 0
  Type = lattice2PopulateCopies.LatticePopulateCopies
  isLattice = 0
FEATURE [Part::FeaturePython] Placment038  # WARN: FeaturePython — macro-defined, semantics opaque (R4)
  AttacherType = Attacher::AttachEngine3D
  ExposePlacement = true
  MarkerShape = 1
  MarkerSize = 10
  NumElements = 1
  Placement = pos=(18.8,10,0) rot=(0,0,1;0rad)
  Type = lattice2AttachablePlacement.AttachablePlacement
  isLattice = 1
  expr: .Placement.Base.x = <<pillar_base_sketch>>.Constraints.width / 2 + 0.5 mm
FEATURE [Part::FeaturePython] Mirror014  label="Mirror014 of Placment038"  # WARN: FeaturePython — macro-defined, semantics opaque (R4)
  ExposePlacement = false
  FlipX = true
  FlipY = false
  FlipZ = false
  MarkerShape = 1
  MarkerSize = 50
  NumElements = 1
  Object = -> Placment038
  ObjectTraversal = 0
  Type = lattice2Mirror.LatticeMirror
  isLattice = 1
FEATURE [Part::FeaturePython] Join016  # WARN: FeaturePython — macro-defined, semantics opaque (R4)
  ExposePlacement = false
  Interleave = false
  Links = -> [Mirror014,Placment038]
  MarkerShape = 1
  MarkerSize = 0
  NumElements = 2
  Type = lattice2JoinArrays.JoinArrays
  isLattice = 1
FEATURE [Part::FeaturePython] Populate063  label="Populate Join016 with LinearArray016"  # WARN: FeaturePython — macro-defined, semantics opaque (R4)
  Copying = 0
  ExposePlacement = false
  MarkerShape = 1
  MarkerSize = 0
  NumElements = 4
  Object = -> LinearArray016
  OutputCompounding = 0
  PlacementsTo = -> Join016
  Referencing = 0
  Type = lattice2PopulateCopies.LatticePopulateCopies
  isLattice = 1
FEATURE [Part::FeaturePython] Populate067  label="Populate pillar3_hat_fix_placement with Populate Join016 with LinearArray016"  # WARN: FeaturePython — macro-defined, semantics opaque (R4)
  Copying = 0
  ExposePlacement = false
  MarkerShape = 1
  MarkerSize = 0
  NumElements = 4
  Object = -> Populate063
  OutputCompounding = 0
  PlacementsTo = -> Placment034
  Referencing = 0
  Type = lattice2PopulateCopies.LatticePopulateCopies
  isLattice = 1
FEATURE [Part::FeaturePython] Populate064  label="Populate Populate Join016 with LinearArray016 with hole_3.4mm_extrude"  # WARN: FeaturePython — macro-defined, semantics opaque (R4)
  Copying = 0
  ExposePlacement = false
  MarkerShape = 1
  MarkerSize = 0
  NumElements = 0
  Object = -> Extrude019
  OutputCompounding = 1
  PlacementsTo = -> Populate067
  Referencing = 0
  Type = lattice2PopulateCopies.LatticePopulateCopies
  isLattice = 0
FEATURE [Part::FeaturePython] LinearArray018  # WARN: FeaturePython — macro-defined, semantics opaque (R4)
  Alignment = 0
  CellStart = A1
  Count = 5
  Dir = (1,0,0)
  DirIsDriven = true
  DistributionLaw = 0
  DrivenProperty = 1
  EndInclusive = true
  ExposePlacement = false
  GeneratorMode = 0
  MarkerShape = 1
  MarkerSize = 0
  NumElements = 5
  OrientMode = 1
  Placement = pos=(0,-2,470) rot=(0.57735,0.57735,0.57735;4.18879rad)
  Point = (0,0,0)
  PointIsDriven = true
  Reverse = false
  SpanEnd = 1104
  SpanStart = 20
  Step = 271
  Type = lattice2LinearArray.LinearArray
  VSGVersion = 1
  Values = 20.0 | 291.0 | 562.0 | 833.0 | 1104.0
  ValuesSource = 2
  isLattice = 1
  expr: .Placement.Base.z = <<pillar3_Properties>>.dec_corner_offset
  expr: SpanEnd = <<pillar3_Properties>>.dec_corner_height - <<pillar3_Properties>>.hat_height - 20 mm
FEATURE [Spreadsheet::Sheet] Spreadsheet005  label="pillar3_Properties"
  cells = B2(total_height)==1684 mm; C2(dec_corner_height)==total_height - dec_corner_offset; D2(dec_corner_offset)==470 mm; E2(hat_offset)==total_height - hat_height; F2(hat_height)==90 mm; G2(width)=36.6; H2(length)=
FEATURE [Part::Compound] Compound101  label="pillar3_hat_fix_common"
FEATURE [PartDesign::SubShapeBinder] Binder147
  BindCopyOnChange = 0
  BindMode = 0
  ClaimChildren = false
  Fuse = false
  MakeFace = false
  OffsetFill = false
  OffsetIntersection = false
  OffsetJoinType = 0
  OffsetOpenResult = false
  PartialLoad = false
  Relative = true
  Support = -> [<external ULZ-P02-14W.FCStd>#Sketch]
  _Version = 2
FEATURE [Sketcher::SketchObject] Sketch264
  ExternalGeometry = -> [Binder147]
  FullyConstrained = true
  sketch-geometry (6):
    g0: ArcOfCircle CenterX=4.15 CenterY=-445.9 CenterZ=0 NormalX=0 NormalY=0 NormalZ=1 AngleXU=0 Radius=1.6 StartAngle=3.14159 EndAngle=6.28319
    g1: ArcOfCircle CenterX=4.15 CenterY=-444.1 CenterZ=0 NormalX=0 NormalY=0 NormalZ=1 AngleXU=0 Radius=1.6 StartAngle=1.21e-14 EndAngle=3.14159
    g2: LineSegment StartX=2.55 StartY=-445.9 StartZ=0 EndX=2.55 EndY=-444.1 EndZ=0
    g3: LineSegment StartX=5.75 StartY=-445.9 StartZ=0 EndX=5.75 EndY=-444.1 EndZ=0
    g4: LineSegment StartX=4.15 StartY=-442.5 StartZ=0 EndX=4.15 EndY=-447.5 EndZ=0
    g5: Circle CenterX=-4.15 CenterY=445 CenterZ=0 NormalX=0 NormalY=0 NormalZ=1 AngleXU=0 Radius=1.6
  constraints (15):
    c: Tangent(g0,g2) = 1.5708
    c: Tangent(g0,g3) = -1.5708
    c: Tangent(g1,g2) = 1.5708
    c: Tangent(g1,g3) = -1.5708
    c: Equal(g0,g1)
    c: Vertical(g2)
    c: Symmetric(g0,g1,g-4)
    c: Equal(g1,g-4)
    c: PointOnObject(g4,g1)
    c: PointOnObject(g4,g0)
    c: Vertical(g4)
    c: PointOnObject(g1,g4)
    c: DistanceY(g4,g4) = 5
    c: Coincident(g5,g-3)
    c: Equal(g5,g-3)
FEATURE [App::Link] Link047  label="pillar3_pillar3_dec_corner_common001"
  LinkPlacement = pos=(0,0,-470) rot=(0,0,1;0rad)
  LinkedObject = -> Compound100
  Placement = pos=(0,0,-470) rot=(0,0,1;0rad)
  expr: Placement = <<pillar3_dec_corner_placement>>.Placement ^ -1
FEATURE [Part::Compound] Compound098
  Links = -> [Link047]
FEATURE [PartDesign::Boolean] Boolean048
  BaseFeature = -> Mirrored021
  Group = -> [Compound098]
  Suppressed = false
  Type = 1
  UsePlacement = true
FEATURE [PartDesign::Body] Body145  label="pilllar3_dec_corner"
  Group = -> [Binder144,BaseBend054,Sketch260,Sketch261,Pocket140,Pocket141,DatumPlane008,Mirrored021,Local_CS008,Boolean048]
  Origin = -> Origin126
  Tip = -> Boolean048
FEATURE [Part::FeaturePython] Populate068  label="Populate LinearArray018 with hole_3.4mm_extrude"  # WARN: FeaturePython — macro-defined, semantics opaque (R4)
  Copying = 0
  ExposePlacement = false
  MarkerShape = 1
  MarkerSize = 0
  NumElements = 0
  Object = -> Extrude019
  OutputCompounding = 1
  PlacementsTo = -> LinearArray018
  Referencing = 0
  Type = lattice2PopulateCopies.LatticePopulateCopies
  isLattice = 0
FEATURE [PartDesign::CoordinateSystem] Local_CS010  label="basement_bottom_plywood_bottom"
  AttacherType = Attacher::AttachEngine3D
  AttachmentSupport = -> [XY_Plane011]
  MapMode = 5
FEATURE [PartDesign::CoordinateSystem] Local_CS011  label="basement_bottom_plywood_top"
  AttacherType = Attacher::AttachEngine3D
  AttachmentOffset = pos=(0,0,18) rot=(0,0,1;0rad)
  AttachmentSupport = -> [XY_Plane011]
  MapMode = 5
  Placement = pos=(0,0,18) rot=(0,0,1;0rad)
FEATURE [PartDesign::Body] Body007  label="basement_bottom_plywood"
  Group = -> [Binder003,Pad002,Sketch110,PolarPattern002,Sketch178,Boolean026,Sketch218,Local_CS010,Local_CS011]
  Origin = -> Origin011
  Tip = -> Boolean026
FEATURE [PartDesign::CoordinateSystem] Local_CS012  label="basement_bottom_proxy_bottom"
  AttacherType = Attacher::AttachEngine3D
  AttachmentSupport = -> [XY_Plane013]
  MapMode = 5
FEATURE [PartDesign::CoordinateSystem] Local_CS013  label="basement_bottom_proxy_top"
  AttacherType = Attacher::AttachEngine3D
  AttachmentOffset = pos=(0,0,3) rot=(0,0,1;0rad)
  AttachmentSupport = -> [XY_Plane013]
  MapMode = 5
  Placement = pos=(0,0,3) rot=(0,0,1;0rad)
FEATURE [PartDesign::CoordinateSystem] Local_CS014  label="basement_bottom_amplifier_bottom_LCS"
  AttacherType = Attacher::AttachEngine3D
  AttachmentSupport = -> [XY_Plane080]
  MapMode = 5
FEATURE [PartDesign::CoordinateSystem] Local_CS015  label="basement_bottom_amplifier_top_LCS"
  AttacherType = Attacher::AttachEngine3D
  AttachmentOffset = pos=(0,0,2) rot=(0,0,1;0rad)
  AttachmentSupport = -> [XY_Plane080]
  MapMode = 5
  Placement = pos=(0,0,2) rot=(0,0,1;0rad)
FEATURE [PartDesign::CoordinateSystem] Local_CS016  label="basement_bottom_proxy_pillar_back_LCS"
  AttacherType = Attacher::AttachEngine3D
  AttachmentOffset = pos=(0,384,3) rot=(0,0,-1;3.14159rad)
  AttachmentSupport = -> [XY_Plane013]
  MapMode = 5
  Placement = pos=(0,384,3) rot=(0,0,-1;3.14159rad)
  expr: .AttachmentOffset.Base.y = <<pillar_placement>>.Placement.Base.y
FEATURE [PartDesign::CoordinateSystem] Local_CS017  label="basement_top_proxy_bottom_LCS"
  AttacherType = Attacher::AttachEngine3D
  AttachmentSupport = -> [XY_Plane012]
  MapMode = 5
FEATURE [PartDesign::CoordinateSystem] Local_CS018  label="basement_top_proxy_top_LCS"
  AttacherType = Attacher::AttachEngine3D
  AttachmentOffset = pos=(0,0,3) rot=(0,0,1;0rad)
  AttachmentSupport = -> [XY_Plane012]
  MapMode = 5
  Placement = pos=(0,0,3) rot=(0,0,1;0rad)
FEATURE [PartDesign::Body] Body008  label="basement_top_proxy"
  Group = -> [Binder006,Pad003,Boolean021,Binder129,Local_CS017,Local_CS018]
  Origin = -> Origin012
  Placement = pos=(0,0,18) rot=(0,0,1;0rad)
  Tip = -> Boolean021
FEATURE [PartDesign::CoordinateSystem] Local_CS019  label="basement_top_plywood_bottom_LCS"
  AttacherType = Attacher::AttachEngine3D
  AttachmentSupport = -> [XY_Plane010]
  MapMode = 5
FEATURE [PartDesign::CoordinateSystem] Local_CS020  label="basement_top_plywood_top_LCS"
  AttacherType = Attacher::AttachEngine3D
  AttachmentOffset = pos=(0,0,18) rot=(0,0,1;0rad)
  AttachmentSupport = -> [XY_Plane010]
  MapMode = 5
  Placement = pos=(0,0,18) rot=(0,0,1;0rad)
FEATURE [PartDesign::CoordinateSystem] Local_CS021  label="basement_top_amplifier_bottom_LCS"
  AttacherType = Attacher::AttachEngine3D
  AttachmentSupport = -> [XY_Plane078]
  MapMode = 5
FEATURE [PartDesign::CoordinateSystem] Local_CS022  label="basement_top_amplifier_top_LCS"
  AttacherType = Attacher::AttachEngine3D
  AttachmentOffset = pos=(0,0,2) rot=(0,0,1;0rad)
  AttachmentSupport = -> [XY_Plane078]
  MapMode = 5
  Placement = pos=(0,0,2) rot=(0,0,1;0rad)
FEATURE [PartDesign::Body] Body105  label="basement_top_amplifier_material_0.50ansi"
  Group = -> [Sketch167,BaseBend043,Bend025,Pocket104,Fillet011,Binder119,Sketch170,DatumPlane005,DatumLine003,DatumLine004,Sketch173,Pocket108,Sketch175,Pocket109,Mirrored010,PDW_Common_Add,PolarPattern006,Binder118,Pocket107,Boolean028,Local_CS021,Local_CS022]
  Origin = -> Origin078
  Tip = -> Boolean028
FEATURE [PartDesign::CoordinateSystem] Local_CS023  label="basement_bottom_proxy_pillar_left_LCS"
  AttacherType = Attacher::AttachEngine3D
  AttachmentOffset = pos=(-332.554,-192,3) rot=(0,0,-1;1.0472rad)
  AttachmentSupport = -> [XY_Plane013]
  MapMode = 5
  Placement = pos=(-332.554,-192,3) rot=(0,0,-1;1.0472rad)
  expr: .AttachmentOffset.Base.x = <<pillar_placement>>.Placement.Base.y * cos(210)
  expr: .AttachmentOffset.Base.y = <<pillar_placement>>.Placement.Base.y * sin(210)
FEATURE [PartDesign::CoordinateSystem] Local_CS024  label="basement_bottom_proxy_pillar_right_LCS"
  AttacherType = Attacher::AttachEngine3D
  AttachmentOffset = pos=(332.554,-192,3) rot=(0,0,1;1.0472rad)
  AttachmentSupport = -> [XY_Plane013]
  MapMode = 5
  Placement = pos=(332.554,-192,3) rot=(0,0,1;1.0472rad)
  expr: .AttachmentOffset.Base.x = <<pillar_placement>>.Placement.Base.y * cos(330)
  expr: .AttachmentOffset.Base.y = <<pillar_placement>>.Placement.Base.y * sin(330)
FEATURE [PartDesign::Body] Body009  label="basement_bottom_proxy"
  Group = -> [Binder004,Pad004,Binder134,Boolean029,Local_CS012,Local_CS013,Local_CS016,Local_CS023,Local_CS024]
  Origin = -> Origin013
  Tip = -> Boolean029
FEATURE [PartDesign::CoordinateSystem] Local_CS025  label="part1_bottom_LCS"
  AttacherType = Attacher::AttachEngine3D
  AttachmentSupport = -> [XY_Plane]
  MapMode = 5
FEATURE [PartDesign::CoordinateSystem] Local_CS026  label="part1_top_LCS"
  AttacherType = Attacher::AttachEngine3D
  AttachmentOffset = pos=(0,0,1428) rot=(0,0,1;0rad)
  AttachmentSupport = -> [XY_Plane]
  MapMode = 5
  Placement = pos=(0,0,1428) rot=(0,0,1;0rad)
  expr: .AttachmentOffset.Base.z = <<Properties>>.total_height
FEATURE [PartDesign::CoordinateSystem] Local_CS027  label="part2_bottom"
  AttacherType = Attacher::AttachEngine3D
  AttachmentOffset = pos=(0,0,0) rot=(0,0,1;2.0944rad)
  AttachmentSupport = -> [XY_Plane001]
  MapMode = 5
  Placement = pos=(0,0,0) rot=(0,0,1;2.0944rad)
FEATURE [PartDesign::CoordinateSystem] Local_CS028
  AttacherType = Attacher::AttachEngine3D
  AttachmentOffset = pos=(0,0,1428) rot=(0,0,1;0rad)
  AttachmentSupport = -> [Local_CS027]
  MapMode = 5
  Placement = pos=(0,0,1428) rot=(0,0,1;2.0944rad)
  expr: .AttachmentOffset.Base.z = <<Properties>>.total_height
FEATURE [App::DocumentObjectGroup] Group017  label="cap_Group"
  Group = -> [Body002,Body003,Body016]
FEATURE [PartDesign::CoordinateSystem] Local_CS029  label="dropper_fix_bottom_outer_LCS"
  AttacherType = Attacher::AttachEngine3D
  AttachmentSupport = -> [XY_Plane007]
  MapMode = 5
FEATURE [PartDesign::CoordinateSystem] Local_CS030  label="dropper_fix_bottom_inner_LCS"
  AttacherType = Attacher::AttachEngine3D
  AttachmentOffset = pos=(0,0,3) rot=(0,0,1;0rad)
  AttachmentSupport = -> [XY_Plane007]
  MapMode = 5
  Placement = pos=(0,0,3) rot=(0,0,1;0rad)
FEATURE [PartDesign::Body] Body004  label="dropper_fix_bottom"
  Group = -> [Binder007,Pad005,Sketch025,Binder021,Pocket006,Sketch027,Sketch028,Binder023,Hole003,Boolean033,PDW_Common_Sub,Compound048,Connect,Local_CS029,Local_CS030]
  Origin = -> Origin007
  Tip = -> PDW_Common_Sub
FEATURE [PartDesign::CoordinateSystem] Local_CS031  label="dropper_fix_top_outer_LCS"
  AttacherType = Attacher::AttachEngine3D
  AttachmentSupport = -> [XY_Plane083]
  MapMode = 5
FEATURE [PartDesign::CoordinateSystem] Local_CS032  label="dropper_fix_top_inner_LCS"
  AttacherType = Attacher::AttachEngine3D
  AttachmentOffset = pos=(0,0,3) rot=(0,0,1;0rad)
  AttachmentSupport = -> [XY_Plane083]
  MapMode = 5
  Placement = pos=(0,0,3) rot=(0,0,1;0rad)
FEATURE [PartDesign::Body] Body110  label="dropper_fix_top"
  Group = -> [BaseFeature,PDW_Sub,Connect001,Boolean034,Local_CS031,Local_CS032]
  Origin = -> Origin083
  Tip = -> Boolean034
FEATURE [App::DocumentObjectGroup] Group019  label="dropper_fix_Group"
  Group = -> [Body004,Body110]
FEATURE [App::DocumentObjectGroup] Group018  label="top_Group"
  Group = -> [Group017,Body017,Group019]
FEATURE [PartDesign::CoordinateSystem] Local_CS033  label="sleeve_inner2_flange_top_LCS"
  AttacherType = Attacher::AttachEngine3D
  AttachmentOffset = pos=(0,0,5) rot=(0,0,1;0rad)
  AttachmentSupport = -> [XY_Plane101]
  MapMode = 5
  Placement = pos=(0,0,5) rot=(0,0,1;0rad)
FEATURE [PartDesign::CoordinateSystem] Local_CS034  label="sleeve_inner2_end_LCS"
  AttacherType = Attacher::AttachEngine3D
  AttachmentOffset = pos=(0,0,83.7) rot=(0,0,1;0rad)
  AttachmentSupport = -> [XY_Plane101]
  MapMode = 5
  Placement = pos=(0,0,83.7) rot=(0,0,1;0rad)
FEATURE [PartDesign::Body] Body133  label="sleeve_inner2"
  Group = -> [Sketch235,Revolution005,Boolean040,Local_CS033,Local_CS034]
  Origin = -> Origin111
  Tip = -> Boolean040
FEATURE [TechDraw::DrawViewPart] View008
  CoarseView = false
  Direction = (0,-1,0)
  Focus = 100
  HardHidden = false
  IsoCount = 0
  IsoHidden = false
  IsoVisible = false
  LockPosition = false
  Perspective = false
  Rotation = 180
  ScaleType = 0
  ScrubCount = 0
  SeamHidden = false
  SeamVisible = true
  SmoothHidden = false
  SmoothVisible = true
  Source = -> [Body133]
  X = 142.629
  XDirection = (1,0,0)
  Y = 105
  expr: Y = Template.Height / 2
FEATURE [TechDraw::DrawViewDimension] Dimension036
  AngleOverride = false
  Arbitrary = false
  ArbitraryTolerances = false
  EqualTolerance = true
  ExtensionAngle = 0
  FormatSpec = %.2w
  FormatSpecOverTolerance = %+.2w
  FormatSpecUnderTolerance = %+.2w
  Inverted = false
  LineAngle = 0
  LockPosition = false
  MeasureType = 1
  OverTolerance = 0
  References2D = -> [View008]
  Rotation = 0
  ScaleType = 0
  TheoreticalExact = false
  Type = 1
  UnderTolerance = 0
  X = -0.138556
  Y = -52.356
FEATURE [TechDraw::DrawViewDimension] Dimension037
  AngleOverride = false
  Arbitrary = false
  ArbitraryTolerances = false
  EqualTolerance = true
  ExtensionAngle = 0
  FormatSpec = %.2w
  FormatSpecOverTolerance = %+.2w
  FormatSpecUnderTolerance = %+.2w
  Inverted = false
  LineAngle = 0
  LockPosition = false
  MeasureType = 1
  OverTolerance = 0
  References2D = -> [View008]
  Rotation = 0
  ScaleType = 0
  TheoreticalExact = false
  Type = 2
  UnderTolerance = 0
  X = 21.4492
  Y = 4.5306
FEATURE [TechDraw::DrawViewDimension] Dimension038
  AngleOverride = false
  Arbitrary = false
  ArbitraryTolerances = false
  EqualTolerance = true
  ExtensionAngle = 0
  FormatSpec = %.2w
  FormatSpecOverTolerance = %+.2w
  FormatSpecUnderTolerance = %+.2w
  Inverted = false
  LineAngle = 0
  LockPosition = false
  MeasureType = 1
  OverTolerance = 0
  References2D = -> [View008]
  Rotation = 0
  ScaleType = 0
  TheoreticalExact = false
  Type = 2
  UnderTolerance = 0
  X = 43.4564
  Y = -40.9108
FEATURE [TechDraw::DrawViewSection] SectionView004  label="Section001  - 001"
  BaseView = -> View008
  CoarseView = false
  CutSurfaceDisplay = 1
  Direction = (-1,0,-1e-16)
  FileGeomPattern = <path>
  FileHatchPattern = <path>
  Focus = 100
  FuseBeforeCut = false
  HardHidden = false
  HatchOffset = (0,0,0)
  HatchRotation = 0
  HatchScale = 1
  IsoCount = 0
  IsoHidden = false
  IsoVisible = false
  LockPosition = false
  NameGeomPattern = Diamond
  Perspective = false
  Rotation = 90
  ScaleType = 0
  ScrubCount = 0
  SeamHidden = false
  SeamVisible = true
  SectionDirection = 4
  SectionLineStretch = 1
  SectionNormal = (-1,0,-1e-16)
  SectionOrigin = (0,0,1473)
  SmoothHidden = false
  SmoothVisible = true
  Source = -> [Body133]
  TrimAfterCut = false
  UsePreviousCut = false
  X = 244.783
  XDirection = (1e-16,0,-1)
  Y = 105
  expr: Y = Template.Height / 2
FEATURE [TechDraw::DrawViewDimension] Dimension035
  AngleOverride = false
  Arbitrary = false
  ArbitraryTolerances = false
  EqualTolerance = true
  ExtensionAngle = 0
  FormatSpec = %.2w
  FormatSpecOverTolerance = %+.2w
  FormatSpecUnderTolerance = %+.2w
  Inverted = false
  LineAngle = 0
  LockPosition = false
  MeasureType = 1
  OverTolerance = 0
  References2D = -> [SectionView004]
  Rotation = 0
  ScaleType = 0
  TheoreticalExact = false
  Type = 1
  UnderTolerance = 0
  X = -0.625347
  Y = 50.1929
FEATURE [TechDraw::DrawViewPart] View009
  CoarseView = false
  Direction = (0,0,1)
  Focus = 100
  HardHidden = false
  IsoCount = 0
  IsoHidden = false
  IsoVisible = false
  LockPosition = false
  Perspective = false
  Rotation = 0
  ScaleType = 0
  ScrubCount = 0
  SeamHidden = false
  SeamVisible = true
  SmoothHidden = false
  SmoothVisible = true
  Source = -> [Body133]
  X = 54.9249
  XDirection = (1,0,0)
  Y = 105
  expr: Y = Template.Height / 2
FEATURE [TechDraw::DrawViewDimension] Dimension032
  AngleOverride = false
  Arbitrary = false
  ArbitraryTolerances = false
  EqualTolerance = true
  ExtensionAngle = 0
  FormatSpec = %.2w
  FormatSpecOverTolerance = %+.2w
  FormatSpecUnderTolerance = %+.2w
  Inverted = false
  LineAngle = 0
  LockPosition = false
  MeasureType = 1
  OverTolerance = 0
  References2D = -> [View009]
  Rotation = 0
  ScaleType = 0
  TheoreticalExact = false
  Type = 0
  UnderTolerance = 0
  X = 4.06158
  Y = 22.1008
FEATURE [TechDraw::DrawViewDimension] Dimension039
  AngleOverride = false
  Arbitrary = true
  ArbitraryTolerances = false
  EqualTolerance = true
  ExtensionAngle = 0
  FormatSpec = ⌀4,2
  FormatSpecOverTolerance = %+.2w
  FormatSpecUnderTolerance = %+.2w
  Inverted = false
  LineAngle = 0
  LockPosition = false
  MeasureType = 1
  OverTolerance = 0
  References2D = -> [View009]
  Rotation = 0
  ScaleType = 0
  TheoreticalExact = false
  Type = 5
  UnderTolerance = 0
  X = 17.5529
  Y = -0.907274
FEATURE [TechDraw::DrawViewDimension] Dimension040
  AngleOverride = false
  Arbitrary = false
  ArbitraryTolerances = false
  EqualTolerance = true
  ExtensionAngle = 0
  FormatSpec = %.2w
  FormatSpecOverTolerance = %+.2w
  FormatSpecUnderTolerance = %+.2w
  Inverted = false
  LineAngle = 0
  LockPosition = false
  MeasureType = 1
  OverTolerance = 0
  References2D = -> [View009]
  Rotation = 0
  ScaleType = 0
  TheoreticalExact = false
  Type = 0
  UnderTolerance = 0
  X = 43.7493
  Y = 16.411
FEATURE [TechDraw::DrawPage] Page004  label="sleeve_inner_Page001"
  KeepUpdated = true
  NextBalloonIndex = 1
  ProjectionType = 0
  Template = -> Template
  Views = -> [View008,View009,SectionView004,Dimension032,Dimension035,Dimension036,Dimension037,Dimension038,Dimension039,Annotation001,Dimension040]
FEATURE [PartDesign::CoordinateSystem] Local_CS035  label="sleeve2_outer_flange_LCS"
  AttacherType = Attacher::AttachEngine3D
  AttachmentSupport = -> [XY_Plane110]
  MapMode = 5
FEATURE [PartDesign::CoordinateSystem] Local_CS036  label="sleeve2_outer_end_LCS"
  AttacherType = Attacher::AttachEngine3D
  AttachmentOffset = pos=(0,0,74.7) rot=(0,0,1;0rad)
  AttachmentSupport = -> [XY_Plane110]
  MapMode = 5
  Placement = pos=(0,0,74.7) rot=(0,0,1;0rad)
FEATURE [PartDesign::Body] Body132  label="sleeve_outer2"
  Group = -> [Sketch234,Revolution006,Boolean039,Local_CS035,Local_CS036]
  Origin = -> Origin110
  Tip = -> Boolean039
FEATURE [TechDraw::DrawViewPart] View006
  CoarseView = false
  Direction = (0,-1,0)
  Focus = 100
  HardHidden = false
  IsoCount = 0
  IsoHidden = false
  IsoVisible = false
  LockPosition = false
  Perspective = false
  Rotation = 0
  ScaleType = 0
  ScrubCount = 0
  SeamHidden = false
  SeamVisible = true
  SmoothHidden = false
  SmoothVisible = true
  Source = -> [Body132]
  X = 237.932
  XDirection = (1,0,0)
  Y = 105
  expr: Y = Template.Height / 2
FEATURE [TechDraw::DrawViewDimension] Dimension024
  AngleOverride = false
  Arbitrary = false
  ArbitraryTolerances = false
  EqualTolerance = true
  ExtensionAngle = 0
  FormatSpec = %.2w
  FormatSpecOverTolerance = %+.2w
  FormatSpecUnderTolerance = %+.2w
  Inverted = false
  LineAngle = 0
  LockPosition = false
  MeasureType = 1
  OverTolerance = 0
  References2D = -> [View006]
  Rotation = 0
  ScaleType = 0
  TheoreticalExact = false
  Type = 2
  UnderTolerance = 0
  X = 42.4652
  Y = -38.9306
FEATURE [TechDraw::DrawViewDimension] Dimension025
  AngleOverride = false
  Arbitrary = false
  ArbitraryTolerances = false
  EqualTolerance = true
  ExtensionAngle = 0
  FormatSpec = %.2w
  FormatSpecOverTolerance = %+.2w
  FormatSpecUnderTolerance = %+.2w
  Inverted = false
  LineAngle = 0
  LockPosition = false
  MeasureType = 1
  OverTolerance = 0
  References2D = -> [View006]
  Rotation = 0
  ScaleType = 0
  TheoreticalExact = false
  Type = 2
  UnderTolerance = 0
  X = 45.1946
  Y = 8.61143
FEATURE [TechDraw::DrawViewSection] SectionView003  label="Section  - 001"
  BaseView = -> View006
  CoarseView = false
  CutSurfaceDisplay = 1
  Direction = (1,0,0)
  FileGeomPattern = <path>
  FileHatchPattern = <path>
  Focus = 100
  FuseBeforeCut = false
  HardHidden = false
  HatchOffset = (0,0,0)
  HatchRotation = 0
  HatchScale = 1
  IsoCount = 0
  IsoHidden = false
  IsoVisible = false
  LockPosition = false
  NameGeomPattern = Diamond
  Perspective = false
  Rotation = 90
  ScaleType = 0
  ScrubCount = 0
  SeamHidden = false
  SeamVisible = true
  SectionDirection = 4
  SectionLineStretch = 1
  SectionNormal = (1,0,0)
  SectionOrigin = (0,0,1467.5)
  SmoothHidden = false
  SmoothVisible = true
  Source = -> [Body132]
  TrimAfterCut = false
  UsePreviousCut = false
  X = 157.277
  XDirection = (0,0,1)
  Y = 105
  expr: Y = Template.Height / 2
FEATURE [TechDraw::DrawViewDimension] Dimension026
  AngleOverride = false
  Arbitrary = false
  ArbitraryTolerances = false
  EqualTolerance = true
  ExtensionAngle = 0
  FormatSpec = %.2w
  FormatSpecOverTolerance = %+.2w
  FormatSpecUnderTolerance = %+.2w
  Inverted = false
  LineAngle = 0
  LockPosition = false
  MeasureType = 1
  OverTolerance = 0
  References2D = -> [SectionView003]
  Rotation = 0
  ScaleType = 0
  TheoreticalExact = false
  Type = 1
  UnderTolerance = 0
  X = 0.683682
  Y = 55.2929
FEATURE [TechDraw::DrawViewDimension] Dimension027
  AngleOverride = false
  Arbitrary = false
  ArbitraryTolerances = false
  EqualTolerance = true
  ExtensionAngle = 0
  FormatSpec = %.2w
  FormatSpecOverTolerance = %+.2w
  FormatSpecUnderTolerance = %+.2w
  Inverted = false
  LineAngle = 0
  LockPosition = false
  MeasureType = 1
  OverTolerance = 0
  References2D = -> [SectionView003]
  Rotation = 0
  ScaleType = 0
  TheoreticalExact = false
  Type = 1
  UnderTolerance = 0
  X = 0.158865
  Y = 68.5155
FEATURE [TechDraw::DrawViewDimension] Dimension028
  AngleOverride = false
  Arbitrary = false
  ArbitraryTolerances = false
  EqualTolerance = true
  ExtensionAngle = 0
  FormatSpec = %.2w
  FormatSpecOverTolerance = %+.2w
  FormatSpecUnderTolerance = %+.2w
  Inverted = false
  LineAngle = 0
  LockPosition = false
  MeasureType = 1
  OverTolerance = 0
  References2D = -> [SectionView003]
  Rotation = 0
  ScaleType = 0
  TheoreticalExact = false
  Type = 1
  UnderTolerance = 0
  X = -3.16566
  Y = -53.4728
FEATURE [TechDraw::DrawViewDimension] Dimension029
  AngleOverride = false
  Arbitrary = false
  ArbitraryTolerances = false
  EqualTolerance = true
  ExtensionAngle = 0
  FormatSpec = %.2w
  FormatSpecOverTolerance = %+.2w
  FormatSpecUnderTolerance = %+.2w
  Inverted = false
  LineAngle = 0
  LockPosition = false
  MeasureType = 1
  OverTolerance = 0
  References2D = -> [SectionView003]
  Rotation = 0
  ScaleType = 0
  TheoreticalExact = false
  Type = 1
  UnderTolerance = 0
  X = -25.9778
  Y = 46.3177
FEATURE [TechDraw::DrawViewPart] View007
  CoarseView = false
  Direction = (0,0,1)
  Focus = 100
  HardHidden = false
  IsoCount = 0
  IsoHidden = false
  IsoVisible = false
  LockPosition = false
  Perspective = false
  Rotation = 0
  ScaleType = 0
  ScrubCount = 0
  SeamHidden = false
  SeamVisible = true
  SmoothHidden = false
  SmoothVisible = true
  Source = -> [Body132]
  X = 65.7116
  XDirection = (1,0,0)
  Y = 105
  expr: Y = Template.Height / 2
FEATURE [TechDraw::DrawViewDimension] Dimension030
  AngleOverride = false
  Arbitrary = true
  ArbitraryTolerances = false
  EqualTolerance = true
  ExtensionAngle = 0
  FormatSpec = ⌀5,0
  FormatSpecOverTolerance = %+.2w
  FormatSpecUnderTolerance = %+.2w
  Inverted = false
  LineAngle = 0
  LockPosition = false
  MeasureType = 1
  OverTolerance = 0
  References2D = -> [View007]
  Rotation = 0
  ScaleType = 0
  TheoreticalExact = false
  Type = 5
  UnderTolerance = 0
  X = 47.8244
  Y = -19.4044
FEATURE [TechDraw::DrawViewDimension] Dimension031
  AngleOverride = false
  Arbitrary = false
  ArbitraryTolerances = false
  EqualTolerance = true
  ExtensionAngle = 0
  FormatSpec = %.2w
  FormatSpecOverTolerance = %+.2w
  FormatSpecUnderTolerance = %+.2w
  Inverted = false
  LineAngle = 0
  LockPosition = false
  MeasureType = 1
  OverTolerance = 0
  References2D = -> [View007]
  Rotation = 0
  ScaleType = 0
  TheoreticalExact = false
  Type = 0
  UnderTolerance = 0
  X = -12.6028
  Y = 21.5334
FEATURE [TechDraw::DrawPage] Page003  label="sleeve_outer_Page001"
  KeepUpdated = true
  NextBalloonIndex = 1
  ProjectionType = 0
  Template = -> Template
  Views = -> [View006,View007,Dimension024,Dimension025,SectionView003,Dimension026,Dimension027,Dimension028,Dimension029,Dimension030,Dimension031,Annotation]
FEATURE [App::DocumentObjectGroup] Group020  label="sleeve2_Group"
  Group = -> [Body133,Body132]
FEATURE [Sketcher::SketchObject] Sketch265
  AttachmentSupport = -> [XY_Plane124]
  FullyConstrained = true
  MapMode = 5
  expr: Constraints[4] = <<pillar3_hat_fix_BaseBend>>.length / 2
  sketch-geometry (8):
    g0: LineSegment StartX=11.3 StartY=14 StartZ=0 EndX=10 EndY=14 EndZ=0
    g1: ArcOfCircle CenterX=10 CenterY=9 CenterZ=0 NormalX=0 NormalY=0 NormalZ=1 AngleXU=0 Radius=5 StartAngle=1.5708 EndAngle=3.14159
    g2: LineSegment StartX=5 StartY=9 StartZ=0 EndX=5 EndY=1 EndZ=0
    g3: LineSegment StartX=14.3 StartY=17 StartZ=0 EndX=14.3 EndY=-7 EndZ=0
    g4: ArcOfCircle CenterX=10 CenterY=1 CenterZ=0 NormalX=0 NormalY=0 NormalZ=1 AngleXU=0 Radius=5 StartAngle=3.14159 EndAngle=4.71239
    g5: ArcOfCircle CenterX=11.3 CenterY=-7 CenterZ=0 NormalX=0 NormalY=0 NormalZ=1 AngleXU=0 Radius=3 StartAngle=-7.46e-14 EndAngle=1.5708
    g6: ArcOfCircle CenterX=11.3 CenterY=17 CenterZ=0 NormalX=0 NormalY=0 NormalZ=1 AngleXU=0 Radius=3 StartAngle=4.71239 EndAngle=6.28319
    g7: LineSegment StartX=10 StartY=-4 StartZ=0 EndX=11.3 EndY=-4 EndZ=0
  constraints (20):
    c: Horizontal(g0)
    c: Vertical(g2)
    c: Vertical(g3)
    c: Radius(g1) = 5
    c: DistanceX(g3) = 14.3
    c: Tangent(g1,g0) = -1.5708
    c: Tangent(g2,g1) = -1.5708
    c: DistanceX(g2) = 5
    c: Tangent(g0,g6) = 1.5708
    c: Tangent(g3,g6) = 1.5708
    c: Horizontal(g7)
    c: Tangent(g3,g5) = 1.5708
    c: Tangent(g4,g2) = -1.5708
    c: Tangent(g7,g4) = -1.5708
    c: Tangent(g7,g5) = 1.5708
    c: Radius(g6) = 3
    c: Equal(g6,g5)
    c: Equal(g4,g1)
    c: DistanceY(g0) = 14
    c: DistanceY(g4) = -4
FEATURE [PartDesign::FeaturePython] SketchOnSheet  # WARN: FeaturePython — macro-defined, semantics opaque (R4)
  BaseFeature = -> BaseBend053
  Sketch = -> Sketch265
  Suppressed = false
  baseObject = -> BaseBend053 [Face22]
  kfactor = 0.5
FEATURE [PartDesign::Pocket] Pocket138
  BaseFeature = -> SketchOnSheet
  Direction = (0,0,-1)
  Length = 5
  Length2 = 5
  Profile = -> Sketch256
  ReferenceAxis = -> Sketch256 [N_Axis]
  Reversed = true
  Suppressed = false
  Type = 0
FEATURE [PartDesign::Pocket] Pocket139
  BaseFeature = -> Pocket138
  Direction = (0,0,-1)
  Length = 5
  Length2 = 5
  Profile = -> Sketch257
  ReferenceAxis = -> Sketch257 [N_Axis]
  Reversed = true
  Suppressed = false
  Type = 1
FEATURE [Part::FeaturePython] LinearArray019  label="hat_hat_fix_placements"  # WARN: FeaturePython — macro-defined, semantics opaque (R4)
  Alignment = 0
  CellStart = A1
  Count = 2
  Dir = (1,0,0)
  DirIsDriven = true
  DistributionLaw = 0
  DrivenProperty = 1
  EndInclusive = true
  ExposePlacement = false
  GeneratorMode = 0
  MarkerShape = 1
  MarkerSize = 0
  NumElements = 2
  OrientMode = 1
  Placement = pos=(0,0,0) rot=(0,0,1;1.5708rad)
  Point = (0,0,0)
  PointIsDriven = true
  Reverse = false
  SpanEnd = 50
  SpanStart = 20
  Step = 30
  Type = lattice2LinearArray.LinearArray
  VSGVersion = 1
  Values = 20.0 | 50.0
  ValuesSource = 2
  isLattice = 1
FEATURE [Part::FeaturePython] Populate069  label="Populate LinearArray019 with hole_3.4mm_extrude"  # WARN: FeaturePython — macro-defined, semantics opaque (R4)
  Copying = 0
  ExposePlacement = false
  MarkerShape = 1
  MarkerSize = 0
  NumElements = 0
  Object = -> Extrude019
  OutputCompounding = 1
  PlacementsTo = -> LinearArray019
  Referencing = 0
  Type = lattice2PopulateCopies.LatticePopulateCopies
  isLattice = 0
FEATURE [Part::Compound] Compound094  label="pillar3_hat_fix_cut1"
  Links = -> [Populate055,Populate069]
FEATURE [PartDesign::Boolean] Boolean046
  BaseFeature = -> Pocket139
  Group = -> [Compound094]
  Suppressed = false
  Type = 1
  UsePlacement = true
FEATURE [PartDesign::Body] Body144  label="pillar3_hat_fix"
  Group = -> [Binder143,BaseBend053,Sketch256,Sketch257,SketchOnSheet,Pocket138,Pocket139,Local_CS005,Boolean046,Sketch265]
  Origin = -> Origin125
  Tip = -> Boolean046
FEATURE [Part::FeaturePython] PolarArray011  # WARN: FeaturePython — macro-defined, semantics opaque (R4)
  Alignment = 0
  AttacherType = Attacher::AttachEngine3D
  CellStart = A1
  Count = 3
  DistributionLaw = 0
  EndInclusive = false
  ExposePlacement = false
  FlipX = false
  FlipZ = false
  GeneratorMode = 0
  MarkerShape = 1
  MarkerSize = 0
  NumElements = 3
  OrientMode = 3
  Placement = pos=(0,0,0) rot=(0,0,1;1.5708rad)
  Radius = 382
  Reverse = false
  SpanEnd = 360
  SpanStart = 0
  Step = 120
  Type = lattice2PolarArray2.PolarArray
  UseArcRadius = false
  UseArcRange = 0
  VSGVersion = 1
  Values = 0.0 | 120.0 | 240.0
  ValuesSource = 2
  isLattice = 1
  expr: Radius = <<pillar_placement>>.Placement.Base.y - 2 mm
FEATURE [Part::FeaturePython] Populate070  label="Populate PolarArray011 with hat_hat_fix_placements"  # WARN: FeaturePython — macro-defined, semantics opaque (R4)
  Copying = 0
  ExposePlacement = false
  MarkerShape = 1
  MarkerSize = 0
  NumElements = 6
  Object = -> LinearArray019
  OutputCompounding = 0
  PlacementsTo = -> PolarArray011
  Referencing = 0
  Type = lattice2PopulateCopies.LatticePopulateCopies
  isLattice = 1
FEATURE [Part::FeaturePython] Populate071  label="Populate Populate PolarArray011 with hat_hat_fix_placements with hole_3.4mm_extrude"  # WARN: FeaturePython — macro-defined, semantics opaque (R4)
  Copying = 0
  ExposePlacement = false
  MarkerShape = 1
  MarkerSize = 0
  NumElements = 0
  Object = -> Extrude019
  OutputCompounding = 1
  PlacementsTo = -> Populate070
  Referencing = 0
  Type = lattice2PopulateCopies.LatticePopulateCopies
  isLattice = 0
FEATURE [PartDesign::CoordinateSystem] Local_CS037  label="hat3_bottom_bottom_LCS"
  AttacherType = Attacher::AttachEngine3D
  AttachmentSupport = -> [XY_Plane122]
  MapMode = 2
FEATURE [PartDesign::CoordinateSystem] Local_CS038  label="hat3_bottom_top_LCS"
  AttacherType = Attacher::AttachEngine3D
  AttachmentOffset = pos=(0,0,3) rot=(0,0,1;0rad)
  AttachmentSupport = -> [XY_Plane122]
  MapMode = 5
  Placement = pos=(0,0,3) rot=(0,0,1;0rad)
FEATURE [Part::FeaturePython] Mirror015  label="Mirror015 of Populate Placment037 with dec_corner_pillar_fix"  # WARN: FeaturePython — macro-defined, semantics opaque (R4)
  ExposePlacement = false
  FlipX = true
  FlipY = false
  FlipZ = false
  MarkerShape = 1
  MarkerSize = 0
  NumElements = 5
  Object = -> Populate058
  ObjectTraversal = 0
  Type = lattice2Mirror.LatticeMirror
  isLattice = 1
FEATURE [Part::FeaturePython] Join017  # WARN: FeaturePython — macro-defined, semantics opaque (R4)
  ExposePlacement = false
  Interleave = false
  Links = -> [Mirror015,Populate058]
  MarkerShape = 1
  MarkerSize = 0
  NumElements = 10
  Type = lattice2JoinArrays.JoinArrays
  isLattice = 1
FEATURE [Part::FeaturePython] Populate059  label="Populate pillar3_dec_corner_placement with Populate Placment037 with dec_corner_pillar_fix"  # WARN: FeaturePython — macro-defined, semantics opaque (R4)
  Copying = 0
  ExposePlacement = false
  MarkerShape = 1
  MarkerSize = 0
  NumElements = 10
  Object = -> Join017
  OutputCompounding = 0
  PlacementsTo = -> Placment035
  Referencing = 0
  Type = lattice2PopulateCopies.LatticePopulateCopies
  isLattice = 1
FEATURE [Part::FeaturePython] Populate061  label="Populate Populate pillar3_dec_corner_placement with Populate Placment037 with dec_corner_pillar_fix with hole_3.4mm_extrude"  # WARN: FeaturePython — macro-defined, semantics opaque (R4)
  Copying = 0
  ExposePlacement = false
  MarkerShape = 1
  MarkerSize = 0
  NumElements = 0
  Object = -> Extrude019
  OutputCompounding = 1
  PlacementsTo = -> Populate059
  Referencing = 0
  Type = lattice2PopulateCopies.LatticePopulateCopies
  isLattice = 0
FEATURE [PartDesign::CoordinateSystem] Local_CS039  label="sleeve_outer_flange_bottom_LCS"
  AttacherType = Attacher::AttachEngine3D
  AttachmentSupport = -> [XY_Plane100]
  MapMode = 5
FEATURE [PartDesign::CoordinateSystem] Local_CS040  label="sleeve_outer_end_LCS"
  AttacherType = Attacher::AttachEngine3D
  AttachmentOffset = pos=(0,0,67) rot=(0,0,1;0rad)
  AttachmentSupport = -> [XY_Plane100]
  MapMode = 5
  Placement = pos=(0,0,67) rot=(0,0,1;0rad)
FEATURE [PartDesign::Body] Body123  label="sleeve_outer"
  Group = -> [Sketch220,Revolution001,Boolean030,Local_CS039,Local_CS040]
  Origin = -> Origin100
  Tip = -> Boolean030
FEATURE [TechDraw::DrawViewPart] View
  CoarseView = false
  Direction = (0,-1,0)
  Focus = 100
  HardHidden = false
  IsoCount = 0
  IsoHidden = false
  IsoVisible = false
  LockPosition = false
  Perspective = false
  Rotation = 0
  ScaleType = 0
  ScrubCount = 0
  SeamHidden = false
  SeamVisible = true
  SmoothHidden = false
  SmoothVisible = true
  Source = -> [Body123]
  X = 237.932
  XDirection = (1,0,0)
  Y = 105
  expr: Y = Template.Height / 2
FEATURE [TechDraw::DrawViewPart] View001
  CoarseView = false
  Direction = (0,0,1)
  Focus = 100
  HardHidden = false
  IsoCount = 0
  IsoHidden = false
  IsoVisible = false
  LockPosition = false
  Perspective = false
  Rotation = 0
  ScaleType = 0
  ScrubCount = 0
  SeamHidden = false
  SeamVisible = true
  SmoothHidden = false
  SmoothVisible = true
  Source = -> [Body123]
  X = 65.7116
  XDirection = (1,0,0)
  Y = 105
  expr: Y = Template.Height / 2
FEATURE [TechDraw::DrawViewDimension] Dimension
  AngleOverride = false
  Arbitrary = false
  ArbitraryTolerances = false
  EqualTolerance = true
  ExtensionAngle = 0
  FormatSpec = %.2w
  FormatSpecOverTolerance = %+.2w
  FormatSpecUnderTolerance = %+.2w
  Inverted = false
  LineAngle = 0
  LockPosition = false
  MeasureType = 1
  OverTolerance = 0
  References2D = -> [View]
  Rotation = 0
  ScaleType = 0
  TheoreticalExact = false
  Type = 2
  UnderTolerance = 0
  X = 42.4652
  Y = -38.9306
FEATURE [TechDraw::DrawViewDimension] Dimension001
  AngleOverride = false
  Arbitrary = false
  ArbitraryTolerances = false
  EqualTolerance = true
  ExtensionAngle = 0
  FormatSpec = %.2w
  FormatSpecOverTolerance = %+.2w
  FormatSpecUnderTolerance = %+.2w
  Inverted = false
  LineAngle = 0
  LockPosition = false
  MeasureType = 1
  OverTolerance = 0
  References2D = -> [View]
  Rotation = 0
  ScaleType = 0
  TheoreticalExact = false
  Type = 2
  UnderTolerance = 0
  X = 45.1946
  Y = 8.61143
FEATURE [TechDraw::DrawViewSection] SectionView  label="Section  - "
  BaseView = -> View
  CoarseView = false
  CutSurfaceDisplay = 1
  Direction = (1,0,0)
  FileGeomPattern = <path>
  FileHatchPattern = <path>
  Focus = 100
  FuseBeforeCut = false
  HardHidden = false
  HatchOffset = (0,0,0)
  HatchRotation = 0
  HatchScale = 1
  IsoCount = 0
  IsoHidden = false
  IsoVisible = false
  LockPosition = false
  NameGeomPattern = Diamond
  Perspective = false
  Rotation = 90
  ScaleType = 0
  ScrubCount = 0
  SeamHidden = false
  SeamVisible = true
  SectionDirection = 4
  SectionLineStretch = 1
  SectionNormal = (1,0,0)
  SectionOrigin = (0,0,1467.5)
  SmoothHidden = false
  SmoothVisible = true
  Source = -> [Body123]
  TrimAfterCut = false
  UsePreviousCut = false
  X = 157.277
  XDirection = (0,0,1)
  Y = 105
  expr: Y = Template.Height / 2
FEATURE [TechDraw::DrawViewDimension] Dimension002
  AngleOverride = false
  Arbitrary = false
  ArbitraryTolerances = false
  EqualTolerance = true
  ExtensionAngle = 0
  FormatSpec = %.2w
  FormatSpecOverTolerance = %+.2w
  FormatSpecUnderTolerance = %+.2w
  Inverted = false
  LineAngle = 0
  LockPosition = false
  MeasureType = 1
  OverTolerance = 0
  References2D = -> [SectionView]
  Rotation = 0
  ScaleType = 0
  TheoreticalExact = false
  Type = 1
  UnderTolerance = 0
  X = 0.683682
  Y = 55.2929
FEATURE [TechDraw::DrawViewDimension] Dimension003
  AngleOverride = false
  Arbitrary = false
  ArbitraryTolerances = false
  EqualTolerance = true
  ExtensionAngle = 0
  FormatSpec = %.2w
  FormatSpecOverTolerance = %+.2w
  FormatSpecUnderTolerance = %+.2w
  Inverted = false
  LineAngle = 0
  LockPosition = false
  MeasureType = 1
  OverTolerance = 0
  References2D = -> [SectionView]
  Rotation = 0
  ScaleType = 0
  TheoreticalExact = false
  Type = 1
  UnderTolerance = 0
  X = 0.158865
  Y = 68.5155
FEATURE [TechDraw::DrawViewDimension] Dimension004
  AngleOverride = false
  Arbitrary = false
  ArbitraryTolerances = false
  EqualTolerance = true
  ExtensionAngle = 0
  FormatSpec = %.2w
  FormatSpecOverTolerance = %+.2w
  FormatSpecUnderTolerance = %+.2w
  Inverted = false
  LineAngle = 0
  LockPosition = false
  MeasureType = 1
  OverTolerance = 0
  References2D = -> [SectionView]
  Rotation = 0
  ScaleType = 0
  TheoreticalExact = false
  Type = 1
  UnderTolerance = 0
  X = -3.16566
  Y = -53.4728
FEATURE [TechDraw::DrawViewDimension] Dimension005
  AngleOverride = false
  Arbitrary = false
  ArbitraryTolerances = false
  EqualTolerance = true
  ExtensionAngle = 0
  FormatSpec = %.2w
  FormatSpecOverTolerance = %+.2w
  FormatSpecUnderTolerance = %+.2w
  Inverted = false
  LineAngle = 0
  LockPosition = false
  MeasureType = 1
  OverTolerance = 0
  References2D = -> [SectionView]
  Rotation = 0
  ScaleType = 0
  TheoreticalExact = false
  Type = 1
  UnderTolerance = 0
  X = -25.9778
  Y = 46.3177
FEATURE [TechDraw::DrawViewDimension] Dimension006
  AngleOverride = false
  Arbitrary = true
  ArbitraryTolerances = false
  EqualTolerance = true
  ExtensionAngle = 0
  FormatSpec = ⌀5,0
  FormatSpecOverTolerance = %+.2w
  FormatSpecUnderTolerance = %+.2w
  Inverted = false
  LineAngle = 0
  LockPosition = false
  MeasureType = 1
  OverTolerance = 0
  References2D = -> [View001]
  Rotation = 0
  ScaleType = 0
  TheoreticalExact = false
  Type = 5
  UnderTolerance = 0
  X = 44.4861
  Y = -24.9682
FEATURE [TechDraw::DrawViewDimension] Dimension007
  AngleOverride = false
  Arbitrary = false
  ArbitraryTolerances = false
  EqualTolerance = true
  ExtensionAngle = 0
  FormatSpec = %.2w
  FormatSpecOverTolerance = %+.2w
  FormatSpecUnderTolerance = %+.2w
  Inverted = false
  LineAngle = 0
  LockPosition = false
  MeasureType = 1
  OverTolerance = 0
  References2D = -> [View001]
  Rotation = 0
  ScaleType = 0
  TheoreticalExact = false
  Type = 0
  UnderTolerance = 0
  X = -12.6028
  Y = 21.5334
FEATURE [TechDraw::DrawPage] Page  label="sleeve_outer_Page"
  KeepUpdated = true
  NextBalloonIndex = 1
  ProjectionType = 0
  Template = -> Template
  Views = -> [View,View001,Dimension,Dimension001,SectionView,Dimension002,Dimension003,Dimension004,Dimension005,Dimension006,Dimension007]
FEATURE [PartDesign::CoordinateSystem] Local_CS041  label="sleeve_inner_flange_top_LCS"
  AttacherType = Attacher::AttachEngine3D
  AttachmentOffset = pos=(0,0,8) rot=(0,0,1;0rad)
  AttachmentSupport = -> [XY_Plane101]
  MapMode = 5
  Placement = pos=(0,0,8) rot=(0,0,1;0rad)
FEATURE [PartDesign::CoordinateSystem] Local_CS042  label="sleeve_inner_end_LCS"
  AttacherType = Attacher::AttachEngine3D
  AttachmentOffset = pos=(0,0,79) rot=(0,0,1;0rad)
  AttachmentSupport = -> [XY_Plane101]
  MapMode = 5
  Placement = pos=(0,0,79) rot=(0,0,1;0rad)
FEATURE [PartDesign::Body] Body124  label="sleeve_inner"
  Group = -> [Sketch221,Revolution,Boolean031,Local_CS041,Local_CS042]
  Origin = -> Origin101
  Tip = -> Boolean031
FEATURE [TechDraw::DrawViewPart] View002
  CoarseView = false
  Direction = (0,-1,0)
  Focus = 100
  HardHidden = false
  IsoCount = 0
  IsoHidden = false
  IsoVisible = false
  LockPosition = false
  Perspective = false
  Rotation = 180
  ScaleType = 0
  ScrubCount = 0
  SeamHidden = false
  SeamVisible = true
  SmoothHidden = false
  SmoothVisible = true
  Source = -> [Body124]
  X = 142.629
  XDirection = (1,0,0)
  Y = 105
  expr: Y = Template.Height / 2
FEATURE [TechDraw::DrawViewPart] View003
  CoarseView = false
  Direction = (0,0,1)
  Focus = 100
  HardHidden = false
  IsoCount = 0
  IsoHidden = false
  IsoVisible = false
  LockPosition = false
  Perspective = false
  Rotation = 0
  ScaleType = 0
  ScrubCount = 0
  SeamHidden = false
  SeamVisible = true
  SmoothHidden = false
  SmoothVisible = true
  Source = -> [Body124]
  X = 54.9249
  XDirection = (1,0,0)
  Y = 105
  expr: Y = Template.Height / 2
FEATURE [TechDraw::DrawViewSection] SectionView001  label="Section001  - "
  BaseView = -> View002
  CoarseView = false
  CutSurfaceDisplay = 1
  Direction = (-1,0,-1e-16)
  FileGeomPattern = <path>
  FileHatchPattern = <path>
  Focus = 100
  FuseBeforeCut = false
  HardHidden = false
  HatchOffset = (0,0,0)
  HatchRotation = 0
  HatchScale = 1
  IsoCount = 0
  IsoHidden = false
  IsoVisible = false
  LockPosition = false
  NameGeomPattern = Diamond
  Perspective = false
  Rotation = 90
  ScaleType = 0
  ScrubCount = 0
  SeamHidden = false
  SeamVisible = true
  SectionDirection = 4
  SectionLineStretch = 1
  SectionNormal = (-1,0,-1e-16)
  SectionOrigin = (0,0,1473)
  SmoothHidden = false
  SmoothVisible = true
  Source = -> [Body124]
  TrimAfterCut = false
  UsePreviousCut = false
  X = 244.783
  XDirection = (1e-16,0,-1)
  Y = 105
  expr: Y = Template.Height / 2
FEATURE [TechDraw::DrawViewDimension] Dimension008
  AngleOverride = false
  Arbitrary = false
  ArbitraryTolerances = false
  EqualTolerance = true
  ExtensionAngle = 0
  FormatSpec = %.2w
  FormatSpecOverTolerance = %+.2w
  FormatSpecUnderTolerance = %+.2w
  Inverted = false
  LineAngle = 0
  LockPosition = false
  MeasureType = 1
  OverTolerance = 0
  References2D = -> [View003]
  Rotation = 0
  ScaleType = 0
  TheoreticalExact = false
  Type = 0
  UnderTolerance = 0
  X = 4.06158
  Y = 22.1008
FEATURE [TechDraw::DrawViewDimension] Dimension011
  AngleOverride = false
  Arbitrary = false
  ArbitraryTolerances = false
  EqualTolerance = true
  ExtensionAngle = 0
  FormatSpec = %.2w
  FormatSpecOverTolerance = %+.2w
  FormatSpecUnderTolerance = %+.2w
  Inverted = false
  LineAngle = 0
  LockPosition = false
  MeasureType = 1
  OverTolerance = 0
  References2D = -> [SectionView001]
  Rotation = 0
  ScaleType = 0
  TheoreticalExact = false
  Type = 1
  UnderTolerance = 0
  X = -0.625347
  Y = 50.1929
FEATURE [TechDraw::DrawViewDimension] Dimension012
  AngleOverride = false
  Arbitrary = false
  ArbitraryTolerances = false
  EqualTolerance = true
  ExtensionAngle = 0
  FormatSpec = %.2w
  FormatSpecOverTolerance = %+.2w
  FormatSpecUnderTolerance = %+.2w
  Inverted = false
  LineAngle = 0
  LockPosition = false
  MeasureType = 1
  OverTolerance = 0
  References2D = -> [View002]
  Rotation = 0
  ScaleType = 0
  TheoreticalExact = false
  Type = 1
  UnderTolerance = 0
  X = -0.138556
  Y = -52.356
FEATURE [TechDraw::DrawViewDimension] Dimension013
  AngleOverride = false
  Arbitrary = false
  ArbitraryTolerances = false
  EqualTolerance = true
  ExtensionAngle = 0
  FormatSpec = %.2w
  FormatSpecOverTolerance = %+.2w
  FormatSpecUnderTolerance = %+.2w
  Inverted = false
  LineAngle = 0
  LockPosition = false
  MeasureType = 1
  OverTolerance = 0
  References2D = -> [View002]
  Rotation = 0
  ScaleType = 0
  TheoreticalExact = false
  Type = 2
  UnderTolerance = 0
  X = 21.4492
  Y = 4.5306
FEATURE [TechDraw::DrawViewDimension] Dimension014
  AngleOverride = false
  Arbitrary = false
  ArbitraryTolerances = false
  EqualTolerance = true
  ExtensionAngle = 0
  FormatSpec = %.2w
  FormatSpecOverTolerance = %+.2w
  FormatSpecUnderTolerance = %+.2w
  Inverted = false
  LineAngle = 0
  LockPosition = false
  MeasureType = 1
  OverTolerance = 0
  References2D = -> [View002]
  Rotation = 0
  ScaleType = 0
  TheoreticalExact = false
  Type = 2
  UnderTolerance = 0
  X = 43.4564
  Y = -40.9108
FEATURE [TechDraw::DrawViewDimension] Dimension015
  AngleOverride = false
  Arbitrary = true
  ArbitraryTolerances = false
  EqualTolerance = true
  ExtensionAngle = 0
  FormatSpec = ⌀4,2
  FormatSpecOverTolerance = %+.2w
  FormatSpecUnderTolerance = %+.2w
  Inverted = false
  LineAngle = 0
  LockPosition = false
  MeasureType = 1
  OverTolerance = 0
  References2D = -> [View003]
  Rotation = 0
  ScaleType = 0
  TheoreticalExact = false
  Type = 5
  UnderTolerance = 0
  X = 17.5529
  Y = -0.907274
FEATURE [TechDraw::DrawPage] Page001  label="sleeve_inner_Page"
  KeepUpdated = true
  NextBalloonIndex = 1
  ProjectionType = 0
  Template = -> Template
  Views = -> [View002,View003,SectionView001,Dimension008,Dimension011,Dimension012,Dimension013,Dimension014,Dimension015]
FEATURE [App::DocumentObjectGroup] Group011  label="blueprints"
  Group = -> [Page,Page001,Page002,Page004,Page003]
FEATURE [App::DocumentObjectGroup] Group021  label="sleeve_Group"
  Group = -> [Body124,Body123]
FEATURE [Part::Mirroring] Part__Mirroring037  label="pillar_dec_corner_base_sketch (Mirror #34)"
  Base = (0,0,0)
  Normal = (1,0,0)
  Source = -> Sketch056
FEATURE [PartDesign::SubShapeBinder] Binder148
  BindCopyOnChange = 0
  BindMode = 0
  ClaimChildren = true
  Context = -> Body147 [Binder148.]
  Fuse = false
  MakeFace = true
  OffsetFill = false
  OffsetIntersection = false
  OffsetJoinType = 0
  OffsetOpenResult = false
  PartialLoad = false
  Relative = false
  Support = -> [Part__Mirroring037]
  _Version = 2
FEATURE [PartDesign::FeaturePython] BaseBend056  label="pilllar3_dec_corner_mirror_BaseBend"  # WARN: FeaturePython — macro-defined, semantics opaque (R4)
  BendSide = 1
  BendSketch = -> Binder148
  MidPlane = false
  Reverse = false
  Suppressed = false
  length = 1214
  radius = 2
  thickness = 0.5
  expr: length = <<pillar3_dec_corner_BaseBend>>.length
  expr: radius = <<pillar3_dec_corner_BaseBend>>.radius
  expr: thickness = <<pillar3_dec_corner_BaseBend>>.thickness
FEATURE [Sketcher::SketchObject] Sketch266
  AttachmentSupport = -> [XZ_Plane127]
  ExternalGeometry = -> [Binder148]
  FullyConstrained = true
  MapMode = 5
  Placement = pos=(0,0,0) rot=(1,0,0;1.5708rad)
  sketch-geometry (3):
    g0: ArcOfCircle CenterX=-13.3 CenterY=5 CenterZ=0 NormalX=0 NormalY=0 NormalZ=1 AngleXU=0 Radius=5 StartAngle=3.14159 EndAngle=4.71239
    g1: LineSegment StartX=-18.3 StartY=5 StartZ=0 EndX=-18.3 EndY=0 EndZ=0
    g2: LineSegment StartX=-18.3 StartY=0 StartZ=0 EndX=-13.3 EndY=-3e-16 EndZ=0
  constraints (7):
    c: PointOnObject(g0,g-3)
    c: Coincident(g1,g2)
    c: Vertical(g1)
    c: Coincident(g1,g-3)
    c: Tangent(g0,g1) = -1.5708
    c: Radius(g0) = 5
    c: Tangent(g2,g0) = -1.5708
FEATURE [Sketcher::SketchObject] Sketch267
  AttachmentSupport = -> [YZ_Plane127]
  ExternalGeometry = -> [Binder148]
  FullyConstrained = true
  MapMode = 5
  Placement = pos=(0,0,0) rot=(0.57735,0.57735,0.57735;2.0944rad)
  sketch-geometry (3):
    g0: LineSegment StartX=14 StartY=6.04e-13 StartZ=0 EndX=19 EndY=0 EndZ=0
    g1: LineSegment StartX=19 StartY=0 StartZ=0 EndX=19 EndY=5 EndZ=0
    g2: ArcOfCircle CenterX=14 CenterY=5 CenterZ=0 NormalX=0 NormalY=0 NormalZ=1 AngleXU=0 Radius=5 StartAngle=4.71239 EndAngle=6.28319
  constraints (7):
    c: PointOnObject(g0,g-1)
    c: Coincident(g0,g1)
    c: Vertical(g1)
    c: Coincident(g0,g-3)
    c: Tangent(g2,g1) = -1.5708
    c: Tangent(g2,g0) = -1.5708
    c: Radius(g2) = 5
FEATURE [PartDesign::Pocket] Pocket142
  BaseFeature = -> BaseBend056
  Direction = (0,1,-2e-16)
  Length = 5
  Length2 = 5
  Midplane = true
  Profile = -> Sketch266
  ReferenceAxis = -> Sketch266 [N_Axis]
  Suppressed = false
  Type = 1
FEATURE [PartDesign::Pocket] Pocket143
  BaseFeature = -> Pocket142
  Direction = (-1,0,0)
  Length = 5
  Length2 = 5
  Midplane = true
  Profile = -> Sketch267
  ReferenceAxis = -> Sketch267 [N_Axis]
  Suppressed = false
  Type = 1
FEATURE [PartDesign::Plane] DatumPlane009
  AttachmentOffset = pos=(0,0,607) rot=(0,0,1;0rad)
  AttachmentSupport = -> [XY_Plane127]
  Length = 60
  MapMode = 5
  Placement = pos=(0,0,607) rot=(0,0,1;0rad)
  ResizeMode = 0
  Width = 60
  expr: .AttachmentOffset.Base.z = <<pilllar3_dec_corner_mirror_BaseBend>>.length / 2
FEATURE [PartDesign::Mirrored] Mirrored022
  BaseFeature = -> Pocket143
  MirrorPlane = -> DatumPlane009
  Originals = -> [Pocket142,Pocket143]
  Suppressed = false
FEATURE [Part::Compound] Compound103
  Links = -> [Link047]
FEATURE [PartDesign::Boolean] Boolean051
  BaseFeature = -> Mirrored022
  Group = -> [Compound103]
  Suppressed = false
  Type = 1
  UsePlacement = true
FEATURE [PartDesign::CoordinateSystem] Local_CS043
  AttacherType = Attacher::AttachEngine3D
  AttachmentSupport = -> [XY_Plane127]
  MapMode = 5
FEATURE [PartDesign::Body] Body147  label="pilllar3_dec_corner_mirror"
  Group = -> [Binder148,BaseBend056,Sketch266,Sketch267,Pocket142,Pocket143,DatumPlane009,Mirrored022,Boolean051,Local_CS043]
  Origin = -> Origin128
  Tip = -> Boolean051
FEATURE [PartDesign::CoordinateSystem] Local_CS044  label="hat3_cap_bottom_LCS"
  AttacherType = Attacher::AttachEngine3D
  AttachmentSupport = -> [XY_Plane123]
  MapMode = 5
FEATURE [PartDesign::CoordinateSystem] Local_CS045  label="hat3_cap_top_LCS"
  AttacherType = Attacher::AttachEngine3D
  AttachmentOffset = pos=(0,0,3) rot=(0,0,1;0rad)
  AttachmentSupport = -> [XY_Plane123]
  MapMode = 5
  Placement = pos=(0,0,3) rot=(0,0,1;0rad)
FEATURE [PartDesign::Body] Body143  label="hat3_cap"
  Group = -> [Binder146,Pad046,Local_CS044,Local_CS045]
  Origin = -> Origin124
  Tip = -> Pad046
FEATURE [Part::FeaturePython] PolarArray012  # WARN: FeaturePython — macro-defined, semantics opaque (R4)
  Alignment = 0
  AttacherType = Attacher::AttachEngine3D
  CellStart = A1
  Count = 3
  DistributionLaw = 0
  EndInclusive = false
  ExposePlacement = false
  FlipX = false
  FlipZ = false
  GeneratorMode = 0
  MarkerShape = 1
  MarkerSize = 0
  NumElements = 3
  OrientMode = 2
  Placement = pos=(0,0,0) rot=(0,0,1;0.523599rad)
  Radius = 118.5
  Reverse = false
  SpanEnd = 360
  SpanStart = 0
  Step = 120
  Type = lattice2PolarArray2.PolarArray
  UseArcRadius = false
  UseArcRange = 0
  VSGVersion = 1
  Values = 0.0 | 120.0 | 240.0
  ValuesSource = 2
  isLattice = 1
  expr: Radius = <<hat3_border>>.Constraints.min_r - 12.5 mm
FEATURE [Part::FeaturePython] Populate072  label="Populate PolarArray012 with hole_3.4mm_extrude"  # WARN: FeaturePython — macro-defined, semantics opaque (R4)
  Copying = 0
  ExposePlacement = false
  MarkerShape = 1
  MarkerSize = 0
  NumElements = 0
  Object = -> Extrude019
  OutputCompounding = 1
  PlacementsTo = -> PolarArray012
  Referencing = 0
  Type = lattice2PopulateCopies.LatticePopulateCopies
  isLattice = 0
FEATURE [Sketcher::SketchObject] Sketch268
  AttachmentSupport = -> [YZ_Plane121]
  FullyConstrained = false
  MapMode = 5
  Placement = pos=(0,0,0) rot=(0.57735,0.57735,0.57735;2.0944rad)
  sketch-geometry (7):
    g0: Circle CenterX=11.5 CenterY=9 CenterZ=0 NormalX=0 NormalY=0 NormalZ=1 AngleXU=0 Radius=1.7
    g1: Circle CenterX=11.5 CenterY=40.3333 CenterZ=0 NormalX=0 NormalY=0 NormalZ=1 AngleXU=0 Radius=1.7
    g2: Circle CenterX=11.5 CenterY=71.6667 CenterZ=0 NormalX=0 NormalY=0 NormalZ=1 AngleXU=0 Radius=1.7
    g3: LineSegment StartX=11.5 StartY=9 StartZ=0 EndX=11.5 EndY=40.3333 EndZ=0
    g4: LineSegment StartX=11.5 StartY=40.3333 StartZ=0 EndX=11.5 EndY=71.6667 EndZ=0
    g5: Circle CenterX=11.5 CenterY=103 CenterZ=0 NormalX=0 NormalY=0 NormalZ=1 AngleXU=0 Radius=1.86607
    g6: LineSegment StartX=11.5 StartY=103 StartZ=0 EndX=11.5 EndY=71.6667 EndZ=0
  constraints (17):
    c: Equal(g0,g1)
    c: Equal(g0,g2)
    c: Diameter(g0) = 3.4
    c: Coincident(g3,g0)
    c: Coincident(g3,g1)
    c: Coincident(g3,g4)
    c: Coincident(g4,g2)
    c: Vertical(g4)
    c: Vertical(g3)
    c: Equal(g3,g4)
    c: Coincident(g6,g5)
    c: Coincident(g6,g2)
    c: Vertical(g6)
    c: DistanceY(g0) = 9
    c: DistanceX(g0) = 11.5
    c: Equal(g6,g4)
    c: DistanceY(g5) = 103
FEATURE [PartDesign::CoordinateSystem] Local_CS047  label="pillar3_bottom_LCS"
  AttacherType = Attacher::AttachEngine3D
  AttachmentOffset = pos=(18.3,4,0) rot=(0,0,1;1.5708rad)
  AttachmentSupport = -> [XY_Plane121]
  MapMode = 5
  Placement = pos=(18.3,4,0) rot=(0,0,1;1.5708rad)
FEATURE [PartDesign::CoordinateSystem] pillar_bottom_LCS
  AttacherType = Attacher::AttachEngine3D
  AttachmentOffset = pos=(-50.5,0,0) rot=(0,0,1;0rad)
  AttachmentSupport = -> [XY_Plane015]
  MapMode = 5
  Placement = pos=(-50.5,0,0) rot=(0,0,1;0rad)
FEATURE [PartDesign::Body] Body011  label="pillar_bottom_material_0.30ansi"
  Group = -> [Sketch010,BaseBend005,Sketch011,Sketch012,WireFilter,WireFilter001,Pocket,Pocket001,Sketch070,Pocket031,Sketch118,Pocket063,pillar_bottom_LCS]
  Origin = -> Origin015
  Placement = pos=(18.3,54.5,0) rot=(0,0,1;1.5708rad)
  Tip = -> Pocket063
  expr: Placement = <<pillar_bottom_placement>>.AttachmentOffset
FEATURE [App::DocumentObjectGroup] Group022  label="pillar_Group"
  Group = -> [Body010,Body011,Body012,Body013,Body014]
FEATURE [App::Link] Link048  label="PSU_holes"
  LinkedObject = -> <external UET-VAS-060A20_12V_IP20.FCStd>#Sketch001
FEATURE [Part::Extrusion] Extrude039  label="PSU_holes_Extrude"
  Base = -> Link048
  Dir = (0,0,1)
  DirMode = 2
  FaceMakerClass = Part::FaceMakerBullseye
  LengthFwd = 10
  LengthRev = 0
  Solid = true
  Symmetric = false
FEATURE [Part::FeaturePython] Placment039  label="hat3_PSU_placement"  # WARN: FeaturePython — macro-defined, semantics opaque (R4)
  AttacherType = Attacher::AttachEngine3D
  ExposePlacement = true
  MarkerShape = 1
  MarkerSize = 50
  NumElements = 1
  Placement = pos=(-24,152,0) rot=(0,0,1;0rad)
  Type = lattice2AttachablePlacement.AttachablePlacement
  isLattice = 1
FEATURE [Part::FeaturePython] Populate073  label="Populate hat3_PSU_placement with PSU_holes_Extrude"  # WARN: FeaturePython — macro-defined, semantics opaque (R4)
  Copying = 0
  ExposePlacement = false
  MarkerShape = 1
  MarkerSize = 0
  NumElements = 0
  Object = -> Extrude039
  OutputCompounding = 2
  PlacementsTo = -> Placment039
  Referencing = 0
  Type = lattice2PopulateCopies.LatticePopulateCopies
  isLattice = 0
FEATURE [Part::Cylinder] Cylinder013
  Angle = 360
  AttacherType = Attacher::AttachEngine3D
  FirstAngle = 0
  Height = 10
  Radius = 13.25
  SecondAngle = 0
  expr: Radius = <<sleeve_inner_sketch>>.Constraints.outer_r + 0.25 mm
FEATURE [PartDesign::SubShapeBinder] Binder149
  BindCopyOnChange = 0
  BindMode = 0
  ClaimChildren = true
  Context = -> <external composit_full_size3_composit_cut.FCStd>#Link026 [Binder149.]
  Fuse = false
  MakeFace = true
  OffsetFill = false
  OffsetIntersection = false
  OffsetJoinType = 0
  OffsetOpenResult = false
  PartialLoad = false
  Placement = pos=(0,0,0) rot=(1,0,0;1.5708rad)
  Relative = false
  Support = -> [Sketch225]
  _Version = 2
  expr: Support = <<UV_driver_holder_base_Sketch>>._self
FEATURE [PartDesign::FeaturePython] BaseBend050  label="UV_driver_holder_BaseBend"  # WARN: FeaturePython — macro-defined, semantics opaque (R4)
  BendSide = 0
  BendSketch = -> Binder149
  MidPlane = true
  Reverse = false
  Suppressed = false
  length = 20
  radius = 0.1
  thickness = 0.3
FEATURE [Sketcher::SketchObject] Sketch269
  AttachmentOffset = pos=(31.5,10,0) rot=(0,0,1;0rad)
  AttachmentSupport = -> [XY_Plane103]
  FullyConstrained = true
  MapMode = 5
  Placement = pos=(31.5,10,0) rot=(0,0,1;0rad)
  expr: .AttachmentOffset.Base.x = <<UV_driver_holder_base_Sketch>>.Constraints.total_width / 2
  expr: .AttachmentOffset.Base.y = <<UV_driver_holder_BaseBend>>.length / 2
  sketch-geometry (3):
    g0: LineSegment StartX=-3 StartY=0 StartZ=0 EndX=0 EndY=0 EndZ=0
    g1: LineSegment StartX=0 StartY=0 StartZ=0 EndX=0 EndY=-3 EndZ=0
    g2: ArcOfCircle CenterX=-3 CenterY=-3 CenterZ=0 NormalX=0 NormalY=0 NormalZ=1 AngleXU=0 Radius=3 StartAngle=1e-16 EndAngle=1.5708
  constraints (7):
    c: PointOnObject(g0,g-1)
    c: Coincident(g0,g-1)
    c: Coincident(g0,g1)
    c: PointOnObject(g1,g-2)
    c: Tangent(g2,g0) = 1.5708
    c: Tangent(g2,g1) = 1.5708
    c: Radius(g2) = 3
FEATURE [PartDesign::Pocket] Pocket145
  BaseFeature = -> BaseBend050
  Direction = (0,0,-1)
  Length = 5
  Length2 = 5
  Profile = -> Sketch269
  ReferenceAxis = -> Sketch269 [N_Axis]
  Reversed = true
  Suppressed = false
  Type = 0
FEATURE [PartDesign::Mirrored] Mirrored023
  MirrorPlane = -> YZ_Plane103
  Suppressed = false
FEATURE [PartDesign::Mirrored] Mirrored024
  MirrorPlane = -> XZ_Plane103
  Suppressed = false
FEATURE [PartDesign::MultiTransform] MultiTransform002
  BaseFeature = -> Pocket145
  Originals = -> [Pocket145]
  Suppressed = false
  Transformations = -> [Mirrored023,Mirrored024]
FEATURE [Part::Extrusion] Extrude040
  Base = -> Sketch226
  Dir = (0,0,1)
  DirMode = 2
  FaceMakerClass = Part::FaceMakerBullseye
  LengthFwd = 10
  LengthRev = 0
  Solid = true
  Symmetric = false
FEATURE [Part::Compound] Compound104
  Links = -> [Extrude040]
FEATURE [PartDesign::Boolean] Boolean052
  BaseFeature = -> MultiTransform002
  Group = -> [Compound104]
  Suppressed = false
  Type = 1
  UsePlacement = true
FEATURE [PartDesign::Body] Body126  label="UV_driver_holder_material_0.30ansi"
  Group = -> [BaseBend050,Binder149,Sketch269,Pocket145,MultiTransform002,Mirrored023,Mirrored024,Boolean052]
  Origin = -> Origin103
  Tip = -> Boolean052
FEATURE [Part::FeaturePython] Placment040  # WARN: FeaturePython — macro-defined, semantics opaque (R4)
  AttacherType = Attacher::AttachEngine3D
  ExposePlacement = true
  MarkerShape = 1
  MarkerSize = 20
  NumElements = 1
  Placement = pos=(35,130,0) rot=(0,0,1;0rad)
  Type = lattice2AttachablePlacement.AttachablePlacement
  isLattice = 1
FEATURE [Part::FeaturePython] Populate074  label="Populate Placment040 with Extrude040"  # WARN: FeaturePython — macro-defined, semantics opaque (R4)
  Copying = 0
  ExposePlacement = false
  MarkerShape = 1
  MarkerSize = 0
  NumElements = 0
  Object = -> Extrude040
  OutputCompounding = 2
  PlacementsTo = -> Placment040
  Referencing = 0
  Type = lattice2PopulateCopies.LatticePopulateCopies
  isLattice = 0
FEATURE [App::Link] Link049  label="fix_holes"
  LinkedObject = -> <external socket_fixture.FCStd>#Sketch003
FEATURE [Part::FeaturePython] Placment041  # WARN: FeaturePython — macro-defined, semantics opaque (R4)
  AttacherType = Attacher::AttachEngine3D
  ExposePlacement = true
  MarkerShape = 1
  MarkerSize = 10
  NumElements = 1
  Placement = pos=(-69,35,0) rot=(0,0,1;0rad)
  Type = lattice2AttachablePlacement.AttachablePlacement
  isLattice = 1
FEATURE [Part::FeaturePython] Placment042  # WARN: FeaturePython — macro-defined, semantics opaque (R4)
  AttacherType = Attacher::AttachEngine3D
  ExposePlacement = true
  MarkerShape = 1
  MarkerSize = 10
  NumElements = 1
  Placement = pos=(69,35,0) rot=(0,0,1;0rad)
  Type = lattice2AttachablePlacement.AttachablePlacement
  isLattice = 1
  expr: .Placement.Base.x = -<<Placment041>>.Placement.Base.x
  expr: .Placement.Base.y = <<Placment041>>.Placement.Base.y
FEATURE [Part::FeaturePython] Join018  # WARN: FeaturePython — macro-defined, semantics opaque (R4)
  ExposePlacement = false
  Interleave = false
  Links = -> [Placment041,Placment042]
  MarkerShape = 1
  MarkerSize = 0
  NumElements = 2
  Type = lattice2JoinArrays.JoinArrays
  isLattice = 1
FEATURE [Part::Extrusion] Extrude041  label="fix_holes_Extrude"
  Base = -> Link049
  Dir = (0,0,1)
  DirMode = 2
  FaceMakerClass = Part::FaceMakerBullseye
  LengthFwd = 10
  LengthRev = 0
  Solid = true
  Symmetric = false
FEATURE [Part::FeaturePython] Populate075  label="Populate Join018 with fix_holes_Extrude"  # WARN: FeaturePython — macro-defined, semantics opaque (R4)
  Copying = 0
  ExposePlacement = false
  MarkerShape = 1
  MarkerSize = 0
  NumElements = 0
  Object = -> Extrude041
  OutputCompounding = 1
  PlacementsTo = -> Join018
  Referencing = 0
  Type = lattice2PopulateCopies.LatticePopulateCopies
  isLattice = 0
FEATURE [Part::Compound] Compound102
  Links = -> [Populate071,Populate072,Populate073,Extrude032,Cylinder013,Populate074,Populate075]
FEATURE [PartDesign::Boolean] Boolean050
  BaseFeature = -> Pad045
  Group = -> [Compound102]
  Suppressed = false
  Type = 1
  UsePlacement = true
FEATURE [PartDesign::Body] Body142  label="hat3_base"
  Group = -> [Binder142,Pad045,Boolean050,Local_CS037,Local_CS038]
  Origin = -> Origin123
  Tip = -> Boolean050
FEATURE [Part::Mirroring] Part__Mirroring038  label="tech_sector_pillar_material_0.30ansi (Mirror #35)"
  Base = (0,0,0)
  Normal = (-0.5,0.866025,0)
  Source = -> Body073
  expr: .Normal.x = cos(120 deg)
  expr: .Normal.y = sin(120 deg)
FEATURE [App::DocumentObjectGroup] Group023  label="obsolete"
  Group = -> [Body015,Body137,Body138,Body140,Part013,Part015]
FEATURE [App::DocumentObjectGroup] Group024  label="tech_sector"
  Group = -> [Body074,Body077,Body073,Part__Mirroring038]
FEATURE [Sketcher::SketchObject] Sketch270
  FullyConstrained = true
  sketch-geometry (13):
    g0: Circle CenterX=0 CenterY=20 CenterZ=0 NormalX=0 NormalY=0 NormalZ=1 AngleXU=0 Radius=1.7
    g1: Circle CenterX=0 CenterY=-20 CenterZ=0 NormalX=0 NormalY=0 NormalZ=1 AngleXU=0 Radius=1.7
    g2: GeomPoint X=0 Y=0 Z=0
    g3: LineSegment StartX=-10 StartY=-24 StartZ=0 EndX=10 EndY=-24 EndZ=0
    g4: LineSegment StartX=15 StartY=-19 StartZ=0 EndX=15 EndY=19 EndZ=0
    g5: LineSegment StartX=10 StartY=24 StartZ=0 EndX=-10 EndY=24 EndZ=0
    g6: LineSegment StartX=-15 StartY=19 StartZ=0 EndX=-15 EndY=-19 EndZ=0
    g7: ArcOfCircle CenterX=-10 CenterY=-19 CenterZ=0 NormalX=0 NormalY=0 NormalZ=1 AngleXU=0 Radius=5 StartAngle=3.14159 EndAngle=4.71239
    g8: ArcOfCircle CenterX=10 CenterY=-19 CenterZ=0 NormalX=0 NormalY=0 NormalZ=1 AngleXU=0 Radius=5 StartAngle=4.71239 EndAngle=6.28319
    g9: ArcOfCircle CenterX=10 CenterY=19 CenterZ=0 NormalX=0 NormalY=0 NormalZ=1 AngleXU=0 Radius=5 StartAngle=5e-16 EndAngle=1.5708
    g10: ArcOfCircle CenterX=-10 CenterY=19 CenterZ=0 NormalX=0 NormalY=0 NormalZ=1 AngleXU=0 Radius=5 StartAngle=1.5708 EndAngle=3.14159
    g11: GeomPoint X=-15 Y=-24 Z=0
    g12: GeomPoint X=15 Y=24 Z=0
  constraints (29):
    c: PointOnObject(g0,g-2)
    c: Equal(g1,g0)
    c: Diameter(g1) = 3.4
    c: Symmetric(g1,g0,g-1)
    c: DistanceY(g1,g0) = 40
    c: Coincident(g2,g-1)
    c: Tangent(g3,g7) = -1.5708
    c: Tangent(g3,g8) = -1.5708
    c: Tangent(g4,g8) = -1.5708
    c: Tangent(g4,g9) = -1.5708
    c: Tangent(g5,g9) = -1.5708
    c: Tangent(g5,g10) = -1.5708
    c: Tangent(g6,g10) = -1.5708
    c: Tangent(g6,g7) = -1.5708
    c: Horizontal(g3)
    c: Horizontal(g5)
    c: Vertical(g4)
    c: Vertical(g6)
    c: Equal(g7,g8)
    c: Equal(g8,g9)
    c: Equal(g9,g10)
    c: PointOnObject(g11,g3)
    c: PointOnObject(g11,g6)
    c: PointOnObject(g12,g4)
    c: PointOnObject(g12,g5)
    c: Radius(g9) = 5
    c: Symmetric(g12,g11,g-1)
    c: DistanceY(g3,g5) = 48
    c: DistanceX(g6,g4) = 30
FEATURE [Sketcher::SketchObject] Sketch271
  ExternalGeometry = -> [Sketch047]
  FullyConstrained = true
  sketch-geometry (3):
    g0: Circle CenterX=22.9472 CenterY=102 CenterZ=0 NormalX=0 NormalY=0 NormalZ=1 AngleXU=0 Radius=1.7
    g1: Circle CenterX=340.4 CenterY=102 CenterZ=0 NormalX=0 NormalY=0 NormalZ=1 AngleXU=0 Radius=1.7
    g2: Circle CenterX=340.4 CenterY=52 CenterZ=0 NormalX=0 NormalY=0 NormalZ=1 AngleXU=0 Radius=1.7
  constraints (9):
    c: Horizontal(g-5,g2)
    c: Vertical(g2,g1)
    c: Horizontal(g1,g-4)
    c: DistanceX(g-4,g1) = 0.4
    c: Equal(g1,g-4)
    c: Horizontal(g0,g-3)
    c: DistanceX(g-3,g0) = 0.2
    c: Equal(g0,g-3)
    c: Equal(g2,g-5)
FEATURE [Part::Extrusion] Extrude042
  Base = -> Sketch271
  Dir = (0,0,1)
  DirMode = 2
  FaceMakerClass = Part::FaceMakerBullseye
  LengthFwd = 30
  LengthRev = 0
  Placement = pos=(0,0,0) rot=(0.57735,0.57735,0.57735;2.0944rad)
  Solid = true
  Symmetric = true
FEATURE [Part::Compound] Compound023  label="sink_fix"
  Links = -> [Extrude042]
  Placement = pos=(0,1,392) rot=(0,0,1;0rad)
  expr: .Placement.Base.z = basin_big#<<Properties>>.height
FEATURE [Part::Compound] Compound005  label="part1_part2_common_cut"
  Links = -> [Extrude,Extrude001,Compound022,Compound023,Compound029,Extrude011,Compound074]
FEATURE [Part::FeaturePython] Array  # Draft array (typed FeaturePython)
  AlwaysSyncPlacement = false
  Angle = 240
  ArrayType = 1
  Axis = (0,0,1)
  Base = -> Compound005
  Center = (0,0,0)
  Count = 2
  ExpandArray = false
  Fuse = true
  IntervalAxis = (0,0,0)
  IntervalX = (50,0,0)
  IntervalY = (0,50,0)
  IntervalZ = (0,0,50)
  NumberCircles = 3
  NumberPolar = 2
  NumberX = 2
  NumberY = 2
  NumberZ = 1
  Placement = pos=(0,0,0) rot=(0,0,1;4.18879rad)
  PlacementList = 2 placements: [(0,0,0),(0,0,0)]
  RadialDistance = 50
  ScaleList = (2) [(1,1,1),(1,1,1)]
  Symmetry = 1
  TangentialDistance = 25
FEATURE [Part::Compound] Compound016  label="part1_cut1"
  Links = -> [Compound015,Compound005,Extrude005,Extrude015]
FEATURE [PartDesign::Boolean] Boolean001
  BaseFeature = -> BaseBend
  Group = -> [Compound016]
  Suppressed = false
  Type = 1
  UsePlacement = false
  expr: Group = <<part1_cut1>>._self
FEATURE [PartDesign::Boolean] Boolean002
  BaseFeature = -> Boolean001
  Group = -> [Compound026]
  Refine = true
  Suppressed = false
  Type = 0
  UsePlacement = false
  expr: Group = <<part1_fuse1>>._self
FEATURE [PartDesign::Pocket] Pocket025
  BaseFeature = -> Boolean002
  Direction = (-1,0,0)
  Length = 5
  Length2 = 5
  Midplane = true
  Profile = -> Sketch044
  ReferenceAxis = -> Sketch044 [N_Axis]
  Suppressed = false
  Type = 1
FEATURE [PartDesign::Boolean] Boolean005
  BaseFeature = -> Pocket025
  Group = -> [Compound024]
  Suppressed = false
  Type = 1
  UsePlacement = false
  expr: Group = <<part1_cut2>>._self
FEATURE [PartDesign::Body] Body  label="part1_material_0.30ansi"
  Group = -> [Binder,BaseBend,Boolean001,Boolean002,Sketch044,Pocket025,Boolean005,Local_CS025,Local_CS026]
  Origin = -> Origin
  Tip = -> Boolean005
FEATURE [Part::Compound] Compound021  label="part2_cut1"
  Links = -> [Array,Compound019,Compound015,Part__Mirroring016]
FEATURE [PartDesign::Boolean] Boolean
  BaseFeature = -> BaseBend001
  Group = -> [Compound021]
  Refine = true
  Suppressed = false
  Type = 1
  UsePlacement = false
  expr: Group = <<part2_cut1>>._self
FEATURE [PartDesign::Boolean] Boolean003
  BaseFeature = -> Boolean
  Group = -> [Compound007]
  Refine = true
  Suppressed = false
  Type = 0
  UsePlacement = false
  expr: Group = <<part2_fuse1>>._self
FEATURE [PartDesign::Boolean] Boolean006
  BaseFeature = -> Boolean003
  Group = -> [Compound025]
  Suppressed = false
  Type = 1
  UsePlacement = false
  expr: Group = <<part2_cut2>>._self
FEATURE [PartDesign::Body] Body001  label="part2_material_0.30ansi"
  Group = -> [Binder001,BaseBend001,Boolean,Boolean003,Boolean006,Local_CS027,Local_CS028]
  Origin = -> Origin001
  Tip = -> Boolean006
FEATURE [PartDesign::CoordinateSystem] Local_CS048
  AttacherType = Attacher::AttachEngine3D
  AttachmentOffset = pos=(0,0,0) rot=(0,1,0;1.5708rad)
  AttachmentSupport = -> [Sketch171]
  MapMode = 7
  Placement = pos=(42.5,285,0) rot=(0.517473,0.605071,0.605071;2.18654rad)
FEATURE [Sketcher::SketchObject] Sketch272
  AttachmentSupport = -> [Local_CS048]
  FullyConstrained = true
  MapMode = 5
  Placement = pos=(42.5,285,0) rot=(0.517473,0.605071,0.605071;2.18654rad)
FEATURE [PartDesign::Body] Body107  label="basement_bottom_amplifier_material_0.50ansi"
  Group = -> [Sketch171,BaseBend044,Bend026,Sketch174,Binder117,Pocket105,Sketch176,Binder120,Local_CS048,Sketch272,Mirrored011,Pocket110,Binder121,Pocket111,Sketch195,Mirrored012,PDW_Add,PDW_Common_Add001,PolarPattern007,Pocket106,Boolean027,Local_CS014,Local_CS015]
  Origin = -> Origin080
  Tip = -> Boolean027
FEATURE [App::DocumentObjectGroup] Group015  label="basement_bottom_Group"
  Group = -> [Body009,Body007,Body107]
FEATURE [Sketcher::SketchObject] Sketch273  label="basement_v4_bottom_amplifier_Sketch"
  FullyConstrained = true
  expr: Constraints[4] = 285 mm - 5 mm
  sketch-geometry (6):
    g0: LineSegment StartX=0 StartY=0 StartZ=0 EndX=142.894 EndY=82.5 EndZ=0
    g1: LineSegment StartX=0 StartY=280 StartZ=0 EndX=52.4359 EndY=280 EndZ=0
    g2: ArcOfCircle CenterX=52.4359 CenterY=270 CenterZ=0 NormalX=0 NormalY=0 NormalZ=1 AngleXU=0 Radius=10 StartAngle=0.280016 EndAngle=1.5708
    g3: ArcOfCircle CenterX=879.708 CenterY=507.9 CenterZ=0 NormalX=0 NormalY=0 NormalZ=1 AngleXU=0 Radius=850.799 StartAngle=3.42161 EndAngle=3.66519
    g4: LineSegment StartX=140.485 StartY=0 StartZ=0 EndX=62.0464 EndY=272.764 EndZ=0
    g5: GeomPoint X=60 Y=280 Z=0
  constraints (17):
    c: Coincident(g0,g-1)
    c: Angle(g0) = 0.523599
    c: PointOnObject(g1,g-2)
    c: Horizontal(g1)
    c: DistanceY(g1) = 280
    c: Coincident(g3,g0)
    c: Tangent(g2,g1) = 1.5708
    c: Tangent(g3,g2) = 1.5708
    c: Perpendicular(g3,g0)
    c: Radius(g2) = 10
    c: PointOnObject(g4,g-1)
    c: Tangent(g4,g2) = -1.5708
    c: Angle(g4) = 1.85081
    c: PointOnObject(g5,g3)
    c: PointOnObject(g5,g1)
    c: DistanceX(g5) = 60
    c: Distance(g0) = 165
FEATURE [Part::Mirroring] Part__Mirroring039  label="basement_v4_bottom_amplifier_Sketch (Mirror #36)"
  Base = (0,0,0)
  Normal = (1,0,0)
  Source = -> Sketch273
FEATURE [Part::Compound] Compound105
  Links = -> [Part__Mirroring039,Sketch273]
FEATURE [Part::FeaturePython] Array015  # Draft array (typed FeaturePython)
  Angle = 360
  ArrayType = 1
  Axis = (0,0,1)
  Base = -> Compound105
  Center = (0,0,0)
  Count = 3
  Fuse = true
  IntervalAxis = (0,0,0)
  IntervalX = (50,0,0)
  IntervalY = (0,50,0)
  IntervalZ = (0,0,50)
  NumberCircles = 3
  NumberPolar = 3
  NumberX = 2
  NumberY = 2
  NumberZ = 1
  RadialDistance = 50
  Symmetry = 1
  TangentialDistance = 25
FEATURE [Part::FeaturePython] Connect008  # WARN: FeaturePython — macro-defined, semantics opaque (R4)
  Objects = -> [Array015]
  Tolerance = 0
FEATURE [PartDesign::SubShapeBinder] Binder150
  BindCopyOnChange = 0
  BindMode = 0
  ClaimChildren = true
  Context = -> Body148 [Binder150.]
  Fuse = false
  MakeFace = true
  OffsetFill = false
  OffsetIntersection = false
  OffsetJoinType = 0
  OffsetOpenResult = false
  PartialLoad = false
  Relative = false
  Support = -> [Connect008]
  _Version = 2
FEATURE [PartDesign::Pad] Pad047
  Direction = (0,0,1)
  Length = 18
  Length2 = 10
  Profile = -> Binder150
  Suppressed = false
  Type = 0
FEATURE [Part::MultiFuse] Fusion002
  Placement = pos=(0,0,0) rot=(0,0,1;1.5708rad)
  Shapes = -> [Populate054]
FEATURE [PartDesign::SubShapeBinder] Binder151
  BindCopyOnChange = 0
  BindMode = 0
  ClaimChildren = false
  Context = -> Body149 [Binder151.]
  Fuse = false
  MakeFace = true
  OffsetFill = false
  OffsetIntersection = false
  OffsetJoinType = 0
  OffsetOpenResult = false
  PartialLoad = false
  Relative = true
  Support = -> [Array002]
  _Version = 2
  expr: Support = <<basement_bottom_2d>>._self
FEATURE [PartDesign::Pad] Pad048
  Direction = (0,0,1)
  Length = 18
  Length2 = 10
  Profile = -> Binder151
  Suppressed = false
  Type = 0
FEATURE [Sketcher::SketchObject] Sketch274
  ExternalGeometry = -> [Sketch273]
  FullyConstrained = true
  sketch-geometry (5):
    g0: Circle CenterX=110.493 CenterY=121.528 CenterZ=0 NormalX=0 NormalY=0 NormalZ=1 AngleXU=0 Radius=2
    g1: Circle CenterX=52.4359 CenterY=270 CenterZ=0 NormalX=0 NormalY=0 NormalZ=1 AngleXU=0 Radius=2
    g2: LineSegment StartX=0 StartY=0 StartZ=0 EndX=142.894 EndY=82.5 EndZ=0
    g3: LineSegment StartX=52.4359 StartY=280 StartZ=0 EndX=52.4359 EndY=270 EndZ=0
    g4: LineSegment StartX=52.4359 StartY=270 StartZ=0 EndX=62.0464 EndY=272.764 EndZ=0
  constraints (14):
    c: Coincident(g2,g-1)
    c: Coincident(g2,g-3)
    c: Distance(g0,g2) = 50
    c: Distance(g0,g-3) = 10
    c: PointOnObject(g3,g-4)
    c: Coincident(g3,g1)
    c: Coincident(g3,g4)
    c: PointOnObject(g4,g-3)
    c: Perpendicular(g-3,g4)
    c: Equal(g3,g4)
    c: Perpendicular(g-4,g3)
    c: Distance(g3) = 10
    c: Equal(g1,g0)
    c: Diameter(g0) = 4
FEATURE [Part::Extrusion] Extrude043
  Base = -> Sketch274
  Dir = (0,0,1)
  DirMode = 2
  FaceMakerClass = Part::FaceMakerBullseye
  LengthFwd = 20
  LengthRev = 0
  Solid = true
  Symmetric = false
FEATURE [Part::Mirroring] Part__Mirroring040  label="Extrude043 (Mirror #37)"
  Base = (0,0,0)
  Normal = (1,0,0)
  Source = -> Extrude043
FEATURE [Part::Compound] Compound108
  Links = -> [Part__Mirroring040,Extrude043]
FEATURE [Part::FeaturePython] Array016  # Draft array (typed FeaturePython)
  Angle = 360
  ArrayType = 1
  Axis = (0,0,1)
  Base = -> Compound108
  Center = (0,0,0)
  Count = 3
  Fuse = true
  IntervalAxis = (0,0,0)
  IntervalX = (50,0,0)
  IntervalY = (0,50,0)
  IntervalZ = (0,0,50)
  NumberCircles = 3
  NumberPolar = 3
  NumberX = 2
  NumberY = 2
  NumberZ = 1
  RadialDistance = 50
  Symmetry = 1
  TangentialDistance = 25
FEATURE [Part::Compound] Compound107
  Links = -> [Populate033,Populate028,Populate045,Cylinder012,Fusion002,Array016]
FEATURE [PartDesign::Boolean] Boolean054
  BaseFeature = -> Pad048
  Group = -> [Compound107]
  Suppressed = false
  Type = 1
  UsePlacement = true
FEATURE [PartDesign::Body] Body149  label="basement_v4_bottom"
  Group = -> [Binder151,Pad048,Boolean054]
  Origin = -> Origin130
  Tip = -> Boolean054
FEATURE [PartDesign::SubShapeBinder] Binder152
  BindCopyOnChange = 0
  BindMode = 0
  ClaimChildren = true
  Context = -> Body151 [Binder152.]
  Fuse = true
  MakeFace = false
  OffsetFill = false
  OffsetIntersection = false
  OffsetJoinType = 0
  OffsetOpenResult = false
  PartialLoad = false
  Relative = false
  Support = -> [Connect010]
  _Version = 2
  expr: Support = <<Connect010>>._self
FEATURE [PartDesign::Pad] Pad049
  Direction = (0,0,1)
  Length = 18
  Length2 = 10
  Profile = -> Binder152
  Refine = true
  Suppressed = false
  Type = 0
FEATURE [Sketcher::SketchObject] Sketch275
  ExternalGeometry = -> [Sketch015]
  FullyConstrained = true
  expr: Constraints[9] = <<U-fix_bottom_array>>.Radius - 17.4 mm - 15 mm
  sketch-geometry (4):
    g0: ArcOfCircle CenterX=-472.335 CenterY=-272.703 CenterZ=0 NormalX=0 NormalY=0 NormalZ=1 AngleXU=0 Radius=748.406 StartAngle=0.523599 EndAngle=0.779626
    g1: ArcOfCircle CenterX=52.8018 CenterY=246.406 CenterZ=0 NormalX=0 NormalY=0 NormalZ=1 AngleXU=0 Radius=10 StartAngle=0.779626 EndAngle=1.3597
    g2: LineSegment StartX=0 StartY=0 StartZ=0 EndX=219.104 EndY=126.5 EndZ=0
    g3: ArcOfCircle CenterX=0 CenterY=0 CenterZ=0 NormalX=0 NormalY=0 NormalZ=1 AngleXU=0 Radius=262 StartAngle=1.3597 EndAngle=1.5708
  constraints (11):
    c: Tangent(g1,g0) = -1.5708
    c: Coincident(g2,g-1)
    c: Coincident(g2,g-3)
    c: PointOnObject(g0,g2)
    c: Radius(g1) = 10
    c: Distance(g0,g2) = 50
    c: Coincident(g-3,g0)
    c: Coincident(g3,g2)
    c: PointOnObject(g3,g-2)
    c: DistanceY(g3) = 262
    c: Tangent(g3,g1) = -1.5708
FEATURE [Part::FeaturePython] Placment043  # WARN: FeaturePython — macro-defined, semantics opaque (R4)
  AttacherType = Attacher::AttachEngine3D
  ExposePlacement = true
  MarkerShape = 1
  MarkerSize = 20
  NumElements = 1
  Type = lattice2AttachablePlacement.AttachablePlacement
  isLattice = 1
FEATURE [Part::FeaturePython] Placment044  # WARN: FeaturePython — macro-defined, semantics opaque (R4)
  AttacherType = Attacher::AttachEngine3D
  ExposePlacement = true
  MarkerShape = 1
  MarkerSize = 20
  NumElements = 1
  Placement = pos=(0,0,0) rot=(0,1,0;3.14159rad)
  Type = lattice2AttachablePlacement.AttachablePlacement
  isLattice = 1
FEATURE [Part::FeaturePython] Join019  # WARN: FeaturePython — macro-defined, semantics opaque (R4)
  ExposePlacement = false
  Interleave = false
  Links = -> [Placment043,Placment044]
  MarkerShape = 1
  MarkerSize = 10
  NumElements = 2
  Type = lattice2JoinArrays.JoinArrays
  isLattice = 1
FEATURE [Part::FeaturePython] PolarArray013  # WARN: FeaturePython — macro-defined, semantics opaque (R4)
  Alignment = 0
  AttacherType = Attacher::AttachEngine3D
  CellStart = A1
  Count = 3
  DistributionLaw = 0
  EndInclusive = false
  ExposePlacement = false
  FlipX = false
  FlipZ = false
  GeneratorMode = 0
  MarkerShape = 1
  MarkerSize = 10
  NumElements = 3
  OrientMode = 2
  Radius = 0
  Reverse = false
  SpanEnd = 360
  SpanStart = 0
  Step = 120
  Type = lattice2PolarArray2.PolarArray
  UseArcRadius = false
  UseArcRange = 0
  VSGVersion = 1
  Values = 0.0 | 120.0 | 240.0
  ValuesSource = 2
  isLattice = 1
FEATURE [Part::FeaturePython] Populate076  label="mirrorYZ_and_populate_3_placements"  # WARN: FeaturePython — macro-defined, semantics opaque (R4)
  Copying = 0
  ExposePlacement = false
  MarkerShape = 1
  MarkerSize = 10
  NumElements = 6
  Object = -> PolarArray013
  OutputCompounding = 0
  PlacementsTo = -> Join019
  Referencing = 0
  Type = lattice2PopulateCopies.LatticePopulateCopies
  isLattice = 1
FEATURE [Part::FeaturePython] Populate077  label="Populate Populate Join019 with PolarArray013 with Sketch275"  # WARN: FeaturePython — macro-defined, semantics opaque (R4)
  Copying = 0
  ExposePlacement = false
  MarkerShape = 1
  MarkerSize = 0
  NumElements = 0
  Object = -> Sketch275
  OutputCompounding = 1
  PlacementsTo = -> Populate076
  Referencing = 0
  Type = lattice2PopulateCopies.LatticePopulateCopies
  isLattice = 0
FEATURE [Part::FeaturePython] Connect009  # WARN: FeaturePython — macro-defined, semantics opaque (R4)
  Objects = -> [Populate077]
  Tolerance = 0
FEATURE [PartDesign::SubShapeBinder] Binder153
  BindCopyOnChange = 0
  BindMode = 0
  ClaimChildren = true
  Context = -> Body150 [Binder153.]
  Fuse = false
  MakeFace = true
  OffsetFill = false
  OffsetIntersection = false
  OffsetJoinType = 0
  OffsetOpenResult = false
  PartialLoad = false
  Relative = false
  Support = -> [Connect009]
  _Version = 2
FEATURE [PartDesign::Pad] Pad050
  Direction = (0,0,1)
  Length = 18
  Length2 = 10
  Profile = -> Binder153
  Suppressed = false
  Type = 0
FEATURE [Sketcher::SketchObject] Sketch276
  ExternalGeometry = -> [Sketch275]
  FullyConstrained = false
  sketch-geometry (3):
    g0: Circle CenterX=42.8252 CenterY=228.013 CenterZ=0 NormalX=0 NormalY=0 NormalZ=1 AngleXU=0 Radius=2
    g1: Circle CenterX=123.314 CenterY=128.93 CenterZ=0 NormalX=0 NormalY=0 NormalZ=1 AngleXU=0 Radius=2
    g2: LineSegment StartX=0 StartY=0 StartZ=0 EndX=204.597 EndY=118.124 EndZ=0
  constraints (8):
    c: Coincident(g2,g-1)
    c: Equal(g1,g0)
    c: Diameter(g1) = 4
    c: Distance(g1,g2) = 50
    c: PointOnObject(g-3,g2)
    c: Distance(g1,g-3) = 30
    c: Distance(g0,g-4) = 30
    c: Distance(g0,g-3) = 30
FEATURE [Part::Extrusion] Extrude044
  Base = -> Sketch276
  Dir = (0,0,1)
  DirMode = 2
  FaceMakerClass = Part::FaceMakerBullseye
  LengthFwd = 40
  LengthRev = 0
  Solid = true
  Symmetric = true
FEATURE [Part::FeaturePython] Populate078  label="Populate mirrorYZ_and_populate_3_placements with Extrude044"  # WARN: FeaturePython — macro-defined, semantics opaque (R4)
  Copying = 0
  ExposePlacement = false
  MarkerShape = 1
  MarkerSize = 0
  NumElements = 0
  Object = -> Extrude044
  OutputCompounding = 1
  PlacementsTo = -> Populate076
  Referencing = 0
  Type = lattice2PopulateCopies.LatticePopulateCopies
  isLattice = 0
FEATURE [Part::Cylinder] Cylinder014
  Angle = 360
  AttacherType = Attacher::AttachEngine3D
  FirstAngle = 0
  Height = 30
  Radius = 12
  SecondAngle = 0
FEATURE [Part::Compound] Compound109
  Links = -> [Populate078,Fusion002,Cylinder014]
FEATURE [PartDesign::Boolean] Boolean055
  BaseFeature = -> Pad050
  Group = -> [Compound109]
  Suppressed = false
  Type = 1
  UsePlacement = true
FEATURE [PartDesign::Body] Body150  label="basement_v4_top_amplifier"
  Group = -> [Binder153,Pad050,Boolean055]
  Origin = -> Origin131
  Tip = -> Boolean055
FEATURE [Part::Compound] Compound110
  Links = -> [Populate078,Fusion002,Cylinder014,Populate037]
FEATURE [Sketcher::SketchObject] Sketch277
  AttachmentOffset = pos=(-253,0,0) rot=(0,0,1;0rad)
  AttachmentSupport = -> [YZ_Plane131]
  FullyConstrained = true
  MapMode = 5
  Placement = pos=(0,-253,0) rot=(0.57735,0.57735,0.57735;2.0944rad)
  sketch-geometry (3):
    g0: LineSegment StartX=0 StartY=15 StartZ=0 EndX=0 EndY=0 EndZ=0
    g1: LineSegment StartX=0 StartY=0 StartZ=0 EndX=15 EndY=0 EndZ=0
    g2: LineSegment StartX=15 StartY=0 StartZ=0 EndX=0 EndY=15 EndZ=0
  constraints (8):
    c: PointOnObject(g0,g-2)
    c: Coincident(g0,g-1)
    c: Coincident(g0,g1)
    c: PointOnObject(g1,g-1)
    c: Coincident(g1,g2)
    c: Coincident(g2,g0)
    c: Angle(g2) = 2.35619
    c: DistanceY(g0,g0) = 15
FEATURE [PartDesign::SubtractivePipe] SubtractivePipe001
  AuxilleryCurvelinear = true
  AuxillerySpineTangent = false
  BaseFeature = -> Pad049
  Binormal = (0,0,0)
  Mode = 0
  Profile = -> Sketch277
  Spine = -> Binder152 [Edge14,Edge13,Edge12,Edge11,Edge10,Edge9,Edge8,Edge7,Edge6,Edge5,Edge4,Edge3,Edge2,Edge1,Edge18,Edge17,Edge16,Edge15]
  SpineTangent = false
  Suppressed = false
  Transformation = 0
  Transition = 0
FEATURE [PartDesign::Boolean] Boolean056
  BaseFeature = -> SubtractivePipe001
  Group = -> [Compound110]
  Refine = true
  Suppressed = false
  Type = 1
  UsePlacement = true
FEATURE [PartDesign::Body] Body151  label="basement_v4_top"
  Group = -> [Binder152,Pad049,SubtractivePipe001,Boolean056,Sketch277]
  Origin = -> Origin132
  Tip = -> SubtractivePipe001
FEATURE [Part::FeaturePython] Connect010  # WARN: FeaturePython — macro-defined, semantics opaque (R4)
  Objects = -> [Array003]
  Tolerance = 0
FEATURE [Part::Cylinder] Cylinder015
  Angle = 360
  AttacherType = Attacher::AttachEngine3D
  FirstAngle = 0
  Height = 20
  Radius = 10
  SecondAngle = 0
FEATURE [Part::Compound] Compound106
  Links = -> [Fusion002,Array016,Cylinder015]
FEATURE [PartDesign::Boolean] Boolean053
  BaseFeature = -> Pad047
  Group = -> [Compound106]
  Suppressed = false
  Type = 1
  UsePlacement = true
FEATURE [PartDesign::Body] Body148  label="basement_v4_bottom_amplifier"
  Group = -> [Binder150,Pad047,Boolean053]
  Origin = -> Origin129
  Tip = -> Boolean053
FEATURE [App::DocumentObjectGroup] Group025  label="basement_v4_Group"
  Group = -> [Body148,Body149,Body150,Body151]
FEATURE [Sketcher::SketchObject] Sketch278
  AttachmentOffset = pos=(0,0,0) rot=(0,1,0;1.5708rad)
  AttachmentSupport = -> [Binder145]
  FullyConstrained = true
  MapMode = 7
  Placement = pos=(113.449,65.5,0) rot=(-0.774597,0.447214,0.447214;4.45971rad)
  sketch-geometry (1):
    g0: Circle CenterX=0 CenterY=22 CenterZ=0 NormalX=0 NormalY=0 NormalZ=1 AngleXU=0 Radius=1.7
  constraints (3):
    c: PointOnObject(g0,g-2)
    c: Diameter(g0) = 3.4
    c: DistanceY(g0) = 22
FEATURE [PartDesign::Pocket] Pocket146
  BaseFeature = -> Boolean047
  Direction = (0.866025,0.5,0)
  Length = 5
  Length2 = 5
  Midplane = true
  Profile = -> Sketch278
  ReferenceAxis = -> Sketch278 [N_Axis]
  Suppressed = false
  Type = 1
FEATURE [Part::FeaturePython] Connect011  # WARN: FeaturePython — macro-defined, semantics opaque (R4)
  Objects = -> [Array003]
  Tolerance = 0
FEATURE [Part::Offset2D] Offset2D001
  Fill = false
  Intersection = false
  Join = 0
  Mode = 1
  SelfIntersection = false
  Source = -> Connect011
  Value = -23
FEATURE [Part::Offset2D] Offset2D002
  Fill = false
  Intersection = false
  Join = 0
  Mode = 1
  SelfIntersection = false
  Source = -> Offset2D001
  Value = -5
FEATURE [Part::Face] Face
  FaceMakerClass = Part::FaceMakerBullseye
  Sources = -> [Offset2D001]
FEATURE [Part::Face] Face001
  FaceMakerClass = Part::FaceMakerBullseye
  Sources = -> [Offset2D002]
FEATURE [Part::Cut] Cut001
  Base = -> Face
  Tool = -> Face001
FEATURE [Part::Extrusion] Extrude045
  Base = -> Cut001
  Dir = (0,0,1)
  DirMode = 2
  FaceMakerClass = Part::FaceMakerBullseye
  LengthFwd = 5
  LengthRev = 0
  Solid = false
  Symmetric = false
FEATURE [Part::Compound] Compound066  label="basement_top_plywood_cut1"
  Links = -> [Populate037,Extrude026,Populate043,Extrude045]
FEATURE [PartDesign::Boolean] Boolean023
  BaseFeature = -> Pocket062
  Group = -> [Compound066]
  Refine = true
  Suppressed = false
  Type = 1
  UsePlacement = false
FEATURE [PartDesign::Body] Body006  label="basement_top_plywood"
  Group = -> [Binder005,Pad001,Sketch112,Sketch113,SubtractivePipe,Pocket062,Sketch166,Sketch216,Boolean023,Local_CS019,Local_CS020]
  Origin = -> Origin010
  Tip = -> Boolean023
FEATURE [App::DocumentObjectGroup] Group014  label="basement_top_Group"
  Group = -> [Body006,Body008,Body122,Body105]
FEATURE [App::DocumentObjectGroup] Group016  label="basement_Group"
  Group = -> [Group014,Group015,Link004]
FEATURE [Sketcher::SketchObject] Sketch280
  FullyConstrained = true
  expr: Constraints[0] = <<pillar_placement>>.Placement.Base.y
  sketch-geometry (1):
    g0: LineSegment StartX=-14.3 StartY=384 StartZ=0 EndX=14.3 EndY=384 EndZ=0
  constraints (3):
    c: DistanceY(g0) = 384
    c: DistanceX(g0,g0) = 28.6
    c: Symmetric(g0,g0,g-2)
FEATURE [Sketcher::SketchObject] Sketch279
  ExternalGeometry = -> [Sketch280]
  FullyConstrained = true
  sketch-geometry (4):
    g0: LineSegment StartX=0 StartY=0 StartZ=0 EndX=317.831 EndY=183.5 EndZ=0
    g1: ArcOfCircle CenterX=-67.55 CenterY=-39 CenterZ=0 NormalX=0 NormalY=0 NormalZ=1 AngleXU=0 Radius=445 StartAngle=0.523599 EndAngle=0.976538
    g2: ArcOfCircle CenterX=14.3 CenterY=99.9868 CenterZ=0 NormalX=0 NormalY=0 NormalZ=1 AngleXU=0 Radius=284.013 StartAngle=0.976538 EndAngle=1.5708
    g3: LineSegment StartX=173.317 StartY=335.31 StartZ=0 EndX=181.603 EndY=329.711 EndZ=0
  constraints (10):
    c: Coincident(g0,g-1)
    c: Coincident(g0,g1)
    c: Angle(g0) = 0.523599
    c: Tangent(g2,g-3) = 1.5708
    c: Perpendicular(g1,g0)
    c: Distance(g0) = 367
    c: Radius(g1) = 445
    c: Tangent(g3,g1) = 1.5708
    c: Distance(g3) = 10
    c: Tangent(g3,g2) = 1.5708
FEATURE [Part::Mirroring] Part__Mirroring041  label="Sketch279 (Mirror #38)"
  Base = (0,0,0)
  Normal = (-0.5,0.866025,0)
  Source = -> Sketch279
  expr: .Normal.x = sin(-30 deg)
  expr: .Normal.y = cos(-30 deg)
FEATURE [Part::FeaturePython] Populate079  label="Populate 3_elem_polar_array with Sketch280"  # WARN: FeaturePython — macro-defined, semantics opaque (R4)
  Copying = 0
  ExposePlacement = false
  MarkerShape = 1
  MarkerSize = 0
  NumElements = 0
  Object = -> Sketch280
  OutputCompounding = 1
  PlacementsTo = -> PolarArray006
  Referencing = 1
  Type = lattice2PopulateCopies.LatticePopulateCopies
  isLattice = 0
FEATURE [Part::Compound] Compound111
  Links = -> [Part__Mirroring041,Sketch279]
FEATURE [Part::Mirroring] Part__Mirroring042  label="Compound111 (Mirror #39)"
  Base = (0,0,0)
  Normal = (1,0,0)
  Source = -> Compound111
FEATURE [Part::Compound] Compound112
  Links = -> [Populate079,Part__Mirroring042,Compound111]
FEATURE [Part::FeaturePython] Connect012  # WARN: FeaturePython — macro-defined, semantics opaque (R4)
  Objects = -> [Compound112]
  Tolerance = 0
FEATURE [PartDesign::SubShapeBinder] Binder154
  BindCopyOnChange = 0
  BindMode = 0
  ClaimChildren = true
  Context = -> Body152 [Binder154.]
  Fuse = false
  MakeFace = true
  OffsetFill = false
  OffsetIntersection = false
  OffsetJoinType = 0
  OffsetOpenResult = false
  PartialLoad = false
  Relative = true
  Support = -> [Connect012]
  _Version = 2
FEATURE [PartDesign::FeaturePython] BaseBend057  # WARN: FeaturePython — macro-defined, semantics opaque (R4)
  BendSide = 1
  BendSketch = -> Binder154
  MidPlane = false
  Reverse = false
  Suppressed = false
  length = 1214
  radius = 1
  thickness = 1.5
FEATURE [Part::FeaturePython] PolarArray014  # WARN: FeaturePython — macro-defined, semantics opaque (R4)
  Alignment = 0
  AttacherType = Attacher::AttachEngine3D
  CellStart = A1
  Count = 3
  DistributionLaw = 0
  EndInclusive = false
  ExposePlacement = false
  FlipX = false
  FlipZ = false
  GeneratorMode = 0
  MarkerShape = 1
  MarkerSize = 0
  NumElements = 3
  OrientMode = 3
  Placement = pos=(0,0,0) rot=(0,0,1;1.5708rad)
  Radius = 384
  Reverse = false
  SpanEnd = 360
  SpanStart = 0
  Step = 120
  Type = lattice2PolarArray2.PolarArray
  UseArcRadius = false
  UseArcRange = 0
  VSGVersion = 1
  Values = 0.0 | 120.0 | 240.0
  ValuesSource = 2
  isLattice = 1
  expr: Radius = <<pillar_placement>>.Placement.Base.y
FEATURE [Part::FeaturePython] Populate080  label="Populate PolarArray014 with pillar3_pillar3_dec_corner_common001"  # WARN: FeaturePython — macro-defined, semantics opaque (R4)
  Copying = 0
  ExposePlacement = false
  MarkerShape = 1
  MarkerSize = 0
  NumElements = 0
  Object = -> Link047
  OutputCompounding = 1
  PlacementsTo = -> PolarArray014
  Referencing = 0
  Type = lattice2PopulateCopies.LatticePopulateCopies
  isLattice = 0
FEATURE [Part::Compound] Compound113
  Links = -> [Populate080]
FEATURE [PartDesign::Boolean] Boolean057
  BaseFeature = -> BaseBend057
  Group = -> [Compound113]
  Refine = true
  Suppressed = false
  Type = 1
  UsePlacement = true
FEATURE [PartDesign::CoordinateSystem] Local_CS049
  AttacherType = Attacher::AttachEngine3D
  AttachmentSupport = -> [XY_Plane132]
  MapMode = 5
FEATURE [PartDesign::Body] Body152  label="pillar3_plexiglass_outer"
  Group = -> [Binder154,BaseBend057,Boolean057,Local_CS049]
  Origin = -> Origin133
  Tip = -> Boolean057
FEATURE [PartDesign::CoordinateSystem] Local_CS050  label="hat3_plexiglass_LCS"
  AttacherType = Attacher::AttachEngine3D
  AttachmentSupport = -> [XY_Plane126]
  MapMode = 5
FEATURE [PartDesign::Body] Body146  label="hat3_plexiglass"
  Group = -> [Binder145,BaseBend055,Extend002,Boolean047,Sketch278,Pocket146,Local_CS050]
  Origin = -> Origin127
  Tip = -> Pocket146
FEATURE [App::DocumentObjectGroup] Group013  label="pillar3_hat_Group"
  Group = -> [Body142,Body143,Body146]
FEATURE [Part::Mirroring] Part__Mirroring043  label="Sketch264 (Mirror #40)"
  Base = (0,0,0)
  Normal = (1,0,0)
  Source = -> Sketch264
FEATURE [Part::Compound] Compound114
  Links = -> [Sketch264,Part__Mirroring043]
FEATURE [Part::Extrusion] Extrude038
  Base = -> Compound114
  Dir = (0,0,1)
  DirMode = 2
  FaceMakerClass = Part::FaceMakerBullseye
  LengthFwd = 10
  LengthRev = 0
  Placement = pos=(0,-5,1060) rot=(0,0.707107,0.707107;3.14159rad)
  Solid = true
  Symmetric = false
FEATURE [Part::Compound] Compound100  label="pillar3_pillar3_dec_corner_common"
  Links = -> [Extrude038,Populate064,Populate062,Populate061,Populate068]
FEATURE [Part::Compound] Compound099
  Links = -> [Compound100]
FEATURE [PartDesign::Boolean] Boolean049
  BaseFeature = -> Mirrored020
  Group = -> [Compound099]
  Suppressed = false
  Type = 1
  UsePlacement = true
FEATURE [PartDesign::Pocket] Pocket144
  BaseFeature = -> Boolean049
  Direction = (-1,0,0)
  Length = 5
  Length2 = 5
  Midplane = true
  Profile = -> Sketch268
  ReferenceAxis = -> Sketch268 [N_Axis]
  Suppressed = false
  Type = 1
FEATURE [PartDesign::Body] Body141  label="pillar3"
  Group = -> [Binder141,BaseBend052,Sketch253,Pocket137,Local_CS006,Local_CS007,DatumPlane007,Mirrored020,Local_CS009,Boolean049,Sketch268,Local_CS047,Pocket144]
  Origin = -> Origin122
  Tip = -> Pocket144
FEATURE [App::DocumentObjectGroup] Group012  label="pillar3_Group"
  Group = -> [Body141,Body144,Group013,Body145,Body147,Spreadsheet005]
FEATURE [App::DocumentObjectGroup] Group  label="parts"
  Group = -> [Part007,Body068,Link005,Part010,Body072,Body018,Part019,Body113,Part020,Body121,Body088,Part021,Body126,Body127,Body128,Body129,Group012,Group016,Body,Body001,Group018,Group020,Group021,Group022,Group024]
FEATURE [Sketcher::SketchObject] Sketch281
  FullyConstrained = false
  sketch-geometry (4):
    g0: LineSegment StartX=0 StartY=0 StartZ=0 EndX=311.636 EndY=179.923 EndZ=0
    g1: LineSegment StartX=15 StartY=351.187 StartZ=0 EndX=212.758 EndY=351.187 EndZ=0
    g2: LineSegment StartX=212.758 StartY=351.187 StartZ=0 EndX=311.636 EndY=179.923 EndZ=0
    g3: Circle CenterX=0 CenterY=0 CenterZ=0 NormalX=0 NormalY=0 NormalZ=1 AngleXU=0 Radius=370
  constraints (10):
    c: Coincident(g0,g-1)
    c: Angle(g0) = 0.523599
    c: Horizontal(g1)
    c: Coincident(g1,g2)
    c: Coincident(g2,g0)
    c: Perpendicular(g0,g2)
    c: Equal(g2,g1)
    c: DistanceX(g1) = 15
    c: Coincident(g3,g0)
    c: Diameter(g3) = 740
note: 11 file-system paths scrubbed to <path> (originals preserved in the JSON sidecar)

RESOLVED EXTERNAL PARTS (link-assembly join: the EXTERNAL_REF files above that resolve inside this repo's crawl, each included once):
---- part U-fix.FCStd = doc fcstd_8b42821c5992 ----
FCSTD DOCUMENT  (FreeCAD 1.1R38827 (Git))
Label: U-fix
License: All rights reserved
LicenseURL: http://en.wikipedia.org/wiki/All_rights_reserved
objects: Sketcher::SketchObject×7, TechDraw::DrawViewDimension×4, TechDraw::DrawViewPart×3, PartDesign::SubShapeBinder×2, PartDesign::Pocket×2, PartDesign::FeaturePython×1, PartDesign::Mirrored×1, TechDraw::DrawSVGTemplate×1, Part::Feature×1, PartDesign::Hole×1, PartDesign::Body×1, TechDraw::DrawPage×1, App::DocumentObjectGroup×1
note: 37 computed .brp shape members not serialized (recipe doc carries the construction recipe); baked Part::Feature solids carry a one-line shape summary decoded from their .brp
EXTERNAL_REF file=ugol90degX40mm.FCStd obj=Binder002
EXTERNAL_REF file=wheel50mm.FCStd obj=Populate001

FEATURE [Sketcher::SketchObject] Sketch
  ArcFitTolerance = 0
  AttachmentSupport = -> [XZ_Plane]
  FullyConstrained = true
  MakeInternals = false
  MapMode = 5
  Placement = pos=(0,0,0) rot=(1,0,0;1.5708rad)
  sketch-geometry (5):
    g0: LineSegment StartX=-11.5 StartY=16 StartZ=0 EndX=-11.5 EndY=0 EndZ=0
    g1: LineSegment StartX=-11.5 StartY=0 StartZ=0 EndX=11.5 EndY=0 EndZ=0
    g2: LineSegment StartX=11.5 StartY=0 StartZ=0 EndX=11.5 EndY=16 EndZ=0
    g3: LineSegment [constr] StartX=11.5 StartY=16 StartZ=0 EndX=-11.5 EndY=16 EndZ=0
    g4: GeomPoint [constr] X=0 Y=8 Z=0
  constraints (13):
    c: Coincident(g0,g1)
    c: Coincident(g1,g2)
    c: Coincident(g2,g3)
    c: Coincident(g3,g0)
    c: Horizontal(g1)
    c: Horizontal(g3)
    c: Vertical(g0)
    c: Vertical(g2)
    c: Symmetric(g1,g0,g4)
    c: PointOnObject(g4,g-2)
    c: PointOnObject(g1,g-1)
    c: DistanceX(g1,g1) = 23  'width'
    c: DistanceY(g2) = 16  'height'
FEATURE [PartDesign::FeaturePython] BaseBend  # WARN: FeaturePython — macro-defined, semantics opaque (R4)
  BendSide = 1
  BendSketch = -> Sketch
  MidPlane = true
  Reverse = false
  Suppressed = false
  length = 65
  radius = 2
  thickness = 1
FEATURE [PartDesign::SubShapeBinder] Binder  label="U-fix_vert_holes"
  BindCopyOnChange = 0
  BindMode = 0
  ClaimChildren = false
  Context = -> Body [Binder.]
  Fuse = false
  MakeFace = true
  OffsetFill = false
  OffsetIntersection = false
  OffsetJoinType = 0
  OffsetOpenResult = false
  PartialLoad = false
  Placement = pos=(0,0,0) rot=(0,0,1;1.5708rad)
  Relative = true
  Support = -> [<external ugol90degX40mm.FCStd>#Binder002]
  _Version = 2
  expr: Support = <<ugol90degX40mm>>#<<vert>>._self
FEATURE [PartDesign::Pocket] Pocket
  BaseFeature = -> BaseBend
  Direction = (1,-2e-16,0)
  Length = 5
  Length2 = 5
  Midplane = true
  Profile = -> Binder
  Suppressed = false
  Type = 1
FEATURE [Sketcher::SketchObject] Sketch001
  ArcFitTolerance = 0
  AttachmentOffset = pos=(32.5,16,0) rot=(0,0,1;0rad)
  AttachmentSupport = -> [YZ_Plane]
  FullyConstrained = true
  MakeInternals = false
  MapMode = 5
  Placement = pos=(0,32.5,16) rot=(0.57735,0.57735,0.57735;2.0944rad)
  expr: .AttachmentOffset.Base.x = BaseBend.length / 2
  expr: .AttachmentOffset.Base.y = Sketch.Constraints.height
  sketch-geometry (3):
    g0: ArcOfCircle CenterX=-5 CenterY=-5 CenterZ=0 NormalX=0 NormalY=0 NormalZ=1 AngleXU=0 Radius=5 StartAngle=0 EndAngle=1.5708
    g1: LineSegment StartX=-9e-16 StartY=-5 StartZ=0 EndX=0 EndY=0 EndZ=0
    g2: LineSegment StartX=0 StartY=0 StartZ=0 EndX=-5.00003 EndY=-4.65468e-11 EndZ=0
  constraints (8):
    c: PointOnObject(g0,g-1)
    c: PointOnObject(g0,g-2)
    c: Coincident(g1,g2)
    c: Coincident(g2,g0)
    c: Tangent(g2,g0)
    c: Tangent(g0,g1) = -1.5708
    c: Coincident(g1,g-1)
    c: Diameter(g0) = 10
FEATURE [PartDesign::Pocket] Pocket001
  BaseFeature = -> Pocket
  Direction = (-1,0,0)
  Length = 5
  Length2 = 5
  Midplane = true
  Profile = -> Sketch001
  ReferenceAxis = -> Sketch001 [N_Axis]
  Suppressed = false
  Type = 1
FEATURE [PartDesign::Mirrored] Mirrored
  BaseFeature = -> Pocket001
  MirrorPlane = -> XZ_Plane
  Originals = -> [Pocket001]
  Suppressed = false
  TransformMode = 0
FEATURE [Sketcher::SketchObject] Sketch002  label="holes_bottom"
  ArcFitTolerance = 0
  AttachmentSupport = -> [XY_Plane]
  FullyConstrained = true
  MakeInternals = false
  MapMode = 5
  sketch-geometry (2):
    g0: Circle CenterX=0 CenterY=17.5 CenterZ=0 NormalX=0 NormalY=0 NormalZ=1 AngleXU=0 Radius=2.5
    g1: Circle CenterX=0 CenterY=-17.5 CenterZ=0 NormalX=0 NormalY=0 NormalZ=1 AngleXU=0 Radius=2.5
  constraints (5):
    c: PointOnObject(g0,g-2)
    c: Symmetric(g1,g0,g-1)
    c: Equal(g1,g0)
    c: Diameter(g1) = 5
    c: DistanceY(g1,g0) = 35
FEATURE [TechDraw::DrawSVGTemplate] Template
  Height = 210
  Orientation = 1
  Template = <path>
  Width = 297
FEATURE [Part::Feature] Unfold
  Placement = pos=(0,0,0) rot=(0,0,1;1.5708rad)
  shape: bbox 53 x 50.85 x 1 mm, 16 faces (baked)
FEATURE [Sketcher::SketchObject] Unfold_Sketch_Outline
  ArcFitTolerance = 0
  FullyConstrained = false
  MakeInternals = false
  sketch-geometry (8):
    g0: ArcOfCircle CenterX=21.5 CenterY=-20.427 CenterZ=0 NormalX=0 NormalY=0 NormalZ=1 AngleXU=4e-16 Radius=5 StartAngle=4.71238 EndAngle=6.28319
    g1: LineSegment StartX=26.5 StartY=20.427 StartZ=0 EndX=26.5 EndY=-20.427 EndZ=0
    g2: ArcOfCircle CenterX=21.5 CenterY=20.427 CenterZ=0 NormalX=0 NormalY=0 NormalZ=1 AngleXU=-4e-16 Radius=5 StartAngle=0 EndAngle=1.5708
    g3: LineSegment StartX=21.5 StartY=25.427 StartZ=0 EndX=-21.5 EndY=25.427 EndZ=0
    g4: ArcOfCircle CenterX=-21.5 CenterY=20.427 CenterZ=0 NormalX=0 NormalY=0 NormalZ=1 AngleXU=-3.14159 Radius=5 StartAngle=4.71238 EndAngle=6.28319
    g5: LineSegment StartX=-26.5 StartY=20.427 StartZ=0 EndX=-26.5 EndY=-20.427 EndZ=0
    g6: ArcOfCircle CenterX=-21.5 CenterY=-20.427 CenterZ=0 NormalX=0 NormalY=0 NormalZ=1 AngleXU=3.14159 Radius=5 StartAngle=0 EndAngle=1.5708
    g7: LineSegment StartX=21.5 StartY=-25.427 StartZ=0 EndX=-21.5 EndY=-25.427 EndZ=0
FEATURE [Sketcher::SketchObject] Unfold_Sketch_Internal
  ArcFitTolerance = 0
  FullyConstrained = false
  MakeInternals = false
  sketch-geometry (6):
    g0: Circle CenterX=17.5 CenterY=0 CenterZ=0 NormalX=0 NormalY=0 NormalZ=1 AngleXU=1.5708 Radius=2.75
    g1: Circle CenterX=-17.5 CenterY=0 CenterZ=0 NormalX=0 NormalY=0 NormalZ=1 AngleXU=1.5708 Radius=2.75
    g2: Circle CenterX=20 CenterY=-19.927 CenterZ=0 NormalX=0 NormalY=0 NormalZ=1 AngleXU=2e-16 Radius=1.7
    g3: Circle CenterX=-20 CenterY=-19.927 CenterZ=0 NormalX=0 NormalY=0 NormalZ=1 AngleXU=2e-16 Radius=1.7
    g4: Circle CenterX=20 CenterY=19.927 CenterZ=0 NormalX=0 NormalY=0 NormalZ=-1 AngleXU=-3.14159 Radius=1.7
    g5: Circle CenterX=-20 CenterY=19.927 CenterZ=0 NormalX=0 NormalY=0 NormalZ=-1 AngleXU=-3.14159 Radius=1.7
FEATURE [Sketcher::SketchObject] Unfold_Sketch_bends
  ArcFitTolerance = 0
  FullyConstrained = false
  MakeInternals = false
  sketch-geometry (2):
    g0: LineSegment StartX=-26.5 StartY=10.4635 StartZ=0 EndX=26.5 EndY=10.4635 EndZ=0
    g1: LineSegment StartX=-26.5 StartY=-10.4635 StartZ=0 EndX=26.5 EndY=-10.4635 EndZ=0
FEATURE [Sketcher::SketchObject] Unfold_Sketch
  ArcFitTolerance = 0
  ExternalGeometry = -> [Unfold_Sketch_bends]
  FullyConstrained = false
  MakeInternals = false
  sketch-geometry (18):
    g0: ArcOfCircle CenterX=21.5 CenterY=-20.427 CenterZ=0 NormalX=0 NormalY=0 NormalZ=1 AngleXU=4e-16 Radius=5 StartAngle=4.71238 EndAngle=6.28319
    g1: LineSegment StartX=21.5 StartY=-25.427 StartZ=0 EndX=-21.5 EndY=-25.427 EndZ=0
    g2: ArcOfCircle CenterX=-21.5 CenterY=-20.427 CenterZ=0 NormalX=0 NormalY=0 NormalZ=1 AngleXU=3.14159 Radius=5 StartAngle=0 EndAngle=1.5708
    g3: ArcOfCircle CenterX=-21.5 CenterY=20.427 CenterZ=0 NormalX=0 NormalY=0 NormalZ=1 AngleXU=-3.14159 Radius=5 StartAngle=4.71238 EndAngle=6.28319
    g4: LineSegment StartX=21.5 StartY=25.427 StartZ=0 EndX=-21.5 EndY=25.427 EndZ=0
    g5: ArcOfCircle CenterX=21.5 CenterY=20.427 CenterZ=0 NormalX=0 NormalY=0 NormalZ=1 AngleXU=-4e-16 Radius=5 StartAngle=0 EndAngle=1.5708
    g6: Circle CenterX=-17.5 CenterY=0 CenterZ=0 NormalX=0 NormalY=0 NormalZ=1 AngleXU=1.5708 Radius=2.75
    g7: Circle CenterX=17.5 CenterY=0 CenterZ=0 NormalX=0 NormalY=0 NormalZ=1 AngleXU=1.5708 Radius=2.75
    g8: Circle CenterX=-20 CenterY=19.927 CenterZ=0 NormalX=0 NormalY=0 NormalZ=-1 AngleXU=-3.14159 Radius=1.7
    g9: Circle CenterX=20 CenterY=19.927 CenterZ=0 NormalX=0 NormalY=0 NormalZ=-1 AngleXU=-3.14159 Radius=1.7
    g10: Circle CenterX=-20 CenterY=-19.927 CenterZ=0 NormalX=0 NormalY=0 NormalZ=1 AngleXU=2e-16 Radius=1.7
    g11: Circle CenterX=20 CenterY=-19.927 CenterZ=0 NormalX=0 NormalY=0 NormalZ=1 AngleXU=2e-16 Radius=1.7
    g12: LineSegment StartX=26.5 StartY=20.427 StartZ=0 EndX=26.5 EndY=-20.427 EndZ=0
    g13: LineSegment StartX=-26.5 StartY=20.427 StartZ=0 EndX=-26.5 EndY=-20.427 EndZ=0
    g14: LineSegment StartX=26.5 StartY=-10.4635 StartZ=0 EndX=24.5 EndY=-10.4635 EndZ=0
    g15: LineSegment StartX=26.5 StartY=10.4635 StartZ=0 EndX=24.5 EndY=10.4635 EndZ=0
    g16: LineSegment StartX=-26.5 StartY=10.4635 StartZ=0 EndX=-24.5 EndY=10.4635 EndZ=0
    g17: LineSegment StartX=-26.5 StartY=-10.4635 StartZ=0 EndX=-24.5 EndY=-10.4635 EndZ=0
  constraints (20):
    c: Coincident(g2,g13)
    c: Coincident(g3,g13)
    c: Coincident(g1,g2)
    c: Coincident(g3,g4)
    c: Coincident(g0,g1)
    c: Coincident(g4,g5)
    c: Coincident(g0,g12)
    c: Coincident(g5,g12)
    c: Coincident(g14,g-4)
    c: Coincident(g15,g-3)
    c: Coincident(g16,g-3)
    c: Coincident(g17,g-4)
    c: PointOnObject(g17,g-4)
    c: PointOnObject(g16,g-3)
    c: PointOnObject(g15,g-3)
    c: PointOnObject(g14,g-4)
    c: Equal(g14,g15)
    c: Equal(g15,g16)
    c: Equal(g16,g17)
    c: Distance(g17) = 2
FEATURE [PartDesign::SubShapeBinder] Binder001
  BindCopyOnChange = 0
  BindMode = 0
  ClaimChildren = false
  Context = -> Body [Binder001.]
  Fuse = false
  MakeFace = true
  OffsetFill = false
  OffsetIntersection = false
  OffsetJoinType = 0
  OffsetOpenResult = false
  PartialLoad = false
  Placement = pos=(0,0,0) rot=(0,0,1;0.785398rad)
  Relative = true
  Support = -> [<external wheel50mm.FCStd>#Populate001]
  _Version = 2
  expr: Support = wheel50mm#<<holes_max>>._self
FEATURE [PartDesign::Hole] Hole
  BaseFeature = -> Mirrored
  CustomThreadClearance = 0
  Depth = 25
  DepthType = 0
  Diameter = 5.5
  DrillForDepth = false
  DrillPoint = 1
  DrillPointAngle = 118
  HoleCutCountersinkAngle = 90
  HoleCutCustomValues = false
  HoleCutDepth = 0
  HoleCutDiameter = 6.1
  HoleCutType = 0
  ModelThread = false
  Profile = -> Binder001
  Reversed = true
  Suppressed = false
  Tapered = false
  TaperedAngle = 90
  ThreadClass = 0
  ThreadDepth = 25
  ThreadDepthType = 0
  ThreadDirection = 0
  ThreadFit = 0
  ThreadSize = 0
  ThreadType = 0
  Threaded = false
  UseCustomThreadClearance = false
FEATURE [PartDesign::Body] Body  label="U_fix_material_0.50ansi"
  AllowCompound = false
  Group = -> [Sketch,BaseBend,Binder,Pocket,Sketch001,Pocket001,Mirrored,Sketch002,Hole,Binder001]
  Origin = -> Origin
  Tip = -> Hole
FEATURE [TechDraw::DrawViewPart] View
  CoarseView = false
  Direction = (0,-1,0)
  Focus = 100
  HardHidden = false
  IsoCount = 0
  IsoHidden = false
  IsoVisible = false
  LockPosition = false
  Perspective = false
  Rotation = 0
  ScaleType = 0
  ScrubCount = 0
  SeamHidden = false
  SeamVisible = true
  SmoothHidden = false
  SmoothVisible = true
  Source = -> [Body]
  X = 69.5
  XDirection = (1,0,0)
  Y = 105
  expr: Y = Template.Height / 2
FEATURE [TechDraw::DrawViewPart] View001
  CoarseView = false
  Direction = (1,0,0)
  Focus = 100
  HardHidden = false
  IsoCount = 0
  IsoHidden = false
  IsoVisible = false
  LockPosition = false
  Perspective = false
  Rotation = 0
  ScaleType = 0
  ScrubCount = 0
  SeamHidden = false
  SeamVisible = true
  SmoothHidden = false
  SmoothVisible = true
  Source = -> [Body]
  X = 226.5
  XDirection = (0,1,-1.19209e-07)
  Y = 105
  expr: Y = Template.Height / 2
FEATURE [TechDraw::DrawViewPart] View002
  CoarseView = false
  Direction = (0,0,1)
  Focus = 100
  HardHidden = false
  IsoCount = 0
  IsoHidden = false
  IsoVisible = false
  LockPosition = false
  Perspective = false
  Rotation = 0
  ScaleType = 0
  ScrubCount = 0
  SeamHidden = false
  SeamVisible = true
  SmoothHidden = false
  SmoothVisible = true
  Source = -> [Body]
  X = 148.5
  XDirection = (1,0,0)
  Y = 105
  expr: Y = Template.Height / 2
FEATURE [TechDraw::DrawViewDimension] Dimension004
  AngleOverride = false
  Arbitrary = false
  ArbitraryTolerances = false
  EqualTolerance = true
  ExtensionAngle = 0
  FormatSpec = R%.2w
  FormatSpecOverTolerance = %+.2w
  FormatSpecUnderTolerance = %+.2w
  Inverted = false
  LineAngle = 0
  LockPosition = false
  MeasureType = 1
  OverTolerance = 0
  References2D = -> [View]
  Rotation = 0
  ScaleType = 0
  TheoreticalExact = false
  Type = 4
  UnderTolerance = 0
  X = -23.1952
  Y = -5.48414
FEATURE [TechDraw::DrawViewDimension] Dimension005
  AngleOverride = false
  Arbitrary = false
  ArbitraryTolerances = false
  EqualTolerance = true
  ExtensionAngle = 0
  FormatSpec = R%.2w
  FormatSpecOverTolerance = %+.2w
  FormatSpecUnderTolerance = %+.2w
  Inverted = false
  LineAngle = 0
  LockPosition = false
  MeasureType = 1
  OverTolerance = 0
  References2D = -> [View]
  Rotation = 0
  ScaleType = 0
  TheoreticalExact = false
  Type = 4
  UnderTolerance = 0
  X = 1.1181
  Y = 3.75976
FEATURE [TechDraw::DrawViewDimension] Dimension
  AngleOverride = false
  Arbitrary = false
  ArbitraryTolerances = false
  BoxCorners = (2) [(-11.5,-8,-1e-07),(11.5,8,1e-07)]
  EqualTolerance = true
  ExtensionAngle = 0
  FormatSpec = %.2w
  FormatSpecOverTolerance = %+.2w
  FormatSpecUnderTolerance = %+.2w
  Inverted = false
  LineAngle = 0
  LockPosition = false
  MeasureType = 1
  OverTolerance = 0
  References2D = -> [View]
  Rotation = 0
  ScaleType = 0
  TheoreticalExact = false
  Type = 1
  UnderTolerance = 0
  X = -0.401552
  Y = 25.4578
FEATURE [TechDraw::DrawViewDimension] Dimension006
  AngleOverride = false
  Arbitrary = false
  ArbitraryTolerances = false
  BoxCorners = (2) [(-11.5,-8,-1e-07),(11.5,8,1e-07)]
  EqualTolerance = true
  ExtensionAngle = 0
  FormatSpec = %.2w
  FormatSpecOverTolerance = %+.2w
  FormatSpecUnderTolerance = %+.2w
  Inverted = false
  LineAngle = 0
  LockPosition = false
  MeasureType = 1
  OverTolerance = 0
  References2D = -> [View]
  Rotation = 0
  ScaleType = 0
  TheoreticalExact = false
  Type = 2
  UnderTolerance = 0
  X = 18.6275
  Y = 2.60039
FEATURE [TechDraw::DrawPage] Page
  KeepUpdated = true
  NextBalloonIndex = 1
  ProjectionType = 0
  Template = -> Template
  Views = -> [View,View001,View002,Dimension004,Dimension005,Dimension,Dimension006]
FEATURE [App::DocumentObjectGroup] Group  label="unfold_Group"
  Group = -> [Page,Unfold,Unfold_Sketch,Unfold_Sketch_Outline,Unfold_Sketch_Internal,Unfold_Sketch_bends]
note: 1 file-system path scrubbed to <path> (originals preserved in the JSON sidecar)
---- part UET-VAS-060A20_12V_IP20.FCStd = doc fcstd_68e2274b13cf ----
FCSTD DOCUMENT  (FreeCAD 1.1R38827 (Git))
Label: UET-VAS-060A20_12V_IP20
License: All rights reserved
LicenseURL: http://en.wikipedia.org/wiki/All_rights_reserved
objects: PartDesign::AdditiveBox×1, PartDesign::Body×1, Sketcher::SketchObject×1
note: 6 computed .brp shape members not serialized (recipe doc carries the construction recipe); baked Part::Feature solids carry a one-line shape summary decoded from their .brp

FEATURE [PartDesign::AdditiveBox] Box
  AttacherType = Attacher::AttachEngine3D
  AttachmentOffset = pos=(-20.15,-80,0) rot=(0,0,1;0rad)
  AttachmentSupport = -> [XY_Plane]
  Height = 35.5
  Length = 40.3
  MapMode = 5
  Placement = pos=(-20.15,-80,0) rot=(0,0,1;0rad)
  Suppressed = false
  Width = 160
  expr: .AttachmentOffset.Base.x = -Length / 2
  expr: .AttachmentOffset.Base.y = -Width / 2
FEATURE [PartDesign::Body] Body
  AllowCompound = false
  Group = -> [Box]
  Origin = -> Origin
  Tip = -> Box
FEATURE [Sketcher::SketchObject] Sketch001  label="holes"
  ArcFitTolerance = 0
  FullyConstrained = true
  MakeInternals = false
  sketch-geometry (2):
    g0: Circle CenterX=13.2 CenterY=-75.0683 CenterZ=0 NormalX=0 NormalY=0 NormalZ=1 AngleXU=0 Radius=1.7
    g1: Circle CenterX=-13.2 CenterY=75.0683 CenterZ=0 NormalX=0 NormalY=0 NormalZ=1 AngleXU=0 Radius=1.7
  constraints (5):
    c: Symmetric(g1,g0,g-1)
    c: Distance(g0,g1) = 152.44
    c: Equal(g0,g1)
    c: Diameter(g0) = 3.4
    c: DistanceX(g1) = -13.2
---- part ULY-P91-20W.FCStd = doc fcstd_bf5f0575c407 ----
FCSTD DOCUMENT  (FreeCAD 1.1R38827 (Git))
Label: ULY-P91-20W
License: All rights reserved
LicenseURL: http://en.wikipedia.org/wiki/All_rights_reserved
objects: Sketcher::SketchObject×7, PartDesign::Pad×4, PartDesign::SubShapeBinder×1, PartDesign::Body×1
note: 28 computed .brp shape members not serialized (recipe doc carries the construction recipe); baked Part::Feature solids carry a one-line shape summary decoded from their .brp

FEATURE [Sketcher::SketchObject] Sketch001  label="holes"
  ArcFitTolerance = 0
  FullyConstrained = true
  MakeInternals = false
  sketch-geometry (6):
    g0: Circle [constr] CenterX=0 CenterY=-1135 CenterZ=0 NormalX=0 NormalY=0 NormalZ=1 AngleXU=0 Radius=1.8
    g1: Circle CenterX=12.5 CenterY=0 CenterZ=0 NormalX=0 NormalY=0 NormalZ=1 AngleXU=0 Radius=1.8
    g2: ArcOfCircle CenterX=0 CenterY=-1132 CenterZ=0 NormalX=0 NormalY=0 NormalZ=1 AngleXU=0 Radius=1.8 StartAngle=4.48e-14 EndAngle=3.14159
    g3: ArcOfCircle CenterX=0 CenterY=-1140 CenterZ=0 NormalX=0 NormalY=0 NormalZ=1 AngleXU=0 Radius=1.8 StartAngle=3.14159 EndAngle=6.28319
    g4: LineSegment StartX=-1.8 StartY=-1132 StartZ=0 EndX=-1.8 EndY=-1140 EndZ=0
    g5: LineSegment StartX=1.8 StartY=-1140 StartZ=0 EndX=1.8 EndY=-1132 EndZ=0
  constraints (16):
    c: DistanceX(g1) = 12.5
    c: Equal(g0,g1)
    c: Diameter(g0) = 3.6
    c: PointOnObject(g1,g-1)
    c: PointOnObject(g0,g-2)
    c: DistanceY(g0) = -1135
    c: Tangent(g2,g4) = -1.5708
    c: Tangent(g4,g3) = -1.5708
    c: Tangent(g3,g5) = -1.5708
    c: Tangent(g5,g2) = -1.5708
    c: Equal(g2,g3)
    c: PointOnObject(g2,g-2)
    c: PointOnObject(g3,g-2)
    c: DistanceY(g0,g2) = 3
    c: DistanceY(g3,g0) = 5
    c: Equal(g2,g0)
FEATURE [Sketcher::SketchObject] Sketch002  label="body"
  ArcFitTolerance = 0
  ExternalGeometry = -> [Sketch001]
  FullyConstrained = true
  MakeInternals = false
  sketch-geometry (4):
    g0: LineSegment StartX=-9 StartY=0 StartZ=0 EndX=31.6 EndY=0 EndZ=0
    g1: LineSegment StartX=31.6 StartY=0 StartZ=0 EndX=31.6 EndY=42.6 EndZ=0
    g2: LineSegment StartX=31.6 StartY=42.6 StartZ=0 EndX=-9 EndY=42.6 EndZ=0
    g3: LineSegment StartX=-9 StartY=42.6 StartZ=0 EndX=-9 EndY=0 EndZ=0
  constraints (12):
    c: Coincident(g0,g1)
    c: Coincident(g1,g2)
    c: Coincident(g2,g3)
    c: Coincident(g3,g0)
    c: Horizontal(g0)
    c: Horizontal(g2)
    c: Vertical(g1)
    c: Vertical(g3)
    c: DistanceX(g0,g0) = 40.6
    c: DistanceY(g1,g1) = 42.6
    c: PointOnObject(g0,g-1)
    c: DistanceX(g0) = 31.6
FEATURE [Sketcher::SketchObject] Sketch
  ArcFitTolerance = 0
  AttachmentOffset = pos=(11.1,0,0) rot=(0,0,1;3.14159rad)
  AttachmentSupport = -> [XY_Plane]
  FullyConstrained = true
  MakeInternals = false
  MapMode = 5
  Placement = pos=(11.1,0,0) rot=(0,0,1;3.14159rad)
  sketch-geometry (5):
    g0: ArcOfCircle CenterX=0 CenterY=4 CenterZ=0 NormalX=0 NormalY=0 NormalZ=1 AngleXU=0 Radius=4.5 StartAngle=2.68873e-11 EndAngle=3.14159
    g1: Circle CenterX=0 CenterY=4 CenterZ=0 NormalX=0 NormalY=0 NormalZ=1 AngleXU=0 Radius=1.8
    g2: LineSegment StartX=-4.5 StartY=4 StartZ=0 EndX=-4.5 EndY=0 EndZ=0
    g3: LineSegment StartX=-4.5 StartY=0 StartZ=0 EndX=4.5 EndY=0 EndZ=0
    g4: LineSegment StartX=4.5 StartY=0 StartZ=0 EndX=4.5 EndY=4 EndZ=0
  constraints (13):
    c: PointOnObject(g0,g-2)
    c: Coincident(g1,g0)
    c: Tangent(g0,g2) = -1.5708
    c: Coincident(g2,g3)
    c: PointOnObject(g3,g-1)
    c: Horizontal(g3)
    c: Coincident(g3,g4)
    c: Vertical(g4)
    c: Tangent(g4,g0) = -1.5708
    c: Vertical(g2)
    c: Diameter(g0) = 9
    c: Diameter(g1) = 3.6
    c: DistanceY(g0) = 4
FEATURE [Sketcher::SketchObject] Sketch003
  ArcFitTolerance = 0
  AttachmentSupport = -> [XY_Plane]
  FullyConstrained = true
  MakeInternals = false
  MapMode = 5
  sketch-geometry (5):
    g0: LineSegment StartX=-6.55 StartY=-1114 StartZ=0 EndX=-6.55 EndY=0 EndZ=0
    g1: LineSegment StartX=-6.55 StartY=0 StartZ=0 EndX=6.55 EndY=0 EndZ=0
    g2: LineSegment StartX=6.55 StartY=0 StartZ=0 EndX=6.55 EndY=-1114 EndZ=0
    g3: LineSegment StartX=6.55 StartY=-1114 StartZ=0 EndX=-6.55 EndY=-1114 EndZ=0
    g4: GeomPoint [constr] X=0 Y=-557 Z=0
  constraints (13):
    c: Coincident(g0,g1)
    c: Coincident(g1,g2)
    c: Coincident(g2,g3)
    c: Coincident(g3,g0)
    c: Horizontal(g1)
    c: Horizontal(g3)
    c: Vertical(g0)
    c: Vertical(g2)
    c: Symmetric(g1,g0,g4)
    c: PointOnObject(g4,g-2)
    c: PointOnObject(g1,g-1)
    c: DistanceX(g1,g1) = 13.1
    c: DistanceY(g2,g2) = 1114
FEATURE [PartDesign::SubShapeBinder] Binder
  BindCopyOnChange = 0
  BindMode = 0
  ClaimChildren = true
  Context = -> Body [Binder.]
  Fuse = false
  MakeFace = true
  OffsetFill = false
  OffsetIntersection = false
  OffsetJoinType = 0
  OffsetOpenResult = false
  PartialLoad = false
  Relative = false
  Support = -> [Sketch002]
  _Version = 2
FEATURE [PartDesign::Pad] Pad002
  Direction = (0,0,1)
  Length = 16.3
  Length2 = 10
  Profile = -> Binder
  Suppressed = false
  Type = 0
FEATURE [PartDesign::Pad] Pad
  BaseFeature = -> Pad002
  Direction = (0,0,1)
  Length = 2
  Length2 = 10
  Profile = -> Sketch
  ReferenceAxis = -> Sketch [N_Axis]
  Suppressed = false
  Type = 0
FEATURE [PartDesign::Pad] Pad001
  BaseFeature = -> Pad
  Direction = (0,0,1)
  Length = 7.3
  Length2 = 10
  Profile = -> Sketch003
  ReferenceAxis = -> Sketch003 [N_Axis]
  Suppressed = false
  Type = 0
FEATURE [Sketcher::SketchObject] Sketch004
  ArcFitTolerance = 0
  AttachmentSupport = -> [XY_Plane]
  ExternalGeometry = -> [Sketch003]
  FullyConstrained = true
  MakeInternals = false
  MapMode = 5
  sketch-geometry (5):
    g0: LineSegment StartX=-7.5 StartY=-1134 StartZ=0 EndX=-7.5 EndY=-1114 EndZ=0
    g1: LineSegment StartX=-7.5 StartY=-1114 StartZ=0 EndX=7.5 EndY=-1114 EndZ=0
    g2: LineSegment StartX=7.5 StartY=-1114 StartZ=0 EndX=7.5 EndY=-1134 EndZ=0
    g3: LineSegment StartX=7.5 StartY=-1134 StartZ=0 EndX=-7.5 EndY=-1134 EndZ=0
    g4: GeomPoint [constr] X=0 Y=-1124 Z=0
  constraints (13):
    c: Coincident(g0,g1)
    c: Coincident(g1,g2)
    c: Coincident(g2,g3)
    c: Coincident(g3,g0)
    c: Horizontal(g1)
    c: Horizontal(g3)
    c: Vertical(g0)
    c: Vertical(g2)
    c: Symmetric(g1,g0,g4)
    c: PointOnObject(g4,g-2)
    c: PointOnObject(g-3,g1)
    c: DistanceX(g1,g1) = 15
    c: DistanceY(g2,g2) = 20
FEATURE [PartDesign::Pad] Pad003
  BaseFeature = -> Pad001
  Direction = (0,0,1)
  Length = 8.3
  Length2 = 1
  Profile = -> Sketch004
  ReferenceAxis = -> Sketch004 [N_Axis]
  Suppressed = false
  Type = 4
FEATURE [Sketcher::SketchObject] Sketch005  label="driver_slice_sketch"
  ArcFitTolerance = 0
  AttachmentSupport = -> [XZ_Plane]
  FullyConstrained = true
  MakeInternals = false
  MapMode = 5
  Placement = pos=(0,0,0) rot=(1,0,0;1.5708rad)
  sketch-geometry (4):
    g0: LineSegment StartX=-9.7 StartY=-1 StartZ=0 EndX=30.9 EndY=-1 EndZ=0
    g1: LineSegment StartX=30.9 StartY=-1 StartZ=0 EndX=30.9 EndY=15 EndZ=0
    g2: LineSegment StartX=30.9 StartY=15 StartZ=0 EndX=-9.7 EndY=15 EndZ=0
    g3: LineSegment StartX=-9.7 StartY=15 StartZ=0 EndX=-9.7 EndY=-1 EndZ=0
  constraints (12):
    c: Coincident(g0,g1)
    c: Coincident(g1,g2)
    c: Coincident(g2,g3)
    c: Coincident(g3,g0)
    c: Horizontal(g0)
    c: Horizontal(g2)
    c: Vertical(g1)
    c: Vertical(g3)
    c: DistanceY(g0) = -1
    c: DistanceY(g1) = 15
    c: DistanceX(g0) = 30.9
    c: DistanceX(g2,g2) = 40.6
FEATURE [Sketcher::SketchObject] Sketch006  label="led_slice_sketch"
  ArcFitTolerance = 0
  AttachmentSupport = -> [XZ_Plane]
  FullyConstrained = true
  MakeInternals = false
  MapMode = 5
  Placement = pos=(0,0,0) rot=(1,0,0;1.5708rad)
  sketch-geometry (5):
    g0: LineSegment StartX=-6.55 StartY=7.3 StartZ=0 EndX=-6.55 EndY=0 EndZ=0
    g1: LineSegment StartX=-6.55 StartY=0 StartZ=0 EndX=6.55 EndY=0 EndZ=0
    g2: LineSegment StartX=6.55 StartY=0 StartZ=0 EndX=6.55 EndY=7.3 EndZ=0
    g3: LineSegment StartX=6.55 StartY=7.3 StartZ=0 EndX=-6.55 EndY=7.3 EndZ=0
    g4: GeomPoint [constr] X=0 Y=3.65 Z=0
  constraints (13):
    c: Coincident(g0,g1)
    c: Coincident(g1,g2)
    c: Coincident(g2,g3)
    c: Coincident(g3,g0)
    c: Horizontal(g1)
    c: Horizontal(g3)
    c: Vertical(g0)
    c: Vertical(g2)
    c: Symmetric(g1,g0,g4)
    c: PointOnObject(g4,g-2)
    c: PointOnObject(g1,g-1)
    c: DistanceX(g1,g1) = 13.1
    c: DistanceY(g2,g2) = 7.3
FEATURE [PartDesign::Body] Body
  AllowCompound = false
  Group = -> [Sketch,Pad002,Pad,Sketch003,Pad001,Binder,Sketch004,Pad003,Sketch005,Sketch006]
  Origin = -> Origin
  Tip = -> Pad003
---- part ULZ-P02-14W.FCStd = doc fcstd_d946428e1785 ----
FCSTD DOCUMENT  (FreeCAD 1.1R38827 (Git))
Label: ULZ-P02-14W
License: All rights reserved
LicenseURL: http://en.wikipedia.org/wiki/All_rights_reserved
objects: Sketcher::SketchObject×4, Part::FeaturePython×4, App::DocumentObjectGroup×3, Path::FeaturePython×3, App::FeaturePython×1, Part::Part2DObjectPython×1, PartDesign::SubShapeBinder×1, PartDesign::Pad×1, PartDesign::CoordinateSystem×1, PartDesign::Body×1
note: 20 computed .brp shape members not serialized (recipe doc carries the construction recipe); baked Part::Feature solids carry a one-line shape summary decoded from their .brp

FEATURE [Sketcher::SketchObject] Sketch  label="holes"
  ArcFitTolerance = 0
  FullyConstrained = true
  MakeInternals = false
  sketch-geometry (3):
    g0: Circle CenterX=-4.15 CenterY=445 CenterZ=0 NormalX=0 NormalY=0 NormalZ=1 AngleXU=0 Radius=1.6
    g1: Circle CenterX=4.15 CenterY=-445 CenterZ=0 NormalX=0 NormalY=0 NormalZ=1 AngleXU=0 Radius=1.6
    g2: GeomPoint [constr] X=-9.05 Y=0 Z=0
  constraints (8):
    c: Symmetric(g1,g0,g-1)
    c: Distance(g0,g1) = 890.039
    c: PointOnObject(g2,g-1)
    c: DistanceX(g2,g0) = 4.9
    c: DistanceX(g2) = -9.05
    c: DistanceY(g1,g0) = 890
    c: Equal(g1,g0)
    c: Diameter(g1) = 3.2
FEATURE [App::FeaturePython] SetupSheet  # Path/CAM operation (typed FeaturePython)
  ClearanceHeightExpression = OpStockZMax+SetupSheet.ClearanceHeightOffset
  ClearanceHeightOffset = 5
  CoolantMode = 0
  CoolantModes = None | Flood | Mist
  FinalDepthExpression = -0.1 mm
  HorizRapid = 0
  ProfileDirection = 1
  ProfileSide = 0
  ProfileUseComp = true
  ProfileprocessCircles = true
  ProfileprocessHoles = true
  ProfileprocessPerimeter = true
  SafeHeightExpression = OpStockZMax+SetupSheet.SafeHeightOffset
  SafeHeightOffset = 3
  StartDepthExpression = 3 mm
  StepDownExpression = 4 mm
  VertRapid = 0
FEATURE [Part::Part2DObjectPython] Clone2D  label="Model-Sketch"  # Draft 2D object (typed FeaturePython)
  Fuse = false
  Objects = -> [Sketch]
  PathResource = Model
  Placement = pos=(-5.75,446.581,0) rot=(0,0,1;0rad)
  Scale = (1,1,1)
FEATURE [App::DocumentObjectGroup] Model
  Group = -> [Clone2D]
FEATURE [Part::FeaturePython] ToolBit  label="3.175mm Endmill"  # Path/CAM toolbit (typed FeaturePython)
  BitPropertyNames = Chipload | CuttingEdgeHeight | Diameter | Flutes | Length | Material | ShankDiameter | SpindleDirection
  BitShape = <path>
  Chipload = 0
  CuttingEdgeHeight = 30
  Diameter = 3.175
  Flutes = 0
  Length = 10
  Material = 0
  ShankDiameter = 3
  ShapeName = endmill
  SpindleDirection = 0
FEATURE [Path::FeaturePython] __175mm_Endmill  label="3.175mm Endmill001"  # Path/CAM operation (typed FeaturePython)
  HorizFeed = 33.3333
  HorizRapid = 0
  SpindleDir = 0
  SpindleSpeed = 18000
  Tool = -> ToolBit
  ToolNumber = 1
  VertFeed = 8.33333
  VertRapid = 0
  expr: HorizRapid = SetupSheet.HorizRapid
  expr: VertRapid = SetupSheet.VertRapid
FEATURE [App::DocumentObjectGroup] Tools
  Group = -> [__175mm_Endmill]
FEATURE [Part::FeaturePython] Stock  # WARN: FeaturePython — macro-defined, semantics opaque (R4)
  Base = -> Model
  ExtXneg = 1
  ExtXpos = 1
  ExtYneg = 1
  ExtYpos = 1
  ExtZneg = 0
  ExtZpos = 1
  Placement = pos=(-5.89217,-448.284,0) rot=(0,0,1;0rad)
  StockType = FromBase
FEATURE [Path::FeaturePython] Profile  # Path/CAM operation (typed FeaturePython)
  Active = true
  AreaParams:
    Tolerance = 1e-07
    FitArcs = True
    Simplify = False
    CleanDistance = 0.0
    Accuracy = 0.01
    Unit = 1.0
    MinArcPoints = 4
    MaxArcPoints = 100
    ClipperScale = 10000000.0
    Fill = 0
    Coplanar = 0
    Reorient = True
    Outline = False
    Explode = False
    OpenMode = 0
    Deflection = 0.01
    SubjectFill = 0
    ClipFill = 0
    Offset = -1.5875
    ExtraPass = 0
    Stepover = 0.0
    LastStepover = 0.0
    JoinType = 0
    EndType = 0
    MiterLimit = 2.0
    RoundPrecision = 0.0
    PocketMode = 0
    ToolRadius = 1.0
    PocketExtraOffset = 0.0
    PocketStepover = 0.0
    PocketLastStepover = 0.0
    FromCenter = False
    Angle = 45.0
    AngleShift = 0.0
    Shift = 0.0
    Thicken = False
    SectionCount = -1
    Stepdown = 1.0
    SectionOffset = 0.0
    SectionTolerance = 1e-06
    SectionMode = 2
    Project = False
  ClearanceHeight = 6
  CoolantMode = 0
  CycleTime = 00:00:57
  Direction = 1
  FinalDepth = -0.1
  HandleMultipleFeatures = 0
  JoinType = 0
  MiterLimit = 0.1
  OffsetExtra = 0
  OpFinalDepth = 0
  OpStartDepth = 1
  OpStockZMax = 1
  OpStockZMin = 0
  OpToolDiameter = 3.175
  PathParams = {'orientation': 1, 'feedrate': 33.333333333333336, 'feedrate_v': 8.333333333333334, 'verbose': True, 'resume_height': 4.0, 'retraction': 6.0, 'return_end': True, 'preamble': False}
  SafeHeight = 4
  Side = 1
  SplitArcs = false
  StartDepth = 3
  StartPoint = (0,0,0)
  StepDown = 4
  ToolController = -> __175mm_Endmill
  UseComp = true
  UseStartPoint = false
  processCircles = true
  processHoles = true
  processPerimeter = true
  expr: ClearanceHeight = OpStockZMax + SetupSheet.ClearanceHeightOffset
  expr: FinalDepth = -0.1 mm
  expr: SafeHeight = OpStockZMax + SetupSheet.SafeHeightOffset
  expr: StartDepth = 3 mm
  expr: StepDown = 4 mm
FEATURE [App::DocumentObjectGroup] Operations
  Group = -> [Profile]
FEATURE [Path::FeaturePython] Job  # Path/CAM operation (typed FeaturePython)
  CycleTime = 00:00:57
  Fixtures = G54
  GeometryTolerance = 0.01
  JobType = 0
  LastPostProcessDate = 2023-12-11 14:23:56.391449
  LastPostProcessOutput = <userpath>/2CAF-B51C/Job-0.tap
  Model = -> Model
  Operations = -> Operations
  OrderOutputBy = 2
  PostProcessor = 3
  PostProcessorOutputFile = %j.tap
  SetupSheet = -> SetupSheet
  SplitOutput = true
  Stock = -> Stock
  Tools = -> Tools
FEATURE [Part::FeaturePython] BoundBox  label="BoundBox of Model-Sketch"  # WARN: FeaturePython — macro-defined, semantics opaque (R4)
  Center = (-5.75,446.581,0)
  CompoundTraversal = 0
  OrientMode = 0
  Padding = 0
  Precision = false
  ScaleFactor = 1
  ShapeLink = -> Clone2D
  Size = (11.5,893.177,0)
FEATURE [Sketcher::SketchObject] Sketch001
  ArcFitTolerance = 0
  FullyConstrained = true
  MakeInternals = false
  Placement = pos=(0,0,0) rot=(1,0,0;1.5708rad)
  sketch-geometry (7):
    g0: LineSegment StartX=-7.3 StartY=1.25 StartZ=0 EndX=7.3 EndY=1.25 EndZ=0
    g1: GeomPoint [constr] X=0 Y=9.25 Z=0
    g2: ArcOfEllipse CenterX=5.1e-15 CenterY=1.25 CenterZ=0 NormalX=0 NormalY=0 NormalZ=1 MajorRadius=8 MinorRadius=7.3 AngleXU=-1.5708 StartAngle=1.5708 EndAngle=4.71239
    g3: LineSegment [constr] StartX=1e-14 StartY=-6.75 StartZ=0 EndX=0 EndY=9.25 EndZ=0
    g4: LineSegment [constr] StartX=7.3 StartY=1.25 StartZ=0 EndX=-7.3 EndY=1.25 EndZ=0
    g5: GeomPoint [constr] X=7.7e-15 Y=-2.02261 Z=0
    g6: GeomPoint [constr] X=3e-15 Y=4.52261 Z=0
  constraints (9):
    c: DistanceX(g0,g0) = 14.6
    c: PointOnObject(g1,g-2)
    c: InternalAlignment(g3-g6 -> g2) x4
    c: Coincident(g3,g1)
    c: Perpendicular(g2,g0) = 4.71239
    c: Perpendicular(g2,g0) = 1.5708
    c: Horizontal(g0)
    c: DistanceY(g2,g1) = 8
    c: DistanceY(g-1,g2) = 1.25
FEATURE [Sketcher::SketchObject] Sketch002
  ArcFitTolerance = 0
  FullyConstrained = true
  MakeInternals = false
  Placement = pos=(0,0,0) rot=(1,0,0;1.5708rad)
  sketch-geometry (8):
    g0: LineSegment StartX=-9 StartY=-5e-16 StartZ=0 EndX=9 EndY=-5e-16 EndZ=0
    g1: LineSegment [constr] StartX=-9 StartY=-5e-16 StartZ=0 EndX=0 EndY=11 EndZ=0
    g2: LineSegment [constr] StartX=7e-16 StartY=11 StartZ=0 EndX=9 EndY=0 EndZ=0
    g3: ArcOfEllipse CenterX=0 CenterY=0 CenterZ=0 NormalX=0 NormalY=0 NormalZ=1 MajorRadius=11 MinorRadius=9 AngleXU=1.5708 StartAngle=4.71239 EndAngle=7.85398
    g4: LineSegment [constr] StartX=7e-16 StartY=11 StartZ=0 EndX=-7e-16 EndY=-11 EndZ=0
    g5: LineSegment [constr] StartX=-9 StartY=6e-16 StartZ=0 EndX=9 EndY=-6e-16 EndZ=0
    g6: GeomPoint [constr] X=7e-16 Y=6.32456 Z=0
    g7: GeomPoint [constr] X=-4e-16 Y=-6.32456 Z=0
  constraints (12):
    c: DistanceX(g0,g0) = 18
    c: Coincident(g0,g1)
    c: Coincident(g1,g2)
    c: Coincident(g2,g0)
    c: Distance(g1,g0) = 11
    c: InternalAlignment(g4-g7 -> g3) x4
    c: Perpendicular(g3,g0) = 1.5708
    c: Equal(g1,g2)
    c: Horizontal(g0)
    c: Coincident(g3,g0)
    c: Coincident(g4,g1)
    c: Coincident(g3,g-1)
FEATURE [PartDesign::SubShapeBinder] Binder
  BindCopyOnChange = 0
  BindMode = 0
  ClaimChildren = true
  Context = -> Body [Binder.]
  Fuse = false
  MakeFace = true
  OffsetFill = false
  OffsetIntersection = false
  OffsetJoinType = 0
  OffsetOpenResult = false
  PartialLoad = false
  Relative = true
  Support = -> [Sketch001]
  _Version = 2
FEATURE [PartDesign::Pad] Pad
  Direction = (0,1,0)
  Length = 820
  Length2 = 10
  Midplane = true
  Profile = -> Binder
  Suppressed = false
  Type = 0
FEATURE [PartDesign::CoordinateSystem] Local_CS
  AttacherType = Attacher::AttachEngine3D
  AttachmentSupport = -> [XY_Plane]
  MapMode = 5
FEATURE [PartDesign::Body] Body
  AllowCompound = false
  Group = -> [Binder,Pad,Local_CS]
  Origin = -> Origin
  Tip = -> Pad
FEATURE [Sketcher::SketchObject] Sketch003
  ArcFitTolerance = 0
  FullyConstrained = true
  MakeInternals = false
  Placement = pos=(0,416,0) rot=(0,0,1;0rad)
  sketch-geometry (8):
    g0: LineSegment StartX=-9 StartY=29.05 StartZ=0 EndX=-9 EndY=0 EndZ=0
    g1: LineSegment StartX=-9 StartY=0 StartZ=0 EndX=9 EndY=0 EndZ=0
    g2: LineSegment StartX=9 StartY=0 StartZ=0 EndX=9 EndY=21.4 EndZ=0
    g3: LineSegment StartX=9 StartY=21.4 StartZ=0 EndX=0.256748 EndY=32.3031 EndZ=0
    g4: ArcOfCircle CenterX=-3.8 CenterY=29.05 CenterZ=0 NormalX=0 NormalY=0 NormalZ=1 AngleXU=0 Radius=5.2 StartAngle=0.675901 EndAngle=3.14159
    g5: GeomPoint [constr] X=-9 Y=43.8466 Z=0
    g6: LineSegment [constr] StartX=0 StartY=34.25 StartZ=0 EndX=-3.8 EndY=34.25 EndZ=0
    g7: Circle CenterX=-3.8 CenterY=29.05 CenterZ=0 NormalX=0 NormalY=0 NormalZ=1 AngleXU=0 Radius=2
  constraints (20):
    c: Vertical(g0)
    c: Coincident(g0,g1)
    c: PointOnObject(g1,g-1)
    c: Coincident(g1,g2)
    c: Vertical(g2)
    c: Coincident(g2,g3)
    c: Symmetric(g0,g1,g-2)
    c: PointOnObject(g5,g0)
    c: PointOnObject(g5,g3)
    c: Tangent(g0,g4) = -1.5708
    c: Tangent(g3,g4) = -1.5708
    c: PointOnObject(g6,g-2)
    c: Tangent(g6,g4) = -1.5708
    c: Horizontal(g6)
    c: DistanceY(g6) = 34.25
    c: DistanceX(g0,g1) = 18
    c: DistanceY(g2,g2) = 21.4
    c: Radius(g4) = 5.2
    c: Coincident(g7,g4)
    c: Diameter(g7) = 4
FEATURE [Part::FeaturePython] Array  # Draft array (typed FeaturePython)
  Angle = 360
  ArrayType = 1
  Axis = (0,0,1)
  Base = -> Sketch003
  Center = (0,0,0)
  Count = 2
  Fuse = true
  IntervalAxis = (0,0,0)
  IntervalX = (50,0,0)
  IntervalY = (0,50,0)
  IntervalZ = (0,0,50)
  NumberCircles = 3
  NumberPolar = 2
  NumberX = 2
  NumberY = 2
  NumberZ = 1
  RadialDistance = 50
  Symmetry = 1
  TangentialDistance = 25
note: 1 file-system path scrubbed to <path> (originals preserved in the JSON sidecar)
---- part basin_big.FCStd = doc fcstd_3c131922ee46 ----
FCSTD DOCUMENT  (FreeCAD 1.1R38827 (Git))
Label: basin_big
License: All rights reserved
LicenseURL: http://en.wikipedia.org/wiki/All_rights_reserved
objects: Part::FeaturePython×4, Sketcher::SketchObject×2, PartDesign::Revolution×2, App::AnnotationLabel×2, PartDesign::Mirrored×1, PartDesign::CoordinateSystem×1, PartDesign::Body×1, Spreadsheet::Sheet×1, App::DocumentObjectGroup×1
note: 18 computed .brp shape members not serialized (recipe doc carries the construction recipe); baked Part::Feature solids carry a one-line shape summary decoded from their .brp

FEATURE [Sketcher::SketchObject] Sketch067  label="basin_sketch"
  ArcFitTolerance = 0
  AttachmentSupport = -> [XZ_Plane034]
  FullyConstrained = true
  MakeInternals = false
  MapMode = 5
  Placement = pos=(0,0,0) rot=(1,0,0;1.5708rad)
  sketch-geometry (10):
    g0: LineSegment StartX=0 StartY=0 StartZ=0 EndX=160 EndY=0 EndZ=0
    g1: LineSegment StartX=160 StartY=0 StartZ=0 EndX=177.5 EndY=357 EndZ=0
    g2: LineSegment StartX=177.5 StartY=357 StartZ=0 EndX=185 EndY=357 EndZ=0
    g3: LineSegment StartX=185 StartY=357 StartZ=0 EndX=185 EndY=369 EndZ=0
    g4: LineSegment StartX=185 StartY=369 StartZ=0 EndX=177.5 EndY=369 EndZ=0
    g5: LineSegment StartX=177.5 StartY=369 StartZ=0 EndX=177.5 EndY=392 EndZ=0
    g6: LineSegment StartX=177.5 StartY=392 StartZ=0 EndX=175.5 EndY=392 EndZ=0
    g7: LineSegment StartX=0 StartY=2 StartZ=0 EndX=0 EndY=0 EndZ=0
    g8: LineSegment StartX=175.5 StartY=392 StartZ=0 EndX=158 EndY=2 EndZ=0
    g9: LineSegment StartX=158 StartY=2 StartZ=0 EndX=0 EndY=2 EndZ=0
  constraints (29):
    c: Coincident(g-1,g0)
    c: PointOnObject(g0,g-1)
    c: Coincident(g0,g1)
    c: Coincident(g1,g2)
    c: Horizontal(g2)
    c: Coincident(g2,g3)
    c: Vertical(g3)
    c: Coincident(g3,g4)
    c: Horizontal(g4)
    c: Coincident(g4,g5)
    c: Coincident(g5,g6)
    c: Horizontal(g6)
    c: Coincident(g7,g0)
    c: DistanceX(g0) = 160  'basin_bottom_r'
    c: DistanceX(g1) = 177.5
    c: Vertical(g4,g1)
    c: Vertical(g5,g4)
    c: DistanceX(g2) = 185
    c: DistanceY(g1) = 357
    c: DistanceY(g2,g3) = 12
    c: Coincident(g9,g8)
    c: Horizontal(g9)
    c: DistanceY(g0,g9) = 2
    c: DistanceX(g8,g0) = 2
    c: DistanceX(g8,g5) = 2
    c: Coincident(g6,g8)
    c: DistanceY(g6) = 392
    c: Coincident(g7,g9)
    c: Vertical(g7)
FEATURE [Sketcher::SketchObject] Sketch068
  ArcFitTolerance = 0
  AttachmentSupport = -> [XZ_Plane034]
  FullyConstrained = true
  MakeInternals = false
  MapMode = 5
  Placement = pos=(0,0,0) rot=(1,0,0;1.5708rad)
  expr: Constraints[13] = Sketch067.Constraints.basin_bottom_r
  expr: Constraints[14] = Sketch067.Constraints[14]
  expr: Constraints[17] = Sketch067.Constraints[17]
  expr: Constraints[18] = Sketch067.Constraints[18]
  expr: Constraints[19] = Sketch067.Constraints[19]
  expr: Constraints[22] = Sketch067.Constraints[22]
  expr: Constraints[23] = Sketch067.Constraints[23]
  expr: Constraints[24] = Sketch067.Constraints[24]
  expr: Constraints[26] = Sketch067.Constraints[26]
  sketch-geometry (14):
    g0: LineSegment [constr] StartX=0 StartY=0 StartZ=0 EndX=160 EndY=0 EndZ=0
    g1: LineSegment [constr] StartX=160 StartY=0 StartZ=0 EndX=177.5 EndY=357 EndZ=0
    g2: LineSegment StartX=177.5 StartY=357 StartZ=0 EndX=185 EndY=357 EndZ=0
    g3: LineSegment StartX=185 StartY=357 StartZ=0 EndX=185 EndY=369 EndZ=0
    g4: LineSegment [constr] StartX=185 StartY=369 StartZ=0 EndX=177.5 EndY=369 EndZ=0
    g5: LineSegment [constr] StartX=177.5 StartY=369 StartZ=0 EndX=177.5 EndY=392 EndZ=0
    g6: LineSegment [constr] StartX=177.5 StartY=392 StartZ=0 EndX=175.5 EndY=392 EndZ=0
    g7: LineSegment [constr] StartX=0 StartY=2 StartZ=0 EndX=0 EndY=0 EndZ=0
    g8: LineSegment [constr] StartX=175.5 StartY=392 StartZ=0 EndX=158 EndY=2 EndZ=0
    g9: LineSegment [constr] StartX=158 StartY=2 StartZ=0 EndX=0 EndY=2 EndZ=0
    g10: LineSegment StartX=185 StartY=369 StartZ=0 EndX=202.5 EndY=369 EndZ=0
    g11: LineSegment StartX=202.5 StartY=369 StartZ=0 EndX=202.5 EndY=319 EndZ=0
    g12: LineSegment StartX=202.5 StartY=319 StartZ=0 EndX=175.637 EndY=319 EndZ=0
    g13: LineSegment StartX=175.637 StartY=319 StartZ=0 EndX=177.5 EndY=357 EndZ=0
  constraints (40):
    c: Coincident(g-1,g0)
    c: PointOnObject(g0,g-1)
    c: Coincident(g0,g1)
    c: Coincident(g1,g2)
    c: Horizontal(g2)
    c: Coincident(g2,g3)
    c: Vertical(g3)
    c: Coincident(g3,g4)
    c: Horizontal(g4)
    c: Coincident(g4,g5)
    c: Coincident(g5,g6)
    c: Horizontal(g6)
    c: Coincident(g7,g0)
    c: DistanceX(g0) = 160
    c: DistanceX(g1) = 177.5
    c: Vertical(g4,g1)
    c: Vertical(g5,g4)
    c: DistanceX(g2) = 185
    c: DistanceY(g1) = 357
    c: DistanceY(g2,g3) = 12
    c: Coincident(g9,g8)
    c: Horizontal(g9)
    c: DistanceY(g0,g9) = 2
    c: DistanceX(g8,g0) = 2
    c: DistanceX(g8,g5) = 2
    c: Coincident(g6,g8)
    c: DistanceY(g6) = 392
    c: Coincident(g7,g9)
    c: Vertical(g7)
    c: Coincident(g10,g3)
    c: Horizontal(g10)
    c: Coincident(g11,g10)
    c: Vertical(g11)
    c: Coincident(g12,g11)
    c: PointOnObject(g12,g1)
    c: Horizontal(g12)
    c: Coincident(g13,g12)
    c: Coincident(g13,g2)
    c: DistanceX(g10) = 202.5
    c: DistanceY(g11,g10) = 50
FEATURE [PartDesign::Revolution] Revolution
  Angle = 360
  Angle2 = 60
  Axis = (0,2e-16,1)
  Base = (0,0,0)
  Placement = pos=(0,0,0) rot=(1,0,0;1.5708rad)
  Profile = -> Sketch067
  ReferenceAxis = -> Sketch067 [V_Axis]
  Reversed = true
  Suppressed = false
  Type = 0
FEATURE [PartDesign::Revolution] Revolution001
  Angle = 34
  Angle2 = 60
  Axis = (0,2e-16,1)
  Base = (0,0,0)
  BaseFeature = -> Revolution
  Midplane = true
  Placement = pos=(0,0,0) rot=(1,0,0;1.5708rad)
  Profile = -> Sketch068
  ReferenceAxis = -> Sketch068 [V_Axis]
  Reversed = true
  Suppressed = false
  Type = 0
FEATURE [PartDesign::Mirrored] Mirrored023
  BaseFeature = -> Revolution001
  MirrorPlane = -> Sketch068 [V_Axis]
  Originals = -> [Revolution001]
  Placement = pos=(0,0,0) rot=(1,0,0;1.5708rad)
  Suppressed = false
  TransformMode = 0
FEATURE [PartDesign::CoordinateSystem] LCS_021  label="base_LCS"
  AttacherType = Attacher::AttachEngine3D
  AttachmentSupport = -> [X_Axis034]
  MapMode = 2
FEATURE [PartDesign::Body] Body_7  label="basin"
  AllowCompound = false
  Group = -> [LCS_021,Sketch067,Revolution,Sketch068,Revolution001,Mirrored023]
  Origin = -> Origin034
  Tip = -> Mirrored023
FEATURE [Spreadsheet::Sheet] Spreadsheet  label="Properties"
  cells = B2(height)==392 mm; C2(bottom_d)==320 mm; D2(max_r)==405 mm
FEATURE [Part::FeaturePython] aCircle  # WARN: FeaturePython — macro-defined, semantics opaque (R4)
FEATURE [Part::FeaturePython] Radius  # WARN: FeaturePython — macro-defined, semantics opaque (R4)
FEATURE [App::AnnotationLabel] MeasureLbl
  BasePosition = (160,0,0)
  LabelText = R = 160.00 mm
  TextPosition = (0,0,0)
FEATURE [Part::FeaturePython] aCircle001  # WARN: FeaturePython — macro-defined, semantics opaque (R4)
FEATURE [Part::FeaturePython] Radius001  # WARN: FeaturePython — macro-defined, semantics opaque (R4)
FEATURE [App::AnnotationLabel] MeasureLbl001
  BasePosition = (193.652,-59.2053,369)
  LabelText = R = 202.50 mm
  TextPosition = (0,0,0)
FEATURE [App::DocumentObjectGroup] Measures
  Group = -> [aCircle,Radius,MeasureLbl,aCircle001,Radius001,MeasureLbl001]
---- part composit-properties.FCStd = doc fcstd_d99993d4ac97 ----
FCSTD DOCUMENT  (FreeCAD 1.1R38827 (Git))
Label: composit-properties
License: All rights reserved
LicenseURL: http://en.wikipedia.org/wiki/All_rights_reserved
objects: Spreadsheet::Sheet×1

FEATURE [Spreadsheet::Sheet] Spreadsheet  label="Properties"
  cells = B2(thickness)==3 mm; C2(al_thickness)==0.3 mm; D2(bend_r)==0.1 mm
---- part dropper.FCStd = doc fcstd_03601a3bb068 ----
FCSTD DOCUMENT  (FreeCAD 1.1R38827 (Git))
Label: dropper
License: All rights reserved
LicenseURL: http://en.wikipedia.org/wiki/All_rights_reserved
objects: Sketcher::SketchObject×9, Part::FeaturePython×4, PartDesign::Revolution×3, PartDesign::Body×2, PartDesign::CoordinateSystem×1, Spreadsheet::Sheet×1, PartDesign::SubShapeBinder×1, PartDesign::Pad×1, PartDesign::Pocket×1, PartDesign::Groove×1, App::Part×1
note: 44 computed .brp shape members not serialized (recipe doc carries the construction recipe); baked Part::Feature solids carry a one-line shape summary decoded from their .brp

FEATURE [Sketcher::SketchObject] Sketch005
  ArcFitTolerance = 0
  AttachmentSupport = -> [YZ_Plane001]
  FullyConstrained = true
  MakeInternals = false
  MapMode = 5
  Placement = pos=(0,0,0) rot=(0.57735,0.57735,0.57735;2.0944rad)
  sketch-geometry (14):
    g0: LineSegment StartX=11.3 StartY=0 StartZ=0 EndX=11.3 EndY=1 EndZ=0
    g1: LineSegment StartX=11.3 StartY=1 StartZ=0 EndX=10.7 EndY=1 EndZ=0
    g2: LineSegment StartX=10.7 StartY=1 StartZ=0 EndX=10.7 EndY=9.9 EndZ=0
    g3: LineSegment StartX=10.7 StartY=9.9 StartZ=0 EndX=6.6 EndY=9.9 EndZ=0
    g4: LineSegment StartX=6.6 StartY=9.9 StartZ=0 EndX=6.6 EndY=3 EndZ=0
    g5: LineSegment StartX=6.6 StartY=3 StartZ=0 EndX=2.5 EndY=3 EndZ=0
    g6: LineSegment StartX=2.5 StartY=3 StartZ=0 EndX=2.5 EndY=20 EndZ=0
    g7: LineSegment StartX=2.5 StartY=20 StartZ=0 EndX=1.45 EndY=20 EndZ=0
    g8: LineSegment StartX=1.45 StartY=20 StartZ=0 EndX=1.45 EndY=2.5 EndZ=0
    g9: LineSegment StartX=1.45 StartY=2.5 StartZ=0 EndX=7 EndY=-0.6 EndZ=0
    g10: LineSegment StartX=7 StartY=-0.6 StartZ=0 EndX=7 EndY=8.85 EndZ=0
    g11: LineSegment StartX=7 StartY=8.85 StartZ=0 EndX=9.5 EndY=8.85 EndZ=0
    g12: LineSegment StartX=9.5 StartY=8.85 StartZ=0 EndX=9.5 EndY=0 EndZ=0
    g13: LineSegment StartX=9.5 StartY=0 StartZ=0 EndX=11.3 EndY=0 EndZ=0
  constraints (43):
    c: PointOnObject(g0,g-1)
    c: Vertical(g0)
    c: Coincident(g0,g1)
    c: Horizontal(g1)
    c: Coincident(g1,g2)
    c: Vertical(g2)
    c: Coincident(g2,g3)
    c: Horizontal(g3)
    c: Coincident(g3,g4)
    c: Vertical(g4)
    c: Coincident(g4,g5)
    c: Coincident(g5,g6)
    c: Vertical(g6)
    c: Coincident(g6,g7)
    c: Horizontal(g7)
    c: Coincident(g7,g8)
    c: Vertical(g8)
    c: Coincident(g8,g9)
    c: Coincident(g9,g10)
    c: Vertical(g10)
    c: Coincident(g10,g11)
    c: Horizontal(g11)
    c: Coincident(g11,g12)
    c: Vertical(g12)
    c: Coincident(g12,g13)
    c: Coincident(g13,g0)
    c: Horizontal(g13)
    c: DistanceX(g0) = 11.3  'outer_r'
    c: DistanceY(g0) = 1
    c: DistanceY(g2) = 9.9
    c: DistanceX(g1,g0) = 0.6
    c: DistanceX(g3,g2) = 4.1
    c: DistanceY(g4,g3) = 6.9
    c: DistanceX(g6) = 2.5
    c: DistanceX(g7) = 1.45
    c: DistanceY(g9,g3) = 10.5
    c: DistanceX(g12,g0) = 1.8
    c: DistanceY(g11) = 8.85
    c: DistanceX(g9) = 7
    c: DistanceY(g9,g6) = 20.6
    c: Horizontal(g5)
    c: DistanceY(g8,g5) = 0.5
    c: DistanceY(g7) = 20
FEATURE [PartDesign::Revolution] Revolution002
  Angle = 360
  Angle2 = 60
  Axis = (0,0,1)
  Base = (0,0,0)
  Placement = pos=(0,0,0) rot=(1,1,1;2.0944rad)
  Profile = -> Sketch005
  ReferenceAxis = -> Sketch005 [V_Axis]
  Reversed = true
  Suppressed = false
  Type = 0
FEATURE [Sketcher::SketchObject] Sketch006
  ArcFitTolerance = 0
  AttachmentSupport = -> [YZ_Plane001]
  FullyConstrained = true
  MakeInternals = false
  MapMode = 5
  Placement = pos=(0,0,0) rot=(0.57735,0.57735,0.57735;2.0944rad)
  expr: Constraints[27] = Sketch005.Constraints.outer_r
  expr: Constraints[28] = Sketch005.Constraints[28]
  expr: Constraints[29] = Sketch005.Constraints[29]
  expr: Constraints[30] = Sketch005.Constraints[30]
  expr: Constraints[31] = Sketch005.Constraints[31]
  expr: Constraints[32] = Sketch005.Constraints[32]
  expr: Constraints[33] = Sketch005.Constraints[33]
  expr: Constraints[34] = Sketch005.Constraints[34]
  expr: Constraints[35] = Sketch005.Constraints[35]
  expr: Constraints[36] = Sketch005.Constraints[36]
  expr: Constraints[37] = Sketch005.Constraints[37]
  expr: Constraints[38] = Sketch005.Constraints[38]
  expr: Constraints[39] = Sketch005.Constraints[39]
  expr: Constraints[41] = Sketch005.Constraints[41]
  expr: Constraints[69] = Sketch005.Constraints.outer_r
  expr: Constraints[70] = Sketch005.Constraints[28]
  expr: Constraints[71] = Sketch005.Constraints[29]
  expr: Constraints[72] = Sketch005.Constraints[30]
  expr: Constraints[73] = Sketch005.Constraints[31]
  expr: Constraints[74] = Sketch005.Constraints[32]
  expr: Constraints[75] = Sketch005.Constraints[33]
  expr: Constraints[76] = Sketch005.Constraints[34]
  expr: Constraints[77] = Sketch005.Constraints[35]
  expr: Constraints[78] = Sketch005.Constraints[36]
  expr: Constraints[79] = Sketch005.Constraints[37]
  expr: Constraints[80] = Sketch005.Constraints[38]
  expr: Constraints[81] = Sketch005.Constraints[39]
  expr: Constraints[83] = Sketch005.Constraints[41]
  sketch-geometry (32):
    g0: LineSegment [constr] StartX=11.3 StartY=0 StartZ=0 EndX=11.3 EndY=1 EndZ=0
    g1: LineSegment [constr] StartX=11.3 StartY=1 StartZ=0 EndX=10.7 EndY=1 EndZ=0
    g2: LineSegment [constr] StartX=10.7 StartY=1 StartZ=0 EndX=10.7 EndY=9.9 EndZ=0
    g3: LineSegment [constr] StartX=10.7 StartY=9.9 StartZ=0 EndX=6.6 EndY=9.9 EndZ=0
    g4: LineSegment StartX=6.6 StartY=9.9 StartZ=0 EndX=6.6 EndY=3 EndZ=0
    g5: LineSegment StartX=6.6 StartY=3 StartZ=0 EndX=2.5 EndY=3 EndZ=0
    g6: LineSegment [constr] StartX=2.5 StartY=3 StartZ=0 EndX=2.5 EndY=20 EndZ=0
    g7: LineSegment [constr] StartX=2.5 StartY=20 StartZ=0 EndX=1.45 EndY=20 EndZ=0
    g8: LineSegment [constr] StartX=1.45 StartY=20 StartZ=0 EndX=1.45 EndY=2.5 EndZ=0
    g9: LineSegment [constr] StartX=1.45 StartY=2.5 StartZ=0 EndX=7 EndY=-0.6 EndZ=0
    g10: LineSegment [constr] StartX=7 StartY=-0.6 StartZ=0 EndX=7 EndY=8.85 EndZ=0
    g11: LineSegment [constr] StartX=7 StartY=8.85 StartZ=0 EndX=9.5 EndY=8.85 EndZ=0
    g12: LineSegment [constr] StartX=9.5 StartY=8.85 StartZ=0 EndX=9.5 EndY=0 EndZ=0
    g13: LineSegment [constr] StartX=9.5 StartY=0 StartZ=0 EndX=11.3 EndY=0 EndZ=0
    g14: LineSegment [constr] StartX=11.3 StartY=0 StartZ=0 EndX=11.3 EndY=1 EndZ=0
    g15: LineSegment [constr] StartX=11.3 StartY=1 StartZ=0 EndX=10.7 EndY=1 EndZ=0
    g16: LineSegment [constr] StartX=10.7 StartY=1 StartZ=0 EndX=10.7 EndY=9.9 EndZ=0
    g17: LineSegment [constr] StartX=10.7 StartY=9.9 StartZ=0 EndX=6.6 EndY=9.9 EndZ=0
    g18: LineSegment [constr] StartX=6.6 StartY=9.9 StartZ=0 EndX=6.6 EndY=3 EndZ=0
    g19: LineSegment [constr] StartX=6.6 StartY=3 StartZ=0 EndX=2.5 EndY=3 EndZ=0
    g20: LineSegment [constr] StartX=2.5 StartY=3 StartZ=0 EndX=2.5 EndY=20 EndZ=0
    g21: LineSegment [constr] StartX=2.5 StartY=20 StartZ=0 EndX=1.45 EndY=20 EndZ=0
    g22: LineSegment [constr] StartX=1.45 StartY=20 StartZ=0 EndX=1.45 EndY=2.5 EndZ=0
    g23: LineSegment [constr] StartX=1.45 StartY=2.5 StartZ=0 EndX=7 EndY=-0.6 EndZ=0
    g24: LineSegment [constr] StartX=7 StartY=-0.6 StartZ=0 EndX=7 EndY=8.85 EndZ=0
    g25: LineSegment [constr] StartX=7 StartY=8.85 StartZ=0 EndX=9.5 EndY=8.85 EndZ=0
    g26: LineSegment [constr] StartX=9.5 StartY=8.85 StartZ=0 EndX=9.5 EndY=0 EndZ=0
    g27: LineSegment [constr] StartX=9.5 StartY=0 StartZ=0 EndX=11.3 EndY=0 EndZ=0
    g28: LineSegment StartX=2.5 StartY=3 StartZ=0 EndX=2.04763 EndY=3 EndZ=0
    g29: LineSegment StartX=2.04763 StartY=3 StartZ=0 EndX=2.04763 EndY=12.6758 EndZ=0
    g30: LineSegment StartX=2.04763 StartY=12.6758 StartZ=0 EndX=6.6 EndY=9.9 EndZ=0
    g31: GeomPoint [constr] X=2.5 Y=12.4 Z=0
  constraints (94):
    c: PointOnObject(g0,g-1)
    c: Vertical(g0)
    c: Coincident(g0,g1)
    c: Horizontal(g1)
    c: Coincident(g1,g2)
    c: Vertical(g2)
    c: Coincident(g2,g3)
    c: Horizontal(g3)
    c: Coincident(g3,g4)
    c: Vertical(g4)
    c: Coincident(g4,g5)
    c: Coincident(g5,g6)
    c: Vertical(g6)
    c: Coincident(g6,g7)
    c: Horizontal(g7)
    c: Coincident(g7,g8)
    c: Vertical(g8)
    c: Coincident(g8,g9)
    c: Coincident(g9,g10)
    c: Vertical(g10)
    c: Coincident(g10,g11)
    c: Horizontal(g11)
    c: Coincident(g11,g12)
    c: Vertical(g12)
    c: Coincident(g12,g13)
    c: Coincident(g13,g0)
    c: Horizontal(g13)
    c: DistanceX(g0) = 11.3
    c: DistanceY(g0) = 1
    c: DistanceY(g2) = 9.9
    c: DistanceX(g1,g0) = 0.6
    c: DistanceX(g3,g2) = 4.1
    c: DistanceY(g4,g3) = 6.9
    c: DistanceX(g6) = 2.5
    c: DistanceX(g7) = 1.45
    c: DistanceY(g9,g3) = 10.5
    c: DistanceX(g12,g0) = 1.8
    c: DistanceY(g11) = 8.85
    c: DistanceX(g9) = 7
    c: DistanceY(g9,g6) = 20.6
    c: Horizontal(g5)
    c: DistanceY(g8,g5) = 0.5
    c: PointOnObject(g14,g-1)
    c: Vertical(g14)
    c: Coincident(g14,g15)
    c: Horizontal(g15)
    c: Coincident(g15,g16)
    c: Vertical(g16)
    c: Coincident(g16,g17)
    c: Horizontal(g17)
    c: Coincident(g17,g18)
    c: Vertical(g18)
    c: Coincident(g18,g19)
    c: Coincident(g19,g20)
    c: Vertical(g20)
    c: Coincident(g20,g21)
    c: Horizontal(g21)
    c: Coincident(g21,g22)
    c: Vertical(g22)
    c: Coincident(g22,g23)
    c: Coincident(g23,g24)
    c: Vertical(g24)
    c: Coincident(g24,g25)
    c: Horizontal(g25)
    c: Coincident(g25,g26)
    c: Vertical(g26)
    c: Coincident(g26,g27)
    c: Coincident(g27,g14)
    c: Horizontal(g27)
    c: DistanceX(g14) = 11.3
    c: DistanceY(g14) = 1
    c: DistanceY(g16) = 9.9
    c: DistanceX(g15,g14) = 0.6
    c: DistanceX(g17,g16) = 4.1
    c: DistanceY(g18,g17) = 6.9
    c: DistanceX(g20) = 2.5
    c: DistanceX(g21) = 1.45
    c: DistanceY(g23,g17) = 10.5
    c: DistanceX(g26,g14) = 1.8
    c: DistanceY(g25) = 8.85
    c: DistanceX(g23) = 7
    c: DistanceY(g23,g20) = 20.6
    c: Horizontal(g19)
    c: DistanceY(g22,g19) = 0.5
    c: Coincident(g28,g5)
    c: Horizontal(g28)
    c: Coincident(g29,g28)
    c: Vertical(g29)
    c: Coincident(g30,g29)
    c: Coincident(g30,g4)
    c: PointOnObject(g31,g30)
    c: PointOnObject(g31,g6)
    c: DistanceY(g4,g31) = 2.5
    c: DistanceX(g29,g31) = 0.452366
FEATURE [PartDesign::Body] Body001
  AllowCompound = false
  Group = -> [Sketch005,Revolution002,Sketch006]
  Origin = -> Origin001
  Placement = pos=(0,0,2.5) rot=(0,0,1;0rad)
  Tip = -> Revolution002
FEATURE [Sketcher::SketchObject] Sketch007  label="base"
  ArcFitTolerance = 0
  FullyConstrained = true
  MakeInternals = false
  expr: .Constraints.r = Sketch005.Constraints.outer_r + 0.5 mm
  sketch-geometry (1):
    g0: Circle CenterX=0 CenterY=0 CenterZ=0 NormalX=0 NormalY=0 NormalZ=1 AngleXU=0 Radius=11.8
  constraints (2):
    c: Coincident(g0,g-1)
    c: Radius(g0) = 11.8  'r'
FEATURE [Sketcher::SketchObject] Sketch002
  ArcFitTolerance = 0
  AttachmentSupport = -> [YZ_Plane]
  FullyConstrained = true
  MakeInternals = false
  MapMode = 5
  Placement = pos=(0,0,0) rot=(0.57735,0.57735,0.57735;2.0944rad)
  expr: Constraints[18] = Sketch001.Constraints[18]
  expr: Constraints[19] = Sketch001.Constraints[19]
  expr: Constraints[20] = Sketch001.Constraints[20]
  expr: Constraints[21] = Sketch001.Constraints[21]
  expr: Constraints[22] = Sketch001.Constraints[22]
  expr: Constraints[23] = Sketch001.Constraints[23]
  expr: Constraints[24] = Sketch001.Constraints[24]
  expr: Constraints[25] = Sketch001.Constraints[25]
  expr: Constraints[27] = Sketch001.Constraints[27]
  sketch-geometry (13):
    g0: LineSegment [constr] StartX=1.15 StartY=0 StartZ=0 EndX=1.15 EndY=-18.1612 EndZ=0
    g1: LineSegment StartX=1.15 StartY=-18.1612 StartZ=0 EndX=2.765 EndY=-8.77 EndZ=0
    g2: LineSegment [constr] StartX=2.765 StartY=-8.77 StartZ=0 EndX=2.2 EndY=-8.77 EndZ=0
    g3: LineSegment [constr] StartX=2.2 StartY=-8.77 StartZ=0 EndX=2.2 EndY=-5.32 EndZ=0
    g4: LineSegment [constr] StartX=2.2 StartY=-5.32 StartZ=0 EndX=3.35 EndY=-5.32 EndZ=0
    g5: LineSegment [constr] StartX=3.35 StartY=-5.32 StartZ=0 EndX=3.35 EndY=-3.66 EndZ=0
    g6: LineSegment [constr] StartX=3.35 StartY=-3.66 StartZ=0 EndX=2.65 EndY=-3.66 EndZ=0
    g7: LineSegment [constr] StartX=2.65 StartY=-3.66 StartZ=0 EndX=2.65 EndY=0 EndZ=0
    g8: LineSegment [constr] StartX=2.65 StartY=0 StartZ=0 EndX=1.15 EndY=0 EndZ=0
    g9: GeomPoint [constr] X=-2.765 Y=-8.77 Z=0
    g10: GeomPoint [constr] X=-2.765 Y=-8.77 Z=0
    g11: LineSegment StartX=1.15 StartY=-18.1612 StartZ=0 EndX=-3.0574 EndY=-18.1612 EndZ=0
    g12: LineSegment StartX=-3.0574 StartY=-18.1612 StartZ=0 EndX=2.765 EndY=-8.77 EndZ=0
  constraints (34):
    c: PointOnObject(g0,g-1)
    c: Vertical(g0)
    c: Coincident(g0,g1)
    c: Coincident(g1,g2)
    c: Horizontal(g2)
    c: Coincident(g2,g3)
    c: Vertical(g3)
    c: Coincident(g3,g4)
    c: Horizontal(g4)
    c: Coincident(g4,g5)
    c: Vertical(g5)
    c: Coincident(g5,g6)
    c: Horizontal(g6)
    c: Coincident(g6,g7)
    c: PointOnObject(g7,g-1)
    c: Vertical(g7)
    c: Coincident(g7,g8)
    c: Coincident(g8,g0)
    c: DistanceY(g2,g3) = 3.45
    c: DistanceY(g4,g5) = 1.66
    c: DistanceY(g6,g7) = 3.66
    c: DistanceX(g2) = 2.2
    c: DistanceX(g4) = 3.35
    c: DistanceX(g0) = 1.15
    c: DistanceX(g7) = 2.65
    c: DistanceX(g1) = 2.765
    c: Symmetric(g9,g1,g-2)
    c: Distance(g9,g1) = 5.45
    c: Symmetric(g10,g1,g-2)
    c: Coincident(g11,g1)
    c: Horizontal(g11)
    c: Coincident(g12,g11)
    c: Coincident(g12,g1)
    c: Distance(g9,g12) = 4.7
FEATURE [Sketcher::SketchObject] Sketch001
  ArcFitTolerance = 0
  AttachmentSupport = -> [XZ_Plane]
  FullyConstrained = true
  MakeInternals = false
  MapMode = 5
  Placement = pos=(0,0,0) rot=(1,0,0;1.5708rad)
  sketch-geometry (10):
    g0: LineSegment StartX=1.15 StartY=0 StartZ=0 EndX=1.15 EndY=-18.1612 EndZ=0
    g1: LineSegment StartX=1.15 StartY=-18.1612 StartZ=0 EndX=2.765 EndY=-8.77 EndZ=0
    g2: LineSegment StartX=2.765 StartY=-8.77 StartZ=0 EndX=2.2 EndY=-8.77 EndZ=0
    g3: LineSegment StartX=2.2 StartY=-8.77 StartZ=0 EndX=2.2 EndY=-5.32 EndZ=0
    g4: LineSegment StartX=2.2 StartY=-5.32 StartZ=0 EndX=3.35 EndY=-5.32 EndZ=0
    g5: LineSegment StartX=3.35 StartY=-5.32 StartZ=0 EndX=3.35 EndY=-3.66 EndZ=0
    g6: LineSegment StartX=3.35 StartY=-3.66 StartZ=0 EndX=2.65 EndY=-3.66 EndZ=0
    g7: LineSegment StartX=2.65 StartY=-3.66 StartZ=0 EndX=2.65 EndY=0 EndZ=0
    g8: LineSegment StartX=2.65 StartY=0 StartZ=0 EndX=1.15 EndY=0 EndZ=0
    g9: GeomPoint [constr] X=-2.765 Y=-8.77 Z=0
  constraints (28):
    c: PointOnObject(g0,g-1)
    c: Vertical(g0)
    c: Coincident(g0,g1)
    c: Coincident(g1,g2)
    c: Horizontal(g2)
    c: Coincident(g2,g3)
    c: Vertical(g3)
    c: Coincident(g3,g4)
    c: Horizontal(g4)
    c: Coincident(g4,g5)
    c: Vertical(g5)
    c: Coincident(g5,g6)
    c: Horizontal(g6)
    c: Coincident(g6,g7)
    c: PointOnObject(g7,g-1)
    c: Vertical(g7)
    c: Coincident(g7,g8)
    c: Coincident(g8,g0)
    c: DistanceY(g2,g3) = 3.45
    c: DistanceY(g4,g5) = 1.66
    c: DistanceY(g6,g7) = 3.66
    c: DistanceX(g2) = 2.2
    c: DistanceX(g4) = 3.35
    c: DistanceX(g0) = 1.15
    c: DistanceX(g7) = 2.65
    c: DistanceX(g1) = 2.765
    c: Symmetric(g9,g1,g-2)
    c: Distance(g9,g1) = 5.45
FEATURE [Sketcher::SketchObject] Sketch  label="fix_sketch"
  ArcFitTolerance = 0
  AttachmentSupport = -> [XY_Plane]
  FullyConstrained = true
  MakeInternals = false
  MapMode = 5
  sketch-geometry (5):
    g0: ArcOfCircle CenterX=0 CenterY=0 CenterZ=0 NormalX=0 NormalY=0 NormalZ=1 AngleXU=0 Radius=10.5 StartAngle=0.496317 EndAngle=1.5708
    g1: ArcOfCircle CenterX=16.5 CenterY=0 CenterZ=0 NormalX=0 NormalY=0 NormalZ=1 AngleXU=0 Radius=3.25 StartAngle=0 EndAngle=1.34547
    g2: LineSegment StartX=17.2261 StartY=3.16784 StartZ=0 EndX=9.23309 EndY=5 EndZ=0
    g3: GeomPoint [constr] X=-19.75 Y=0 Z=0
    g4: GeomPoint [constr] X=0 Y=-10.5 Z=0
  constraints (14):
    c: PointOnObject(g0,g-2)
    c: PointOnObject(g1,g-1)
    c: PointOnObject(g1,g-1)
    c: Coincident(g2,g0)
    c: Tangent(g2,g1) = -1.5708
    c: Diameter(g0) = 21
    c: DistanceX(g1) = 19.75
    c: DistanceY(g0) = 5
    c: Diameter(g1) = 6.5
    c: Coincident(g0,g-1)
    c: Symmetric(g3,g1,g-2)
    c: DistanceX(g3,g1) = 39.5  'length'
    c: Symmetric(g4,g0,g-1)
    c: DistanceY(g4,g0) = 21  'width'
FEATURE [Sketcher::SketchObject] Sketch004
  ArcFitTolerance = 0
  AttachmentSupport = -> [YZ_Plane]
  FullyConstrained = true
  MakeInternals = false
  MapMode = 5
  Placement = pos=(0,0,0) rot=(0.57735,0.57735,0.57735;2.0944rad)
  expr: Constraints[3] = Sketch003.Constraints[9]
  sketch-geometry (6):
    g0: LineSegment StartX=7.75 StartY=10.9 StartZ=0 EndX=0 EndY=10.9 EndZ=0
    g1: LineSegment StartX=0 StartY=10.9 StartZ=0 EndX=0 EndY=1.5 EndZ=0
    g2: LineSegment StartX=0 StartY=1.5 StartZ=0 EndX=7.25 EndY=1.5 EndZ=0
    g3: LineSegment StartX=7.25 StartY=1.5 StartZ=0 EndX=7.25 EndY=2.5 EndZ=0
    g4: LineSegment StartX=7.25 StartY=2.5 StartZ=0 EndX=7.75 EndY=4 EndZ=0
    g5: LineSegment StartX=7.75 StartY=4 StartZ=0 EndX=7.75 EndY=10.9 EndZ=0
  constraints (18):
    c: Coincident(g0,g1)
    c: Horizontal(g0)
    c: Vertical(g1)
    c: DistanceY(g0) = 10.9
    c: Horizontal(g2)
    c: Coincident(g2,g3)
    c: Vertical(g3)
    c: Coincident(g3,g4)
    c: Coincident(g4,g5)
    c: Vertical(g5)
    c: Coincident(g0,g5)
    c: Coincident(g1,g2)
    c: DistanceY(g1,g0) = 9.4
    c: DistanceX(g0) = 7.75
    c: DistanceY(g2,g3) = 1
    c: DistanceY(g3,g4) = 1.5
    c: DistanceX(g2,g4) = 0.5
    c: Vertical(g1,g-1)
FEATURE [Sketcher::SketchObject] Sketch003
  ArcFitTolerance = 0
  AttachmentSupport = -> [YZ_Plane]
  FullyConstrained = true
  MakeInternals = false
  MapMode = 5
  Placement = pos=(0,0,0) rot=(0.57735,0.57735,0.57735;2.0944rad)
  sketch-geometry (4):
    g0: LineSegment StartX=0 StartY=0 StartZ=0 EndX=8.825 EndY=0 EndZ=0
    g1: LineSegment StartX=8.825 StartY=0 StartZ=0 EndX=8.825 EndY=10.9 EndZ=0
    g2: LineSegment StartX=8.825 StartY=10.9 StartZ=0 EndX=0 EndY=10.9 EndZ=0
    g3: LineSegment StartX=0 StartY=10.9 StartZ=0 EndX=0 EndY=0 EndZ=0
  constraints (11):
    c: Coincident(g0,g1)
    c: Coincident(g1,g2)
    c: Coincident(g2,g3)
    c: Coincident(g3,g0)
    c: Horizontal(g0)
    c: Horizontal(g2)
    c: Vertical(g1)
    c: Vertical(g3)
    c: Coincident(g0,g-1)
    c: DistanceY(g2) = 10.9
    c: DistanceX(g0) = 8.825
FEATURE [PartDesign::CoordinateSystem] LCS_0
  AttacherType = Attacher::AttachEngine3D
  AttachmentOffset = pos=(0,0,2.45) rot=(0,0,1;0rad)
  AttachmentSupport = -> [X_Axis002]
  MapMode = 2
  Placement = pos=(0,0,2.45) rot=(0,0,1;0rad)
FEATURE [Spreadsheet::Sheet] Spreadsheet  label="Properties"
  cells = B2(top_d)==22.6 mm; C2(bot_d)==21 mm; D2(top_height)==20 mm; E2(bot_base_height)==2.4 mm; F2(total_height)==22.4 mm; G2(total_width)==38.9 mm
FEATURE [Part::FeaturePython] Mirror  label="Mirror of Sketch"  # WARN: FeaturePython — macro-defined, semantics opaque (R4)
  ExposePlacement = false
  FlipX = true
  FlipY = false
  FlipZ = false
  MarkerShape = 1
  MarkerSize = 0
  NumElements = 0
  Object = -> Sketch
  ObjectTraversal = 0
  Type = lattice2Mirror.LatticeMirror
  isLattice = 0
FEATURE [Part::FeaturePython] Mirror001  label="Mirror001 of Mirror of Sketch"  # WARN: FeaturePython — macro-defined, semantics opaque (R4)
  ExposePlacement = false
  FlipX = false
  FlipY = true
  FlipZ = false
  MarkerShape = 1
  MarkerSize = 0
  NumElements = 0
  Object = -> Mirror
  ObjectTraversal = 0
  Type = lattice2Mirror.LatticeMirror
  isLattice = 0
FEATURE [Part::FeaturePython] Mirror002  label="Mirror002 of Mirror001 of Mirror of Sketch"  # WARN: FeaturePython — macro-defined, semantics opaque (R4)
  ExposePlacement = false
  FlipX = true
  FlipY = false
  FlipZ = false
  MarkerShape = 1
  MarkerSize = 0
  NumElements = 0
  Object = -> Mirror001
  ObjectTraversal = 0
  Type = lattice2Mirror.LatticeMirror
  isLattice = 0
FEATURE [PartDesign::SubShapeBinder] Binder
  BindCopyOnChange = 0
  BindMode = 0
  ClaimChildren = true
  Context = -> Part [Body.Binder.]
  Fuse = false
  MakeFace = true
  OffsetFill = false
  OffsetIntersection = false
  OffsetJoinType = 0
  OffsetOpenResult = false
  PartialLoad = false
  Relative = true
  Support = -> [Connect]
  _Version = 2
FEATURE [PartDesign::Pad] Pad
  Direction = (0,0,1)
  Length = 2.45
  Length2 = 10
  Profile = -> Binder
  Suppressed = false
  Type = 0
FEATURE [PartDesign::Revolution] Revolution
  Angle = 360
  Angle2 = 60
  Axis = (0,2e-16,1)
  Base = (0,0,0)
  BaseFeature = -> Pad
  Profile = -> Sketch001
  ReferenceAxis = -> Sketch001 [V_Axis]
  Reversed = true
  Suppressed = false
  Type = 0
FEATURE [PartDesign::Pocket] Pocket
  BaseFeature = -> Revolution
  Direction = (-1,0,0)
  Length = 5
  Length2 = 5
  Midplane = true
  Profile = -> Sketch002
  ReferenceAxis = -> Sketch002 [N_Axis]
  Suppressed = false
  Type = 1
FEATURE [PartDesign::Revolution] Revolution001
  Angle = 360
  Angle2 = 60
  Axis = (0,0,1)
  Base = (0,0,0)
  BaseFeature = -> Pocket
  Profile = -> Sketch003
  ReferenceAxis = -> Sketch003 [V_Axis]
  Reversed = true
  Suppressed = false
  Type = 0
FEATURE [PartDesign::Groove] Groove
  Angle = 360
  Angle2 = 60
  Axis = (0,0,1)
  Base = (0,0,0)
  BaseFeature = -> Revolution001
  Profile = -> Sketch004
  ReferenceAxis = -> Sketch004 [V_Axis]
  Suppressed = false
  Type = 0
FEATURE [Sketcher::SketchObject] Sketch008  label="feed"
  ArcFitTolerance = 0
  AttachmentSupport = -> [XY_Plane]
  FullyConstrained = true
  MakeInternals = false
  MapMode = 5
  sketch-geometry (1):
    g0: Circle CenterX=0 CenterY=0 CenterZ=0 NormalX=0 NormalY=0 NormalZ=1 AngleXU=0 Radius=4
  constraints (2):
    c: Coincident(g0,g-1)
    c: Diameter(g0) = 8
FEATURE [PartDesign::Body] Body
  AllowCompound = false
  Group = -> [Sketch,Pad,Sketch001,Revolution,Sketch002,Pocket,Sketch003,Sketch004,Revolution001,Groove,Sketch008,Binder]
  Origin = -> Origin
  Tip = -> Groove
FEATURE [App::Part] Part  label="dropper"
  Group = -> [LCS_0,Body001,Body]
  Origin = -> Origin002
FEATURE [Part::FeaturePython] Connect  label="fix"  # WARN: FeaturePython — macro-defined, semantics opaque (R4)
  Objects = -> [Sketch,Mirror002,Mirror001,Mirror]
  Tolerance = 0
---- part hub2108.FCStd = doc fcstd_856699a5e2c1 ----
FCSTD DOCUMENT  (FreeCAD 1.1R38827 (Git))
Label: hub2108
License: All rights reserved
LicenseURL: http://en.wikipedia.org/wiki/All_rights_reserved
objects: Sketcher::SketchObject×5, PartDesign::CoordinateSystem×2, PartDesign::AdditiveCylinder×1, PartDesign::Body×1
note: 16 computed .brp shape members not serialized (recipe doc carries the construction recipe); baked Part::Feature solids carry a one-line shape summary decoded from their .brp

FEATURE [Sketcher::SketchObject] Sketch  label="top_fix_holes"
  ArcFitTolerance = 0
  FullyConstrained = true
  MakeInternals = false
  expr: Constraints[6] = (58.8 mm + 38 mm) / 2
  expr: Constraints[7] = (87.5 mm + 66.67 mm) / 2
  expr: Constraints[8] = (76.14 mm + 96.68 mm) / 2
  sketch-geometry (5):
    g0: Circle CenterX=38.5425 CenterY=-28.0433 CenterZ=0 NormalX=0 NormalY=0 NormalZ=1 AngleXU=0 Radius=5.1
    g1: Circle CenterX=43.205 CenterY=20.1316 CenterZ=0 NormalX=0 NormalY=0 NormalZ=1 AngleXU=0 Radius=5.1
    g2: Circle CenterX=-43.205 CenterY=20.1316 CenterZ=0 NormalX=0 NormalY=0 NormalZ=1 AngleXU=0 Radius=5.1
    g3: Circle CenterX=-38.5425 CenterY=-28.0433 CenterZ=0 NormalX=0 NormalY=0 NormalZ=1 AngleXU=0 Radius=5.1
    g4: Circle [constr] CenterX=0 CenterY=0 CenterZ=0 NormalX=0 NormalY=0 NormalZ=1 AngleXU=0 Radius=47.665
  constraints (13):
    c: Equal(g3,g2)
    c: Equal(g3,g1)
    c: Equal(g3,g0)
    c: Diameter(g3) = 10.2
    c: Symmetric(g0,g3,g-2)
    c: Symmetric(g1,g2,g-2)
    c: Distance(g0,g1) = 48.4
    c: Distance(g0,g3) = 77.085
    c: Distance(g2,g1) = 86.41
    c: Coincident(g4,g-1)
    c: PointOnObject(g0,g4)
    c: Distance(g3,g1) = 94.8866
    c: PointOnObject(g1,g4)
FEATURE [Sketcher::SketchObject] Sketch001  label="top_center_hole"
  ArcFitTolerance = 0
  FullyConstrained = true
  MakeInternals = false
  sketch-geometry (1):
    g0: Circle CenterX=0 CenterY=0 CenterZ=0 NormalX=0 NormalY=0 NormalZ=1 AngleXU=0 Radius=28
  constraints (2):
    c: Coincident(g0,g-1)
    c: Diameter(g0) = 56
FEATURE [Sketcher::SketchObject] Sketch002  label="bottom_fix_holes"
  ArcFitTolerance = 0
  FullyConstrained = true
  MakeInternals = false
  expr: Constraints[7] = (80 mm + 58.3 mm) / 4
  sketch-geometry (6):
    g0: Circle CenterX=34.575 CenterY=34.575 CenterZ=0 NormalX=0 NormalY=0 NormalZ=1 AngleXU=0 Radius=5.4
    g1: LineSegment [constr] StartX=34.575 StartY=34.575 StartZ=0 EndX=34.575 EndY=0 EndZ=0
    g2: LineSegment [constr] StartX=34.575 StartY=34.575 StartZ=0 EndX=0 EndY=34.575 EndZ=0
    g3: Circle CenterX=-34.575 CenterY=34.575 CenterZ=0 NormalX=0 NormalY=0 NormalZ=1 AngleXU=0 Radius=5.4
    g4: Circle CenterX=-34.575 CenterY=-34.575 CenterZ=0 NormalX=0 NormalY=0 NormalZ=1 AngleXU=0 Radius=5.4
    g5: Circle CenterX=34.575 CenterY=-34.575 CenterZ=0 NormalX=0 NormalY=0 NormalZ=1 AngleXU=0 Radius=5.4
  constraints (15):
    c: Coincident(g1,g0)
    c: PointOnObject(g1,g-1)
    c: Vertical(g1)
    c: Coincident(g2,g0)
    c: PointOnObject(g2,g-2)
    c: Horizontal(g2)
    c: Equal(g1,g2)
    c: DistanceY(g1,g1) = 34.575
    c: Diameter(g0) = 10.8
    c: Symmetric(g5,g0,g-1)
    c: Symmetric(g3,g0,g-2)
    c: Symmetric(g0,g4,g-1)
    c: Equal(g0,g5)
    c: Equal(g5,g4)
    c: Equal(g4,g3)
FEATURE [Sketcher::SketchObject] Sketch003  label="bottom_center_hole"
  ArcFitTolerance = 0
  FullyConstrained = true
  MakeInternals = false
  sketch-geometry (1):
    g0: Circle CenterX=0 CenterY=0 CenterZ=0 NormalX=0 NormalY=0 NormalZ=1 AngleXU=0 Radius=30.2
  constraints (2):
    c: Coincident(g0,g-1)
    c: Diameter(g0) = 60.4
FEATURE [PartDesign::AdditiveCylinder] Cylinder
  Angle = 360
  AttacherType = Attacher::AttachEngine3D
  AttachmentSupport = -> [XY_Plane]
  FirstAngle = 0
  Height = 67
  MapMode = 5
  Radius = 58
  SecondAngle = 0
  Suppressed = false
FEATURE [PartDesign::CoordinateSystem] Local_CS  label="bottom"
  AttacherType = Attacher::AttachEngine3D
  AttachmentSupport = -> [XY_Plane]
  MapMode = 5
FEATURE [PartDesign::CoordinateSystem] Local_CS001  label="top"
  AttacherType = Attacher::AttachEngine3D
  AttachmentOffset = pos=(0,0,67) rot=(0,0,1;0rad)
  AttachmentSupport = -> [XY_Plane]
  MapMode = 5
  Placement = pos=(0,0,67) rot=(0,0,1;0rad)
  expr: .AttachmentOffset.Base.z = Cylinder.Height
FEATURE [Sketcher::SketchObject] Sketch004
  ArcFitTolerance = 0
  AttachmentSupport = -> [XY_Plane]
  FullyConstrained = false
  MakeInternals = false
  MapMode = 5
  sketch-geometry (1):
    g0: Circle CenterX=0 CenterY=-2.41744 CenterZ=0 NormalX=0 NormalY=0 NormalZ=1 AngleXU=0 Radius=27.7935
  constraints (1):
    c: PointOnObject(g0,g-2)
FEATURE [PartDesign::Body] Body  label="hub2108"
  AllowCompound = false
  Group = -> [Cylinder,Local_CS,Local_CS001,Sketch004]
  Origin = -> Origin
  Tip = -> Cylinder
---- part module.FCStd = doc fcstd_3955753b3a20 ----
FCSTD DOCUMENT  (FreeCAD 1.1R38827 (Git))
Label: module
License: All rights reserved
LicenseURL: http://en.wikipedia.org/wiki/All_rights_reserved
objects: Sketcher::SketchObject×2, Part::Feature×1, PartDesign::FeatureBase×1, PartDesign::Body×1, Spreadsheet::Sheet×1
note: 8 computed .brp shape members not serialized (recipe doc carries the construction recipe); baked Part::Feature solids carry a one-line shape summary decoded from their .brp

FEATURE [Part::Feature] Part__Feature  label="module002"
  shape: bbox 170 x 148 x 41.12 mm, 715 faces (baked)
FEATURE [Sketcher::SketchObject] Sketch  label="module_holes"
  ArcFitTolerance = 0
  FullyConstrained = true
  MakeInternals = false
  sketch-geometry (10):
    g0: LineSegment StartX=59.5 StartY=-3.5 StartZ=0 EndX=59.5 EndY=3.5 EndZ=0
    g1: LineSegment StartX=59.5 StartY=3.5 StartZ=0 EndX=72.5 EndY=3.5 EndZ=0
    g2: LineSegment StartX=72.5 StartY=3.5 StartZ=0 EndX=72.5 EndY=-3.5 EndZ=0
    g3: LineSegment StartX=72.5 StartY=-3.5 StartZ=0 EndX=59.5 EndY=-3.5 EndZ=0
    g4: GeomPoint [constr] X=66 Y=0 Z=0
    g5: LineSegment StartX=-72.5 StartY=-3.5 StartZ=0 EndX=-72.5 EndY=3.5 EndZ=0
    g6: LineSegment StartX=-72.5 StartY=3.5 StartZ=0 EndX=-59.5 EndY=3.5 EndZ=0
    g7: LineSegment StartX=-59.5 StartY=3.5 StartZ=0 EndX=-59.5 EndY=-3.5 EndZ=0
    g8: LineSegment StartX=-59.5 StartY=-3.5 StartZ=0 EndX=-72.5 EndY=-3.5 EndZ=0
    g9: GeomPoint [constr] X=-66 Y=0 Z=0
  constraints (25):
    c: Coincident(g0,g1)
    c: Coincident(g1,g2)
    c: Coincident(g2,g3)
    c: Coincident(g3,g0)
    c: Horizontal(g1)
    c: Horizontal(g3)
    c: Vertical(g0)
    c: Vertical(g2)
    c: Symmetric(g1,g0,g4)
    c: PointOnObject(g4,g-1)
    c: Coincident(g5,g6)
    c: Coincident(g6,g7)
    c: Coincident(g7,g8)
    c: Coincident(g8,g5)
    c: Horizontal(g6)
    c: Horizontal(g8)
    c: Vertical(g5)
    c: Vertical(g7)
    c: Symmetric(g6,g5,g9)
    c: Symmetric(g9,g4,g-2)
    c: Equal(g1,g6)
    c: Equal(g7,g2)
    c: DistanceX(g1,g1) = 13
    c: DistanceY(g2,g2) = 7
    c: DistanceX(g9,g4) = 132
FEATURE [PartDesign::FeatureBase] BaseFeature
  BaseFeature = -> Part__Feature
  Placement = pos=(0,0,0) rot=(0,0,1;1.5708rad)
  Suppressed = false
FEATURE [PartDesign::Body] Body  label="module_Body"
  AllowCompound = false
  BaseFeature = -> Part__Feature
  Group = -> [BaseFeature]
  Origin = -> Origin
  Tip = -> BaseFeature
FEATURE [Spreadsheet::Sheet] Spreadsheet  label="Properties"
  cells = B2(module_width)==148 mm; C2(module_height)==160 mm; D2(module_fixture_distance_x)==132 mm; E2(module_fixture_distance_y)==80 mm; F2(module_hole_x)==13 mm; G2(module_hole_y)==7 mm
FEATURE [Sketcher::SketchObject] Sketch001  label="module_holes001"
  ArcFitTolerance = 0
  FullyConstrained = true
  MakeInternals = false
  sketch-geometry (10):
    g0: LineSegment StartX=59 StartY=-3.5 StartZ=0 EndX=59 EndY=3.5 EndZ=0
    g1: LineSegment StartX=59 StartY=3.5 StartZ=0 EndX=73 EndY=3.5 EndZ=0
    g2: LineSegment StartX=73 StartY=3.5 StartZ=0 EndX=73 EndY=-3.5 EndZ=0
    g3: LineSegment StartX=73 StartY=-3.5 StartZ=0 EndX=59 EndY=-3.5 EndZ=0
    g4: GeomPoint [constr] X=66 Y=0 Z=0
    g5: LineSegment StartX=-73 StartY=-3.5 StartZ=0 EndX=-73 EndY=3.5 EndZ=0
    g6: LineSegment StartX=-73 StartY=3.5 StartZ=0 EndX=-59 EndY=3.5 EndZ=0
    g7: LineSegment StartX=-59 StartY=3.5 StartZ=0 EndX=-59 EndY=-3.5 EndZ=0
    g8: LineSegment StartX=-59 StartY=-3.5 StartZ=0 EndX=-73 EndY=-3.5 EndZ=0
    g9: GeomPoint [constr] X=-66 Y=0 Z=0
  constraints (25):
    c: Coincident(g0,g1)
    c: Coincident(g1,g2)
    c: Coincident(g2,g3)
    c: Coincident(g3,g0)
    c: Horizontal(g1)
    c: Horizontal(g3)
    c: Vertical(g0)
    c: Vertical(g2)
    c: Symmetric(g1,g0,g4)
    c: PointOnObject(g4,g-1)
    c: Coincident(g5,g6)
    c: Coincident(g6,g7)
    c: Coincident(g7,g8)
    c: Coincident(g8,g5)
    c: Horizontal(g6)
    c: Horizontal(g8)
    c: Vertical(g5)
    c: Vertical(g7)
    c: Symmetric(g6,g5,g9)
    c: Symmetric(g9,g4,g-2)
    c: Equal(g1,g6)
    c: Equal(g7,g2)
    c: DistanceX(g1,g1) = 14
    c: DistanceY(g2,g2) = 7
    c: DistanceX(g9,g4) = 132
---- part socket_fixture.FCStd = doc fcstd_b5b55a086a53 ----
FCSTD DOCUMENT  (FreeCAD 1.1R38827 (Git))
Label: socket_fixture
License: All rights reserved
LicenseURL: http://en.wikipedia.org/wiki/All_rights_reserved
objects: Sketcher::SketchObject×5, PartDesign::Pocket×4, PartDesign::FeaturePython×2, Part::FeaturePython×1, PartDesign::Body×1, Part::Feature×1
note: 29 computed .brp shape members not serialized (recipe doc carries the construction recipe); baked Part::Feature solids carry a one-line shape summary decoded from their .brp
EXTERNAL_REF file=composit-properties.FCStd obj=Spreadsheet

FEATURE [Sketcher::SketchObject] Sketch
  ArcFitTolerance = 0
  AttachmentSupport = -> [XY_Plane]
  FullyConstrained = true
  MakeInternals = false
  MapMode = 5
  sketch-geometry (5):
    g0: LineSegment StartX=-19 StartY=20 StartZ=0 EndX=-19 EndY=0 EndZ=0
    g1: LineSegment StartX=-19 StartY=0 StartZ=0 EndX=19 EndY=0 EndZ=0
    g2: LineSegment StartX=19 StartY=0 StartZ=0 EndX=19 EndY=20 EndZ=0
    g3: LineSegment [constr] StartX=19 StartY=20 StartZ=0 EndX=-19 EndY=20 EndZ=0
    g4: GeomPoint [constr] X=0 Y=10 Z=0
  constraints (13):
    c: Coincident(g0,g1)
    c: Coincident(g1,g2)
    c: Coincident(g2,g3)
    c: Coincident(g3,g0)
    c: Horizontal(g1)
    c: Horizontal(g3)
    c: Vertical(g0)
    c: Vertical(g2)
    c: Symmetric(g1,g0,g4)
    c: PointOnObject(g4,g-2)
    c: PointOnObject(g1,g-1)
    c: DistanceX(g1,g1) = 38  'width'
    c: DistanceY(g2,g2) = 20  'length'
FEATURE [PartDesign::FeaturePython] BaseBend  # WARN: FeaturePython — macro-defined, semantics opaque (R4)
  BendSide = 1
  BendSketch = -> Sketch
  MidPlane = false
  Reverse = false
  Suppressed = false
  length = 67
  radius = 0.1
  thickness = 0.3
  expr: radius = composit_properties#<<Properties>>.bend_r
  expr: thickness = composit_properties#<<Properties>>.al_thickness
FEATURE [Sketcher::SketchObject] Sketch001
  ArcFitTolerance = 0
  AttachmentSupport = -> [YZ_Plane]
  FullyConstrained = true
  MakeInternals = false
  MapMode = 5
  Placement = pos=(0,0,0) rot=(0.57735,0.57735,0.57735;2.0944rad)
  expr: Constraints[11] = <<composit-properties>>#<<Properties>>.bend_r + <<composit-properties>>#<<Properties>>.al_thickness
  expr: Constraints[7] = <<composit-properties>>#<<Properties>>.thickness
  expr: Constraints[8] = <<composit-properties>>#<<Properties>>.bend_r + <<composit-properties>>#<<Properties>>.al_thickness
  sketch-geometry (4):
    g0: LineSegment StartX=0.4 StartY=0 StartZ=0 EndX=3 EndY=0 EndZ=0
    g1: LineSegment StartX=3 StartY=0 StartZ=0 EndX=3 EndY=0.4 EndZ=0
    g2: LineSegment StartX=3 StartY=0.4 StartZ=0 EndX=0.4 EndY=0.4 EndZ=0
    g3: LineSegment StartX=0.4 StartY=0.4 StartZ=0 EndX=0.4 EndY=0 EndZ=0
  constraints (12):
    c: Coincident(g0,g1)
    c: Coincident(g1,g2)
    c: Coincident(g2,g3)
    c: Horizontal(g0)
    c: Horizontal(g2)
    c: Vertical(g1)
    c: Vertical(g3)
    c: DistanceX(g1) = 3
    c: DistanceY(g1) = 0.4
    c: Coincident(g0,g3)
    c: PointOnObject(g0,g-1)
    c: DistanceX(g0) = 0.4
FEATURE [PartDesign::FeaturePython] Bend  # WARN: FeaturePython — macro-defined, semantics opaque (R4)
  AutoMiter = true
  BaseFeature = -> BaseBend
  BendType = 1
  LengthList = [14]
  LengthSpec = 1
  ReliefFactor = 0.7
  Suppressed = false
  UseReliefFactor = false
  angle = 90
  baseObject = -> BaseBend [Edge11,Edge42]
  bendAList = [90]
  extend1 = 0
  extend2 = 0
  gap1 = 0
  gap2 = 0
  invert = false
  kfactor = 0.5
  length = 14
  maxExtendDist = 5
  minGap = 0.1
  minReliefGap = 1
  miterangle1 = 0
  miterangle2 = 0
  offset = 0
  radius = 0.1
  reliefType = 0
  reliefd = 1
  reliefw = 0.8
  sketchflip = false
  sketchinvert = false
  unfold = false
  expr: length = Sketch.Constraints.width / 2 - 5 mm
  expr: radius = BaseBend.radius
FEATURE [PartDesign::Pocket] Pocket
  BaseFeature = -> Bend
  Direction = (-1,2e-16,-3e-16)
  Length = 5
  Length2 = 5
  Midplane = true
  Profile = -> Sketch001
  ReferenceAxis = -> Sketch001 [N_Axis]
  Suppressed = false
  Type = 1
FEATURE [Sketcher::SketchObject] Sketch002
  ArcFitTolerance = 0
  AttachmentSupport = -> [YZ_Plane]
  FullyConstrained = true
  MakeInternals = false
  MapMode = 5
  Placement = pos=(0,0,0) rot=(0.57735,0.57735,0.57735;2.0944rad)
  expr: Constraints[10] = BaseBend.length
  expr: Constraints[11] = Sketch.Constraints.length
  expr: Constraints[12] = <<composit-properties>>#<<Properties>>.thickness
  sketch-geometry (5):
    g0: LineSegment StartX=0 StartY=0 StartZ=0 EndX=20 EndY=0 EndZ=0
    g1: LineSegment StartX=20 StartY=0 StartZ=0 EndX=20 EndY=3 EndZ=0
    g2: LineSegment StartX=20 StartY=3 StartZ=0 EndX=3 EndY=67 EndZ=0
    g3: LineSegment StartX=3 StartY=67 StartZ=0 EndX=0 EndY=67 EndZ=0
    g4: LineSegment StartX=0 StartY=67 StartZ=0 EndX=0 EndY=0 EndZ=0
  constraints (14):
    c: Coincident(g-1,g0)
    c: PointOnObject(g0,g-1)
    c: Coincident(g0,g1)
    c: Vertical(g1)
    c: Coincident(g1,g2)
    c: Coincident(g2,g3)
    c: PointOnObject(g3,g-2)
    c: Horizontal(g3)
    c: Coincident(g3,g4)
    c: Coincident(g4,g0)
    c: DistanceY(g3) = 67
    c: DistanceX(g0,g0) = 20
    c: DistanceY(g1,g1) = 3
    c: Equal(g3,g1)
FEATURE [Part::FeaturePython] WireFilter  # WARN: FeaturePython — macro-defined, semantics opaque (R4)
  AttacherType = Attacher::AttachEngine3D
  ClaimChildren = true
  ColorKeyCount = 8
  Colorize = true
  FaceMaker = 5
  FixNormal = false
  FollowSource = true
  InvertedFaceScale = 5
  MaxWires = 25
  Normal = (1,-3e-16,2e-16)
  OffsetFill = false
  OffsetIntersection = false
  OffsetJoin = 0
  OffsetOpenResult = false
  Scale = (1,1,1)
  SelectEdges = false
  Source = -> Sketch002
  UniformScale = 1
  UseDefault = false
  UseSelected = true
  UseSelectedEdges = false
  Version = 0.2022.02.09
  WireOrder = [1]
FEATURE [PartDesign::Pocket] Pocket001
  BaseFeature = -> Pocket
  Direction = (-1,3e-16,-2e-16)
  Length = 5
  Length2 = 5
  Midplane = true
  Profile = -> WireFilter
  Suppressed = false
  Type = 1
FEATURE [Sketcher::SketchObject] Sketch003  label="fix_holes"
  ArcFitTolerance = 0
  AttachmentSupport = -> [XY_Plane]
  FullyConstrained = true
  MakeInternals = false
  MapMode = 5
  expr: Constraints[1] = 3.4
  sketch-geometry (2):
    g0: Circle CenterX=-10 CenterY=15 CenterZ=0 NormalX=0 NormalY=0 NormalZ=1 AngleXU=0 Radius=1.7
    g1: Circle CenterX=10 CenterY=15 CenterZ=0 NormalX=0 NormalY=0 NormalZ=1 AngleXU=0 Radius=1.7
  constraints (5):
    c: Equal(g1,g0)
    c: Diameter(g1) = 3.4
    c: Symmetric(g0,g1,g-2)
    c: DistanceX(g0,g1) = 20
    c: DistanceY(g1) = 15
FEATURE [PartDesign::Pocket] Pocket002
  BaseFeature = -> Pocket001
  Direction = (0,0,-1)
  Length = 5
  Length2 = 5
  Midplane = true
  Profile = -> Sketch003
  ReferenceAxis = -> Sketch003 [N_Axis]
  Suppressed = false
  Type = 1
FEATURE [Sketcher::SketchObject] Sketch004
  ArcFitTolerance = 0
  AttachmentSupport = -> [XZ_Plane]
  FullyConstrained = true
  MakeInternals = false
  MapMode = 5
  Placement = pos=(0,0,0) rot=(1,0,0;1.5708rad)
  sketch-geometry (2):
    g0: Circle CenterX=0 CenterY=18 CenterZ=0 NormalX=0 NormalY=0 NormalZ=1 AngleXU=0 Radius=2.5
    g1: Circle CenterX=0 CenterY=55 CenterZ=0 NormalX=0 NormalY=0 NormalZ=1 AngleXU=0 Radius=2.5
  constraints (6):
    c: PointOnObject(g0,g-2)
    c: PointOnObject(g1,g-2)
    c: Equal(g0,g1)
    c: Diameter(g0) = 5
    c: DistanceY(g0) = 18
    c: DistanceY(g1) = 55
FEATURE [PartDesign::Pocket] Pocket003
  BaseFeature = -> Pocket002
  Direction = (0,1,2e-16)
  Length = 5
  Length2 = 5
  Midplane = true
  Profile = -> Sketch004
  ReferenceAxis = -> Sketch004 [N_Axis]
  Suppressed = false
  Type = 1
FEATURE [PartDesign::Body] Body  label="Body_material_0.45ansi"
  AllowCompound = false
  Group = -> [Sketch,BaseBend,Sketch001,Bend,Pocket,Sketch002,WireFilter,Pocket001,Sketch003,Pocket002,Sketch004,Pocket003]
  Origin = -> Origin
  Tip = -> Pocket003
FEATURE [Part::Feature] Unfold034  label="socket_fixture_unfold"
  Placement = pos=(0,0,-3) rot=(0.5774,0.5774,0.5774;0rad)
  shape: bbox 77.8 x 0.3 x 85.8 mm, 24 faces (baked)
